FCSTD DOCUMENT  (FreeCAD 0.21R33771 (Git))
Label: Expeditioner Model
License: All rights reserved
LicenseURL: http://en.wikipedia.org/wiki/All_rights_reserved
objects: Part::Feature×562, Sketcher::SketchObject×231, App::Part×178, TechDraw::DrawViewDimension×156, PartDesign::Pocket×103, PartDesign::Fillet×78, Part::Extrusion×48, PartDesign::Body×41, App::MeasureDistance×31, PartDesign::Hole×30, TechDraw::DrawViewBalloon×28, PartDesign::Pad×27, PartDesign::FeatureBase×16, TechDraw::DrawViewAnnotation×14, TechDraw::DrawViewPart×11, Mesh::Feature×7, PartDesign::Chamfer×5, TechDraw::DrawSVGTemplate×5, TechDraw::DrawPage×5, App::FeaturePython×1, +5 more types
note: 1624 computed .brp shape members not serialized (recipe doc carries the construction recipe); baked Part::Feature solids carry a one-line shape summary decoded from their .brp

FEATURE [App::FeaturePython] Marz_Files  # WARN: FeaturePython — macro-defined, semantics opaque (R4)
FEATURE [Sketcher::SketchObject] Sketch  label="blank template"
  FullyConstrained = false
  MapMode = 5
  Support = -> [XY_Plane]
  sketch-geometry (4):
    g0: LineSegment StartX=0 StartY=615 StartZ=0 EndX=450 EndY=615 EndZ=0
    g1: LineSegment StartX=450 StartY=615 StartZ=0 EndX=450 EndY=15 EndZ=0
    g2: LineSegment StartX=450 StartY=15 StartZ=0 EndX=0 EndY=15 EndZ=0
    g3: LineSegment StartX=0 StartY=15 StartZ=0 EndX=0 EndY=615 EndZ=0
  constraints (10):
    c: Coincident(g0,g1)
    c: Coincident(g1,g2)
    c: Coincident(g2,g3)
    c: Coincident(g3,g0)
    c: Horizontal(g0)
    c: Horizontal(g2)
    c: Vertical(g1)
    c: Vertical(g3)
    c: DistanceX(g2,g2) = 450
    c: DistanceY(g1,g1) = 600
FEATURE [Image::ImagePlane] Screenshot_2024_10_02_125832  label="bettie schem"
  Placement = pos=(-143.3,315.1,0) rot=(0,0,1;1.5708rad)
  XSize = 165.652
  YSize = 124.636
FEATURE [Sketcher::SketchObject] Sketch011  label="bettie measurements"
  FullyConstrained = false
  MapMode = 5
  Support = -> [XY_Plane]
  sketch-geometry (52):
    g0: LineSegment StartX=45 StartY=-146.5 StartZ=0 EndX=35.3685 EndY=-167.589 EndZ=0
    g1: LineSegment StartX=35.3685 StartY=-167.589 StartZ=0 EndX=34.2637 EndY=-168.593 EndZ=0
    g2: LineSegment StartX=34.2637 StartY=-168.593 StartZ=0 EndX=33 EndY=-169.396 EndZ=0
    g3: LineSegment StartX=33 StartY=-169.396 StartZ=0 EndX=31.6649 EndY=-169.786 EndZ=0
    g4: LineSegment StartX=31.6649 StartY=-169.786 StartZ=0 EndX=29 EndY=-169.786 EndZ=0
    g5: LineSegment StartX=29 StartY=-169.786 StartZ=0 EndX=1.8 EndY=-159.5 EndZ=0
    g6: LineSegment StartX=1.8 StartY=-159.5 StartZ=0 EndX=-1.2 EndY=-159.5 EndZ=0
    g7: LineSegment StartX=-1.2 StartY=-159.5 StartZ=0 EndX=-69 EndY=-185.428 EndZ=0
    g8: LineSegment StartX=-69 StartY=-185.428 StartZ=0 EndX=-70.8 EndY=-185.428 EndZ=0
    g9: LineSegment StartX=-70.8 StartY=-185.428 StartZ=0 EndX=-71.8 EndY=-184.767 EndZ=0
    g10: LineSegment StartX=-71.8 StartY=-184.767 StartZ=0 EndX=-72.4211 EndY=-184 EndZ=0
    g11: LineSegment StartX=-72.4211 StartY=-184 StartZ=0 EndX=-72.8 EndY=-183.2 EndZ=0
    g12: LineSegment StartX=-72.8 StartY=-183.2 StartZ=0 EndX=-72.8555 EndY=-183 EndZ=0
    g13: LineSegment StartX=-72.8555 StartY=-183 StartZ=0 EndX=-72.8555 EndY=-181.7 EndZ=0
    g14: LineSegment StartX=-72.8555 StartY=-181.7 StartZ=0 EndX=-67.6345 EndY=-163 EndZ=0
    g15: LineSegment StartX=-67.6345 StartY=-163 StartZ=0 EndX=-64.5009 EndY=-153.288 EndZ=0
    g16: LineSegment StartX=-64.5009 StartY=-153.288 StartZ=0 EndX=-61.7538 EndY=-145.228 EndZ=0
    g17: LineSegment StartX=-61.7538 StartY=-145.228 StartZ=0 EndX=-59.2797 EndY=-138.257 EndZ=0
    g18: LineSegment StartX=-59.2797 StartY=-138.257 StartZ=0 EndX=-57.2993 EndY=-133 EndZ=0
    g19: LineSegment StartX=-57.2993 StartY=-133 StartZ=0 EndX=-54.706 EndY=-126.347 EndZ=0
    g20: LineSegment StartX=-54.706 StartY=-126.347 StartZ=0 EndX=-52.2652 EndY=-120.606 EndZ=0
    g21: LineSegment StartX=-52.2652 StartY=-120.606 StartZ=0 EndX=-48.3212 EndY=-111.536 EndZ=0
    g22: LineSegment StartX=-48.3212 StartY=-111.536 StartZ=0 EndX=-45 EndY=-104.429 EndZ=0
    g23: LineSegment StartX=-45 StartY=-104.429 StartZ=0 EndX=-42 EndY=-98 EndZ=0
    g24: LineSegment StartX=-42 StartY=-98 StartZ=0 EndX=-40.3107 EndY=-94.759 EndZ=0
    g25: LineSegment StartX=-40.3107 StartY=-94.759 StartZ=0 EndX=-39.498 EndY=-93.793 EndZ=0
    g26: LineSegment StartX=-39.498 StartY=-93.793 StartZ=0 EndX=-38.7466 EndY=-93.2563 EndZ=0
    g27: LineSegment StartX=-38.7466 StartY=-93.2563 StartZ=0 EndX=-38 EndY=-93 EndZ=0
    g28: LineSegment StartX=-38 StartY=-93 StartZ=0 EndX=-37 EndY=-93 EndZ=0
    g29: LineSegment StartX=-37 StartY=-93 StartZ=0 EndX=-36.528 EndY=-93 EndZ=0
    g30: LineSegment StartX=-36.528 StartY=-93 StartZ=0 EndX=3.99999 EndY=-118.6 EndZ=0
    g31: LineSegment StartX=3.99999 StartY=-118.6 StartZ=0 EndX=4.79999 EndY=-119 EndZ=0
    g32: LineSegment StartX=4.79999 StartY=-119 StartZ=0 EndX=7.79999 EndY=-119 EndZ=0
    g33: LineSegment StartX=7.79999 StartY=-119 StartZ=0 EndX=13.4 EndY=-117.1 EndZ=0
    g34: LineSegment StartX=13.4 StartY=-117.1 StartZ=0 EndX=18 EndY=-115.5 EndZ=0
    g35: LineSegment StartX=18 StartY=-115.5 StartZ=0 EndX=61 EndY=-100.8 EndZ=0
    g36: LineSegment StartX=61 StartY=-100.8 StartZ=0 EndX=62.5 EndY=-100.8 EndZ=0
    g37: LineSegment StartX=62.5 StartY=-100.8 StartZ=0 EndX=63 EndY=-101.2 EndZ=0
    g38: LineSegment StartX=63 StartY=-101.2 StartZ=0 EndX=63.5 EndY=-101.7 EndZ=0
    g39: LineSegment StartX=63.5 StartY=-101.7 StartZ=0 EndX=63.8 EndY=-102.1 EndZ=0
    g40: LineSegment StartX=63.8 StartY=-102.1 StartZ=0 EndX=63.9 EndY=-102.3 EndZ=0
    g41: LineSegment StartX=63.9 StartY=-102.3 StartZ=0 EndX=63.9 EndY=-104 EndZ=0
    g42: LineSegment StartX=63.9 StartY=-104 StartZ=0 EndX=52.7 EndY=-129 EndZ=0
    g43: LineSegment StartX=52.7 StartY=-129 StartZ=0 EndX=52.5574 EndY=-129.3 EndZ=0
    g44: LineSegment StartX=52.5574 StartY=-129.3 StartZ=0 EndX=52.5574 EndY=-130.5 EndZ=0
    g45: LineSegment StartX=52.5574 StartY=-130.5 StartZ=0 EndX=53.4 EndY=-131.7 EndZ=0
    g46: LineSegment StartX=53.4 StartY=-131.7 StartZ=0 EndX=54 EndY=-132 EndZ=0
    g47: LineSegment StartX=54 StartY=-132 StartZ=0 EndX=54 EndY=-146.5 EndZ=0
    g48: LineSegment StartX=54 StartY=-146.5 StartZ=0 EndX=45 EndY=-146.5 EndZ=0
    g49: LineSegment StartX=63.9 StartY=-104 StartZ=0 EndX=63.9 EndY=-129 EndZ=0
    g50: LineSegment StartX=-40.3107 StartY=-94.759 StartZ=0 EndX=-41 EndY=-94 EndZ=0
    g51: LineSegment StartX=-70.8 StartY=-185.428 StartZ=0 EndX=-70.8 EndY=-187 EndZ=0
  constraints (116):
    c: Coincident(g0,g1)
    c: Coincident(g1,g2)
    c: Coincident(g2,g3)
    c: Coincident(g3,g4)
    c: Horizontal(g4)
    c: Coincident(g4,g5)
    c: Coincident(g5,g6)
    c: Horizontal(g6)
    c: Coincident(g6,g7)
    c: Coincident(g7,g8)
    c: Horizontal(g8)
    c: Coincident(g8,g9)
    c: Coincident(g9,g10)
    c: Coincident(g10,g11)
    c: Coincident(g11,g12)
    c: Coincident(g12,g13)
    c: Vertical(g13)
    c: Coincident(g13,g14)
    c: Coincident(g14,g15)
    c: Coincident(g15,g16)
    c: Coincident(g16,g17)
    c: Coincident(g17,g18)
    c: Coincident(g18,g19)
    c: Coincident(g19,g20)
    c: Coincident(g20,g21)
    c: Coincident(g21,g22)
    c: Coincident(g22,g23)
    c: Coincident(g23,g24)
    c: Coincident(g24,g25)
    c: Coincident(g25,g26)
    c: Coincident(g26,g27)
    c: Coincident(g27,g28)
    c: Horizontal(g28)
    c: Coincident(g28,g29)
    c: Horizontal(g29)
    c: Coincident(g29,g30)
    c: Coincident(g30,g31)
    c: Coincident(g31,g32)
    c: Horizontal(g32)
    c: Coincident(g32,g33)
    c: Coincident(g33,g34)
    c: Coincident(g34,g35)
    c: Coincident(g35,g36)
    c: Horizontal(g36)
    c: Coincident(g36,g37)
    c: Coincident(g37,g38)
    c: Coincident(g38,g39)
    c: Coincident(g39,g40)
    c: Coincident(g40,g41)
    c: Vertical(g41)
    c: Coincident(g41,g42)
    c: Coincident(g42,g43)
    c: Coincident(g43,g44)
    c: Vertical(g44)
    c: Coincident(g44,g45)
    c: Coincident(g45,g46)
    c: Coincident(g46,g47)
    c: Vertical(g47)
    c: Coincident(g47,g48)
    c: Coincident(g48,g0)
    c: Horizontal(g48)
    c: Distance(g0) = 23.184
    c: Distance(g42) = 27.3942
    c: Distance(g43) = 0.33218
    c: Distance(g44) = 1.2
    c: Distance(g45) = 1.4663
    c: Distance(g46) = 0.67082
    c: Distance(g47) = 14.5
    c: Distance(g48) = 9
    c: Distance(g1) = 1.49309
    c: Distance(g2) = 1.49749
    c: Distance(g3) = 1.39068
    c: Distance(g4) = 2.6649
    c: Distance(g5) = 29.0798
    c: Distance(g6) = 3
    c: Distance(g7) = 72.5885
    c: Distance(g8) = 1.8
    c: Distance(g9) = 1.19864
    c: Distance(g10) = 0.98682
    c: Distance(g11) = 0.88518
    c: Distance(g12) = 0.20755
    c: Distance(g13) = 1.3
    c: Distance(g14) = 19.4152
    c: Distance(g15) = 10.2052
    c: Distance(g16) = 8.51506
    c: Distance(g17) = 7.39698
    c: Distance(g18) = 5.61771
    c: Distance(g19) = 7.14023
    c: Distance(g20) = 6.23864
    c: Distance(g21) = 9.89066
    c: Distance(g22) = 7.84408
    c: Distance(g23) = 7.09491
    c: Distance(g24) = 3.65484
    c: Distance(g25) = 1.26244
    c: Distance(g26) = 0.92337
    c: Distance(g27) = 0.78933
    c: Distance(g28) = 1
    c: Distance(g29) = 0.47203
    c: Distance(g30) = 47.9362
    c: Distance(g31) = 0.89443
    c: Distance(g32) = 3
    c: Distance(g33) = 5.91354
    c: Distance(g34) = 4.87032
    c: Distance(g35) = 45.4433
    c: Distance(g36) = 1.50001
    c: Distance(g37) = 0.64031
    c: Distance(g38) = 0.70711
    c: Distance(g39) = 0.5
    c: Distance(g40) = 0.22361
    c: Distance(g41) = 1.7
    c: Coincident(g49,g41)
    c: Vertical(g49)
    c: Coincident(g50,g24)
    c: Coincident(g51,g8)
    c: Vertical(g51)
    c: Angle(g8,g9) = 2.55763
FEATURE [PartDesign::Pad] Pad
  Direction = (0,0,1)
  Length = 45
  Length2 = 10
  Profile = -> Sketch
  ReferenceAxis = -> Sketch [N_Axis]
  Type = 0
FEATURE [Sketcher::SketchObject] Sketch002  label="pickup holes"
  FullyConstrained = false
  MapMode = 5
  Placement = pos=(0,0,45) rot=(0,0,1;0rad)
  Support = -> [Pad]
  sketch-geometry (28):
    g0: LineSegment StartX=225 StartY=601 StartZ=0 EndX=225 EndY=-1 EndZ=0
    g1: LineSegment StartX=182.5 StartY=460 StartZ=0 EndX=267.5 EndY=460 EndZ=0
    g2: LineSegment StartX=267.5 StartY=460 StartZ=0 EndX=267.5 EndY=441 EndZ=0
    g3: LineSegment StartX=267.5 StartY=441 StartZ=0 EndX=182.5 EndY=441 EndZ=0
    g4: LineSegment StartX=182.5 StartY=441 StartZ=0 EndX=182.5 EndY=460 EndZ=0
    g5: LineSegment StartX=182.5 StartY=400 StartZ=0 EndX=267.5 EndY=400 EndZ=0
    g6: LineSegment StartX=267.5 StartY=400 StartZ=0 EndX=267.5 EndY=381 EndZ=0
    g7: LineSegment StartX=267.5 StartY=381 StartZ=0 EndX=182.5 EndY=381 EndZ=0
    g8: LineSegment StartX=182.5 StartY=381 StartZ=0 EndX=182.5 EndY=400 EndZ=0
    g9: LineSegment StartX=188.75 StartY=357.8 StartZ=0 EndX=261.25 EndY=357.8 EndZ=0
    g10: LineSegment StartX=261.25 StartY=357.8 StartZ=0 EndX=261.25 EndY=347.8 EndZ=0
    g11: LineSegment StartX=261.25 StartY=347.8 StartZ=0 EndX=269.25 EndY=347.8 EndZ=0
    g12: LineSegment StartX=269.25 StartY=347.8 StartZ=0 EndX=269.25 EndY=327.8 EndZ=0
    g13: LineSegment StartX=269.25 StartY=327.8 StartZ=0 EndX=261.25 EndY=327.8 EndZ=0
    g14: LineSegment StartX=261.25 StartY=327.8 StartZ=0 EndX=261.25 EndY=317.8 EndZ=0
    g15: LineSegment StartX=261.25 StartY=317.8 StartZ=0 EndX=188.75 EndY=317.8 EndZ=0
    g16: LineSegment StartX=188.75 StartY=317.8 StartZ=0 EndX=188.75 EndY=327.8 EndZ=0
    g17: LineSegment StartX=188.75 StartY=327.8 StartZ=0 EndX=180.75 EndY=327.8 EndZ=0
    g18: LineSegment StartX=180.75 StartY=327.8 StartZ=0 EndX=180.75 EndY=347.8 EndZ=0
    g19: LineSegment StartX=180.75 StartY=347.8 StartZ=0 EndX=188.75 EndY=347.8 EndZ=0
    g20: LineSegment StartX=188.75 StartY=347.8 StartZ=0 EndX=188.75 EndY=357.8 EndZ=0
    g21: LineSegment StartX=182.5 StartY=460 StartZ=0 EndX=182.5 EndY=469.3 EndZ=0
    g22: LineSegment StartX=182.5 StartY=469.3 StartZ=0 EndX=210 EndY=469.3 EndZ=0
    g23: LineSegment StartX=182.5 StartY=441 StartZ=0 EndX=182.5 EndY=400 EndZ=0
    g24: LineSegment StartX=177 StartY=469.3 StartZ=0 EndX=177 EndY=357.8 EndZ=0
    g25: LineSegment StartX=177 StartY=357.8 StartZ=0 EndX=180.75 EndY=357.8 EndZ=0
    g26: LineSegment StartX=180.75 StartY=357.8 StartZ=0 EndX=188.75 EndY=357.8 EndZ=0
    g27: LineSegment StartX=261.25 StartY=357.8 StartZ=0 EndX=261.25 EndY=381 EndZ=0
  constraints (76):
    c: Vertical(g0)
    c: Coincident(g1,g2)
    c: Coincident(g2,g3)
    c: Coincident(g3,g4)
    c: Coincident(g4,g1)
    c: Horizontal(g1)
    c: Horizontal(g3)
    c: Vertical(g2)
    c: Vertical(g4)
    c: DistanceX(g1,g1) = 85
    c: DistanceY(g2,g2) = 19
    c: Coincident(g5,g6)
    c: Coincident(g6,g7)
    c: Coincident(g7,g8)
    c: Coincident(g8,g5)
    c: Horizontal(g5)
    c: Horizontal(g7)
    c: Vertical(g6)
    c: Vertical(g8)
    c: DistanceX(g5,g5) = 85
    c: DistanceY(g8,g8) = 19
    c: Horizontal(g9)
    c: Coincident(g9,g10)
    c: Vertical(g10)
    c: Coincident(g10,g11)
    c: Horizontal(g11)
    c: Coincident(g11,g12)
    c: Vertical(g12)
    c: Coincident(g12,g13)
    c: Horizontal(g13)
    c: Coincident(g13,g14)
    c: Vertical(g14)
    c: Coincident(g14,g15)
    c: Horizontal(g15)
    c: Coincident(g15,g16)
    c: Vertical(g16)
    c: Coincident(g16,g17)
    c: Horizontal(g17)
    c: Coincident(g17,g18)
    c: Vertical(g18)
    c: Coincident(g18,g19)
    c: Horizontal(g19)
    c: Coincident(g19,g20)
    c: Coincident(g20,g9)
    c: Vertical(g20)
    c: DistanceX(g9,g9) = 72.5
    c: DistanceY(g12,g12) = 20
    c: DistanceY(g10,g10) = 10
    c: DistanceY(g14,g14) = 10
    c: DistanceX(g19,g19) = 8
    c: DistanceX(g17,g17) = 8
    c: DistanceX(g13,g13) = 8
    c: DistanceY(g20,g20) = 10
    c: DistanceY(g16,g16) = 10
    c: DistanceX(g15,g15) = 72.5
    c: Coincident(g21,g1)
    c: Vertical(g21)
    c: DistanceY(g21,g21) = 9.3
    c: Coincident(g22,g21)
    c: Horizontal(g22)
    c: Coincident(g23,g3)
    c: Vertical(g23)
    c: DistanceY(g23,g23) = 41
    c: Vertical(g24)
    c: Coincident(g25,g24)
    c: Horizontal(g25)
    c: DistanceY(g24,g24) = 111.5
    c: Coincident(g26,g25)
    c: Coincident(g26,g9)
    c: Horizontal(g26)
    c: DistanceX(g26,g26) = 8
    c: DistanceX(g25,g25) = 3.74999
    c: Coincident(g27,g9)
    c: PointOnObject(g27,g7)
    c: Vertical(g27)
    c: DistanceY(g27,g27) = 23.2
FEATURE [Sketcher::SketchObject] Sketch003  label="tremelo pocket"
  FullyConstrained = false
  MapMode = 5
  Placement = pos=(0,0,45) rot=(0,0,1;0rad)
  Support = -> [Pad]
  sketch-geometry (11):
    g0: LineSegment StartX=225 StartY=610 StartZ=0 EndX=225 EndY=-10 EndZ=0
    g1: LineSegment StartX=182.5 StartY=460 StartZ=0 EndX=182.5 EndY=469.3 EndZ=0
    g2: LineSegment StartX=182.5 StartY=469.3 StartZ=0 EndX=182.5 EndY=481.3 EndZ=0
    g3: LineSegment StartX=178 StartY=481.3 StartZ=0 EndX=178 EndY=295.3 EndZ=0
    g4: LineSegment StartX=178 StartY=295.3 StartZ=0 EndX=178 EndY=282.3 EndZ=0
    g5: LineSegment StartX=224.9 StartY=282.4 StartZ=0 EndX=224.99 EndY=282.4 EndZ=0
    g6: LineSegment StartX=224.9 StartY=282.4 StartZ=0 EndX=189.9 EndY=282.4 EndZ=0
    g7: LineSegment StartX=189.9 StartY=282.3 StartZ=0 EndX=267.9 EndY=282.3 EndZ=0
    g8: LineSegment StartX=267.9 StartY=282.3 StartZ=0 EndX=267.9 EndY=263.3 EndZ=0
    g9: LineSegment StartX=267.9 StartY=263.3 StartZ=0 EndX=189.9 EndY=263.3 EndZ=0
    g10: LineSegment StartX=189.9 StartY=263.3 StartZ=0 EndX=189.9 EndY=282.3 EndZ=0
  constraints (26):
    c: Vertical(g0)
    c: Vertical(g1)
    c: Coincident(g2,g1)
    c: Vertical(g2)
    c: Vertical(g3)
    c: Coincident(g4,g3)
    c: Vertical(g4)
    c: DistanceY(g4,g4) = 13
    c: DistanceY(g3,g3) = 186
    c: DistanceY(g1,g1) = 9.3
    c: DistanceY(g2,g2) = 12
    c: Horizontal(g5)
    c: Coincident(g6,g5)
    c: Horizontal(g6)
    c: DistanceX(g6,g6) = 35
    c: DistanceX(g5,g5) = 0.08999
    c: Coincident(g7,g8)
    c: Coincident(g8,g9)
    c: Coincident(g9,g10)
    c: Coincident(g10,g7)
    c: Horizontal(g7)
    c: Horizontal(g9)
    c: Vertical(g8)
    c: Vertical(g10)
    c: DistanceX(g7,g7) = 78
    c: DistanceY(g10,g10) = 19
FEATURE [Sketcher::SketchObject] Sketch004  label="control pocket"
  FullyConstrained = false
  MapMode = 5
  Placement = pos=(0,0,45) rot=(0,0,1;0rad)
  Support = -> [Pad]
  sketch-geometry (11):
    g0: LineSegment StartX=330 StartY=250 StartZ=0 EndX=353.532 EndY=180 EndZ=0
    g1: LineSegment StartX=353.532 StartY=180 StartZ=0 EndX=290 EndY=180 EndZ=0
    g2: LineSegment StartX=290 StartY=180 StartZ=0 EndX=290 EndY=250 EndZ=0
    g3: LineSegment StartX=330 StartY=250 StartZ=0 EndX=290 EndY=250 EndZ=0
    g4: Circle CenterX=302 CenterY=230 CenterZ=0 NormalX=0 NormalY=0 NormalZ=1 AngleXU=0 Radius=8.5
    g5: Circle CenterX=302 CenterY=200 CenterZ=0 NormalX=0 NormalY=0 NormalZ=1 AngleXU=0 Radius=8.5
    g6: LineSegment StartX=316.216 StartY=240.298 StartZ=0 EndX=326.216 EndY=240.298 EndZ=0
    g7: LineSegment StartX=326.216 StartY=240.298 StartZ=0 EndX=341.048 EndY=194.647 EndZ=0
    g8: LineSegment StartX=341.048 StartY=194.647 StartZ=0 EndX=330.587 EndY=191.248 EndZ=0
    g9: LineSegment StartX=326.216 StartY=240.298 StartZ=0 EndX=315.754 EndY=236.898 EndZ=0
    g10: LineSegment StartX=315.754 StartY=236.898 StartZ=0 EndX=330.587 EndY=191.248 EndZ=0
  constraints (25):
    c: Coincident(g1,g0)
    c: Horizontal(g1)
    c: Coincident(g2,g1)
    c: Vertical(g2)
    c: Coincident(g3,g0)
    c: Coincident(g3,g2)
    c: Horizontal(g3)
    c: Distance(g0) = 73.8495
    c: DistanceX(g3,g3) = 40
    c: DistanceX(g1,g1) = 63.5319
    c: Diameter(g4) = 17
    c: Diameter(g5) = 17
    c: Horizontal(g6)
    c: Coincident(g7,g6)
    c: DistanceX(g6,g6) = 10
    c: Angle(g6,g7) = 1.88496
    c: Distance(g7) = 48
    c: Coincident(g8,g7)
    c: Angle(g7,g8) = 1.5708
    c: Distance(g8) = 11
    c: Coincident(g9,g7)
    c: Angle(g9,g7) = 1.5708
    c: Coincident(g10,g9)
    c: Coincident(g10,g8)
    c: Distance(g9) = 11
FEATURE [Sketcher::SketchObject] Sketch005  label="AFPI pocket"
  FullyConstrained = false
  MapMode = 5
  Placement = pos=(0,0,45) rot=(0,0,1;0rad)
  Support = -> [Pad]
  sketch-geometry (24):
    g0: LineSegment StartX=68 StartY=506.5 StartZ=0 EndX=160 EndY=506.5 EndZ=0
    g1: LineSegment StartX=160 StartY=506.5 StartZ=0 EndX=160 EndY=402.5 EndZ=0
    g2: LineSegment StartX=160 StartY=402.5 StartZ=0 EndX=68 EndY=402.5 EndZ=0
    g3: LineSegment StartX=68 StartY=402.5 StartZ=0 EndX=68 EndY=506.5 EndZ=0
    g4: LineSegment StartX=-192.181 StartY=581.522 StartZ=0 EndX=-181.31 EndY=478.092 EndZ=0
    g5: LineSegment StartX=-181.31 StartY=478.092 StartZ=0 EndX=-89.8139 EndY=487.709 EndZ=0
    g6: LineSegment StartX=-192.181 StartY=581.522 StartZ=0 EndX=-100.685 EndY=591.139 EndZ=0
    g7: LineSegment StartX=-100.685 StartY=591.139 StartZ=0 EndX=-89.8139 EndY=487.709 EndZ=0
    g8: LineSegment StartX=-192.181 StartY=581.522 StartZ=0 EndX=-192.181 EndY=481.522 EndZ=0
    g9: LineSegment StartX=175 StartY=400 StartZ=0 EndX=275 EndY=400 EndZ=0
    g10: LineSegment StartX=175 StartY=400 StartZ=0 EndX=175 EndY=490 EndZ=0
    g11: LineSegment StartX=175 StartY=400 StartZ=0 EndX=175 EndY=380 EndZ=0
    g12: LineSegment StartX=-89.8139 StartY=487.709 StartZ=0 EndX=-88.927 EndY=479.201 EndZ=0
    g13: LineSegment StartX=-181.31 StartY=478.092 StartZ=0 EndX=-180.433 EndY=469.628 EndZ=0
    g14: LineSegment StartX=-180.433 StartY=469.628 StartZ=0 EndX=-88.927 EndY=479.201 EndZ=0
    g15: LineSegment StartX=-192.181 StartY=581.522 StartZ=0 EndX=-193.082 EndY=590 EndZ=0
    g16: LineSegment StartX=-100.685 StartY=591.139 StartZ=0 EndX=-101.58 EndY=599.597 EndZ=0
    g17: LineSegment StartX=-101.58 StartY=599.597 StartZ=0 EndX=-193.082 EndY=590 EndZ=0
    g18: LineSegment StartX=68 StartY=506.5 StartZ=0 EndX=68 EndY=515 EndZ=0
    g19: LineSegment StartX=68 StartY=515 StartZ=0 EndX=160 EndY=515 EndZ=0
    g20: LineSegment StartX=160 StartY=515 StartZ=0 EndX=160 EndY=506.5 EndZ=0
    g21: LineSegment StartX=160 StartY=402.5 StartZ=0 EndX=160 EndY=393.9 EndZ=0
    g22: LineSegment StartX=160 StartY=393.9 StartZ=0 EndX=68 EndY=393.9 EndZ=0
    g23: LineSegment StartX=68 StartY=393.9 StartZ=0 EndX=68 EndY=402.5 EndZ=0
  constraints (60):
    c: Coincident(g0,g1)
    c: Coincident(g1,g2)
    c: Coincident(g2,g3)
    c: Coincident(g3,g0)
    c: Horizontal(g0)
    c: Horizontal(g2)
    c: Vertical(g1)
    c: Vertical(g3)
    c: DistanceY(g1,g1) = 104
    c: DistanceX(g0,g0) = 92
    c: Coincident(g4,g5)
    c: Coincident(g4,g6)
    c: Coincident(g6,g7)
    c: Coincident(g7,g5)
    c: Angle(g7,g5) = 1.5708
    c: Angle(g6,g7) = 1.5708
    c: Angle(g4,g6) = 1.5708
    c: Distance(g4) = 104
    c: Distance(g5) = 92
    c: Coincident(g8,g4)
    c: Vertical(g8)
    c: Angle(g8,g4) = 0.10472
    c: DistanceY(g8,g8) = 100
    c: Horizontal(g9)
    c: Coincident(g10,g9)
    c: Vertical(g10)
    c: Coincident(g11,g9)
    c: Vertical(g11)
    c: Coincident(g5,g12)
    c: Coincident(g4,g13)
    c: Coincident(g13,g14)
    c: Coincident(g14,g12)
    c: Distance(g12) = 8.5541
    c: Distance(g14) = 92.0049
    c: Distance(g13) = 8.50942
    c: Coincident(g4,g15)
    c: Coincident(g16,g6)
    c: Coincident(g17,g16)
    c: Coincident(g17,g15)
    c: Distance(g15) = 8.52543
    c: Distance(g17) = 92.0046
    c: Distance(g16) = 8.50507
    c: Angle(g17,g16) = 1.57171
    c: Angle(g12,g14) = 1.57116
    c: Coincident(g0,g18)
    c: Vertical(g18)
    c: Coincident(g18,g19)
    c: Horizontal(g19)
    c: Coincident(g19,g20)
    c: Coincident(g20,g0)
    c: Vertical(g20)
    c: Coincident(g1,g21)
    c: Vertical(g21)
    c: Coincident(g21,g22)
    c: Horizontal(g22)
    c: Coincident(g22,g23)
    c: Coincident(g23,g2)
    c: Vertical(g23)
    c: DistanceY(g23,g23) = 8.59999
    c: DistanceY(g18,g18) = 8.50001
FEATURE [Sketcher::SketchObject] Sketch007  label="RGB Board Pockets"
  FullyConstrained = false
  MapMode = 5
  Placement = pos=(0,0,45) rot=(0,0,1;0rad)
  Support = -> [Pad]
  sketch-geometry (12):
    g0: LineSegment StartX=220 StartY=282.3 StartZ=0 EndX=220 EndY=284.3 EndZ=0
    g1: LineSegment StartX=220 StartY=284.3 StartZ=0 EndX=220 EndY=382.3 EndZ=0
    g2: LineSegment StartX=183 StartY=427.9 StartZ=0 EndX=267 EndY=427.9 EndZ=0
    g3: LineSegment StartX=267 StartY=427.9 StartZ=0 EndX=267 EndY=412.9 EndZ=0
    g4: LineSegment StartX=267 StartY=412.9 StartZ=0 EndX=183 EndY=412.9 EndZ=0
    g5: LineSegment StartX=183 StartY=412.9 StartZ=0 EndX=183 EndY=427.9 EndZ=0
    g6: LineSegment StartX=182.5 StartY=460 StartZ=0 EndX=225 EndY=460 EndZ=0
    g7: LineSegment StartX=225 StartY=460 StartZ=0 EndX=225 EndY=244 EndZ=0
    g8: LineSegment StartX=267.5 StartY=441 StartZ=0 EndX=267.5 EndY=400 EndZ=0
    g9: LineSegment StartX=267 StartY=441 StartZ=0 EndX=267 EndY=420.4 EndZ=0
    g10: LineSegment StartX=263.999 StartY=441 StartZ=0 EndX=263.999 EndY=427.9 EndZ=0
    g11: LineSegment StartX=210 StartY=282.3 StartZ=0 EndX=210 EndY=302.3 EndZ=0
  constraints (21):
    c: Vertical(g0)
    c: Coincident(g1,g0)
    c: Vertical(g1)
    c: Coincident(g2,g3)
    c: Coincident(g3,g4)
    c: Coincident(g4,g5)
    c: Coincident(g5,g2)
    c: Horizontal(g2)
    c: Horizontal(g4)
    c: Vertical(g3)
    c: Vertical(g5)
    c: DistanceX(g2,g2) = 84
    c: DistanceY(g5,g5) = 15
    c: Horizontal(g6)
    c: Coincident(g7,g6)
    c: Vertical(g7)
    c: Vertical(g8)
    c: Vertical(g9)
    c: PointOnObject(g10,g2)
    c: Vertical(g10)
    c: Vertical(g11)
FEATURE [Sketcher::SketchObject] Sketch008  label="Speaker hole"
  FullyConstrained = false
  MapMode = 5
  Placement = pos=(0,0,45) rot=(0,0,1;0rad)
  Support = -> [Pad]
  sketch-geometry (3):
    g0: Circle CenterX=330 CenterY=121 CenterZ=0 NormalX=0 NormalY=0 NormalZ=1 AngleXU=0 Radius=37
    g1: LineSegment StartX=377 StartY=123.392 StartZ=0 EndX=283 EndY=123.392 EndZ=0
    g2: LineSegment StartX=377 StartY=123.4 StartZ=0 EndX=330 EndY=123.4 EndZ=0
  constraints (4):
    c: Diameter(g0) = 74
    c: Horizontal(g1)
    c: DistanceX(g1,g1) = 94
    c: Horizontal(g2)
FEATURE [Sketcher::SketchObject] Sketch009  label="control plate mount pocket"
  FullyConstrained = false
  MapMode = 5
  Placement = pos=(0,0,45) rot=(0,0,1;0rad)
  Support = -> [Pad]
  sketch-geometry (6):
    g0: LineSegment StartX=267.9 StartY=263.3 StartZ=0 EndX=267.9 EndY=243.3 EndZ=0
    g1: LineSegment StartX=267.9 StartY=243.3 StartZ=0 EndX=272.9 EndY=243.3 EndZ=0
    g2: LineSegment StartX=282 StartY=258 StartZ=0 EndX=337 EndY=258 EndZ=0
    g3: LineSegment StartX=282 StartY=258 StartZ=0 EndX=282 EndY=172 EndZ=0
    g4: LineSegment StartX=282 StartY=172 StartZ=0 EndX=365.925 EndY=172 EndZ=0
    g5: LineSegment StartX=365.925 StartY=172 StartZ=0 EndX=337 EndY=258 EndZ=0
  constraints (12):
    c: Vertical(g0)
    c: Coincident(g1,g0)
    c: Horizontal(g1)
    c: Horizontal(g2)
    c: Coincident(g3,g2)
    c: Vertical(g3)
    c: DistanceY(g3,g3) = 86
    c: Coincident(g4,g3)
    c: Horizontal(g4)
    c: Coincident(g5,g4)
    c: Coincident(g5,g2)
    c: Distance(g5) = 90.7339
FEATURE [Sketcher::SketchObject] Sketch001  label="Body Outline"
  FullyConstrained = false
  MapMode = 5
  Placement = pos=(0,0,45) rot=(0,0,1;0rad)
  Support = -> [Pad]
  sketch-geometry (66):
    g0: LineSegment StartX=0 StartY=610.061 StartZ=0 EndX=225 EndY=610.061 EndZ=0
    g1: LineSegment StartX=225 StartY=610.061 StartZ=0 EndX=225 EndY=-10 EndZ=0
    g2: LineSegment StartX=196 StartY=469.3 StartZ=0 EndX=196 EndY=495.3 EndZ=0
    g3: LineSegment StartX=197.29 StartY=495.3 StartZ=0 EndX=73.9 EndY=550.1 EndZ=0
    g4: LineSegment StartX=252.163 StartY=545.479 StartZ=0 EndX=252.549 EndY=509.479 EndZ=0
    g5: LineSegment StartX=252.549 StartY=509.479 StartZ=0 EndX=336.625 EndY=471.135 EndZ=0
    g6: LineSegment StartX=336.625 StartY=471.135 StartZ=0 EndX=340.409 EndY=466.998 EndZ=0
    g7: LineSegment StartX=340.409 StartY=466.998 StartZ=0 EndX=343.206 EndY=462.496 EndZ=0
    g8: LineSegment StartX=343.206 StartY=462.496 StartZ=0 EndX=343.206 EndY=452.096 EndZ=0
    g9: LineSegment StartX=343.206 StartY=452.096 StartZ=0 EndX=301.899 EndY=343.599 EndZ=0
    g10: LineSegment StartX=301.899 StartY=343.599 StartZ=0 EndX=301.899 EndY=331.599 EndZ=0
    g11: LineSegment StartX=405.404 StartY=60.6684 StartZ=0 EndX=405.404 EndY=53.4684 EndZ=0
    g12: LineSegment StartX=195.595 StartY=533.229 StartZ=0 EndX=190.6 EndY=530.763 EndZ=0
    g13: LineSegment StartX=190.6 StartY=530.763 StartZ=0 EndX=185.73 EndY=530.763 EndZ=0
    g14: LineSegment StartX=185.73 StartY=530.763 StartZ=0 EndX=184.498 EndY=530.891 EndZ=0
    g15: LineSegment StartX=184.498 StartY=530.891 StartZ=0 EndX=97.9951 EndY=587.067 EndZ=0
    g16: LineSegment StartX=198.214 StartY=509.5 StartZ=0 EndX=198.014 EndY=509.5 EndZ=0
    g17: LineSegment StartX=97.9951 StartY=587.067 StartZ=0 EndX=91.1434 EndY=587.067 EndZ=0
    g18: LineSegment StartX=91.1434 StartY=587.067 StartZ=0 EndX=89.4834 EndY=585.824 EndZ=0
    g19: LineSegment StartX=89.4834 StartY=585.824 StartZ=0 EndX=87.4934 EndY=583.854 EndZ=0
    g20: LineSegment StartX=87.4934 StartY=583.854 StartZ=0 EndX=85.9834 EndY=581.974 EndZ=0
    g21: LineSegment StartX=107.659 StartY=357.048 StartZ=0 EndX=122.894 EndY=344.497 EndZ=0
    g22: LineSegment StartX=122.894 StartY=344.497 StartZ=0 EndX=130.394 EndY=322.397 EndZ=0
    g23: LineSegment StartX=130.394 StartY=322.397 StartZ=0 EndX=130.394 EndY=310.397 EndZ=0
    g24: LineSegment StartX=130.394 StartY=310.397 StartZ=0 EndX=128.394 EndY=307.697 EndZ=0
    g25: LineSegment StartX=128.394 StartY=307.697 StartZ=0 EndX=44.2001 EndY=150.2 EndZ=0
    g26: LineSegment StartX=44.2001 StartY=150.2 StartZ=0 EndX=44.2001 EndY=148.6 EndZ=0
    g27: LineSegment StartX=44.2001 StartY=148.6 StartZ=0 EndX=44.2001 EndY=144.6 EndZ=0
    g28: LineSegment StartX=44.2001 StartY=144.6 StartZ=0 EndX=45.1101 EndY=141.95 EndZ=0
    g29: LineSegment StartX=45.1101 StartY=141.95 StartZ=0 EndX=47.2241 EndY=138.987 EndZ=0
    g30: LineSegment StartX=47.2241 StartY=138.987 StartZ=0 EndX=50.9701 EndY=135.84 EndZ=0
    g31: LineSegment StartX=405.404 StartY=53.4684 StartZ=0 EndX=402.904 EndY=49.7684 EndZ=0
    g32: LineSegment StartX=402.904 StartY=49.7684 StartZ=0 EndX=400.778 EndY=46.5378 EndZ=0
    g33: LineSegment StartX=400.778 StartY=46.5378 StartZ=0 EndX=395.404 EndY=46.5378 EndZ=0
    g34: LineSegment StartX=301.899 StartY=331.599 StartZ=0 EndX=405.5 EndY=60.6996 EndZ=0
    g35: LineSegment StartX=395.404 StartY=46.5378 StartZ=0 EndX=320.445 EndY=66.6105 EndZ=0
    g36: LineSegment StartX=320.445 StartY=66.6105 StartZ=0 EndX=282.02 EndY=79.0879 EndZ=0
    g37: LineSegment StartX=88.8 StartY=549.8 StartZ=0 EndX=397 EndY=549.8 EndZ=0
    g38: LineSegment StartX=320.445 StartY=66.6105 StartZ=0 EndX=290 EndY=70 EndZ=0
    g39: LineSegment StartX=290 StartY=70 StartZ=0 EndX=160 EndY=70 EndZ=0
    g40: LineSegment StartX=160 StartY=70 StartZ=0 EndX=50.9701 EndY=135.84 EndZ=0
    g41: LineSegment StartX=252.163 StartY=545.479 StartZ=0 EndX=197.847 EndY=545.479 EndZ=0
    g42: LineSegment StartX=197.847 StartY=545.479 StartZ=0 EndX=197.725 EndY=534.5 EndZ=0
    g43: LineSegment StartX=197.725 StartY=534.5 StartZ=0 EndX=195.595 EndY=533.229 EndZ=0
    g44: LineSegment StartX=88.8 StartY=549.8 StartZ=0 EndX=0 EndY=549.8 EndZ=0
    g45: LineSegment StartX=400.79 StartY=46.5378 StartZ=0 EndX=400.79 EndY=580 EndZ=0
    g46: LineSegment StartX=400.79 StartY=580 StartZ=0 EndX=-10 EndY=580 EndZ=0
    g47: LineSegment StartX=400.76 StartY=46.5378 StartZ=0 EndX=400.7 EndY=594.6 EndZ=0
    g48: LineSegment StartX=107.659 StartY=357.048 StartZ=0 EndX=96.1282 EndY=362.119 EndZ=0
    g49: LineSegment StartX=68 StartY=394 StartZ=0 EndX=68 EndY=379 EndZ=0
    g50: LineSegment StartX=68 StartY=379 StartZ=0 EndX=160 EndY=379 EndZ=0
    g51: LineSegment StartX=68 StartY=379 StartZ=0 EndX=53 EndY=379 EndZ=0
    g52: LineSegment StartX=53 StartY=379 StartZ=0 EndX=53 EndY=530 EndZ=0
    g53: LineSegment StartX=53 StartY=530 StartZ=0 EndX=159.753 EndY=530 EndZ=0
    g54: LineSegment StartX=159.753 StartY=530 StartZ=0 EndX=159.753 EndY=515 EndZ=0
    g55: LineSegment StartX=96.1282 StartY=362.119 StartZ=0 EndX=64 EndY=377 EndZ=0
    g56: LineSegment StartX=64 StartY=377 StartZ=0 EndX=61 EndY=378.8 EndZ=0
    g57: LineSegment StartX=61 StartY=378.8 StartZ=0 EndX=56.5 EndY=383.7 EndZ=0
    g58: LineSegment StartX=56.5 StartY=383.7 StartZ=0 EndX=54 EndY=388 EndZ=0
    g59: LineSegment StartX=54 StartY=388 StartZ=0 EndX=52.6 EndY=392 EndZ=0
    g60: LineSegment StartX=52.6 StartY=392 StartZ=0 EndX=52.6 EndY=529.8 EndZ=0
    g61: LineSegment StartX=52.6 StartY=529.8 StartZ=0 EndX=54 EndY=534 EndZ=0
    g62: LineSegment StartX=54 StartY=534 StartZ=0 EndX=57 EndY=538 EndZ=0
    g63: LineSegment StartX=57 StartY=538 StartZ=0 EndX=85.9834 EndY=581.974 EndZ=0
    g64: LineSegment StartX=44.2 StartY=150.3 StartZ=0 EndX=44 EndY=600 EndZ=0
    g65: LineSegment StartX=252.549 StartY=509.479 StartZ=0 EndX=197.725 EndY=534.501 EndZ=0
  constraints (165):
    c: PointOnObject(g0,g-2)
    c: Horizontal(g0)
    c: Coincident(g1,g0)
    c: Vertical(g1)
    c: DistanceX(g0,g0) = 225
    c: Vertical(g2)
    c: Coincident(g4,g5)
    c: Coincident(g5,g6)
    c: Coincident(g6,g7)
    c: Coincident(g7,g8)
    c: Vertical(g8)
    c: Coincident(g9,g8)
    c: Coincident(g10,g9)
    c: Vertical(g10)
    c: Vertical(g11)
    c: Coincident(g12,g13)
    c: Horizontal(g13)
    c: Coincident(g13,g14)
    c: Coincident(g14,g15)
    c: Distance(g14) = 1.23908
    c: Distance(g12) = 5.57001
    c: Horizontal(g16)
    c: DistanceX(g13,g13) = 4.86999
    c: Coincident(g17,g15)
    c: Horizontal(g17)
    c: Coincident(g18,g17)
    c: Coincident(g18,g19)
    c: Coincident(g19,g20)
    c: Coincident(g21,g22)
    c: Coincident(g22,g23)
    c: Vertical(g23)
    c: Coincident(g24,g23)
    c: Coincident(g25,g24)
    c: Coincident(g26,g25)
    c: Vertical(g26)
    c: Coincident(g26,g27)
    c: Vertical(g27)
    c: Coincident(g27,g28)
    c: Coincident(g28,g29)
    c: Coincident(g29,g30)
    c: Coincident(g31,g11)
    c: Coincident(g32,g31)
    c: Coincident(g33,g32)
    c: Horizontal(g33)
    c: DistanceX(g33,g33) = 5.37372
    c: DistanceY(g11,g11) = 7.20001
    c: Distance(g31) = 4.46542
    c: Distance(g32) = 3.86749
    c: Coincident(g34,g10)
    c: Angle(g11,g31) = 2.54738
    c: Angle(g11,g32) = 2.55948
    c: Coincident(g35,g33)
    c: Distance(g34) = 290.034
    c: Distance(g9) = 116.095
    c: DistanceY(g10,g10) = 12
    c: DistanceY(g8,g8) = 10.4
    c: Distance(g7) = 5.3
    c: Distance(g6) = 5.60673
    c: Distance(g5) = 92.4066
    c: Distance(g4) = 36.0023
    c: Distance(g20) = 2.41133
    c: Distance(g19) = 2.80018
    c: Distance(g18) = 2.07357
    c: DistanceX(g17,g17) = 6.85172
    c: Distance(g21) = 19.7388
    c: Distance(g22) = 23.3379
    c: DistanceY(g23,g23) = 12
    c: Distance(g24) = 3.36006
    c: DistanceY(g26,g26) = 1.6
    c: DistanceY(g27,g27) = 4
    c: Distance(g28) = 2.8019
    c: Distance(g29) = 3.63982
    c: Distance(g30) = 4.89246
    c: Angle(g28,g27) = 2.81082
    c: Angle(g29,g27) = 2.52188
    c: Angle(g30,g27) = 2.26951
    c: Angle(g23,g24) = 2.50404
    c: Angle(g22,g23) = 2.81442
    c: Distance(g35) = 77.6
    c: Angle(g33,g35) = 2.87995
    c: Coincident(g36,g35)
    c: Distance(g36) = 40.4
    c: Angle(g33,g36) = 2.82761
    c: Horizontal(g37)
    c: Coincident(g38,g35)
    c: Coincident(g39,g38)
    c: Horizontal(g39)
    c: Coincident(g40,g39)
    c: Coincident(g40,g30)
    c: Distance(g38) = 30.6334
    c: Angle(g38,g33) = 0.110874
    c: DistanceX(g39,g39) = 130
    c: Distance(g40) = 127.367
    c: Coincident(g4,g41)
    c: Horizontal(g41)
    c: Coincident(g41,g42)
    c: Coincident(g43,g42)
    c: Coincident(g43,g12)
    c: Distance(g43) = 2.4804
    c: Angle(g18,g17) = 2.49901
    c: Angle(g19,g17) = 2.36124
    c: Angle(g20,g17) = 2.24748
    c: Coincident(g44,g37)
    c: Horizontal(g44)
    c: Angle(g42,g43) = 2.11973
    c: Angle(g42,g12) = 2.04062
    c: Angle(g42,g13) = 1.58195
    c: Angle(g13,g14) = 3.03808
    c: Vertical(g45)
    c: Coincident(g46,g45)
    c: Horizontal(g46)
    c: DistanceY(g45,g45) = 533.462
    c: PointOnObject(g47,g33)
    c: DistanceY(g47,g47) = 548.062
    c: Angle(g39,g40) = 2.59833
    c: Coincident(g21,g48)
    c: Vertical(g49)
    c: Coincident(g49,g50)
    c: Horizontal(g50)
    c: Coincident(g49,g51)
    c: Horizontal(g51)
    c: Coincident(g51,g52)
    c: Vertical(g52)
    c: Coincident(g52,g53)
    c: Horizontal(g53)
    c: Coincident(g53,g54)
    c: Vertical(g54)
    c: Coincident(g48,g55)
    c: Coincident(g55,g56)
    c: Coincident(g56,g57)
    c: Coincident(g57,g58)
    c: Coincident(g58,g59)
    c: Coincident(g59,g60)
    c: Vertical(g60)
    c: Coincident(g60,g61)
    c: Coincident(g61,g62)
    c: Coincident(g63,g20)
    c: Distance(g25) = 178.589
    c: Angle(g25,g24) = 2.99497
    c: Distance(g48) = 12.5968
    c: Distance(g55) = 35.4072
    c: Distance(g56) = 3.49857
    c: Distance(g57) = 6.65282
    c: Distance(g58) = 4.97393
    c: Distance(g59) = 4.23793
    c: DistanceY(g60,g60) = 137.8
    c: Angle(g21,g22) = 2.58706
    c: Angle(g48,g21) = 2.86681
    c: Angle(g48,g55) = 3.12214
    c: Angle(g55,g56) = 3.03493
    c: Angle(g56,g57) = 2.85409
    c: Angle(g57,g58) = 2.92535
    c: Angle(g58,g59) = 2.95164
    c: Angle(g60,g61) = 2.81984
    c: Angle(g60,g62) = 2.49809
    c: Angle(g5,g4) = 2.00942
    c: Angle(g41,g4) = 1.58154
    c: DistanceX(g41,g41) = 54.3154
    c: Coincident(g65,g4)
    c: PointOnObject(g65,g42)
    c: Distance(g42) = 10.9802
    c: Distance(g63) = 52.6666
    c: Distance(g62) = 5
    c: Distance(g61) = 4.42719
    c: Distance(g15) = 103.143
FEATURE [Sketcher::SketchObject] Sketch013  label="Body Outline002"
  FullyConstrained = false
  MapMode = 5
  Placement = pos=(0,0,45) rot=(0,0,1;0rad)
  Support = -> [Pad]
  sketch-geometry (53):
    g0: LineSegment StartX=197.29 StartY=495.3 StartZ=0 EndX=73.9 EndY=550.1 EndZ=0
    g1: LineSegment StartX=252.163 StartY=545.48 StartZ=0 EndX=252.549 EndY=509.479 EndZ=0
    g2: LineSegment StartX=252.549 StartY=509.479 StartZ=0 EndX=349.415 EndY=461.037 EndZ=0
    g3: LineSegment StartX=349.415 StartY=461.037 StartZ=0 EndX=353.199 EndY=456.9 EndZ=0
    g4: LineSegment StartX=353.199 StartY=456.9 StartZ=0 EndX=356 EndY=452.4 EndZ=0
    g5: LineSegment StartX=356 StartY=452.4 StartZ=0 EndX=356 EndY=442 EndZ=0
    g6: LineSegment StartX=356 StartY=442 StartZ=0 EndX=320 EndY=343.5 EndZ=0
    g7: LineSegment StartX=320 StartY=343.5 StartZ=0 EndX=320 EndY=331.5 EndZ=0
    g8: LineSegment StartX=195.595 StartY=533.23 StartZ=0 EndX=190.6 EndY=530.763 EndZ=0
    g9: LineSegment StartX=190.6 StartY=530.763 StartZ=0 EndX=185.73 EndY=530.763 EndZ=0
    g10: LineSegment StartX=185.73 StartY=530.763 StartZ=0 EndX=184.498 EndY=530.892 EndZ=0
    g11: LineSegment StartX=184.498 StartY=530.892 StartZ=0 EndX=97.995 EndY=587.067 EndZ=0
    g12: LineSegment StartX=97.995 StartY=587.067 StartZ=0 EndX=91.1433 EndY=587.067 EndZ=0
    g13: LineSegment StartX=91.1433 StartY=587.067 StartZ=0 EndX=89.4833 EndY=585.824 EndZ=0
    g14: LineSegment StartX=89.4833 StartY=585.824 StartZ=0 EndX=87.4933 EndY=583.854 EndZ=0
    g15: LineSegment StartX=87.4933 StartY=583.854 StartZ=0 EndX=85.9833 EndY=581.974 EndZ=0
    g16: LineSegment StartX=107.659 StartY=357.048 StartZ=0 EndX=122.894 EndY=344.497 EndZ=0
    g17: LineSegment StartX=122.894 StartY=344.497 StartZ=0 EndX=130.394 EndY=322.397 EndZ=0
    g18: LineSegment StartX=130.394 StartY=322.397 StartZ=0 EndX=130.394 EndY=310.397 EndZ=0
    g19: LineSegment StartX=130.394 StartY=310.397 StartZ=0 EndX=128.394 EndY=307.697 EndZ=0
    g20: LineSegment StartX=128.394 StartY=307.697 StartZ=0 EndX=44.2001 EndY=150.2 EndZ=0
    g21: LineSegment StartX=44.2001 StartY=150.2 StartZ=0 EndX=44.2001 EndY=148.6 EndZ=0
    g22: LineSegment StartX=44.2001 StartY=148.6 StartZ=0 EndX=44.2001 EndY=144.6 EndZ=0
    g23: LineSegment StartX=44.2001 StartY=144.6 StartZ=0 EndX=45.1101 EndY=141.95 EndZ=0
    g24: LineSegment StartX=45.1101 StartY=141.95 StartZ=0 EndX=47.2241 EndY=138.987 EndZ=0
    g25: LineSegment StartX=47.2241 StartY=138.987 StartZ=0 EndX=50.9701 EndY=135.84 EndZ=0
    g26: LineSegment StartX=413.447 StartY=50.3961 StartZ=0 EndX=410.947 EndY=46.6961 EndZ=0
    g27: LineSegment StartX=410.947 StartY=46.6961 StartZ=0 EndX=408.821 EndY=43.4656 EndZ=0
    g28: LineSegment StartX=408.821 StartY=43.4656 StartZ=0 EndX=403.447 EndY=43.4656 EndZ=0
    g29: LineSegment StartX=403.447 StartY=43.4656 StartZ=0 EndX=320.445 EndY=66.6105 EndZ=0
    g30: LineSegment StartX=320.445 StartY=66.6105 StartZ=0 EndX=290 EndY=70 EndZ=0
    g31: LineSegment StartX=290 StartY=70 StartZ=0 EndX=160 EndY=70 EndZ=0
    g32: LineSegment StartX=160 StartY=70 StartZ=0 EndX=50.9701 EndY=135.84 EndZ=0
    g33: LineSegment StartX=252.163 StartY=545.48 StartZ=0 EndX=197.847 EndY=545.48 EndZ=0
    g34: LineSegment StartX=197.847 StartY=545.48 StartZ=0 EndX=197.725 EndY=534.5 EndZ=0
    g35: LineSegment StartX=197.725 StartY=534.5 StartZ=0 EndX=195.595 EndY=533.23 EndZ=0
    g36: LineSegment StartX=107.659 StartY=357.048 StartZ=0 EndX=96.1282 EndY=362.119 EndZ=0
    g37: LineSegment StartX=96.1282 StartY=362.119 StartZ=0 EndX=64 EndY=377 EndZ=0
    g38: LineSegment StartX=64 StartY=377 StartZ=0 EndX=61 EndY=378.8 EndZ=0
    g39: LineSegment StartX=61 StartY=378.8 StartZ=0 EndX=56.5 EndY=383.7 EndZ=0
    g40: LineSegment StartX=56.5 StartY=383.7 StartZ=0 EndX=54 EndY=388 EndZ=0
    g41: LineSegment StartX=54 StartY=388 StartZ=0 EndX=52.6 EndY=392 EndZ=0
    g42: LineSegment StartX=52.6 StartY=392 StartZ=0 EndX=52.6 EndY=529.8 EndZ=0
    g43: LineSegment StartX=52.6 StartY=529.8 StartZ=0 EndX=54 EndY=534 EndZ=0
    g44: LineSegment StartX=54 StartY=534 StartZ=0 EndX=57 EndY=538 EndZ=0
    g45: LineSegment StartX=57 StartY=538 StartZ=0 EndX=85.9833 EndY=581.974 EndZ=0
    g46: LineSegment StartX=413.447 StartY=50.3961 StartZ=0 EndX=413.447 EndY=57.5961 EndZ=0
    g47: LineSegment StartX=-1 StartY=616 StartZ=0 EndX=451 EndY=616 EndZ=0
    g48: LineSegment StartX=451 StartY=616 StartZ=0 EndX=451 EndY=14 EndZ=0
    g49: LineSegment StartX=451 StartY=14 StartZ=0 EndX=-1 EndY=14 EndZ=0
    g50: LineSegment StartX=-1 StartY=14 StartZ=0 EndX=-1 EndY=616 EndZ=0
    g51: LineSegment StartX=257 StartY=545.5 StartZ=0 EndX=257 EndY=245.424 EndZ=0
    g52: LineSegment StartX=320 StartY=331.5 StartZ=0 EndX=413.447 EndY=57.5961 EndZ=0
  constraints (145):
    c: Coincident(g1,g2)
    c: Coincident(g2,g3)
    c: Coincident(g3,g4)
    c: Coincident(g4,g5)
    c: Vertical(g5)
    c: Coincident(g6,g5)
    c: Coincident(g7,g6)
    c: Vertical(g7)
    c: Coincident(g8,g9)
    c: Horizontal(g9)
    c: Coincident(g9,g10)
    c: Coincident(g10,g11)
    c: Distance(g10) = 1.23908
    c: Distance(g8) = 5.57001
    c: DistanceX(g9,g9) = 4.86999
    c: Coincident(g12,g11)
    c: Horizontal(g12)
    c: Coincident(g13,g12)
    c: Coincident(g13,g14)
    c: Coincident(g14,g15)
    c: Coincident(g16,g17)
    c: Coincident(g17,g18)
    c: Vertical(g18)
    c: Coincident(g19,g18)
    c: Coincident(g20,g19)
    c: Coincident(g21,g20)
    c: Vertical(g21)
    c: Coincident(g21,g22)
    c: Vertical(g22)
    c: Coincident(g22,g23)
    c: Coincident(g23,g24)
    c: Coincident(g24,g25)
    c: Coincident(g27,g26)
    c: Coincident(g28,g27)
    c: Horizontal(g28)
    c: DistanceX(g28,g28) = 5.37372
    c: Distance(g26) = 4.46542
    c: Distance(g27) = 3.86749
    c: Coincident(g29,g28)
    c: DistanceY(g7,g7) = 12
    c: DistanceY(g5,g5) = 10.4
    c: Distance(g4) = 5.3
    c: Distance(g3) = 5.60673
    c: Distance(g1) = 36.0023
    c: Distance(g15) = 2.41133
    c: Distance(g14) = 2.80018
    c: Distance(g13) = 2.07357
    c: DistanceX(g12,g12) = 6.85172
    c: Distance(g16) = 19.7388
    c: Distance(g17) = 23.3379
    c: DistanceY(g18,g18) = 12
    c: Distance(g19) = 3.36006
    c: DistanceY(g21,g21) = 1.6
    c: DistanceY(g22,g22) = 4
    c: Distance(g23) = 2.8019
    c: Distance(g24) = 3.63982
    c: Distance(g25) = 4.89246
    c: Angle(g23,g22) = 2.81082
    c: Angle(g24,g22) = 2.52188
    c: Angle(g25,g22) = 2.26951
    c: Angle(g18,g19) = 2.50404
    c: Angle(g17,g18) = 2.81442
    c: Coincident(g30,g29)
    c: Coincident(g31,g30)
    c: Horizontal(g31)
    c: Coincident(g32,g31)
    c: Coincident(g32,g25)
    c: Distance(g30) = 30.6334
    c: Angle(g30,g28) = 0.110874
    c: DistanceX(g31,g31) = 130
    c: Distance(g32) = 127.367
    c: Coincident(g1,g33)
    c: Horizontal(g33)
    c: Coincident(g33,g34)
    c: Coincident(g35,g34)
    c: Coincident(g35,g8)
    c: Distance(g35) = 2.4804
    c: Angle(g13,g12) = 2.49901
    c: Angle(g14,g12) = 2.36124
    c: Angle(g15,g12) = 2.24748
    c: Angle(g34,g35) = 2.11973
    c: Angle(g34,g8) = 2.04062
    c: Angle(g34,g9) = 1.58195
    c: Angle(g9,g10) = 3.03808
    c: Angle(g31,g32) = 2.59833
    c: Coincident(g16,g36)
    c: Coincident(g36,g37)
    c: Coincident(g37,g38)
    c: Coincident(g38,g39)
    c: Coincident(g39,g40)
    c: Coincident(g40,g41)
    c: Coincident(g41,g42)
    c: Vertical(g42)
    c: Coincident(g42,g43)
    c: Coincident(g43,g44)
    c: Coincident(g45,g15)
    c: Distance(g20) = 178.589
    c: Angle(g20,g19) = 2.99497
    c: Distance(g36) = 12.5968
    c: Distance(g37) = 35.4072
    c: Distance(g38) = 3.49857
    c: Distance(g39) = 6.65282
    c: Distance(g40) = 4.97393
    c: Distance(g41) = 4.23793
    c: DistanceY(g42,g42) = 137.8
    c: Angle(g16,g17) = 2.58706
    c: Angle(g36,g16) = 2.86681
    c: Angle(g36,g37) = 3.12214
    c: Angle(g37,g38) = 3.03493
    c: Angle(g38,g39) = 2.85409
    c: Angle(g39,g40) = 2.92535
    c: Angle(g40,g41) = 2.95164
    c: Angle(g42,g43) = 2.81984
    c: Angle(g42,g44) = 2.49809
    c: Angle(g33,g1) = 1.58154
    c: DistanceX(g33,g33) = 54.3154
    c: Distance(g34) = 10.9802
    c: Distance(g45) = 52.6666
    c: Distance(g44) = 5
    c: Distance(g43) = 4.42719
    c: Distance(g11) = 103.143
    c: Coincident(g44,g45)
    c: Coincident(g46,g26)
    c: Vertical(g46)
    c: Distance(g46) = 7.20003
    c: Angle(g46,g26) = 2.54737
    c: Coincident(g47,g48)
    c: Coincident(g48,g49)
    c: Coincident(g49,g50)
    c: Coincident(g50,g47)
    c: Horizontal(g47)
    c: Horizontal(g49)
    c: Vertical(g48)
    c: Vertical(g50)
    c: DistanceY(g48,g48) = 602
    c: DistanceX(g49,g49) = 452
    c: Vertical(g51)
    c: Coincident(g52,g7)
    c: Coincident(g52,g46)
    c: Angle(g27,g28) = 2.1529
    c: Angle(g4,g5) = 2.58482
    c: Angle(g3,g5) = 2.40074
    c: Distance(g2) = 108.304
    c: Angle(g2,g5) = 2.03453
    c: Angle(g28,g29) = 2.86965
FEATURE [Sketcher::SketchObject] Sketch014  label="speaker grill recess"
  FullyConstrained = false
  MapMode = 5
  Placement = pos=(0,0,45) rot=(0,0,1;0rad)
  Support = -> [Pad]
  sketch-geometry (1):
    g0: Circle CenterX=330 CenterY=121 CenterZ=0 NormalX=0 NormalY=0 NormalZ=1 AngleXU=0 Radius=47
  constraints (1):
    c: Diameter(g0) = 94
FEATURE [Sketcher::SketchObject] Sketch015  label="Red Stripe outline"
  FullyConstrained = false
  MapMode = 5
  Placement = pos=(0,0,45) rot=(0,0,1;0rad)
  Support = -> [Pad]
  sketch-geometry (4):
    g0: LineSegment StartX=170 StartY=70 StartZ=0 EndX=280 EndY=70 EndZ=0
    g1: LineSegment StartX=280 StartY=70 StartZ=0 EndX=280 EndY=540 EndZ=0
    g2: LineSegment StartX=280 StartY=540 StartZ=0 EndX=170 EndY=540 EndZ=0
    g3: LineSegment StartX=170 StartY=540 StartZ=0 EndX=170 EndY=70 EndZ=0
  constraints (8):
    c: Coincident(g0,g1)
    c: Coincident(g1,g2)
    c: Coincident(g2,g3)
    c: Coincident(g3,g0)
    c: Horizontal(g0)
    c: Horizontal(g2)
    c: Vertical(g1)
    c: Vertical(g3)
FEATURE [Sketcher::SketchObject] Sketch016  label="AFPI Mount Pocket"
  FullyConstrained = false
  MapMode = 5
  Placement = pos=(0,0,45) rot=(0,0,1;0rad)
  Support = -> [Pad]
  sketch-geometry (4):
    g0: LineSegment StartX=68 StartY=514 StartZ=0 EndX=160 EndY=514 EndZ=0
    g1: LineSegment StartX=160 StartY=514 StartZ=0 EndX=160 EndY=395 EndZ=0
    g2: LineSegment StartX=160 StartY=395 StartZ=0 EndX=68 EndY=395 EndZ=0
    g3: LineSegment StartX=68 StartY=395 StartZ=0 EndX=68 EndY=514 EndZ=0
  constraints (10):
    c: Coincident(g0,g1)
    c: Coincident(g1,g2)
    c: Coincident(g2,g3)
    c: Coincident(g3,g0)
    c: Horizontal(g0)
    c: Horizontal(g2)
    c: Vertical(g1)
    c: Vertical(g3)
    c: DistanceY(g1,g1) = 119
    c: DistanceX(g0,g0) = 92
FEATURE [Sketcher::SketchObject] Sketch017  label="Pickup Controls layouts"
  FullyConstrained = false
  MapMode = 5
  Placement = pos=(0,0,45) rot=(0,0,1;0rad)
  Support = -> [Pad]
  sketch-geometry (11):
    g0: LineSegment StartX=330 StartY=250 StartZ=0 EndX=353.532 EndY=180 EndZ=0
    g1: LineSegment StartX=353.532 StartY=180 StartZ=0 EndX=290 EndY=180 EndZ=0
    g2: LineSegment StartX=290 StartY=180 StartZ=0 EndX=290 EndY=250 EndZ=0
    g3: LineSegment StartX=330 StartY=250 StartZ=0 EndX=290 EndY=250 EndZ=0
    g4: Circle CenterX=302 CenterY=230 CenterZ=0 NormalX=0 NormalY=0 NormalZ=1 AngleXU=0 Radius=8.5
    g5: Circle CenterX=302 CenterY=200 CenterZ=0 NormalX=0 NormalY=0 NormalZ=1 AngleXU=0 Radius=8.5
    g6: LineSegment StartX=316.216 StartY=240.209 StartZ=0 EndX=326.216 EndY=240.209 EndZ=0
    g7: LineSegment StartX=326.216 StartY=240.209 StartZ=0 EndX=341.048 EndY=194.558 EndZ=0
    g8: LineSegment StartX=341.048 StartY=194.558 StartZ=0 EndX=330.587 EndY=191.159 EndZ=0
    g9: LineSegment StartX=326.216 StartY=240.209 StartZ=0 EndX=315.754 EndY=236.809 EndZ=0
    g10: LineSegment StartX=315.754 StartY=236.809 StartZ=0 EndX=330.587 EndY=191.159 EndZ=0
  constraints (25):
    c: Coincident(g1,g0)
    c: Horizontal(g1)
    c: Coincident(g2,g1)
    c: Vertical(g2)
    c: Coincident(g3,g0)
    c: Coincident(g3,g2)
    c: Horizontal(g3)
    c: Distance(g0) = 73.8495
    c: DistanceX(g3,g3) = 40
    c: DistanceX(g1,g1) = 63.5319
    c: Diameter(g4) = 17
    c: Diameter(g5) = 17
    c: Horizontal(g6)
    c: Coincident(g7,g6)
    c: DistanceX(g6,g6) = 10
    c: Angle(g6,g7) = 1.88496
    c: Distance(g7) = 48
    c: Coincident(g8,g7)
    c: Angle(g7,g8) = 1.5708
    c: Distance(g8) = 11
    c: Coincident(g9,g7)
    c: Angle(g9,g7) = 1.5708
    c: Coincident(g10,g9)
    c: Coincident(g10,g8)
    c: Distance(g9) = 11
FEATURE [Sketcher::SketchObject] Sketch018  label="RGB clear plate pocket"
  FullyConstrained = false
  MapMode = 5
  Placement = pos=(0,0,45) rot=(0,0,1;0rad)
  Support = -> [Pad]
  sketch-geometry (4):
    g0: LineSegment StartX=178 StartY=430.5 StartZ=0 EndX=272 EndY=430.5 EndZ=0
    g1: LineSegment StartX=272 StartY=430.5 StartZ=0 EndX=272 EndY=410.5 EndZ=0
    g2: LineSegment StartX=272 StartY=410.5 StartZ=0 EndX=178 EndY=410.5 EndZ=0
    g3: LineSegment StartX=178 StartY=410.5 StartZ=0 EndX=178 EndY=430.5 EndZ=0
  constraints (10):
    c: Coincident(g0,g1)
    c: Coincident(g1,g2)
    c: Coincident(g2,g3)
    c: Coincident(g3,g0)
    c: Horizontal(g0)
    c: Horizontal(g2)
    c: Vertical(g1)
    c: Vertical(g3)
    c: DistanceY(g3,g3) = 20
    c: DistanceX(g0,g0) = 94
FEATURE [Sketcher::SketchObject] Sketch019  label="blank template001"
  FullyConstrained = false
  MapMode = 5
  Support = -> [XY_Plane001]
  sketch-geometry (4):
    g0: LineSegment StartX=0 StartY=615 StartZ=0 EndX=450 EndY=615 EndZ=0
    g1: LineSegment StartX=450 StartY=615 StartZ=0 EndX=450 EndY=15 EndZ=0
    g2: LineSegment StartX=450 StartY=15 StartZ=0 EndX=0 EndY=15 EndZ=0
    g3: LineSegment StartX=0 StartY=15 StartZ=0 EndX=0 EndY=615 EndZ=0
  constraints (10):
    c: Coincident(g0,g1)
    c: Coincident(g1,g2)
    c: Coincident(g2,g3)
    c: Coincident(g3,g0)
    c: Horizontal(g0)
    c: Horizontal(g2)
    c: Vertical(g1)
    c: Vertical(g3)
    c: DistanceX(g2,g2) = 450
    c: DistanceY(g1,g1) = 600
FEATURE [PartDesign::Pad] Pad001  label="Template 600x450"
  Direction = (0,0,1)
  Length = 45
  Length2 = 10
  Profile = -> Sketch019
  ReferenceAxis = -> Sketch019 [N_Axis]
  Type = 0
FEATURE [Sketcher::SketchObject] Sketch021  label="pickup holes001"
  FullyConstrained = false
  MapMode = 5
  Placement = pos=(0,0,45) rot=(0,0,1;0rad)
  Support = -> [Pad001]
  sketch-geometry (28):
    g0: LineSegment StartX=225 StartY=601 StartZ=0 EndX=225 EndY=-1 EndZ=0
    g1: LineSegment StartX=182.5 StartY=460 StartZ=0 EndX=267.5 EndY=460 EndZ=0
    g2: LineSegment StartX=267.5 StartY=460 StartZ=0 EndX=267.5 EndY=441 EndZ=0
    g3: LineSegment StartX=267.5 StartY=441 StartZ=0 EndX=182.5 EndY=441 EndZ=0
    g4: LineSegment StartX=182.5 StartY=441 StartZ=0 EndX=182.5 EndY=460 EndZ=0
    g5: LineSegment StartX=182.5 StartY=400 StartZ=0 EndX=267.5 EndY=400 EndZ=0
    g6: LineSegment StartX=267.5 StartY=400 StartZ=0 EndX=267.5 EndY=381 EndZ=0
    g7: LineSegment StartX=267.5 StartY=381 StartZ=0 EndX=182.5 EndY=381 EndZ=0
    g8: LineSegment StartX=182.5 StartY=381 StartZ=0 EndX=182.5 EndY=400 EndZ=0
    g9: LineSegment StartX=188.75 StartY=357.8 StartZ=0 EndX=261.25 EndY=357.8 EndZ=0
    g10: LineSegment StartX=261.25 StartY=357.8 StartZ=0 EndX=261.25 EndY=347.8 EndZ=0
    g11: LineSegment StartX=261.25 StartY=347.8 StartZ=0 EndX=269.25 EndY=347.8 EndZ=0
    g12: LineSegment StartX=269.25 StartY=347.8 StartZ=0 EndX=269.25 EndY=327.8 EndZ=0
    g13: LineSegment StartX=269.25 StartY=327.8 StartZ=0 EndX=261.25 EndY=327.8 EndZ=0
    g14: LineSegment StartX=261.25 StartY=327.8 StartZ=0 EndX=261.25 EndY=317.8 EndZ=0
    g15: LineSegment StartX=261.25 StartY=317.8 StartZ=0 EndX=188.75 EndY=317.8 EndZ=0
    g16: LineSegment StartX=188.75 StartY=317.8 StartZ=0 EndX=188.75 EndY=327.8 EndZ=0
    g17: LineSegment StartX=188.75 StartY=327.8 StartZ=0 EndX=180.75 EndY=327.8 EndZ=0
    g18: LineSegment StartX=180.75 StartY=327.8 StartZ=0 EndX=180.75 EndY=347.8 EndZ=0
    g19: LineSegment StartX=180.75 StartY=347.8 StartZ=0 EndX=188.75 EndY=347.8 EndZ=0
    g20: LineSegment StartX=188.75 StartY=347.8 StartZ=0 EndX=188.75 EndY=357.8 EndZ=0
    g21: LineSegment StartX=182.5 StartY=460 StartZ=0 EndX=182.5 EndY=469.3 EndZ=0
    g22: LineSegment StartX=182.5 StartY=469.3 StartZ=0 EndX=210 EndY=469.3 EndZ=0
    g23: LineSegment StartX=182.5 StartY=441 StartZ=0 EndX=182.5 EndY=400 EndZ=0
    g24: LineSegment StartX=177 StartY=469.3 StartZ=0 EndX=177 EndY=357.8 EndZ=0
    g25: LineSegment StartX=177 StartY=357.8 StartZ=0 EndX=180.75 EndY=357.8 EndZ=0
    g26: LineSegment StartX=180.75 StartY=357.8 StartZ=0 EndX=188.75 EndY=357.8 EndZ=0
    g27: LineSegment StartX=261.25 StartY=357.8 StartZ=0 EndX=261.25 EndY=381 EndZ=0
  constraints (76):
    c: Vertical(g0)
    c: Coincident(g1,g2)
    c: Coincident(g2,g3)
    c: Coincident(g3,g4)
    c: Coincident(g4,g1)
    c: Horizontal(g1)
    c: Horizontal(g3)
    c: Vertical(g2)
    c: Vertical(g4)
    c: DistanceX(g1,g1) = 85
    c: DistanceY(g2,g2) = 19
    c: Coincident(g5,g6)
    c: Coincident(g6,g7)
    c: Coincident(g7,g8)
    c: Coincident(g8,g5)
    c: Horizontal(g5)
    c: Horizontal(g7)
    c: Vertical(g6)
    c: Vertical(g8)
    c: DistanceX(g5,g5) = 85
    c: DistanceY(g8,g8) = 19
    c: Horizontal(g9)
    c: Coincident(g9,g10)
    c: Vertical(g10)
    c: Coincident(g10,g11)
    c: Horizontal(g11)
    c: Coincident(g11,g12)
    c: Vertical(g12)
    c: Coincident(g12,g13)
    c: Horizontal(g13)
    c: Coincident(g13,g14)
    c: Vertical(g14)
    c: Coincident(g14,g15)
    c: Horizontal(g15)
    c: Coincident(g15,g16)
    c: Vertical(g16)
    c: Coincident(g16,g17)
    c: Horizontal(g17)
    c: Coincident(g17,g18)
    c: Vertical(g18)
    c: Coincident(g18,g19)
    c: Horizontal(g19)
    c: Coincident(g19,g20)
    c: Coincident(g20,g9)
    c: Vertical(g20)
    c: DistanceX(g9,g9) = 72.5
    c: DistanceY(g12,g12) = 20
    c: DistanceY(g10,g10) = 10
    c: DistanceY(g14,g14) = 10
    c: DistanceX(g19,g19) = 8
    c: DistanceX(g17,g17) = 8
    c: DistanceX(g13,g13) = 8
    c: DistanceY(g20,g20) = 10
    c: DistanceY(g16,g16) = 10
    c: DistanceX(g15,g15) = 72.5
    c: Coincident(g21,g1)
    c: Vertical(g21)
    c: DistanceY(g21,g21) = 9.3
    c: Coincident(g22,g21)
    c: Horizontal(g22)
    c: Coincident(g23,g3)
    c: Vertical(g23)
    c: DistanceY(g23,g23) = 41
    c: Vertical(g24)
    c: Coincident(g25,g24)
    c: Horizontal(g25)
    c: DistanceY(g24,g24) = 111.5
    c: Coincident(g26,g25)
    c: Coincident(g26,g9)
    c: Horizontal(g26)
    c: DistanceX(g26,g26) = 8
    c: DistanceX(g25,g25) = 3.74999
    c: Coincident(g27,g9)
    c: PointOnObject(g27,g7)
    c: Vertical(g27)
    c: DistanceY(g27,g27) = 23.2
FEATURE [Sketcher::SketchObject] Sketch022  label="tremelo pocket001"
  FullyConstrained = false
  MapMode = 5
  Placement = pos=(0,0,45) rot=(0,0,1;0rad)
  Support = -> [Pad001]
  sketch-geometry (11):
    g0: LineSegment StartX=225 StartY=610 StartZ=0 EndX=225 EndY=-10 EndZ=0
    g1: LineSegment StartX=182.5 StartY=460 StartZ=0 EndX=182.5 EndY=469.3 EndZ=0
    g2: LineSegment StartX=182.5 StartY=469.3 StartZ=0 EndX=182.5 EndY=481.3 EndZ=0
    g3: LineSegment StartX=178 StartY=481.3 StartZ=0 EndX=178 EndY=295.3 EndZ=0
    g4: LineSegment StartX=178 StartY=295.3 StartZ=0 EndX=178 EndY=282.3 EndZ=0
    g5: LineSegment StartX=224.9 StartY=282.4 StartZ=0 EndX=224.99 EndY=282.4 EndZ=0
    g6: LineSegment StartX=224.9 StartY=282.4 StartZ=0 EndX=189.9 EndY=282.4 EndZ=0
    g7: LineSegment StartX=189.9 StartY=282.3 StartZ=0 EndX=267.9 EndY=282.3 EndZ=0
    g8: LineSegment StartX=267.9 StartY=282.3 StartZ=0 EndX=267.9 EndY=263.3 EndZ=0
    g9: LineSegment StartX=267.9 StartY=263.3 StartZ=0 EndX=189.9 EndY=263.3 EndZ=0
    g10: LineSegment StartX=189.9 StartY=263.3 StartZ=0 EndX=189.9 EndY=282.3 EndZ=0
  constraints (26):
    c: Vertical(g0)
    c: Vertical(g1)
    c: Coincident(g2,g1)
    c: Vertical(g2)
    c: Vertical(g3)
    c: Coincident(g4,g3)
    c: Vertical(g4)
    c: DistanceY(g4,g4) = 13
    c: DistanceY(g3,g3) = 186
    c: DistanceY(g1,g1) = 9.3
    c: DistanceY(g2,g2) = 12
    c: Horizontal(g5)
    c: Coincident(g6,g5)
    c: Horizontal(g6)
    c: DistanceX(g6,g6) = 35
    c: DistanceX(g5,g5) = 0.08999
    c: Coincident(g7,g8)
    c: Coincident(g8,g9)
    c: Coincident(g9,g10)
    c: Coincident(g10,g7)
    c: Horizontal(g7)
    c: Horizontal(g9)
    c: Vertical(g8)
    c: Vertical(g10)
    c: DistanceX(g7,g7) = 78
    c: DistanceY(g10,g10) = 19
FEATURE [Sketcher::SketchObject] Sketch023  label="control pocket001"
  FullyConstrained = false
  MapMode = 5
  Placement = pos=(0,0,45) rot=(0,0,1;0rad)
  Support = -> [Pad001]
  sketch-geometry (11):
    g0: LineSegment StartX=330 StartY=250 StartZ=0 EndX=353.532 EndY=180 EndZ=0
    g1: LineSegment StartX=353.532 StartY=180 StartZ=0 EndX=290 EndY=180 EndZ=0
    g2: LineSegment StartX=290 StartY=180 StartZ=0 EndX=290 EndY=250 EndZ=0
    g3: LineSegment StartX=330 StartY=250 StartZ=0 EndX=290 EndY=250 EndZ=0
    g4: Circle CenterX=302 CenterY=230 CenterZ=0 NormalX=0 NormalY=0 NormalZ=1 AngleXU=0 Radius=8.5
    g5: Circle CenterX=302 CenterY=200 CenterZ=0 NormalX=0 NormalY=0 NormalZ=1 AngleXU=0 Radius=8.5
    g6: LineSegment StartX=316.216 StartY=240.298 StartZ=0 EndX=326.216 EndY=240.298 EndZ=0
    g7: LineSegment StartX=326.216 StartY=240.298 StartZ=0 EndX=341.048 EndY=194.647 EndZ=0
    g8: LineSegment StartX=341.048 StartY=194.647 StartZ=0 EndX=330.587 EndY=191.248 EndZ=0
    g9: LineSegment StartX=326.216 StartY=240.298 StartZ=0 EndX=315.754 EndY=236.898 EndZ=0
    g10: LineSegment StartX=315.754 StartY=236.898 StartZ=0 EndX=330.587 EndY=191.248 EndZ=0
  constraints (25):
    c: Coincident(g1,g0)
    c: Horizontal(g1)
    c: Coincident(g2,g1)
    c: Vertical(g2)
    c: Coincident(g3,g0)
    c: Coincident(g3,g2)
    c: Horizontal(g3)
    c: Distance(g0) = 73.8495
    c: DistanceX(g3,g3) = 40
    c: DistanceX(g1,g1) = 63.5319
    c: Diameter(g4) = 17
    c: Diameter(g5) = 17
    c: Horizontal(g6)
    c: Coincident(g7,g6)
    c: DistanceX(g6,g6) = 10
    c: Angle(g6,g7) = 1.88496
    c: Distance(g7) = 48
    c: Coincident(g8,g7)
    c: Angle(g7,g8) = 1.5708
    c: Distance(g8) = 11
    c: Coincident(g9,g7)
    c: Angle(g9,g7) = 1.5708
    c: Coincident(g10,g9)
    c: Coincident(g10,g8)
    c: Distance(g9) = 11
FEATURE [Sketcher::SketchObject] Sketch024  label="AFPI pocket001"
  FullyConstrained = false
  MapMode = 5
  Placement = pos=(0,0,45) rot=(0,0,1;0rad)
  Support = -> [Pad001]
  sketch-geometry (24):
    g0: LineSegment StartX=68 StartY=506.5 StartZ=0 EndX=160 EndY=506.5 EndZ=0
    g1: LineSegment StartX=160 StartY=506.5 StartZ=0 EndX=160 EndY=402.5 EndZ=0
    g2: LineSegment StartX=160 StartY=402.5 StartZ=0 EndX=68 EndY=402.5 EndZ=0
    g3: LineSegment StartX=68 StartY=402.5 StartZ=0 EndX=68 EndY=506.5 EndZ=0
    g4: LineSegment StartX=-192.181 StartY=581.522 StartZ=0 EndX=-181.31 EndY=478.092 EndZ=0
    g5: LineSegment StartX=-181.31 StartY=478.092 StartZ=0 EndX=-89.8139 EndY=487.709 EndZ=0
    g6: LineSegment StartX=-192.181 StartY=581.522 StartZ=0 EndX=-100.685 EndY=591.139 EndZ=0
    g7: LineSegment StartX=-100.685 StartY=591.139 StartZ=0 EndX=-89.8139 EndY=487.709 EndZ=0
    g8: LineSegment StartX=-192.181 StartY=581.522 StartZ=0 EndX=-192.181 EndY=481.522 EndZ=0
    g9: LineSegment StartX=175 StartY=400 StartZ=0 EndX=275 EndY=400 EndZ=0
    g10: LineSegment StartX=175 StartY=400 StartZ=0 EndX=175 EndY=490 EndZ=0
    g11: LineSegment StartX=175 StartY=400 StartZ=0 EndX=175 EndY=380 EndZ=0
    g12: LineSegment StartX=-89.8139 StartY=487.709 StartZ=0 EndX=-88.927 EndY=479.201 EndZ=0
    g13: LineSegment StartX=-181.31 StartY=478.092 StartZ=0 EndX=-180.433 EndY=469.628 EndZ=0
    g14: LineSegment StartX=-180.433 StartY=469.628 StartZ=0 EndX=-88.927 EndY=479.201 EndZ=0
    g15: LineSegment StartX=-192.181 StartY=581.522 StartZ=0 EndX=-193.082 EndY=590 EndZ=0
    g16: LineSegment StartX=-100.685 StartY=591.139 StartZ=0 EndX=-101.58 EndY=599.597 EndZ=0
    g17: LineSegment StartX=-101.58 StartY=599.597 StartZ=0 EndX=-193.082 EndY=590 EndZ=0
    g18: LineSegment StartX=68 StartY=506.5 StartZ=0 EndX=68 EndY=515 EndZ=0
    g19: LineSegment StartX=68 StartY=515 StartZ=0 EndX=160 EndY=515 EndZ=0
    g20: LineSegment StartX=160 StartY=515 StartZ=0 EndX=160 EndY=506.5 EndZ=0
    g21: LineSegment StartX=160 StartY=402.5 StartZ=0 EndX=160 EndY=393.9 EndZ=0
    g22: LineSegment StartX=160 StartY=393.9 StartZ=0 EndX=68 EndY=393.9 EndZ=0
    g23: LineSegment StartX=68 StartY=393.9 StartZ=0 EndX=68 EndY=402.5 EndZ=0
  constraints (60):
    c: Coincident(g0,g1)
    c: Coincident(g1,g2)
    c: Coincident(g2,g3)
    c: Coincident(g3,g0)
    c: Horizontal(g0)
    c: Horizontal(g2)
    c: Vertical(g1)
    c: Vertical(g3)
    c: DistanceY(g1,g1) = 104
    c: DistanceX(g0,g0) = 92
    c: Coincident(g4,g5)
    c: Coincident(g4,g6)
    c: Coincident(g6,g7)
    c: Coincident(g7,g5)
    c: Angle(g7,g5) = 1.5708
    c: Angle(g6,g7) = 1.5708
    c: Angle(g4,g6) = 1.5708
    c: Distance(g4) = 104
    c: Distance(g5) = 92
    c: Coincident(g8,g4)
    c: Vertical(g8)
    c: Angle(g8,g4) = 0.10472
    c: DistanceY(g8,g8) = 100
    c: Horizontal(g9)
    c: Coincident(g10,g9)
    c: Vertical(g10)
    c: Coincident(g11,g9)
    c: Vertical(g11)
    c: Coincident(g5,g12)
    c: Coincident(g4,g13)
    c: Coincident(g13,g14)
    c: Coincident(g14,g12)
    c: Distance(g12) = 8.5541
    c: Distance(g14) = 92.0049
    c: Distance(g13) = 8.50942
    c: Coincident(g4,g15)
    c: Coincident(g16,g6)
    c: Coincident(g17,g16)
    c: Coincident(g17,g15)
    c: Distance(g15) = 8.52543
    c: Distance(g17) = 92.0046
    c: Distance(g16) = 8.50507
    c: Angle(g17,g16) = 1.57171
    c: Angle(g12,g14) = 1.57116
    c: Coincident(g0,g18)
    c: Vertical(g18)
    c: Coincident(g18,g19)
    c: Horizontal(g19)
    c: Coincident(g19,g20)
    c: Coincident(g20,g0)
    c: Vertical(g20)
    c: Coincident(g1,g21)
    c: Vertical(g21)
    c: Coincident(g21,g22)
    c: Horizontal(g22)
    c: Coincident(g22,g23)
    c: Coincident(g23,g2)
    c: Vertical(g23)
    c: DistanceY(g23,g23) = 8.59999
    c: DistanceY(g18,g18) = 8.50001
FEATURE [Sketcher::SketchObject] Sketch025  label="Batt Sleeve Pocket001"
  FullyConstrained = false
  MapMode = 5
  sketch-geometry (6):
    g0: LineSegment StartX=177.5 StartY=70 StartZ=0 EndX=272.5 EndY=70 EndZ=0
    g1: LineSegment StartX=272.5 StartY=70 StartZ=0 EndX=272.5 EndY=200 EndZ=0
    g2: LineSegment StartX=272.5 StartY=200 StartZ=0 EndX=177.5 EndY=200 EndZ=0
    g3: LineSegment StartX=177.5 StartY=200 StartZ=0 EndX=177.5 EndY=70 EndZ=0
    g4: LineSegment StartX=182.5 StartY=460 StartZ=0 EndX=267.5 EndY=460 EndZ=0
    g5: LineSegment StartX=225 StartY=459 StartZ=0 EndX=225 EndY=69 EndZ=0
  constraints (13):
    c: Coincident(g0,g1)
    c: Coincident(g1,g2)
    c: Coincident(g2,g3)
    c: Coincident(g3,g0)
    c: Horizontal(g0)
    c: Horizontal(g2)
    c: Vertical(g1)
    c: Vertical(g3)
    c: DistanceY(g1,g1) = 130
    c: DistanceX(g2,g2) = 95
    c: Horizontal(g4)
    c: DistanceX(g4,g4) = 85
    c: Vertical(g5)
FEATURE [Sketcher::SketchObject] Sketch026  label="RGB Board Pockets001"
  FullyConstrained = false
  MapMode = 5
  Placement = pos=(0,0,45) rot=(0,0,1;0rad)
  Support = -> [Pad001]
  sketch-geometry (12):
    g0: LineSegment StartX=220 StartY=282.3 StartZ=0 EndX=220 EndY=284.3 EndZ=0
    g1: LineSegment StartX=220 StartY=284.3 StartZ=0 EndX=220 EndY=382.3 EndZ=0
    g2: LineSegment StartX=183 StartY=427.9 StartZ=0 EndX=267 EndY=427.9 EndZ=0
    g3: LineSegment StartX=267 StartY=427.9 StartZ=0 EndX=267 EndY=412.9 EndZ=0
    g4: LineSegment StartX=267 StartY=412.9 StartZ=0 EndX=183 EndY=412.9 EndZ=0
    g5: LineSegment StartX=183 StartY=412.9 StartZ=0 EndX=183 EndY=427.9 EndZ=0
    g6: LineSegment StartX=182.5 StartY=460 StartZ=0 EndX=225 EndY=460 EndZ=0
    g7: LineSegment StartX=225 StartY=460 StartZ=0 EndX=225 EndY=244 EndZ=0
    g8: LineSegment StartX=267.5 StartY=441 StartZ=0 EndX=267.5 EndY=400 EndZ=0
    g9: LineSegment StartX=267 StartY=441 StartZ=0 EndX=267 EndY=420.4 EndZ=0
    g10: LineSegment StartX=263.999 StartY=441 StartZ=0 EndX=263.999 EndY=427.9 EndZ=0
    g11: LineSegment StartX=210 StartY=282.3 StartZ=0 EndX=210 EndY=302.3 EndZ=0
  constraints (21):
    c: Vertical(g0)
    c: Coincident(g1,g0)
    c: Vertical(g1)
    c: Coincident(g2,g3)
    c: Coincident(g3,g4)
    c: Coincident(g4,g5)
    c: Coincident(g5,g2)
    c: Horizontal(g2)
    c: Horizontal(g4)
    c: Vertical(g3)
    c: Vertical(g5)
    c: DistanceX(g2,g2) = 84
    c: DistanceY(g5,g5) = 15
    c: Horizontal(g6)
    c: Coincident(g7,g6)
    c: Vertical(g7)
    c: Vertical(g8)
    c: Vertical(g9)
    c: PointOnObject(g10,g2)
    c: Vertical(g10)
    c: Vertical(g11)
FEATURE [Sketcher::SketchObject] Sketch027  label="Speaker hole001"
  FullyConstrained = false
  MapMode = 5
  Placement = pos=(0,0,45) rot=(0,0,1;0rad)
  Support = -> [Pad001]
  sketch-geometry (3):
    g0: Circle CenterX=330 CenterY=121 CenterZ=0 NormalX=0 NormalY=0 NormalZ=1 AngleXU=0 Radius=37
    g1: LineSegment StartX=377 StartY=123.392 StartZ=0 EndX=283 EndY=123.392 EndZ=0
    g2: LineSegment StartX=377 StartY=123.4 StartZ=0 EndX=330 EndY=123.4 EndZ=0
  constraints (4):
    c: Diameter(g0) = 74
    c: Horizontal(g1)
    c: DistanceX(g1,g1) = 94
    c: Horizontal(g2)
FEATURE [Sketcher::SketchObject] Sketch028  label="control plate mount pocket001"
  FullyConstrained = false
  MapMode = 5
  Placement = pos=(0,0,45) rot=(0,0,1;0rad)
  Support = -> [Pad001]
  sketch-geometry (6):
    g0: LineSegment StartX=267.9 StartY=263.3 StartZ=0 EndX=267.9 EndY=243.3 EndZ=0
    g1: LineSegment StartX=267.9 StartY=243.3 StartZ=0 EndX=272.9 EndY=243.3 EndZ=0
    g2: LineSegment StartX=282 StartY=258 StartZ=0 EndX=337 EndY=258 EndZ=0
    g3: LineSegment StartX=282 StartY=258 StartZ=0 EndX=282 EndY=172 EndZ=0
    g4: LineSegment StartX=282 StartY=172 StartZ=0 EndX=365.925 EndY=172 EndZ=0
    g5: LineSegment StartX=365.925 StartY=172 StartZ=0 EndX=337 EndY=258 EndZ=0
  constraints (12):
    c: Vertical(g0)
    c: Coincident(g1,g0)
    c: Horizontal(g1)
    c: Horizontal(g2)
    c: Coincident(g3,g2)
    c: Vertical(g3)
    c: DistanceY(g3,g3) = 86
    c: Coincident(g4,g3)
    c: Horizontal(g4)
    c: Coincident(g5,g4)
    c: Coincident(g5,g2)
    c: Distance(g5) = 90.7339
FEATURE [Sketcher::SketchObject] Sketch029  label="neck pocket001"
  FullyConstrained = false
  MapMode = 5
  Placement = pos=(0,0,45) rot=(0,0,1;0rad)
  Support = -> [Pad001]
  sketch-geometry (8):
    g0: LineSegment StartX=225 StartY=610 StartZ=0 EndX=225 EndY=-10 EndZ=0
    g1: LineSegment StartX=182.5 StartY=460 StartZ=0 EndX=182.5 EndY=469.332 EndZ=0
    g2: LineSegment StartX=182.5 StartY=469.332 StartZ=0 EndX=225 EndY=469.332 EndZ=0
    g3: LineSegment StartX=196.001 StartY=469.332 StartZ=0 EndX=196.001 EndY=545.5 EndZ=0
    g4: ArcOfCircle CenterX=225 CenterY=596.31 CenterZ=0 NormalX=0 NormalY=0 NormalZ=1 AngleXU=0 Radius=127 StartAngle=4.4901 EndAngle=4.93459
    g5: LineSegment StartX=252.988 StartY=472.432 StartZ=0 EndX=252.15 EndY=545.7 EndZ=0
    g6: LineSegment StartX=197.001 StartY=472.435 StartZ=0 EndX=197.8 EndY=545.7 EndZ=0
    g7: LineSegment StartX=197.8 StartY=545.7 StartZ=0 EndX=252.15 EndY=545.7 EndZ=0
  constraints (15):
    c: Vertical(g0)
    c: Vertical(g1)
    c: Coincident(g2,g1)
    c: Horizontal(g2)
    c: PointOnObject(g3,g2)
    c: Vertical(g3)
    c: Radius(g4) = 127
    c: Coincident(g5,g4)
    c: Distance(g5) = 73.2725
    c: Coincident(g6,g4)
    c: Coincident(g7,g6)
    c: Coincident(g7,g5)
    c: Horizontal(g7)
    c: DistanceX(g7,g7) = 54.35
    c: Distance(g6) = 73.2695
FEATURE [Sketcher::SketchObject] Sketch031  label="Body Outline004"
  FullyConstrained = false
  MapMode = 5
  Placement = pos=(0,0,45) rot=(0,0,1;0rad)
  Support = -> [Pad001]
  sketch-geometry (54):
    g0: LineSegment StartX=197.29 StartY=495.3 StartZ=0 EndX=73.9 EndY=550.1 EndZ=0
    g1: LineSegment StartX=252.15 StartY=545.5 StartZ=0 EndX=252.536 EndY=509.5 EndZ=0
    g2: LineSegment StartX=252.536 StartY=509.5 StartZ=0 EndX=349.402 EndY=461.057 EndZ=0
    g3: LineSegment StartX=349.402 StartY=461.057 StartZ=0 EndX=353.186 EndY=456.92 EndZ=0
    g4: LineSegment StartX=353.186 StartY=456.92 StartZ=0 EndX=355.987 EndY=452.42 EndZ=0
    g5: LineSegment StartX=355.987 StartY=452.42 StartZ=0 EndX=355.987 EndY=442.02 EndZ=0
    g6: LineSegment StartX=355.987 StartY=442.02 StartZ=0 EndX=320 EndY=343.5 EndZ=0
    g7: LineSegment StartX=320 StartY=343.5 StartZ=0 EndX=320 EndY=331.5 EndZ=0
    g8: LineSegment StartX=195.596 StartY=533.25 StartZ=0 EndX=190.601 EndY=530.784 EndZ=0
    g9: LineSegment StartX=190.601 StartY=530.784 StartZ=0 EndX=185.731 EndY=530.784 EndZ=0
    g10: LineSegment StartX=185.731 StartY=530.784 StartZ=0 EndX=184.499 EndY=530.912 EndZ=0
    g11: LineSegment StartX=184.499 StartY=530.912 StartZ=0 EndX=97.9865 EndY=587.073 EndZ=0
    g12: LineSegment StartX=97.9865 StartY=587.073 StartZ=0 EndX=91.1348 EndY=587.073 EndZ=0
    g13: LineSegment StartX=91.1348 StartY=587.073 StartZ=0 EndX=89.4748 EndY=585.83 EndZ=0
    g14: LineSegment StartX=89.4748 StartY=585.83 StartZ=0 EndX=87.4848 EndY=583.86 EndZ=0
    g15: LineSegment StartX=87.4848 StartY=583.86 StartZ=0 EndX=85.9748 EndY=581.98 EndZ=0
    g16: LineSegment StartX=107.659 StartY=357.048 StartZ=0 EndX=122.894 EndY=344.497 EndZ=0
    g17: LineSegment StartX=122.894 StartY=344.497 StartZ=0 EndX=130.394 EndY=322.397 EndZ=0
    g18: LineSegment StartX=130.394 StartY=322.397 StartZ=0 EndX=130.394 EndY=310.397 EndZ=0
    g19: LineSegment StartX=130.394 StartY=310.397 StartZ=0 EndX=128.394 EndY=307.697 EndZ=0
    g20: LineSegment StartX=128.394 StartY=307.697 StartZ=0 EndX=44.2002 EndY=150.2 EndZ=0
    g21: LineSegment StartX=44.2002 StartY=150.2 StartZ=0 EndX=44.2002 EndY=148.6 EndZ=0
    g22: LineSegment StartX=44.2002 StartY=148.6 StartZ=0 EndX=44.2002 EndY=144.6 EndZ=0
    g23: LineSegment StartX=44.2002 StartY=144.6 StartZ=0 EndX=45.1102 EndY=141.95 EndZ=0
    g24: LineSegment StartX=45.1102 StartY=141.95 StartZ=0 EndX=47.2242 EndY=138.987 EndZ=0
    g25: LineSegment StartX=47.2242 StartY=138.987 StartZ=0 EndX=50.9702 EndY=135.84 EndZ=0
    g26: LineSegment StartX=413.447 StartY=50.3962 StartZ=0 EndX=410.947 EndY=46.6962 EndZ=0
    g27: LineSegment StartX=410.947 StartY=46.6962 StartZ=0 EndX=408.821 EndY=43.4657 EndZ=0
    g28: LineSegment StartX=408.821 StartY=43.4657 StartZ=0 EndX=403.447 EndY=43.4657 EndZ=0
    g29: LineSegment StartX=403.447 StartY=43.4657 StartZ=0 EndX=320.445 EndY=66.6106 EndZ=0
    g30: LineSegment StartX=320.445 StartY=66.6106 StartZ=0 EndX=290 EndY=70.0001 EndZ=0
    g31: LineSegment StartX=290 StartY=70.0001 StartZ=0 EndX=160 EndY=70.0001 EndZ=0
    g32: LineSegment StartX=160 StartY=70.0001 StartZ=0 EndX=50.9702 EndY=135.84 EndZ=0
    g33: LineSegment StartX=252.15 StartY=545.5 StartZ=0 EndX=197.848 EndY=545.5 EndZ=0
    g34: LineSegment StartX=197.848 StartY=545.5 StartZ=0 EndX=197.726 EndY=534.521 EndZ=0
    g35: LineSegment StartX=197.726 StartY=534.521 StartZ=0 EndX=195.596 EndY=533.25 EndZ=0
    g36: LineSegment StartX=107.659 StartY=357.048 StartZ=0 EndX=96.1282 EndY=362.119 EndZ=0
    g37: LineSegment StartX=96.1282 StartY=362.119 StartZ=0 EndX=64 EndY=377 EndZ=0
    g38: LineSegment StartX=64 StartY=377 StartZ=0 EndX=61 EndY=378.8 EndZ=0
    g39: LineSegment StartX=61 StartY=378.8 StartZ=0 EndX=56.5 EndY=383.7 EndZ=0
    g40: LineSegment StartX=56.5 StartY=383.7 StartZ=0 EndX=54 EndY=388 EndZ=0
    g41: LineSegment StartX=54 StartY=388 StartZ=0 EndX=52.6 EndY=392 EndZ=0
    g42: LineSegment StartX=52.6 StartY=392 StartZ=0 EndX=52.6 EndY=529.8 EndZ=0
    g43: LineSegment StartX=52.6 StartY=529.8 StartZ=0 EndX=54 EndY=534 EndZ=0
    g44: LineSegment StartX=54 StartY=534 StartZ=0 EndX=57 EndY=538 EndZ=0
    g45: LineSegment StartX=57 StartY=538 StartZ=0 EndX=85.9748 EndY=581.98 EndZ=0
    g46: LineSegment StartX=413.447 StartY=50.3962 StartZ=0 EndX=413.447 EndY=57.5962 EndZ=0
    g47: LineSegment StartX=-1 StartY=616 StartZ=0 EndX=451 EndY=616 EndZ=0
    g48: LineSegment StartX=451 StartY=616 StartZ=0 EndX=451 EndY=14 EndZ=0
    g49: LineSegment StartX=451 StartY=14 StartZ=0 EndX=-1 EndY=14 EndZ=0
    g50: LineSegment StartX=-1 StartY=14 StartZ=0 EndX=-1 EndY=616 EndZ=0
    g51: LineSegment StartX=257 StartY=545.5 StartZ=0 EndX=257 EndY=245.424 EndZ=0
    g52: LineSegment StartX=320 StartY=331.5 StartZ=0 EndX=413.447 EndY=57.5962 EndZ=0
    g53: LineSegment StartX=320 StartY=331.5 StartZ=0 EndX=127.305 EndY=331.5 EndZ=0
  constraints (149):
    c: Coincident(g1,g2)
    c: Coincident(g2,g3)
    c: Coincident(g3,g4)
    c: Coincident(g4,g5)
    c: Vertical(g5)
    c: Coincident(g6,g5)
    c: Coincident(g7,g6)
    c: Vertical(g7)
    c: Coincident(g8,g9)
    c: Horizontal(g9)
    c: Coincident(g9,g10)
    c: Coincident(g10,g11)
    c: Distance(g10) = 1.23908
    c: Distance(g8) = 5.57001
    c: DistanceX(g9,g9) = 4.86999
    c: Coincident(g12,g11)
    c: Horizontal(g12)
    c: Coincident(g13,g12)
    c: Coincident(g13,g14)
    c: Coincident(g14,g15)
    c: Coincident(g16,g17)
    c: Coincident(g17,g18)
    c: Vertical(g18)
    c: Coincident(g19,g18)
    c: Coincident(g20,g19)
    c: Coincident(g21,g20)
    c: Vertical(g21)
    c: Coincident(g21,g22)
    c: Vertical(g22)
    c: Coincident(g22,g23)
    c: Coincident(g23,g24)
    c: Coincident(g24,g25)
    c: Coincident(g27,g26)
    c: Coincident(g28,g27)
    c: Horizontal(g28)
    c: DistanceX(g28,g28) = 5.37372
    c: Distance(g26) = 4.46542
    c: Distance(g27) = 3.86749
    c: Coincident(g29,g28)
    c: DistanceY(g7,g7) = 12
    c: DistanceY(g5,g5) = 10.4
    c: Distance(g4) = 5.3
    c: Distance(g3) = 5.60673
    c: Distance(g1) = 36.0023
    c: Distance(g15) = 2.41133
    c: Distance(g14) = 2.80018
    c: Distance(g13) = 2.07357
    c: DistanceX(g12,g12) = 6.85172
    c: Distance(g16) = 19.7388
    c: Distance(g17) = 23.3379
    c: DistanceY(g18,g18) = 12
    c: DistanceY(g21,g21) = 1.6
    c: DistanceY(g22,g22) = 4
    c: Distance(g23) = 2.8019
    c: Distance(g24) = 3.63982
    c: Distance(g25) = 4.89246
    c: Angle(g23,g22) = 2.81082
    c: Angle(g24,g22) = 2.52188
    c: Angle(g25,g22) = 2.26951
    c: Angle(g18,g19) = 2.50404
    c: Angle(g17,g18) = 2.81442
    c: Coincident(g30,g29)
    c: Coincident(g31,g30)
    c: Horizontal(g31)
    c: Coincident(g32,g31)
    c: Coincident(g32,g25)
    c: Distance(g30) = 30.6334
    c: Angle(g30,g28) = 0.110874
    c: DistanceX(g31,g31) = 130
    c: Distance(g32) = 127.367
    c: Coincident(g1,g33)
    c: Horizontal(g33)
    c: Coincident(g33,g34)
    c: Coincident(g35,g34)
    c: Coincident(g35,g8)
    c: Distance(g35) = 2.4804
    c: Angle(g13,g12) = 2.49901
    c: Angle(g14,g12) = 2.36124
    c: Angle(g15,g12) = 2.24748
    c: Angle(g34,g35) = 2.11973
    c: Angle(g34,g8) = 2.04062
    c: Angle(g34,g9) = 1.58195
    c: Angle(g9,g10) = 3.03808
    c: Angle(g31,g32) = 2.59833
    c: Coincident(g16,g36)
    c: Coincident(g36,g37)
    c: Coincident(g37,g38)
    c: Coincident(g38,g39)
    c: Coincident(g39,g40)
    c: Coincident(g40,g41)
    c: Coincident(g41,g42)
    c: Vertical(g42)
    c: Coincident(g42,g43)
    c: Coincident(g43,g44)
    c: Coincident(g45,g15)
    c: Distance(g36) = 12.5968
    c: Distance(g37) = 35.4072
    c: Distance(g38) = 3.49857
    c: Distance(g39) = 6.65282
    c: Distance(g40) = 4.97393
    c: Distance(g41) = 4.23793
    c: DistanceY(g42,g42) = 137.8
    c: Angle(g16,g17) = 2.58706
    c: Angle(g36,g16) = 2.86681
    c: Angle(g36,g37) = 3.12214
    c: Angle(g37,g38) = 3.03493
    c: Angle(g38,g39) = 2.85409
    c: Angle(g39,g40) = 2.92535
    c: Angle(g40,g41) = 2.95164
    c: Angle(g42,g43) = 2.81984
    c: Angle(g42,g44) = 2.49809
    c: Angle(g33,g1) = 1.58154
    c: Distance(g34) = 10.9802
    c: Distance(g45) = 52.6666
    c: Distance(g44) = 5
    c: Distance(g43) = 4.42719
    c: Distance(g11) = 103.143
    c: Coincident(g44,g45)
    c: Coincident(g46,g26)
    c: Vertical(g46)
    c: Distance(g46) = 7.20003
    c: Angle(g46,g26) = 2.54737
    c: Coincident(g47,g48)
    c: Coincident(g48,g49)
    c: Coincident(g49,g50)
    c: Coincident(g50,g47)
    c: Horizontal(g47)
    c: Horizontal(g49)
    c: Vertical(g48)
    c: Vertical(g50)
    c: DistanceY(g48,g48) = 602
    c: DistanceX(g49,g49) = 452
    c: Vertical(g51)
    c: Coincident(g52,g7)
    c: Coincident(g52,g46)
    c: Angle(g27,g28) = 2.1529
    c: Angle(g4,g5) = 2.58482
    c: Angle(g3,g5) = 2.40074
    c: Distance(g2) = 108.304
    c: Angle(g2,g5) = 2.03453
    c: Angle(g28,g29) = 2.86965
    c: DistanceX(g33,g33) = 54.3011
    c: Angle(g21,g20) = 2.65067
    c: Distance(g20) = 178.589
    c: Distance(g19) = 3.36006
    c: Coincident(g53,g7)
    c: PointOnObject(g53,g17)
    c: Horizontal(g53)
    c: DistanceX(g53,g53) = 192.695
FEATURE [Sketcher::SketchObject] Sketch032  label="speaker grill recess001"
  FullyConstrained = false
  MapMode = 5
  Placement = pos=(0,0,45) rot=(0,0,1;0rad)
  Support = -> [Pad001]
  sketch-geometry (1):
    g0: Circle CenterX=330 CenterY=121 CenterZ=0 NormalX=0 NormalY=0 NormalZ=1 AngleXU=0 Radius=47
  constraints (1):
    c: Diameter(g0) = 94
FEATURE [Sketcher::SketchObject] Sketch033  label="Red Stripe outline001"
  FullyConstrained = false
  MapMode = 5
  Placement = pos=(0,0,45) rot=(0,0,1;0rad)
  Support = -> [Pad001]
  sketch-geometry (41):
    g0: LineSegment StartX=170 StartY=70 StartZ=0 EndX=280 EndY=70 EndZ=0
    g1: LineSegment StartX=170 StartY=540 StartZ=0 EndX=170 EndY=70 EndZ=0
    g2: LineSegment StartX=189.9 StartY=282.3 StartZ=0 EndX=267.9 EndY=282.3 EndZ=0
    g3: LineSegment StartX=267.9 StartY=282.3 StartZ=0 EndX=267.9 EndY=263.3 EndZ=0
    g4: LineSegment StartX=267.9 StartY=263.3 StartZ=0 EndX=189.9 EndY=263.3 EndZ=0
    g5: LineSegment StartX=189.9 StartY=263.3 StartZ=0 EndX=189.9 EndY=282.3 EndZ=0
    g6: LineSegment StartX=188.75 StartY=357.8 StartZ=0 EndX=261.25 EndY=357.8 EndZ=0
    g7: LineSegment StartX=261.25 StartY=357.8 StartZ=0 EndX=261.25 EndY=347.8 EndZ=0
    g8: LineSegment StartX=261.25 StartY=347.8 StartZ=0 EndX=269.25 EndY=347.8 EndZ=0
    g9: LineSegment StartX=269.25 StartY=347.8 StartZ=0 EndX=269.25 EndY=327.8 EndZ=0
    g10: LineSegment StartX=269.25 StartY=327.8 StartZ=0 EndX=261.25 EndY=327.8 EndZ=0
    g11: LineSegment StartX=261.25 StartY=327.8 StartZ=0 EndX=261.25 EndY=317.8 EndZ=0
    g12: LineSegment StartX=261.25 StartY=317.8 StartZ=0 EndX=188.75 EndY=317.8 EndZ=0
    g13: LineSegment StartX=188.75 StartY=317.8 StartZ=0 EndX=188.75 EndY=327.8 EndZ=0
    g14: LineSegment StartX=188.75 StartY=327.8 StartZ=0 EndX=180.75 EndY=327.8 EndZ=0
    g15: LineSegment StartX=180.75 StartY=327.8 StartZ=0 EndX=180.75 EndY=347.8 EndZ=0
    g16: LineSegment StartX=180.75 StartY=347.8 StartZ=0 EndX=188.75 EndY=347.8 EndZ=0
    g17: LineSegment StartX=188.75 StartY=347.8 StartZ=0 EndX=188.75 EndY=357.8 EndZ=0
    g18: LineSegment StartX=182.5 StartY=381 StartZ=0 EndX=182.5 EndY=400 EndZ=0
    g19: LineSegment StartX=182.5 StartY=400 StartZ=0 EndX=267.5 EndY=400 EndZ=0
    g20: LineSegment StartX=267.5 StartY=400 StartZ=0 EndX=267.5 EndY=381 EndZ=0
    g21: LineSegment StartX=267.5 StartY=381 StartZ=0 EndX=182.5 EndY=381 EndZ=0
    g22: LineSegment StartX=178 StartY=430.5 StartZ=0 EndX=178 EndY=410.5 EndZ=0
    g23: LineSegment StartX=178 StartY=410.5 StartZ=0 EndX=272 EndY=410.5 EndZ=0
    g24: LineSegment StartX=272 StartY=410.5 StartZ=0 EndX=272 EndY=430.5 EndZ=0
    g25: LineSegment StartX=272 StartY=430.5 StartZ=0 EndX=178 EndY=430.5 EndZ=0
    g26: LineSegment StartX=182.5 StartY=460 StartZ=0 EndX=267.5 EndY=460 EndZ=0
    g27: LineSegment StartX=267.5 StartY=460 StartZ=0 EndX=267.5 EndY=441 EndZ=0
    g28: LineSegment StartX=267.5 StartY=441 StartZ=0 EndX=182.5 EndY=441 EndZ=0
    g29: LineSegment StartX=182.5 StartY=441 StartZ=0 EndX=182.5 EndY=460 EndZ=0
    g30: LineSegment StartX=280 StartY=70 StartZ=0 EndX=280 EndY=495.759 EndZ=0
    g31: LineSegment StartX=280 StartY=495.759 StartZ=0 EndX=252.536 EndY=509.5 EndZ=0
    g32: LineSegment StartX=197.726 StartY=534.521 StartZ=0 EndX=195.6 EndY=533.253 EndZ=0
    g33: LineSegment StartX=195.6 StartY=533.253 StartZ=0 EndX=190.601 EndY=530.784 EndZ=0
    g34: LineSegment StartX=190.601 StartY=530.784 StartZ=0 EndX=185.73 EndY=530.784 EndZ=0
    g35: LineSegment StartX=185.73 StartY=530.784 StartZ=0 EndX=184.499 EndY=530.912 EndZ=0
    g36: LineSegment StartX=184.499 StartY=530.912 StartZ=0 EndX=170 EndY=540.325 EndZ=0
    g37: LineSegment StartX=170 StartY=540.325 StartZ=0 EndX=170 EndY=540 EndZ=0
    g38: LineSegment StartX=197.726 StartY=534.521 StartZ=0 EndX=196.975 EndY=469.3 EndZ=0
    g39: LineSegment StartX=196.975 StartY=469.3 StartZ=0 EndX=252.975 EndY=469.3 EndZ=0
    g40: LineSegment StartX=252.975 StartY=469.3 StartZ=0 EndX=252.536 EndY=509.5 EndZ=0
  constraints (74):
    c: Coincident(g1,g0)
    c: Horizontal(g0)
    c: Vertical(g1)
    c: Coincident(g2,g3)
    c: Coincident(g3,g4)
    c: Coincident(g4,g5)
    c: Coincident(g5,g2)
    c: Horizontal(g2)
    c: Horizontal(g4)
    c: Vertical(g3)
    c: Vertical(g5)
    c: Horizontal(g6)
    c: Coincident(g6,g7)
    c: Vertical(g7)
    c: Coincident(g7,g8)
    c: Horizontal(g8)
    c: Coincident(g8,g9)
    c: Vertical(g9)
    c: Coincident(g9,g10)
    c: Horizontal(g10)
    c: Coincident(g10,g11)
    c: Vertical(g11)
    c: Coincident(g11,g12)
    c: Horizontal(g12)
    c: Coincident(g12,g13)
    c: Vertical(g13)
    c: Coincident(g13,g14)
    c: Horizontal(g14)
    c: Coincident(g14,g15)
    c: Vertical(g15)
    c: Coincident(g15,g16)
    c: Horizontal(g16)
    c: Coincident(g16,g17)
    c: Coincident(g17,g6)
    c: Vertical(g17)
    c: Vertical(g18)
    c: Coincident(g18,g19)
    c: Horizontal(g19)
    c: Coincident(g19,g20)
    c: Vertical(g20)
    c: Coincident(g20,g21)
    c: Coincident(g21,g18)
    c: Horizontal(g21)
    c: Vertical(g22)
    c: Coincident(g22,g23)
    c: Horizontal(g23)
    c: Coincident(g23,g24)
    c: Vertical(g24)
    c: Coincident(g24,g25)
    c: Coincident(g25,g22)
    c: Horizontal(g25)
    c: Horizontal(g26)
    c: Coincident(g26,g27)
    c: Vertical(g27)
    c: Coincident(g27,g28)
    c: Horizontal(g28)
    c: Coincident(g28,g29)
    c: Coincident(g29,g26)
    c: Vertical(g29)
    c: Coincident(g0,g30)
    c: Vertical(g30)
    c: Coincident(g30,g31)
    c: Coincident(g32,g33)
    c: Coincident(g33,g34)
    c: Horizontal(g34)
    c: Coincident(g34,g35)
    c: Coincident(g35,g36)
    c: Coincident(g36,g37)
    c: Coincident(g37,g1)
    c: Vertical(g37)
    c: Coincident(g32,g38)
    c: Coincident(g38,g39)
    c: Horizontal(g39)
    c: Coincident(g39,g40)
FEATURE [Sketcher::SketchObject] Sketch034  label="AFPI Mount Pocket001"
  FullyConstrained = false
  MapMode = 5
  Placement = pos=(0,0,45) rot=(0,0,1;0rad)
  Support = -> [Pad001]
  sketch-geometry (4):
    g0: LineSegment StartX=68 StartY=514 StartZ=0 EndX=160 EndY=514 EndZ=0
    g1: LineSegment StartX=160 StartY=514 StartZ=0 EndX=160 EndY=395 EndZ=0
    g2: LineSegment StartX=160 StartY=395 StartZ=0 EndX=68 EndY=395 EndZ=0
    g3: LineSegment StartX=68 StartY=395 StartZ=0 EndX=68 EndY=514 EndZ=0
  constraints (10):
    c: Coincident(g0,g1)
    c: Coincident(g1,g2)
    c: Coincident(g2,g3)
    c: Coincident(g3,g0)
    c: Horizontal(g0)
    c: Horizontal(g2)
    c: Vertical(g1)
    c: Vertical(g3)
    c: DistanceY(g1,g1) = 119
    c: DistanceX(g0,g0) = 92
FEATURE [Sketcher::SketchObject] Sketch035  label="Pickup Controls layouts001"
  FullyConstrained = false
  MapMode = 5
  Placement = pos=(0,0,45) rot=(0,0,1;0rad)
  Support = -> [Pad001]
  sketch-geometry (7):
    g0: Circle CenterX=302 CenterY=230 CenterZ=0 NormalX=0 NormalY=0 NormalZ=1 AngleXU=0 Radius=8.5
    g1: Circle CenterX=302 CenterY=200 CenterZ=0 NormalX=0 NormalY=0 NormalZ=1 AngleXU=0 Radius=8.5
    g2: LineSegment StartX=316.216 StartY=240.209 StartZ=0 EndX=326.216 EndY=240.209 EndZ=0
    g3: LineSegment StartX=326.216 StartY=240.209 StartZ=0 EndX=341.048 EndY=194.558 EndZ=0
    g4: LineSegment StartX=341.048 StartY=194.558 StartZ=0 EndX=330.587 EndY=191.159 EndZ=0
    g5: LineSegment StartX=326.216 StartY=240.209 StartZ=0 EndX=315.754 EndY=236.809 EndZ=0
    g6: LineSegment StartX=315.754 StartY=236.809 StartZ=0 EndX=330.587 EndY=191.159 EndZ=0
  constraints (15):
    c: Diameter(g0) = 17
    c: Diameter(g1) = 17
    c: Horizontal(g2)
    c: Coincident(g3,g2)
    c: DistanceX(g2,g2) = 10
    c: Angle(g2,g3) = 1.88496
    c: Distance(g3) = 48
    c: Coincident(g4,g3)
    c: Angle(g3,g4) = 1.5708
    c: Distance(g4) = 11
    c: Coincident(g5,g3)
    c: Angle(g5,g3) = 1.5708
    c: Coincident(g6,g5)
    c: Coincident(g6,g4)
    c: Distance(g5) = 11
FEATURE [Sketcher::SketchObject] Sketch036  label="RGB clear plate pocket001"
  FullyConstrained = false
  MapMode = 5
  Placement = pos=(0,0,45) rot=(0,0,1;0rad)
  Support = -> [Pad001]
  sketch-geometry (4):
    g0: LineSegment StartX=178 StartY=430.5 StartZ=0 EndX=272 EndY=430.5 EndZ=0
    g1: LineSegment StartX=272 StartY=430.5 StartZ=0 EndX=272 EndY=410.5 EndZ=0
    g2: LineSegment StartX=272 StartY=410.5 StartZ=0 EndX=178 EndY=410.5 EndZ=0
    g3: LineSegment StartX=178 StartY=410.5 StartZ=0 EndX=178 EndY=430.5 EndZ=0
  constraints (10):
    c: Coincident(g0,g1)
    c: Coincident(g1,g2)
    c: Coincident(g2,g3)
    c: Coincident(g3,g0)
    c: Horizontal(g0)
    c: Horizontal(g2)
    c: Vertical(g1)
    c: Vertical(g3)
    c: DistanceY(g3,g3) = 20
    c: DistanceX(g0,g0) = 94
FEATURE [PartDesign::Pocket] Pocket  label="Body Cutout"
  BaseFeature = -> Pad001
  Direction = (0,0,-1)
  Length = 45
  Length2 = 5
  Profile = -> Sketch031
  ReferenceAxis = -> Sketch031 [N_Axis]
  Type = 0
FEATURE [Sketcher::SketchObject] Sketch010  label="neck pocket"
  FullyConstrained = false
  MapMode = 5
  Placement = pos=(0,0,45) rot=(0,0,1;0rad)
  Support = -> [Pocket]
  sketch-geometry (8):
    g0: LineSegment StartX=225 StartY=610 StartZ=0 EndX=225 EndY=-10 EndZ=0
    g1: LineSegment StartX=182.5 StartY=460 StartZ=0 EndX=182.5 EndY=469.3 EndZ=0
    g2: LineSegment StartX=182.5 StartY=469.3 StartZ=0 EndX=223 EndY=469.3 EndZ=0
    g3: LineSegment StartX=253 StartY=469.3 StartZ=0 EndX=197 EndY=469.3 EndZ=0
    g4: LineSegment StartX=196.001 StartY=469.3 StartZ=0 EndX=196.001 EndY=545.5 EndZ=0
    g5: LineSegment StartX=252.15 StartY=545.5 StartZ=0 EndX=197.85 EndY=545.5 EndZ=0
    g6: LineSegment StartX=197 StartY=469.3 StartZ=0 EndX=197.85 EndY=545.5 EndZ=0
    g7: LineSegment StartX=253 StartY=469.3 StartZ=0 EndX=252.15 EndY=545.5 EndZ=0
  constraints (14):
    c: Vertical(g0)
    c: Vertical(g1)
    c: Coincident(g2,g1)
    c: Horizontal(g2)
    c: Horizontal(g3)
    c: DistanceX(g3,g3) = 56
    c: PointOnObject(g4,g2)
    c: Vertical(g4)
    c: Horizontal(g5)
    c: DistanceX(g5,g5) = 54.3
    c: Coincident(g6,g3)
    c: Distance(g6) = 76.2047
    c: Coincident(g7,g3)
    c: Distance(g7) = 76.2047
FEATURE [PartDesign::Pocket] Pocket001  label="Neck Pocket"
  BaseFeature = -> Pocket
  Direction = (0,0,-1)
  Length = 20
  Length2 = 5
  Profile = -> Sketch029
  ReferenceAxis = -> Sketch029 [N_Axis]
  Type = 0
FEATURE [PartDesign::Pocket] Pocket002  label="Speaker magnet hole"
  BaseFeature = -> Pocket001
  Direction = (0,0,-1)
  Length = 45
  Length2 = 5
  Profile = -> Sketch027
  ReferenceAxis = -> Sketch027 [N_Axis]
  Type = 0
FEATURE [PartDesign::Pocket] Pocket003  label="Tremelo Pocket"
  BaseFeature = -> Pocket002
  Direction = (0,0,-1)
  Length = 6
  Length2 = 5
  Profile = -> Sketch022
  ReferenceAxis = -> Sketch022 [N_Axis]
  Type = 0
FEATURE [PartDesign::Pocket] Pocket004  label="AFPI Main body Pocket"
  BaseFeature = -> Pocket003
  Direction = (0,0,-1)
  Length = 45
  Length2 = 5
  Profile = -> Sketch024
  ReferenceAxis = -> Sketch024 [N_Axis]
  Type = 0
FEATURE [PartDesign::Pocket] Pocket005  label="AFPI body mount"
  BaseFeature = -> Pocket004
  Direction = (0,0,-1)
  Length = 5.5
  Length2 = 5
  Profile = -> Sketch034
  ReferenceAxis = -> Sketch034 [N_Axis]
  Type = 0
FEATURE [PartDesign::Pocket] Pocket006  label="Control Pocket"
  BaseFeature = -> Pocket005
  Direction = (0,0,-1)
  Length = 36
  Length2 = 5
  Profile = -> Sketch023
  ReferenceAxis = -> Sketch023 [N_Axis]
  Type = 0
FEATURE [PartDesign::Pocket] Pocket007  label="Control plate pocket"
  BaseFeature = -> Pocket006
  Direction = (0,0,-1)
  Length = 3
  Length2 = 5
  Profile = -> Sketch028
  ReferenceAxis = -> Sketch028 [N_Axis]
  Type = 0
FEATURE [Sketcher::SketchObject] Sketch006  label="Batt Sleeve Pocket"
  FullyConstrained = false
  MapMode = 5
  Placement = pos=(0,0,0) rot=(1,0,0;3.14159rad)
  Support = -> [Pocket007]
  sketch-geometry (6):
    g0: LineSegment StartX=177.5 StartY=70 StartZ=0 EndX=272.5 EndY=70 EndZ=0
    g1: LineSegment StartX=272.5 StartY=70 StartZ=0 EndX=272.5 EndY=200 EndZ=0
    g2: LineSegment StartX=272.5 StartY=200 StartZ=0 EndX=177.5 EndY=200 EndZ=0
    g3: LineSegment StartX=177.5 StartY=200 StartZ=0 EndX=177.5 EndY=70 EndZ=0
    g4: LineSegment StartX=182.5 StartY=460 StartZ=0 EndX=267.5 EndY=460 EndZ=0
    g5: LineSegment StartX=225 StartY=459 StartZ=0 EndX=225 EndY=69 EndZ=0
  constraints (13):
    c: Coincident(g0,g1)
    c: Coincident(g1,g2)
    c: Coincident(g2,g3)
    c: Coincident(g3,g0)
    c: Horizontal(g0)
    c: Horizontal(g2)
    c: Vertical(g1)
    c: Vertical(g3)
    c: DistanceY(g1,g1) = 130
    c: DistanceX(g2,g2) = 95
    c: Horizontal(g4)
    c: DistanceX(g4,g4) = 85
    c: Vertical(g5)
FEATURE [PartDesign::Body] Body  label="Body Template and outlines"
  Group = -> [Sketch,Sketch001,Sketch002,Sketch003,Sketch004,Sketch005,Sketch006,Sketch007,Sketch008,Sketch009,Sketch010,Sketch011,Pad,Sketch013,Sketch014,Sketch015,Sketch016,Sketch017,Sketch018]
  Origin = -> Origin
  Tip = -> Pad
FEATURE [PartDesign::Pocket] Pocket008  label="Battery Sleeve Pocket"
  BaseFeature = -> Pocket007
  Direction = (0,0,-1)
  Length = 28.5
  Length2 = 5
  Profile = -> Sketch025
  ReferenceAxis = -> Sketch025 [N_Axis]
  Reversed = true
  Type = 0
FEATURE [Part::Extrusion] Extrude001  label="painted Red Stripe"
  Base = -> Sketch033
  Dir = (0,0,1)
  DirMode = 2
  FaceMakerClass = Part::FaceMakerBullseye
  LengthFwd = 0
  LengthRev = 0
  Solid = true
  Symmetric = false
FEATURE [PartDesign::Pocket] Pocket009  label="pickup pockets"
  BaseFeature = -> Pocket008
  Direction = (0,0,-1)
  Length = 24
  Length2 = 5
  Profile = -> Sketch021
  ReferenceAxis = -> Sketch021 [N_Axis]
  Type = 0
FEATURE [PartDesign::Pocket] Pocket010  label="RGB Board Pocket"
  BaseFeature = -> Pocket009
  Direction = (0,0,-1)
  Length = 22
  Length2 = 5
  Profile = -> Sketch026
  ReferenceAxis = -> Sketch026 [N_Axis]
  Type = 0
FEATURE [PartDesign::Pocket] Pocket011  label="Speaker Grill Pocket"
  BaseFeature = -> Pocket010
  Direction = (0,0,-1)
  Length = 2
  Length2 = 5
  Profile = -> Sketch032
  ReferenceAxis = -> Sketch032 [N_Axis]
  Type = 0
FEATURE [PartDesign::Pocket] Pocket012  label="RGB Clear Plate Pocket"
  BaseFeature = -> Pocket011
  Direction = (0,0,-1)
  Length = 1.8
  Length2 = 5
  Profile = -> Sketch036
  ReferenceAxis = -> Sketch036 [N_Axis]
  Type = 0
FEATURE [App::Part] Part  label="Guitar Body Template"
  Group = -> [Body]
  Origin = -> Origin002
FEATURE [PartDesign::FeatureBase] BaseFeature002  label="centre walling"
FEATURE [PartDesign::FeatureBase] BaseFeature003
FEATURE [PartDesign::Body] Body002  label="OLED SCREEN"
  Origin = -> Origin007
FEATURE [App::MeasureDistance] Distance  label="Distance: 73.45 mm"
  Distance = 73.4508
  P1 = (-13.0946,110.772,1.2)
  P2 = (-12.7297,37.41,-2.4)
FEATURE [App::MeasureDistance] Distance001  label="Distance: 90.28 mm"
  Distance = 90.2836
  P1 = (-30.0421,47.8754,4.2)
  P2 = (60,47.8975,-2.4)
FEATURE [App::MeasureDistance] Distance002  label="Distance: 29.15 mm"
  Distance = 29.1515
  P1 = (-9.36148,64.9754,1.2)
  P2 = (-9.65197,64.9277,-27.95)
FEATURE [App::MeasureDistance] Distance003  label="Distance: 1.60 mm"
  Distance = 1.60068
  P1 = (59.543,51.023,-30.6)
  P2 = (59.4962,51.023,-32.2)
FEATURE [App::MeasureDistance] Distance004  label="Distance: 10.32 mm"
  Distance = 10.324
  P1 = (48.0802,57.404,-30.4)
  P2 = (47.9984,57.9005,-20.0883)
FEATURE [App::MeasureDistance] Distance005  label="Distance: 6.87 mm"
  Distance = 6.87486
  P1 = (29.3003,61.567,-32.3751)
  P2 = (29.287,61.567,-39.25)
FEATURE [App::MeasureDistance] Distance006  label="Distance: 44.99 mm"
  Distance = 44.9895
  P1 = (-36.4,26.58,-44.9895)
  P2 = (-36.4,26.58,0)
FEATURE [App::MeasureDistance] Distance007  label="Distance: 84.96 mm"
  Distance = 84.959
  P1 = (-33.3675,114.27,-45)
  P2 = (-33.45,29.3107,-45)
FEATURE [App::MeasureDistance] Distance008  label="Distance: 96.93 mm"
  Distance = 96.9292
  P1 = (-33.3792,29.203,-45)
  P2 = (63.55,29.203,-45)
FEATURE [App::MeasureDistance] Distance009  label="Distance: 101.69 mm"
  Distance = 101.69
  P1 = (-35.6401,26.9804,-45)
  P2 = (66.05,26.7738,-45)
FEATURE [App::MeasureDistance] Distance010  label="Distance: 89.52 mm"
  Distance = 89.5204
  P1 = (-35.95,116.705,-45)
  P2 = (-35.4239,27.1861,-45)
FEATURE [App::MeasureDistance] Distance011  label="Distance: 124.21 mm"
  Distance = 124.207
  P1 = (77.3519,24.8322,2.2)
  P2 = (-46.8546,24.4842,2.2)
FEATURE [App::MeasureDistance] Distance012  label="Distance: 97.00 mm"
  Distance = 97
  P1 = (63.55,114.203,0)
  P2 = (-33.45,114.203,0)
FEATURE [App::MeasureDistance] Distance013  label="Distance: 3.95 mm"
  Distance = 3.95392
  P1 = (-21.5031,94.2803,-30.6)
  P2 = (-25.457,94.2578,-30.6)
FEATURE [App::MeasureDistance] Distance014  label="Distance: 2.64 mm"
  Distance = 2.6442
  P1 = (-17.6786,58.6345,-26.3)
  P2 = (-19.125,58.5074,-28.5098)
FEATURE [App::MeasureDistance] Distance015  label="Distance: 21.17 mm"
  Distance = 21.1653
  P1 = (63.4222,50.3697,-26.8)
  P2 = (63.55,29.2224,-27.6637)
FEATURE [App::MeasureDistance] Distance016  label="Distance: 17.28 mm"
  Distance = 17.2787
  P1 = (63.5047,96.965,-26.8)
  P2 = (62.3428,114.203,-26.5675)
FEATURE [App::MeasureDistance] Distance017  label="Distance: 29.49 mm"
  Distance = 29.4907
  P1 = (63.4734,88.365,-26.8)
  P2 = (63.53,58.8744,-26.8)
FEATURE [App::MeasureDistance] Distance018  label="Distance: 2.93 mm"
  Distance = 2.93101
  P1 = (-35.9205,26.6266,2.2)
  P2 = (-35.7592,23.7,2.2)
FEATURE [App::Part] Part007  label="AFPI Board"
  Group = -> [Distance005,Distance004,Distance003]
  Origin = -> Origin067
FEATURE [App::Part] Part009  label="Comp Placements"
  Group = -> [Distance001,Distance,Distance002]
  Origin = -> Origin069
FEATURE [App::Part] Part014  label="Enclosure001"
  Group = -> [Distance006,Distance007,Distance008,Distance009,Distance010,Distance011]
  Origin = -> Origin076
FEATURE [App::Part] Part008  label="Measurements"
  Group = -> [Part007,Part009,Part014,Distance012,Distance018,Distance017,Distance016,Distance015,Distance014,Distance013]
  Origin = -> Origin068
FEATURE [Part::Feature] Part__Feature  label="SOLID"
  shape: bbox 4.9 x 4.9 x 5.1 mm, 7 faces (baked)
FEATURE [Part::Feature] Part__Feature001  label="COMPOUND"
  shape: bbox 14 x 14.9 x 25.2 mm, 393 faces, 0 solids (baked)
FEATURE [Part::Feature] Part__Feature002  label="COMPOUND001"
  shape: bbox 11.4 x 9.2 x 0.4 mm, 11 faces, 0 solids (baked)
FEATURE [App::Part] COMPOUND  label="COMPOUND002"
  Group = -> [Part__Feature001,Part__Feature002]
  Origin = -> Origin009
FEATURE [Part::Feature] Part__Feature003  label="SOLID001"
  shape: bbox 4.9 x 4.9 x 5.1 mm, 7 faces (baked)
FEATURE [Part::Feature] Part__Feature004  label="COMPOUND003"
  shape: bbox 14 x 14.9 x 25.2 mm, 393 faces, 0 solids (baked)
FEATURE [Part::Feature] Part__Feature005  label="COMPOUND004"
  shape: bbox 11.4 x 9.2 x 0.4 mm, 11 faces, 0 solids (baked)
FEATURE [App::Part] COMPOUND001  label="COMPOUND005"
  Group = -> [Part__Feature004,Part__Feature005]
  Origin = -> Origin011
FEATURE [Part::Feature] Part__Feature006  label="SOLID002"
  shape: bbox 4.9 x 4.9 x 5.1 mm, 7 faces (baked)
FEATURE [Part::Feature] Part__Feature007  label="COMPOUND006"
  shape: bbox 14 x 14.9 x 25.2 mm, 393 faces, 0 solids (baked)
FEATURE [Part::Feature] Part__Feature008  label="COMPOUND007"
  shape: bbox 11.4 x 9.2 x 0.4 mm, 11 faces, 0 solids (baked)
FEATURE [App::Part] COMPOUND002  label="COMPOUND008"
  Group = -> [Part__Feature007,Part__Feature008]
  Origin = -> Origin013
FEATURE [Part::Feature] Part__Feature009  label="SOLID003"
  shape: bbox 4.9 x 4.9 x 5.1 mm, 7 faces (baked)
FEATURE [Part::Feature] Part__Feature010  label="COMPOUND009"
  shape: bbox 14 x 14.9 x 25.2 mm, 393 faces, 0 solids (baked)
FEATURE [Part::Feature] Part__Feature011  label="COMPOUND010"
  shape: bbox 11.4 x 9.2 x 0.4 mm, 11 faces, 0 solids (baked)
FEATURE [App::Part] COMPOUND003  label="COMPOUND011"
  Group = -> [Part__Feature010,Part__Feature011]
  Origin = -> Origin015
FEATURE [Part::Feature] Part__Feature012  label="Extrude005"
  Placement = pos=(0,0,0.05) rot=(0,0,1;0rad)
  shape: bbox 4 x 4 x 0.85 mm, 6 faces (baked)
FEATURE [Part::Feature] Part__Feature013  label="Fusion001"
  shape: bbox 0.25 x 0.4 x 0.203 mm, 6 faces (baked)
FEATURE [Part::Feature] Part__Feature014  label="Fusion002"
  shape: bbox 0.25 x 0.4 x 0.203 mm, 6 faces (baked)
FEATURE [Part::Feature] Part__Feature015  label="Fusion003"
  shape: bbox 0.25 x 0.4 x 0.203 mm, 6 faces (baked)
FEATURE [Part::Feature] Part__Feature016  label="Fusion004"
  shape: bbox 0.25 x 0.4 x 0.203 mm, 6 faces (baked)
FEATURE [Part::Feature] Part__Feature017  label="Fusion005"
  shape: bbox 0.25 x 0.4 x 0.203 mm, 6 faces (baked)
FEATURE [Part::Feature] Part__Feature018  label="Fusion006"
  shape: bbox 0.25 x 0.4 x 0.203 mm, 6 faces (baked)
FEATURE [Part::Feature] Part__Feature019  label="Fusion007"
  shape: bbox 0.4 x 0.25 x 0.203 mm, 6 faces (baked)
FEATURE [Part::Feature] Part__Feature020  label="Fusion008"
  shape: bbox 0.4 x 0.25 x 0.203 mm, 6 faces (baked)
FEATURE [Part::Feature] Part__Feature021  label="Fusion009"
  shape: bbox 0.4 x 0.25 x 0.203 mm, 6 faces (baked)
FEATURE [Part::Feature] Part__Feature022  label="Fusion010"
  shape: bbox 0.4 x 0.25 x 0.203 mm, 6 faces (baked)
FEATURE [Part::Feature] Part__Feature023  label="Fusion011"
  shape: bbox 0.4 x 0.25 x 0.203 mm, 6 faces (baked)
FEATURE [Part::Feature] Part__Feature024  label="Fusion012"
  shape: bbox 0.4 x 0.25 x 0.203 mm, 6 faces (baked)
FEATURE [Part::Feature] Part__Feature025  label="Fusion013"
  shape: bbox 0.25 x 0.4 x 0.203 mm, 6 faces (baked)
FEATURE [Part::Feature] Part__Feature026  label="Fusion014"
  shape: bbox 0.25 x 0.4 x 0.203 mm, 6 faces (baked)
FEATURE [Part::Feature] Part__Feature027  label="Fusion015"
  shape: bbox 0.25 x 0.4 x 0.203 mm, 6 faces (baked)
FEATURE [Part::Feature] Part__Feature028  label="Fusion016"
  shape: bbox 0.25 x 0.4 x 0.203 mm, 6 faces (baked)
FEATURE [Part::Feature] Part__Feature029  label="Fusion017"
  shape: bbox 0.25 x 0.4 x 0.203 mm, 6 faces (baked)
FEATURE [Part::Feature] Part__Feature030  label="Fusion018"
  shape: bbox 0.25 x 0.4 x 0.203 mm, 6 faces (baked)
FEATURE [Part::Feature] Part__Feature031  label="Fusion019"
  shape: bbox 0.4 x 0.25 x 0.203 mm, 6 faces (baked)
FEATURE [Part::Feature] Part__Feature032  label="Fusion020"
  shape: bbox 0.4 x 0.25 x 0.203 mm, 6 faces (baked)
FEATURE [Part::Feature] Part__Feature033  label="Fusion021"
  shape: bbox 0.4 x 0.25 x 0.203 mm, 6 faces (baked)
FEATURE [Part::Feature] Part__Feature034  label="Fusion022"
  shape: bbox 0.4 x 0.25 x 0.203 mm, 6 faces (baked)
FEATURE [Part::Feature] Part__Feature035  label="Fusion023"
  shape: bbox 0.4 x 0.25 x 0.203 mm, 6 faces (baked)
FEATURE [Part::Feature] Part__Feature036  label="Fusion024"
  shape: bbox 0.4 x 0.25 x 0.203 mm, 6 faces (baked)
FEATURE [Part::Feature] Part__Feature037  label="Fusion025"
  shape: bbox 2.6 x 2.6 x 0.203 mm, 12 faces (baked)
FEATURE [Part::Feature] Part__Feature038  label="Fusion026"
  shape: bbox 2e+100 x 2e+100 x 2e+100 mm, 1 faces, 0 solids (baked)
FEATURE [Part::Feature] Part__Feature039  label="Fusion027"
  shape: bbox 2e+100 x 2e+100 x 2e+100 mm, 1 faces, 0 solids (baked)
FEATURE [Part::Feature] Part__Feature040  label="Fusion028"
  shape: bbox 2e+100 x 2e+100 x 2e+100 mm, 1 faces, 0 solids (baked)
FEATURE [Part::Feature] Part__Feature041  label="Fusion029"
  shape: bbox 2e+100 x 2e+100 x 2e+100 mm, 1 faces, 0 solids (baked)
FEATURE [App::Part] Fusion001  label="Fusion030"
  Group = -> [Part__Feature013,Part__Feature014,Part__Feature015,Part__Feature016,Part__Feature017,Part__Feature018,Part__Feature019,Part__Feature020,Part__Feature021,Part__Feature022,Part__Feature023,Part__Feature024,Part__Feature025,Part__Feature026,Part__Feature027,Part__Feature028,Part__Feature029,Part__Feature030,Part__Feature031,Part__Feature032,Part__Feature033,Part__Feature034,Part__Feature035,+6 more]
  Origin = -> Origin017
FEATURE [App::Part] ATTINY817
  Group = -> [Part__Feature012,Fusion001]
  Origin = -> Origin018
  Placement = pos=(33.27,10.79,1.6) rot=(0,0,-1;0.785398rad)
FEATURE [Part::Feature] Part__Feature042  label="Pino"
  shape: bbox 0.64 x 0.64 x 11.54 mm, 14 faces (baked)
FEATURE [Part::Feature] Part__Feature043  label="Base"
  Placement = pos=(0,0,3) rot=(0,0,1;0rad)
  shape: bbox 2.54 x 2.54 x 2.54 mm, 18 faces (baked)
FEATURE [Part::Feature] Part__Feature044  label="Pino001"
  shape: bbox 0.64 x 0.64 x 11.54 mm, 14 faces (baked)
FEATURE [Part::Feature] Part__Feature045  label="Base001"
  Placement = pos=(0,0,3) rot=(0,0,1;0rad)
  shape: bbox 2.54 x 2.54 x 2.54 mm, 18 faces (baked)
FEATURE [Part::Feature] Part__Feature046  label="Pino002"
  shape: bbox 0.64 x 0.64 x 11.54 mm, 14 faces (baked)
FEATURE [Part::Feature] Part__Feature047  label="Base002"
  Placement = pos=(0,0,3) rot=(0,0,1;0rad)
  shape: bbox 2.54 x 2.54 x 2.54 mm, 18 faces (baked)
FEATURE [Part::Feature] Part__Feature048  label="Pino003"
  shape: bbox 0.64 x 0.64 x 11.54 mm, 14 faces (baked)
FEATURE [Part::Feature] Part__Feature049  label="Base003"
  Placement = pos=(0,0,3) rot=(0,0,1;0rad)
  shape: bbox 2.54 x 2.54 x 2.54 mm, 18 faces (baked)
FEATURE [Part::Feature] Part__Feature050  label="Pino004"
  shape: bbox 0.64 x 0.64 x 11.54 mm, 14 faces (baked)
FEATURE [Part::Feature] Part__Feature051  label="Base004"
  Placement = pos=(0,0,3) rot=(0,0,1;0rad)
  shape: bbox 2.54 x 2.54 x 2.54 mm, 18 faces (baked)
FEATURE [Part::Feature] Part__Feature052  label="Pino005"
  shape: bbox 0.64 x 0.64 x 11.54 mm, 14 faces (baked)
FEATURE [Part::Feature] Part__Feature053  label="Base005"
  Placement = pos=(0,0,3) rot=(0,0,1;0rad)
  shape: bbox 2.54 x 2.54 x 2.54 mm, 18 faces (baked)
FEATURE [Part::Feature] Part__Feature054  label="BMxB-SRSS-TB"
  Placement = pos=(6.64,12.17,1.6) rot=(0,0,-1;1.5708rad)
  shape: bbox 3.1 x 0.2 x 3.05 mm, 27 faces (baked)
FEATURE [Part::Feature] Part__Feature055  label="BMxB-SRSS-TB001"
  Placement = pos=(6.64,12.17,1.6) rot=(0,0,-1;1.5708rad)
  shape: bbox 3.1 x 0.2 x 3.05 mm, 27 faces (baked)
FEATURE [Part::Feature] Part__Feature056  label="BMxB-SRSS-TB002"
  Placement = pos=(6.64,12.17,1.6) rot=(0,0,-1;1.5708rad)
  shape: bbox 3.1 x 0.2 x 3.05 mm, 27 faces (baked)
FEATURE [Part::Feature] Part__Feature057  label="BMxB-SRSS-TB003"
  Placement = pos=(6.64,12.17,1.6) rot=(0,0,-1;1.5708rad)
  shape: bbox 3.1 x 0.2 x 3.05 mm, 27 faces (baked)
FEATURE [Part::Feature] Part__Feature058  label="BMxB-SRSS-TB004"
  Placement = pos=(6.64,12.17,1.6) rot=(0,0,-1;1.5708rad)
  shape: bbox 1.5 x 0.2 x 1.25 mm, 11 faces (baked)
FEATURE [Part::Feature] Part__Feature059  label="BMxB-SRSS-TB005"
  Placement = pos=(6.64,12.17,1.6) rot=(0,0,-1;1.5708rad)
  shape: bbox 1.5 x 0.2 x 1.25 mm, 11 faces (baked)
FEATURE [Part::Feature] Part__Feature060  label="BMxB-SRSS-TB006"
  Placement = pos=(6.64,12.17,1.6) rot=(0,0,-1;1.5708rad)
  shape: bbox 2.9 x 6 x 4.25 mm, 121 faces (baked)
FEATURE [App::Part] BMxB_SRSS_TB  label="BMxB-SRSS-TB007"
  Group = -> [Part__Feature054,Part__Feature055,Part__Feature056,Part__Feature057,Part__Feature058,Part__Feature059,Part__Feature060]
  Origin = -> Origin026
FEATURE [Part::Feature] Part__Feature061  label="BMxB-SRSS-TB008"
  Placement = pos=(69.43,9.17,1.6) rot=(0,0,1;1.5708rad)
  shape: bbox 3.1 x 0.2 x 3.05 mm, 27 faces (baked)
FEATURE [Part::Feature] Part__Feature062  label="BMxB-SRSS-TB009"
  Placement = pos=(69.43,9.17,1.6) rot=(0,0,1;1.5708rad)
  shape: bbox 3.1 x 0.2 x 3.05 mm, 27 faces (baked)
FEATURE [Part::Feature] Part__Feature063  label="BMxB-SRSS-TB010"
  Placement = pos=(69.43,9.17,1.6) rot=(0,0,1;1.5708rad)
  shape: bbox 3.1 x 0.2 x 3.05 mm, 27 faces (baked)
FEATURE [Part::Feature] Part__Feature064  label="BMxB-SRSS-TB011"
  Placement = pos=(69.43,9.17,1.6) rot=(0,0,1;1.5708rad)
  shape: bbox 3.1 x 0.2 x 3.05 mm, 27 faces (baked)
FEATURE [Part::Feature] Part__Feature065  label="BMxB-SRSS-TB012"
  Placement = pos=(69.43,9.17,1.6) rot=(0,0,1;1.5708rad)
  shape: bbox 1.5 x 0.2 x 1.25 mm, 11 faces (baked)
FEATURE [Part::Feature] Part__Feature066  label="BMxB-SRSS-TB013"
  Placement = pos=(69.43,9.17,1.6) rot=(0,0,1;1.5708rad)
  shape: bbox 1.5 x 0.2 x 1.25 mm, 11 faces (baked)
FEATURE [Part::Feature] Part__Feature067  label="BMxB-SRSS-TB014"
  Placement = pos=(69.43,9.17,1.6) rot=(0,0,1;1.5708rad)
  shape: bbox 2.9 x 6 x 4.25 mm, 121 faces (baked)
FEATURE [App::Part] BMxB_SRSS_TB001  label="BMxB-SRSS-TB015"
  Group = -> [Part__Feature061,Part__Feature062,Part__Feature063,Part__Feature064,Part__Feature065,Part__Feature066,Part__Feature067]
  Origin = -> Origin027
FEATURE [Part::Feature] Part__Feature068  label="Pino006"
  shape: bbox 0.64 x 0.64 x 11.54 mm, 14 faces (baked)
FEATURE [Part::Feature] Part__Feature069  label="Base006"
  Placement = pos=(0,0,3) rot=(0,0,1;0rad)
  shape: bbox 2.54 x 2.54 x 2.54 mm, 18 faces (baked)
FEATURE [Part::Feature] Part__Feature070  label="Pino007"
  shape: bbox 0.64 x 0.64 x 11.54 mm, 14 faces (baked)
FEATURE [Part::Feature] Part__Feature071  label="Base007"
  Placement = pos=(0,0,3) rot=(0,0,1;0rad)
  shape: bbox 2.54 x 2.54 x 2.54 mm, 18 faces (baked)
FEATURE [Part::Feature] Part__Feature072  label="Pino008"
  shape: bbox 0.64 x 0.64 x 11.54 mm, 14 faces (baked)
FEATURE [Part::Feature] Part__Feature073  label="Base008"
  Placement = pos=(0,0,3) rot=(0,0,1;0rad)
  shape: bbox 2.54 x 2.54 x 2.54 mm, 18 faces (baked)
FEATURE [Part::Feature] Part__Feature074  label="Pino009"
  shape: bbox 0.64 x 0.64 x 11.54 mm, 14 faces (baked)
FEATURE [Part::Feature] Part__Feature075  label="Base009"
  Placement = pos=(0,0,3) rot=(0,0,1;0rad)
  shape: bbox 2.54 x 2.54 x 2.54 mm, 18 faces (baked)
FEATURE [Part::Feature] Part__Feature076  label="Pino010"
  shape: bbox 0.64 x 0.64 x 11.54 mm, 14 faces (baked)
FEATURE [Part::Feature] Part__Feature077  label="Base010"
  Placement = pos=(0,0,3) rot=(0,0,1;0rad)
  shape: bbox 2.54 x 2.54 x 2.54 mm, 18 faces (baked)
FEATURE [Part::Feature] Part__Feature078  label="Pino011"
  shape: bbox 0.64 x 0.64 x 11.54 mm, 14 faces (baked)
FEATURE [Part::Feature] Part__Feature079  label="Base011"
  Placement = pos=(0,0,3) rot=(0,0,1;0rad)
  shape: bbox 2.54 x 2.54 x 2.54 mm, 18 faces (baked)
FEATURE [Part::Feature] Part__Feature080  label="Cut005"
  shape: bbox 76.2 x 21.59 x 1.6 mm, 94 faces (baked)
FEATURE [Part::Feature] Part__Feature081  label="Extrude008"
  shape: bbox 5.4 x 2.8 x 1.6 mm, 10 faces (baked)
FEATURE [Part::Feature] Part__Feature082  label="Extrude009"
  shape: bbox 5.4 x 2.8 x 1.6 mm, 10 faces (baked)
FEATURE [Part::Feature] Part__Feature083  label="Extrude010"
  shape: bbox 5.4 x 2.8 x 1.6 mm, 10 faces (baked)
FEATURE [Part::Feature] Part__Feature084  label="Extrude011"
  shape: bbox 5.4 x 2.8 x 1.6 mm, 10 faces (baked)
FEATURE [Part::Feature] Part__Feature085  label="Extrude012"
  shape: bbox 5.4 x 2.8 x 1.6 mm, 10 faces (baked)
FEATURE [Part::Feature] Part__Feature086  label="Extrude013"
  shape: bbox 5.4 x 2.8 x 1.6 mm, 10 faces (baked)
FEATURE [Part::Feature] Part__Feature087  label="Extrude014"
  shape: bbox 5.4 x 2.8 x 1.6 mm, 10 faces (baked)
FEATURE [Part::Feature] Part__Feature088  label="Extrude015"
  shape: bbox 5.4 x 2.8 x 1.6 mm, 10 faces (baked)
FEATURE [Part::Feature] Part__Feature089  label="Extrude016"
  shape: bbox 3.2 x 3.2 x 1.6 mm, 4 faces (baked)
FEATURE [Part::Feature] Part__Feature090  label="Extrude017"
  shape: bbox 3.2 x 3.2 x 1.6 mm, 4 faces (baked)
FEATURE [Part::Feature] Part__Feature091  label="Extrude018"
  shape: bbox 3.2 x 3.2 x 1.6 mm, 4 faces (baked)
FEATURE [Part::Feature] Part__Feature092  label="Extrude019"
  shape: bbox 3.2 x 3.2 x 1.6 mm, 4 faces (baked)
FEATURE [Part::Feature] Part__Feature093  label="Extrude020"
  shape: bbox 1.8 x 1.8 x 1.6 mm, 4 faces (baked)
FEATURE [Part::Feature] Part__Feature094  label="Extrude021"
  shape: bbox 1.8 x 1.8 x 1.6 mm, 4 faces (baked)
FEATURE [Part::Feature] Part__Feature095  label="Extrude022"
  shape: bbox 1.8 x 1.8 x 1.6 mm, 4 faces (baked)
FEATURE [Part::Feature] Part__Feature096  label="Extrude023"
  shape: bbox 1.8 x 1.8 x 1.6 mm, 4 faces (baked)
FEATURE [Part::Feature] Part__Feature097  label="Extrude024"
  shape: bbox 1.8 x 1.8 x 1.6 mm, 4 faces (baked)
FEATURE [Part::Feature] Part__Feature098  label="Extrude025"
  shape: bbox 1.8 x 1.8 x 1.6 mm, 4 faces (baked)
FEATURE [Part::Feature] Part__Feature099  label="Extrude026"
  shape: bbox 1.8 x 1.8 x 1.6 mm, 4 faces (baked)
FEATURE [Part::Feature] Part__Feature100  label="Extrude027"
  shape: bbox 1.8 x 1.8 x 1.6 mm, 4 faces (baked)
FEATURE [Part::Feature] Part__Feature101  label="Extrude028"
  shape: bbox 1.8 x 1.8 x 1.6 mm, 4 faces (baked)
FEATURE [Part::Feature] Part__Feature102  label="Extrude029"
  shape: bbox 1.8 x 1.8 x 1.6 mm, 4 faces (baked)
FEATURE [Part::Feature] Part__Feature103  label="Extrude030"
  shape: bbox 1.8 x 1.8 x 1.6 mm, 4 faces (baked)
FEATURE [Part::Feature] Part__Feature104  label="Extrude031"
  shape: bbox 1.8 x 1.8 x 1.6 mm, 4 faces (baked)
FEATURE [Part::Feature] Part__Feature105  label="Extrude032"
  shape: bbox 1.8 x 1.8 x 1.6 mm, 4 faces (baked)
FEATURE [Part::Feature] Part__Feature106  label="Extrude033"
  shape: bbox 1.8 x 1.8 x 1.6 mm, 4 faces (baked)
FEATURE [Part::Feature] Part__Feature107  label="Extrude034"
  shape: bbox 1.8 x 1.8 x 1.6 mm, 4 faces (baked)
FEATURE [Part::Feature] Part__Feature108  label="Extrude035"
  shape: bbox 1.8 x 1.8 x 1.6 mm, 4 faces (baked)
FEATURE [Part::Feature] Part__Feature109  label="Extrude036"
  shape: bbox 1.8 x 1.8 x 1.6 mm, 4 faces (baked)
FEATURE [Part::Feature] Part__Feature110  label="Extrude037"
  shape: bbox 1.8 x 1.8 x 1.6 mm, 4 faces (baked)
FEATURE [Part::Feature] Part__Feature111  label="Extrude038"
  shape: bbox 1.8 x 1.8 x 1.6 mm, 4 faces (baked)
FEATURE [Part::Feature] Part__Feature112  label="Extrude039"
  shape: bbox 1.8 x 1.8 x 1.6 mm, 4 faces (baked)
FEATURE [Part::Feature] Part__Feature113  label="Extrude040"
  shape: bbox 1.778 x 1.778 x 1.6 mm, 4 faces (baked)
FEATURE [Part::Feature] Part__Feature114  label="Extrude041"
  shape: bbox 1.778 x 1.778 x 1.6 mm, 4 faces (baked)
FEATURE [Part::Feature] Part__Feature115  label="Extrude042"
  shape: bbox 1.778 x 1.778 x 1.6 mm, 4 faces (baked)
FEATURE [Part::Feature] Part__Feature116  label="Extrude043"
  shape: bbox 1.778 x 1.778 x 1.6 mm, 4 faces (baked)
FEATURE [Part::Feature] Part__Feature117  label="Extrude044"
  shape: bbox 1.778 x 1.778 x 1.6 mm, 4 faces (baked)
FEATURE [Part::Feature] Part__Feature118  label="Extrude045"
  shape: bbox 1.778 x 1.778 x 1.6 mm, 4 faces (baked)
FEATURE [Part::Feature] Part__Feature119  label="Extrude046"
  shape: bbox 1.778 x 1.778 x 1.6 mm, 4 faces (baked)
FEATURE [Part::Feature] Part__Feature120  label="Extrude047"
  shape: bbox 1.778 x 1.778 x 1.6 mm, 4 faces (baked)
FEATURE [Part::Feature] Part__Feature121  label="Extrude048"
  shape: bbox 1.778 x 1.778 x 1.6 mm, 4 faces (baked)
FEATURE [Part::Feature] Part__Feature122  label="Extrude049"
  shape: bbox 1.778 x 1.778 x 1.6 mm, 4 faces (baked)
FEATURE [Part::Feature] Part__Feature123  label="Extrude050"
  shape: bbox 1.778 x 1.778 x 1.6 mm, 4 faces (baked)
FEATURE [Part::Feature] Part__Feature124  label="Extrude051"
  shape: bbox 1.778 x 1.778 x 1.6 mm, 4 faces (baked)
FEATURE [App::Part] Extrude008  label="Extrude052"
  Group = -> [Part__Feature081,Part__Feature082,Part__Feature083,Part__Feature084,Part__Feature085,Part__Feature086,Part__Feature087,Part__Feature088,Part__Feature089,Part__Feature090,Part__Feature091,Part__Feature092,Part__Feature093,Part__Feature094,Part__Feature095,Part__Feature096,Part__Feature097,Part__Feature098,Part__Feature099,Part__Feature100,Part__Feature101,Part__Feature102,Part__Feature103,+21 more]
  Origin = -> Origin035
FEATURE [App::Part] PCB001
  Group = -> [Part__Feature080,Extrude008]
  Origin = -> Origin036
FEATURE [Part::Feature] Part__Feature125  label="Solid"
  shape: bbox 1.34 x 0.68 x 0.254 mm, 7 faces (baked)
FEATURE [Part::Feature] Part__Feature126  label="Solid001"
  shape: bbox 1.34 x 0.68 x 0.254 mm, 6 faces (baked)
FEATURE [Part::Feature] Part__Feature127  label="Solid002"
  shape: bbox 1.34 x 0.68 x 0.254 mm, 6 faces (baked)
FEATURE [Part::Feature] Part__Feature128  label="Solid003"
  shape: bbox 1.34 x 0.68 x 0.254 mm, 6 faces (baked)
FEATURE [Part::Feature] Part__Feature129  label="Face"
  shape: bbox 0.1489 x 2.8 x 0.94 mm, 1 faces, 0 solids (baked)
FEATURE [Part::Feature] Part__Feature130  label="Face001"
  shape: bbox 3.2 x 0.1489 x 0.94 mm, 1 faces, 0 solids (baked)
FEATURE [Part::Feature] Part__Feature131  label="Face002"
  shape: bbox 0.1489 x 2.8 x 0.94 mm, 1 faces, 0 solids (baked)
FEATURE [Part::Feature] Part__Feature132  label="Face003"
  shape: bbox 3.2 x 0.1489 x 0.94 mm, 1 faces, 0 solids (baked)
FEATURE [Part::Feature] Part__Feature133  label="Face004"
  shape: bbox 2.902 x 2.502 x 2e-07 mm, 1 faces, 0 solids (baked)
FEATURE [Part::Feature] Part__Feature134  label="Face005"
  shape: bbox 0.8 x 0.8 x 0.2 mm, 1 faces, 0 solids (baked)
FEATURE [Part::Feature] Part__Feature135  label="Face006"
  shape: bbox 0.8 x 0.8 x 2e-07 mm, 1 faces, 0 solids (baked)
FEATURE [Part::Feature] Part__Feature136  label="Face007"
  shape: bbox 1 x 1 x 2e-07 mm, 1 faces, 0 solids (baked)
FEATURE [Part::Feature] Part__Feature137  label="Face008"
  shape: bbox 1 x 1 x 0.84 mm, 1 faces, 0 solids (baked)
FEATURE [Part::Feature] Part__Feature138  label="Face009"
  shape: bbox 2.2 x 2e-07 x 0.84 mm, 1 faces, 0 solids (baked)
FEATURE [Part::Feature] Part__Feature139  label="Face010"
  shape: bbox 2e-07 x 2.8 x 0.84 mm, 1 faces, 0 solids (baked)
FEATURE [Part::Feature] Part__Feature140  label="Face011"
  shape: bbox 3.2 x 2e-07 x 0.84 mm, 1 faces, 0 solids (baked)
FEATURE [Part::Feature] Part__Feature141  label="Face012"
  shape: bbox 2e-07 x 1.8 x 0.84 mm, 1 faces, 0 solids (baked)
FEATURE [Part::Feature] Part__Feature142  label="Face013"
  shape: bbox 3.2 x 2.8 x 2e-07 mm, 1 faces, 0 solids (baked)
FEATURE [Part::Feature] Part__Feature143  label="Face014"
  shape: bbox 2.4 x 2.4 x 0.2 mm, 1 faces, 0 solids (baked)
FEATURE [Part::Feature] Part__Feature144  label="Face015"
  shape: bbox 2.4 x 2.4 x 2e-07 mm, 1 faces, 0 solids (baked)
FEATURE [App::Part] NEO3535_REVERSE
  Group = -> [Part__Feature125,Part__Feature126,Part__Feature127,Part__Feature128,Part__Feature129,Part__Feature130,Part__Feature131,Part__Feature132,Part__Feature133,Part__Feature134,Part__Feature135,Part__Feature136,Part__Feature137,Part__Feature138,Part__Feature139,Part__Feature140,Part__Feature141,Part__Feature142,Part__Feature143,Part__Feature144]
  Origin = -> Origin037
  Placement = pos=(9.53,10.79,1.6) rot=(-0.707107,0.707107,0;3.14159rad)
FEATURE [Part::Feature] Part__Feature145  label="Solid004"
  shape: bbox 1.34 x 0.68 x 0.254 mm, 7 faces (baked)
FEATURE [Part::Feature] Part__Feature146  label="Solid005"
  shape: bbox 1.34 x 0.68 x 0.254 mm, 6 faces (baked)
FEATURE [Part::Feature] Part__Feature147  label="Solid006"
  shape: bbox 1.34 x 0.68 x 0.254 mm, 6 faces (baked)
FEATURE [Part::Feature] Part__Feature148  label="Solid007"
  shape: bbox 1.34 x 0.68 x 0.254 mm, 6 faces (baked)
FEATURE [Part::Feature] Part__Feature149  label="Face016"
  shape: bbox 0.1489 x 2.8 x 0.94 mm, 1 faces, 0 solids (baked)
FEATURE [Part::Feature] Part__Feature150  label="Face017"
  shape: bbox 3.2 x 0.1489 x 0.94 mm, 1 faces, 0 solids (baked)
FEATURE [Part::Feature] Part__Feature151  label="Face018"
  shape: bbox 0.1489 x 2.8 x 0.94 mm, 1 faces, 0 solids (baked)
FEATURE [Part::Feature] Part__Feature152  label="Face019"
  shape: bbox 3.2 x 0.1489 x 0.94 mm, 1 faces, 0 solids (baked)
FEATURE [Part::Feature] Part__Feature153  label="Face020"
  shape: bbox 2.902 x 2.502 x 2e-07 mm, 1 faces, 0 solids (baked)
FEATURE [Part::Feature] Part__Feature154  label="Face021"
  shape: bbox 0.8 x 0.8 x 0.2 mm, 1 faces, 0 solids (baked)
FEATURE [Part::Feature] Part__Feature155  label="Face022"
  shape: bbox 0.8 x 0.8 x 2e-07 mm, 1 faces, 0 solids (baked)
FEATURE [Part::Feature] Part__Feature156  label="Face023"
  shape: bbox 1 x 1 x 2e-07 mm, 1 faces, 0 solids (baked)
FEATURE [Part::Feature] Part__Feature157  label="Face024"
  shape: bbox 1 x 1 x 0.84 mm, 1 faces, 0 solids (baked)
FEATURE [Part::Feature] Part__Feature158  label="Face025"
  shape: bbox 2.2 x 2e-07 x 0.84 mm, 1 faces, 0 solids (baked)
FEATURE [Part::Feature] Part__Feature159  label="Face026"
  shape: bbox 2e-07 x 2.8 x 0.84 mm, 1 faces, 0 solids (baked)
FEATURE [Part::Feature] Part__Feature160  label="Face027"
  shape: bbox 3.2 x 2e-07 x 0.84 mm, 1 faces, 0 solids (baked)
FEATURE [Part::Feature] Part__Feature161  label="Face028"
  shape: bbox 2e-07 x 1.8 x 0.84 mm, 1 faces, 0 solids (baked)
FEATURE [Part::Feature] Part__Feature162  label="Face029"
  shape: bbox 3.2 x 2.8 x 2e-07 mm, 1 faces, 0 solids (baked)
FEATURE [Part::Feature] Part__Feature163  label="Face030"
  shape: bbox 2.4 x 2.4 x 0.2 mm, 1 faces, 0 solids (baked)
FEATURE [Part::Feature] Part__Feature164  label="Face031"
  shape: bbox 2.4 x 2.4 x 2e-07 mm, 1 faces, 0 solids (baked)
FEATURE [App::Part] NEO3535_REVERSE001
  Group = -> [Part__Feature145,Part__Feature146,Part__Feature147,Part__Feature148,Part__Feature149,Part__Feature150,Part__Feature151,Part__Feature152,Part__Feature153,Part__Feature154,Part__Feature155,Part__Feature156,Part__Feature157,Part__Feature158,Part__Feature159,Part__Feature160,Part__Feature161,Part__Feature162,Part__Feature163,Part__Feature164]
  Origin = -> Origin038
  Placement = pos=(28.19,10.79,1.6) rot=(-0.707107,0.707107,0;3.14159rad)
FEATURE [Part::Feature] Part__Feature165  label="Solid008"
  shape: bbox 1.34 x 0.68 x 0.254 mm, 7 faces (baked)
FEATURE [Part::Feature] Part__Feature166  label="Solid009"
  shape: bbox 1.34 x 0.68 x 0.254 mm, 6 faces (baked)
FEATURE [Part::Feature] Part__Feature167  label="Solid010"
  shape: bbox 1.34 x 0.68 x 0.254 mm, 6 faces (baked)
FEATURE [Part::Feature] Part__Feature168  label="Solid011"
  shape: bbox 1.34 x 0.68 x 0.254 mm, 6 faces (baked)
FEATURE [Part::Feature] Part__Feature169  label="Face032"
  shape: bbox 0.1489 x 2.8 x 0.94 mm, 1 faces, 0 solids (baked)
FEATURE [Part::Feature] Part__Feature170  label="Face033"
  shape: bbox 3.2 x 0.1489 x 0.94 mm, 1 faces, 0 solids (baked)
FEATURE [Part::Feature] Part__Feature171  label="Face034"
  shape: bbox 0.1489 x 2.8 x 0.94 mm, 1 faces, 0 solids (baked)
FEATURE [Part::Feature] Part__Feature172  label="Face035"
  shape: bbox 3.2 x 0.1489 x 0.94 mm, 1 faces, 0 solids (baked)
FEATURE [Part::Feature] Part__Feature173  label="Face036"
  shape: bbox 2.902 x 2.502 x 2e-07 mm, 1 faces, 0 solids (baked)
FEATURE [Part::Feature] Part__Feature174  label="Face037"
  shape: bbox 0.8 x 0.8 x 0.2 mm, 1 faces, 0 solids (baked)
FEATURE [Part::Feature] Part__Feature175  label="Face038"
  shape: bbox 0.8 x 0.8 x 2e-07 mm, 1 faces, 0 solids (baked)
FEATURE [Part::Feature] Part__Feature176  label="Face039"
  shape: bbox 1 x 1 x 2e-07 mm, 1 faces, 0 solids (baked)
FEATURE [Part::Feature] Part__Feature177  label="Face040"
  shape: bbox 1 x 1 x 0.84 mm, 1 faces, 0 solids (baked)
FEATURE [Part::Feature] Part__Feature178  label="Face041"
  shape: bbox 2.2 x 2e-07 x 0.84 mm, 1 faces, 0 solids (baked)
FEATURE [Part::Feature] Part__Feature179  label="Face042"
  shape: bbox 2e-07 x 2.8 x 0.84 mm, 1 faces, 0 solids (baked)
FEATURE [Part::Feature] Part__Feature180  label="Face043"
  shape: bbox 3.2 x 2e-07 x 0.84 mm, 1 faces, 0 solids (baked)
FEATURE [Part::Feature] Part__Feature181  label="Face044"
  shape: bbox 2e-07 x 1.8 x 0.84 mm, 1 faces, 0 solids (baked)
FEATURE [Part::Feature] Part__Feature182  label="Face045"
  shape: bbox 3.2 x 2.8 x 2e-07 mm, 1 faces, 0 solids (baked)
FEATURE [Part::Feature] Part__Feature183  label="Face046"
  shape: bbox 2.4 x 2.4 x 0.2 mm, 1 faces, 0 solids (baked)
FEATURE [Part::Feature] Part__Feature184  label="Face047"
  shape: bbox 2.4 x 2.4 x 2e-07 mm, 1 faces, 0 solids (baked)
FEATURE [App::Part] NEO3535_REVERSE002
  Group = -> [Part__Feature165,Part__Feature166,Part__Feature167,Part__Feature168,Part__Feature169,Part__Feature170,Part__Feature171,Part__Feature172,Part__Feature173,Part__Feature174,Part__Feature175,Part__Feature176,Part__Feature177,Part__Feature178,Part__Feature179,Part__Feature180,Part__Feature181,Part__Feature182,Part__Feature183,Part__Feature184]
  Origin = -> Origin039
  Placement = pos=(47.63,10.79,1.6) rot=(-0.707107,0.707107,0;3.14159rad)
FEATURE [Part::Feature] Part__Feature185  label="Solid012"
  shape: bbox 1.34 x 0.68 x 0.254 mm, 7 faces (baked)
FEATURE [Part::Feature] Part__Feature186  label="Solid013"
  shape: bbox 1.34 x 0.68 x 0.254 mm, 6 faces (baked)
FEATURE [Part::Feature] Part__Feature187  label="Solid014"
  shape: bbox 1.34 x 0.68 x 0.254 mm, 6 faces (baked)
FEATURE [Part::Feature] Part__Feature188  label="Solid015"
  shape: bbox 1.34 x 0.68 x 0.254 mm, 6 faces (baked)
FEATURE [Part::Feature] Part__Feature189  label="Face048"
  shape: bbox 0.1489 x 2.8 x 0.94 mm, 1 faces, 0 solids (baked)
FEATURE [Part::Feature] Part__Feature190  label="Face049"
  shape: bbox 3.2 x 0.1489 x 0.94 mm, 1 faces, 0 solids (baked)
FEATURE [Part::Feature] Part__Feature191  label="Face050"
  shape: bbox 0.1489 x 2.8 x 0.94 mm, 1 faces, 0 solids (baked)
FEATURE [Part::Feature] Part__Feature192  label="Face051"
  shape: bbox 3.2 x 0.1489 x 0.94 mm, 1 faces, 0 solids (baked)
FEATURE [Part::Feature] Part__Feature193  label="Face052"
  shape: bbox 2.902 x 2.502 x 2e-07 mm, 1 faces, 0 solids (baked)
FEATURE [Part::Feature] Part__Feature194  label="Face053"
  shape: bbox 0.8 x 0.8 x 0.2 mm, 1 faces, 0 solids (baked)
FEATURE [Part::Feature] Part__Feature195  label="Face054"
  shape: bbox 0.8 x 0.8 x 2e-07 mm, 1 faces, 0 solids (baked)
FEATURE [Part::Feature] Part__Feature196  label="Face055"
  shape: bbox 1 x 1 x 2e-07 mm, 1 faces, 0 solids (baked)
FEATURE [Part::Feature] Part__Feature197  label="Face056"
  shape: bbox 1 x 1 x 0.84 mm, 1 faces, 0 solids (baked)
FEATURE [Part::Feature] Part__Feature198  label="Face057"
  shape: bbox 2.2 x 2e-07 x 0.84 mm, 1 faces, 0 solids (baked)
FEATURE [Part::Feature] Part__Feature199  label="Face058"
  shape: bbox 2e-07 x 2.8 x 0.84 mm, 1 faces, 0 solids (baked)
FEATURE [Part::Feature] Part__Feature200  label="Face059"
  shape: bbox 3.2 x 2e-07 x 0.84 mm, 1 faces, 0 solids (baked)
FEATURE [Part::Feature] Part__Feature201  label="Face060"
  shape: bbox 2e-07 x 1.8 x 0.84 mm, 1 faces, 0 solids (baked)
FEATURE [Part::Feature] Part__Feature202  label="Face061"
  shape: bbox 3.2 x 2.8 x 2e-07 mm, 1 faces, 0 solids (baked)
FEATURE [Part::Feature] Part__Feature203  label="Face062"
  shape: bbox 2.4 x 2.4 x 0.2 mm, 1 faces, 0 solids (baked)
FEATURE [Part::Feature] Part__Feature204  label="Face063"
  shape: bbox 2.4 x 2.4 x 2e-07 mm, 1 faces, 0 solids (baked)
FEATURE [App::Part] NEO3535_REVERSE003
  Group = -> [Part__Feature185,Part__Feature186,Part__Feature187,Part__Feature188,Part__Feature189,Part__Feature190,Part__Feature191,Part__Feature192,Part__Feature193,Part__Feature194,Part__Feature195,Part__Feature196,Part__Feature197,Part__Feature198,Part__Feature199,Part__Feature200,Part__Feature201,Part__Feature202,Part__Feature203,Part__Feature204]
  Origin = -> Origin040
  Placement = pos=(66.67,10.79,1.6) rot=(-0.707107,0.707107,0;3.14159rad)
FEATURE [Part::Feature] Part__Feature205  label="Washer"
  Placement = pos=(0,0,7.5) rot=(0,0,1;0rad)
  shape: bbox 11 x 11 x 1 mm, 6 faces (baked)
FEATURE [Part::Feature] Part__Feature206  label="Cap"
  shape: bbox 6.494 x 6.494 x 3.75 mm, 6 faces (baked)
FEATURE [Part::Feature] Part__Feature207  label="Metal Body"
  shape: bbox 10.29 x 10.29 x 9.954 mm, 63 faces (baked)
FEATURE [Part::Feature] Part__Feature208  label="Plastic Body"
  shape: bbox 7.3 x 7.3 x 7 mm, 4 faces (baked)
FEATURE [Part::Feature] Part__Feature209  label="Contact 1"
  shape: bbox 0.5 x 4 x 5.75 mm, 14 faces (baked)
FEATURE [Part::Feature] Part__Feature210  label="Contact 2"
  shape: bbox 0.5 x 4 x 5.75 mm, 14 faces (baked)
FEATURE [Part::Feature] Part__Feature211  label="Nut"
  Placement = pos=(0,0,0.5) rot=(0,0,1;0rad)
  shape: bbox 11.05 x 10.02 x 2 mm, 53 faces (baked)
FEATURE [Part::Feature] Part__Feature212  label="Body"
  Placement = pos=(0,0,-0.3) rot=(0,0,1;0rad)
  shape: bbox 12.9 x 6.5 x 10.2 mm, 48 faces (baked)
FEATURE [Part::Feature] Part__Feature213  label="Body001"
  shape: bbox 12.9 x 6.5 x 17.85 mm, 60 faces (baked)
FEATURE [Part::Feature] Part__Feature214  label="Body002"
  Placement = pos=(0,0,6) rot=(0,1,0;0.174533rad)
  shape: bbox 5.726 x 4 x 14.94 mm, 4 faces (baked)
FEATURE [Part::Feature] Part__Feature215  label="Body003"
  Placement = pos=(0,0,0.875) rot=(0,0,1;0rad)
  shape: bbox 9.007 x 9.007 x 1.75 mm, 23 faces (baked)
FEATURE [Part::Feature] Part__Feature216  label="Body004"
  Placement = pos=(0,0,5.35) rot=(0,0,1;0rad)
  shape: bbox 9.007 x 9.007 x 1.75 mm, 23 faces (baked)
FEATURE [Part::Feature] Part__Feature217  label="Body005"
  Placement = pos=(0,0,1.75) rot=(0,0,1;0rad)
  shape: bbox 12.98 x 11.95 x 1.8 mm, 14 faces (baked)
FEATURE [Part::Feature] Part__Feature218  label="Body006"
  Placement = pos=(-4.6,0,-9.55) rot=(0,0,1;0rad)
  shape: bbox 0.65 x 2 x 4 mm, 12 faces (baked)
FEATURE [Part::Feature] Part__Feature219  label="Body007"
  Placement = pos=(0,0,-9.55) rot=(0,0,1;0rad)
  shape: bbox 0.65 x 2 x 4 mm, 12 faces (baked)
FEATURE [Part::Feature] Part__Feature220  label="Body008"
  Placement = pos=(4.6,0,-9.55) rot=(0,0,1;0rad)
  shape: bbox 0.65 x 2 x 4 mm, 12 faces (baked)
FEATURE [App::Part] Array
  Group = -> [Part__Feature218,Part__Feature219,Part__Feature220]
  Origin = -> Origin044
FEATURE [Part::Feature] Part__Feature221  label="SOLID004"
  shape: bbox 3.2 x 1.6 x 1.6 mm, 28 faces (baked)
FEATURE [App::Part] C_1206_3216Metric
  Group = -> [Part__Feature221]
  Origin = -> Origin046
  Placement = pos=(3.981,-17.999,1.65) rot=(0,0,1;0rad)
FEATURE [Part::Feature] Part__Feature222  label="SOLID005"
  shape: bbox 3.2 x 1.6 x 1.6 mm, 28 faces (baked)
FEATURE [App::Part] C_1206_3216Metric001
  Group = -> [Part__Feature222]
  Origin = -> Origin047
  Placement = pos=(69.458,-8.113,1.65) rot=(0,0,1;1.5708rad)
FEATURE [Part::Feature] Part__Feature223  label="SOLID006"
  shape: bbox 3.2 x 1.6 x 1.6 mm, 28 faces (baked)
FEATURE [App::Part] C_1206_3216Metric002
  Group = -> [Part__Feature223]
  Origin = -> Origin048
  Placement = pos=(9.315,-17.999,1.65) rot=(0,0,1;3.14159rad)
FEATURE [Part::Feature] Part__Feature224  label="SOLID007"
  shape: bbox 7.4 x 5.75 x 10.4 mm, 89 faces (baked)
FEATURE [App::Part] JST_XH_B2B_XH_A_1x02_P2_50mm_Vertical  label="JST_XH_B2B-XH-A_1x02_P2.50mm_Vertical"
  Group = -> [Part__Feature224]
  Origin = -> Origin049
  Placement = pos=(8.68,-29.556,1.65) rot=(0,0,-1;1.5708rad)
FEATURE [Part::Feature] Part__Feature225  label="SOLID008"
  shape: bbox 3.2 x 1.6 x 0.55 mm, 26 faces (baked)
FEATURE [Part::Feature] Part__Feature226  label="SOLID009"
  shape: bbox 8.606 x 8.603 x 7.7 mm, 41 faces (baked)
FEATURE [App::Part] CP_Elec_6_3x7_7  label="CP_Elec_6.3x7.7"
  Group = -> [Part__Feature226]
  Origin = -> Origin051
  Placement = pos=(61.883,-33.122,1.65) rot=(0,0,1;3.14159rad)
FEATURE [Part::Feature] Part__Feature227  label="SOLID010"
  shape: bbox 6.985 x 6.828 x 5.4 mm, 41 faces (baked)
FEATURE [App::Part] CP_Elec_5x5_4  label="CP_Elec_5x5.4"
  Group = -> [Part__Feature227]
  Origin = -> Origin052
  Placement = pos=(52.536,-38.573,1.65) rot=(0,0,1;3.14159rad)
FEATURE [Part::Feature] Part__Feature228  label="SOLID011"
  shape: bbox 7 x 6.5 x 1.7 mm, 78 faces (baked)
FEATURE [Part::Feature] Part__Feature229  label="SOLID012"
  shape: bbox 10.73 x 10.92 x 10.5 mm, 41 faces (baked)
FEATURE [App::Part] CP_Elec_8x10_5  label="CP_Elec_8x10.5"
  Group = -> [Part__Feature229]
  Origin = -> Origin054
  Placement = pos=(73.716,-34.646,1.65) rot=(0,0,1;0rad)
FEATURE [Part::Feature] Part__Feature230  label="SOLID013"
  shape: bbox 3.2 x 1.6 x 0.55 mm, 26 faces (baked)
FEATURE [Part::Feature] Part__Feature231  label="SOLID014"
  shape: bbox 3.2 x 1.6 x 0.55 mm, 26 faces (baked)
FEATURE [Part::Feature] Part__Feature232  label="COMPOUND012"
  shape: bbox 17 x 9 x 5.8 mm, 69 faces (baked)
FEATURE [Part::Feature] Part__Feature233  label="COMPOUND013"
  shape: bbox 9.65 x 11.95 x 1.35 mm, 32 faces (baked)
FEATURE [Part::Feature] Part__Feature234  label="COMPOUND014"
  shape: bbox 1.8 x 0.5 x 0.45 mm, 8 faces (baked)
FEATURE [Part::Feature] Part__Feature235  label="COMPOUND015"
  shape: bbox 1.8 x 0.5 x 0.45 mm, 8 faces (baked)
FEATURE [Part::Feature] Part__Feature236  label="COMPOUND016"
  shape: bbox 1.8 x 0.5 x 0.45 mm, 8 faces (baked)
FEATURE [Part::Feature] Part__Feature237  label="COMPOUND017"
  shape: bbox 1.8 x 0.5 x 0.45 mm, 8 faces (baked)
FEATURE [Part::Feature] Part__Feature238  label="COMPOUND018"
  shape: bbox 1.8 x 0.5 x 0.45 mm, 8 faces (baked)
FEATURE [Part::Feature] Part__Feature239  label="COMPOUND019"
  shape: bbox 1.8 x 0.5 x 0.45 mm, 8 faces (baked)
FEATURE [Part::Feature] Part__Feature240  label="COMPOUND020"
  shape: bbox 1.8 x 0.5 x 0.45 mm, 8 faces (baked)
FEATURE [Part::Feature] Part__Feature241  label="COMPOUND021"
  shape: bbox 1.8 x 0.5 x 0.45 mm, 8 faces (baked)
FEATURE [Part::Feature] Part__Feature242  label="COMPOUND022"
  shape: bbox 11.45 x 11.95 x 1.55 mm, 59 faces (baked)
FEATURE [Part::Feature] Part__Feature243  label="COMPOUND023"
  shape: bbox 35.5 x 36.8 x 1.6 mm, 37 faces (baked)
FEATURE [Part::Feature] Part__Feature244  label="COMPOUND024"
  shape: bbox 1.3 x 1.3 x 0.1 mm, 4 faces (baked)
FEATURE [Part::Feature] Part__Feature245  label="COMPOUND025"
  shape: bbox 1.3 x 1.3 x 0.1 mm, 4 faces (baked)
FEATURE [Part::Feature] Part__Feature246  label="COMPOUND026"
  shape: bbox 1.3 x 1.3 x 0.1 mm, 4 faces (baked)
FEATURE [Part::Feature] Part__Feature247  label="COMPOUND027"
  shape: bbox 1.3 x 1.3 x 0.1 mm, 4 faces (baked)
FEATURE [Part::Feature] Part__Feature248  label="COMPOUND028"
  shape: bbox 1.3 x 1.3 x 0.1 mm, 4 faces (baked)
FEATURE [Part::Feature] Part__Feature249  label="COMPOUND029"
  shape: bbox 1.3 x 1.3 x 0.1 mm, 4 faces (baked)
FEATURE [Part::Feature] Part__Feature250  label="COMPOUND030"
  shape: bbox 1.3 x 1.3 x 0.1 mm, 4 faces (baked)
FEATURE [Part::Feature] Part__Feature251  label="COMPOUND031"
  shape: bbox 1.3 x 1.3 x 0.1 mm, 4 faces (baked)
FEATURE [Part::Feature] Part__Feature252  label="COMPOUND032"
  shape: bbox 1.3 x 1.3 x 0.1 mm, 4 faces (baked)
FEATURE [Part::Feature] Part__Feature253  label="COMPOUND033"
  shape: bbox 1.3 x 1.3 x 0.1 mm, 4 faces (baked)
FEATURE [Part::Feature] Part__Feature254  label="COMPOUND034"
  shape: bbox 1.3 x 1.3 x 0.1 mm, 4 faces (baked)
FEATURE [Part::Feature] Part__Feature255  label="COMPOUND035"
  shape: bbox 1.3 x 1.3 x 0.1 mm, 4 faces (baked)
FEATURE [Part::Feature] Part__Feature256  label="COMPOUND036"
  shape: bbox 1.3 x 1.3 x 0.1 mm, 4 faces (baked)
FEATURE [Part::Feature] Part__Feature257  label="COMPOUND037"
  shape: bbox 1.3 x 1.3 x 0.1 mm, 4 faces (baked)
FEATURE [Part::Feature] Part__Feature258  label="COMPOUND038"
  shape: bbox 1.3 x 1.3 x 0.1 mm, 4 faces (baked)
FEATURE [Part::Feature] Part__Feature259  label="COMPOUND039"
  shape: bbox 1.3 x 1.3 x 0.1 mm, 4 faces (baked)
FEATURE [Part::Feature] Part__Feature260  label="COMPOUND040"
  shape: bbox 1.3 x 1.3 x 0.1 mm, 4 faces (baked)
FEATURE [Part::Feature] Part__Feature261  label="COMPOUND041"
  shape: bbox 1.3 x 1.3 x 0.1 mm, 4 faces (baked)
FEATURE [Part::Feature] Part__Feature262  label="COMPOUND042"
  shape: bbox 1.3 x 1.3 x 0.1 mm, 4 faces (baked)
FEATURE [Part::Feature] Part__Feature263  label="COMPOUND043"
  shape: bbox 1.3 x 1.3 x 0.1 mm, 4 faces (baked)
FEATURE [Part::Feature] Part__Feature264  label="COMPOUND044"
  shape: bbox 1.3 x 1.3 x 0.1 mm, 4 faces (baked)
FEATURE [Part::Feature] Part__Feature265  label="COMPOUND045"
  shape: bbox 1.3 x 1.3 x 0.1 mm, 4 faces (baked)
FEATURE [Part::Feature] Part__Feature266  label="COMPOUND046"
  shape: bbox 1.3 x 1.3 x 0.1 mm, 4 faces (baked)
FEATURE [Part::Feature] Part__Feature267  label="COMPOUND047"
  shape: bbox 1.3 x 1.3 x 0.1 mm, 4 faces (baked)
FEATURE [Part::Feature] Part__Feature268  label="COMPOUND048"
  shape: bbox 1.3 x 1.3 x 0.1 mm, 4 faces (baked)
FEATURE [Part::Feature] Part__Feature269  label="COMPOUND049"
  shape: bbox 1.3 x 1.3 x 0.1 mm, 4 faces (baked)
FEATURE [Part::Feature] Part__Feature270  label="COMPOUND050"
  shape: bbox 1.3 x 1.3 x 0.1 mm, 4 faces (baked)
FEATURE [Part::Feature] Part__Feature271  label="COMPOUND051"
  shape: bbox 1.3 x 1.3 x 0.1 mm, 4 faces (baked)
FEATURE [Part::Feature] Part__Feature272  label="COMPOUND052"
  shape: bbox 4.7 x 4.7 x 3 mm, 6 faces (baked)
FEATURE [Part::Feature] Part__Feature273  label="COMPOUND053"
  shape: bbox 1.3 x 1.3 x 0.1 mm, 4 faces (baked)
FEATURE [Part::Feature] Part__Feature274  label="COMPOUND054"
  shape: bbox 1.3 x 1.3 x 0.1 mm, 4 faces (baked)
FEATURE [Part::Feature] Part__Feature275  label="COMPOUND055"
  shape: bbox 1.3 x 1.3 x 0.1 mm, 4 faces (baked)
FEATURE [Part::Feature] Part__Feature276  label="COMPOUND056"
  shape: bbox 1.3 x 1.3 x 0.1 mm, 4 faces (baked)
FEATURE [Part::Feature] Part__Feature277  label="COMPOUND057"
  shape: bbox 1.3 x 1.3 x 0.1 mm, 4 faces (baked)
FEATURE [Part::Feature] Part__Feature278  label="COMPOUND058"
  shape: bbox 1.3 x 1.3 x 0.1 mm, 4 faces (baked)
FEATURE [Part::Feature] Part__Feature279  label="COMPOUND059"
  shape: bbox 1.3 x 1.3 x 0.1 mm, 4 faces (baked)
FEATURE [Part::Feature] Part__Feature280  label="COMPOUND060"
  shape: bbox 1.3 x 1.3 x 0.1 mm, 4 faces (baked)
FEATURE [Part::Feature] Part__Feature281  label="COMPOUND061"
  shape: bbox 1.3 x 1.3 x 0.1 mm, 4 faces (baked)
FEATURE [Part::Feature] Part__Feature282  label="COMPOUND062"
  shape: bbox 1.3 x 1.3 x 0.1 mm, 4 faces (baked)
FEATURE [Part::Feature] Part__Feature283  label="COMPOUND063"
  shape: bbox 1.3 x 1.3 x 0.1 mm, 4 faces (baked)
FEATURE [Part::Feature] Part__Feature284  label="COMPOUND064"
  shape: bbox 1.3 x 1.3 x 0.1 mm, 4 faces (baked)
FEATURE [Part::Feature] Part__Feature285  label="COMPOUND065"
  shape: bbox 1.3 x 1.3 x 0.1 mm, 4 faces (baked)
FEATURE [Part::Feature] Part__Feature286  label="COMPOUND066"
  shape: bbox 1.3 x 1.3 x 0.1 mm, 4 faces (baked)
FEATURE [App::Part] COMPOUND004  label="COMPOUND067"
  Group = -> [Part__Feature232,Part__Feature233,Part__Feature234,Part__Feature235,Part__Feature236,Part__Feature237,Part__Feature238,Part__Feature239,Part__Feature240,Part__Feature241,Part__Feature242,Part__Feature243,Part__Feature244,Part__Feature245,Part__Feature246,Part__Feature247,Part__Feature248,Part__Feature249,Part__Feature250,Part__Feature251,Part__Feature252,Part__Feature253,Part__Feature254,+32 more]
  Origin = -> Origin057
FEATURE [Part::Feature] Part__Feature287  label="COMPOUND068"
  shape: bbox 35.5 x 1.4 x 17.7 mm, 74 faces (baked)
FEATURE [Part::Feature] Part__Feature288  label="COMPOUND069"
  shape: bbox 4.2 x 1.55 x 0.3 mm, 15 faces (baked)
FEATURE [Part::Feature] Part__Feature289  label="COMPOUND070"
  shape: bbox 4.2 x 1.55 x 0.3 mm, 15 faces (baked)
FEATURE [Part::Feature] Part__Feature290  label="COMPOUND071"
  shape: bbox 4.2 x 1.55 x 0.3 mm, 15 faces (baked)
FEATURE [Part::Feature] Part__Feature291  label="COMPOUND072"
  shape: bbox 4.2 x 1.55 x 0.3 mm, 15 faces (baked)
FEATURE [Part::Feature] Part__Feature292  label="COMPOUND073"
  shape: bbox 4.2 x 1.55 x 0.3 mm, 15 faces (baked)
FEATURE [Part::Feature] Part__Feature293  label="COMPOUND074"
  shape: bbox 4.15 x 2.4 x 6.9 mm, 176 faces (baked)
FEATURE [Part::Feature] Part__Feature294  label="COMPOUND075"
  shape: bbox 5.619 x 3.786 x 8.172 mm, 257 faces (baked)
FEATURE [Part::Feature] Part__Feature295  label="COMPOUND076"
  shape: bbox 10 x 1.52 x 10 mm, 6 faces (baked)
FEATURE [Part::Feature] Part__Feature296  label="COMPOUND077"
  shape: bbox 4.893 x 2.55 x 3.225 mm, 149 faces (baked)
FEATURE [App::Part] COMPOUND005  label="COMPOUND078"
  Group = -> [Part__Feature287,Part__Feature288,Part__Feature289,Part__Feature290,Part__Feature291,Part__Feature292,Part__Feature293,Part__Feature294,Part__Feature295,Part__Feature296]
  Origin = -> Origin059
FEATURE [Part::Feature] Part__Feature297  label="SOLID015"
  shape: bbox 7.874 x 9.27 x 6.98 mm, 148 faces (baked)
FEATURE [App::Part] DIP_8_W7_62mm  label="DIP-8_W7.62mm"
  Group = -> [Part__Feature297]
  Origin = -> Origin061
  Placement = pos=(70.519,-20.422,1.65) rot=(0,0,-1;1.5708rad)
FEATURE [Part::Feature] Part__Feature298  label="SOLID016"
  shape: bbox 3.2 x 1.6 x 1.6 mm, 28 faces (baked)
FEATURE [App::Part] C_1206_3216Metric003
  Group = -> [Part__Feature298]
  Origin = -> Origin062
  Placement = pos=(59.425,-25.475,1.65) rot=(0,0,1;1.5708rad)
FEATURE [Part::Feature] Part__Feature299  label="SOLID017"
  shape: bbox 3.2 x 1.6 x 1.6 mm, 28 faces (baked)
FEATURE [App::Part] C_1206_3216Metric004
  Group = -> [Part__Feature299]
  Origin = -> Origin063
  Placement = pos=(59.552,-38.583,1.65) rot=(0,0,1;0rad)
FEATURE [Part::Feature] Part__Feature300  label="SOLID018"
  shape: bbox 4.83 x 3.745 x 9.8 mm, 23 faces (baked)
FEATURE [Part::Feature] Part__Feature301  label="SOLID019"
  shape: bbox 9.9 x 5.75 x 10.4 mm, 117 faces (baked)
FEATURE [App::Part] JST_XH_B3B_XH_A_1x03_P2_50mm_Vertical  label="JST_XH_B3B-XH-A_1x03_P2.50mm_Vertical"
  Group = -> [Part__Feature301]
  Origin = -> Origin065
  Placement = pos=(52.766,-32.183,-0.05) rot=(0.707107,0.707107,0;3.14159rad)
FEATURE [Part::Feature] Part__Feature302  label="_autosave-AFPI Device V1.1 PCB"
  shape: bbox 85 x 45 x 1.6 mm, 102 faces (baked)
FEATURE [Part::Feature] Path
  shape: bbox 180.6 x 86.08 x 2e-07 mm, 1 faces, 0 solids (baked)
FEATURE [Part::Feature] Path001
  shape: bbox 17.99 x 36.34 x 2e-07 mm, 1 faces, 0 solids (baked)
FEATURE [Part::Feature] Path002
  shape: bbox 129.5 x 129.9 x 2e-07 mm, 1 faces, 0 solids (baked)
FEATURE [Part::FeaturePython] Clone  label="Path003"  # Draft clone (typed FeaturePython)
  AttacherType = Attacher::AttachEngine3D
  Fuse = false
  Objects = -> [Path002,Path,Path001]
  Placement = pos=(-28.9278,29.2503,27.7988) rot=(0,0,1;0rad)
  Scale = (0.04,0.04,0.04)
FEATURE [App::Part] Pushbutton_v16  label="Home SW"
  Group = -> [Part__Feature205,Part__Feature206,Part__Feature207,Part__Feature208,Part__Feature209,Part__Feature210,Part__Feature211]
  Origin = -> Origin042
  Placement = pos=(-24.3,43.2,15.9) rot=(0,1,0;3.14159rad)
FEATURE [App::Part] R_1206_3216Metric
  Group = -> [Part__Feature225]
  Origin = -> Origin050
  Placement = pos=(75.257,-6.833,1.65) rot=(0,0,1;3.14159rad)
FEATURE [App::Part] R_1206_3216Metric001
  Group = -> [Part__Feature230]
  Origin = -> Origin055
  Placement = pos=(65.267,-8.24,1.65) rot=(0,0,1;1.5708rad)
FEATURE [App::Part] R_1206_3216Metric002
  Group = -> [Part__Feature231]
  Origin = -> Origin056
  Placement = pos=(64.589,-38.583,1.65) rot=(0,0,1;3.14159rad)
FEATURE [App::Part] SOT_223  label="SOT-223"
  Group = -> [Part__Feature228]
  Origin = -> Origin053
  Placement = pos=(7.664,-12.03,1.65) rot=(0,0,1;1.5708rad)
FEATURE [App::Part] SW_PEC11R_4215F_S0024  label="SW-PEC11R-4215F-S0024"
  Group = -> [Part__Feature,COMPOUND]
  Origin = -> Origin010
  Placement = pos=(9.53,10.79,0) rot=(0.707107,0.707107,0;3.14159rad)
FEATURE [App::Part] SW_PEC11R_4215F_S0025  label="SW-PEC11R-4215F-S0025"
  Group = -> [Part__Feature003,COMPOUND001]
  Origin = -> Origin012
  Placement = pos=(28.57,10.79,0.05) rot=(0.707107,0.707107,0;3.14159rad)
FEATURE [App::Part] SW_PEC11R_4215F_S0026  label="SW-PEC11R-4215F-S0026"
  Group = -> [Part__Feature006,COMPOUND002]
  Origin = -> Origin014
  Placement = pos=(47.63,10.79,0.05) rot=(0.707107,0.707107,0;3.14159rad)
FEATURE [App::Part] SW_PEC11R_4215F_S0027  label="SW-PEC11R-4215F-S0027"
  Group = -> [Part__Feature009,COMPOUND003]
  Origin = -> Origin016
  Placement = pos=(66.67,10.79,0.05) rot=(0.707107,0.707107,0;3.14159rad)
FEATURE [Part::Part2DObjectPython] ShapeString  # Draft 2D object (typed FeaturePython)
  FontFile = <path>
  MakeFace = true
  Placement = pos=(46.09,3.49,-4.88) rot=(0,1,0;3.14159rad)
  Size = 2
  String = 2.42 OLED I2C Display
  Tracking = 0
FEATURE [Part::Extrusion] Extrude004
  Base = -> ShapeString
  Dir = (0,0,-1)
  DirMode = 2
  FaceMakerClass = Part::FaceMakerBullseye
  LengthFwd = 0.3
  LengthRev = 0
  Placement = pos=(0,0,4.7) rot=(0,0,1;0rad)
  Solid = false
  Symmetric = false
FEATURE [Sketcher::SketchObject] Sketch038  label="Disp PCB Outer"
  FullyConstrained = false
  MapMode = 5
  Support = -> [XY_Plane007]
  sketch-geometry (4):
    g0: LineSegment StartX=-10 StartY=-12.8284 StartZ=0 EndX=60 EndY=-12.8284 EndZ=0
    g1: LineSegment StartX=60 StartY=-12.8284 StartZ=0 EndX=60 EndY=35.1716 EndZ=0
    g2: LineSegment StartX=60 StartY=35.1716 StartZ=0 EndX=-10 EndY=35.1716 EndZ=0
    g3: LineSegment StartX=-10 StartY=35.1716 StartZ=0 EndX=-10 EndY=-12.8284 EndZ=0
  constraints (10):
    c: Coincident(g0,g1)
    c: Coincident(g1,g2)
    c: Coincident(g2,g3)
    c: Coincident(g3,g0)
    c: Horizontal(g0)
    c: Horizontal(g2)
    c: Vertical(g1)
    c: Vertical(g3)
    c: DistanceX(g2,g2) = 70
    c: DistanceY(g3,g3) = 48
FEATURE [Part::Extrusion] Extrude
  Base = -> Sketch038
  Dir = (0,0,1)
  DirMode = 2
  FaceMakerClass = Part::FaceMakerBullseye
  LengthFwd = 1.2
  LengthRev = 0
  Solid = true
  Symmetric = false
FEATURE [Sketcher::SketchObject] Sketch039  label="Disp screen Outer"
  FullyConstrained = false
  MapMode = 5
  Placement = pos=(0,0,1.2) rot=(0,0,1;0rad)
  Support = -> [Extrude]
  sketch-geometry (8):
    g0: LineSegment StartX=-10 StartY=35.18 StartZ=0 EndX=-6 EndY=35.18 EndZ=0
    g1: LineSegment StartX=-6 StartY=35.18 StartZ=0 EndX=-6 EndY=31.18 EndZ=0
    g2: LineSegment StartX=60 StartY=-12.8284 StartZ=0 EndX=56 EndY=-12.8284 EndZ=0
    g3: LineSegment StartX=56 StartY=-12.8284 StartZ=0 EndX=56 EndY=-8.83 EndZ=0
    g4: LineSegment StartX=56 StartY=-8.83 StartZ=0 EndX=-6 EndY=-8.83 EndZ=0
    g5: LineSegment StartX=-6 StartY=-8.83 StartZ=0 EndX=-6 EndY=31.18 EndZ=0
    g6: LineSegment StartX=-6 StartY=31.18 StartZ=0 EndX=56 EndY=31.18 EndZ=0
    g7: LineSegment StartX=56 StartY=31.18 StartZ=0 EndX=56 EndY=-8.83 EndZ=0
  constraints (20):
    c: Horizontal(g0)
    c: DistanceX(g0,g0) = 4
    c: Coincident(g1,g0)
    c: Vertical(g1)
    c: DistanceY(g1,g1) = 4
    c: Horizontal(g2)
    c: DistanceX(g2,g2) = 4
    c: Vertical(g3)
    c: Coincident(g4,g5)
    c: Coincident(g5,g6)
    c: Coincident(g6,g7)
    c: Coincident(g7,g4)
    c: Horizontal(g4)
    c: Horizontal(g6)
    c: Vertical(g5)
    c: Vertical(g7)
    c: Coincident(g4,g3)
    c: Coincident(g5,g1)
    c: DistanceX(g6,g6) = 62
    c: DistanceY(g5,g5) = 40.01
FEATURE [Part::Extrusion] Extrude002
  Base = -> Sketch039
  Dir = (0,0,1)
  DirMode = 2
  FaceMakerClass = Part::FaceMakerBullseye
  LengthFwd = 3
  LengthRev = 0
  Solid = true
  Symmetric = false
FEATURE [Sketcher::SketchObject] Sketch040  label="Disp Glass"
  FullyConstrained = false
  MapMode = 5
  Placement = pos=(0,0,4.2) rot=(0,0,1;0rad)
  Support = -> [Extrude002]
  sketch-geometry (8):
    g0: LineSegment StartX=-6 StartY=31.18 StartZ=0 EndX=-3.4 EndY=31.18 EndZ=0
    g1: LineSegment StartX=-3.4 StartY=31.18 StartZ=0 EndX=-3.4 EndY=29.28 EndZ=0
    g2: LineSegment StartX=56 StartY=-8.83 StartZ=0 EndX=53.7 EndY=-8.83 EndZ=0
    g3: LineSegment StartX=53.7 StartY=-8.83 StartZ=0 EndX=53.7 EndY=-1.38 EndZ=0
    g4: LineSegment StartX=-3.4 StartY=29.28 StartZ=0 EndX=53.7 EndY=29.28 EndZ=0
    g5: LineSegment StartX=53.7 StartY=29.28 StartZ=0 EndX=53.7 EndY=-1.38 EndZ=0
    g6: LineSegment StartX=53.7 StartY=-1.38 StartZ=0 EndX=-3.4 EndY=-1.38 EndZ=0
    g7: LineSegment StartX=-3.4 StartY=-1.38 StartZ=0 EndX=-3.4 EndY=29.28 EndZ=0
  constraints (22):
    c: Horizontal(g0)
    c: DistanceX(g0,g0) = 2.6
    c: Coincident(g1,g0)
    c: Vertical(g1)
    c: DistanceY(g1,g1) = 1.9
    c: Horizontal(g2)
    c: DistanceX(g2,g2) = 2.3
    c: Coincident(g3,g2)
    c: Vertical(g3)
    c: DistanceY(g3,g3) = 7.45
    c: Coincident(g4,g5)
    c: Coincident(g5,g6)
    c: Coincident(g6,g7)
    c: Coincident(g7,g4)
    c: Horizontal(g4)
    c: Horizontal(g6)
    c: Vertical(g5)
    c: Vertical(g7)
    c: Coincident(g4,g1)
    c: Coincident(g5,g3)
    c: DistanceY(g5,g5) = 30.66
    c: DistanceX(g6,g6) = 57.1
FEATURE [Part::Extrusion] Extrude003
  Base = -> Sketch040
  Dir = (0,0,1)
  DirMode = 2
  FaceMakerClass = Part::FaceMakerBullseye
  LengthFwd = 0.1
  LengthRev = 0
  Solid = true
  Symmetric = false
FEATURE [Sketcher::SketchObject] Sketch041  label="Disp Mounting Holes"
  FullyConstrained = false
  MapMode = 5
  Placement = pos=(0,0,1.2) rot=(0,0,1;0rad)
  Support = -> [Extrude]
  sketch-geometry (12):
    g0: Circle CenterX=-7.75 CenterY=32.92 CenterZ=0 NormalX=0 NormalY=0 NormalZ=1 AngleXU=0 Radius=1.25
    g1: LineSegment StartX=-10 StartY=35.1716 StartZ=0 EndX=-10 EndY=32.9216 EndZ=0
    g2: LineSegment StartX=-10 StartY=32.922 StartZ=0 EndX=-9 EndY=32.922 EndZ=0
    g3: Circle CenterX=57.7504 CenterY=32.922 CenterZ=0 NormalX=0 NormalY=0 NormalZ=1 AngleXU=0 Radius=1.25
    g4: LineSegment StartX=60 StartY=35.1715 StartZ=0 EndX=60 EndY=32.9215 EndZ=0
    g5: LineSegment StartX=60 StartY=32.9215 StartZ=0 EndX=59 EndY=32.9215 EndZ=0
    g6: LineSegment StartX=-10 StartY=-12.8284 StartZ=0 EndX=-10 EndY=-10.5284 EndZ=0
    g7: LineSegment StartX=-10 StartY=-10.5284 StartZ=0 EndX=-9 EndY=-10.5284 EndZ=0
    g8: LineSegment StartX=60 StartY=-12.8278 StartZ=0 EndX=60 EndY=-10.5278 EndZ=0
    g9: LineSegment StartX=60 StartY=-10.5278 StartZ=0 EndX=59 EndY=-10.5278 EndZ=0
    g10: Circle CenterX=57.75 CenterY=-10.5274 CenterZ=0 NormalX=0 NormalY=0 NormalZ=1 AngleXU=0 Radius=1.25
    g11: Circle CenterX=-7.75 CenterY=-10.53 CenterZ=0 NormalX=0 NormalY=0 NormalZ=1 AngleXU=0 Radius=1.25
  constraints (23):
    c: Diameter(g0) = 2.5
    c: Vertical(g1)
    c: DistanceY(g1,g1) = 2.25
    c: Horizontal(g2)
    c: DistanceX(g2,g2) = 1
    c: Diameter(g3) = 2.5
    c: Vertical(g4)
    c: DistanceY(g4,g4) = 2.25
    c: Coincident(g5,g4)
    c: Horizontal(g5)
    c: DistanceX(g5,g5) = 1
    c: Vertical(g6)
    c: DistanceY(g6,g6) = 2.3
    c: Coincident(g7,g6)
    c: Horizontal(g7)
    c: DistanceX(g7,g7) = 1
    c: Vertical(g8)
    c: DistanceY(g8,g8) = 2.3
    c: Coincident(g9,g8)
    c: Horizontal(g9)
    c: DistanceX(g9,g9) = 1
    c: Diameter(g10) = 2.5
    c: Diameter(g11) = 2.5
FEATURE [PartDesign::Hole] Hole
  CustomThreadClearance = 0
  Depth = 3
  DepthType = 0
  Diameter = 2.5
  DrillForDepth = false
  DrillPoint = 0
  DrillPointAngle = 118
  HoleCutCountersinkAngle = 90
  HoleCutCustomValues = false
  HoleCutDepth = 0
  HoleCutDiameter = 6.1
  HoleCutType = 0
  ModelThread = false
  Profile = -> Sketch041
  Tapered = false
  TaperedAngle = 90
  ThreadClass = 0
  ThreadDepth = 3
  ThreadDepthType = 0
  ThreadDirection = 0
  ThreadFit = 0
  ThreadSize = 0
  ThreadType = 0
  Threaded = false
  UseCustomThreadClearance = false
FEATURE [App::Part] Part005  label="2.42 OLED Display"
  Group = -> [Body002,Hole,Extrude002,Extrude003,Sketch039,Sketch038,Sketch041,Sketch040,Extrude,ShapeString,Extrude004]
  Origin = -> Origin008
  Placement = pos=(-2,75.6,0) rot=(0,0,1;0rad)
FEATURE [Sketcher::SketchObject] Sketch047  label="Enclosure Walling"
  FullyConstrained = false
  MapMode = 5
  Support = -> [XY_Plane075]
  sketch-geometry (22):
    g0: LineSegment StartX=-10 StartY=32.398 StartZ=0 EndX=-10 EndY=110.768 EndZ=0
    g1: LineSegment StartX=-10 StartY=32.398 StartZ=0 EndX=-10 EndY=29.078 EndZ=0
    g2: LineSegment StartX=-10 StartY=110.768 StartZ=0 EndX=-10 EndY=114.078 EndZ=0
    g3: LineSegment StartX=-30.9 StartY=43.2 StartZ=0 EndX=60 EndY=43.2 EndZ=0
    g4: LineSegment StartX=60 StartY=43.2 StartZ=0 EndX=63.1 EndY=43.2 EndZ=0
    g5: LineSegment StartX=-30.9 StartY=43.2 StartZ=0 EndX=-33.9 EndY=43.2 EndZ=0
    g6: LineSegment StartX=-33.9 StartY=43.2 StartZ=0 EndX=-33.9 EndY=140 EndZ=0
    g7: LineSegment StartX=-10 StartY=114.078 StartZ=0 EndX=-33.9 EndY=114.078 EndZ=0
    g8: LineSegment StartX=-10 StartY=29.078 StartZ=0 EndX=70 EndY=29.078 EndZ=0
    g9: LineSegment StartX=63.1 StartY=43.2 StartZ=0 EndX=63.1 EndY=29.078 EndZ=0
    g10: LineSegment StartX=-33.9 StartY=114.078 StartZ=0 EndX=63.1 EndY=114.078 EndZ=0
    g11: LineSegment StartX=63.1 StartY=114.078 StartZ=0 EndX=63.1 EndY=29.078 EndZ=0
    g12: LineSegment StartX=63.1 StartY=29.078 StartZ=0 EndX=-33.9 EndY=29.078 EndZ=0
    g13: LineSegment StartX=-33.9 StartY=29.078 StartZ=0 EndX=-33.9 EndY=114.078 EndZ=0
    g14: LineSegment StartX=-33.9 StartY=29.078 StartZ=0 EndX=-33.9 EndY=26.58 EndZ=0
    g15: LineSegment StartX=-33.9 StartY=26.58 StartZ=0 EndX=-36.4 EndY=26.58 EndZ=0
    g16: LineSegment StartX=63.1 StartY=114.078 StartZ=0 EndX=65.6 EndY=114.078 EndZ=0
    g17: LineSegment StartX=65.6 StartY=114.078 StartZ=0 EndX=65.6 EndY=116.58 EndZ=0
    g18: LineSegment StartX=-36.4 StartY=26.58 StartZ=0 EndX=65.6 EndY=26.58 EndZ=0
    g19: LineSegment StartX=65.6 StartY=26.58 StartZ=0 EndX=65.6 EndY=116.58 EndZ=0
    g20: LineSegment StartX=65.6 StartY=116.58 StartZ=0 EndX=-36.4 EndY=116.58 EndZ=0
    g21: LineSegment StartX=-36.4 StartY=116.58 StartZ=0 EndX=-36.4 EndY=26.58 EndZ=0
  constraints (52):
    c: Vertical(g0)
    c: Coincident(g1,g0)
    c: Vertical(g1)
    c: Coincident(g2,g0)
    c: Vertical(g2)
    c: Horizontal(g3)
    c: Coincident(g4,g3)
    c: Horizontal(g4)
    c: Coincident(g5,g3)
    c: Horizontal(g5)
    c: Coincident(g6,g5)
    c: Vertical(g6)
    c: Coincident(g7,g2)
    c: PointOnObject(g7,g6)
    c: Horizontal(g7)
    c: Coincident(g8,g1)
    c: Horizontal(g8)
    c: Coincident(g9,g4)
    c: PointOnObject(g9,g8)
    c: Vertical(g9)
    c: Coincident(g10,g11)
    c: Coincident(g11,g12)
    c: Coincident(g12,g13)
    c: Coincident(g13,g10)
    c: Horizontal(g10)
    c: Horizontal(g12)
    c: Vertical(g11)
    c: Vertical(g13)
    c: Coincident(g10,g7)
    c: Coincident(g11,g9)
    c: DistanceX(g10,g10) = 97
    c: DistanceY(g13,g13) = 85
    c: Coincident(g14,g12)
    c: Vertical(g14)
    c: Coincident(g15,g14)
    c: Horizontal(g15)
    c: Coincident(g16,g10)
    c: Horizontal(g16)
    c: Coincident(g17,g16)
    c: Vertical(g17)
    c: Coincident(g18,g19)
    c: Coincident(g19,g20)
    c: Coincident(g20,g21)
    c: Coincident(g21,g18)
    c: Horizontal(g18)
    c: Horizontal(g20)
    c: Vertical(g19)
    c: Vertical(g21)
    c: Coincident(g18,g15)
    c: Coincident(g19,g17)
    c: DistanceX(g20,g20) = 102
    c: DistanceY(g19,g19) = 90
FEATURE [Part::Extrusion] Extrude009  label="Walls"
  Base = -> Sketch047
  Dir = (0,0,1)
  DirMode = 2
  FaceMakerClass = Part::FaceMakerBullseye
  LengthFwd = 45
  LengthRev = 0
  Reversed = true
  Solid = true
  Symmetric = false
FEATURE [Sketcher::SketchObject] Sketch048  label="Main Top Plate"
  FullyConstrained = false
  MapMode = 5
  Support = -> [XY_Plane072]
  sketch-geometry (8):
    g0: LineSegment StartX=-44.45 StartY=26.7053 StartZ=0 EndX=-47.45 EndY=26.7053 EndZ=0
    g1: LineSegment StartX=-44.45 StartY=26.7053 StartZ=0 EndX=-44.45 EndY=23.701 EndZ=0
    g2: LineSegment StartX=74.55 StartY=116.705 StartZ=0 EndX=77.55 EndY=116.705 EndZ=0
    g3: LineSegment StartX=77.55 StartY=116.705 StartZ=0 EndX=77.55 EndY=119.704 EndZ=0
    g4: LineSegment StartX=77.55 StartY=119.704 StartZ=0 EndX=-47.4504 EndY=119.704 EndZ=0
    g5: LineSegment StartX=-47.4504 StartY=119.704 StartZ=0 EndX=-47.4504 EndY=23.7 EndZ=0
    g6: LineSegment StartX=-47.4504 StartY=23.7 StartZ=0 EndX=77.55 EndY=23.7 EndZ=0
    g7: LineSegment StartX=77.55 StartY=23.7 StartZ=0 EndX=77.55 EndY=119.704 EndZ=0
  constraints (15):
    c: Horizontal(g0)
    c: Coincident(g1,g0)
    c: Vertical(g1)
    c: Horizontal(g2)
    c: Coincident(g3,g2)
    c: Vertical(g3)
    c: Coincident(g4,g5)
    c: Coincident(g5,g6)
    c: Coincident(g6,g7)
    c: Coincident(g7,g4)
    c: Horizontal(g4)
    c: Horizontal(g6)
    c: Vertical(g5)
    c: Vertical(g7)
    c: Coincident(g4,g3)
FEATURE [Part::Extrusion] Extrude013  label="bare plate"
  Base = -> Sketch048
  Dir = (0,0,1)
  DirMode = 2
  FaceMakerClass = Part::FaceMakerBullseye
  LengthFwd = 3
  LengthRev = 0
  Solid = true
  Symmetric = false
FEATURE [PartDesign::FeatureBase] BaseFeature
  BaseFeature = -> Extrude013
FEATURE [Sketcher::SketchObject] Sketch042  label="Home Button Hole"
  FullyConstrained = false
  MapMode = 5
  Placement = pos=(0,0,3) rot=(0,0,1;0rad)
  Support = -> [Extrude013]
  sketch-geometry (2):
    g0: LineSegment StartX=-25.4 StartY=48.2 StartZ=0 EndX=-25.4 EndY=43.2 EndZ=0
    g1: Circle CenterX=-25.4 CenterY=43.2 CenterZ=0 NormalX=0 NormalY=0 NormalZ=1 AngleXU=0 Radius=3.75
  constraints (3):
    c: Vertical(g0)
    c: Coincident(g1,g0)
    c: Diameter(g1) = 7.5
FEATURE [PartDesign::Hole] Hole001
  BaseFeature = -> BaseFeature
  CustomThreadClearance = 0
  Depth = 3
  DepthType = 0
  Diameter = 7.5
  DrillForDepth = false
  DrillPoint = 0
  DrillPointAngle = 118
  HoleCutCountersinkAngle = 90
  HoleCutCustomValues = false
  HoleCutDepth = 0
  HoleCutDiameter = 6.1
  HoleCutType = 0
  ModelThread = false
  Profile = -> Sketch042
  Tapered = false
  TaperedAngle = 90
  ThreadClass = 0
  ThreadDepth = 3
  ThreadDepthType = 0
  ThreadDirection = 0
  ThreadFit = 0
  ThreadSize = 0
  ThreadType = 0
  Threaded = false
  UseCustomThreadClearance = false
FEATURE [Sketcher::SketchObject] Sketch043  label="Power Switch Hole"
  FullyConstrained = false
  MapMode = 5
  Placement = pos=(0,0,3) rot=(0,0,1;0rad)
  Support = -> [Hole001]
  sketch-geometry (1):
    g0: Circle CenterX=-25.3 CenterY=87.77 CenterZ=0 NormalX=0 NormalY=0 NormalZ=1 AngleXU=0 Radius=3.25
  constraints (1):
    c: Diameter(g0) = 6.5
FEATURE [PartDesign::Hole] Hole002
  BaseFeature = -> Hole001
  CustomThreadClearance = 0
  Depth = 3
  DepthType = 0
  Diameter = 6.5
  DrillForDepth = false
  DrillPoint = 0
  DrillPointAngle = 118
  HoleCutCountersinkAngle = 90
  HoleCutCustomValues = false
  HoleCutDepth = 0
  HoleCutDiameter = 6.1
  HoleCutType = 0
  ModelThread = false
  Profile = -> Sketch043
  Tapered = false
  TaperedAngle = 90
  ThreadClass = 0
  ThreadDepth = 3
  ThreadDepthType = 0
  ThreadDirection = 0
  ThreadFit = 0
  ThreadSize = 0
  ThreadType = 0
  Threaded = false
  UseCustomThreadClearance = false
FEATURE [Sketcher::SketchObject] Sketch045  label="Rot Enc Holes"
  FullyConstrained = false
  MapMode = 5
  Placement = pos=(0,0,3) rot=(0,0,1;0rad)
  Support = -> [Hole002]
  sketch-geometry (10):
    g0: LineSegment StartX=31.43 StartY=51.71 StartZ=0 EndX=31.43 EndY=44.71 EndZ=0
    g1: LineSegment StartX=50.47 StartY=44.71 StartZ=0 EndX=50.47 EndY=51.71 EndZ=0
    g2: LineSegment StartX=-6.67 StartY=48.2 StartZ=0 EndX=-6.67 EndY=43.2 EndZ=0
    g3: Circle CenterX=-6.67 CenterY=43.2 CenterZ=0 NormalX=0 NormalY=0 NormalZ=1 AngleXU=0 Radius=3.75
    g4: LineSegment StartX=12.3686 StartY=48.2 StartZ=0 EndX=12.3686 EndY=43.2 EndZ=0
    g5: Circle CenterX=12.3686 CenterY=43.2 CenterZ=0 NormalX=0 NormalY=0 NormalZ=1 AngleXU=0 Radius=3.75
    g6: LineSegment StartX=31.43 StartY=48.2 StartZ=0 EndX=31.43 EndY=43.2 EndZ=0
    g7: Circle CenterX=31.43 CenterY=43.2 CenterZ=0 NormalX=0 NormalY=0 NormalZ=1 AngleXU=0 Radius=3.75
    g8: LineSegment StartX=50.47 StartY=48.2 StartZ=0 EndX=50.47 EndY=43.2 EndZ=0
    g9: Circle CenterX=50.47 CenterY=43.2 CenterZ=0 NormalX=0 NormalY=0 NormalZ=1 AngleXU=0 Radius=3.75
  constraints (15):
    c: Vertical(g0)
    c: Vertical(g1)
    c: Vertical(g2)
    c: Diameter(g3) = 7.5
    c: DistanceY(g2,g2) = 5
    c: Vertical(g4)
    c: DistanceY(g4,g4) = 5
    c: Coincident(g5,g4)
    c: Diameter(g5) = 7.5
    c: Vertical(g6)
    c: Coincident(g7,g6)
    c: Diameter(g7) = 7.5
    c: Vertical(g8)
    c: Coincident(g9,g8)
    c: Diameter(g9) = 7.5
FEATURE [PartDesign::Hole] Hole003
  BaseFeature = -> Hole002
  CustomThreadClearance = 0
  Depth = 3
  DepthType = 0
  Diameter = 7.5
  DrillForDepth = false
  DrillPoint = 0
  DrillPointAngle = 118
  HoleCutCountersinkAngle = 90
  HoleCutCustomValues = false
  HoleCutDepth = 0
  HoleCutDiameter = 6.1
  HoleCutType = 0
  ModelThread = false
  Profile = -> Sketch045
  Tapered = false
  TaperedAngle = 90
  ThreadClass = 0
  ThreadDepth = 3
  ThreadDepthType = 0
  ThreadDirection = 0
  ThreadFit = 0
  ThreadSize = 0
  ThreadType = 0
  Threaded = false
  UseCustomThreadClearance = false
FEATURE [Sketcher::SketchObject] Sketch044  label="Display Mounting Hole"
  FullyConstrained = false
  MapMode = 5
  Placement = pos=(0,0,3) rot=(0,0,1;0rad)
  Support = -> [Hole003]
  sketch-geometry (4):
    g0: Circle CenterX=-10.85 CenterY=65.07 CenterZ=0 NormalX=0 NormalY=0 NormalZ=1 AngleXU=0 Radius=1.25
    g1: Circle CenterX=54.65 CenterY=65.07 CenterZ=0 NormalX=0 NormalY=0 NormalZ=1 AngleXU=0 Radius=1.25
    g2: Circle CenterX=54.65 CenterY=108.53 CenterZ=0 NormalX=0 NormalY=0 NormalZ=1 AngleXU=0 Radius=1.25
    g3: Circle CenterX=-10.85 CenterY=108.52 CenterZ=0 NormalX=0 NormalY=0 NormalZ=1 AngleXU=0 Radius=1.25
  constraints (4):
    c: Diameter(g0) = 2.5
    c: Diameter(g1) = 2.5
    c: Diameter(g2) = 2.5
    c: Diameter(g3) = 2.5
FEATURE [PartDesign::Hole] Hole004
  BaseFeature = -> Hole003
  CustomThreadClearance = 0
  Depth = 3
  DepthType = 0
  Diameter = 2.7
  DrillForDepth = false
  DrillPoint = 0
  DrillPointAngle = 118
  HoleCutCountersinkAngle = 90
  HoleCutCustomValues = false
  HoleCutDepth = 0
  HoleCutDiameter = 6.1
  HoleCutType = 0
  ModelThread = false
  Profile = -> Sketch044
  Tapered = false
  TaperedAngle = 90
  ThreadClass = 0
  ThreadDepth = 3
  ThreadDepthType = 0
  ThreadDirection = 0
  ThreadFit = 0
  ThreadSize = 0
  ThreadType = 0
  Threaded = false
  UseCustomThreadClearance = false
FEATURE [Sketcher::SketchObject] Sketch046  label="Display View Hole"
  FullyConstrained = false
  MapMode = 5
  Placement = pos=(0,0,3) rot=(0,0,1;0rad)
  Support = -> [Hole004]
  sketch-geometry (4):
    g0: LineSegment StartX=-6.5 StartY=104.88 StartZ=0 EndX=50.6 EndY=104.88 EndZ=0
    g1: LineSegment StartX=50.6 StartY=104.88 StartZ=0 EndX=50.6 EndY=74.22 EndZ=0
    g2: LineSegment StartX=50.6 StartY=74.22 StartZ=0 EndX=-6.5 EndY=74.22 EndZ=0
    g3: LineSegment StartX=-6.5 StartY=74.22 StartZ=0 EndX=-6.5 EndY=104.88 EndZ=0
  constraints (10):
    c: Coincident(g0,g1)
    c: Coincident(g1,g2)
    c: Coincident(g2,g3)
    c: Coincident(g3,g0)
    c: Horizontal(g0)
    c: Horizontal(g2)
    c: Vertical(g1)
    c: Vertical(g3)
    c: DistanceY(g1,g1) = 30.66
    c: DistanceX(g2,g2) = 57.1
FEATURE [PartDesign::Pocket] Pocket013
  BaseFeature = -> Hole004
  Direction = (0,0,-1)
  Length = 3
  Length2 = 5
  Profile = -> Sketch046
  ReferenceAxis = -> Sketch046 [N_Axis]
  Type = 0
FEATURE [Sketcher::SketchObject] Sketch050  label="Left Lip sk"
  FullyConstrained = false
  MapMode = 5
  Support = -> [BaseFeature002]
  sketch-geometry (4):
    g0: LineSegment StartX=-36.4 StartY=26.5706 StartZ=0 EndX=-44.9 EndY=26.5706 EndZ=0
    g1: LineSegment StartX=-44.9 StartY=26.5706 StartZ=0 EndX=-44.9 EndY=116.571 EndZ=0
    g2: LineSegment StartX=-44.9 StartY=116.571 StartZ=0 EndX=-36.4 EndY=116.571 EndZ=0
    g3: LineSegment StartX=-36.4 StartY=116.571 StartZ=0 EndX=-36.4 EndY=26.5706 EndZ=0
  constraints (10):
    c: Coincident(g0,g1)
    c: Coincident(g1,g2)
    c: Coincident(g2,g3)
    c: Coincident(g3,g0)
    c: Horizontal(g0)
    c: Horizontal(g2)
    c: Vertical(g1)
    c: Vertical(g3)
    c: DistanceY(g1,g1) = 90
    c: DistanceX(g2,g2) = 8.5
FEATURE [Part::Extrusion] Extrude014  label="left lip bare"
  Base = -> Sketch050
  Dir = (0,0,1)
  DirMode = 2
  FaceMakerClass = Part::FaceMakerBullseye
  LengthFwd = 5
  LengthRev = 0
  Reversed = true
  Solid = true
  Symmetric = false
FEATURE [Sketcher::SketchObject] Sketch051  label="left ext mounting holes"
  FullyConstrained = false
  MapMode = 5
  Support = -> [Extrude014]
  sketch-geometry (11):
    g0: LineSegment StartX=-44.925 StartY=26.5956 StartZ=0 EndX=-44.925 EndY=30.85 EndZ=0
    g1: LineSegment StartX=-44.925 StartY=30.85 StartZ=0 EndX=65.575 EndY=30.85 EndZ=0
    g2: LineSegment StartX=-44.925 StartY=30.85 StartZ=0 EndX=-44.925 EndY=70.008 EndZ=0
    g3: LineSegment StartX=-44.925 StartY=70.008 StartZ=0 EndX=65.5785 EndY=70.008 EndZ=0
    g4: LineSegment StartX=-44.925 StartY=116.596 StartZ=0 EndX=-44.925 EndY=112.35 EndZ=0
    g5: LineSegment StartX=-44.925 StartY=112.35 StartZ=0 EndX=-33.925 EndY=112.35 EndZ=0
    g6: LineSegment StartX=-44.925 StartY=116.596 StartZ=0 EndX=-40.675 EndY=116.596 EndZ=0
    g7: LineSegment StartX=-40.675 StartY=116.596 StartZ=0 EndX=-40.675 EndY=26.5956 EndZ=0
    g8: Circle CenterX=-40.675 CenterY=30.85 CenterZ=0 NormalX=0 NormalY=0 NormalZ=1 AngleXU=0 Radius=1.6
    g9: Circle CenterX=-40.675 CenterY=70.008 CenterZ=0 NormalX=0 NormalY=0 NormalZ=1 AngleXU=0 Radius=1.6
    g10: Circle CenterX=-40.675 CenterY=112.35 CenterZ=0 NormalX=0 NormalY=0 NormalZ=1 AngleXU=0 Radius=1.6
  constraints (20):
    c: Vertical(g0)
    c: Coincident(g1,g0)
    c: Horizontal(g1)
    c: Coincident(g2,g0)
    c: Vertical(g2)
    c: Coincident(g3,g2)
    c: Horizontal(g3)
    c: Vertical(g4)
    c: Coincident(g5,g4)
    c: Horizontal(g5)
    c: Coincident(g6,g4)
    c: Horizontal(g6)
    c: Coincident(g7,g6)
    c: Vertical(g7)
    c: PointOnObject(g8,g7)
    c: Diameter(g8) = 3.2
    c: PointOnObject(g9,g3)
    c: Diameter(g9) = 3.2
    c: PointOnObject(g10,g5)
    c: Diameter(g10) = 3.2
FEATURE [PartDesign::Hole] Hole005  label="left Lip mount"
  CustomThreadClearance = 0
  Depth = 5
  DepthType = 0
  Diameter = 3.2
  DrillForDepth = false
  DrillPoint = 1
  DrillPointAngle = 118
  HoleCutCountersinkAngle = 90
  HoleCutCustomValues = false
  HoleCutDepth = 0
  HoleCutDiameter = 6.1
  HoleCutType = 0
  ModelThread = false
  Placement = pos=(0.1,0,0) rot=(0,0,1;0rad)
  Profile = -> Sketch051
  Tapered = false
  TaperedAngle = 90
  ThreadClass = 0
  ThreadDepth = 5
  ThreadDepthType = 0
  ThreadDirection = 0
  ThreadFit = 0
  ThreadSize = 0
  ThreadType = 0
  Threaded = false
  UseCustomThreadClearance = false
FEATURE [Sketcher::SketchObject] Sketch052  label="right Lip sk"
  FullyConstrained = false
  MapMode = 5
  Support = -> [BaseFeature002]
  sketch-geometry (4):
    g0: LineSegment StartX=65.5709 StartY=26.605 StartZ=0 EndX=74.0709 EndY=26.605 EndZ=0
    g1: LineSegment StartX=74.0709 StartY=26.605 StartZ=0 EndX=74.0709 EndY=116.605 EndZ=0
    g2: LineSegment StartX=74.0709 StartY=116.605 StartZ=0 EndX=65.5709 EndY=116.605 EndZ=0
    g3: LineSegment StartX=65.5709 StartY=116.605 StartZ=0 EndX=65.5709 EndY=26.605 EndZ=0
  constraints (10):
    c: Coincident(g0,g1)
    c: Coincident(g1,g2)
    c: Coincident(g2,g3)
    c: Coincident(g3,g0)
    c: Horizontal(g0)
    c: Horizontal(g2)
    c: Vertical(g1)
    c: Vertical(g3)
    c: DistanceY(g1,g1) = 90
    c: DistanceX(g2,g2) = 8.5
FEATURE [Part::Extrusion] Extrude015  label="right lip bare"
  Base = -> Sketch052
  Dir = (0,0,1)
  DirMode = 2
  FaceMakerClass = Part::FaceMakerBullseye
  LengthFwd = 5
  LengthRev = 0
  Reversed = true
  Solid = true
  Symmetric = false
FEATURE [Sketcher::SketchObject] Sketch053  label="right ext mounting holes"
  FullyConstrained = false
  MapMode = 5
  Support = -> [Extrude015]
  sketch-geometry (7):
    g0: LineSegment StartX=74.046 StartY=26.63 StartZ=0 EndX=69.8 EndY=26.63 EndZ=0
    g1: LineSegment StartX=69.8 StartY=26.63 StartZ=0 EndX=69.8 EndY=116.63 EndZ=0
    g2: LineSegment StartX=69.81 StartY=116.63 StartZ=0 EndX=69.81 EndY=112.38 EndZ=0
    g3: Circle CenterX=69.8 CenterY=112.38 CenterZ=0 NormalX=0 NormalY=0 NormalZ=1 AngleXU=0 Radius=1.6
    g4: Circle CenterX=69.8 CenterY=73.22 CenterZ=0 NormalX=0 NormalY=0 NormalZ=1 AngleXU=0 Radius=1.6
    g5: LineSegment StartX=69.81 StartY=26.63 StartZ=0 EndX=69.81 EndY=30.88 EndZ=0
    g6: Circle CenterX=69.8 CenterY=30.88 CenterZ=0 NormalX=0 NormalY=0 NormalZ=1 AngleXU=0 Radius=1.6
  constraints (9):
    c: Horizontal(g0)
    c: Coincident(g1,g0)
    c: Vertical(g1)
    c: Vertical(g2)
    c: Diameter(g3) = 3.2
    c: Diameter(g4) = 3.2
    c: PointOnObject(g5,g0)
    c: Vertical(g5)
    c: Diameter(g6) = 3.2
FEATURE [PartDesign::Hole] Hole006  label="right Lip mount"
  CustomThreadClearance = 0
  Depth = 5
  DepthType = 0
  Diameter = 3.2
  DrillForDepth = false
  DrillPoint = 1
  DrillPointAngle = 118
  HoleCutCountersinkAngle = 90
  HoleCutCustomValues = false
  HoleCutDepth = 0
  HoleCutDiameter = 6.1
  HoleCutType = 0
  ModelThread = false
  Profile = -> Sketch053
  Tapered = false
  TaperedAngle = 90
  ThreadClass = 0
  ThreadDepth = 5
  ThreadDepthType = 0
  ThreadDirection = 0
  ThreadFit = 0
  ThreadSize = 0
  ThreadType = 0
  Threaded = false
  UseCustomThreadClearance = false
FEATURE [Sketcher::SketchObject] Sketch054  label="plate to enc mounting holes"
  FullyConstrained = false
  MapMode = 5
  Placement = pos=(0,0,3) rot=(0,0,1;0rad)
  Support = -> [Pocket013]
  sketch-geometry (6):
    g0: Circle CenterX=-40.2273 CenterY=30.9765 CenterZ=0 NormalX=0 NormalY=0 NormalZ=1 AngleXU=0 Radius=1.6
    g1: Circle CenterX=-40.2319 CenterY=70.1333 CenterZ=0 NormalX=0 NormalY=0 NormalZ=1 AngleXU=0 Radius=1.6
    g2: Circle CenterX=-40.231 CenterY=112.471 CenterZ=0 NormalX=0 NormalY=0 NormalZ=1 AngleXU=0 Radius=1.6
    g3: Circle CenterX=70.2732 CenterY=112.478 CenterZ=0 NormalX=0 NormalY=0 NormalZ=1 AngleXU=0 Radius=1.6
    g4: Circle CenterX=70.2763 CenterY=73.3222 CenterZ=0 NormalX=0 NormalY=0 NormalZ=1 AngleXU=0 Radius=1.6
    g5: Circle CenterX=70.2722 CenterY=30.9778 CenterZ=0 NormalX=0 NormalY=0 NormalZ=1 AngleXU=0 Radius=1.6
  constraints (6):
    c: Diameter(g0) = 3.2
    c: Diameter(g1) = 3.2
    c: Diameter(g2) = 3.2
    c: Diameter(g3) = 3.2
    c: Diameter(g4) = 3.2
    c: Diameter(g5) = 3.2
FEATURE [PartDesign::Hole] Hole007
  BaseFeature = -> Pocket013
  CustomThreadClearance = 0
  Depth = 3
  DepthType = 0
  Diameter = 3.2
  DrillForDepth = false
  DrillPoint = 1
  DrillPointAngle = 118
  HoleCutCountersinkAngle = 90
  HoleCutCustomValues = false
  HoleCutDepth = 0
  HoleCutDiameter = 6.1
  HoleCutType = 0
  ModelThread = false
  Profile = -> Sketch054
  Tapered = false
  TaperedAngle = 90
  ThreadClass = 0
  ThreadDepth = 3
  ThreadDepthType = 0
  ThreadDirection = 0
  ThreadFit = 0
  ThreadSize = 0
  ThreadType = 0
  Threaded = false
  UseCustomThreadClearance = false
FEATURE [PartDesign::Fillet] Fillet
  Base = -> Hole007 [Edge32,Edge8,Edge10,Edge2,Edge4,Edge1,Edge7,Edge5]
  BaseFeature = -> Hole007
  Radius = 2
  SupportTransform = false
  UseAllEdges = false
FEATURE [PartDesign::Fillet] Fillet001
  Base = -> Fillet [Edge76,Edge80,Edge81,Edge78]
  BaseFeature = -> Fillet
  Radius = 2
  SupportTransform = false
  UseAllEdges = false
FEATURE [PartDesign::Chamfer] Chamfer
  Angle = 45
  Base = -> Fillet001 [Edge64,Edge40,Edge8,Edge10]
  BaseFeature = -> Fillet001
  ChamferType = 0
  FlipDirection = false
  Size = 1
  Size2 = 1
  SupportTransform = false
  UseAllEdges = false
FEATURE [Sketcher::SketchObject] Sketch055  label="House icon Sketch"
  FullyConstrained = false
  MapMode = 5
  Placement = pos=(0,0,3) rot=(0,0,1;0rad)
  Support = -> [Fillet001]
  sketch-geometry (60):
    g0: BSplineCurve PolesCount=4 KnotsCount=2 Degree=3 IsPeriodic=0
    g1: BSplineCurve PolesCount=4 KnotsCount=2 Degree=3 IsPeriodic=0
    g2: BSplineCurve PolesCount=4 KnotsCount=2 Degree=3 IsPeriodic=0
    g3: BSplineCurve PolesCount=2 KnotsCount=2 Degree=1 IsPeriodic=0
    g4: BSplineCurve PolesCount=2 KnotsCount=2 Degree=1 IsPeriodic=0
    g5: BSplineCurve PolesCount=4 KnotsCount=2 Degree=3 IsPeriodic=0
    g6: BSplineCurve PolesCount=4 KnotsCount=2 Degree=3 IsPeriodic=0
    g7: BSplineCurve PolesCount=2 KnotsCount=2 Degree=1 IsPeriodic=0
    g8: BSplineCurve PolesCount=2 KnotsCount=2 Degree=1 IsPeriodic=0
    g9: BSplineCurve PolesCount=4 KnotsCount=2 Degree=3 IsPeriodic=0
    g10: BSplineCurve PolesCount=4 KnotsCount=2 Degree=3 IsPeriodic=0
    g11: BSplineCurve PolesCount=4 KnotsCount=2 Degree=3 IsPeriodic=0
    g12: BSplineCurve PolesCount=4 KnotsCount=2 Degree=3 IsPeriodic=0
    g13: BSplineCurve PolesCount=4 KnotsCount=2 Degree=3 IsPeriodic=0
    g14: BSplineCurve PolesCount=4 KnotsCount=2 Degree=3 IsPeriodic=0
    g15: BSplineCurve PolesCount=2 KnotsCount=2 Degree=1 IsPeriodic=0
    g16: BSplineCurve PolesCount=2 KnotsCount=2 Degree=1 IsPeriodic=0
    g17: BSplineCurve PolesCount=4 KnotsCount=2 Degree=3 IsPeriodic=0
    g18: BSplineCurve PolesCount=4 KnotsCount=2 Degree=3 IsPeriodic=0
    g19: BSplineCurve PolesCount=2 KnotsCount=2 Degree=1 IsPeriodic=0
    g20: BSplineCurve PolesCount=2 KnotsCount=2 Degree=1 IsPeriodic=0
    g21: BSplineCurve PolesCount=4 KnotsCount=2 Degree=3 IsPeriodic=0
    g22: BSplineCurve PolesCount=4 KnotsCount=2 Degree=3 IsPeriodic=0
    g23: BSplineCurve PolesCount=4 KnotsCount=2 Degree=3 IsPeriodic=0
    g24: BSplineCurve PolesCount=4 KnotsCount=2 Degree=3 IsPeriodic=0
    g25: BSplineCurve PolesCount=4 KnotsCount=2 Degree=3 IsPeriodic=0
    g26: BSplineCurve PolesCount=4 KnotsCount=2 Degree=3 IsPeriodic=0
    g27: BSplineCurve PolesCount=4 KnotsCount=2 Degree=3 IsPeriodic=0
    g28: BSplineCurve PolesCount=4 KnotsCount=2 Degree=3 IsPeriodic=0
    g29: BSplineCurve PolesCount=4 KnotsCount=2 Degree=3 IsPeriodic=0
    g30: BSplineCurve PolesCount=4 KnotsCount=2 Degree=3 IsPeriodic=0
    g31: BSplineCurve PolesCount=4 KnotsCount=2 Degree=3 IsPeriodic=0
    g32: BSplineCurve PolesCount=4 KnotsCount=2 Degree=3 IsPeriodic=0
    g33: BSplineCurve PolesCount=4 KnotsCount=2 Degree=3 IsPeriodic=0
    g34: BSplineCurve PolesCount=4 KnotsCount=2 Degree=3 IsPeriodic=0
    g35: BSplineCurve PolesCount=4 KnotsCount=2 Degree=3 IsPeriodic=0
    g36: BSplineCurve PolesCount=4 KnotsCount=2 Degree=3 IsPeriodic=0
    g37: BSplineCurve PolesCount=4 KnotsCount=2 Degree=3 IsPeriodic=0
    g38: BSplineCurve PolesCount=4 KnotsCount=2 Degree=3 IsPeriodic=0
    g39: BSplineCurve PolesCount=4 KnotsCount=2 Degree=3 IsPeriodic=0
    g40: BSplineCurve PolesCount=4 KnotsCount=2 Degree=3 IsPeriodic=0
    g41: BSplineCurve PolesCount=4 KnotsCount=2 Degree=3 IsPeriodic=0
    g42: BSplineCurve PolesCount=4 KnotsCount=2 Degree=3 IsPeriodic=0
    g43: BSplineCurve PolesCount=4 KnotsCount=2 Degree=3 IsPeriodic=0
    g44: BSplineCurve PolesCount=2 KnotsCount=2 Degree=1 IsPeriodic=0
    g45: BSplineCurve PolesCount=2 KnotsCount=2 Degree=1 IsPeriodic=0
    g46: BSplineCurve PolesCount=4 KnotsCount=2 Degree=3 IsPeriodic=0
    g47: BSplineCurve PolesCount=4 KnotsCount=2 Degree=3 IsPeriodic=0
    g48: BSplineCurve PolesCount=4 KnotsCount=2 Degree=3 IsPeriodic=0
    g49: BSplineCurve PolesCount=4 KnotsCount=2 Degree=3 IsPeriodic=0
    g50: BSplineCurve PolesCount=4 KnotsCount=2 Degree=3 IsPeriodic=0
    g51: BSplineCurve PolesCount=4 KnotsCount=2 Degree=3 IsPeriodic=0
    g52: BSplineCurve PolesCount=2 KnotsCount=2 Degree=1 IsPeriodic=0
    g53: BSplineCurve PolesCount=2 KnotsCount=2 Degree=1 IsPeriodic=0
    g54: BSplineCurve PolesCount=4 KnotsCount=2 Degree=3 IsPeriodic=0
    g55: BSplineCurve PolesCount=4 KnotsCount=2 Degree=3 IsPeriodic=0
    g56: BSplineCurve PolesCount=2 KnotsCount=2 Degree=1 IsPeriodic=0
    g57: BSplineCurve PolesCount=2 KnotsCount=2 Degree=1 IsPeriodic=0
    g58: BSplineCurve PolesCount=2 KnotsCount=2 Degree=1 IsPeriodic=0
    g59: BSplineCurve PolesCount=2 KnotsCount=2 Degree=1 IsPeriodic=0
  constraints (60):
    c: Coincident(g0,g1)
    c: Coincident(g1,g2)
    c: Coincident(g2,g3)
    c: Coincident(g3,g4)
    c: Coincident(g4,g5)
    c: Coincident(g5,g6)
    c: Coincident(g6,g7)
    c: Coincident(g7,g8)
    c: Coincident(g8,g9)
    c: Coincident(g9,g10)
    c: Coincident(g10,g11)
    c: Coincident(g11,g12)
    c: Coincident(g12,g13)
    c: Coincident(g13,g14)
    c: Coincident(g14,g15)
    c: Coincident(g15,g16)
    c: Coincident(g16,g17)
    c: Coincident(g17,g18)
    c: Coincident(g18,g19)
    c: Coincident(g19,g20)
    c: Coincident(g20,g21)
    c: Coincident(g21,g22)
    c: Coincident(g22,g23)
    c: Coincident(g23,g0)
    c: Coincident(g24,g25)
    c: Coincident(g25,g26)
    c: Coincident(g26,g27)
    c: Coincident(g27,g28)
    c: Coincident(g28,g29)
    c: Coincident(g29,g30)
    c: Coincident(g30,g31)
    c: Coincident(g31,g32)
    c: Coincident(g32,g33)
    c: Coincident(g33,g34)
    c: Coincident(g34,g35)
    c: Coincident(g35,g36)
    c: Coincident(g36,g37)
    c: Coincident(g37,g38)
    c: Coincident(g38,g39)
    c: Coincident(g39,g40)
    c: Coincident(g40,g41)
    c: Coincident(g41,g42)
    c: Coincident(g42,g43)
    c: Coincident(g43,g44)
    c: Coincident(g44,g45)
    c: Coincident(g45,g46)
    c: Coincident(g46,g47)
    c: Coincident(g47,g48)
    c: Coincident(g48,g49)
    c: Coincident(g49,g50)
    c: Coincident(g50,g51)
    c: Coincident(g51,g24)
    c: Coincident(g52,g53)
    c: Coincident(g53,g54)
    c: Coincident(g54,g55)
    c: Coincident(g55,g56)
    c: Coincident(g56,g57)
    c: Coincident(g57,g58)
    c: Coincident(g58,g59)
    c: Coincident(g59,g52)
FEATURE [Sketcher::SketchObject] Sketch056
  FullyConstrained = false
  MapMode = 5
  Placement = pos=(0,0,3) rot=(0,0,1;0rad)
  Support = -> [Fillet001]
  sketch-geometry (10):
    g0: LineSegment StartX=75.55 StartY=117.704 StartZ=0 EndX=75.55 EndY=116.7 EndZ=0
    g1: LineSegment StartX=-45.45 StartY=25.7 StartZ=0 EndX=-44.45 EndY=25.7 EndZ=0
    g2: LineSegment StartX=-33.5221 StartY=26.7 StartZ=0 EndX=63.6179 EndY=26.7 EndZ=0
    g3: LineSegment StartX=74.55 StartY=37.6321 StartZ=0 EndX=74.55 EndY=103.972 EndZ=0
    g4: LineSegment StartX=61.8221 StartY=116.7 StartZ=0 EndX=-31.7179 EndY=116.7 EndZ=0
    g5: LineSegment StartX=-44.45 StartY=103.968 StartZ=0 EndX=-44.45 EndY=37.6279 EndZ=0
    g6: ArcOfCircle CenterX=-31.7179 CenterY=103.968 CenterZ=0 NormalX=0 NormalY=0 NormalZ=1 AngleXU=0 Radius=12.7321 StartAngle=1.5708 EndAngle=3.14159
    g7: ArcOfCircle CenterX=61.8221 CenterY=103.972 CenterZ=0 NormalX=0 NormalY=0 NormalZ=1 AngleXU=0 Radius=12.7279 StartAngle=0 EndAngle=1.5708
    g8: ArcOfCircle CenterX=-33.5221 CenterY=37.6279 CenterZ=0 NormalX=0 NormalY=0 NormalZ=1 AngleXU=0 Radius=10.9279 StartAngle=3.14159 EndAngle=4.71239
    g9: ArcOfCircle CenterX=63.6179 CenterY=37.6321 CenterZ=0 NormalX=0 NormalY=0 NormalZ=1 AngleXU=0 Radius=10.9321 StartAngle=4.71239 EndAngle=6.28319
  constraints (18):
    c: Vertical(g0)
    c: Horizontal(g1)
    c: Horizontal(g2)
    c: Horizontal(g4)
    c: Vertical(g3)
    c: Vertical(g5)
    c: Tangent(g4,g6) = -1.5708
    c: Tangent(g5,g6) = -1.5708
    c: Tangent(g3,g7) = -1.5708
    c: Tangent(g4,g7) = -1.5708
    c: Tangent(g2,g8) = -1.5708
    c: Tangent(g5,g8) = -1.5708
    c: Tangent(g2,g9) = -1.5708
    c: Tangent(g3,g9) = -1.5708
    c: DistanceX(g2,g2) = 97.14
    c: DistanceX(g4,g4) = 93.54
    c: DistanceY(g3,g3) = 66.34
    c: DistanceY(g5,g5) = 66.34
FEATURE [PartDesign::Body] Body003  label="Top Plate"
  BaseFeature = -> Extrude013
  Group = -> [BaseFeature,Sketch042,Sketch043,Sketch044,Sketch045,Sketch046,Hole001,Hole002,Hole003,Hole004,Pocket013,Sketch054,Hole007,Fillet,Fillet001,Sketch056,Sketch055,Chamfer]
  Origin = -> Origin072
  Placement = pos=(0,0,24.7) rot=(0,0,1;0rad)
  Tip = -> Chamfer
FEATURE [App::Part] Part011  label="Top Enclosure Plate"
  Group = -> [Body003,Path002,Path,Path001,Clone]
  Origin = -> Origin071
  Placement = pos=(0,0,-22.5) rot=(0,0,1;0rad)
FEATURE [Sketcher::SketchObject] Sketch057  label="Internal Mounts"
  FullyConstrained = false
  MapMode = 5
  Placement = pos=(0,0,-45) rot=(1,0,0;3.14159rad)
  Support = -> [BaseFeature002]
  sketch-geometry (10):
    g0: LineSegment StartX=-23.93 StartY=-53.0177 StartZ=0 EndX=-23.93 EndY=-56.1943 EndZ=0
    g1: LineSegment StartX=-23.93 StartY=-53.0177 StartZ=0 EndX=-23.93 EndY=-50.27 EndZ=0
    g2: LineSegment StartX=-22.332 StartY=-54.606 StartZ=0 EndX=-19.58 EndY=-54.606 EndZ=0
    g3: LineSegment StartX=-23.93 StartY=-56.1943 StartZ=0 EndX=-23.93 EndY=-58.87 EndZ=0
    g4: LineSegment StartX=-23.93 StartY=-58.87 StartZ=0 EndX=-16.93 EndY=-58.87 EndZ=0
    g5: LineSegment StartX=-23.93 StartY=-50.27 StartZ=0 EndX=-33.9264 EndY=-50.27 EndZ=0
    g6: LineSegment StartX=-33.9 StartY=-50.27 StartZ=0 EndX=-19.57 EndY=-50.27 EndZ=0
    g7: LineSegment StartX=-19.57 StartY=-50.27 StartZ=0 EndX=-19.57 EndY=-58.87 EndZ=0
    g8: LineSegment StartX=-19.57 StartY=-58.87 StartZ=0 EndX=-33.9 EndY=-58.87 EndZ=0
    g9: LineSegment StartX=-33.9 StartY=-58.87 StartZ=0 EndX=-33.9 EndY=-50.27 EndZ=0
  constraints (22):
    c: Vertical(g0)
    c: Coincident(g1,g0)
    c: Vertical(g1)
    c: Horizontal(g2)
    c: Coincident(g3,g0)
    c: Vertical(g3)
    c: Coincident(g4,g3)
    c: Horizontal(g4)
    c: Coincident(g5,g1)
    c: Horizontal(g5)
    c: Coincident(g6,g7)
    c: Coincident(g7,g8)
    c: Coincident(g8,g9)
    c: Coincident(g9,g6)
    c: Horizontal(g6)
    c: Horizontal(g8)
    c: Vertical(g7)
    c: Vertical(g9)
    c: PointOnObject(g6,g5)
    c: PointOnObject(g7,g4)
    c: DistanceX(g6,g6) = 14.33
    c: DistanceY(g7,g7) = 8.6
FEATURE [Part::Extrusion] Extrude016  label="Extrude053"
  Base = -> Sketch057
  Dir = (0,0,-1)
  DirMode = 2
  FaceMakerClass = Part::FaceMakerBullseye
  LengthFwd = 16
  LengthRev = 0
  Reversed = true
  Solid = true
  Symmetric = false
FEATURE [Sketcher::SketchObject] Sketch058  label="bottom left mount"
  FullyConstrained = false
  MapMode = 5
  Placement = pos=(0,0,-29) rot=(0,0,1;0rad)
  Support = -> [Extrude016]
  sketch-geometry (2):
    g0: LineSegment StartX=-25.532 StartY=54.606 StartZ=0 EndX=-23.93 EndY=54.606 EndZ=0
    g1: Circle CenterX=-23.93 CenterY=54.606 CenterZ=0 NormalX=0 NormalY=0 NormalZ=1 AngleXU=0 Radius=1.5
  constraints (3):
    c: Horizontal(g0)
    c: Coincident(g1,g0)
    c: Diameter(g1) = 3
FEATURE [PartDesign::Hole] Hole008  label="bottom left pcb mount"
  CustomThreadClearance = 0
  Depth = 4
  DepthType = 0
  Diameter = 3
  DrillForDepth = false
  DrillPoint = 0
  DrillPointAngle = 118
  HoleCutCountersinkAngle = 90
  HoleCutCustomValues = false
  HoleCutDepth = 0
  HoleCutDiameter = 6.1
  HoleCutType = 0
  ModelThread = false
  Profile = -> Sketch058
  Tapered = false
  TaperedAngle = 90
  ThreadClass = 0
  ThreadDepth = 4
  ThreadDepthType = 0
  ThreadDirection = 0
  ThreadFit = 0
  ThreadSize = 0
  ThreadType = 0
  Threaded = false
  UseCustomThreadClearance = false
FEATURE [Sketcher::SketchObject] Sketch059  label="top left mount"
  FullyConstrained = false
  MapMode = 5
  Placement = pos=(0,0,-45) rot=(1,0,0;3.14159rad)
  Support = -> [BaseFeature002]
  sketch-geometry (10):
    g0: LineSegment StartX=-23.93 StartY=-90.99 StartZ=0 EndX=-23.93 EndY=-88.24 EndZ=0
    g1: LineSegment StartX=-23.93 StartY=-88.24 StartZ=0 EndX=-33.9252 EndY=-88.24 EndZ=0
    g2: LineSegment StartX=-23.93 StartY=-94.1675 StartZ=0 EndX=-23.93 EndY=-96.92 EndZ=0
    g3: LineSegment StartX=-23.93 StartY=-96.92 StartZ=0 EndX=-17 EndY=-96.92 EndZ=0
    g4: LineSegment StartX=-22.332 StartY=-92.579 StartZ=0 EndX=-19.5752 EndY=-92.579 EndZ=0
    g5: LineSegment StartX=-19.5752 StartY=-92.579 StartZ=0 EndX=-19.5752 EndY=-96.92 EndZ=0
    g6: LineSegment StartX=-19.5752 StartY=-96.92 StartZ=0 EndX=-33.9252 EndY=-96.92 EndZ=0
    g7: LineSegment StartX=-33.9252 StartY=-96.92 StartZ=0 EndX=-33.9252 EndY=-88.24 EndZ=0
    g8: LineSegment StartX=-33.9252 StartY=-88.24 StartZ=0 EndX=-19.5752 EndY=-88.24 EndZ=0
    g9: LineSegment StartX=-19.5752 StartY=-88.24 StartZ=0 EndX=-19.5752 EndY=-96.92 EndZ=0
  constraints (22):
    c: Vertical(g0)
    c: Coincident(g1,g0)
    c: Horizontal(g1)
    c: Vertical(g2)
    c: Coincident(g3,g2)
    c: Horizontal(g3)
    c: Horizontal(g4)
    c: Coincident(g5,g4)
    c: PointOnObject(g5,g3)
    c: Vertical(g5)
    c: Coincident(g6,g7)
    c: Coincident(g7,g8)
    c: Coincident(g8,g9)
    c: Coincident(g9,g6)
    c: Horizontal(g6)
    c: Horizontal(g8)
    c: Vertical(g7)
    c: Vertical(g9)
    c: Coincident(g6,g5)
    c: Coincident(g7,g1)
    c: DistanceX(g8,g8) = 14.35
    c: DistanceY(g7,g7) = 8.68
FEATURE [Part::Extrusion] Extrude017  label="top left pcb"
  Base = -> Sketch059
  Dir = (0,0,-1)
  DirMode = 2
  FaceMakerClass = Part::FaceMakerBullseye
  LengthFwd = 16
  LengthRev = 0
  Reversed = true
  Solid = true
  Symmetric = false
FEATURE [Sketcher::SketchObject] Sketch060  label="top left mount001"
  FullyConstrained = false
  MapMode = 5
  Placement = pos=(0,0,-29) rot=(0,0,1;0rad)
  Support = -> [Extrude017]
  sketch-geometry (2):
    g0: LineSegment StartX=-25.532 StartY=92.579 StartZ=0 EndX=-23.93 EndY=92.579 EndZ=0
    g1: Circle CenterX=-23.93 CenterY=92.579 CenterZ=0 NormalX=0 NormalY=0 NormalZ=1 AngleXU=0 Radius=1.5
  constraints (3):
    c: Horizontal(g0)
    c: Coincident(g1,g0)
    c: Diameter(g1) = 3
FEATURE [PartDesign::Hole] Hole009  label="top left pcb mount"
  CustomThreadClearance = 0
  Depth = 4
  DepthType = 0
  Diameter = 3
  DrillForDepth = false
  DrillPoint = 0
  DrillPointAngle = 118
  HoleCutCountersinkAngle = 90
  HoleCutCustomValues = false
  HoleCutDepth = 0
  HoleCutDiameter = 6.1
  HoleCutType = 0
  ModelThread = false
  Profile = -> Sketch060
  Tapered = false
  TaperedAngle = 90
  ThreadClass = 0
  ThreadDepth = 4
  ThreadDepthType = 0
  ThreadDirection = 0
  ThreadFit = 0
  ThreadSize = 0
  ThreadType = 0
  Threaded = false
  UseCustomThreadClearance = false
FEATURE [Sketcher::SketchObject] Sketch061  label="top right mount"
  FullyConstrained = false
  MapMode = 5
  Placement = pos=(0,0,-45) rot=(1,0,0;3.14159rad)
  Support = -> [BaseFeature002]
  sketch-geometry (11):
    g0: LineSegment StartX=53.07 StartY=-52.99 StartZ=0 EndX=53.07 EndY=-50.24 EndZ=0
    g1: LineSegment StartX=53.07 StartY=-50.24 StartZ=0 EndX=63.0742 EndY=-50.24 EndZ=0
    g2: LineSegment StartX=51.4672 StartY=-54.58 StartZ=0 EndX=48.72 EndY=-54.58 EndZ=0
    g3: LineSegment StartX=53.07 StartY=-52.99 StartZ=0 EndX=53.07 EndY=-56.1672 EndZ=0
    g4: LineSegment StartX=53.07 StartY=-56.1672 StartZ=0 EndX=53.07 EndY=-58.8447 EndZ=0
    g5: LineSegment StartX=53.07 StartY=-58.8447 StartZ=0 EndX=48 EndY=-58.8447 EndZ=0
    g6: LineSegment StartX=48.72 StartY=-54.58 StartZ=0 EndX=48.72 EndY=-58.8447 EndZ=0
    g7: LineSegment StartX=48.72 StartY=-58.8447 StartZ=0 EndX=63.08 EndY=-58.8447 EndZ=0
    g8: LineSegment StartX=63.08 StartY=-58.8447 StartZ=0 EndX=63.08 EndY=-50.2447 EndZ=0
    g9: LineSegment StartX=63.08 StartY=-50.2447 StartZ=0 EndX=48.72 EndY=-50.2447 EndZ=0
    g10: LineSegment StartX=48.72 StartY=-50.2447 StartZ=0 EndX=48.72 EndY=-58.8447 EndZ=0
  constraints (24):
    c: Vertical(g0)
    c: Coincident(g1,g0)
    c: Horizontal(g1)
    c: Horizontal(g2)
    c: Coincident(g3,g0)
    c: Vertical(g3)
    c: Coincident(g4,g3)
    c: Vertical(g4)
    c: Coincident(g5,g4)
    c: Horizontal(g5)
    c: Coincident(g6,g2)
    c: PointOnObject(g6,g5)
    c: Vertical(g6)
    c: Coincident(g7,g8)
    c: Coincident(g8,g9)
    c: Coincident(g9,g10)
    c: Coincident(g10,g7)
    c: Horizontal(g7)
    c: Horizontal(g9)
    c: Vertical(g8)
    c: Vertical(g10)
    c: Coincident(g7,g6)
    c: DistanceX(g9,g9) = 14.36
    c: DistanceY(g8,g8) = 8.6
FEATURE [Part::Extrusion] Extrude018  label="Extrude054"
  Base = -> Sketch061
  Dir = (0,0,-1)
  DirMode = 2
  FaceMakerClass = Part::FaceMakerBullseye
  LengthFwd = 16
  LengthRev = 0
  Reversed = true
  Solid = true
  Symmetric = false
FEATURE [Sketcher::SketchObject] Sketch062
  FullyConstrained = false
  MapMode = 5
  Placement = pos=(0,0,-29) rot=(0,0,1;0rad)
  Support = -> [Extrude018]
  sketch-geometry (2):
    g0: LineSegment StartX=51.468 StartY=54.579 StartZ=0 EndX=53.07 EndY=54.579 EndZ=0
    g1: Circle CenterX=53.07 CenterY=54.579 CenterZ=0 NormalX=0 NormalY=0 NormalZ=1 AngleXU=0 Radius=1.5
  constraints (3):
    c: Horizontal(g0)
    c: Coincident(g1,g0)
    c: Diameter(g1) = 3
FEATURE [PartDesign::Hole] Hole010  label="bottom right pcb mount"
  CustomThreadClearance = 0
  Depth = 4
  DepthType = 0
  Diameter = 3
  DrillForDepth = false
  DrillPoint = 0
  DrillPointAngle = 118
  HoleCutCountersinkAngle = 90
  HoleCutCustomValues = false
  HoleCutDepth = 0
  HoleCutDiameter = 6.1
  HoleCutType = 0
  ModelThread = false
  Placement = pos=(0.21,0,0) rot=(0,0,1;0rad)
  Profile = -> Sketch062
  Tapered = false
  TaperedAngle = 90
  ThreadClass = 0
  ThreadDepth = 4
  ThreadDepthType = 0
  ThreadDirection = 0
  ThreadFit = 0
  ThreadSize = 0
  ThreadType = 0
  Threaded = false
  UseCustomThreadClearance = false
FEATURE [Sketcher::SketchObject] Sketch063  label="top right mount001"
  FullyConstrained = false
  MapMode = 5
  Placement = pos=(0,0,-45) rot=(1,0,0;3.14159rad)
  Support = -> [BaseFeature002]
  sketch-geometry (11):
    g0: LineSegment StartX=53.07 StartY=-90.99 StartZ=0 EndX=53.07 EndY=-88.24 EndZ=0
    g1: LineSegment StartX=53.07 StartY=-88.24 StartZ=0 EndX=63.0745 EndY=-88.24 EndZ=0
    g2: LineSegment StartX=51.468 StartY=-92.579 StartZ=0 EndX=48.715 EndY=-92.579 EndZ=0
    g3: LineSegment StartX=48.715 StartY=-92.579 StartZ=0 EndX=48.715 EndY=-100.1 EndZ=0
    g4: LineSegment StartX=53.07 StartY=-90.99 StartZ=0 EndX=53.07 EndY=-94.1675 EndZ=0
    g5: LineSegment StartX=53.07 StartY=-94.1675 StartZ=0 EndX=53.07 EndY=-96.84 EndZ=0
    g6: LineSegment StartX=53.07 StartY=-96.84 StartZ=0 EndX=48.715 EndY=-96.84 EndZ=0
    g7: LineSegment StartX=48.715 StartY=-96.84 StartZ=0 EndX=63.075 EndY=-96.84 EndZ=0
    g8: LineSegment StartX=63.075 StartY=-96.84 StartZ=0 EndX=63.075 EndY=-88.24 EndZ=0
    g9: LineSegment StartX=63.075 StartY=-88.24 StartZ=0 EndX=48.715 EndY=-88.24 EndZ=0
    g10: LineSegment StartX=48.715 StartY=-88.24 StartZ=0 EndX=48.715 EndY=-96.84 EndZ=0
  constraints (24):
    c: Vertical(g0)
    c: Coincident(g1,g0)
    c: Horizontal(g1)
    c: Horizontal(g2)
    c: Coincident(g3,g2)
    c: Vertical(g3)
    c: Coincident(g4,g0)
    c: Vertical(g4)
    c: Coincident(g5,g4)
    c: Vertical(g5)
    c: Coincident(g6,g5)
    c: PointOnObject(g6,g3)
    c: Horizontal(g6)
    c: Coincident(g7,g8)
    c: Coincident(g8,g9)
    c: Coincident(g9,g10)
    c: Coincident(g10,g7)
    c: Horizontal(g7)
    c: Horizontal(g9)
    c: Vertical(g8)
    c: Vertical(g10)
    c: Coincident(g7,g6)
    c: DistanceX(g9,g9) = 14.36
    c: DistanceY(g8,g8) = 8.6
FEATURE [Part::Extrusion] Extrude019  label="Extrude055"
  Base = -> Sketch063
  Dir = (0,0,-1)
  DirMode = 2
  FaceMakerClass = Part::FaceMakerBullseye
  LengthFwd = 16
  LengthRev = 0
  Reversed = true
  Solid = true
  Symmetric = false
FEATURE [Sketcher::SketchObject] Sketch064
  FullyConstrained = false
  MapMode = 5
  Placement = pos=(0,0,-29) rot=(0,0,1;0rad)
  Support = -> [Extrude019]
  sketch-geometry (2):
    g0: LineSegment StartX=51.468 StartY=92.579 StartZ=0 EndX=53.07 EndY=92.579 EndZ=0
    g1: Circle CenterX=53.07 CenterY=92.579 CenterZ=0 NormalX=0 NormalY=0 NormalZ=1 AngleXU=0 Radius=1.5
  constraints (3):
    c: Horizontal(g0)
    c: Coincident(g1,g0)
    c: Diameter(g1) = 3
FEATURE [PartDesign::Hole] Hole011
  CustomThreadClearance = 0
  Depth = 4
  DepthType = 0
  Diameter = 3
  DrillForDepth = false
  DrillPoint = 0
  DrillPointAngle = 118
  HoleCutCountersinkAngle = 90
  HoleCutCustomValues = false
  HoleCutDepth = 0
  HoleCutDiameter = 6.1
  HoleCutType = 0
  ModelThread = false
  Placement = pos=(0.16,0,0) rot=(0,0,1;0rad)
  Profile = -> Sketch064
  Tapered = false
  TaperedAngle = 90
  ThreadClass = 0
  ThreadDepth = 4
  ThreadDepthType = 0
  ThreadDirection = 0
  ThreadFit = 0
  ThreadSize = 0
  ThreadType = 0
  Threaded = false
  UseCustomThreadClearance = false
FEATURE [Sketcher::SketchObject] Sketch065  label="bottom left "
  FullyConstrained = false
  MapMode = 5
  Placement = pos=(0,0,-45) rot=(1,0,0;3.14159rad)
  Support = -> [BaseFeature002]
  sketch-geometry (6):
    g0: LineSegment StartX=-33.925 StartY=-114.1 StartZ=0 EndX=-33.925 EndY=-109.1 EndZ=0
    g1: LineSegment StartX=-33.925 StartY=-109.1 StartZ=0 EndX=-28.925 EndY=-109.1 EndZ=0
    g2: LineSegment StartX=-33.925 StartY=-114.1 StartZ=0 EndX=-28.925 EndY=-114.1 EndZ=0
    g3: LineSegment StartX=-28.925 StartY=-114.1 StartZ=0 EndX=-28.925 EndY=-109.1 EndZ=0
    g4: LineSegment StartX=-28.925 StartY=-109.1 StartZ=0 EndX=-33.925 EndY=-109.1 EndZ=0
    g5: LineSegment StartX=-33.925 StartY=-109.1 StartZ=0 EndX=-33.925 EndY=-114.1 EndZ=0
  constraints (15):
    c: Vertical(g0)
    c: Coincident(g1,g0)
    c: Horizontal(g1)
    c: Coincident(g2,g3)
    c: Coincident(g3,g4)
    c: Coincident(g4,g5)
    c: Coincident(g5,g2)
    c: Horizontal(g2)
    c: Horizontal(g4)
    c: Vertical(g3)
    c: Vertical(g5)
    c: Coincident(g2,g0)
    c: Coincident(g3,g1)
    c: DistanceX(g4,g4) = 5
    c: DistanceY(g3,g3) = 5
FEATURE [Part::Extrusion] Extrude020  label="Extrude056"
  Base = -> Sketch065
  Dir = (0,0,-1)
  DirMode = 2
  FaceMakerClass = Part::FaceMakerBullseye
  LengthFwd = 6
  LengthRev = 0
  Reversed = true
  Solid = true
  Symmetric = false
FEATURE [Sketcher::SketchObject] Sketch066
  FullyConstrained = false
  MapMode = 5
  Placement = pos=(0,0,-45) rot=(1,0,0;3.14159rad)
  Support = -> [Extrude020]
  sketch-geometry (3):
    g0: LineSegment StartX=-33.925 StartY=-114.103 StartZ=0 EndX=-33.925 EndY=-111.958 EndZ=0
    g1: LineSegment StartX=-33.925 StartY=-111.958 StartZ=0 EndX=-31.78 EndY=-111.958 EndZ=0
    g2: Circle CenterX=-31.78 CenterY=-111.958 CenterZ=0 NormalX=0 NormalY=0 NormalZ=1 AngleXU=0 Radius=1.5
  constraints (5):
    c: Vertical(g0)
    c: Coincident(g1,g0)
    c: Horizontal(g1)
    c: Coincident(g2,g1)
    c: Diameter(g2) = 3
FEATURE [PartDesign::Hole] Hole012
  CustomThreadClearance = 0
  Depth = 4
  DepthType = 0
  Diameter = 3
  DrillForDepth = false
  DrillPoint = 0
  DrillPointAngle = 118
  HoleCutCountersinkAngle = 90
  HoleCutCustomValues = false
  HoleCutDepth = 0
  HoleCutDiameter = 6.1
  HoleCutType = 0
  ModelThread = false
  Profile = -> Sketch066
  Tapered = false
  TaperedAngle = 90
  ThreadClass = 0
  ThreadDepth = 4
  ThreadDepthType = 0
  ThreadDirection = 0
  ThreadFit = 0
  ThreadSize = 0
  ThreadType = 0
  Threaded = false
  UseCustomThreadClearance = false
FEATURE [Sketcher::SketchObject] Sketch067
  FullyConstrained = false
  MapMode = 5
  Placement = pos=(0,0,-45) rot=(1,0,0;3.14159rad)
  Support = -> [BaseFeature002]
  sketch-geometry (4):
    g0: LineSegment StartX=-33.9 StartY=-29.0739 StartZ=0 EndX=-28.9 EndY=-29.0739 EndZ=0
    g1: LineSegment StartX=-28.9 StartY=-29.0739 StartZ=0 EndX=-28.9 EndY=-34.0739 EndZ=0
    g2: LineSegment StartX=-28.9 StartY=-34.0739 StartZ=0 EndX=-33.9 EndY=-34.0739 EndZ=0
    g3: LineSegment StartX=-33.9 StartY=-34.0739 StartZ=0 EndX=-33.9 EndY=-29.0739 EndZ=0
  constraints (10):
    c: Coincident(g0,g1)
    c: Coincident(g1,g2)
    c: Coincident(g2,g3)
    c: Coincident(g3,g0)
    c: Horizontal(g0)
    c: Horizontal(g2)
    c: Vertical(g1)
    c: Vertical(g3)
    c: DistanceX(g2,g2) = 5
    c: DistanceY(g1,g1) = 5
FEATURE [Part::Extrusion] Extrude021  label="Extrude057"
  Base = -> Sketch067
  Dir = (0,0,-1)
  DirMode = 2
  FaceMakerClass = Part::FaceMakerBullseye
  LengthFwd = 6
  LengthRev = 0
  Reversed = true
  Solid = true
  Symmetric = false
FEATURE [Sketcher::SketchObject] Sketch068
  FullyConstrained = false
  MapMode = 5
  Placement = pos=(0,0,-45) rot=(1,0,0;3.14159rad)
  Support = -> [Extrude021]
  sketch-geometry (3):
    g0: LineSegment StartX=-33.9251 StartY=-29.103 StartZ=0 EndX=-33.9251 EndY=-31.25 EndZ=0
    g1: LineSegment StartX=-33.9251 StartY=-31.25 StartZ=0 EndX=-31.78 EndY=-31.25 EndZ=0
    g2: Circle CenterX=-31.78 CenterY=-31.25 CenterZ=0 NormalX=0 NormalY=0 NormalZ=1 AngleXU=0 Radius=1.5
  constraints (5):
    c: Vertical(g0)
    c: Coincident(g1,g0)
    c: Horizontal(g1)
    c: Coincident(g2,g1)
    c: Diameter(g2) = 3
FEATURE [PartDesign::Hole] Hole013
  CustomThreadClearance = 0
  Depth = 4
  DepthType = 0
  Diameter = 3
  DrillForDepth = false
  DrillPoint = 0
  DrillPointAngle = 118
  HoleCutCountersinkAngle = 90
  HoleCutCustomValues = false
  HoleCutDepth = 0
  HoleCutDiameter = 6.1
  HoleCutType = 0
  ModelThread = false
  Placement = pos=(0,-0.04,0) rot=(0,0,1;0rad)
  Profile = -> Sketch068
  Tapered = false
  TaperedAngle = 90
  ThreadClass = 0
  ThreadDepth = 4
  ThreadDepthType = 0
  ThreadDirection = 0
  ThreadFit = 0
  ThreadSize = 0
  ThreadType = 0
  Threaded = false
  UseCustomThreadClearance = false
FEATURE [Sketcher::SketchObject] Sketch069
  FullyConstrained = false
  MapMode = 5
  Placement = pos=(0,0,-45) rot=(1,0,0;3.14159rad)
  Support = -> [BaseFeature002]
  sketch-geometry (4):
    g0: LineSegment StartX=63.08 StartY=-114.1 StartZ=0 EndX=58.08 EndY=-114.1 EndZ=0
    g1: LineSegment StartX=58.08 StartY=-114.1 StartZ=0 EndX=58.08 EndY=-109.1 EndZ=0
    g2: LineSegment StartX=58.08 StartY=-109.1 StartZ=0 EndX=63.08 EndY=-109.1 EndZ=0
    g3: LineSegment StartX=63.08 StartY=-109.1 StartZ=0 EndX=63.08 EndY=-114.1 EndZ=0
  constraints (10):
    c: Coincident(g0,g1)
    c: Coincident(g1,g2)
    c: Coincident(g2,g3)
    c: Coincident(g3,g0)
    c: Horizontal(g0)
    c: Horizontal(g2)
    c: Vertical(g1)
    c: Vertical(g3)
    c: DistanceX(g2,g2) = 5
    c: DistanceY(g1,g1) = 5
FEATURE [Part::Extrusion] Extrude022  label="Extrude058"
  Base = -> Sketch069
  Dir = (0,0,-1)
  DirMode = 2
  FaceMakerClass = Part::FaceMakerBullseye
  LengthFwd = 6
  LengthRev = 0
  Reversed = true
  Solid = true
  Symmetric = false
FEATURE [Sketcher::SketchObject] Sketch070
  FullyConstrained = false
  MapMode = 5
  Placement = pos=(0,0,-45) rot=(1,0,0;3.14159rad)
  Support = -> [Extrude022]
  sketch-geometry (3):
    g0: LineSegment StartX=63.0765 StartY=-114.103 StartZ=0 EndX=60.93 EndY=-114.103 EndZ=0
    g1: LineSegment StartX=60.93 StartY=-114.103 StartZ=0 EndX=60.93 EndY=-111.95 EndZ=0
    g2: Circle CenterX=60.93 CenterY=-111.95 CenterZ=0 NormalX=0 NormalY=0 NormalZ=1 AngleXU=0 Radius=1.5
  constraints (5):
    c: Horizontal(g0)
    c: Coincident(g1,g0)
    c: Vertical(g1)
    c: Coincident(g2,g1)
    c: Diameter(g2) = 3
FEATURE [PartDesign::Hole] Hole014
  CustomThreadClearance = 0
  Depth = 4
  DepthType = 0
  Diameter = 3
  DrillForDepth = false
  DrillPoint = 0
  DrillPointAngle = 118
  HoleCutCountersinkAngle = 90
  HoleCutCustomValues = false
  HoleCutDepth = 0
  HoleCutDiameter = 6.1
  HoleCutType = 0
  ModelThread = false
  Placement = pos=(0.07,0,0) rot=(0,0,1;0rad)
  Profile = -> Sketch070
  Tapered = false
  TaperedAngle = 90
  ThreadClass = 0
  ThreadDepth = 4
  ThreadDepthType = 0
  ThreadDirection = 0
  ThreadFit = 0
  ThreadSize = 0
  ThreadType = 0
  Threaded = false
  UseCustomThreadClearance = false
FEATURE [Sketcher::SketchObject] Sketch071
  FullyConstrained = false
  MapMode = 5
  Placement = pos=(0,0,-45) rot=(1,0,0;3.14159rad)
  Support = -> [BaseFeature002]
  sketch-geometry (4):
    g0: LineSegment StartX=58.075 StartY=-34.103 StartZ=0 EndX=63.075 EndY=-34.103 EndZ=0
    g1: LineSegment StartX=63.075 StartY=-34.103 StartZ=0 EndX=63.075 EndY=-29.103 EndZ=0
    g2: LineSegment StartX=63.075 StartY=-29.103 StartZ=0 EndX=58.075 EndY=-29.103 EndZ=0
    g3: LineSegment StartX=58.075 StartY=-29.103 StartZ=0 EndX=58.075 EndY=-34.103 EndZ=0
  constraints (10):
    c: Coincident(g0,g1)
    c: Coincident(g1,g2)
    c: Coincident(g2,g3)
    c: Coincident(g3,g0)
    c: Horizontal(g0)
    c: Horizontal(g2)
    c: Vertical(g1)
    c: Vertical(g3)
    c: DistanceX(g2,g2) = 5
    c: DistanceY(g1,g1) = 5
FEATURE [Part::Extrusion] Extrude023  label="Extrude059"
  Base = -> Sketch071
  Dir = (0,0,-1)
  DirMode = 2
  FaceMakerClass = Part::FaceMakerBullseye
  LengthFwd = 6
  LengthRev = 0
  Reversed = true
  Solid = true
  Symmetric = false
FEATURE [Sketcher::SketchObject] Sketch072
  FullyConstrained = false
  MapMode = 5
  Placement = pos=(0,0,-45) rot=(1,0,0;3.14159rad)
  Support = -> [Extrude023]
  sketch-geometry (3):
    g0: LineSegment StartX=63.075 StartY=-29.103 StartZ=0 EndX=63.075 EndY=-31.25 EndZ=0
    g1: LineSegment StartX=63.075 StartY=-31.25 StartZ=0 EndX=60.92 EndY=-31.25 EndZ=0
    g2: Circle CenterX=60.92 CenterY=-31.25 CenterZ=0 NormalX=0 NormalY=0 NormalZ=1 AngleXU=0 Radius=1.5
  constraints (5):
    c: Vertical(g0)
    c: Coincident(g1,g0)
    c: Horizontal(g1)
    c: Coincident(g2,g1)
    c: Diameter(g2) = 3
FEATURE [PartDesign::Hole] Hole015
  CustomThreadClearance = 0
  Depth = 4
  DepthType = 0
  Diameter = 3
  DrillForDepth = false
  DrillPoint = 0
  DrillPointAngle = 118
  HoleCutCountersinkAngle = 90
  HoleCutCustomValues = false
  HoleCutDepth = 0
  HoleCutDiameter = 6.1
  HoleCutType = 0
  ModelThread = false
  Placement = pos=(0.09,-0.09,0) rot=(0,0,1;0rad)
  Profile = -> Sketch072
  Tapered = false
  TaperedAngle = 90
  ThreadClass = 0
  ThreadDepth = 4
  ThreadDepthType = 0
  ThreadDirection = 0
  ThreadFit = 0
  ThreadSize = 0
  ThreadType = 0
  Threaded = false
  UseCustomThreadClearance = false
FEATURE [Sketcher::SketchObject] Sketch073
  FullyConstrained = false
  MapMode = 5
  Placement = pos=(63.1,0,0) rot=(0.57735,-0.57735,-0.57735;2.0944rad)
  Support = -> [BaseFeature003]
  sketch-geometry (5):
    g0: LineSegment StartX=-88 StartY=-45 StartZ=0 EndX=-88 EndY=-35 EndZ=0
    g1: LineSegment StartX=-88 StartY=-35 StartZ=0 EndX=-59 EndY=-35 EndZ=0
    g2: LineSegment StartX=-59 StartY=-35 StartZ=0 EndX=-59 EndY=-20 EndZ=0
    g3: LineSegment StartX=-59 StartY=-20 StartZ=0 EndX=-88 EndY=-20 EndZ=0
    g4: LineSegment StartX=-88 StartY=-20 StartZ=0 EndX=-88 EndY=-35 EndZ=0
  constraints (12):
    c: Vertical(g0)
    c: Coincident(g1,g2)
    c: Coincident(g2,g3)
    c: Coincident(g3,g4)
    c: Coincident(g4,g1)
    c: Horizontal(g1)
    c: Horizontal(g3)
    c: Vertical(g2)
    c: Vertical(g4)
    c: Coincident(g1,g0)
    c: DistanceX(g3,g3) = 29
    c: DistanceY(g4,g4) = 15
FEATURE [PartDesign::Pocket] Pocket014
  BaseFeature = -> BaseFeature003
  Direction = (1,0,0)
  Length = 3
  Length2 = 5
  Profile = -> Sketch073
  ReferenceAxis = -> Sketch073 [N_Axis]
  Type = 0
FEATURE [PartDesign::Body] Body004  label="Enclosure Centre and mounts"
  Group = -> [BaseFeature003,Sketch073,Pocket014]
  Origin = -> Origin075
  Placement = pos=(0.025,-0.025,-3e-15) rot=(0,0,1;0rad)
  Tip = -> Pocket014
FEATURE [App::Part] Part013  label="Centre Exterior "
  Group = -> [Body004,Sketch050,BaseFeature002,Extrude014,Sketch051,Sketch052,Hole005,Extrude015,Sketch057,Hole006,Sketch053,Hole009,Sketch058,Sketch059,Hole008,Extrude017,Sketch060,Sketch061,Extrude018,Sketch062,Sketch063,Hole010,Extrude019,Hole011,Sketch064,Sketch065,Extrude020,Hole012,Sketch066,Sketch067,Extrude021,Hole013,Sketch069,Sketch068,Extrude022,Sketch070,Hole014,Sketch071,Extrude023,Sketch072,+1 more]
  Origin = -> Origin074
  Placement = pos=(0.45,0.125,2.2) rot=(0,0,1;0rad)
FEATURE [Sketcher::SketchObject] Sketch074  label="B plate"
  FullyConstrained = false
  MapMode = 5
  Support = -> [XY_Plane078]
  sketch-geometry (4):
    g0: LineSegment StartX=-47.45 StartY=23.7 StartZ=0 EndX=77.55 EndY=23.7 EndZ=0
    g1: LineSegment StartX=77.55 StartY=23.7 StartZ=0 EndX=77.55 EndY=119.7 EndZ=0
    g2: LineSegment StartX=77.55 StartY=119.7 StartZ=0 EndX=-47.45 EndY=119.7 EndZ=0
    g3: LineSegment StartX=-47.45 StartY=119.7 StartZ=0 EndX=-47.45 EndY=23.7 EndZ=0
  constraints (10):
    c: Coincident(g0,g1)
    c: Coincident(g1,g2)
    c: Coincident(g2,g3)
    c: Coincident(g3,g0)
    c: Horizontal(g0)
    c: Horizontal(g2)
    c: Vertical(g1)
    c: Vertical(g3)
    c: DistanceX(g2,g2) = 125
    c: DistanceY(g1,g1) = 96
FEATURE [Part::Extrusion] Extrude024  label="Extrude060"
  Base = -> Sketch074
  Dir = (0,0,1)
  DirMode = 2
  FaceMakerClass = Part::FaceMakerBullseye
  LengthFwd = 3
  LengthRev = 0
  Reversed = true
  Solid = true
  Symmetric = false
FEATURE [PartDesign::FeatureBase] BaseFeature004
  BaseFeature = -> Extrude024
FEATURE [Sketcher::SketchObject] Sketch075
  FullyConstrained = false
  MapMode = 5
  Placement = pos=(0,0,-3) rot=(1,0,0;3.14159rad)
  Support = -> [BaseFeature004]
  sketch-geometry (4):
    g0: Circle CenterX=-31.331 CenterY=-31.335 CenterZ=0 NormalX=0 NormalY=0 NormalZ=1 AngleXU=0 Radius=1.6
    g1: Circle CenterX=-31.332 CenterY=-112.083 CenterZ=0 NormalX=0 NormalY=0 NormalZ=1 AngleXU=0 Radius=1.6
    g2: Circle CenterX=61.4495 CenterY=-112.078 CenterZ=0 NormalX=0 NormalY=0 NormalZ=1 AngleXU=0 Radius=1.6
    g3: Circle CenterX=61.46 CenterY=-31.285 CenterZ=0 NormalX=0 NormalY=0 NormalZ=1 AngleXU=0 Radius=1.6
  constraints (4):
    c: Diameter(g0) = 3.2
    c: Diameter(g1) = 3.2
    c: Diameter(g2) = 3.2
    c: Diameter(g3) = 3.2
FEATURE [PartDesign::Hole] Hole016
  BaseFeature = -> BaseFeature004
  CustomThreadClearance = 0
  Depth = 3
  DepthType = 0
  Diameter = 3.2
  DrillForDepth = false
  DrillPoint = 1
  DrillPointAngle = 118
  HoleCutCountersinkAngle = 90
  HoleCutCustomValues = false
  HoleCutDepth = 0
  HoleCutDiameter = 6.1
  HoleCutType = 0
  ModelThread = false
  Profile = -> Sketch075
  Tapered = false
  TaperedAngle = 90
  ThreadClass = 0
  ThreadDepth = 3
  ThreadDepthType = 0
  ThreadDirection = 0
  ThreadFit = 0
  ThreadSize = 0
  ThreadType = 0
  Threaded = false
  UseCustomThreadClearance = false
FEATURE [PartDesign::Fillet] Fillet002
  Base = -> Hole016 [Edge1,Edge7,Edge4,Edge2,Edge10,Edge8,Edge16,Edge5]
  BaseFeature = -> Hole016
  Radius = 2
  SupportTransform = false
  UseAllEdges = false
FEATURE [PartDesign::Body] Body005  label="Bottom Plate"
  BaseFeature = -> Extrude024
  Group = -> [BaseFeature004,Sketch075,Hole016,Fillet002]
  Origin = -> Origin078
  Placement = pos=(0,0,-41.83) rot=(0,0,1;0rad)
  Tip = -> Fillet002
FEATURE [App::Part] Part015  label="Bottom cover plate"
  Group = -> [Body005]
  Origin = -> Origin077
  Placement = pos=(0,0,-1.06) rot=(0,0,1;0rad)
FEATURE [App::Part] Part012  label="Enclosure"
  Group = -> [Part011,Part013,Part015]
  Origin = -> Origin073
FEATURE [App::Part] TO_92  label="TO-92"
  Group = -> [Part__Feature300]
  Origin = -> Origin064
  Placement = pos=(77.035,-11.532,1.65) rot=(0,0,1;3.14159rad)
FEATURE [App::Part] TeensyAudioBoard
  Group = -> [COMPOUND004]
  Origin = -> Origin058
  Placement = pos=(12.683,-42.31,2.65) rot=(0,0,1;0rad)
FEATURE [App::Part] Teensy_4_0_Assembly  label="Teensy_4.0_Assembly"
  Group = -> [COMPOUND005]
  Origin = -> Origin060
  Placement = pos=(63.133,-13.31,-16.35) rot=(1,0,0;1.5708rad)
FEATURE [App::Part] AFPI_Device_V1_1_1  label="AFPI Device V1.1 1"
  Group = -> [C_1206_3216Metric,C_1206_3216Metric001,C_1206_3216Metric002,JST_XH_B2B_XH_A_1x02_P2_50mm_Vertical,R_1206_3216Metric,CP_Elec_6_3x7_7,CP_Elec_5x5_4,SOT_223,CP_Elec_8x10_5,R_1206_3216Metric001,R_1206_3216Metric002,TeensyAudioBoard,Teensy_4_0_Assembly,DIP_8_W7_62mm,C_1206_3216Metric003,C_1206_3216Metric004,TO_92,JST_XH_B3B_XH_A_1x03_P2_50mm_Vertical,Part__Feature302]
  Origin = -> Origin066
  Placement = pos=(-27.8,96.2,-26.3) rot=(0,0,1;0rad)
FEATURE [App::Part] Unnamed  label="Power SW"
  Group = -> [Part__Feature212,Part__Feature213,Part__Feature214,Part__Feature215,Part__Feature216,Part__Feature217,Array]
  Origin = -> Origin045
  Placement = pos=(-24.2,87.7,1.4) rot=(0,0,1;4.71239rad)
FEATURE [App::Part] _  label="1"
  Group = -> [Part__Feature042,Part__Feature043]
  Origin = -> Origin019
FEATURE [App::Part] _001  label="2"
  Group = -> [Part__Feature044,Part__Feature045]
  Origin = -> Origin020
  Placement = pos=(2.54,0,0) rot=(0,0,1;0rad)
FEATURE [App::Part] _002  label="3"
  Group = -> [Part__Feature046,Part__Feature047]
  Origin = -> Origin021
  Placement = pos=(5.08,0,0) rot=(0,0,1;0rad)
FEATURE [App::Part] _003  label="4"
  Group = -> [Part__Feature048,Part__Feature049]
  Origin = -> Origin022
  Placement = pos=(7.62,0,0) rot=(0,0,1;0rad)
FEATURE [App::Part] _004  label="5"
  Group = -> [Part__Feature050,Part__Feature051]
  Origin = -> Origin023
  Placement = pos=(10.16,0,0) rot=(0,0,1;0rad)
FEATURE [App::Part] _005  label="6"
  Group = -> [Part__Feature052,Part__Feature053]
  Origin = -> Origin024
  Placement = pos=(12.7,0,0) rot=(0,0,1;0rad)
FEATURE [App::Part] _006  label="1001"
  Group = -> [Part__Feature068,Part__Feature069]
  Origin = -> Origin028
FEATURE [App::Part] _007  label="2001"
  Group = -> [Part__Feature070,Part__Feature071]
  Origin = -> Origin029
  Placement = pos=(2.54,0,0) rot=(0,0,1;0rad)
FEATURE [App::Part] _008  label="3001"
  Group = -> [Part__Feature072,Part__Feature073]
  Origin = -> Origin030
  Placement = pos=(5.08,0,0) rot=(0,0,1;0rad)
FEATURE [App::Part] _009  label="4001"
  Group = -> [Part__Feature074,Part__Feature075]
  Origin = -> Origin031
  Placement = pos=(7.62,0,0) rot=(0,0,1;0rad)
FEATURE [App::Part] _010  label="5001"
  Group = -> [Part__Feature076,Part__Feature077]
  Origin = -> Origin032
  Placement = pos=(10.16,0,0) rot=(0,0,1;0rad)
FEATURE [App::Part] _011  label="6001"
  Group = -> [Part__Feature078,Part__Feature079]
  Origin = -> Origin033
  Placement = pos=(12.7,0,0) rot=(0,0,1;0rad)
FEATURE [App::Part] _PIN_HEADER  label="6PIN_HEADER"
  Group = -> [_,_001,_002,_003,_004,_005]
  Origin = -> Origin025
  Placement = pos=(31.75,19.68,-1.6) rot=(0,0,1;0rad)
FEATURE [App::Part] _PIN_HEADER001  label="6PIN_HEADER001"
  Group = -> [_006,_007,_008,_009,_010,_011]
  Origin = -> Origin034
  Placement = pos=(31.75,1.91,-1.6) rot=(0,0,1;0rad)
FEATURE [App::Part] ADAFRUIT_ENCODER
  Group = -> [SW_PEC11R_4215F_S0024,SW_PEC11R_4215F_S0025,SW_PEC11R_4215F_S0026,SW_PEC11R_4215F_S0027,ATTINY817,_PIN_HEADER,BMxB_SRSS_TB,BMxB_SRSS_TB001,_PIN_HEADER001,PCB001,NEO3535_REVERSE,NEO3535_REVERSE001,NEO3535_REVERSE002,NEO3535_REVERSE003]
  Origin = -> Origin041
  Placement = pos=(-15.1,54,-2.4) rot=(1,0,0;3.14159rad)
FEATURE [App::Part] Part006  label="Peripherals"
  Group = -> [Part005,ADAFRUIT_ENCODER,Pushbutton_v16,Unnamed]
  Origin = -> Origin043
  Placement = pos=(-1.1,0,-2.3) rot=(0,0,1;0rad)
FEATURE [App::Part] Part010  label="Internal Components"
  Group = -> [Part006,AFPI_Device_V1_1_1]
  Origin = -> Origin070
FEATURE [App::Part] Part004  label="AFPI Device and Enclosure"
  Group = -> [Part010,Part012,Part008]
  Origin = -> Origin006
  Placement = pos=(42.3,469.8,42.9) rot=(0,0,1;4.71239rad)
FEATURE [Part::Feature] Part__Feature303  label="M2.5_MF_TORRETTA"
  Placement = pos=(-38.55,10.82,-10.01) rot=(0,0,1;0rad)
  shape: bbox 5.78 x 5.78 x 16.02 mm, 16 faces (baked)
FEATURE [Part::Feature] Part__Feature304  label="M2.5_MF_TORRETTA001"
  Placement = pos=(39.79,10.82,-10.01) rot=(0,0,1;0rad)
  shape: bbox 5.78 x 5.78 x 16.02 mm, 16 faces (baked)
FEATURE [Part::Feature] Part__Feature305  label="SOLID022"
  shape: bbox 3.2 x 1.6 x 0.55 mm, 26 faces (baked)
FEATURE [Part::Feature] Part__Feature306  label="SOLID023"
  shape: bbox 3.2 x 1.6 x 1.6 mm, 28 faces (baked)
FEATURE [App::Part] C_1206_3216Metric008
  Group = -> [Part__Feature306]
  Origin = -> Origin084
  Placement = pos=(-7.575,15.225,1.65) rot=(0,0,1;0rad)
FEATURE [Part::Feature] Part__Feature307  label="SOLID024"
  shape: bbox 6.985 x 6.828 x 5.4 mm, 41 faces (baked)
FEATURE [App::Part] CP_Elec_5x5_005  label="CP_Elec_5x5.005"
  Group = -> [Part__Feature307]
  Origin = -> Origin085
  Placement = pos=(-32.5875,14.125,1.65) rot=(0,0,1;0rad)
FEATURE [Part::Feature] Part__Feature308  label="SOLID025"
  shape: bbox 7 x 4.95 x 4.2 mm, 162 faces (baked)
FEATURE [App::Part] JST_GH_BM03B_GHS_TBT_1x03_1MP_P1_25mm_Vertical004  label="JST_GH_BM03B-GHS-TBT_1x03-1MP_P1.25mm_Vertical004"
  Group = -> [Part__Feature308]
  Origin = -> Origin086
  Placement = pos=(32.3125,7.9,1.65) rot=(0,0,1;3.14159rad)
FEATURE [Part::Feature] Part__Feature309  label="SOLID026"
  shape: bbox 5.4 x 5 x 1.6 mm, 68 faces (baked)
FEATURE [App::Part] LED_WS2812B_PLCC4_5_0x5_0mm_P3_2mm008  label="LED_WS2812B_PLCC4_5.0x5.0mm_P3.2mm008"
  Group = -> [Part__Feature309]
  Origin = -> Origin087
  Placement = pos=(-6.1875,10.825,1.65) rot=(0,0,1;3.14159rad)
FEATURE [Part::Feature] Part__Feature310  label="SOLID027"
  shape: bbox 3.2 x 1.6 x 1.6 mm, 28 faces (baked)
FEATURE [App::Part] C_1206_3216Metric009
  Group = -> [Part__Feature310]
  Origin = -> Origin088
  Placement = pos=(18.1125,15.225,1.65) rot=(0,0,1;0rad)
FEATURE [Part::Feature] Part__Feature311  label="SOLID028"
  shape: bbox 3.2 x 1.6 x 1.6 mm, 28 faces (baked)
FEATURE [App::Part] C_1206_3216Metric010
  Group = -> [Part__Feature311]
  Origin = -> Origin089
  Placement = pos=(5.25,15.2,1.65) rot=(0,0,1;0rad)
FEATURE [Part::Feature] Part__Feature312  label="SOLID029"
  shape: bbox 3.2 x 1.6 x 1.6 mm, 28 faces (baked)
FEATURE [App::Part] C_1206_3216Metric011
  Group = -> [Part__Feature312]
  Origin = -> Origin090
  Placement = pos=(-20.3625,15.225,1.65) rot=(0,0,1;0rad)
FEATURE [Part::Feature] Part__Feature313  label="SOLID030"
  shape: bbox 5.4 x 5 x 1.6 mm, 68 faces (baked)
FEATURE [App::Part] LED_WS2812B_PLCC4_5_0x5_0mm_P3_2mm009  label="LED_WS2812B_PLCC4_5.0x5.0mm_P3.2mm009"
  Group = -> [Part__Feature313]
  Origin = -> Origin091
  Placement = pos=(-19.0375,10.825,1.65) rot=(0,0,1;3.14159rad)
FEATURE [Part::Feature] Part__Feature314  label="SOLID031"
  shape: bbox 5.4 x 5 x 1.6 mm, 68 faces (baked)
FEATURE [App::Part] LED_WS2812B_PLCC4_5_0x5_0mm_P3_2mm010  label="LED_WS2812B_PLCC4_5.0x5.0mm_P3.2mm010"
  Group = -> [Part__Feature314]
  Origin = -> Origin092
  Placement = pos=(6.6375,10.825,1.65) rot=(0,0,1;3.14159rad)
FEATURE [Part::Feature] Part__Feature315  label="SOLID032"
  shape: bbox 5.4 x 5 x 1.6 mm, 68 faces (baked)
FEATURE [App::Part] LED_WS2812B_PLCC4_5_0x5_0mm_P3_2mm011  label="LED_WS2812B_PLCC4_5.0x5.0mm_P3.2mm011"
  Group = -> [Part__Feature315]
  Origin = -> Origin093
  Placement = pos=(19.5125,10.825,1.65) rot=(0,0,1;3.14159rad)
FEATURE [Part::Feature] Part__Feature316  label="SOLID033"
  shape: bbox 7 x 4.95 x 4.2 mm, 162 faces (baked)
FEATURE [App::Part] JST_GH_BM03B_GHS_TBT_1x03_1MP_P1_25mm_Vertical005  label="JST_GH_BM03B-GHS-TBT_1x03-1MP_P1.25mm_Vertical005"
  Group = -> [Part__Feature316]
  Origin = -> Origin094
  Placement = pos=(-32.3375,6.75,1.65) rot=(0,0,1;3.14159rad)
FEATURE [Part::Feature] Part__Feature317  label="_autosave-RGB LED Mounting Board PCB003"
  shape: bbox 84 x 15 x 1.6 mm, 8 faces (baked)
FEATURE [App::Part] R_1206_3216Metric003
  Group = -> [Part__Feature305]
  Origin = -> Origin083
  Placement = pos=(-25.2625,6.65,1.65) rot=(0,0,-1;1.5708rad)
FEATURE [App::Part] Part017  label="PCB 1"
  Group = -> [CP_Elec_5x5_005,C_1206_3216Metric008,C_1206_3216Metric009,C_1206_3216Metric010,C_1206_3216Metric011,JST_GH_BM03B_GHS_TBT_1x03_1MP_P1_25mm_Vertical004,JST_GH_BM03B_GHS_TBT_1x03_1MP_P1_25mm_Vertical005,LED_WS2812B_PLCC4_5_0x5_0mm_P3_2mm008,LED_WS2812B_PLCC4_5_0x5_0mm_P3_2mm009,LED_WS2812B_PLCC4_5_0x5_0mm_P3_2mm010,LED_WS2812B_PLCC4_5_0x5_0mm_P3_2mm011,R_1206_3216Metric003,Part__Feature317]
  Origin = -> Origin082
  Placement = pos=(0.6,0,-11.45) rot=(0,0,1;0rad)
FEATURE [Sketcher::SketchObject] Sketch076
  FullyConstrained = false
  sketch-geometry (5):
    g0: LineSegment StartX=-46.38 StartY=20.9 StartZ=0 EndX=47.62 EndY=20.9 EndZ=0
    g1: LineSegment StartX=47.62 StartY=20.9 StartZ=0 EndX=47.62 EndY=0.899999 EndZ=0
    g2: LineSegment StartX=47.62 StartY=0.899999 StartZ=0 EndX=-46.38 EndY=0.899999 EndZ=0
    g3: LineSegment StartX=-46.38 StartY=0.899999 StartZ=0 EndX=-46.38 EndY=20.9 EndZ=0
    g4: LineSegment StartX=-41.3775 StartY=18.375 StartZ=0 EndX=-41.3775 EndY=20.9 EndZ=0
  constraints (11):
    c: Coincident(g0,g1)
    c: Coincident(g1,g2)
    c: Coincident(g2,g3)
    c: Coincident(g3,g0)
    c: Horizontal(g0)
    c: Horizontal(g2)
    c: Vertical(g1)
    c: Vertical(g3)
    c: DistanceX(g0,g0) = 94
    c: DistanceY(g3,g3) = 20
    c: Vertical(g4)
FEATURE [Part::Extrusion] Extrude025  label="Extrude061"
  Base = -> Sketch076
  Dir = (0,0,1)
  DirMode = 2
  FaceMakerClass = Part::FaceMakerBullseye
  LengthFwd = 3
  LengthRev = 0
  Solid = true
  Symmetric = false
FEATURE [PartDesign::FeatureBase] BaseFeature005
  BaseFeature = -> Extrude025
FEATURE [Sketcher::SketchObject] Sketch077
  FullyConstrained = false
  MapMode = 5
  Placement = pos=(0,0,3) rot=(0,0,1;0rad)
  Support = -> [BaseFeature005]
  sketch-geometry (2):
    g0: Circle CenterX=-38.55 CenterY=10.83 CenterZ=0 NormalX=0 NormalY=0 NormalZ=1 AngleXU=0 Radius=1.25
    g1: Circle CenterX=39.8 CenterY=10.8236 CenterZ=0 NormalX=0 NormalY=0 NormalZ=1 AngleXU=0 Radius=1.25
  constraints (2):
    c: Diameter(g0) = 2.5
    c: Diameter(g1) = 2.5
FEATURE [PartDesign::Hole] Hole017
  BaseFeature = -> BaseFeature005
  CustomThreadClearance = 0
  Depth = 3
  DepthType = 0
  Diameter = 2.5
  DrillForDepth = false
  DrillPoint = 0
  DrillPointAngle = 118
  HoleCutCountersinkAngle = 90
  HoleCutCustomValues = false
  HoleCutDepth = 0
  HoleCutDiameter = 6.1
  HoleCutType = 0
  ModelThread = false
  Profile = -> Sketch077
  Tapered = false
  TaperedAngle = 90
  ThreadClass = 0
  ThreadDepth = 3
  ThreadDepthType = 0
  ThreadDirection = 0
  ThreadFit = 0
  ThreadSize = 0
  ThreadType = 0
  Threaded = false
  UseCustomThreadClearance = false
FEATURE [PartDesign::Fillet] Fillet003
  Base = -> Hole017 [Edge5,Edge1,Edge2,Edge8]
  BaseFeature = -> Hole017
  Radius = 6
  SupportTransform = false
  UseAllEdges = false
FEATURE [Sketcher::SketchObject] Sketch078
  FullyConstrained = false
  MapMode = 5
  Placement = pos=(0,0,3) rot=(0,0,1;0rad)
  Support = -> [Fillet003]
  sketch-geometry (4):
    g0: LineSegment StartX=-23.0016 StartY=0.200001 StartZ=0 EndX=-46.4016 EndY=0.200001 EndZ=0
    g1: LineSegment StartX=-46.4016 StartY=0.200001 StartZ=0 EndX=-46.4016 EndY=21.2 EndZ=0
    g2: LineSegment StartX=-46.4016 StartY=21.2 StartZ=0 EndX=-23.0016 EndY=21.2 EndZ=0
    g3: LineSegment StartX=-23.0016 StartY=21.2 StartZ=0 EndX=-23.0016 EndY=0.200001 EndZ=0
  constraints (10):
    c: Coincident(g0,g1)
    c: Coincident(g1,g2)
    c: Coincident(g2,g3)
    c: Coincident(g3,g0)
    c: Horizontal(g0)
    c: Horizontal(g2)
    c: Vertical(g1)
    c: Vertical(g3)
    c: DistanceX(g2,g2) = 23.4
    c: DistanceY(g1,g1) = 21
FEATURE [PartDesign::Pocket] Pocket015
  BaseFeature = -> Fillet003
  Direction = (0,0,-1)
  Length = 1.5
  Length2 = 5
  Profile = -> Sketch078
  ReferenceAxis = -> Sketch078 [N_Axis]
  Type = 0
FEATURE [Sketcher::SketchObject] Sketch079
  FullyConstrained = false
  MapMode = 5
  Placement = pos=(0,0,3) rot=(0,0,1;0rad)
  Support = -> [Pocket015]
  sketch-geometry (4):
    g0: LineSegment StartX=24.7 StartY=21.1996 StartZ=0 EndX=48.1 EndY=21.1996 EndZ=0
    g1: LineSegment StartX=48.1 StartY=21.1996 StartZ=0 EndX=48.1 EndY=0.199637 EndZ=0
    g2: LineSegment StartX=48.1 StartY=0.199637 StartZ=0 EndX=24.7 EndY=0.199637 EndZ=0
    g3: LineSegment StartX=24.7 StartY=0.199637 StartZ=0 EndX=24.7 EndY=21.1996 EndZ=0
  constraints (10):
    c: Coincident(g0,g1)
    c: Coincident(g1,g2)
    c: Coincident(g2,g3)
    c: Coincident(g3,g0)
    c: Horizontal(g0)
    c: Horizontal(g2)
    c: Vertical(g1)
    c: Vertical(g3)
    c: DistanceX(g0,g0) = 23.4
    c: DistanceY(g3,g3) = 21
FEATURE [PartDesign::Pocket] Pocket016
  BaseFeature = -> Pocket015
  Direction = (0,0,-1)
  Length = 1.5
  Length2 = 5
  Profile = -> Sketch079
  ReferenceAxis = -> Sketch079 [N_Axis]
  Type = 0
FEATURE [PartDesign::Body] Body006  label="Body009"
  BaseFeature = -> Extrude025
  Group = -> [BaseFeature005,Sketch077,Hole017,Fillet003,Sketch078,Pocket015,Sketch079,Pocket016]
  Origin = -> Origin081
  Tip = -> Pocket016
FEATURE [App::Part] Part018  label="B1 Top plate"
  Group = -> [Body006,Sketch076,Extrude025]
  Origin = -> Origin080
FEATURE [PartDesign::Body] BaseFeature010Body
  Origin = -> Origin117
FEATURE [PartDesign::Body] Body007  label="CELL MOUNT BODY"
  Origin = -> Origin098
FEATURE [PartDesign::Body] Body008  label="BACK BODY"
  Origin = -> Origin100
FEATURE [PartDesign::Body] Body011  label="HANDLE FASTEN PIN BODY"
  Origin = -> Origin106
FEATURE [App::MeasureDistance] Distance019  label="Distance: 3.33780 mm"
  Distance = 3.3378
  P1 = (43.5,-109.3,19.3861)
  P2 = (43.16,-112.62,19.44)
FEATURE [App::MeasureDistance] Distance020  label="Distance: 94.93000 mm"
  Distance = 94.93
  P1 = (84.2,-109.301,22.88)
  P2 = (84.2,-14.3705,22.88)
FEATURE [App::MeasureDistance] Distance021  label="Distance: 84.03434 mm"
  Distance = 84.0343
  P1 = (0.165655,-109.301,22.88)
  P2 = (84.2,-109.301,22.88)
FEATURE [App::MeasureDistance] Distance022  label="Distance: 22.78329 mm"
  Distance = 22.7833
  P1 = (0,-14.3705,22.7833)
  P2 = (0,-14.4,0)
FEATURE [App::MeasureDistance] Distance023  label="Distance: 10.06841 mm"
  Distance = 10.0684
  P1 = (82.0192,-16.37,21.3)
  P2 = (82.2,-26.4368,21.3)
FEATURE [App::MeasureDistance] Distance024  label="Distance: 7.48747 mm"
  Distance = 7.48747
  P1 = (82.0952,-107.281,21.3)
  P2 = (82.1396,-99.794,21.3)
FEATURE [App::MeasureDistance] Distance025  label="Distance: 1.03116 mm"
  Distance = 1.03116
  P1 = (82.2,-95.6714,11.6529)
  P2 = (82.1272,-96.7,11.65)
FEATURE [App::MeasureDistance] Distance026  label="Distance: 0.98878 mm"
  Distance = 0.988782
  P1 = (62.8884,-97.788,21.3)
  P2 = (61.9,-97.7591,21.3)
FEATURE [App::MeasureDistance] Distance027  label="Distance: 3.00017 mm"
  Distance = 3.00017
  P1 = (0,-109.3,3.96765)
  P2 = (-3,-109.3,3.93616)
FEATURE [App::MeasureDistance] Distance028  label="Distance: 90.20000 mm"
  Distance = 90.2
  P1 = (-3,-109.3,0)
  P2 = (87.2,-109.302,0)
FEATURE [App::MeasureDistance] Distance029  label="Distance: 94.80000 mm"
  Distance = 94.8
  P1 = (89.5,2.74181e-07,-2.3)
  P2 = (-5.3,2.74181e-07,-2.3)
FEATURE [App::MeasureDistance] Distance030  label="Distance: 94.92901 mm"
  Distance = 94.929
  P1 = (0,-109.3,22.6426)
  P2 = (0,-14.3705,22.6545)
FEATURE [App::Part] Part027  label="Batt Measurements"
  Group = -> [Distance019,Distance020,Distance021,Distance022,Distance023,Distance024,Distance025,Distance026,Distance027,Distance028,Distance029,Distance030]
  Origin = -> Origin110
FEATURE [Part::Feature] Part__Feature318  label="cell 001"
  Placement = pos=(11.67,-30.7,11.73) rot=(1,0,0;1.5708rad)
  shape: bbox 19.48 x 65 x 19.48 mm, 202 faces (baked)
FEATURE [Part::Feature] Part__Feature319  label="cell 002"
  Placement = pos=(32.21,-30.56,12.09) rot=(1,0,0;1.5708rad)
  shape: bbox 19.48 x 65 x 19.48 mm, 202 faces (baked)
FEATURE [Part::Feature] Part__Feature320  label="cell 003"
  Placement = pos=(52.45,-30.79,11.7) rot=(1,0,0;1.5708rad)
  shape: bbox 19.48 x 65 x 19.48 mm, 202 faces (baked)
FEATURE [Part::Feature] Part__Feature321  label="cell 004"
  Placement = pos=(72.58,-30.46,11.13) rot=(1,0,0;1.5708rad)
  shape: bbox 19.48 x 65 x 19.48 mm, 202 faces (baked)
FEATURE [App::Part] Part022  label="Batt Cells"
  Group = -> [Part__Feature318,Part__Feature319,Part__Feature320,Part__Feature321]
  Origin = -> Origin099
FEATURE [Sketcher::SketchObject] Sketch080
  FullyConstrained = false
  MapMode = 5
  Support = -> [XY_Plane098]
  sketch-geometry (4):
    g0: LineSegment StartX=0 StartY=-99.794 StartZ=0 EndX=84.2 EndY=-99.794 EndZ=0
    g1: LineSegment StartX=84.2 StartY=-99.794 StartZ=0 EndX=84.2 EndY=-26.494 EndZ=0
    g2: LineSegment StartX=84.2 StartY=-26.494 StartZ=0 EndX=0 EndY=-26.494 EndZ=0
    g3: LineSegment StartX=0 StartY=-26.494 StartZ=0 EndX=0 EndY=-99.794 EndZ=0
  constraints (10):
    c: Coincident(g0,g1)
    c: Coincident(g1,g2)
    c: Coincident(g2,g3)
    c: Coincident(g3,g0)
    c: Horizontal(g0)
    c: Horizontal(g2)
    c: Vertical(g1)
    c: Vertical(g3)
    c: DistanceX(g2,g2) = 84.2
    c: DistanceY(g3,g3) = 73.3
FEATURE [Part::Extrusion] Extrude026  label="CELL MOUNT FLOOR"
  Base = -> Sketch080
  Dir = (0,0,1)
  DirMode = 2
  FaceMakerClass = Part::FaceMakerBullseye
  LengthFwd = 2
  LengthRev = 0
  Solid = true
  Symmetric = false
FEATURE [Sketcher::SketchObject] Sketch081
  FullyConstrained = false
  MapMode = 5
  Placement = pos=(0,0,2) rot=(0,0,1;0rad)
  Support = -> [Extrude026]
  sketch-geometry (12):
    g0: LineSegment StartX=0 StartY=-26.494 StartZ=0 EndX=84.2 EndY=-26.494 EndZ=0
    g1: LineSegment StartX=84.2 StartY=-26.494 StartZ=0 EndX=84.2 EndY=-99.794 EndZ=0
    g2: LineSegment StartX=84.2 StartY=-99.794 StartZ=0 EndX=0 EndY=-99.794 EndZ=0
    g3: LineSegment StartX=0 StartY=-99.794 StartZ=0 EndX=0 EndY=-26.494 EndZ=0
    g4: LineSegment StartX=84.2 StartY=-99.794 StartZ=0 EndX=84.2 EndY=-97.79 EndZ=0
    g5: LineSegment StartX=84.2 StartY=-97.79 StartZ=0 EndX=82.2 EndY=-97.79 EndZ=0
    g6: LineSegment StartX=0 StartY=-26.494 StartZ=0 EndX=0 EndY=-28.49 EndZ=0
    g7: LineSegment StartX=0 StartY=-28.49 StartZ=0 EndX=2 EndY=-28.49 EndZ=0
    g8: LineSegment StartX=2 StartY=-28.49 StartZ=0 EndX=82.2 EndY=-28.49 EndZ=0
    g9: LineSegment StartX=82.2 StartY=-28.49 StartZ=0 EndX=82.2 EndY=-97.79 EndZ=0
    g10: LineSegment StartX=82.2 StartY=-97.79 StartZ=0 EndX=2 EndY=-97.79 EndZ=0
    g11: LineSegment StartX=2 StartY=-97.79 StartZ=0 EndX=2 EndY=-28.49 EndZ=0
  constraints (31):
    c: Coincident(g0,g1)
    c: Coincident(g1,g2)
    c: Coincident(g2,g3)
    c: Coincident(g3,g0)
    c: Horizontal(g0)
    c: Horizontal(g2)
    c: Vertical(g1)
    c: Vertical(g3)
    c: PointOnObject(g0,g-2)
    c: DistanceX(g2,g2) = 84.2
    c: DistanceY(g1,g1) = 73.3
    c: Coincident(g4,g1)
    c: PointOnObject(g4,g1)
    c: Coincident(g5,g4)
    c: Horizontal(g5)
    c: Coincident(g6,g0)
    c: PointOnObject(g6,g3)
    c: Coincident(g7,g6)
    c: Horizontal(g7)
    c: Coincident(g8,g9)
    c: Coincident(g9,g10)
    c: Coincident(g10,g11)
    c: Coincident(g11,g8)
    c: Horizontal(g8)
    c: Horizontal(g10)
    c: Vertical(g9)
    c: Vertical(g11)
    c: Coincident(g8,g7)
    c: Coincident(g9,g5)
    c: DistanceX(g8,g8) = 80.2
    c: DistanceY(g9,g9) = 69.3
FEATURE [Part::Extrusion] Extrude027  label="CELL MOUNT EXT WALLS"
  Base = -> Sketch081
  Dir = (0,0,1)
  DirMode = 2
  FaceMakerClass = Part::FaceMakerBullseye
  LengthFwd = 19.3
  LengthRev = 0
  Solid = true
  Symmetric = false
FEATURE [PartDesign::FeatureBase] BaseFeature012
  BaseFeature = -> Extrude027
FEATURE [Sketcher::SketchObject] Sketch082
  FullyConstrained = false
  MapMode = 5
  Placement = pos=(0,0,2) rot=(0,0,1;0rad)
  Support = -> [Extrude026]
  sketch-geometry (15):
    g0: LineSegment StartX=22.2999 StartY=-28.6 StartZ=0 EndX=41.5999 EndY=-28.6 EndZ=0
    g1: LineSegment StartX=21.2995 StartY=-28.49 StartZ=0 EndX=22.2995 EndY=-28.49 EndZ=0
    g2: LineSegment StartX=22.2995 StartY=-28.49 StartZ=0 EndX=22.2995 EndY=-97.8 EndZ=0
    g3: LineSegment StartX=22.2995 StartY=-97.8 StartZ=0 EndX=21.2995 EndY=-97.8 EndZ=0
    g4: LineSegment StartX=21.2995 StartY=-97.8 StartZ=0 EndX=21.2995 EndY=-28.49 EndZ=0
    g5: LineSegment StartX=41.6 StartY=-28.49 StartZ=0 EndX=42.6 EndY=-28.49 EndZ=0
    g6: LineSegment StartX=42.6 StartY=-28.49 StartZ=0 EndX=42.6 EndY=-97.79 EndZ=0
    g7: LineSegment StartX=42.6 StartY=-97.79 StartZ=0 EndX=41.6 EndY=-97.79 EndZ=0
    g8: LineSegment StartX=41.6 StartY=-97.79 StartZ=0 EndX=41.6 EndY=-28.49 EndZ=0
    g9: LineSegment StartX=42.6 StartY=-28.6021 StartZ=0 EndX=61.9 EndY=-28.6021 EndZ=0
    g10: LineSegment StartX=61.9 StartY=-28.49 StartZ=0 EndX=62.9 EndY=-28.49 EndZ=0
    g11: LineSegment StartX=62.9 StartY=-28.49 StartZ=0 EndX=62.9 EndY=-97.8 EndZ=0
    g12: LineSegment StartX=62.9 StartY=-97.8 StartZ=0 EndX=61.9 EndY=-97.8 EndZ=0
    g13: LineSegment StartX=61.9 StartY=-97.8 StartZ=0 EndX=61.9 EndY=-28.49 EndZ=0
    g14: LineSegment StartX=62.9 StartY=-28.601 StartZ=0 EndX=82.2 EndY=-28.601 EndZ=0
  constraints (38):
    c: Horizontal(g0)
    c: Coincident(g1,g2)
    c: Coincident(g2,g3)
    c: Coincident(g3,g4)
    c: Coincident(g4,g1)
    c: Horizontal(g1)
    c: Horizontal(g3)
    c: Vertical(g2)
    c: Vertical(g4)
    c: Coincident(g5,g6)
    c: Coincident(g6,g7)
    c: Coincident(g7,g8)
    c: Coincident(g8,g5)
    c: Horizontal(g5)
    c: Horizontal(g7)
    c: Vertical(g6)
    c: Vertical(g8)
    c: PointOnObject(g9,g6)
    c: Horizontal(g9)
    c: Coincident(g10,g11)
    c: Coincident(g11,g12)
    c: Coincident(g12,g13)
    c: Coincident(g13,g10)
    c: Horizontal(g10)
    c: Horizontal(g12)
    c: Vertical(g11)
    c: Vertical(g13)
    c: PointOnObject(g14,g11)
    c: Horizontal(g14)
    c: DistanceY(g4,g4) = 69.31
    c: DistanceY(g8,g8) = 69.3
    c: DistanceY(g13,g13) = 69.31
    c: DistanceX(g1,g1) = 1
    c: DistanceX(g0,g0) = 19.3
    c: DistanceX(g9,g9) = 19.3
    c: DistanceX(g5,g5) = 1
    c: DistanceX(g10,g10) = 1
    c: DistanceX(g14,g14) = 19.3
FEATURE [Part::Extrusion] Extrude028  label="CELL DIVIDER WALLS"
  Base = -> Sketch082
  Dir = (0,0,1)
  DirMode = 2
  FaceMakerClass = Part::FaceMakerBullseye
  LengthFwd = 19.3
  LengthRev = 0
  Solid = true
  Symmetric = false
FEATURE [Sketcher::SketchObject] Sketch083
  FullyConstrained = false
  MapMode = 5
  Placement = pos=(0,0,2) rot=(0,0,1;0rad)
  Support = -> [Extrude026]
  sketch-geometry (66):
    g0: LineSegment StartX=2.1 StartY=-28.49 StartZ=0 EndX=2.1 EndY=-29.49 EndZ=0
    g1: LineSegment StartX=2 StartY=-29.5 StartZ=0 EndX=6.5 EndY=-29.5 EndZ=0
    g2: LineSegment StartX=6.5 StartY=-29.5 StartZ=0 EndX=6.5 EndY=-30.5 EndZ=0
    g3: LineSegment StartX=6.5 StartY=-30.5 StartZ=0 EndX=2 EndY=-30.5 EndZ=0
    g4: LineSegment StartX=2 StartY=-30.5 StartZ=0 EndX=2 EndY=-29.5 EndZ=0
    g5: LineSegment StartX=21.3 StartY=-29.49 StartZ=0 EndX=16.8 EndY=-29.49 EndZ=0
    g6: LineSegment StartX=16.8 StartY=-29.49 StartZ=0 EndX=16.8 EndY=-30.49 EndZ=0
    g7: LineSegment StartX=16.8 StartY=-30.49 StartZ=0 EndX=21.3 EndY=-30.49 EndZ=0
    g8: LineSegment StartX=21.3 StartY=-30.49 StartZ=0 EndX=21.3 EndY=-29.49 EndZ=0
    g9: LineSegment StartX=22.3 StartY=-30.49 StartZ=0 EndX=26.8 EndY=-30.49 EndZ=0
    g10: LineSegment StartX=26.8 StartY=-30.49 StartZ=0 EndX=26.8 EndY=-29.49 EndZ=0
    g11: LineSegment StartX=26.8 StartY=-29.49 StartZ=0 EndX=22.3 EndY=-29.49 EndZ=0
    g12: LineSegment StartX=22.3 StartY=-29.49 StartZ=0 EndX=22.3 EndY=-30.49 EndZ=0
    g13: LineSegment StartX=41.6 StartY=-29.5 StartZ=0 EndX=37.1 EndY=-29.5 EndZ=0
    g14: LineSegment StartX=37.1 StartY=-29.5 StartZ=0 EndX=37.1 EndY=-30.5 EndZ=0
    g15: LineSegment StartX=37.1 StartY=-30.5 StartZ=0 EndX=41.6 EndY=-30.5 EndZ=0
    g16: LineSegment StartX=41.6 StartY=-30.5 StartZ=0 EndX=41.6 EndY=-29.5 EndZ=0
    g17: LineSegment StartX=42.6 StartY=-29.5 StartZ=0 EndX=47.1 EndY=-29.5 EndZ=0
    g18: LineSegment StartX=47.1 StartY=-29.5 StartZ=0 EndX=47.1 EndY=-30.5 EndZ=0
    g19: LineSegment StartX=47.1 StartY=-30.5 StartZ=0 EndX=42.6 EndY=-30.5 EndZ=0
    g20: LineSegment StartX=42.6 StartY=-30.5 StartZ=0 EndX=42.6 EndY=-29.5 EndZ=0
    g21: LineSegment StartX=61.9 StartY=-29.5 StartZ=0 EndX=57.4 EndY=-29.5 EndZ=0
    g22: LineSegment StartX=57.4 StartY=-29.5 StartZ=0 EndX=57.4 EndY=-30.5 EndZ=0
    g23: LineSegment StartX=57.4 StartY=-30.5 StartZ=0 EndX=61.9 EndY=-30.5 EndZ=0
    g24: LineSegment StartX=61.9 StartY=-30.5 StartZ=0 EndX=61.9 EndY=-29.5 EndZ=0
    g25: LineSegment StartX=62.9 StartY=-29.5 StartZ=0 EndX=67.4 EndY=-29.5 EndZ=0
    g26: LineSegment StartX=67.4 StartY=-29.5 StartZ=0 EndX=67.4 EndY=-30.5 EndZ=0
    g27: LineSegment StartX=67.4 StartY=-30.5 StartZ=0 EndX=62.9 EndY=-30.5 EndZ=0
    g28: LineSegment StartX=62.9 StartY=-30.5 StartZ=0 EndX=62.9 EndY=-29.5 EndZ=0
    g29: LineSegment StartX=82.2 StartY=-29.5 StartZ=0 EndX=77.7 EndY=-29.5 EndZ=0
    g30: LineSegment StartX=77.7 StartY=-29.5 StartZ=0 EndX=77.7 EndY=-30.5 EndZ=0
    g31: LineSegment StartX=77.7 StartY=-30.5 StartZ=0 EndX=82.2 EndY=-30.5 EndZ=0
    g32: LineSegment StartX=82.2 StartY=-30.5 StartZ=0 EndX=82.2 EndY=-29.5 EndZ=0
    g33: LineSegment StartX=2.1 StartY=-97.79 StartZ=0 EndX=2.1 EndY=-96.7 EndZ=0
    g34: LineSegment StartX=2 StartY=-96.7 StartZ=0 EndX=6.5 EndY=-96.7 EndZ=0
    g35: LineSegment StartX=6.5 StartY=-96.7 StartZ=0 EndX=6.5 EndY=-95.7 EndZ=0
    g36: LineSegment StartX=6.5 StartY=-95.7 StartZ=0 EndX=2 EndY=-95.7 EndZ=0
    g37: LineSegment StartX=2 StartY=-95.7 StartZ=0 EndX=2 EndY=-96.7 EndZ=0
    g38: LineSegment StartX=21.3 StartY=-95.7 StartZ=0 EndX=16.8 EndY=-95.7 EndZ=0
    g39: LineSegment StartX=16.8 StartY=-95.7 StartZ=0 EndX=16.8 EndY=-96.7 EndZ=0
    g40: LineSegment StartX=16.8 StartY=-96.7 StartZ=0 EndX=21.3 EndY=-96.7 EndZ=0
    g41: LineSegment StartX=21.3 StartY=-96.7 StartZ=0 EndX=21.3 EndY=-95.7 EndZ=0
    g42: LineSegment StartX=22.3 StartY=-96.7 StartZ=0 EndX=26.8 EndY=-96.7 EndZ=0
    g43: LineSegment StartX=26.8 StartY=-96.7 StartZ=0 EndX=26.8 EndY=-95.7 EndZ=0
    g44: LineSegment StartX=26.8 StartY=-95.7 StartZ=0 EndX=22.3 EndY=-95.7 EndZ=0
    g45: LineSegment StartX=22.3 StartY=-95.7 StartZ=0 EndX=22.3 EndY=-96.7 EndZ=0
    g46: LineSegment StartX=41.6 StartY=-95.7 StartZ=0 EndX=37.1 EndY=-95.7 EndZ=0
    g47: LineSegment StartX=37.1 StartY=-95.7 StartZ=0 EndX=37.1 EndY=-96.7 EndZ=0
    g48: LineSegment StartX=37.1 StartY=-96.7 StartZ=0 EndX=41.6 EndY=-96.7 EndZ=0
    g49: LineSegment StartX=41.6 StartY=-96.7 StartZ=0 EndX=41.6 EndY=-95.7 EndZ=0
    g50: LineSegment StartX=42.6 StartY=-96.7 StartZ=0 EndX=47.1 EndY=-96.7 EndZ=0
    g51: LineSegment StartX=47.1 StartY=-96.7 StartZ=0 EndX=47.1 EndY=-95.7 EndZ=0
    g52: LineSegment StartX=47.1 StartY=-95.7 StartZ=0 EndX=42.6 EndY=-95.7 EndZ=0
    g53: LineSegment StartX=42.6 StartY=-95.7 StartZ=0 EndX=42.6 EndY=-96.7 EndZ=0
    g54: LineSegment StartX=61.9 StartY=-95.7 StartZ=0 EndX=57.4 EndY=-95.7 EndZ=0
    g55: LineSegment StartX=57.4 StartY=-95.7 StartZ=0 EndX=57.4 EndY=-96.7 EndZ=0
    g56: LineSegment StartX=57.4 StartY=-96.7 StartZ=0 EndX=61.9 EndY=-96.7 EndZ=0
    g57: LineSegment StartX=61.9 StartY=-96.7 StartZ=0 EndX=61.9 EndY=-95.7 EndZ=0
    g58: LineSegment StartX=62.9 StartY=-95.7 StartZ=0 EndX=67.4 EndY=-95.7 EndZ=0
    g59: LineSegment StartX=67.4 StartY=-95.7 StartZ=0 EndX=67.4 EndY=-96.7 EndZ=0
    g60: LineSegment StartX=67.4 StartY=-96.7 StartZ=0 EndX=62.9 EndY=-96.7 EndZ=0
    g61: LineSegment StartX=62.9 StartY=-96.7 StartZ=0 EndX=62.9 EndY=-95.7 EndZ=0
    g62: LineSegment StartX=82.2 StartY=-95.7 StartZ=0 EndX=77.7 EndY=-95.7 EndZ=0
    g63: LineSegment StartX=77.7 StartY=-95.7 StartZ=0 EndX=77.7 EndY=-96.7 EndZ=0
    g64: LineSegment StartX=77.7 StartY=-96.7 StartZ=0 EndX=82.2 EndY=-96.7 EndZ=0
    g65: LineSegment StartX=82.2 StartY=-96.7 StartZ=0 EndX=82.2 EndY=-95.7 EndZ=0
  constraints (162):
    c: Vertical(g0)
    c: Coincident(g1,g2)
    c: Coincident(g2,g3)
    c: Coincident(g3,g4)
    c: Coincident(g4,g1)
    c: Horizontal(g1)
    c: Horizontal(g3)
    c: Vertical(g2)
    c: Vertical(g4)
    c: Coincident(g5,g6)
    c: Coincident(g6,g7)
    c: Coincident(g7,g8)
    c: Coincident(g8,g5)
    c: Horizontal(g5)
    c: Horizontal(g7)
    c: Vertical(g6)
    c: Vertical(g8)
    c: DistanceX(g1,g1) = 4.5
    c: DistanceX(g5,g5) = 4.5
    c: DistanceY(g2,g2) = 1
    c: DistanceY(g6,g6) = 1
    c: Coincident(g9,g10)
    c: Coincident(g10,g11)
    c: Coincident(g11,g12)
    c: Coincident(g12,g9)
    c: Horizontal(g9)
    c: Horizontal(g11)
    c: Vertical(g10)
    c: Vertical(g12)
    c: Coincident(g13,g14)
    c: Coincident(g14,g15)
    c: Coincident(g15,g16)
    c: Coincident(g16,g13)
    c: Horizontal(g13)
    c: Horizontal(g15)
    c: Vertical(g14)
    c: Vertical(g16)
    c: DistanceX(g13,g13) = 4.5
    c: DistanceX(g11,g11) = 4.5
    c: DistanceY(g10,g10) = 1
    c: DistanceY(g14,g14) = 1
    c: Coincident(g17,g18)
    c: Coincident(g18,g19)
    c: Coincident(g19,g20)
    c: Coincident(g20,g17)
    c: Horizontal(g17)
    c: Horizontal(g19)
    c: Vertical(g18)
    c: Vertical(g20)
    c: Coincident(g21,g22)
    c: Coincident(g22,g23)
    c: Coincident(g23,g24)
    c: Coincident(g24,g21)
    c: Horizontal(g21)
    c: Horizontal(g23)
    c: Vertical(g22)
    c: Vertical(g24)
    c: DistanceX(g17,g17) = 4.5
    c: DistanceY(g18,g18) = 1
    c: DistanceX(g21,g21) = 4.5
    c: DistanceY(g22,g22) = 1
    c: Coincident(g25,g26)
    c: Coincident(g26,g27)
    c: Coincident(g27,g28)
    c: Coincident(g28,g25)
    c: Horizontal(g25)
    c: Horizontal(g27)
    c: Vertical(g26)
    c: Vertical(g28)
    c: Coincident(g29,g30)
    c: Coincident(g30,g31)
    c: Coincident(g31,g32)
    c: Coincident(g32,g29)
    c: Horizontal(g29)
    c: Horizontal(g31)
    c: Vertical(g30)
    c: Vertical(g32)
    c: DistanceX(g29,g29) = 4.5
    c: DistanceX(g25,g25) = 4.5
    c: DistanceY(g26,g26) = 1
    c: DistanceY(g30,g30) = 1
    c: Vertical(g33)
    c: Coincident(g34,g35)
    c: Coincident(g35,g36)
    c: Coincident(g36,g37)
    c: Coincident(g37,g34)
    c: Horizontal(g34)
    c: Horizontal(g36)
    c: Vertical(g35)
    c: Vertical(g37)
    c: Coincident(g38,g39)
    c: Coincident(g39,g40)
    c: Coincident(g40,g41)
    c: Coincident(g41,g38)
    c: Horizontal(g38)
    c: Horizontal(g40)
    c: Vertical(g39)
    c: Vertical(g41)
    c: DistanceY(g39,g39) = 1
    c: DistanceY(g35,g35) = 1
    c: DistanceX(g36,g36) = 4.5
    c: DistanceX(g38,g38) = 4.5
    c: Coincident(g42,g43)
    c: Coincident(g43,g44)
    c: Coincident(g44,g45)
    c: Coincident(g45,g42)
    c: Horizontal(g42)
    c: Horizontal(g44)
    c: Vertical(g43)
    c: Vertical(g45)
    c: Coincident(g46,g47)
    c: Coincident(g47,g48)
    c: Coincident(g48,g49)
    c: Coincident(g49,g46)
    c: Horizontal(g46)
    c: Horizontal(g48)
    c: Vertical(g47)
    c: Vertical(g49)
    c: DistanceX(g46,g46) = 4.5
    c: DistanceX(g44,g44) = 4.5
    c: DistanceY(g43,g43) = 1
    c: DistanceY(g47,g47) = 1
    c: Coincident(g50,g51)
    c: Coincident(g51,g52)
    c: Coincident(g52,g53)
    c: Coincident(g53,g50)
    c: Horizontal(g50)
    c: Horizontal(g52)
    c: Vertical(g51)
    c: Vertical(g53)
    c: DistanceY(g51,g51) = 1
    c: DistanceX(g52,g52) = 4.5
    c: Coincident(g54,g55)
    c: Coincident(g55,g56)
    c: Coincident(g56,g57)
    c: Coincident(g57,g54)
    c: Horizontal(g54)
    c: Horizontal(g56)
    c: Vertical(g55)
    c: Vertical(g57)
    c: DistanceX(g54,g54) = 4.5
    c: DistanceY(g55,g55) = 1
    c: Coincident(g58,g59)
    c: Coincident(g59,g60)
    c: Coincident(g60,g61)
    c: Coincident(g61,g58)
    c: Horizontal(g58)
    c: Horizontal(g60)
    c: Vertical(g59)
    c: Vertical(g61)
    c: DistanceY(g59,g59) = 1
    c: DistanceX(g60,g60) = 4.5
    c: Coincident(g62,g63)
    c: Coincident(g63,g64)
    c: Coincident(g64,g65)
    c: Coincident(g65,g62)
    c: Horizontal(g62)
    c: Horizontal(g64)
    c: Vertical(g63)
    c: Vertical(g65)
    c: DistanceY(g63,g63) = 1
    c: DistanceX(g62,g62) = 4.5
FEATURE [Part::Extrusion] Extrude029  label="CELL ENDS SPRING HOLDERS"
  Base = -> Sketch083
  Dir = (0,0,1)
  DirMode = 2
  FaceMakerClass = Part::FaceMakerBullseye
  LengthFwd = 9.65
  LengthRev = 0
  Solid = true
  Symmetric = false
FEATURE [Sketcher::SketchObject] Sketch084
  FullyConstrained = false
  MapMode = 5
  Support = -> [XY_Plane098]
  sketch-geometry (4):
    g0: LineSegment StartX=0 StartY=-26.49 StartZ=0 EndX=84.2 EndY=-26.49 EndZ=0
    g1: LineSegment StartX=84.2 StartY=-26.49 StartZ=0 EndX=84.2 EndY=-14.4 EndZ=0
    g2: LineSegment StartX=84.2 StartY=-14.4 StartZ=0 EndX=0 EndY=-14.4 EndZ=0
    g3: LineSegment StartX=0 StartY=-14.4 StartZ=0 EndX=0 EndY=-26.49 EndZ=0
  constraints (11):
    c: Coincident(g0,g1)
    c: Coincident(g1,g2)
    c: Coincident(g2,g3)
    c: Coincident(g3,g0)
    c: Horizontal(g0)
    c: Horizontal(g2)
    c: Vertical(g1)
    c: Vertical(g3)
    c: PointOnObject(g0,g-2)
    c: DistanceX(g2,g2) = 84.2
    c: DistanceY(g1,g1) = 12.09
FEATURE [Part::Extrusion] Extrude030  label="BACK FLOOR"
  Base = -> Sketch084
  Dir = (0,0,1)
  DirMode = 2
  FaceMakerClass = Part::FaceMakerBullseye
  LengthFwd = 2
  LengthRev = 0
  Solid = true
  Symmetric = false
FEATURE [Sketcher::SketchObject] Sketch085
  FullyConstrained = false
  MapMode = 5
  Placement = pos=(0,0,2) rot=(0,0,1;0rad)
  Support = -> [Extrude030]
  sketch-geometry (8):
    g0: LineSegment StartX=0 StartY=-26.4942 StartZ=0 EndX=84.2 EndY=-26.4942 EndZ=0
    g1: LineSegment StartX=84.2 StartY=-26.4942 StartZ=0 EndX=84.2 EndY=-14.4 EndZ=0
    g2: LineSegment StartX=84.2 StartY=-14.4 StartZ=0 EndX=0 EndY=-14.4 EndZ=0
    g3: LineSegment StartX=0 StartY=-14.4 StartZ=0 EndX=0 EndY=-26.4942 EndZ=0
    g4: LineSegment StartX=82.2 StartY=-26.4942 StartZ=0 EndX=2 EndY=-26.4942 EndZ=0
    g5: LineSegment StartX=2 StartY=-26.4942 StartZ=0 EndX=2 EndY=-16.37 EndZ=0
    g6: LineSegment StartX=2 StartY=-16.37 StartZ=0 EndX=82.2 EndY=-16.37 EndZ=0
    g7: LineSegment StartX=82.2 StartY=-16.37 StartZ=0 EndX=82.2 EndY=-26.4942 EndZ=0
  constraints (22):
    c: Coincident(g0,g1)
    c: Coincident(g1,g2)
    c: Coincident(g2,g3)
    c: Coincident(g3,g0)
    c: Horizontal(g0)
    c: Horizontal(g2)
    c: Vertical(g1)
    c: Vertical(g3)
    c: PointOnObject(g0,g-2)
    c: Coincident(g4,g5)
    c: Coincident(g5,g6)
    c: Coincident(g6,g7)
    c: Coincident(g7,g4)
    c: Horizontal(g4)
    c: Horizontal(g6)
    c: Vertical(g5)
    c: Vertical(g7)
    c: PointOnObject(g4,g0)
    c: DistanceX(g6,g6) = 80.2
    c: DistanceX(g2,g2) = 84.2
    c: DistanceY(g5,g5) = 10.1242
    c: DistanceY(g3,g3) = 12.0942
FEATURE [Part::Extrusion] Extrude005  label="Extrude062"
  Base = -> Sketch085
  Dir = (0,0,1)
  DirMode = 2
  FaceMakerClass = Part::FaceMakerBullseye
  LengthFwd = 19.3
  LengthRev = 0
  Solid = true
  Symmetric = false
FEATURE [PartDesign::FeatureBase] BaseFeature006
  BaseFeature = -> Extrude005
FEATURE [Sketcher::SketchObject] Sketch086
  FullyConstrained = false
  MapMode = 5
  Placement = pos=(0,-14.4,0) rot=(0,0.707107,0.707107;3.14159rad)
  Support = -> [BaseFeature006]
  sketch-geometry (4):
    g0: LineSegment StartX=-7 StartY=10 StartZ=0 EndX=-24.64 EndY=10 EndZ=0
    g1: LineSegment StartX=-24.64 StartY=10 StartZ=0 EndX=-24.64 EndY=14 EndZ=0
    g2: LineSegment StartX=-24.64 StartY=14 StartZ=0 EndX=-7 EndY=14 EndZ=0
    g3: LineSegment StartX=-7 StartY=14 StartZ=0 EndX=-7 EndY=10 EndZ=0
  constraints (10):
    c: Coincident(g0,g1)
    c: Coincident(g1,g2)
    c: Coincident(g2,g3)
    c: Coincident(g3,g0)
    c: Horizontal(g0)
    c: Horizontal(g2)
    c: Vertical(g1)
    c: Vertical(g3)
    c: DistanceX(g2,g2) = 17.64
    c: DistanceY(g1,g1) = 4
FEATURE [PartDesign::Pocket] Pocket017  label="BACK WALL"
  Direction = (0,-1,2e-16)
  Length = 2
  Length2 = 5
  Profile = -> Sketch086
  ReferenceAxis = -> Sketch086 [N_Axis]
  Type = 0
FEATURE [Sketcher::SketchObject] Sketch087
  FullyConstrained = false
  MapMode = 5
  Support = -> [XY_Plane102]
  sketch-geometry (4):
    g0: LineSegment StartX=-140 StartY=-110 StartZ=0 EndX=-128 EndY=-110 EndZ=0
    g1: LineSegment StartX=-128 StartY=-110 StartZ=0 EndX=-128 EndY=-117 EndZ=0
    g2: LineSegment StartX=-128 StartY=-117 StartZ=0 EndX=-140 EndY=-117 EndZ=0
    g3: LineSegment StartX=-140 StartY=-117 StartZ=0 EndX=-140 EndY=-110 EndZ=0
  constraints (10):
    c: Coincident(g0,g1)
    c: Coincident(g1,g2)
    c: Coincident(g2,g3)
    c: Coincident(g3,g0)
    c: Horizontal(g0)
    c: Horizontal(g2)
    c: Vertical(g1)
    c: Vertical(g3)
    c: DistanceX(g0,g0) = 12
    c: DistanceY(g3,g3) = 7
FEATURE [Part::Extrusion] Extrude007
  Base = -> Sketch087
  Dir = (0,0,1)
  DirMode = 2
  FaceMakerClass = Part::FaceMakerBullseye
  LengthFwd = 7
  LengthRev = 0
  Solid = true
  Symmetric = false
FEATURE [PartDesign::FeatureBase] BaseFeature007
  BaseFeature = -> Extrude007
FEATURE [Sketcher::SketchObject] Sketch012
  FullyConstrained = false
  MapMode = 5
  Placement = pos=(0,0,7) rot=(0,0,1;0rad)
  Support = -> [Extrude007]
  sketch-geometry (4):
    g0: LineSegment StartX=-139 StartY=-111 StartZ=0 EndX=-129 EndY=-111 EndZ=0
    g1: LineSegment StartX=-129 StartY=-111 StartZ=0 EndX=-129 EndY=-116 EndZ=0
    g2: LineSegment StartX=-129 StartY=-116 StartZ=0 EndX=-139 EndY=-116 EndZ=0
    g3: LineSegment StartX=-139 StartY=-116 StartZ=0 EndX=-139 EndY=-111 EndZ=0
  constraints (10):
    c: Coincident(g0,g1)
    c: Coincident(g1,g2)
    c: Coincident(g2,g3)
    c: Coincident(g3,g0)
    c: Horizontal(g0)
    c: Horizontal(g2)
    c: Vertical(g1)
    c: Vertical(g3)
    c: DistanceY(g3,g3) = 5
    c: DistanceX(g0,g0) = 10
FEATURE [Sketcher::SketchObject] Sketch088
  FullyConstrained = false
  MapMode = 5
  Placement = pos=(0,-117,0) rot=(1,0,0;1.5708rad)
  Support = -> [Extrude007]
  sketch-geometry (4):
    g0: LineSegment StartX=-135 StartY=2 StartZ=0 EndX=-133 EndY=2 EndZ=0
    g1: LineSegment StartX=-133 StartY=2 StartZ=0 EndX=-133 EndY=5 EndZ=0
    g2: LineSegment StartX=-133 StartY=5 StartZ=0 EndX=-135 EndY=5 EndZ=0
    g3: LineSegment StartX=-135 StartY=5 StartZ=0 EndX=-135 EndY=2 EndZ=0
  constraints (10):
    c: Coincident(g0,g1)
    c: Coincident(g1,g2)
    c: Coincident(g2,g3)
    c: Coincident(g3,g0)
    c: Horizontal(g0)
    c: Horizontal(g2)
    c: Vertical(g1)
    c: Vertical(g3)
    c: DistanceX(g2,g2) = 2
    c: DistanceY(g3,g3) = 3
FEATURE [PartDesign::Pocket] Pocket018
  Direction = (0,1,-2e-16)
  Length = 3.5
  Length2 = 5
  Profile = -> Sketch088
  ReferenceAxis = -> Sketch088 [N_Axis]
  Type = 0
FEATURE [PartDesign::FeatureBase] BaseFeature008
  BaseFeature = -> Pocket018
FEATURE [Sketcher::SketchObject] Sketch089
  FullyConstrained = false
  MapMode = 5
  Placement = pos=(-128,0,0) rot=(0.57735,0.57735,0.57735;2.0944rad)
  Support = -> [Pocket018]
  sketch-geometry (1):
    g0: Circle CenterX=-115.25 CenterY=3.5 CenterZ=0 NormalX=0 NormalY=0 NormalZ=1 AngleXU=0 Radius=0.75
  constraints (1):
    c: Diameter(g0) = 1.5
FEATURE [PartDesign::Hole] Hole018  label="MAIN LOCKING HANDLE MNT"
  CustomThreadClearance = 0
  Depth = 12
  DepthType = 0
  Diameter = 1.5
  DrillForDepth = false
  DrillPoint = 1
  DrillPointAngle = 118
  HoleCutCountersinkAngle = 90
  HoleCutCustomValues = false
  HoleCutDepth = 0
  HoleCutDiameter = 6.1
  HoleCutType = 0
  ModelThread = false
  Profile = -> Sketch089
  Tapered = false
  TaperedAngle = 90
  ThreadClass = 0
  ThreadDepth = 12
  ThreadDepthType = 0
  ThreadDirection = 0
  ThreadFit = 0
  ThreadSize = 0
  ThreadType = 0
  Threaded = false
  UseCustomThreadClearance = false
FEATURE [Sketcher::SketchObject] Sketch090
  FullyConstrained = false
  MapMode = 5
  Placement = pos=(0,0,0) rot=(0.57735,0.57735,0.57735;2.0944rad)
  Support = -> [YZ_Plane104]
  sketch-geometry (17):
    g0: LineSegment StartX=-128 StartY=5 StartZ=0 EndX=-130 EndY=5 EndZ=0
    g1: LineSegment StartX=-130 StartY=5 StartZ=0 EndX=-130.3 EndY=5 EndZ=0
    g2: LineSegment StartX=-130.3 StartY=5 StartZ=0 EndX=-133.3 EndY=5 EndZ=0
    g3: LineSegment StartX=-133.3 StartY=5 StartZ=0 EndX=-133.3 EndY=3 EndZ=0
    g4: LineSegment StartX=-133.3 StartY=3 StartZ=0 EndX=-131.8 EndY=3 EndZ=0
    g5: LineSegment StartX=-131.8 StartY=3 StartZ=0 EndX=-131.8 EndY=-7 EndZ=0
    g6: LineSegment StartX=-131.8 StartY=-7 StartZ=0 EndX=-133.3 EndY=-7 EndZ=0
    g7: LineSegment StartX=-133.3 StartY=-7 StartZ=0 EndX=-133.3 EndY=-9 EndZ=0
    g8: LineSegment StartX=-133.3 StartY=-9 StartZ=0 EndX=-130.3 EndY=-9 EndZ=0
    g9: LineSegment StartX=-128 StartY=5 StartZ=0 EndX=-127.7 EndY=5 EndZ=0
    g10: LineSegment StartX=-127.7 StartY=5 StartZ=0 EndX=-124.2 EndY=5 EndZ=0
    g11: LineSegment StartX=-124.2 StartY=5 StartZ=0 EndX=-124.2 EndY=2 EndZ=0
    g12: LineSegment StartX=-124.2 StartY=2 StartZ=0 EndX=-127.7 EndY=2 EndZ=0
    g13: LineSegment StartX=-127.7 StartY=2 StartZ=0 EndX=-128 EndY=2 EndZ=0
    g14: LineSegment StartX=-128 StartY=2 StartZ=0 EndX=-130 EndY=2 EndZ=0
    g15: LineSegment StartX=-130 StartY=2 StartZ=0 EndX=-130.3 EndY=2 EndZ=0
    g16: LineSegment StartX=-130.3 StartY=2 StartZ=0 EndX=-130.3 EndY=-9 EndZ=0
  constraints (49):
    c: Horizontal(g0)
    c: Coincident(g0,g1)
    c: Horizontal(g1)
    c: Coincident(g1,g2)
    c: Horizontal(g2)
    c: Coincident(g2,g3)
    c: Vertical(g3)
    c: Coincident(g3,g4)
    c: Horizontal(g4)
    c: Coincident(g4,g5)
    c: Vertical(g5)
    c: Coincident(g5,g6)
    c: Horizontal(g6)
    c: Coincident(g6,g7)
    c: Vertical(g7)
    c: Coincident(g7,g8)
    c: Horizontal(g8)
    c: DistanceY(g5,g5) = 10
    c: DistanceY(g3,g3) = 2
    c: DistanceX(g4,g4) = 1.5
    c: DistanceX(g2,g2) = 3
    c: DistanceX(g1,g1) = 0.3
    c: DistanceX(g0,g0) = 2
    c: DistanceX(g6,g6) = 1.5
    c: Coincident(g9,g0)
    c: Horizontal(g9)
    c: Coincident(g9,g10)
    c: Horizontal(g10)
    c: Coincident(g10,g11)
    c: Vertical(g11)
    c: Coincident(g11,g12)
    c: Horizontal(g12)
    c: Coincident(g12,g13)
    c: Horizontal(g13)
    c: Coincident(g13,g14)
    c: Horizontal(g14)
    c: Coincident(g15,g14)
    c: Horizontal(g15)
    c: Coincident(g15,g16)
    c: Coincident(g16,g8)
    c: Vertical(g16)
    c: DistanceY(g7,g7) = 2
    c: DistanceY(g16,g16) = 11
    c: DistanceX(g8,g8) = 3
    c: DistanceX(g15,g15) = 0.3
    c: DistanceX(g14,g14) = 2
    c: DistanceX(g13,g13) = 0.3
    c: DistanceX(g12,g12) = 3.5
    c: DistanceX(g10,g10) = 3.5
FEATURE [Part::Extrusion] Extrude041  label="Extrude071"
  Base = -> Sketch090
  Dir = (1,-1e-16,1e-16)
  DirMode = 2
  FaceMakerClass = Part::FaceMakerBullseye
  LengthFwd = 2
  LengthRev = 0
  Solid = true
  Symmetric = false
FEATURE [Sketcher::SketchObject] Sketch091
  FullyConstrained = false
  MapMode = 5
  Placement = pos=(0,0,0) rot=(0.57735,0.57735,0.57735;2.0944rad)
  Support = -> [YZ_Plane106]
  sketch-geometry (1):
    g0: Circle CenterX=-160 CenterY=10 CenterZ=0 NormalX=0 NormalY=0 NormalZ=1 AngleXU=0 Radius=1.5
  constraints (1):
    c: Diameter(g0) = 3
FEATURE [Part::Extrusion] Extrude011  label="PIN BASE"
  Base = -> Sketch091
  Dir = (1,-1e-16,1e-16)
  DirMode = 2
  FaceMakerClass = Part::FaceMakerBullseye
  LengthFwd = 1.5
  LengthRev = 0
  Solid = true
  Symmetric = false
FEATURE [Sketcher::SketchObject] Sketch092
  FullyConstrained = false
  MapMode = 5
  Placement = pos=(1.5,-3e-16,3e-16) rot=(0.57735,0.57735,0.57735;2.0944rad)
  Support = -> [Extrude011]
  sketch-geometry (1):
    g0: Circle CenterX=-160 CenterY=10 CenterZ=0 NormalX=0 NormalY=0 NormalZ=1 AngleXU=0 Radius=0.74
  constraints (1):
    c: Diameter(g0) = 1.48
FEATURE [Part::Extrusion] Extrude012  label="PIN LENGTH"
  Base = -> Sketch092
  Dir = (1,-2e-16,2e-16)
  DirMode = 2
  FaceMakerClass = Part::FaceMakerBullseye
  LengthFwd = 13.5
  LengthRev = 0
  Solid = true
  Symmetric = false
FEATURE [App::Part] Part025  label="handle to mechanism pin"
  Group = -> [Body011,Sketch091,Extrude011,Sketch092,Extrude012]
  Origin = -> Origin105
  Placement = pos=(34.67,54.77,7.74) rot=(0,0,1;0rad)
FEATURE [Sketcher::SketchObject] Sketch093
  FullyConstrained = false
  MapMode = 5
  Support = -> [XY_Plane107]
  sketch-geometry (4):
    g0: LineSegment StartX=0 StartY=-99.794 StartZ=0 EndX=84.2 EndY=-99.794 EndZ=0
    g1: LineSegment StartX=84.2 StartY=-99.794 StartZ=0 EndX=84.2 EndY=-109.304 EndZ=0
    g2: LineSegment StartX=84.2 StartY=-109.304 StartZ=0 EndX=0 EndY=-109.304 EndZ=0
    g3: LineSegment StartX=0 StartY=-109.304 StartZ=0 EndX=0 EndY=-99.794 EndZ=0
  constraints (11):
    c: Coincident(g0,g1)
    c: Coincident(g1,g2)
    c: Coincident(g2,g3)
    c: Coincident(g3,g0)
    c: Horizontal(g0)
    c: Horizontal(g2)
    c: Vertical(g1)
    c: Vertical(g3)
    c: PointOnObject(g0,g-2)
    c: DistanceX(g2,g2) = 84.2
    c: DistanceY(g1,g1) = 9.51
FEATURE [Part::Extrusion] Extrude031  label="Extrude063"
  Base = -> Sketch093
  Dir = (0,0,1)
  DirMode = 2
  FaceMakerClass = Part::FaceMakerBullseye
  LengthFwd = 2
  LengthRev = 0
  Solid = true
  Symmetric = false
FEATURE [PartDesign::FeatureBase] BaseFeature009  label="FRONT FLOOR"
  BaseFeature = -> Extrude031
FEATURE [Sketcher::SketchObject] Sketch094
  FullyConstrained = false
  MapMode = 5
  Placement = pos=(0,0,2) rot=(0,0,1;0rad)
  Support = -> [Extrude031]
  sketch-geometry (8):
    g0: LineSegment StartX=0 StartY=-99.8 StartZ=0 EndX=0 EndY=-109.3 EndZ=0
    g1: LineSegment StartX=0 StartY=-109.3 StartZ=0 EndX=84.2 EndY=-109.3 EndZ=0
    g2: LineSegment StartX=84.2 StartY=-109.3 StartZ=0 EndX=84.2 EndY=-99.79 EndZ=0
    g3: LineSegment StartX=84.2 StartY=-99.79 StartZ=0 EndX=82.2 EndY=-99.79 EndZ=0
    g4: LineSegment StartX=82.2 StartY=-99.79 StartZ=0 EndX=82.2 EndY=-107.3 EndZ=0
    g5: LineSegment StartX=82.2 StartY=-107.3 StartZ=0 EndX=2 EndY=-107.3 EndZ=0
    g6: LineSegment StartX=2 StartY=-107.3 StartZ=0 EndX=2 EndY=-99.8 EndZ=0
    g7: LineSegment StartX=2 StartY=-99.8 StartZ=0 EndX=0 EndY=-99.8 EndZ=0
  constraints (23):
    c: PointOnObject(g0,g-2)
    c: PointOnObject(g0,g-2)
    c: Coincident(g0,g1)
    c: Horizontal(g1)
    c: Coincident(g1,g2)
    c: Vertical(g2)
    c: Coincident(g2,g3)
    c: Horizontal(g3)
    c: Coincident(g3,g4)
    c: Vertical(g4)
    c: Coincident(g4,g5)
    c: Horizontal(g5)
    c: Coincident(g5,g6)
    c: Vertical(g6)
    c: Coincident(g6,g7)
    c: Coincident(g7,g0)
    c: Horizontal(g7)
    c: DistanceX(g7,g7) = 2
    c: DistanceX(g1,g1) = 84.2
    c: DistanceX(g5,g5) = 80.2
    c: DistanceY(g2,g2) = 9.51
    c: DistanceY(g4,g4) = 7.51
    c: DistanceY(g6,g6) = 7.5
FEATURE [Part::Extrusion] Extrude032  label="FRONT WALL"
  Base = -> Sketch094
  Dir = (0,0,1)
  DirMode = 2
  FaceMakerClass = Part::FaceMakerBullseye
  LengthFwd = 19.3
  LengthRev = 0
  Solid = true
  Symmetric = false
FEATURE [PartDesign::FeatureBase] BaseFeature011
  BaseFeature = -> Extrude032
FEATURE [Sketcher::SketchObject] Sketch095
  FullyConstrained = false
  MapMode = 5
  Placement = pos=(0,0,2) rot=(0,0,1;0rad)
  Support = -> [BaseFeature009]
  sketch-geometry (4):
    g0: LineSegment StartX=2 StartY=-107.3 StartZ=0 EndX=8 EndY=-107.3 EndZ=0
    g1: LineSegment StartX=8 StartY=-107.3 StartZ=0 EndX=8 EndY=-101.3 EndZ=0
    g2: LineSegment StartX=8 StartY=-101.3 StartZ=0 EndX=2 EndY=-101.3 EndZ=0
    g3: LineSegment StartX=2 StartY=-101.3 StartZ=0 EndX=2 EndY=-107.3 EndZ=0
  constraints (10):
    c: Coincident(g0,g1)
    c: Coincident(g1,g2)
    c: Coincident(g2,g3)
    c: Coincident(g3,g0)
    c: Horizontal(g0)
    c: Horizontal(g2)
    c: Vertical(g1)
    c: Vertical(g3)
    c: DistanceX(g2,g2) = 6
    c: DistanceY(g1,g1) = 6
FEATURE [Part::Extrusion] Extrude033  label="Extrude064"
  Base = -> Sketch095
  Dir = (0,0,1)
  DirMode = 2
  FaceMakerClass = Part::FaceMakerBullseye
  LengthFwd = 19.3
  LengthRev = 0
  Solid = true
  Symmetric = false
FEATURE [Sketcher::SketchObject] Sketch096
  FullyConstrained = false
  MapMode = 5
  Placement = pos=(0,0,21.3) rot=(0,0,1;0rad)
  Support = -> [Extrude033]
  sketch-geometry (1):
    g0: Circle CenterX=5 CenterY=-104.3 CenterZ=0 NormalX=0 NormalY=0 NormalZ=1 AngleXU=0 Radius=1.55
  constraints (1):
    c: Diameter(g0) = 3.1
FEATURE [PartDesign::Hole] Hole019  label="FRONT LEFT INSERT MNT"
  CustomThreadClearance = 0
  Depth = 2.5
  DepthType = 0
  Diameter = 3.2
  DrillForDepth = false
  DrillPoint = 1
  DrillPointAngle = 118
  HoleCutCountersinkAngle = 90
  HoleCutCustomValues = false
  HoleCutDepth = 0
  HoleCutDiameter = 6.1
  HoleCutType = 0
  ModelThread = false
  Profile = -> Sketch096
  Tapered = false
  TaperedAngle = 90
  ThreadClass = 0
  ThreadDepth = 2.5
  ThreadDepthType = 0
  ThreadDirection = 0
  ThreadFit = 0
  ThreadSize = 0
  ThreadType = 0
  Threaded = false
  UseCustomThreadClearance = false
FEATURE [Sketcher::SketchObject] Sketch097
  FullyConstrained = false
  MapMode = 5
  Placement = pos=(0,0,2) rot=(0,0,1;0rad)
  Support = -> [BaseFeature009]
  sketch-geometry (4):
    g0: LineSegment StartX=82.2 StartY=-107.3 StartZ=0 EndX=76.2 EndY=-107.3 EndZ=0
    g1: LineSegment StartX=76.2 StartY=-107.3 StartZ=0 EndX=76.2 EndY=-101.3 EndZ=0
    g2: LineSegment StartX=76.2 StartY=-101.3 StartZ=0 EndX=82.2 EndY=-101.3 EndZ=0
    g3: LineSegment StartX=82.2 StartY=-101.3 StartZ=0 EndX=82.2 EndY=-107.3 EndZ=0
  constraints (9):
    c: Coincident(g0,g1)
    c: Coincident(g1,g2)
    c: Coincident(g2,g3)
    c: Coincident(g3,g0)
    c: Horizontal(g0)
    c: Horizontal(g2)
    c: Vertical(g1)
    c: Vertical(g3)
    c: DistanceY(g1,g1) = 6
FEATURE [Part::Extrusion] Extrude034  label="Extrude065"
  Base = -> Sketch097
  Dir = (0,0,1)
  DirMode = 2
  FaceMakerClass = Part::FaceMakerBullseye
  LengthFwd = 19.3
  LengthRev = 0
  Solid = true
  Symmetric = false
FEATURE [Sketcher::SketchObject] Sketch098
  FullyConstrained = false
  MapMode = 5
  Placement = pos=(0,0,21.3) rot=(0,0,1;0rad)
  Support = -> [Extrude034]
  sketch-geometry (1):
    g0: Circle CenterX=79.2 CenterY=-104.3 CenterZ=0 NormalX=0 NormalY=0 NormalZ=1 AngleXU=0 Radius=1.6
  constraints (1):
    c: Diameter(g0) = 3.2
FEATURE [PartDesign::Hole] Hole020  label="FRONT RIGHT INSERT MNT"
  CustomThreadClearance = 0
  Depth = 2.3
  DepthType = 0
  Diameter = 3.2
  DrillForDepth = false
  DrillPoint = 1
  DrillPointAngle = 118
  HoleCutCountersinkAngle = 90
  HoleCutCustomValues = false
  HoleCutDepth = 0
  HoleCutDiameter = 6.1
  HoleCutType = 0
  ModelThread = false
  Profile = -> Sketch098
  Tapered = false
  TaperedAngle = 90
  ThreadClass = 0
  ThreadDepth = 2.3
  ThreadDepthType = 0
  ThreadDirection = 0
  ThreadFit = 0
  ThreadSize = 0
  ThreadType = 0
  Threaded = false
  UseCustomThreadClearance = false
FEATURE [Sketcher::SketchObject] Sketch099
  FullyConstrained = false
  MapMode = 5
  Placement = pos=(0,-16.37,0) rot=(1,0,0;1.5708rad)
  Support = -> [Pocket017]
  sketch-geometry (4):
    g0: LineSegment StartX=2 StartY=21.3 StartZ=0 EndX=7 EndY=21.3 EndZ=0
    g1: LineSegment StartX=7 StartY=21.3 StartZ=0 EndX=7 EndY=16.3 EndZ=0
    g2: LineSegment StartX=7 StartY=16.3 StartZ=0 EndX=2 EndY=16.3 EndZ=0
    g3: LineSegment StartX=2 StartY=16.3 StartZ=0 EndX=2 EndY=21.3 EndZ=0
  constraints (10):
    c: Coincident(g0,g1)
    c: Coincident(g1,g2)
    c: Coincident(g2,g3)
    c: Coincident(g3,g0)
    c: Horizontal(g0)
    c: Horizontal(g2)
    c: Vertical(g1)
    c: Vertical(g3)
    c: DistanceY(g1,g1) = 5
    c: DistanceX(g0,g0) = 5
FEATURE [Part::Extrusion] Extrude035  label="Extrude066"
  Base = -> Sketch099
  Dir = (0,-1,2e-16)
  DirMode = 2
  FaceMakerClass = Part::FaceMakerBullseye
  LengthFwd = 5
  LengthRev = 0
  Solid = true
  Symmetric = false
FEATURE [Sketcher::SketchObject] Sketch100
  FullyConstrained = false
  MapMode = 5
  Placement = pos=(0,4.7e-15,21.3) rot=(0,0,1;0rad)
  Support = -> [Extrude035]
  sketch-geometry (1):
    g0: Circle CenterX=4 CenterY=-18.4 CenterZ=0 NormalX=0 NormalY=0 NormalZ=1 AngleXU=0 Radius=1.6
  constraints (1):
    c: Diameter(g0) = 3.2
FEATURE [PartDesign::Hole] Hole021  label="BACK LEFT INSERT MNT"
  CustomThreadClearance = 0
  Depth = 2.2
  DepthType = 0
  Diameter = 3.2
  DrillForDepth = false
  DrillPoint = 1
  DrillPointAngle = 118
  HoleCutCountersinkAngle = 90
  HoleCutCustomValues = false
  HoleCutDepth = 0
  HoleCutDiameter = 6.1
  HoleCutType = 0
  ModelThread = false
  Profile = -> Sketch100
  Tapered = false
  TaperedAngle = 90
  ThreadClass = 0
  ThreadDepth = 2.2
  ThreadDepthType = 0
  ThreadDirection = 0
  ThreadFit = 0
  ThreadSize = 0
  ThreadType = 0
  Threaded = false
  UseCustomThreadClearance = false
FEATURE [Sketcher::SketchObject] Sketch101
  FullyConstrained = false
  MapMode = 5
  Placement = pos=(0,-16.37,0) rot=(1,0,0;1.5708rad)
  Support = -> [Pocket017]
  sketch-geometry (4):
    g0: LineSegment StartX=82.2 StartY=21.3 StartZ=0 EndX=77.2 EndY=21.3 EndZ=0
    g1: LineSegment StartX=77.2 StartY=21.3 StartZ=0 EndX=77.2 EndY=16.3 EndZ=0
    g2: LineSegment StartX=77.2 StartY=16.3 StartZ=0 EndX=82.2 EndY=16.3 EndZ=0
    g3: LineSegment StartX=82.2 StartY=16.3 StartZ=0 EndX=82.2 EndY=21.3 EndZ=0
  constraints (10):
    c: Coincident(g0,g1)
    c: Coincident(g1,g2)
    c: Coincident(g2,g3)
    c: Coincident(g3,g0)
    c: Horizontal(g0)
    c: Horizontal(g2)
    c: Vertical(g1)
    c: Vertical(g3)
    c: DistanceX(g0,g0) = 5
    c: DistanceY(g3,g3) = 5
FEATURE [Part::Extrusion] Extrude036  label="Extrude067"
  Base = -> Sketch101
  Dir = (0,-1,2e-16)
  DirMode = 2
  FaceMakerClass = Part::FaceMakerBullseye
  LengthFwd = 5
  LengthRev = 0
  Solid = true
  Symmetric = false
FEATURE [Sketcher::SketchObject] Sketch102
  FullyConstrained = false
  MapMode = 5
  Placement = pos=(0,4.7e-15,21.3) rot=(0,0,1;0rad)
  Support = -> [Extrude036]
  sketch-geometry (1):
    g0: Circle CenterX=80 CenterY=-18.4 CenterZ=0 NormalX=0 NormalY=0 NormalZ=1 AngleXU=0 Radius=1.6
  constraints (1):
    c: Diameter(g0) = 3.2
FEATURE [PartDesign::Hole] Hole022  label="BACK RIGHT INSERT MNT"
  CustomThreadClearance = 0
  Depth = 2.3
  DepthType = 0
  Diameter = 3.2
  DrillForDepth = false
  DrillPoint = 1
  DrillPointAngle = 118
  HoleCutCountersinkAngle = 90
  HoleCutCustomValues = false
  HoleCutDepth = 0
  HoleCutDiameter = 6.1
  HoleCutType = 0
  ModelThread = false
  Profile = -> Sketch102
  Tapered = false
  TaperedAngle = 90
  ThreadClass = 0
  ThreadDepth = 2.3
  ThreadDepthType = 0
  ThreadDirection = 0
  ThreadFit = 0
  ThreadSize = 0
  ThreadType = 0
  Threaded = false
  UseCustomThreadClearance = false
FEATURE [Sketcher::SketchObject] Sketch103
  FullyConstrained = false
  MapMode = 5
  Support = -> [XY_Plane109]
  sketch-geometry (4):
    g0: LineSegment StartX=0 StartY=-14.3705 StartZ=0 EndX=84.2 EndY=-14.3705 EndZ=0
    g1: LineSegment StartX=84.2 StartY=-14.3705 StartZ=0 EndX=84.2 EndY=-109.301 EndZ=0
    g2: LineSegment StartX=84.2 StartY=-109.301 StartZ=0 EndX=0 EndY=-109.301 EndZ=0
    g3: LineSegment StartX=0 StartY=-109.301 StartZ=0 EndX=0 EndY=-14.3705 EndZ=0
  constraints (11):
    c: Coincident(g0,g1)
    c: Coincident(g1,g2)
    c: Coincident(g2,g3)
    c: Coincident(g3,g0)
    c: Horizontal(g0)
    c: Horizontal(g2)
    c: Vertical(g1)
    c: Vertical(g3)
    c: PointOnObject(g0,g-2)
    c: DistanceX(g2,g2) = 84.2
    c: DistanceY(g1,g1) = 94.93
FEATURE [Part::Extrusion] Extrude037  label="Extrude068"
  Base = -> Sketch103
  Dir = (0,0,1)
  DirMode = 2
  FaceMakerClass = Part::FaceMakerBullseye
  LengthFwd = 1.5
  LengthRev = 0
  Solid = true
  Symmetric = false
FEATURE [Sketcher::SketchObject] Sketch104
  FullyConstrained = false
  MapMode = 5
  Placement = pos=(0,0,1.5) rot=(0,0,1;0rad)
  Support = -> [Extrude037]
  sketch-geometry (4):
    g0: Circle CenterX=4 CenterY=-18.3995 CenterZ=0 NormalX=0 NormalY=0 NormalZ=1 AngleXU=0 Radius=1.6
    g1: Circle CenterX=80 CenterY=-18.4 CenterZ=0 NormalX=0 NormalY=0 NormalZ=1 AngleXU=0 Radius=1.6
    g2: Circle CenterX=79.2 CenterY=-104.3 CenterZ=0 NormalX=0 NormalY=0 NormalZ=1 AngleXU=0 Radius=1.6
    g3: Circle CenterX=5 CenterY=-104.3 CenterZ=0 NormalX=0 NormalY=0 NormalZ=1 AngleXU=0 Radius=1.6
  constraints (4):
    c: Diameter(g0) = 3.2
    c: Diameter(g1) = 3.2
    c: Diameter(g2) = 3.2
    c: Diameter(g3) = 3.2
FEATURE [PartDesign::Hole] Hole023  label="TOP PLATE WITH COUNTERSUNK HOLES"
  CustomThreadClearance = 0
  Depth = 2
  DepthType = 0
  Diameter = 2
  DrillForDepth = false
  DrillPoint = 0
  DrillPointAngle = 118
  HoleCutCountersinkAngle = 90
  HoleCutCustomValues = false
  HoleCutDepth = 2
  HoleCutDiameter = 3.8
  HoleCutType = 2
  ModelThread = false
  Profile = -> Sketch104
  Tapered = false
  TaperedAngle = 90
  ThreadClass = 0
  ThreadDepth = 2
  ThreadDepthType = 0
  ThreadDirection = 0
  ThreadFit = 0
  ThreadSize = 0
  ThreadType = 0
  Threaded = false
  UseCustomThreadClearance = false
FEATURE [Sketcher::SketchObject] Sketch105
  FullyConstrained = false
  MapMode = 5
  Placement = pos=(0,0,2) rot=(0,0,1;0rad)
  Support = -> [BaseFeature009]
  sketch-geometry (7):
    g0: LineSegment StartX=2 StartY=-99.8 StartZ=0 EndX=82.2 EndY=-99.8 EndZ=0
    g1: LineSegment StartX=2 StartY=-99.9 StartZ=0 EndX=42.1 EndY=-99.9 EndZ=0
    g2: LineSegment StartX=42.1 StartY=-100 StartZ=0 EndX=37.85 EndY=-100 EndZ=0
    g3: LineSegment StartX=37.85 StartY=-99.7927 StartZ=0 EndX=46.4 EndY=-99.7927 EndZ=0
    g4: LineSegment StartX=46.4 StartY=-99.7927 StartZ=0 EndX=46.4 EndY=-107.303 EndZ=0
    g5: LineSegment StartX=46.4 StartY=-107.303 StartZ=0 EndX=37.85 EndY=-107.303 EndZ=0
    g6: LineSegment StartX=37.85 StartY=-107.303 StartZ=0 EndX=37.85 EndY=-99.7927 EndZ=0
  constraints (15):
    c: Horizontal(g0)
    c: DistanceX(g0,g0) = 80.2
    c: Horizontal(g1)
    c: DistanceX(g1,g1) = 40.1
    c: Horizontal(g2)
    c: Coincident(g3,g4)
    c: Coincident(g4,g5)
    c: Coincident(g5,g6)
    c: Coincident(g6,g3)
    c: Horizontal(g3)
    c: Horizontal(g5)
    c: Vertical(g4)
    c: Vertical(g6)
    c: DistanceY(g4,g4) = 7.51
    c: DistanceX(g3,g3) = 8.55
FEATURE [Part::Extrusion] Extrude038  label="Extrude069"
  Base = -> Sketch105
  Dir = (0,0,1)
  DirMode = 2
  FaceMakerClass = Part::FaceMakerBullseye
  LengthFwd = 5.5
  LengthRev = 0
  Solid = true
  Symmetric = false
FEATURE [Sketcher::SketchObject] Sketch106
  FullyConstrained = false
  MapMode = 5
  Placement = pos=(0,0,7.5) rot=(0,0,1;0rad)
  Support = -> [Extrude038]
  sketch-geometry (1):
    g0: Circle CenterX=42.15 CenterY=-103.5 CenterZ=0 NormalX=0 NormalY=0 NormalZ=1 AngleXU=0 Radius=2.25
  constraints (1):
    c: Diameter(g0) = 4.5
FEATURE [PartDesign::Hole] Hole024  label="FRONT LOCK SLOT"
  CustomThreadClearance = 0
  Depth = 5.5
  DepthType = 0
  Diameter = 4.5
  DrillForDepth = false
  DrillPoint = 0
  DrillPointAngle = 118
  HoleCutCountersinkAngle = 90
  HoleCutCustomValues = false
  HoleCutDepth = 0
  HoleCutDiameter = 6.1
  HoleCutType = 0
  ModelThread = false
  Profile = -> Sketch106
  Tapered = false
  TaperedAngle = 90
  ThreadClass = 0
  ThreadDepth = 5.5
  ThreadDepthType = 0
  ThreadDirection = 0
  ThreadFit = 0
  ThreadSize = 0
  ThreadType = 0
  Threaded = false
  UseCustomThreadClearance = false
FEATURE [Sketcher::SketchObject] Sketch107
  FullyConstrained = false
  MapMode = 5
  Placement = pos=(0,0,0) rot=(1,0,0;3.14159rad)
  Support = -> [Hole018]
  sketch-geometry (1):
    g0: Circle CenterX=-134 CenterY=113.5 CenterZ=0 NormalX=0 NormalY=0 NormalZ=1 AngleXU=0 Radius=2.125
  constraints (1):
    c: Diameter(g0) = 4.25
FEATURE [Part::Extrusion] Extrude039  label="SPRING CYLINDER"
  Base = -> Sketch107
  Dir = (0,0,-1)
  DirMode = 2
  FaceMakerClass = Part::FaceMakerBullseye
  LengthFwd = 9
  LengthRev = 0
  Solid = true
  Symmetric = false
FEATURE [Sketcher::SketchObject] Sketch108
  FullyConstrained = false
  MapMode = 5
  Placement = pos=(0,0,1.5) rot=(0,0,1;0rad)
  Support = -> [Hole023]
  sketch-geometry (4):
    g0: LineSegment StartX=36.86 StartY=-100.71 StartZ=0 EndX=47.46 EndY=-100.71 EndZ=0
    g1: LineSegment StartX=47.46 StartY=-100.71 StartZ=0 EndX=47.46 EndY=-106.31 EndZ=0
    g2: LineSegment StartX=47.46 StartY=-106.31 StartZ=0 EndX=36.86 EndY=-106.31 EndZ=0
    g3: LineSegment StartX=36.86 StartY=-106.31 StartZ=0 EndX=36.86 EndY=-100.71 EndZ=0
  constraints (10):
    c: Coincident(g0,g1)
    c: Coincident(g1,g2)
    c: Coincident(g2,g3)
    c: Coincident(g3,g0)
    c: Horizontal(g0)
    c: Horizontal(g2)
    c: Vertical(g1)
    c: Vertical(g3)
    c: DistanceX(g0,g0) = 10.6
    c: DistanceY(g3,g3) = 5.6
FEATURE [PartDesign::Pocket] Pocket020  label="TOP PLATE WITH LOCK POCKET"
  BaseFeature = -> Hole023
  Direction = (0,0,-1)
  Length = 1.5
  Length2 = 5
  Profile = -> Sketch108
  ReferenceAxis = -> Sketch108 [N_Axis]
  Type = 0
FEATURE [PartDesign::Body] Body013  label="TOP PLATE BODY"
  Group = -> [Sketch104,Hole023,Sketch108,Pocket020]
  Origin = -> Origin109
  Tip = -> Pocket020
FEATURE [App::Part] Part026  label="top plate"
  Group = -> [Body013,Sketch103,Extrude037]
  Origin = -> Origin108
  Placement = pos=(0,0,21.28) rot=(0,0,1;0rad)
FEATURE [Sketcher::SketchObject] Sketch109
  FullyConstrained = false
  MapMode = 5
  Placement = pos=(0,0,7) rot=(0,0,1;0rad)
  Support = -> [Hole018]
  sketch-geometry (4):
    g0: LineSegment StartX=-139 StartY=-111 StartZ=0 EndX=-129 EndY=-111 EndZ=0
    g1: LineSegment StartX=-129 StartY=-111 StartZ=0 EndX=-129 EndY=-116 EndZ=0
    g2: LineSegment StartX=-129 StartY=-116 StartZ=0 EndX=-139 EndY=-116 EndZ=0
    g3: LineSegment StartX=-139 StartY=-116 StartZ=0 EndX=-139 EndY=-111 EndZ=0
  constraints (10):
    c: Coincident(g0,g1)
    c: Coincident(g1,g2)
    c: Coincident(g2,g3)
    c: Coincident(g3,g0)
    c: Horizontal(g0)
    c: Horizontal(g2)
    c: Vertical(g1)
    c: Vertical(g3)
    c: DistanceY(g1,g1) = 5
    c: DistanceX(g0,g0) = 10
FEATURE [Part::Extrusion] Extrude040  label="Extrude070"
  Base = -> Sketch109
  Dir = (0,0,1)
  DirMode = 2
  FaceMakerClass = Part::FaceMakerBullseye
  LengthFwd = 4.5
  LengthRev = 0
  Solid = true
  Symmetric = false
FEATURE [PartDesign::FeatureBase] BaseFeature010
  BaseFeature = -> Extrude040
FEATURE [Sketcher::SketchObject] Sketch110
  FullyConstrained = false
  MapMode = 5
  Placement = pos=(-129,0,0) rot=(0.57735,0.57735,0.57735;2.0944rad)
  Support = -> [Extrude040]
  sketch-geometry (3):
    g0: LineSegment StartX=-110.99 StartY=8.49 StartZ=0 EndX=-116 EndY=11.5 EndZ=0
    g1: LineSegment StartX=-116 StartY=11.5 StartZ=0 EndX=-110.99 EndY=11.5 EndZ=0
    g2: LineSegment StartX=-110.99 StartY=11.5 StartZ=0 EndX=-110.99 EndY=8.49 EndZ=0
  constraints (7):
    c: Coincident(g0,g1)
    c: Horizontal(g1)
    c: Coincident(g1,g2)
    c: Coincident(g2,g0)
    c: Vertical(g2)
    c: DistanceY(g2,g2) = 3.01
    c: DistanceX(g1,g1) = 5.01
FEATURE [PartDesign::Pocket] Pocket019  label="LOCK SLIDE HOOK"
  Direction = (-1,0,0)
  Length = 10
  Length2 = 5
  Profile = -> Sketch110
  ReferenceAxis = -> Sketch110 [N_Axis]
  Type = 0
FEATURE [Sketcher::SketchObject] Sketch111
  FullyConstrained = false
  MapMode = 5
  Support = -> [XY_Plane102]
  sketch-geometry (6):
    g0: LineSegment StartX=-145 StartY=-119.61 StartZ=0 EndX=-145 EndY=-110 EndZ=0
    g1: LineSegment StartX=-123 StartY=-119.61 StartZ=0 EndX=-123 EndY=-110 EndZ=0
    g2: LineSegment StartX=-147 StartY=-110 StartZ=0 EndX=-121 EndY=-110 EndZ=0
    g3: LineSegment StartX=-121 StartY=-110 StartZ=0 EndX=-121 EndY=-117 EndZ=0
    g4: LineSegment StartX=-121 StartY=-117 StartZ=0 EndX=-147 EndY=-117 EndZ=0
    g5: LineSegment StartX=-147 StartY=-117 StartZ=0 EndX=-147 EndY=-110 EndZ=0
  constraints (12):
    c: Vertical(g0)
    c: Vertical(g1)
    c: Coincident(g2,g3)
    c: Coincident(g3,g4)
    c: Coincident(g4,g5)
    c: Coincident(g5,g2)
    c: Horizontal(g2)
    c: Horizontal(g4)
    c: Vertical(g3)
    c: Vertical(g5)
    c: DistanceY(g5,g5) = 7
    c: DistanceX(g2,g2) = 26
FEATURE [Part::Extrusion] Extrude047  label="Extrude076"
  Base = -> Sketch111
  Dir = (0,0,1)
  DirMode = 2
  FaceMakerClass = Part::FaceMakerBullseye
  LengthFwd = 7
  LengthRev = 0
  Solid = true
  Symmetric = false
FEATURE [PartDesign::FeatureBase] BaseFeature016
  BaseFeature = -> Extrude047
FEATURE [Sketcher::SketchObject] Sketch112
  FullyConstrained = false
  MapMode = 5
  Placement = pos=(0,-109.3,0) rot=(1,0,0;1.5708rad)
  Support = -> [Extrude032]
  sketch-geometry (4):
    g0: LineSegment StartX=40.86 StartY=19.75 StartZ=0 EndX=43.5 EndY=19.75 EndZ=0
    g1: LineSegment StartX=43.5 StartY=19.75 StartZ=0 EndX=43.5 EndY=12.6 EndZ=0
    g2: LineSegment StartX=43.5 StartY=12.6 StartZ=0 EndX=40.86 EndY=12.6 EndZ=0
    g3: LineSegment StartX=40.86 StartY=12.6 StartZ=0 EndX=40.86 EndY=19.75 EndZ=0
  constraints (10):
    c: Coincident(g0,g1)
    c: Coincident(g1,g2)
    c: Coincident(g2,g3)
    c: Coincident(g3,g0)
    c: Horizontal(g0)
    c: Horizontal(g2)
    c: Vertical(g1)
    c: Vertical(g3)
    c: DistanceX(g0,g0) = 2.64
    c: DistanceY(g3,g3) = 7.15
FEATURE [PartDesign::Pocket] Pocket021  label="FRONT WALL WITH HANDLE SLOT"
  BaseFeature = -> BaseFeature011
  Direction = (0,1,-2e-16)
  Length = 2
  Length2 = 5
  Profile = -> Sketch112
  ReferenceAxis = -> Sketch112 [N_Axis]
  Type = 0
FEATURE [Sketcher::SketchObject] Sketch113
  FullyConstrained = false
  MapMode = 5
  Placement = pos=(2,-4e-16,4e-16) rot=(0.57735,0.57735,0.57735;2.0944rad)
  Support = -> [Extrude041]
  sketch-geometry (1):
    g0: Circle CenterX=-125.95 CenterY=3.5 CenterZ=0 NormalX=0 NormalY=0 NormalZ=1 AngleXU=0 Radius=0.75
  constraints (1):
    c: Diameter(g0) = 1.5
FEATURE [PartDesign::Hole] Hole025  label="BASE HANDLE INSERT"
  CustomThreadClearance = 0
  Depth = 2
  DepthType = 0
  Diameter = 1.5
  DrillForDepth = false
  DrillPoint = 1
  DrillPointAngle = 118
  HoleCutCountersinkAngle = 90
  HoleCutCustomValues = false
  HoleCutDepth = 0
  HoleCutDiameter = 6.1
  HoleCutType = 0
  ModelThread = false
  Profile = -> Sketch113
  Tapered = false
  TaperedAngle = 90
  ThreadClass = 0
  ThreadDepth = 2
  ThreadDepthType = 0
  ThreadDirection = 0
  ThreadFit = 0
  ThreadSize = 0
  ThreadType = 0
  Threaded = false
  UseCustomThreadClearance = false
FEATURE [Sketcher::SketchObject] Sketch114
  FullyConstrained = false
  MapMode = 5
  Placement = pos=(0,-28.49,0) rot=(1,0,0;1.5708rad)
  Support = -> [Extrude027]
  sketch-geometry (8):
    g0: ArcOfCircle CenterX=11.5 CenterY=21.374 CenterZ=0 NormalX=0 NormalY=0 NormalZ=1 AngleXU=0 Radius=7.50005 StartAngle=3.13813 EndAngle=6.28665
    g1: LineSegment StartX=4 StartY=21.4 StartZ=0 EndX=19 EndY=21.4 EndZ=0
    g2: ArcOfCircle CenterX=32 CenterY=21.3845 CenterZ=0 NormalX=0 NormalY=0 NormalZ=1 AngleXU=0 Radius=8.00001 StartAngle=3.13966 EndAngle=6.28512
    g3: LineSegment StartX=24 StartY=21.4 StartZ=0 EndX=40 EndY=21.4 EndZ=0
    g4: ArcOfCircle CenterX=52.2 CenterY=21.3636 CenterZ=0 NormalX=0 NormalY=0 NormalZ=1 AngleXU=0 Radius=7.80009 StartAngle=3.13692 EndAngle=6.28785
    g5: LineSegment StartX=60 StartY=21.4 StartZ=0 EndX=44.4 EndY=21.4 EndZ=0
    g6: ArcOfCircle CenterX=72.5 CenterY=21.2875 CenterZ=0 NormalX=0 NormalY=0 NormalZ=1 AngleXU=0 Radius=7.50084 StartAngle=3.12659 EndAngle=6.29819
    g7: LineSegment StartX=80 StartY=21.4 StartZ=0 EndX=65 EndY=21.4 EndZ=0
  constraints (19):
    c: Coincident(g1,g0)
    c: Coincident(g1,g0)
    c: Horizontal(g1)
    c: DistanceX(g1,g1) = 15
    c: Diameter(g0) = 15.0001
    c: Coincident(g3,g2)
    c: Coincident(g3,g2)
    c: Horizontal(g3)
    c: DistanceX(g3,g3) = 16
    c: Diameter(g2) = 16
    c: Coincident(g5,g4)
    c: Coincident(g5,g4)
    c: Horizontal(g5)
    c: DistanceX(g5,g5) = 15.6
    c: Diameter(g4) = 15.6002
    c: Coincident(g7,g6)
    c: Coincident(g7,g6)
    c: Horizontal(g7)
    c: DistanceX(g7,g7) = 15
FEATURE [PartDesign::Pocket] Pocket022  label="cell walls"
  BaseFeature = -> BaseFeature012
  Direction = (0,1,-2e-16)
  Length = 5
  Length2 = 5
  Profile = -> Sketch114
  ReferenceAxis = -> Sketch114 [N_Axis]
  Type = 0
FEATURE [PartDesign::FeatureBase] BaseFeature013
  BaseFeature = -> Pocket022
FEATURE [Sketcher::SketchObject] Sketch115
  FullyConstrained = false
  MapMode = 5
  Placement = pos=(2,-4e-16,4e-16) rot=(0.57735,0.57735,0.57735;2.0944rad)
  Support = -> [Hole025]
  sketch-geometry (9):
    g0: LineSegment StartX=-133.3 StartY=5 StartZ=0 EndX=-133.3 EndY=3 EndZ=0
    g1: LineSegment StartX=-133.3 StartY=3 StartZ=0 EndX=-131.8 EndY=3 EndZ=0
    g2: LineSegment StartX=-131.8 StartY=3 StartZ=0 EndX=-131.8 EndY=-7 EndZ=0
    g3: LineSegment StartX=-131.8 StartY=-7 StartZ=0 EndX=-133.3 EndY=-7 EndZ=0
    g4: LineSegment StartX=-133.3 StartY=-7 StartZ=0 EndX=-133.3 EndY=-9 EndZ=0
    g5: LineSegment StartX=-133.3 StartY=-9 StartZ=0 EndX=-130.3 EndY=-9 EndZ=0
    g6: LineSegment StartX=-130.3 StartY=-9 StartZ=0 EndX=-130.3 EndY=2 EndZ=0
    g7: LineSegment StartX=-130.3 StartY=2 StartZ=0 EndX=-130.3 EndY=5 EndZ=0
    g8: LineSegment StartX=-130.3 StartY=5 StartZ=0 EndX=-133.3 EndY=5 EndZ=0
  constraints (25):
    c: Vertical(g0)
    c: Coincident(g0,g1)
    c: Horizontal(g1)
    c: Coincident(g1,g2)
    c: Vertical(g2)
    c: Coincident(g2,g3)
    c: Horizontal(g3)
    c: Coincident(g3,g4)
    c: Vertical(g4)
    c: Coincident(g4,g5)
    c: Horizontal(g5)
    c: Coincident(g5,g6)
    c: Vertical(g6)
    c: Coincident(g6,g7)
    c: Vertical(g7)
    c: Coincident(g7,g8)
    c: Coincident(g8,g0)
    c: Horizontal(g8)
    c: DistanceX(g8,g8) = 3
    c: DistanceX(g1,g1) = 1.5
    c: DistanceX(g3,g3) = 1.50001
    c: DistanceY(g6,g6) = 11
    c: DistanceY(g2,g2) = 10
    c: DistanceY(g4,g4) = 2
    c: DistanceY(g0,g0) = 2
FEATURE [Part::Extrusion] Extrude042  label="Extrude072"
  Base = -> Sketch115
  Dir = (1,-2e-16,2e-16)
  DirMode = 2
  FaceMakerClass = Part::FaceMakerBullseye
  LengthFwd = 10
  LengthRev = 0
  Solid = true
  Symmetric = false
FEATURE [Sketcher::SketchObject] Sketch116
  FullyConstrained = false
  MapMode = 5
  Placement = pos=(-3e-16,0,0) rot=(-0.57735,0.57735,0.57735;4.18879rad)
  Support = -> [Hole025]
  sketch-geometry (9):
    g0: LineSegment StartX=133.3 StartY=5 StartZ=0 EndX=133.3 EndY=3 EndZ=0
    g1: LineSegment StartX=133.3 StartY=3 StartZ=0 EndX=131.8 EndY=3 EndZ=0
    g2: LineSegment StartX=131.8 StartY=3 StartZ=0 EndX=131.8 EndY=-7 EndZ=0
    g3: LineSegment StartX=131.8 StartY=-7 StartZ=0 EndX=133.3 EndY=-7 EndZ=0
    g4: LineSegment StartX=133.3 StartY=-7 StartZ=0 EndX=133.3 EndY=-9 EndZ=0
    g5: LineSegment StartX=133.3 StartY=-9 StartZ=0 EndX=130.3 EndY=-9 EndZ=0
    g6: LineSegment StartX=130.3 StartY=-9 StartZ=0 EndX=130.3 EndY=2 EndZ=0
    g7: LineSegment StartX=130.3 StartY=2 StartZ=0 EndX=130.3 EndY=5 EndZ=0
    g8: LineSegment StartX=130.3 StartY=5 StartZ=0 EndX=133.3 EndY=5 EndZ=0
  constraints (25):
    c: Vertical(g0)
    c: Coincident(g0,g1)
    c: Horizontal(g1)
    c: Coincident(g1,g2)
    c: Vertical(g2)
    c: Coincident(g2,g3)
    c: Horizontal(g3)
    c: Coincident(g3,g4)
    c: Vertical(g4)
    c: Coincident(g4,g5)
    c: Horizontal(g5)
    c: Coincident(g5,g6)
    c: Vertical(g6)
    c: Coincident(g6,g7)
    c: Vertical(g7)
    c: Coincident(g7,g8)
    c: Coincident(g8,g0)
    c: Horizontal(g8)
    c: DistanceX(g8,g8) = 3
    c: DistanceX(g1,g1) = 1.49999
    c: DistanceX(g5,g5) = 3
    c: DistanceY(g6,g6) = 11
    c: DistanceY(g4,g4) = 2
    c: DistanceY(g2,g2) = 10
    c: DistanceY(g0,g0) = 2
FEATURE [Part::Extrusion] Extrude043  label="Extrude073"
  Base = -> Sketch116
  Dir = (-1,2e-16,-2e-16)
  DirMode = 2
  FaceMakerClass = Part::FaceMakerBullseye
  LengthFwd = 10
  LengthRev = 0
  Solid = true
  Symmetric = false
FEATURE [Sketcher::SketchObject] Sketch117
  FullyConstrained = false
  MapMode = 5
  Placement = pos=(0,-109.3,0) rot=(1,0,0;1.5708rad)
  Support = -> [Pocket021]
  sketch-geometry (32):
    g0: Circle CenterX=10 CenterY=16 CenterZ=0 NormalX=0 NormalY=0 NormalZ=1 AngleXU=0 Radius=0.5
    g1: Circle CenterX=11.3 CenterY=16 CenterZ=0 NormalX=0 NormalY=0 NormalZ=1 AngleXU=0 Radius=0.5
    g2: Circle CenterX=10 CenterY=14.7 CenterZ=0 NormalX=0 NormalY=0 NormalZ=1 AngleXU=0 Radius=0.5
    g3: Circle CenterX=11.3 CenterY=14.7 CenterZ=0 NormalX=0 NormalY=0 NormalZ=1 AngleXU=0 Radius=0.5
    g4: Circle CenterX=12.6 CenterY=14.7 CenterZ=0 NormalX=0 NormalY=0 NormalZ=1 AngleXU=0 Radius=0.5
    g5: Circle CenterX=13.9 CenterY=14.7 CenterZ=0 NormalX=0 NormalY=0 NormalZ=1 AngleXU=0 Radius=0.5
    g6: Circle CenterX=15.2 CenterY=14.7 CenterZ=0 NormalX=0 NormalY=0 NormalZ=1 AngleXU=0 Radius=0.5
    g7: Circle CenterX=12.6 CenterY=16 CenterZ=0 NormalX=0 NormalY=0 NormalZ=1 AngleXU=0 Radius=0.5
    g8: Circle CenterX=13.9 CenterY=16 CenterZ=0 NormalX=0 NormalY=0 NormalZ=1 AngleXU=0 Radius=0.5
    g9: Circle CenterX=15.2 CenterY=16 CenterZ=0 NormalX=0 NormalY=0 NormalZ=1 AngleXU=0 Radius=0.5
    g10: Circle CenterX=10 CenterY=13.4 CenterZ=0 NormalX=0 NormalY=0 NormalZ=1 AngleXU=0 Radius=0.5
    g11: Circle CenterX=11.3 CenterY=13.4 CenterZ=0 NormalX=0 NormalY=0 NormalZ=1 AngleXU=0 Radius=0.5
    g12: Circle CenterX=12.6 CenterY=13.4 CenterZ=0 NormalX=0 NormalY=0 NormalZ=1 AngleXU=0 Radius=0.5
    g13: Circle CenterX=13.9 CenterY=13.4 CenterZ=0 NormalX=0 NormalY=0 NormalZ=1 AngleXU=0 Radius=0.5
    g14: Circle CenterX=15.2 CenterY=13.4 CenterZ=0 NormalX=0 NormalY=0 NormalZ=1 AngleXU=0 Radius=0.5
    g15: Circle CenterX=10 CenterY=12.1 CenterZ=0 NormalX=0 NormalY=0 NormalZ=1 AngleXU=0 Radius=0.5
    g16: Circle CenterX=11.3 CenterY=12.1 CenterZ=0 NormalX=0 NormalY=0 NormalZ=1 AngleXU=0 Radius=0.5
    g17: Circle CenterX=12.6 CenterY=12.1 CenterZ=0 NormalX=0 NormalY=0 NormalZ=1 AngleXU=0 Radius=0.5
    g18: Circle CenterX=13.9 CenterY=12.1 CenterZ=0 NormalX=0 NormalY=0 NormalZ=1 AngleXU=0 Radius=0.5
    g19: Circle CenterX=15.2 CenterY=12.1 CenterZ=0 NormalX=0 NormalY=0 NormalZ=1 AngleXU=0 Radius=0.5
    g20: Circle CenterX=16.5 CenterY=16 CenterZ=0 NormalX=0 NormalY=0 NormalZ=1 AngleXU=0 Radius=0.5
    g21: Circle CenterX=16.5 CenterY=14.7 CenterZ=0 NormalX=0 NormalY=0 NormalZ=1 AngleXU=0 Radius=0.5
    g22: Circle CenterX=16.5 CenterY=13.4 CenterZ=0 NormalX=0 NormalY=0 NormalZ=1 AngleXU=0 Radius=0.5
    g23: Circle CenterX=16.5 CenterY=12.1 CenterZ=0 NormalX=0 NormalY=0 NormalZ=1 AngleXU=0 Radius=0.5
    g24: Circle CenterX=17.8 CenterY=16 CenterZ=0 NormalX=0 NormalY=0 NormalZ=1 AngleXU=0 Radius=0.5
    g25: Circle CenterX=19.1 CenterY=16 CenterZ=0 NormalX=0 NormalY=0 NormalZ=1 AngleXU=0 Radius=0.5
    g26: Circle CenterX=17.8 CenterY=14.7 CenterZ=0 NormalX=0 NormalY=0 NormalZ=1 AngleXU=0 Radius=0.5
    g27: Circle CenterX=19.1 CenterY=14.7 CenterZ=0 NormalX=0 NormalY=0 NormalZ=1 AngleXU=0 Radius=0.5
    g28: Circle CenterX=17.8 CenterY=13.4 CenterZ=0 NormalX=0 NormalY=0 NormalZ=1 AngleXU=0 Radius=0.5
    g29: Circle CenterX=19.1 CenterY=13.4 CenterZ=0 NormalX=0 NormalY=0 NormalZ=1 AngleXU=0 Radius=0.5
    g30: Circle CenterX=17.8 CenterY=12.1 CenterZ=0 NormalX=0 NormalY=0 NormalZ=1 AngleXU=0 Radius=0.5
    g31: Circle CenterX=19.1 CenterY=12.1 CenterZ=0 NormalX=0 NormalY=0 NormalZ=1 AngleXU=0 Radius=0.5
  constraints (32):
    c: Diameter(g0) = 1
    c: Diameter(g1) = 1
    c: Diameter(g7) = 1
    c: Diameter(g8) = 1
    c: Diameter(g9) = 1
    c: Diameter(g2) = 1
    c: Diameter(g3) = 1
    c: Diameter(g4) = 1
    c: Diameter(g5) = 1
    c: Diameter(g6) = 1
    c: Diameter(g10) = 1
    c: Diameter(g11) = 1
    c: Diameter(g12) = 1
    c: Diameter(g13) = 1
    c: Diameter(g14) = 1
    c: Diameter(g19) = 1
    c: Diameter(g18) = 1
    c: Diameter(g17) = 1
    c: Diameter(g16) = 1
    c: Diameter(g15) = 1
    c: Diameter(g20) = 1
    c: Diameter(g21) = 1
    c: Diameter(g22) = 1
    c: Diameter(g23) = 1
    c: Diameter(g24) = 1
    c: Diameter(g26) = 1
    c: Diameter(g28) = 1
    c: Diameter(g30) = 1
    c: Diameter(g31) = 1
    c: Diameter(g29) = 1
    c: Diameter(g27) = 1
    c: Diameter(g25) = 1
FEATURE [PartDesign::Hole] Hole026
  CustomThreadClearance = 0
  Depth = 2
  DepthType = 0
  Diameter = 1
  DrillForDepth = false
  DrillPoint = 0
  DrillPointAngle = 118
  HoleCutCountersinkAngle = 90
  HoleCutCustomValues = false
  HoleCutDepth = 0
  HoleCutDiameter = 6.1
  HoleCutType = 0
  ModelThread = false
  Profile = -> Sketch117
  Tapered = false
  TaperedAngle = 90
  ThreadClass = 0
  ThreadDepth = 2
  ThreadDepthType = 0
  ThreadDirection = 0
  ThreadFit = 0
  ThreadSize = 0
  ThreadType = 0
  Threaded = false
  UseCustomThreadClearance = false
FEATURE [Sketcher::SketchObject] Sketch118
  FullyConstrained = false
  MapMode = 5
  Placement = pos=(0,-99.794,0) rot=(1,0,0;1.5708rad)
  Support = -> [Pocket022]
  sketch-geometry (8):
    g0: ArcOfCircle CenterX=11.5 CenterY=21.374 CenterZ=0 NormalX=0 NormalY=0 NormalZ=1 AngleXU=0 Radius=7.50005 StartAngle=3.13813 EndAngle=6.28665
    g1: LineSegment StartX=4 StartY=21.4 StartZ=0 EndX=19 EndY=21.4 EndZ=0
    g2: ArcOfCircle CenterX=32 CenterY=21.3845 CenterZ=0 NormalX=0 NormalY=0 NormalZ=1 AngleXU=0 Radius=8.00001 StartAngle=3.13966 EndAngle=6.28512
    g3: LineSegment StartX=24 StartY=21.4 StartZ=0 EndX=40 EndY=21.4 EndZ=0
    g4: ArcOfCircle CenterX=52.2 CenterY=21.3636 CenterZ=0 NormalX=0 NormalY=0 NormalZ=1 AngleXU=0 Radius=7.80009 StartAngle=3.13692 EndAngle=6.28785
    g5: LineSegment StartX=60 StartY=21.4 StartZ=0 EndX=44.4 EndY=21.4 EndZ=0
    g6: ArcOfCircle CenterX=72.5 CenterY=21.2875 CenterZ=0 NormalX=0 NormalY=0 NormalZ=1 AngleXU=0 Radius=7.50084 StartAngle=3.12659 EndAngle=6.29819
    g7: LineSegment StartX=80 StartY=21.4 StartZ=0 EndX=65 EndY=21.4 EndZ=0
  constraints (19):
    c: Coincident(g1,g0)
    c: Coincident(g1,g0)
    c: Horizontal(g1)
    c: DistanceX(g1,g1) = 15
    c: Diameter(g0) = 15.0001
    c: Coincident(g3,g2)
    c: Coincident(g3,g2)
    c: Horizontal(g3)
    c: DistanceX(g3,g3) = 16
    c: Diameter(g2) = 16
    c: Coincident(g5,g4)
    c: Coincident(g5,g4)
    c: Horizontal(g5)
    c: DistanceX(g5,g5) = 15.6
    c: Diameter(g4) = 15.6002
    c: Coincident(g7,g6)
    c: Coincident(g7,g6)
    c: Horizontal(g7)
    c: DistanceX(g7,g7) = 15
FEATURE [PartDesign::Pocket] Pocket023  label="!!!!!!!!!!!!!!!!!!!!!!!!!!!!"
  Direction = (0,1,-2e-16)
  Length = 5
  Length2 = 5
  Profile = -> Sketch118
  ReferenceAxis = -> Sketch118 [N_Axis]
  Type = 0
FEATURE [Sketcher::SketchObject] Sketch119
  FullyConstrained = false
  MapMode = 5
  Placement = pos=(0,0,0) rot=(0.57735,-0.57735,-0.57735;2.0944rad)
  Support = -> [Pocket023]
  sketch-geometry (4):
    g0: LineSegment StartX=14.4002 StartY=0 StartZ=0 EndX=109.3 EndY=0 EndZ=0
    g1: LineSegment StartX=109.3 StartY=0 StartZ=0 EndX=109.3 EndY=4 EndZ=0
    g2: LineSegment StartX=109.3 StartY=4 StartZ=0 EndX=14.4002 EndY=4 EndZ=0
    g3: LineSegment StartX=14.4002 StartY=4 StartZ=0 EndX=14.4002 EndY=0 EndZ=0
  constraints (11):
    c: Coincident(g0,g1)
    c: Coincident(g1,g2)
    c: Coincident(g2,g3)
    c: Coincident(g3,g0)
    c: Horizontal(g0)
    c: Horizontal(g2)
    c: Vertical(g1)
    c: Vertical(g3)
    c: PointOnObject(g0,g-1)
    c: DistanceX(g2,g2) = 94.8998
    c: DistanceY(g1,g1) = 4
FEATURE [Part::Extrusion] Extrude044  label="Extrude074"
  Base = -> Sketch119
  Dir = (-1,0,0)
  DirMode = 2
  FaceMakerClass = Part::FaceMakerBullseye
  LengthFwd = 3
  LengthRev = 0
  Solid = true
  Symmetric = false
FEATURE [Sketcher::SketchObject] Sketch120
  FullyConstrained = false
  MapMode = 5
  Placement = pos=(84.2,0,0) rot=(0.57735,0.57735,0.57735;2.0944rad)
  Support = -> [Pocket023]
  sketch-geometry (4):
    g0: LineSegment StartX=-109.302 StartY=0 StartZ=0 EndX=-14.4 EndY=0 EndZ=0
    g1: LineSegment StartX=-14.4 StartY=0 StartZ=0 EndX=-14.4 EndY=4 EndZ=0
    g2: LineSegment StartX=-14.4 StartY=4 StartZ=0 EndX=-109.302 EndY=4 EndZ=0
    g3: LineSegment StartX=-109.302 StartY=4 StartZ=0 EndX=-109.302 EndY=0 EndZ=0
  constraints (11):
    c: Coincident(g0,g1)
    c: Coincident(g1,g2)
    c: Coincident(g2,g3)
    c: Coincident(g3,g0)
    c: Horizontal(g0)
    c: Horizontal(g2)
    c: Vertical(g1)
    c: Vertical(g3)
    c: PointOnObject(g0,g-1)
    c: DistanceX(g2,g2) = 94.9019
    c: DistanceY(g1,g1) = 4
FEATURE [Part::Extrusion] Extrude045  label="Extrude075"
  Base = -> Sketch120
  Dir = (1,0,0)
  DirMode = 2
  FaceMakerClass = Part::FaceMakerBullseye
  LengthFwd = 3
  LengthRev = 0
  Solid = true
  Symmetric = false
FEATURE [Sketcher::SketchObject] Sketch125
  FullyConstrained = false
  MapMode = 5
  Placement = pos=(0,-109.3,0) rot=(1,0,0;1.5708rad)
  Support = -> [Hole026]
  sketch-geometry (16):
    g0: LineSegment StartX=40.86 StartY=19.44 StartZ=0 EndX=31.16 EndY=19.44 EndZ=0
    g1: LineSegment StartX=43.5 StartY=19.44 StartZ=0 EndX=53.16 EndY=19.44 EndZ=0
    g2: LineSegment StartX=40.86 StartY=19.75 StartZ=0 EndX=43.5 EndY=19.75 EndZ=0
    g3: LineSegment StartX=43.5 StartY=19.75 StartZ=0 EndX=43.5 EndY=12.6 EndZ=0
    g4: LineSegment StartX=43.5 StartY=12.6 StartZ=0 EndX=40.86 EndY=12.6 EndZ=0
    g5: LineSegment StartX=40.86 StartY=12.6 StartZ=0 EndX=40.86 EndY=19.75 EndZ=0
    g6: LineSegment StartX=31.16 StartY=19.75 StartZ=0 EndX=33.8 EndY=19.75 EndZ=0
    g7: LineSegment StartX=33.8 StartY=19.75 StartZ=0 EndX=33.8 EndY=12.6 EndZ=0
    g8: LineSegment StartX=33.8 StartY=12.6 StartZ=0 EndX=31.16 EndY=12.6 EndZ=0
    g9: LineSegment StartX=31.16 StartY=12.6 StartZ=0 EndX=31.16 EndY=19.75 EndZ=0
    g10: LineSegment StartX=50.52 StartY=19.75 StartZ=0 EndX=53.16 EndY=19.75 EndZ=0
    g11: LineSegment StartX=53.16 StartY=19.75 StartZ=0 EndX=53.16 EndY=12.6 EndZ=0
    g12: LineSegment StartX=53.16 StartY=12.6 StartZ=0 EndX=50.52 EndY=12.6 EndZ=0
    g13: LineSegment StartX=50.52 StartY=12.6 StartZ=0 EndX=50.52 EndY=19.75 EndZ=0
    g14: LineSegment StartX=40.86 StartY=19.75 StartZ=0 EndX=31.16 EndY=19.75 EndZ=0
    g15: LineSegment StartX=43.5 StartY=19.75 StartZ=0 EndX=53.16 EndY=19.75 EndZ=0
  constraints (38):
    c: Horizontal(g0)
    c: DistanceX(g0,g0) = 9.7
    c: Horizontal(g1)
    c: DistanceX(g1,g1) = 9.66
    c: Coincident(g2,g3)
    c: Coincident(g3,g4)
    c: Coincident(g4,g5)
    c: Coincident(g5,g2)
    c: Horizontal(g2)
    c: Horizontal(g4)
    c: Vertical(g3)
    c: Vertical(g5)
    c: DistanceX(g2,g2) = 2.64
    c: DistanceY(g3,g3) = 7.15
    c: Coincident(g6,g7)
    c: Coincident(g7,g8)
    c: Coincident(g8,g9)
    c: Coincident(g9,g6)
    c: Horizontal(g6)
    c: Horizontal(g8)
    c: Vertical(g7)
    c: Vertical(g9)
    c: Coincident(g10,g11)
    c: Coincident(g11,g12)
    c: Coincident(g12,g13)
    c: Coincident(g13,g10)
    c: Horizontal(g10)
    c: Horizontal(g12)
    c: Vertical(g11)
    c: Vertical(g13)
    c: DistanceX(g6,g6) = 2.64
    c: DistanceX(g10,g10) = 2.64
    c: DistanceY(g9,g9) = 7.15
    c: DistanceY(g13,g13) = 7.15
    c: Coincident(g14,g2)
    c: Horizontal(g14)
    c: Coincident(g15,g2)
    c: Horizontal(g15)
FEATURE [PartDesign::Pocket] Pocket024
  BaseFeature = -> Hole026
  Direction = (0,1,-2e-16)
  Length = 5
  Length2 = 5
  Profile = -> Sketch125
  ReferenceAxis = -> Sketch125 [N_Axis]
  Type = 0
FEATURE [Sketcher::SketchObject] Sketch126
  FullyConstrained = false
  MapMode = 5
  Placement = pos=(-2.87e-14,-130.3,0) rot=(0,0.707107,0.707107;3.14159rad)
  Support = -> [Extrude043]
  sketch-geometry (4):
    g0: LineSegment StartX=10 StartY=5 StartZ=0 EndX=8 EndY=5 EndZ=0
    g1: LineSegment StartX=8 StartY=5 StartZ=0 EndX=8 EndY=2 EndZ=0
    g2: LineSegment StartX=8 StartY=2 StartZ=0 EndX=10 EndY=2 EndZ=0
    g3: LineSegment StartX=10 StartY=2 StartZ=0 EndX=10 EndY=5 EndZ=0
  constraints (10):
    c: Coincident(g0,g1)
    c: Coincident(g1,g2)
    c: Coincident(g2,g3)
    c: Coincident(g3,g0)
    c: Horizontal(g0)
    c: Horizontal(g2)
    c: Vertical(g1)
    c: Vertical(g3)
    c: DistanceX(g0,g0) = 2
    c: DistanceY(g1,g1) = 3
FEATURE [Part::Extrusion] Extrude048  label="Extrude077"
  Base = -> Sketch126
  Dir = (2e-16,1,-2e-16)
  DirMode = 2
  FaceMakerClass = Part::FaceMakerBullseye
  LengthFwd = 6.1
  LengthRev = 0
  Solid = true
  Symmetric = false
FEATURE [Sketcher::SketchObject] Sketch127
  FullyConstrained = false
  MapMode = 5
  Placement = pos=(-2.87e-14,-130.3,0) rot=(0,0.707107,0.707107;3.14159rad)
  Support = -> [Extrude042]
  sketch-geometry (4):
    g0: LineSegment StartX=-12 StartY=5 StartZ=0 EndX=-10 EndY=5 EndZ=0
    g1: LineSegment StartX=-10 StartY=5 StartZ=0 EndX=-10 EndY=2 EndZ=0
    g2: LineSegment StartX=-10 StartY=2 StartZ=0 EndX=-12 EndY=2 EndZ=0
    g3: LineSegment StartX=-12 StartY=2 StartZ=0 EndX=-12 EndY=5 EndZ=0
  constraints (10):
    c: Coincident(g0,g1)
    c: Coincident(g1,g2)
    c: Coincident(g2,g3)
    c: Coincident(g3,g0)
    c: Horizontal(g0)
    c: Horizontal(g2)
    c: Vertical(g1)
    c: Vertical(g3)
    c: DistanceX(g2,g2) = 2
    c: DistanceY(g1,g1) = 3
FEATURE [Part::Extrusion] Extrude049  label="Extrude078"
  Base = -> Sketch127
  Dir = (2e-16,1,-2e-16)
  DirMode = 2
  FaceMakerClass = Part::FaceMakerBullseye
  LengthFwd = 6.1
  LengthRev = 0
  Solid = true
  Symmetric = false
FEATURE [PartDesign::FeatureBase] BaseFeature015
  BaseFeature = -> Extrude049
FEATURE [Sketcher::SketchObject] Sketch128
  FullyConstrained = false
  MapMode = 5
  Placement = pos=(-10,2.2e-15,0) rot=(-0.57735,0.57735,0.57735;4.18879rad)
  Support = -> [Extrude048]
  sketch-geometry (1):
    g0: Circle CenterX=125.95 CenterY=3.5 CenterZ=0 NormalX=0 NormalY=0 NormalZ=1 AngleXU=0 Radius=0.75
  constraints (1):
    c: Diameter(g0) = 1.5
FEATURE [PartDesign::Hole] Hole027
  CustomThreadClearance = 0
  Depth = 2
  DepthType = 0
  Diameter = 1.5
  DrillForDepth = false
  DrillPoint = 1
  DrillPointAngle = 118
  HoleCutCountersinkAngle = 90
  HoleCutCustomValues = false
  HoleCutDepth = 0
  HoleCutDiameter = 6.1
  HoleCutType = 0
  ModelThread = false
  Profile = -> Sketch128
  Tapered = false
  TaperedAngle = 90
  ThreadClass = 0
  ThreadDepth = 2
  ThreadDepthType = 0
  ThreadDirection = 0
  ThreadFit = 0
  ThreadSize = 0
  ThreadType = 0
  Threaded = false
  UseCustomThreadClearance = false
FEATURE [Sketcher::SketchObject] Sketch129
  FullyConstrained = false
  MapMode = 5
  Placement = pos=(12,-2.6e-15,0) rot=(0.57735,0.57735,0.57735;2.0944rad)
  Support = -> [BaseFeature015]
  sketch-geometry (1):
    g0: Circle CenterX=-125.951 CenterY=3.5 CenterZ=0 NormalX=0 NormalY=0 NormalZ=1 AngleXU=0 Radius=0.75
  constraints (1):
    c: Diameter(g0) = 1.5
FEATURE [PartDesign::Hole] Hole028
  BaseFeature = -> BaseFeature015
  CustomThreadClearance = 0
  Depth = 14.3135
  DepthType = 0
  Diameter = 1.5
  DrillForDepth = false
  DrillPoint = 1
  DrillPointAngle = 118
  HoleCutCountersinkAngle = 90
  HoleCutCustomValues = false
  HoleCutDepth = 0
  HoleCutDiameter = 6.1
  HoleCutType = 0
  ModelThread = false
  Profile = -> Sketch129
  Tapered = false
  TaperedAngle = 90
  ThreadClass = 0
  ThreadDepth = 14.3135
  ThreadDepthType = 0
  ThreadDirection = 0
  ThreadFit = 0
  ThreadSize = 0
  ThreadType = 0
  Threaded = false
  UseCustomThreadClearance = false
FEATURE [PartDesign::Body] Body010  label="HANDLE LOCK"
  BaseFeature = -> Extrude049
  Group = -> [BaseFeature015,Sketch129,Hole028]
  Origin = -> Origin104
  Tip = -> Hole028
FEATURE [Sketcher::SketchObject] Sketch130
  FullyConstrained = false
  MapMode = 5
  Placement = pos=(-2.9e-14,-131.8,0) rot=(1,0,0;1.5708rad)
  Support = -> [Extrude042]
  sketch-geometry (8):
    g0: LineSegment StartX=-10 StartY=-7 StartZ=0 EndX=-8 EndY=-7 EndZ=0
    g1: LineSegment StartX=-8 StartY=-7 StartZ=0 EndX=-8 EndY=3 EndZ=0
    g2: LineSegment StartX=-8 StartY=3 StartZ=0 EndX=-10 EndY=3 EndZ=0
    g3: LineSegment StartX=-10 StartY=3 StartZ=0 EndX=-10 EndY=-7 EndZ=0
    g4: LineSegment StartX=10 StartY=3 StartZ=0 EndX=12 EndY=3 EndZ=0
    g5: LineSegment StartX=12 StartY=3 StartZ=0 EndX=12 EndY=-7 EndZ=0
    g6: LineSegment StartX=12 StartY=-7 StartZ=0 EndX=10 EndY=-7 EndZ=0
    g7: LineSegment StartX=10 StartY=-7 StartZ=0 EndX=10 EndY=3 EndZ=0
  constraints (20):
    c: Coincident(g0,g1)
    c: Coincident(g1,g2)
    c: Coincident(g2,g3)
    c: Coincident(g3,g0)
    c: Horizontal(g0)
    c: Horizontal(g2)
    c: Vertical(g1)
    c: Vertical(g3)
    c: Coincident(g4,g5)
    c: Coincident(g5,g6)
    c: Coincident(g6,g7)
    c: Coincident(g7,g4)
    c: Horizontal(g4)
    c: Horizontal(g6)
    c: Vertical(g5)
    c: Vertical(g7)
    c: DistanceX(g6,g6) = 2
    c: DistanceX(g0,g0) = 2
    c: DistanceY(g1,g1) = 10
    c: DistanceY(g7,g7) = 10
FEATURE [Part::Extrusion] Extrude050  label="Extrude079"
  Base = -> Sketch130
  Dir = (-2e-16,-1,2e-16)
  DirMode = 2
  FaceMakerClass = Part::FaceMakerBullseye
  LengthFwd = 1.5
  LengthRev = 0
  Solid = true
  Symmetric = false
FEATURE [App::Part] Part024  label="locking handle"
  Group = -> [Body010,Sketch090,Sketch113,Sketch116,Sketch115,Extrude041,Extrude043,Extrude042,Hole025,Sketch126,Sketch127,Sketch128,Extrude048,Extrude049,Hole027,Sketch130,Extrude050]
  Origin = -> Origin103
  Placement = pos=(41.16,20.68,14.44) rot=(0,0,1;0rad)
FEATURE [Sketcher::SketchObject] Sketch131
  FullyConstrained = false
  MapMode = 5
  Placement = pos=(0,-117,0) rot=(1,0,0;1.5708rad)
  Support = -> [BaseFeature016]
  sketch-geometry (20):
    g0: LineSegment StartX=-135.5 StartY=5.5 StartZ=0 EndX=-132.5 EndY=5.5 EndZ=0
    g1: LineSegment StartX=-132.5 StartY=5.5 StartZ=0 EndX=-132.5 EndY=1.5 EndZ=0
    g2: LineSegment StartX=-132.5 StartY=1.5 StartZ=0 EndX=-135.5 EndY=1.5 EndZ=0
    g3: LineSegment StartX=-135.5 StartY=1.5 StartZ=0 EndX=-135.5 EndY=5.5 EndZ=0
    g4: LineSegment StartX=-123 StartY=5 StartZ=0 EndX=-125 EndY=5 EndZ=0
    g5: LineSegment StartX=-125 StartY=5 StartZ=0 EndX=-125 EndY=2 EndZ=0
    g6: LineSegment StartX=-125 StartY=2 StartZ=0 EndX=-123 EndY=2 EndZ=0
    g7: LineSegment StartX=-123 StartY=2 StartZ=0 EndX=-123 EndY=5 EndZ=0
    g8: LineSegment StartX=-145 StartY=5 StartZ=0 EndX=-143 EndY=5 EndZ=0
    g9: LineSegment StartX=-143 StartY=5 StartZ=0 EndX=-143 EndY=2 EndZ=0
    g10: LineSegment StartX=-143 StartY=2 StartZ=0 EndX=-145 EndY=2 EndZ=0
    g11: LineSegment StartX=-145 StartY=2 StartZ=0 EndX=-145 EndY=5 EndZ=0
    g12: LineSegment StartX=-145.5 StartY=5.5 StartZ=0 EndX=-142.5 EndY=5.5 EndZ=0
    g13: LineSegment StartX=-142.5 StartY=5.5 StartZ=0 EndX=-142.5 EndY=1.5 EndZ=0
    g14: LineSegment StartX=-142.5 StartY=1.5 StartZ=0 EndX=-145.5 EndY=1.5 EndZ=0
    g15: LineSegment StartX=-145.5 StartY=1.5 StartZ=0 EndX=-145.5 EndY=5.5 EndZ=0
    g16: LineSegment StartX=-125.5 StartY=5.5 StartZ=0 EndX=-122.5 EndY=5.5 EndZ=0
    g17: LineSegment StartX=-122.5 StartY=5.5 StartZ=0 EndX=-122.5 EndY=1.5 EndZ=0
    g18: LineSegment StartX=-122.5 StartY=1.5 StartZ=0 EndX=-125.5 EndY=1.5 EndZ=0
    g19: LineSegment StartX=-125.5 StartY=1.5 StartZ=0 EndX=-125.5 EndY=5.5 EndZ=0
  constraints (46):
    c: Coincident(g0,g1)
    c: Coincident(g1,g2)
    c: Coincident(g2,g3)
    c: Coincident(g3,g0)
    c: Horizontal(g0)
    c: Horizontal(g2)
    c: Vertical(g1)
    c: Vertical(g3)
    c: Coincident(g4,g5)
    c: Coincident(g5,g6)
    c: Coincident(g6,g7)
    c: Coincident(g7,g4)
    c: Horizontal(g4)
    c: Horizontal(g6)
    c: Vertical(g5)
    c: Vertical(g7)
    c: Coincident(g8,g9)
    c: Coincident(g9,g10)
    c: Coincident(g10,g11)
    c: Coincident(g11,g8)
    c: Horizontal(g8)
    c: Horizontal(g10)
    c: Vertical(g9)
    c: Vertical(g11)
    c: Coincident(g12,g13)
    c: Coincident(g13,g14)
    c: Coincident(g14,g15)
    c: Coincident(g15,g12)
    c: Horizontal(g12)
    c: Horizontal(g14)
    c: Vertical(g13)
    c: Vertical(g15)
    c: Coincident(g16,g17)
    c: Coincident(g17,g18)
    c: Coincident(g18,g19)
    c: Coincident(g19,g16)
    c: Horizontal(g16)
    c: Horizontal(g18)
    c: Vertical(g17)
    c: Vertical(g19)
    c: DistanceY(g13,g13) = 4
    c: DistanceY(g1,g1) = 4
    c: DistanceY(g19,g19) = 4
    c: DistanceX(g12,g12) = 3
    c: DistanceX(g0,g0) = 3
    c: DistanceX(g16,g16) = 3
FEATURE [PartDesign::Pocket] Pocket025
  BaseFeature = -> BaseFeature016
  Direction = (0,1,-2e-16)
  Length = 4
  Length2 = 5
  Profile = -> Sketch131
  ReferenceAxis = -> Sketch131 [N_Axis]
  Type = 0
FEATURE [Sketcher::SketchObject] Sketch132
  FullyConstrained = false
  MapMode = 5
  Placement = pos=(-121,0,0) rot=(0.57735,0.57735,0.57735;2.0944rad)
  Support = -> [Pocket025]
  sketch-geometry (1):
    g0: Circle CenterX=-115.25 CenterY=3.5 CenterZ=0 NormalX=0 NormalY=0 NormalZ=1 AngleXU=0 Radius=0.75
  constraints (1):
    c: Diameter(g0) = 1.5
FEATURE [PartDesign::Hole] Hole029
  BaseFeature = -> Pocket025
  CustomThreadClearance = 0
  Depth = 24
  DepthType = 0
  Diameter = 1.5
  DrillForDepth = false
  DrillPoint = 0
  DrillPointAngle = 118
  HoleCutCountersinkAngle = 90
  HoleCutCustomValues = false
  HoleCutDepth = 0
  HoleCutDiameter = 6.1
  HoleCutType = 0
  ModelThread = false
  Profile = -> Sketch132
  Tapered = false
  TaperedAngle = 90
  ThreadClass = 0
  ThreadDepth = 24
  ThreadDepthType = 0
  ThreadDirection = 0
  ThreadFit = 0
  ThreadSize = 0
  ThreadType = 0
  Threaded = false
  UseCustomThreadClearance = false
FEATURE [PartDesign::Body] Body009  label="LOCK MECHANISM BODY"
  BaseFeature = -> Extrude047
  Group = -> [BaseFeature016,Sketch131,Pocket025,Sketch132,Hole029]
  Origin = -> Origin102
  Tip = -> Hole029
FEATURE [App::Part] Part023  label="locking mechanism"
  Group = -> [Body009,BaseFeature007,BaseFeature008,Sketch089,Extrude007,Sketch110,Sketch088,Sketch012,BaseFeature010,Pocket018,Sketch087,Sketch107,Sketch109,Extrude039,Extrude040,Pocket019,Hole018]
  Origin = -> Origin101
  Placement = pos=(176.16,9.99,14.45) rot=(0,0,1;0rad)
FEATURE [App::Part] Part028  label="Locking Components"
  Group = -> [Part023,Part024,Part025]
  Origin = -> Origin111
FEATURE [Sketcher::SketchObject] Sketch133
  FullyConstrained = false
  MapMode = 5
  Placement = pos=(0,-109.3,0) rot=(1,0,0;1.5708rad)
  Support = -> [Pocket024]
  sketch-geometry (8):
    g0: LineSegment StartX=7.1 StartY=19.01 StartZ=0 EndX=27.1 EndY=19.01 EndZ=0
    g1: LineSegment StartX=27.1 StartY=19.01 StartZ=0 EndX=27.1 EndY=4.01 EndZ=0
    g2: LineSegment StartX=27.1 StartY=4.01 StartZ=0 EndX=7.1 EndY=4.01 EndZ=0
    g3: LineSegment StartX=7.1 StartY=4.01 StartZ=0 EndX=7.1 EndY=19.01 EndZ=0
    g4: LineSegment StartX=57.1633 StartY=4 StartZ=0 EndX=77.1635 EndY=4 EndZ=0
    g5: LineSegment StartX=77.1635 StartY=4 StartZ=0 EndX=77.1635 EndY=19 EndZ=0
    g6: LineSegment StartX=77.1635 StartY=19 StartZ=0 EndX=57.1633 EndY=19 EndZ=0
    g7: LineSegment StartX=57.1633 StartY=19 StartZ=0 EndX=57.1633 EndY=4 EndZ=0
  constraints (20):
    c: Coincident(g0,g1)
    c: Coincident(g1,g2)
    c: Coincident(g2,g3)
    c: Coincident(g3,g0)
    c: Horizontal(g0)
    c: Horizontal(g2)
    c: Vertical(g1)
    c: Vertical(g3)
    c: Coincident(g4,g5)
    c: Coincident(g5,g6)
    c: Coincident(g6,g7)
    c: Coincident(g7,g4)
    c: Horizontal(g4)
    c: Horizontal(g6)
    c: Vertical(g5)
    c: Vertical(g7)
    c: DistanceY(g5,g5) = 15
    c: DistanceX(g6,g6) = 20.0002
    c: DistanceX(g0,g0) = 20
    c: DistanceY(g1,g1) = 15
FEATURE [PartDesign::Pocket] Pocket026
  BaseFeature = -> Pocket024
  Direction = (0,1,-2e-16)
  Length = 5
  Length2 = 5
  Profile = -> Sketch133
  ReferenceAxis = -> Sketch133 [N_Axis]
  Type = 0
FEATURE [PartDesign::Body] Body012  label="FRONT BODY"
  Group = -> [Sketch117,Hole026,Sketch125,Pocket024,Sketch133,Pocket026]
  Origin = -> Origin107
  Tip = -> Pocket026
FEATURE [App::Part] Part021  label="main enclosure"
  Group = -> [Body007,Extrude030,Extrude005,Sketch085,Sketch084,Body012,BaseFeature006,Sketch086,Sketch099,Extrude035,Sketch100,Sketch101,Hole021,Extrude036,Extrude033,BaseFeature009,Hole019,Sketch096,Sketch095,Sketch097,Sketch098,Sketch105,Extrude034,Hole020,Extrude038,Sketch106,Hole024,Extrude031,Sketch093,Sketch094,Pocket021,Sketch112,BaseFeature011,Extrude032,Pocket017,Sketch102,Hole022,Body008,Extrude029,+18 more]
  Origin = -> Origin097
FEATURE [App::Part] Part030  label="Battery"
  Group = -> [Part021,Part026,Part028,Part022,Part027,Sketch111,Extrude047]
  Origin = -> Origin114
  Placement = pos=(84.2,-17.7,19) rot=(0,-1,0;3.14159rad)
FEATURE [Part::Feature] Part__Feature322  label="Base012"
  shape: bbox 83.22 x 38.74 x 9.662 mm, 80 faces (baked)
FEATURE [Part::Feature] Part__Feature323  label="Base013"
  shape: bbox 76 x 12.7 x 41.75 mm, 13 faces (baked)
FEATURE [App::Part] Base  label="Base014"
  Group = -> [Part__Feature322,Part__Feature323]
  Origin = -> Origin118
FEATURE [Part::Feature] Part__Feature324  label="Springs and adjustment"
  shape: bbox 11 x 21.89 x 6.263 mm, 48 faces (baked)
FEATURE [Part::Feature] Part__Feature325  label="Springs and adjustment001"
  shape: bbox 5.684 x 18.4 x 5.67 mm, 22 faces (baked)
FEATURE [Part::Feature] Part__Feature326  label="Springs and adjustment002"
  shape: bbox 2.927 x 3.632 x 10.38 mm, 10 faces (baked)
FEATURE [Part::Feature] Part__Feature327  label="Springs and adjustment003"
  shape: bbox 2.927 x 3.632 x 10.38 mm, 10 faces (baked)
FEATURE [Part::Feature] Part__Feature328  label="Springs and adjustment004"
  shape: bbox 6.267 x 9.413 x 6.349 mm, 3 faces (baked)
FEATURE [App::Part] Springs_and_adjustment  label="Springs and adjustment005"
  Group = -> [Part__Feature324,Part__Feature325,Part__Feature326,Part__Feature327,Part__Feature328]
  Origin = -> Origin119
FEATURE [Part::Feature] Part__Feature329  label="Springs and adjustment006"
  Placement = pos=(-11,0,0) rot=(0,0,1;0rad)
  shape: bbox 11 x 21.89 x 6.263 mm, 48 faces (baked)
FEATURE [Part::Feature] Part__Feature330  label="Springs and adjustment007"
  Placement = pos=(-11,0,0) rot=(0,0,1;0rad)
  shape: bbox 5.684 x 18.4 x 5.67 mm, 22 faces (baked)
FEATURE [Part::Feature] Part__Feature331  label="Springs and adjustment008"
  Placement = pos=(-11,0,0) rot=(0,0,1;0rad)
  shape: bbox 2.927 x 3.632 x 10.38 mm, 10 faces (baked)
FEATURE [Part::Feature] Part__Feature332  label="Springs and adjustment009"
  Placement = pos=(-11,0,0) rot=(0,0,1;0rad)
  shape: bbox 2.927 x 3.632 x 10.38 mm, 10 faces (baked)
FEATURE [Part::Feature] Part__Feature333  label="Springs and adjustment010"
  Placement = pos=(-11,0,0) rot=(0,0,1;0rad)
  shape: bbox 6.267 x 9.413 x 6.349 mm, 3 faces (baked)
FEATURE [App::Part] Springs_and_adjustment001  label="Springs and adjustment011"
  Group = -> [Part__Feature329,Part__Feature330,Part__Feature331,Part__Feature332,Part__Feature333]
  Origin = -> Origin120
FEATURE [Part::Feature] Part__Feature334  label="Springs and adjustment012"
  Placement = pos=(-22,0,0) rot=(0,0,1;0rad)
  shape: bbox 11 x 21.89 x 6.263 mm, 48 faces (baked)
FEATURE [Part::Feature] Part__Feature335  label="Springs and adjustment013"
  Placement = pos=(-22,0,0) rot=(0,0,1;0rad)
  shape: bbox 5.684 x 18.4 x 5.67 mm, 22 faces (baked)
FEATURE [Part::Feature] Part__Feature336  label="Springs and adjustment014"
  Placement = pos=(-22,0,0) rot=(0,0,1;0rad)
  shape: bbox 2.927 x 3.632 x 10.38 mm, 10 faces (baked)
FEATURE [Part::Feature] Part__Feature337  label="Springs and adjustment015"
  Placement = pos=(-22,0,0) rot=(0,0,1;0rad)
  shape: bbox 2.927 x 3.632 x 10.38 mm, 10 faces (baked)
FEATURE [Part::Feature] Part__Feature338  label="Springs and adjustment016"
  Placement = pos=(-22,0,0) rot=(0,0,1;0rad)
  shape: bbox 6.267 x 9.413 x 6.349 mm, 3 faces (baked)
FEATURE [App::Part] Springs_and_adjustment002  label="Springs and adjustment017"
  Group = -> [Part__Feature334,Part__Feature335,Part__Feature336,Part__Feature337,Part__Feature338]
  Origin = -> Origin121
FEATURE [Part::Feature] Part__Feature339  label="Springs and adjustment018"
  Placement = pos=(-33,0,0) rot=(0,0,1;0rad)
  shape: bbox 11 x 21.89 x 6.263 mm, 48 faces (baked)
FEATURE [Part::Feature] Part__Feature340  label="Springs and adjustment019"
  Placement = pos=(-33,0,0) rot=(0,0,1;0rad)
  shape: bbox 5.684 x 18.4 x 5.67 mm, 22 faces (baked)
FEATURE [Part::Feature] Part__Feature341  label="Springs and adjustment020"
  Placement = pos=(-33,0,0) rot=(0,0,1;0rad)
  shape: bbox 2.927 x 3.632 x 10.38 mm, 10 faces (baked)
FEATURE [Part::Feature] Part__Feature342  label="Springs and adjustment021"
  Placement = pos=(-33,0,0) rot=(0,0,1;0rad)
  shape: bbox 2.927 x 3.632 x 10.38 mm, 10 faces (baked)
FEATURE [Part::Feature] Part__Feature343  label="Springs and adjustment022"
  Placement = pos=(-33,0,0) rot=(0,0,1;0rad)
  shape: bbox 6.267 x 9.413 x 6.349 mm, 3 faces (baked)
FEATURE [App::Part] Springs_and_adjustment003  label="Springs and adjustment023"
  Group = -> [Part__Feature339,Part__Feature340,Part__Feature341,Part__Feature342,Part__Feature343]
  Origin = -> Origin122
FEATURE [Part::Feature] Part__Feature344  label="Springs and adjustment024"
  Placement = pos=(-44,0,0) rot=(0,0,1;0rad)
  shape: bbox 11 x 21.89 x 6.263 mm, 48 faces (baked)
FEATURE [Part::Feature] Part__Feature345  label="Springs and adjustment025"
  Placement = pos=(-44,0,0) rot=(0,0,1;0rad)
  shape: bbox 5.684 x 18.4 x 5.67 mm, 22 faces (baked)
FEATURE [Part::Feature] Part__Feature346  label="Springs and adjustment026"
  Placement = pos=(-44,0,0) rot=(0,0,1;0rad)
  shape: bbox 2.927 x 3.632 x 10.38 mm, 10 faces (baked)
FEATURE [Part::Feature] Part__Feature347  label="Springs and adjustment027"
  Placement = pos=(-44,0,0) rot=(0,0,1;0rad)
  shape: bbox 2.927 x 3.632 x 10.38 mm, 10 faces (baked)
FEATURE [Part::Feature] Part__Feature348  label="Springs and adjustment028"
  Placement = pos=(-44,0,0) rot=(0,0,1;0rad)
  shape: bbox 6.267 x 9.413 x 6.349 mm, 3 faces (baked)
FEATURE [App::Part] Springs_and_adjustment004  label="Springs and adjustment029"
  Group = -> [Part__Feature344,Part__Feature345,Part__Feature346,Part__Feature347,Part__Feature348]
  Origin = -> Origin123
FEATURE [Part::Feature] Part__Feature349  label="Springs and adjustment030"
  Placement = pos=(-55,0,0) rot=(0,0,1;0rad)
  shape: bbox 11 x 21.89 x 6.263 mm, 48 faces (baked)
FEATURE [Part::Feature] Part__Feature350  label="Springs and adjustment031"
  Placement = pos=(-55,0,0) rot=(0,0,1;0rad)
  shape: bbox 5.684 x 18.4 x 5.67 mm, 22 faces (baked)
FEATURE [Part::Feature] Part__Feature351  label="Springs and adjustment032"
  Placement = pos=(-55,0,0) rot=(0,0,1;0rad)
  shape: bbox 2.927 x 3.632 x 10.38 mm, 10 faces (baked)
FEATURE [Part::Feature] Part__Feature352  label="Springs and adjustment033"
  Placement = pos=(-55,0,0) rot=(0,0,1;0rad)
  shape: bbox 2.927 x 3.632 x 10.38 mm, 10 faces (baked)
FEATURE [Part::Feature] Part__Feature353  label="Springs and adjustment034"
  Placement = pos=(-55,0,0) rot=(0,0,1;0rad)
  shape: bbox 6.267 x 9.413 x 6.349 mm, 3 faces (baked)
FEATURE [App::Part] Springs_and_adjustment005  label="Springs and adjustment035"
  Group = -> [Part__Feature349,Part__Feature350,Part__Feature351,Part__Feature352,Part__Feature353]
  Origin = -> Origin124
FEATURE [App::Part] Harley_Benton_Tremolo_11mm_spacing_v14  label="Tremelo Block"
  Group = -> [Base,Springs_and_adjustment,Springs_and_adjustment001,Springs_and_adjustment002,Springs_and_adjustment003,Springs_and_adjustment004,Springs_and_adjustment005]
  Origin = -> Origin125
  Placement = pos=(186.9,286.1,44.2) rot=(0,0,1;0rad)
FEATURE [Part::Feature] Part__Feature354  label="Sustainiac Single Coil v1"
  shape: bbox 8.068 x 2.988 x 3.81 mm, 24 faces (baked)
FEATURE [Part::Feature] Part__Feature355  label="Sustainiac Single Coil v002"
  shape: bbox 71.31 x 14.38 x 19.24 mm, 334 faces (baked)
FEATURE [Part::Feature] Part__Feature356  label="Sustainiac Single Coil v003"
  shape: bbox 84.78 x 3.405 x 19.24 mm, 71 faces (baked)
FEATURE [Part::Feature] Part__Feature357  label="Sustainiac Single Coil v004"
  shape: bbox 70.45 x 2 x 17.77 mm, 50 faces (baked)
FEATURE [Part::Feature] Part__Feature359  label="Sustainiac Single Coil v006"
  shape: bbox 31.75 x 2.5 x 8 mm, 18 faces (baked)
FEATURE [Part::Feature] Part__Feature360  label="Sustainiac Single Coil v007"
  shape: bbox 7.237 x 0.25 x 2.518 mm, 67 faces (baked)
FEATURE [Part::Feature] Part__Feature361  label="Sustainiac Single Coil v008"
  shape: bbox 3.06 x 0.25 x 2.456 mm, 30 faces (baked)
FEATURE [Part::Feature] Part__Feature362  label="Sustainiac Single Coil v009"
  shape: bbox 7.113 x 0.25 x 2.608 mm, 75 faces (baked)
FEATURE [Part::Feature] Part__Feature364  label="Sustainiac Single Coil v011"
  shape: bbox 3.07 x 0.25 x 2.423 mm, 17 faces (baked)
FEATURE [Part::Feature] Part__Feature365  label="Sustainiac Single Coil v012"
  shape: bbox 2.792 x 0.25 x 2.535 mm, 49 faces (baked)
FEATURE [Sketcher::SketchObject] Sketch140  label="Tremelo underside "
  FullyConstrained = false
  MapMode = 5
  Placement = pos=(0,0,0) rot=(1,0,0;3.14159rad)
  Support = -> [Pocket012]
  sketch-geometry (4):
    g0: LineSegment StartX=189.9 StartY=-261.3 StartZ=0 EndX=267.9 EndY=-261.3 EndZ=0
    g1: LineSegment StartX=267.9 StartY=-261.3 StartZ=0 EndX=267.9 EndY=-287.3 EndZ=0
    g2: LineSegment StartX=267.9 StartY=-287.3 StartZ=0 EndX=189.9 EndY=-287.3 EndZ=0
    g3: LineSegment StartX=189.9 StartY=-287.3 StartZ=0 EndX=189.9 EndY=-261.3 EndZ=0
  constraints (10):
    c: Coincident(g0,g1)
    c: Coincident(g1,g2)
    c: Coincident(g2,g3)
    c: Coincident(g3,g0)
    c: Horizontal(g0)
    c: Horizontal(g2)
    c: Vertical(g1)
    c: Vertical(g3)
    c: DistanceX(g0,g0) = 78
    c: DistanceY(g1,g1) = 26
FEATURE [Part::Feature] Part__Feature358  label="Sustainiac Single Coil v005"
  shape: bbox 31.75 x 2.5 x 8 mm, 18 faces (baked)
FEATURE [Part::Feature] Part__Feature363  label="Sustainiac Single Coil v010"
  shape: bbox 5.798 x 0.25 x 2.596 mm, 47 faces (baked)
FEATURE [App::Part] Sustainiac_Single_Coil_v1  label="Neck Pickup"
  Group = -> [Part__Feature354,Part__Feature355,Part__Feature356,Part__Feature357,Part__Feature358,Part__Feature359,Part__Feature360,Part__Feature361,Part__Feature362,Part__Feature363,Part__Feature364,Part__Feature365]
  Origin = -> Origin126
  Placement = pos=(225,450.5,31.1) rot=(0,0.707107,0.707107;3.14159rad)
FEATURE [Part::Feature] Part__Feature366  label="Sustainiac Single Coil v013"
  shape: bbox 8.068 x 2.988 x 3.81 mm, 24 faces (baked)
FEATURE [Part::Feature] Part__Feature367  label="Sustainiac Single Coil v014"
  shape: bbox 71.31 x 14.38 x 19.24 mm, 334 faces (baked)
FEATURE [Part::Feature] Part__Feature368  label="Sustainiac Single Coil v015"
  shape: bbox 84.78 x 3.405 x 19.24 mm, 71 faces (baked)
FEATURE [Part::Feature] Part__Feature369  label="Sustainiac Single Coil v016"
  shape: bbox 70.45 x 2 x 17.77 mm, 50 faces (baked)
FEATURE [Part::Feature] Part__Feature370  label="Sustainiac Single Coil v017"
  shape: bbox 31.75 x 2.5 x 8 mm, 18 faces (baked)
FEATURE [Part::Feature] Part__Feature371  label="Sustainiac Single Coil v018"
  shape: bbox 31.75 x 2.5 x 8 mm, 18 faces (baked)
FEATURE [Part::Feature] Part__Feature372  label="Sustainiac Single Coil v019"
  shape: bbox 7.237 x 0.25 x 2.518 mm, 67 faces (baked)
FEATURE [Part::Feature] Part__Feature373  label="Sustainiac Single Coil v020"
  shape: bbox 3.06 x 0.25 x 2.456 mm, 30 faces (baked)
FEATURE [Part::Feature] Part__Feature374  label="Sustainiac Single Coil v021"
  shape: bbox 7.113 x 0.25 x 2.608 mm, 75 faces (baked)
FEATURE [Part::Feature] Part__Feature375  label="Sustainiac Single Coil v022"
  shape: bbox 5.798 x 0.25 x 2.596 mm, 47 faces (baked)
FEATURE [Part::Feature] Part__Feature376  label="Sustainiac Single Coil v023"
  shape: bbox 3.07 x 0.25 x 2.423 mm, 17 faces (baked)
FEATURE [Part::Feature] Part__Feature377  label="Sustainiac Single Coil v024"
  shape: bbox 2.792 x 0.25 x 2.535 mm, 49 faces (baked)
FEATURE [App::Part] Sustainiac_Single_Coil_v002  label="Middle Pickup"
  Group = -> [Part__Feature366,Part__Feature367,Part__Feature368,Part__Feature369,Part__Feature370,Part__Feature371,Part__Feature372,Part__Feature373,Part__Feature374,Part__Feature375,Part__Feature376,Part__Feature377]
  Origin = -> Origin127
  Placement = pos=(225,390.5,31.2) rot=(0,0.707107,0.707107;3.14159rad)
FEATURE [Mesh::Feature] Humbucker_Rahmen_LP_Hals  label="Humbucker frame"
  Placement = pos=(177.9,189.6,45.1) rot=(0,0,1;0rad)
FEATURE [Part::Feature] SH13  label="Humbucker Bridge Pickup"
  Placement = pos=(224.4,338,35.4) rot=(0,0,1;0rad)
  shape: bbox 91.78 x 77.39 x 19.15 mm, 363 faces, 0 solids (baked)
FEATURE [Sketcher::SketchObject] Sketch141  label="Tremelo Springs Pocket"
  FullyConstrained = false
  MapMode = 5
  Placement = pos=(0,0,0) rot=(1,0,0;3.14159rad)
  Support = -> [Pocket012]
  sketch-geometry (5):
    g0: LineSegment StartX=253.5 StartY=-385.3 StartZ=0 EndX=196.5 EndY=-385.3 EndZ=0
    g1: LineSegment StartX=196.5 StartY=-385.3 StartZ=0 EndX=196.5 EndY=-287.3 EndZ=0
    g2: LineSegment StartX=196.5 StartY=-287.3 StartZ=0 EndX=253.5 EndY=-287.3 EndZ=0
    g3: LineSegment StartX=253.5 StartY=-287.3 StartZ=0 EndX=253.5 EndY=-385.3 EndZ=0
    g4: LineSegment StartX=225 StartY=-70 StartZ=0 EndX=225 EndY=-310 EndZ=0
  constraints (11):
    c: Coincident(g0,g1)
    c: Coincident(g1,g2)
    c: Coincident(g2,g3)
    c: Coincident(g3,g0)
    c: Horizontal(g0)
    c: Horizontal(g2)
    c: Vertical(g1)
    c: Vertical(g3)
    c: DistanceY(g3,g3) = 98
    c: DistanceX(g0,g0) = 57
    c: Vertical(g4)
FEATURE [PartDesign::Pocket] Pocket029  label="Trem underside pocket"
  BaseFeature = -> Pocket012
  Direction = (0,0,1)
  Length = 39
  Length2 = 5
  Profile = -> Sketch140
  ReferenceAxis = -> Sketch140 [N_Axis]
  Type = 0
FEATURE [PartDesign::Pocket] Pocket030  label="Trem Spring pocket"
  BaseFeature = -> Pocket029
  Direction = (0,0,1)
  Length = 16
  Length2 = 5
  Profile = -> Sketch141
  ReferenceAxis = -> Sketch141 [N_Axis]
  Type = 0
FEATURE [Sketcher::SketchObject] Sketch142  label="Speaker Rear cover mount pocket"
  FullyConstrained = false
  MapMode = 5
  Placement = pos=(0,0,0) rot=(1,0,0;3.14159rad)
  Support = -> [Pocket030]
  sketch-geometry (1):
    g0: Circle CenterX=330 CenterY=-121 CenterZ=0 NormalX=0 NormalY=0 NormalZ=1 AngleXU=0 Radius=47
  constraints (1):
    c: Diameter(g0) = 94
FEATURE [PartDesign::Fillet] Fillet004  label="Neck Pickup Internal Edges"
  Base = -> Pocket030 [Edge321,Edge320,Edge323,Edge325]
  BaseFeature = -> Pocket030
  Radius = 6.35
  SupportTransform = false
  UseAllEdges = false
FEATURE [PartDesign::Fillet] Fillet005  label="Middle Pickup Internal Edges"
  Base = -> Fillet004 [Edge269,Edge270,Edge274,Edge272]
  BaseFeature = -> Fillet004
  Radius = 6.35
  SupportTransform = false
  UseAllEdges = false
FEATURE [PartDesign::Fillet] Fillet006  label="Tremolo Top Side Internal Edges"
  Base = -> Fillet005 [Edge233,Edge234,Edge238,Edge236]
  BaseFeature = -> Fillet005
  Radius = 6
  SupportTransform = false
  UseAllEdges = false
FEATURE [PartDesign::Fillet] Fillet007  label="Tremolo Underside Internal Edges"
  Base = -> Fillet006 [Edge323,Edge322,Edge319,Edge320]
  BaseFeature = -> Fillet006
  Radius = 6
  SupportTransform = false
  UseAllEdges = false
FEATURE [PartDesign::Fillet] Fillet008  label="Tremolo Spring Pocket Internal Edges"
  Base = -> Fillet007 [Edge209,Edge206]
  BaseFeature = -> Fillet007
  Radius = 6
  SupportTransform = false
  UseAllEdges = false
FEATURE [PartDesign::Fillet] Fillet009  label="RGB Clear Plate Mount Internal Edges"
  Base = -> Fillet008 [Edge379,Edge376,Edge374,Edge377]
  BaseFeature = -> Fillet008
  Radius = 6
  SupportTransform = false
  UseAllEdges = false
FEATURE [Part::Feature] Part__Feature378  label="Potentiometer"
  shape: bbox 17.63 x 17.86 x 8.502 mm, 73 faces (baked)
FEATURE [Part::Feature] Part__Feature379  label="Potentiometer001"
  shape: bbox 6.5 x 7.506 x 5.668 mm, 47 faces (baked)
FEATURE [Part::Feature] Part__Feature380  label="Potentiometer002"
  shape: bbox 5.992 x 5.992 x 9 mm, 102 faces (baked)
FEATURE [Part::Feature] Part__Feature381  label="Potentiometer003"
  shape: bbox 16.5 x 23.7 x 1.45 mm, 84 faces (baked)
FEATURE [App::Part] Potentiometer  label="Tone Pot"
  Group = -> [Part__Feature378,Part__Feature379,Part__Feature380,Part__Feature381]
  Origin = -> Origin128
  Placement = pos=(304.1,218.6,41.9) rot=(0,0,1;0rad)
FEATURE [Part::Feature] Part__Feature382  label="Potentiometer005"
  shape: bbox 17.63 x 17.86 x 8.502 mm, 73 faces (baked)
FEATURE [Part::Feature] Part__Feature383  label="Potentiometer006"
  shape: bbox 6.5 x 7.506 x 5.668 mm, 47 faces (baked)
FEATURE [Part::Feature] Part__Feature384  label="Potentiometer007"
  shape: bbox 5.992 x 5.992 x 9 mm, 102 faces (baked)
FEATURE [Part::Feature] Part__Feature385  label="Potentiometer008"
  shape: bbox 16.5 x 23.7 x 1.45 mm, 84 faces (baked)
FEATURE [App::Part] Potentiometer001  label="Vol Pot"
  Group = -> [Part__Feature382,Part__Feature383,Part__Feature384,Part__Feature385]
  Origin = -> Origin129
  Placement = pos=(304.1,188.6,42.6) rot=(0,0,1;0rad)
FEATURE [Mesh::Feature] Trem_Claw  label="Trem Claw"
  Placement = pos=(248.7,358.6,12.3) rot=(0.57735,-0.57735,0.57735;4.18879rad)
FEATURE [Mesh::Feature] Spring  label="Left Spring"
  Placement = pos=(246.7,308.2,4.9) rot=(1,0,0;4.71239rad)
FEATURE [Mesh::Feature] Spring001  label="Middle Spring"
  Placement = pos=(226.6,308.3,4.8) rot=(1,0,0;4.71239rad)
FEATURE [Mesh::Feature] Spring002  label="Right Spring"
  Placement = pos=(207.8,308.2,4.8) rot=(1,0,0;4.71239rad)
FEATURE [App::Part] Part035  label="Trem Springs and Claw"
  Group = -> [Trem_Claw,Spring,Spring001,Spring002]
  Origin = -> Origin132
  Placement = pos=(0,6.5,0) rot=(0,0,1;0rad)
FEATURE [App::Part] Part034  label="Tremelo Parts"
  Group = -> [Part035,Harley_Benton_Tremolo_11mm_spacing_v14]
  Origin = -> Origin131
FEATURE [PartDesign::Fillet] Fillet010  label="Controls Cavity plate mount edges"
  Base = -> Fillet009 [Edge277,Edge273,Edge275,Edge279]
  BaseFeature = -> Fillet009
  Radius = 6
  SupportTransform = false
  UseAllEdges = false
FEATURE [PartDesign::Fillet] Fillet011  label="Control Cavity internal Edges"
  Base = -> Fillet010 [Edge403,Edge397,Edge399,Edge401]
  BaseFeature = -> Fillet010
  Radius = 6
  SupportTransform = false
  UseAllEdges = false
FEATURE [PartDesign::Fillet] Fillet012  label="body Outer edges 1"
  Base = -> Fillet011 [Edge98,Edge252,Edge100,Edge256,Edge102,Edge260,Edge104,Edge264,Edge106,Edge269,Edge108,Edge277,Edge281,Edge110,Edge112,Edge285,Edge96,Edge248,Edge114,Edge289,Edge116,Edge118,Edge120,Edge293,Edge297,Edge301,Edge122,Edge305,Edge124,Edge309,Edge126,Edge312,Edge127,Edge314,Edge125,Edge311,Edge123,Edge307,Edge121,Edge303,+8 more]
  BaseFeature = -> Fillet011
  Radius = 5
  SupportTransform = false
  UseAllEdges = false
FEATURE [PartDesign::Fillet] Fillet013  label="body Outer edges 2"
  Base = -> Fillet012 [Edge21,Edge23,Edge25,Edge27,Edge170,Edge166,Edge162,Edge158,Edge17,Edge150,Edge154,Edge19,Edge29,Edge175,Edge425,Edge434,Edge15,Edge145,Edge142,Edge13,Edge7,Edge130,Edge9,Edge11,Edge138,Edge134,Edge5,Edge3,Edge1,Edge109,Edge126,Edge121,Edge117]
  BaseFeature = -> Fillet012
  Radius = 5
  SupportTransform = false
  UseAllEdges = false
FEATURE [PartDesign::Fillet] Fillet014  label="body Outer edges 3"
  Base = -> Fillet013 [Edge208]
  BaseFeature = -> Fillet013
  Radius = 5
  SupportTransform = false
  UseAllEdges = false
FEATURE [PartDesign::Fillet] Fillet015  label="body Outer edges 4"
  Base = -> Fillet014 [Edge142,Edge146]
  BaseFeature = -> Fillet014
  Radius = 6.35
  SupportTransform = false
  UseAllEdges = false
FEATURE [Sketcher::SketchObject] Sketch143  label="control plate mount pocket002"
  FullyConstrained = false
  MapMode = 5
  Placement = pos=(0,0,45) rot=(0,0,1;0rad)
  sketch-geometry (6):
    g0: LineSegment StartX=267.9 StartY=263.3 StartZ=0 EndX=267.9 EndY=243.3 EndZ=0
    g1: LineSegment StartX=267.9 StartY=243.3 StartZ=0 EndX=272.9 EndY=243.3 EndZ=0
    g2: LineSegment StartX=282 StartY=258 StartZ=0 EndX=337 EndY=258 EndZ=0
    g3: LineSegment StartX=282 StartY=258 StartZ=0 EndX=282 EndY=172 EndZ=0
    g4: LineSegment StartX=282 StartY=172 StartZ=0 EndX=365.925 EndY=172 EndZ=0
    g5: LineSegment StartX=365.925 StartY=172 StartZ=0 EndX=337 EndY=258 EndZ=0
  constraints (12):
    c: Vertical(g0)
    c: Coincident(g1,g0)
    c: Horizontal(g1)
    c: Horizontal(g2)
    c: Coincident(g3,g2)
    c: Vertical(g3)
    c: DistanceY(g3,g3) = 86
    c: Coincident(g4,g3)
    c: Horizontal(g4)
    c: Coincident(g5,g4)
    c: Coincident(g5,g2)
    c: Distance(g5) = 90.7339
FEATURE [PartDesign::Pad] Pad004  label="Main Plate"
  Direction = (0,0,1)
  Length = 3
  Length2 = 10
  Placement = pos=(0,0,45) rot=(0,0,1;0rad)
  Profile = -> Sketch143
  ReferenceAxis = -> Sketch143 [N_Axis]
  Type = 0
FEATURE [PartDesign::Fillet] Fillet016  label="Corner edges "
  Base = -> Pad004 [Edge5,Edge8,Edge1,Edge2]
  BaseFeature = -> Pad004
  Placement = pos=(0,0,45) rot=(0,0,1;0rad)
  Radius = 6
  SupportTransform = false
  UseAllEdges = false
FEATURE [Sketcher::SketchObject] Sketch144  label="Pot holes"
  FullyConstrained = false
  MapMode = 5
  Placement = pos=(0,0,48) rot=(0,0,1;0rad)
  Support = -> [Fillet016]
  sketch-geometry (3):
    g0: Circle CenterX=302 CenterY=230 CenterZ=0 NormalX=0 NormalY=0 NormalZ=1 AngleXU=0 Radius=3.75
    g1: LineSegment StartX=310.5 StartY=200 StartZ=0 EndX=302 EndY=200 EndZ=0
    g2: Circle CenterX=302 CenterY=200 CenterZ=0 NormalX=0 NormalY=0 NormalZ=1 AngleXU=0 Radius=3.75
  constraints (4):
    c: Diameter(g0) = 7.5
    c: Horizontal(g1)
    c: Coincident(g2,g1)
    c: Diameter(g2) = 7.5
FEATURE [PartDesign::Pocket] Pocket031  label="Potentiometer holes"
  BaseFeature = -> Fillet016
  Direction = (0,0,-1)
  Length = 5
  Length2 = 5
  Placement = pos=(0,0,45) rot=(0,0,1;0rad)
  Profile = -> Sketch144
  ReferenceAxis = -> Sketch144 [N_Axis]
  Type = 0
FEATURE [Sketcher::SketchObject] Sketch145  label="Selector Switch Slit and mounting holes"
  FullyConstrained = false
  MapMode = 5
  Placement = pos=(0,0,48) rot=(0,0,1;0rad)
  Support = -> [Pocket031]
  sketch-geometry (18):
    g0: LineSegment StartX=326.216 StartY=240.209 StartZ=0 EndX=325.616 EndY=240.209 EndZ=0
    g1: LineSegment StartX=326.216 StartY=240.209 StartZ=0 EndX=320.985 EndY=238.509 EndZ=0
    g2: LineSegment StartX=320.985 StartY=238.509 StartZ=0 EndX=322.023 EndY=235.313 EndZ=0
    g3: Circle CenterX=322.023 CenterY=235.313 CenterZ=0 NormalX=0 NormalY=0 NormalZ=1 AngleXU=0 Radius=1.75
    g4: LineSegment StartX=341.048 StartY=194.558 StartZ=0 EndX=339.648 EndY=194.558 EndZ=0
    g5: LineSegment StartX=341.048 StartY=194.558 StartZ=0 EndX=335.818 EndY=192.858 EndZ=0
    g6: LineSegment StartX=335.818 StartY=192.858 StartZ=0 EndX=334.779 EndY=196.054 EndZ=0
    g7: Circle CenterX=334.779 CenterY=196.054 CenterZ=0 NormalX=0 NormalY=0 NormalZ=1 AngleXU=0 Radius=1.75
    g8: LineSegment StartX=322.023 StartY=235.313 StartZ=0 EndX=334.779 EndY=196.054 EndZ=0
    g9: LineSegment StartX=334.238 StartY=197.718 StartZ=0 EndX=333.263 EndY=200.72 EndZ=0
    g10: LineSegment StartX=333.263 StartY=200.72 StartZ=0 EndX=334.214 EndY=201.029 EndZ=0
    g11: LineSegment StartX=322.564 StartY=233.649 StartZ=0 EndX=323.538 EndY=230.65 EndZ=0
    g12: LineSegment StartX=334.238 StartY=197.718 StartZ=0 EndX=333.263 EndY=200.72 EndZ=0
    g13: LineSegment StartX=334.214 StartY=201.029 StartZ=0 EndX=324.49 EndY=230.959 EndZ=0
    g14: LineSegment StartX=333.263 StartY=200.72 StartZ=0 EndX=332.312 EndY=200.412 EndZ=0
    g15: LineSegment StartX=322.587 StartY=230.341 StartZ=0 EndX=332.312 EndY=200.412 EndZ=0
    g16: LineSegment StartX=323.538 StartY=230.65 StartZ=0 EndX=322.587 EndY=230.341 EndZ=0
    g17: LineSegment StartX=323.538 StartY=230.65 StartZ=0 EndX=324.49 EndY=230.959 EndZ=0
  constraints (44):
    c: Horizontal(g0)
    c: Coincident(g1,g0)
    c: DistanceX(g0,g0) = 0.6
    c: Angle(g0,g1) = 0.314159
    c: Distance(g1) = 5.5
    c: Coincident(g2,g1)
    c: Coincident(g3,g2)
    c: Diameter(g3) = 3.5
    c: Angle(g2,g0) = 1.25664
    c: Distance(g2) = 3.36
    c: Horizontal(g4)
    c: Coincident(g5,g4)
    c: DistanceX(g4,g4) = 1.4
    c: Distance(g5) = 5.5
    c: Angle(g4,g5) = 0.314159
    c: Coincident(g6,g5)
    c: Distance(g6) = 3.36
    c: Angle(g6,g4) = 1.25664
    c: Coincident(g7,g6)
    c: Diameter(g7) = 3.5
    c: Coincident(g8,g3)
    c: Coincident(g8,g7)
    c: PointOnObject(g9,g7)
    c: PointOnObject(g9,g8)
    c: Coincident(g9,g10)
    c: PointOnObject(g11,g8)
    c: PointOnObject(g11,g8)
    c: Distance(g11) = 3.15373
    c: Coincident(g12,g9)
    c: Coincident(g12,g10)
    c: Distance(g12) = 3.1567
    c: Distance(g10) = 1
    c: Angle(g12,g10) = 1.5708
    c: Coincident(g13,g10)
    c: Coincident(g14,g10)
    c: Distance(g14) = 1
    c: Angle(g14,g12) = 1.5708
    c: Coincident(g15,g14)
    c: Distance(g13) = 31.4696
    c: Coincident(g16,g11)
    c: Coincident(g16,g15)
    c: Coincident(g17,g16)
    c: Coincident(g17,g13)
    c: Distance(g16) = 1
FEATURE [Sketcher::SketchObject] Sketch152  label="IO Pocket"
  FullyConstrained = false
  MapMode = 5
  Placement = pos=(73.7302,122.096,0) rot=(0.930428,-0.259137,-0.259137;1.64285rad)
  Support = -> [Fillet015]
  sketch-geometry (4):
    g0: LineSegment StartX=-12.9 StartY=35 StartZ=0 EndX=87.1 EndY=35 EndZ=0
    g1: LineSegment StartX=87.1 StartY=35 StartZ=0 EndX=87.1 EndY=10 EndZ=0
    g2: LineSegment StartX=87.1 StartY=10 StartZ=0 EndX=-12.9 EndY=10 EndZ=0
    g3: LineSegment StartX=-12.9 StartY=10 StartZ=0 EndX=-12.9 EndY=35 EndZ=0
  constraints (10):
    c: Coincident(g0,g1)
    c: Coincident(g1,g2)
    c: Coincident(g2,g3)
    c: Coincident(g3,g0)
    c: Horizontal(g0)
    c: Horizontal(g2)
    c: Vertical(g1)
    c: Vertical(g3)
    c: DistanceX(g0,g0) = 100
    c: DistanceY(g3,g3) = 25
FEATURE [Sketcher::SketchObject] Sketch153  label="IO Plate Mounting Pocket"
  FullyConstrained = false
  MapMode = 5
  Placement = pos=(73.7302,122.096,0) rot=(0.930428,-0.259137,-0.259137;1.64285rad)
  Support = -> [Fillet015]
  sketch-geometry (4):
    g0: LineSegment StartX=-23 StartY=39 StartZ=0 EndX=97 EndY=39 EndZ=0
    g1: LineSegment StartX=97 StartY=39 StartZ=0 EndX=97 EndY=6 EndZ=0
    g2: LineSegment StartX=97 StartY=6 StartZ=0 EndX=-23 EndY=6 EndZ=0
    g3: LineSegment StartX=-23 StartY=6 StartZ=0 EndX=-23 EndY=39 EndZ=0
  constraints (9):
    c: Coincident(g0,g1)
    c: Coincident(g1,g2)
    c: Coincident(g2,g3)
    c: Coincident(g3,g0)
    c: Horizontal(g0)
    c: Horizontal(g2)
    c: Vertical(g1)
    c: Vertical(g3)
    c: DistanceX(g0,g0) = 120
FEATURE [PartDesign::Pocket] Pocket032  label="IO section Pocket"
  BaseFeature = -> Fillet015
  Direction = (0.51693,0.856028,0)
  Length = 40
  Length2 = 5
  Profile = -> Sketch152
  ReferenceAxis = -> Sketch152 [N_Axis]
  Type = 0
FEATURE [PartDesign::Pocket] Pocket033  label="IO Plate Mounting lip Pocket"
  BaseFeature = -> Pocket032
  Direction = (0.51693,0.856028,0)
  Length = 3
  Length2 = 5
  Profile = -> Sketch153
  ReferenceAxis = -> Sketch153 [N_Axis]
  Type = 0
FEATURE [PartDesign::Fillet] Fillet017  label="IO Pocket internal Edges"
  Base = -> Pocket033 [Edge655,Edge658,Edge656,Edge653]
  BaseFeature = -> Pocket033
  Radius = 6
  SupportTransform = false
  UseAllEdges = false
FEATURE [PartDesign::Fillet] Fillet018  label="IO plate Internal Edges"
  Base = -> Fillet017 [Edge34,Edge32,Edge29,Edge30]
  BaseFeature = -> Fillet017
  Radius = 6
  SupportTransform = false
  UseAllEdges = false
FEATURE [Sketcher::SketchObject] Sketch155  label="Wire channels Pocket"
  FullyConstrained = false
  MapMode = 5
  Placement = pos=(0,0,0) rot=(1,0,0;3.14159rad)
  Support = -> [Fillet018]
  sketch-geometry (35):
    g0: LineSegment StartX=137.085 StartY=-133.454 StartZ=0 EndX=137.085 EndY=-200.021 EndZ=0
    g1: LineSegment StartX=156.976 StartY=-121.576 StartZ=0 EndX=156.976 EndY=-200 EndZ=0
    g2: LineSegment StartX=137.085 StartY=-200.021 StartZ=0 EndX=150.067 EndY=-239.979 EndZ=0
    g3: LineSegment StartX=156.976 StartY=-200 StartZ=0 EndX=163.474 EndY=-220 EndZ=0
    g4: LineSegment StartX=101.467 StartY=-402.5 StartZ=0 EndX=101.467 EndY=-397.5 EndZ=0
    g5: LineSegment StartX=101.467 StartY=-397.5 StartZ=0 EndX=150.067 EndY=-348.9 EndZ=0
    g6: LineSegment StartX=150.067 StartY=-348.9 StartZ=0 EndX=150.067 EndY=-239.979 EndZ=0
    g7: LineSegment StartX=130.4 StartY=-402.5 StartZ=0 EndX=130.4 EndY=-397.5 EndZ=0
    g8: LineSegment StartX=130.4 StartY=-397.5 StartZ=0 EndX=170 EndY=-357.835 EndZ=0
    g9: LineSegment StartX=170 StartY=-357.835 StartZ=0 EndX=170 EndY=-240 EndZ=0
    g10: LineSegment StartX=163.474 StartY=-220 StartZ=0 EndX=200 EndY=-220 EndZ=0
    g11: LineSegment StartX=200 StartY=-220 StartZ=0 EndX=200 EndY=-200 EndZ=0
    g12: LineSegment StartX=220 StartY=-200 StartZ=0 EndX=220 EndY=-220 EndZ=0
    g13: LineSegment StartX=101.467 StartY=-402.5 StartZ=0 EndX=130.4 EndY=-402.5 EndZ=0
    g14: LineSegment StartX=200 StartY=-200 StartZ=0 EndX=220 EndY=-200 EndZ=0
    g15: LineSegment StartX=156.976 StartY=-121.576 StartZ=0 EndX=156.976 EndY=-115 EndZ=0
    g16: LineSegment StartX=137.085 StartY=-133.454 StartZ=0 EndX=137.085 EndY=-126.91 EndZ=0
    g17: LineSegment StartX=137.085 StartY=-126.91 StartZ=0 EndX=156.976 EndY=-115 EndZ=0
    g18: LineSegment StartX=254 StartY=-454.998 StartZ=0 EndX=254 EndY=-385.013 EndZ=0
    g19: LineSegment StartX=254 StartY=-385.013 StartZ=0 EndX=260 EndY=-369.99 EndZ=0
    g20: LineSegment StartX=260 StartY=-369.99 StartZ=0 EndX=255.25 EndY=-344.003 EndZ=0
    g21: LineSegment StartX=279 StartY=-454.998 StartZ=0 EndX=279 EndY=-384.9 EndZ=0
    g22: LineSegment StartX=295.012 StartY=-275.002 StartZ=0 EndX=279 EndY=-384.9 EndZ=0
    g23: LineSegment StartX=282 StartY=-274.99 StartZ=0 EndX=255.25 EndY=-332.21 EndZ=0
    g24: LineSegment StartX=255.25 StartY=-344.003 StartZ=0 EndX=255.25 EndY=-332.21 EndZ=0
    g25: LineSegment StartX=254 StartY=-454.998 StartZ=0 EndX=254 EndY=-459.998 EndZ=0
    g26: LineSegment StartX=279 StartY=-454.998 StartZ=0 EndX=279 EndY=-459.998 EndZ=0
    g27: LineSegment StartX=279 StartY=-459.998 StartZ=0 EndX=254 EndY=-459.998 EndZ=0
    g28: LineSegment StartX=290 StartY=-220 StartZ=0 EndX=220 EndY=-220 EndZ=0
    g29: LineSegment StartX=170 StartY=-240 StartZ=0 EndX=290 EndY=-240 EndZ=0
    g30: LineSegment StartX=290 StartY=-240 StartZ=0 EndX=290 EndY=-220 EndZ=0
    g31: LineSegment StartX=317.382 StartY=-256 StartZ=0 EndX=295.012 EndY=-275.002 EndZ=0
    g32: LineSegment StartX=307.382 StartY=-251 StartZ=0 EndX=282 EndY=-274.99 EndZ=0
    g33: LineSegment StartX=317.382 StartY=-256 StartZ=0 EndX=317.382 EndY=-251 EndZ=0
    g34: LineSegment StartX=307.382 StartY=-251 StartZ=0 EndX=317.382 EndY=-251 EndZ=0
  constraints (94):
    c: Vertical(g0)
    c: Vertical(g1)
    c: Coincident(g2,g0)
    c: Coincident(g3,g1)
    c: Angle(g3,g1) = 2.82743
    c: Angle(g2,g0) = 2.82743
    c: Vertical(g4)
    c: Coincident(g5,g4)
    c: Angle(g4,g5) = 2.35619
    c: DistanceY(g4,g4) = 5
    c: Coincident(g6,g5)
    c: Coincident(g6,g2)
    c: Vertical(g6)
    c: Vertical(g7)
    c: DistanceY(g7,g7) = 5
    c: Coincident(g8,g7)
    c: Coincident(g9,g8)
    c: Vertical(g9)
    c: Coincident(g10,g3)
    c: Horizontal(g10)
    c: Coincident(g11,g10)
    c: Vertical(g11)
    c: Vertical(g12)
    c: Coincident(g13,g4)
    c: Coincident(g13,g7)
    c: Horizontal(g13)
    c: Distance(g5) = 68.7308
    c: Distance(g8) = 56.0489
    c: Distance(g9) = 117.835
    c: Distance(g6) = 108.921
    c: Distance(g2) = 42.0134
    c: Distance(g0) = 66.5671
    c: Distance(g1) = 78.4237
    c: Distance(g3) = 21.0293
    c: Distance(g10) = 36.5256
    c: Distance(g11) = 20
    c: DistanceX(g13,g13) = 28.9326
    c: Coincident(g14,g11)
    c: Coincident(g14,g12)
    c: Horizontal(g14)
    c: DistanceX(g14,g14) = 20
    c: Coincident(g15,g1)
    c: Vertical(g15)
    c: DistanceY(g15,g15) = 6.57624
    c: Coincident(g16,g0)
    c: Vertical(g16)
    c: DistanceY(g16,g16) = 6.5444
    c: Coincident(g17,g16)
    c: Coincident(g17,g15)
    c: Vertical(g18)
    c: Coincident(g18,g19)
    c: Coincident(g19,g20)
    c: Vertical(g21)
    c: Coincident(g22,g21)
    c: Distance(g22) = 111.059
    c: Distance(g23) = 63.1639
    c: Distance(g20) = 26.4172
    c: Distance(g19) = 16.1774
    c: Distance(g18) = 69.9845
    c: Distance(g21) = 70.0978
    c: Coincident(g24,g20)
    c: Coincident(g24,g23)
    c: Vertical(g24)
    c: Distance(g24) = 11.7934
    c: Coincident(g25,g18)
    c: Vertical(g25)
    c: Coincident(g26,g21)
    c: Vertical(g26)
    c: Coincident(g27,g26)
    c: Coincident(g27,g25)
    c: Horizontal(g27)
    c: Distance(g25) = 5
    c: Distance(g27) = 25
    c: Distance(g26) = 5
    c: Coincident(g28,g12)
    c: Horizontal(g28)
    c: Coincident(g29,g9)
    c: Horizontal(g29)
    c: Coincident(g30,g29)
    c: Coincident(g30,g28)
    c: Vertical(g30)
    c: DistanceX(g28,g28) = 70
    c: DistanceX(g29,g29) = 120
    c: DistanceY(g30,g30) = 20
    c: Coincident(g31,g22)
    c: Distance(g31) = 29.351
    c: Coincident(g32,g23)
    c: Coincident(g33,g31)
    c: Vertical(g33)
    c: Distance(g32) = 34.9253
    c: Distance(g33) = 5
    c: Coincident(g34,g32)
    c: Coincident(g34,g33)
    c: Horizontal(g34)
FEATURE [Sketcher::SketchObject] Sketch156  label="IO Plate Mounting Pocket001"
  FullyConstrained = false
  MapMode = 5
  Placement = pos=(73.7302,122.096,0) rot=(0.930428,-0.259137,-0.259137;1.64285rad)
  Support = -> [Fillet015]
  sketch-geometry (4):
    g0: LineSegment StartX=-23 StartY=39 StartZ=0 EndX=97 EndY=39 EndZ=0
    g1: LineSegment StartX=97 StartY=39 StartZ=0 EndX=97 EndY=6 EndZ=0
    g2: LineSegment StartX=97 StartY=6 StartZ=0 EndX=-23 EndY=6 EndZ=0
    g3: LineSegment StartX=-23 StartY=6 StartZ=0 EndX=-23 EndY=39 EndZ=0
  constraints (9):
    c: Coincident(g0,g1)
    c: Coincident(g1,g2)
    c: Coincident(g2,g3)
    c: Coincident(g3,g0)
    c: Horizontal(g0)
    c: Horizontal(g2)
    c: Vertical(g1)
    c: Vertical(g3)
    c: DistanceX(g0,g0) = 120
FEATURE [PartDesign::Body] Body016  label="IO Plate"
  Group = -> [Sketch156]
  Origin = -> Origin134
  Placement = pos=(1.5,2.5,0) rot=(0,0,1;0rad)
FEATURE [Part::Extrusion] Extrude051  label="Extrude080"
  Base = -> Sketch156
  Dir = (-0.51693,-0.856028,3e-16)
  DirMode = 2
  FaceMakerClass = Part::FaceMakerBullseye
  LengthFwd = 3
  LengthRev = 0
  Solid = true
  Symmetric = false
FEATURE [PartDesign::FeatureBase] BaseFeature018
  BaseFeature = -> Extrude051
FEATURE [PartDesign::Fillet] Fillet019
  Base = -> BaseFeature018 [Edge1,Edge8,Edge5,Edge2]
  BaseFeature = -> BaseFeature018
  Radius = 6
  SupportTransform = false
  UseAllEdges = false
FEATURE [Sketcher::SketchObject] Sketch157  label="IO plate jack Holes"
  FullyConstrained = false
  MapMode = 5
  Placement = pos=(72.1794,119.528,-5.45e-14) rot=(0.930428,-0.259137,-0.259137;1.64285rad)
  Support = -> [Fillet019]
  sketch-geometry (15):
    g0: LineSegment StartX=-13 StartY=38.9592 StartZ=0 EndX=-13 EndY=22.9592 EndZ=0
    g1: LineSegment StartX=-23 StartY=23 StartZ=0 EndX=-13 EndY=23 EndZ=0
    g2: LineSegment StartX=-13 StartY=23 StartZ=0 EndX=-3 EndY=23 EndZ=0
    g3: LineSegment StartX=7 StartY=23 StartZ=0 EndX=17 EndY=23 EndZ=0
    g4: LineSegment StartX=37.0325 StartY=23 StartZ=0 EndX=27 EndY=23 EndZ=0
    g5: LineSegment StartX=57 StartY=23 StartZ=0 EndX=67 EndY=23 EndZ=0
    g6: LineSegment StartX=77 StartY=23 StartZ=0 EndX=86 EndY=23 EndZ=0
    g7: LineSegment StartX=2 StartY=23 StartZ=0 EndX=2 EndY=22 EndZ=0
    g8: LineSegment StartX=22 StartY=23 StartZ=0 EndX=22 EndY=22 EndZ=0
    g9: LineSegment StartX=47 StartY=23 StartZ=0 EndX=47 EndY=22 EndZ=0
    g10: LineSegment StartX=72 StartY=23 StartZ=0 EndX=72 EndY=22 EndZ=0
    g11: Circle CenterX=2 CenterY=23 CenterZ=0 NormalX=0 NormalY=0 NormalZ=1 AngleXU=0 Radius=4
    g12: Circle CenterX=22 CenterY=23 CenterZ=0 NormalX=0 NormalY=0 NormalZ=1 AngleXU=0 Radius=4
    g13: Circle CenterX=47 CenterY=23 CenterZ=0 NormalX=0 NormalY=0 NormalZ=1 AngleXU=0 Radius=5
    g14: Circle CenterX=72 CenterY=23 CenterZ=0 NormalX=0 NormalY=0 NormalZ=1 AngleXU=0 Radius=4
  constraints (20):
    c: Vertical(g0)
    c: Horizontal(g1)
    c: Coincident(g2,g1)
    c: Horizontal(g2)
    c: Horizontal(g3)
    c: Horizontal(g4)
    c: Horizontal(g5)
    c: Horizontal(g6)
    c: Vertical(g7)
    c: Vertical(g8)
    c: Vertical(g9)
    c: Vertical(g10)
    c: Coincident(g11,g7)
    c: Coincident(g12,g8)
    c: Coincident(g13,g9)
    c: Coincident(g14,g10)
    c: Diameter(g14) = 8
    c: Diameter(g11) = 8
    c: Diameter(g12) = 8
    c: Diameter(g13) = 10
FEATURE [PartDesign::Pocket] Pocket034
  Direction = (0.51693,0.856028,-2e-16)
  Length = 3
  Length2 = 5
  Profile = -> Sketch157
  ReferenceAxis = -> Sketch157 [N_Axis]
  Type = 0
FEATURE [Part::Feature] Part__Feature386  label="FenderJack_Cylinder"
  Placement = pos=(5.05896,3.4811,15.0685) rot=(0,0,1;0rad)
  shape: bbox 15.24 x 10.78 x 15.24 mm, 76 faces (baked)
FEATURE [Part::Feature] Part__Feature387  label="FenderJack_UpperTab"
  Placement = pos=(5.05896,13.4506,15.0685) rot=(0,-1,0;0.523599rad)
  shape: bbox 16.87 x 8.606 x 12.95 mm, 28 faces (baked)
FEATURE [Part::Feature] Part__Feature388  label="FenderJack_UpperSiPlate"
  Placement = pos=(5.05896,12.4346,15.0685) rot=(0,0,1;0rad)
  shape: bbox 19.05 x 1.016 x 18.14 mm, 44 faces (baked)
FEATURE [Part::Feature] Part__Feature389  label="FenderJack_LowerTab"
  Placement = pos=(5.05896,12.1806,15.0685) rot=(0,1,0;3.14159rad)
  shape: bbox 17.49 x 22.56 x 16.82 mm, 64 faces (baked)
FEATURE [Part::Feature] Part__Feature390  label="FenderJack_LowerSiPlate"
  Placement = pos=(5.05896,11.1646,15.0685) rot=(0,0,1;0rad)
  shape: bbox 17.78 x 1.016 x 17.78 mm, 6 faces (baked)
FEATURE [App::Part] FenderJack  label="1/4 Aux Out Jack"
  Group = -> [Part__Feature386,Part__Feature387,Part__Feature388,Part__Feature389,Part__Feature390]
  Origin = -> Origin136
  Placement = pos=(106.054,94.5608,8) rot=(0,0,1;5.74213rad)
FEATURE [App::Part] Part036  label="IO Plate Peripherals"
  Group = -> [FenderJack]
  Origin = -> Origin137
FEATURE [Part::Feature] Part__Feature391  label="Fret Wire"
  shape: bbox 2.413 x 56.15 x 6.018 mm, 609 faces (baked)
FEATURE [Part::Feature] Part__Feature392  label="Fret Wire001"
  shape: bbox 2.413 x 55.75 x 5.982 mm, 599 faces (baked)
FEATURE [Part::Feature] Part__Feature393  label="Fret Wire002"
  shape: bbox 2.413 x 55.42 x 5.943 mm, 600 faces (baked)
FEATURE [Part::Feature] Part__Feature394  label="Fret Wire003"
  shape: bbox 2.413 x 55.17 x 5.903 mm, 601 faces (baked)
FEATURE [Part::Feature] Part__Feature395  label="Fret Wire004"
  shape: bbox 2.413 x 54.78 x 5.861 mm, 589 faces (baked)
FEATURE [Part::Feature] Part__Feature396  label="Fret Wire005"
  shape: bbox 2.413 x 54.38 x 5.816 mm, 589 faces (baked)
FEATURE [Part::Feature] Part__Feature397  label="Fret Wire006"
  shape: bbox 2.413 x 53.97 x 5.768 mm, 588 faces (baked)
FEATURE [Part::Feature] Part__Feature398  label="Fret Wire007"
  shape: bbox 2.413 x 53.5 x 5.726 mm, 580 faces (baked)
FEATURE [Part::Feature] Part__Feature399  label="Fret Wire008"
  shape: bbox 2.413 x 53.05 x 5.675 mm, 571 faces (baked)
FEATURE [Part::Feature] Part__Feature400  label="Fret Wire009"
  shape: bbox 2.413 x 52.57 x 5.621 mm, 571 faces (baked)
FEATURE [Part::Feature] Part__Feature401  label="Fret Wire010"
  shape: bbox 2.413 x 52.05 x 5.564 mm, 558 faces (baked)
FEATURE [Part::Feature] Part__Feature402  label="Fret Wire011"
  shape: bbox 2.413 x 51.51 x 5.504 mm, 552 faces (baked)
FEATURE [Part::Feature] Part__Feature403  label="Fret Wire012"
  shape: bbox 2.413 x 50.95 x 5.442 mm, 551 faces (baked)
FEATURE [Part::Feature] Part__Feature404  label="Fret Wire013"
  shape: bbox 2.413 x 50.34 x 5.376 mm, 539 faces (baked)
FEATURE [Part::Feature] Part__Feature405  label="Fret Wire014"
  shape: bbox 2.413 x 49.69 x 5.315 mm, 539 faces (baked)
FEATURE [Part::Feature] Part__Feature406  label="Fret Wire015"
  shape: bbox 2.413 x 49.01 x 5.244 mm, 533 faces (baked)
FEATURE [Part::Feature] Part__Feature407  label="Fret Wire016"
  shape: bbox 2.413 x 48.29 x 5.17 mm, 525 faces (baked)
FEATURE [Part::Feature] Part__Feature408  label="Fret Wire017"
  shape: bbox 2.413 x 47.61 x 5.093 mm, 519 faces (baked)
FEATURE [Part::Feature] Part__Feature409  label="Fret Wire018"
  shape: bbox 2.413 x 46.72 x 5.012 mm, 501 faces (baked)
FEATURE [Part::Feature] Part__Feature410  label="Fret Wire019"
  shape: bbox 2.413 x 45.96 x 4.927 mm, 496 faces (baked)
FEATURE [Part::Feature] Part__Feature411  label="Fret Wire020"
  shape: bbox 2.413 x 44.96 x 4.839 mm, 485 faces (baked)
FEATURE [Part::Feature] Part__Feature412  label="Fret Wire021"
  shape: bbox 2.413 x 44.06 x 4.757 mm, 482 faces (baked)
FEATURE [App::Part] Fret_Wire  label="Fret Wire022"
  Group = -> [Part__Feature391,Part__Feature392,Part__Feature393,Part__Feature394,Part__Feature395,Part__Feature396,Part__Feature397,Part__Feature398,Part__Feature399,Part__Feature400,Part__Feature401,Part__Feature402,Part__Feature403,Part__Feature404,Part__Feature405,Part__Feature406,Part__Feature407,Part__Feature408,Part__Feature409,Part__Feature410,Part__Feature411,Part__Feature412]
  Origin = -> Origin138
FEATURE [App::Part] Fret_Wire_Set  label="Fret Wire Set"
  Group = -> [Fret_Wire]
  Origin = -> Origin139
  Placement = pos=(369.946,0,88.8272) rot=(0,0,1;0rad)
FEATURE [Part::Feature] Part__Feature413  label="COMPOUND079"
  shape: bbox 656.6 x 94.69 x 37.28 mm, 125 faces (baked)
FEATURE [Part::Feature] Part__Feature414  label="COMPOUND080"
  shape: bbox 488 x 55.72 x 8.992 mm, 222 faces (baked)
FEATURE [Part::Feature] Part__Feature415  label="COMPOUND081"
  shape: bbox 390.2 x 7.073 x 12.95 mm, 16 faces (baked)
FEATURE [Part::Feature] Part__Feature416  label="COMPOUND082"
  shape: bbox 6.353 x 6.353 x 1.143 mm, 3 faces (baked)
FEATURE [Part::Feature] Part__Feature417  label="COMPOUND083"
  shape: bbox 6.353 x 6.353 x 1.143 mm, 3 faces (baked)
FEATURE [Part::Feature] Part__Feature418  label="COMPOUND084"
  shape: bbox 6.353 x 6.353 x 1.143 mm, 3 faces (baked)
FEATURE [Part::Feature] Part__Feature419  label="COMPOUND085"
  shape: bbox 6.353 x 6.353 x 1.143 mm, 3 faces (baked)
FEATURE [Part::Feature] Part__Feature420  label="COMPOUND086"
  shape: bbox 6.353 x 6.353 x 1.023 mm, 3 faces (baked)
FEATURE [Part::Feature] Part__Feature421  label="COMPOUND087"
  shape: bbox 6.353 x 6.353 x 1.023 mm, 3 faces (baked)
FEATURE [Part::Feature] Part__Feature422  label="COMPOUND088"
  shape: bbox 6.353 x 6.353 x 1.143 mm, 3 faces (baked)
FEATURE [Part::Feature] Part__Feature423  label="COMPOUND089"
  shape: bbox 6.353 x 6.353 x 1.143 mm, 3 faces (baked)
FEATURE [Part::Feature] Part__Feature424  label="COMPOUND090"
  shape: bbox 6.353 x 6.353 x 1.143 mm, 3 faces (baked)
FEATURE [Part::Feature] Part__Feature425  label="COMPOUND091"
  shape: bbox 6.353 x 6.353 x 1.143 mm, 3 faces (baked)
FEATURE [Part::Feature] Part__Feature426  label="COMPOUND092"
  shape: bbox 1.588 x 6.339 x 1.588 mm, 3 faces (baked)
FEATURE [Part::Feature] Part__Feature427  label="COMPOUND093"
  shape: bbox 1.588 x 6.339 x 1.588 mm, 3 faces (baked)
FEATURE [Part::Feature] Part__Feature428  label="COMPOUND094"
  shape: bbox 1.588 x 6.339 x 1.588 mm, 3 faces (baked)
FEATURE [Part::Feature] Part__Feature429  label="COMPOUND095"
  shape: bbox 1.588 x 6.339 x 1.588 mm, 3 faces (baked)
FEATURE [Part::Feature] Part__Feature430  label="COMPOUND096"
  shape: bbox 1.588 x 6.339 x 1.588 mm, 3 faces (baked)
FEATURE [Part::Feature] Part__Feature431  label="COMPOUND097"
  shape: bbox 1.588 x 6.339 x 1.588 mm, 3 faces (baked)
FEATURE [Part::Feature] Part__Feature432  label="COMPOUND098"
  shape: bbox 1.588 x 6.339 x 1.588 mm, 3 faces (baked)
FEATURE [Part::Feature] Part__Feature433  label="COMPOUND099"
  shape: bbox 1.588 x 6.339 x 1.588 mm, 3 faces (baked)
FEATURE [Part::Feature] Part__Feature434  label="COMPOUND100"
  shape: bbox 1.588 x 6.339 x 1.588 mm, 3 faces (baked)
FEATURE [Part::Feature] Part__Feature435  label="COMPOUND101"
  shape: bbox 1.588 x 6.339 x 1.588 mm, 3 faces (baked)
FEATURE [Part::Feature] Part__Feature436  label="COMPOUND102"
  shape: bbox 27.79 x 10.75 x 11.74 mm, 39 faces (baked)
FEATURE [Part::Feature] Part__Feature437  label="COMPOUND103"
  shape: bbox 3.175 x 42.92 x 4.725 mm, 126 faces (baked)
FEATURE [App::Part] COMPOUND006  label="COMPOUND104"
  Group = -> [Part__Feature413,Part__Feature414,Part__Feature415,Part__Feature416,Part__Feature417,Part__Feature418,Part__Feature419,Part__Feature420,Part__Feature421,Part__Feature422,Part__Feature423,Part__Feature424,Part__Feature425,Part__Feature426,Part__Feature427,Part__Feature428,Part__Feature429,Part__Feature430,Part__Feature431,Part__Feature432,Part__Feature433,Part__Feature434,Part__Feature435,+2 more]
  Origin = -> Origin140
FEATURE [App::Part] Neck
  Group = -> [Fret_Wire_Set,COMPOUND006]
  Origin = -> Origin141
FEATURE [Part::Feature] Part__Feature438  label="Truss Rod Anchor"
  shape: bbox 19.05 x 19.05 x 19.05 mm, 69 faces (baked)
FEATURE [Part::Feature] Part__Feature439  label="Truss Rod"
  Placement = pos=(-55.6412,0,13.6003) rot=(0,1,0;0.001086rad)
  shape: bbox 434.5 x 5.618 x 12.48 mm, 132 faces (baked)
FEATURE [Part::Feature] Part__Feature440  label="Truss Rod Nut"
  Placement = pos=(-84.2975,0,-12.7017) rot=(0,-1,0;0.051274rad)
  shape: bbox 25.35 x 8.002 x 9.222 mm, 100 faces (baked)
FEATURE [Part::Feature] Part__Feature441  label="Truss Rod Retainer"
  Placement = pos=(309.509,-3.175,6.75489) rot=(0,1,0;0.001086rad)
  shape: bbox 7.635 x 6.359 x 11.44 mm, 56 faces (baked)
FEATURE [Part::Feature] Part__Feature442  label="Washer, No.8"
  Placement = pos=(486.451,0,16.5884) rot=(-0.557618,0.586968,-0.586968;4.15894rad)
  shape: bbox 1.794 x 10.31 x 10.36 mm, 6 faces (baked)
FEATURE [Part::Feature] Part__Feature443  label="Washer, No.009"
  Placement = pos=(512.706,0,17.9358) rot=(-0.557618,0.586968,-0.586968;4.15894rad)
  shape: bbox 1.794 x 10.31 x 10.36 mm, 6 faces (baked)
FEATURE [Part::Feature] Part__Feature444  label="Screw, 4-40 UNC"
  Placement = pos=(313.114,-8.2e-14,13.9265) rot=(0.000543,0,1;3.14159rad)
  shape: bbox 6.729 x 6.415 x 10.25 mm, 70 faces (baked)
FEATURE [App::Part] Truss_Rod_Assembly  label="Truss Rod Assembly"
  Group = -> [Part__Feature438,Part__Feature439,Part__Feature440,Part__Feature441,Part__Feature442,Part__Feature443,Part__Feature444]
  Origin = -> Origin142
  Placement = pos=(276.288,0,28.702) rot=(0,0,1;0rad)
FEATURE [App::Part] Neck__American_Standard_v6  label="Guitar 22 Fret America Standard Neck"
  Group = -> [Neck,Truss_Rod_Assembly]
  Origin = -> Origin143
  Placement = pos=(225.2,147.3,-4) rot=(0,0,1;1.5708rad)
FEATURE [Part::Feature] Part__Feature445  label="Machine Head Casing"
  shape: bbox 23.13 x 26.04 x 19.4 mm, 137 faces (baked)
FEATURE [Part::Feature] Part__Feature446  label="Machine Head Casing001"
  shape: bbox 13.37 x 13.37 x 0.45 mm, 9 faces (baked)
FEATURE [App::Part] Machine_Head_Casing  label="Machine Head Casing002"
  Group = -> [Part__Feature445,Part__Feature446]
  Origin = -> Origin149
FEATURE [Part::Feature] Part__Feature447  label="Threaded Bush"
  Placement = pos=(-0.161068,9.11347,14.25) rot=(0,0,-1;0.359447rad)
  shape: bbox 11.56 x 11.56 x 13.22 mm, 43 faces (baked)
FEATURE [Part::Feature] Part__Feature448  label="Shoulder Washer"
  Placement = pos=(0,0,-1) rot=(0,0,1;0rad)
  shape: bbox 15.69 x 15.69 x 3 mm, 13 faces (baked)
FEATURE [Part::Feature] Part__Feature449  label="Wheel"
  Placement = pos=(4e-15,-1.6256,-1.6256) rot=(-0.673004,-0.523004,0.523004;1.95684rad)
  shape: bbox 16.38 x 16.29 x 7.63 mm, 271 faces (baked)
FEATURE [Part::Feature] Part__Feature450  label="Worm"
  Placement = pos=(-10.0783,9.19608,10.6389) rot=(0,-1,0;1.79163rad)
  shape: bbox 6.209 x 33.16 x 6.231 mm, 288 faces (baked)
FEATURE [App::Part] Worm_Gear_Drive  label="Worm Gear Drive"
  Group = -> [Part__Feature449,Part__Feature450]
  Origin = -> Origin150
  Placement = pos=(25,6.6256,6.1256) rot=(0,0,1;0rad)
FEATURE [Part::Feature] Part__Feature451  label="String Post"
  Placement = pos=(23.7653,0.154858,-20.0756) rot=(0,0,1;1.32126rad)
  shape: bbox 9.642 x 9.642 x 32.19 mm, 69 faces (baked)
FEATURE [Part::Feature] Part__Feature452  label="Washer, M4"
  Placement = pos=(9.53074,10.4443,8.821) rot=(0,1,0;1.34996rad)
  shape: bbox 6 x 1 x 6 mm, 8 faces (baked)
FEATURE [Part::Feature] Part__Feature453  label="Screw, M2.5, L5"
  Placement = pos=(25,5,4.7256) rot=(0,0,1;1.32126rad)
  shape: bbox 5.835 x 5.463 x 5.784 mm, 37 faces (baked)
FEATURE [Part::Feature] Part__Feature454  label="Shim, ID5"
  Placement = pos=(25,5,1.5004) rot=(0.717545,0.492509,0.492509;1.89678rad)
  shape: bbox 7.82 x 7.82 x 0.254 mm, 4 faces (baked)
FEATURE [Part::Feature] Part__Feature455  label="Button"
  Placement = pos=(20.0188,11.5943,-5.94015) rot=(-0.662083,0.529928,0.529928;1.97195rad)
  shape: bbox 10.07 x 14.71 x 19.93 mm, 68 faces (baked)
FEATURE [Part::Feature] Part__Feature456  label="Screw, M2.5, L12"
  Placement = pos=(17.675,34.3443,4.5) rot=(-0.362665,0.658967,0.658967;2.44577rad)
  shape: bbox 6.021 x 12.78 x 6.209 mm, 76 faces (baked)
FEATURE [Part::Feature] Part__Feature457  label="Washer, Plastic"
  Placement = pos=(47.5439,20.2943,-14.4168) rot=(-0.662083,0.529928,0.529928;1.97195rad)
  shape: bbox 7.393 x 1.3 x 7.393 mm, 8 faces (baked)
FEATURE [App::Part] Machine_Head_135_L_v9  label="Machine Head Low E"
  Group = -> [Machine_Head_Casing,Part__Feature447,Part__Feature448,Worm_Gear_Drive,Part__Feature451,Part__Feature452,Part__Feature453,Part__Feature454,Part__Feature455,Part__Feature456,Part__Feature457]
  Origin = -> Origin151
  Placement = pos=(207.4,999.2,22.9) rot=(0.707107,-0.707107,0;3.14159rad)
FEATURE [Part::Feature] Part__Feature458  label="Machine Head Casing004"
  shape: bbox 23.13 x 26.04 x 19.4 mm, 137 faces (baked)
FEATURE [Part::Feature] Part__Feature459  label="Machine Head Casing005"
  shape: bbox 13.37 x 13.37 x 0.45 mm, 9 faces (baked)
FEATURE [App::Part] Machine_Head_Casing001  label="Machine Head Casing003"
  Group = -> [Part__Feature458,Part__Feature459]
  Origin = -> Origin152
FEATURE [Part::Feature] Part__Feature460  label="Threaded Bush001"
  Placement = pos=(-0.161068,9.11347,14.25) rot=(0,0,-1;0.359447rad)
  shape: bbox 11.56 x 11.56 x 13.22 mm, 43 faces (baked)
FEATURE [Part::Feature] Part__Feature461  label="Shoulder Washer001"
  Placement = pos=(0,0,-1) rot=(0,0,1;0rad)
  shape: bbox 15.69 x 15.69 x 3 mm, 13 faces (baked)
FEATURE [Part::Feature] Part__Feature462  label="Wheel001"
  Placement = pos=(4e-15,-1.6256,-1.6256) rot=(-0.673004,-0.523004,0.523004;1.95684rad)
  shape: bbox 16.38 x 16.29 x 7.63 mm, 271 faces (baked)
FEATURE [Part::Feature] Part__Feature463  label="Worm001"
  Placement = pos=(-10.0783,9.19608,10.6389) rot=(0,-1,0;1.79163rad)
  shape: bbox 6.209 x 33.16 x 6.231 mm, 288 faces (baked)
FEATURE [Part::Feature] Part__Feature464  label="String Post001"
  Placement = pos=(23.7653,0.154858,-20.0756) rot=(0,0,1;1.32126rad)
  shape: bbox 9.642 x 9.642 x 32.19 mm, 69 faces (baked)
FEATURE [Part::Feature] Part__Feature465  label="Washer, M005"
  Placement = pos=(9.53074,10.4443,8.821) rot=(0,1,0;1.34996rad)
  shape: bbox 6 x 1 x 6 mm, 8 faces (baked)
FEATURE [Part::Feature] Part__Feature466  label="Screw, M2.5, L013"
  Placement = pos=(25,5,4.7256) rot=(0,0,1;1.32126rad)
  shape: bbox 5.835 x 5.463 x 5.784 mm, 37 faces (baked)
FEATURE [Part::Feature] Part__Feature467  label="Shim, ID006"
  Placement = pos=(25,5,1.5004) rot=(0.717545,0.492509,0.492509;1.89678rad)
  shape: bbox 7.82 x 7.82 x 0.254 mm, 4 faces (baked)
FEATURE [Part::Feature] Part__Feature468  label="Button001"
  Placement = pos=(20.0188,11.5943,-5.94015) rot=(-0.662083,0.529928,0.529928;1.97195rad)
  shape: bbox 10.07 x 14.71 x 19.93 mm, 68 faces (baked)
FEATURE [Part::Feature] Part__Feature469  label="Screw, M2.5, L014"
  Placement = pos=(17.675,34.3443,4.5) rot=(-0.362665,0.658967,0.658967;2.44577rad)
  shape: bbox 6.021 x 12.78 x 6.209 mm, 76 faces (baked)
FEATURE [Part::Feature] Part__Feature470  label="Washer, Plastic001"
  Placement = pos=(47.5439,20.2943,-14.4168) rot=(-0.662083,0.529928,0.529928;1.97195rad)
  shape: bbox 7.393 x 1.3 x 7.393 mm, 8 faces (baked)
FEATURE [App::Part] Worm_Gear_Drive001  label="Worm Gear Drive001"
  Group = -> [Part__Feature462,Part__Feature463]
  Origin = -> Origin153
  Placement = pos=(25,6.6256,6.1256) rot=(0,0,1;0rad)
FEATURE [App::Part] Machine_Head_135_L_v010  label="Machine Head A"
  Group = -> [Machine_Head_Casing001,Part__Feature460,Part__Feature461,Worm_Gear_Drive001,Part__Feature464,Part__Feature465,Part__Feature466,Part__Feature467,Part__Feature468,Part__Feature469,Part__Feature470]
  Origin = -> Origin154
  Placement = pos=(215.5,1021.6,23.2) rot=(0.707107,-0.707107,0;3.14159rad)
FEATURE [Part::Feature] Part__Feature471  label="Machine Head Casing007"
  shape: bbox 23.13 x 26.04 x 19.4 mm, 137 faces (baked)
FEATURE [Part::Feature] Part__Feature472  label="Machine Head Casing008"
  shape: bbox 13.37 x 13.37 x 0.45 mm, 9 faces (baked)
FEATURE [App::Part] Machine_Head_Casing002  label="Machine Head Casing006"
  Group = -> [Part__Feature471,Part__Feature472]
  Origin = -> Origin155
FEATURE [Part::Feature] Part__Feature473  label="Threaded Bush002"
  Placement = pos=(-0.161068,9.11347,14.25) rot=(0,0,-1;0.359447rad)
  shape: bbox 11.56 x 11.56 x 13.22 mm, 43 faces (baked)
FEATURE [Part::Feature] Part__Feature474  label="Shoulder Washer002"
  Placement = pos=(0,0,-1) rot=(0,0,1;0rad)
  shape: bbox 15.69 x 15.69 x 3 mm, 13 faces (baked)
FEATURE [Part::Feature] Part__Feature475  label="Wheel002"
  Placement = pos=(4e-15,-1.6256,-1.6256) rot=(-0.673004,-0.523004,0.523004;1.95684rad)
  shape: bbox 16.38 x 16.29 x 7.63 mm, 271 faces (baked)
FEATURE [Part::Feature] Part__Feature476  label="Worm002"
  Placement = pos=(-10.0783,9.19608,10.6389) rot=(0,-1,0;1.79163rad)
  shape: bbox 6.209 x 33.16 x 6.231 mm, 288 faces (baked)
FEATURE [Part::Feature] Part__Feature477  label="String Post002"
  Placement = pos=(23.7653,0.154858,-20.0756) rot=(0,0,1;1.32126rad)
  shape: bbox 9.642 x 9.642 x 32.19 mm, 69 faces (baked)
FEATURE [Part::Feature] Part__Feature478  label="Washer, M006"
  Placement = pos=(9.53074,10.4443,8.821) rot=(0,1,0;1.34996rad)
  shape: bbox 6 x 1 x 6 mm, 8 faces (baked)
FEATURE [Part::Feature] Part__Feature479  label="Screw, M2.5, L015"
  Placement = pos=(25,5,4.7256) rot=(0,0,1;1.32126rad)
  shape: bbox 5.835 x 5.463 x 5.784 mm, 37 faces (baked)
FEATURE [Part::Feature] Part__Feature480  label="Shim, ID007"
  Placement = pos=(25,5,1.5004) rot=(0.717545,0.492509,0.492509;1.89678rad)
  shape: bbox 7.82 x 7.82 x 0.254 mm, 4 faces (baked)
FEATURE [Part::Feature] Part__Feature481  label="Button002"
  Placement = pos=(20.0188,11.5943,-5.94015) rot=(-0.662083,0.529928,0.529928;1.97195rad)
  shape: bbox 10.07 x 14.71 x 19.93 mm, 68 faces (baked)
FEATURE [Part::Feature] Part__Feature482  label="Screw, M2.5, L016"
  Placement = pos=(17.675,34.3443,4.5) rot=(-0.362665,0.658967,0.658967;2.44577rad)
  shape: bbox 6.021 x 12.78 x 6.209 mm, 76 faces (baked)
FEATURE [Part::Feature] Part__Feature483  label="Washer, Plastic002"
  Placement = pos=(47.5439,20.2943,-14.4168) rot=(-0.662083,0.529928,0.529928;1.97195rad)
  shape: bbox 7.393 x 1.3 x 7.393 mm, 8 faces (baked)
FEATURE [App::Part] Worm_Gear_Drive002  label="Worm Gear Drive002"
  Group = -> [Part__Feature475,Part__Feature476]
  Origin = -> Origin156
  Placement = pos=(25,6.6256,6.1256) rot=(0,0,1;0rad)
FEATURE [App::Part] Machine_Head_135_L_v011  label="Machine Head D"
  Group = -> [Machine_Head_Casing002,Part__Feature473,Part__Feature474,Worm_Gear_Drive002,Part__Feature477,Part__Feature478,Part__Feature479,Part__Feature480,Part__Feature481,Part__Feature482,Part__Feature483]
  Origin = -> Origin157
  Placement = pos=(221.3,1046.7,23.1) rot=(0.707107,-0.707107,0;3.14159rad)
FEATURE [Part::Feature] Part__Feature484  label="Machine Head Casing010"
  shape: bbox 23.13 x 26.04 x 19.4 mm, 137 faces (baked)
FEATURE [Part::Feature] Part__Feature485  label="Machine Head Casing011"
  shape: bbox 13.37 x 13.37 x 0.45 mm, 9 faces (baked)
FEATURE [App::Part] Machine_Head_Casing003  label="Machine Head Casing009"
  Group = -> [Part__Feature484,Part__Feature485]
  Origin = -> Origin158
FEATURE [Part::Feature] Part__Feature486  label="Threaded Bush003"
  Placement = pos=(-0.161068,9.11347,14.25) rot=(0,0,-1;0.359447rad)
  shape: bbox 11.56 x 11.56 x 13.22 mm, 43 faces (baked)
FEATURE [Part::Feature] Part__Feature487  label="Shoulder Washer003"
  Placement = pos=(0,0,-1) rot=(0,0,1;0rad)
  shape: bbox 15.69 x 15.69 x 3 mm, 13 faces (baked)
FEATURE [Part::Feature] Part__Feature488  label="Wheel003"
  Placement = pos=(4e-15,-1.6256,-1.6256) rot=(-0.673004,-0.523004,0.523004;1.95684rad)
  shape: bbox 16.38 x 16.29 x 7.63 mm, 271 faces (baked)
FEATURE [Part::Feature] Part__Feature489  label="Worm003"
  Placement = pos=(-10.0783,9.19608,10.6389) rot=(0,-1,0;1.79163rad)
  shape: bbox 6.209 x 33.16 x 6.231 mm, 288 faces (baked)
FEATURE [Part::Feature] Part__Feature490  label="String Post003"
  Placement = pos=(23.7653,0.154858,-20.0756) rot=(0,0,1;1.32126rad)
  shape: bbox 9.642 x 9.642 x 32.19 mm, 69 faces (baked)
FEATURE [Part::Feature] Part__Feature491  label="Washer, M007"
  Placement = pos=(9.53074,10.4443,8.821) rot=(0,1,0;1.34996rad)
  shape: bbox 6 x 1 x 6 mm, 8 faces (baked)
FEATURE [Part::Feature] Part__Feature492  label="Screw, M2.5, L017"
  Placement = pos=(25,5,4.7256) rot=(0,0,1;1.32126rad)
  shape: bbox 5.835 x 5.463 x 5.784 mm, 37 faces (baked)
FEATURE [Part::Feature] Part__Feature493  label="Shim, ID008"
  Placement = pos=(25,5,1.5004) rot=(0.717545,0.492509,0.492509;1.89678rad)
  shape: bbox 7.82 x 7.82 x 0.254 mm, 4 faces (baked)
FEATURE [Part::Feature] Part__Feature494  label="Button003"
  Placement = pos=(20.0188,11.5943,-5.94015) rot=(-0.662083,0.529928,0.529928;1.97195rad)
  shape: bbox 10.07 x 14.71 x 19.93 mm, 68 faces (baked)
FEATURE [Part::Feature] Part__Feature495  label="Screw, M2.5, L018"
  Placement = pos=(17.675,34.3443,4.5) rot=(-0.362665,0.658967,0.658967;2.44577rad)
  shape: bbox 6.021 x 12.78 x 6.209 mm, 76 faces (baked)
FEATURE [Part::Feature] Part__Feature496  label="Washer, Plastic003"
  Placement = pos=(47.5439,20.2943,-14.4168) rot=(-0.662083,0.529928,0.529928;1.97195rad)
  shape: bbox 7.393 x 1.3 x 7.393 mm, 8 faces (baked)
FEATURE [App::Part] Worm_Gear_Drive003  label="Worm Gear Drive003"
  Group = -> [Part__Feature488,Part__Feature489]
  Origin = -> Origin159
  Placement = pos=(25,6.6256,6.1256) rot=(0,0,1;0rad)
FEATURE [App::Part] Machine_Head_135_L_v012  label="Machine Head G"
  Group = -> [Machine_Head_Casing003,Part__Feature486,Part__Feature487,Worm_Gear_Drive003,Part__Feature490,Part__Feature491,Part__Feature492,Part__Feature493,Part__Feature494,Part__Feature495,Part__Feature496]
  Origin = -> Origin160
  Placement = pos=(229.8,1068.8,23) rot=(0.707107,-0.707107,0;3.14159rad)
FEATURE [Part::Feature] Part__Feature497  label="Machine Head Casing013"
  shape: bbox 23.13 x 26.04 x 19.4 mm, 137 faces (baked)
FEATURE [Part::Feature] Part__Feature498  label="Machine Head Casing014"
  shape: bbox 13.37 x 13.37 x 0.45 mm, 9 faces (baked)
FEATURE [App::Part] Machine_Head_Casing004  label="Machine Head Casing012"
  Group = -> [Part__Feature497,Part__Feature498]
  Origin = -> Origin161
FEATURE [Part::Feature] Part__Feature499  label="Threaded Bush004"
  Placement = pos=(-0.161068,9.11347,14.25) rot=(0,0,-1;0.359447rad)
  shape: bbox 11.56 x 11.56 x 13.22 mm, 43 faces (baked)
FEATURE [Part::Feature] Part__Feature500  label="Shoulder Washer004"
  Placement = pos=(0,0,-1) rot=(0,0,1;0rad)
  shape: bbox 15.69 x 15.69 x 3 mm, 13 faces (baked)
FEATURE [Part::Feature] Part__Feature501  label="Wheel004"
  Placement = pos=(4e-15,-1.6256,-1.6256) rot=(-0.673004,-0.523004,0.523004;1.95684rad)
  shape: bbox 16.38 x 16.29 x 7.63 mm, 271 faces (baked)
FEATURE [Part::Feature] Part__Feature502  label="Worm004"
  Placement = pos=(-10.0783,9.19608,10.6389) rot=(0,-1,0;1.79163rad)
  shape: bbox 6.209 x 33.16 x 6.231 mm, 288 faces (baked)
FEATURE [Part::Feature] Part__Feature503  label="String Post004"
  Placement = pos=(23.7653,0.154858,-20.0756) rot=(0,0,1;1.32126rad)
  shape: bbox 9.642 x 9.642 x 32.19 mm, 69 faces (baked)
FEATURE [Part::Feature] Part__Feature504  label="Washer, M008"
  Placement = pos=(9.53074,10.4443,8.821) rot=(0,1,0;1.34996rad)
  shape: bbox 6 x 1 x 6 mm, 8 faces (baked)
FEATURE [Part::Feature] Part__Feature505  label="Screw, M2.5, L019"
  Placement = pos=(25,5,4.7256) rot=(0,0,1;1.32126rad)
  shape: bbox 5.835 x 5.463 x 5.784 mm, 37 faces (baked)
FEATURE [Part::Feature] Part__Feature506  label="Shim, ID009"
  Placement = pos=(25,5,1.5004) rot=(0.717545,0.492509,0.492509;1.89678rad)
  shape: bbox 7.82 x 7.82 x 0.254 mm, 4 faces (baked)
FEATURE [Part::Feature] Part__Feature507  label="Button004"
  Placement = pos=(20.0188,11.5943,-5.94015) rot=(-0.662083,0.529928,0.529928;1.97195rad)
  shape: bbox 10.07 x 14.71 x 19.93 mm, 68 faces (baked)
FEATURE [Part::Feature] Part__Feature508  label="Screw, M2.5, L020"
  Placement = pos=(17.675,34.3443,4.5) rot=(-0.362665,0.658967,0.658967;2.44577rad)
  shape: bbox 6.021 x 12.78 x 6.209 mm, 76 faces (baked)
FEATURE [Part::Feature] Part__Feature509  label="Washer, Plastic004"
  Placement = pos=(47.5439,20.2943,-14.4168) rot=(-0.662083,0.529928,0.529928;1.97195rad)
  shape: bbox 7.393 x 1.3 x 7.393 mm, 8 faces (baked)
FEATURE [App::Part] Worm_Gear_Drive004  label="Worm Gear Drive004"
  Group = -> [Part__Feature501,Part__Feature502]
  Origin = -> Origin162
  Placement = pos=(25,6.6256,6.1256) rot=(0,0,1;0rad)
FEATURE [App::Part] Machine_Head_135_L_v013  label="Machine Head B"
  Group = -> [Machine_Head_Casing004,Part__Feature499,Part__Feature500,Worm_Gear_Drive004,Part__Feature503,Part__Feature504,Part__Feature505,Part__Feature506,Part__Feature507,Part__Feature508,Part__Feature509]
  Origin = -> Origin163
  Placement = pos=(235.8,1092.2,23) rot=(0.707107,-0.707107,0;3.14159rad)
FEATURE [Part::Feature] Part__Feature510  label="Machine Head Casing016"
  shape: bbox 23.13 x 26.04 x 19.4 mm, 137 faces (baked)
FEATURE [Part::Feature] Part__Feature511  label="Machine Head Casing017"
  shape: bbox 13.37 x 13.37 x 0.45 mm, 9 faces (baked)
FEATURE [App::Part] Machine_Head_Casing005  label="Machine Head Casing015"
  Group = -> [Part__Feature510,Part__Feature511]
  Origin = -> Origin164
FEATURE [Part::Feature] Part__Feature512  label="Threaded Bush005"
  Placement = pos=(-0.161068,9.11347,14.25) rot=(0,0,-1;0.359447rad)
  shape: bbox 11.56 x 11.56 x 13.22 mm, 43 faces (baked)
FEATURE [Part::Feature] Part__Feature513  label="Shoulder Washer005"
  Placement = pos=(0,0,-1) rot=(0,0,1;0rad)
  shape: bbox 15.69 x 15.69 x 3 mm, 13 faces (baked)
FEATURE [Part::Feature] Part__Feature514  label="Wheel005"
  Placement = pos=(4e-15,-1.6256,-1.6256) rot=(-0.673004,-0.523004,0.523004;1.95684rad)
  shape: bbox 16.38 x 16.29 x 7.63 mm, 271 faces (baked)
FEATURE [Part::Feature] Part__Feature515  label="Worm005"
  Placement = pos=(-10.0783,9.19608,10.6389) rot=(0,-1,0;1.79163rad)
  shape: bbox 6.209 x 33.16 x 6.231 mm, 288 faces (baked)
FEATURE [Part::Feature] Part__Feature516  label="String Post005"
  Placement = pos=(23.7653,0.154858,-20.0756) rot=(0,0,1;1.32126rad)
  shape: bbox 9.642 x 9.642 x 32.19 mm, 69 faces (baked)
FEATURE [Part::Feature] Part__Feature517  label="Washer, M009"
  Placement = pos=(9.53074,10.4443,8.821) rot=(0,1,0;1.34996rad)
  shape: bbox 6 x 1 x 6 mm, 8 faces (baked)
FEATURE [Part::Feature] Part__Feature518  label="Screw, M2.5, L021"
  Placement = pos=(25,5,4.7256) rot=(0,0,1;1.32126rad)
  shape: bbox 5.835 x 5.463 x 5.784 mm, 37 faces (baked)
FEATURE [Part::Feature] Part__Feature519  label="Shim, ID010"
  Placement = pos=(25,5,1.5004) rot=(0.717545,0.492509,0.492509;1.89678rad)
  shape: bbox 7.82 x 7.82 x 0.254 mm, 4 faces (baked)
FEATURE [Part::Feature] Part__Feature520  label="Button005"
  Placement = pos=(20.0188,11.5943,-5.94015) rot=(-0.662083,0.529928,0.529928;1.97195rad)
  shape: bbox 10.07 x 14.71 x 19.93 mm, 68 faces (baked)
FEATURE [Part::Feature] Part__Feature521  label="Screw, M2.5, L022"
  Placement = pos=(17.675,34.3443,4.5) rot=(-0.362665,0.658967,0.658967;2.44577rad)
  shape: bbox 6.021 x 12.78 x 6.209 mm, 76 faces (baked)
FEATURE [Part::Feature] Part__Feature522  label="Washer, Plastic005"
  Placement = pos=(47.5439,20.2943,-14.4168) rot=(-0.662083,0.529928,0.529928;1.97195rad)
  shape: bbox 7.393 x 1.3 x 7.393 mm, 8 faces (baked)
FEATURE [App::Part] Worm_Gear_Drive005  label="Worm Gear Drive005"
  Group = -> [Part__Feature514,Part__Feature515]
  Origin = -> Origin165
  Placement = pos=(25,6.6256,6.1256) rot=(0,0,1;0rad)
FEATURE [App::Part] Machine_Head_135_L_v014  label="Machine Head High E"
  Group = -> [Machine_Head_Casing005,Part__Feature512,Part__Feature513,Worm_Gear_Drive005,Part__Feature516,Part__Feature517,Part__Feature518,Part__Feature519,Part__Feature520,Part__Feature521,Part__Feature522]
  Origin = -> Origin166
  Placement = pos=(243,1115.5,22.9) rot=(0.707107,-0.707107,0;3.14159rad)
FEATURE [App::Part] Part038  label="Machine Head Tuners"
  Group = -> [Machine_Head_135_L_v9,Machine_Head_135_L_v010,Machine_Head_135_L_v011,Machine_Head_135_L_v012,Machine_Head_135_L_v013,Machine_Head_135_L_v014]
  Origin = -> Origin148
FEATURE [App::Part] Part037  label="Neck and Pegs"
  Group = -> [Neck__American_Standard_v6,Part038]
  Origin = -> Origin144
  Placement = pos=(-0.2,-1.4,0.3) rot=(0,0,1;0rad)
FEATURE [Sketcher::SketchObject] Sketch158  label="Overall Guitar Dimensions"
  FullyConstrained = false
  MapMode = 5
  Support = -> [XY_Plane001]
  sketch-geometry (11):
    g0: LineSegment StartX=255 StartY=1125 StartZ=0 EndX=500 EndY=1125 EndZ=0
    g1: LineSegment StartX=408.821 StartY=43.4656 StartZ=0 EndX=500 EndY=43.4656 EndZ=0
    g2: LineSegment StartX=500 StartY=43.4656 StartZ=0 EndX=500 EndY=1125 EndZ=0
    g3: LineSegment StartX=413.448 StartY=50.4 StartZ=0 EndX=413.448 EndY=40 EndZ=0
    g4: LineSegment StartX=44.2 StartY=144.6 StartZ=0 EndX=44.2 EndY=40 EndZ=0
    g5: LineSegment StartX=44.2 StartY=40 StartZ=0 EndX=413.448 EndY=40 EndZ=0
    g6: LineSegment StartX=52.6 StartY=529.8 StartZ=0 EndX=52.6 EndY=600 EndZ=0
    g7: LineSegment StartX=355.987 StartY=452.42 StartZ=0 EndX=355.987 EndY=600 EndZ=0
    g8: LineSegment StartX=355.987 StartY=600 StartZ=0 EndX=52.6 EndY=600 EndZ=0
    g9: LineSegment StartX=97.988 StartY=587.07 StartZ=0 EndX=430 EndY=587.07 EndZ=0
    g10: LineSegment StartX=430 StartY=587.07 StartZ=0 EndX=430 EndY=43.4656 EndZ=0
  constraints (23):
    c: Horizontal(g0)
    c: Horizontal(g1)
    c: Coincident(g2,g1)
    c: Coincident(g2,g0)
    c: Vertical(g2)
    c: DistanceY(g2,g2) = 1081.53
    c: Vertical(g3)
    c: Vertical(g4)
    c: Coincident(g5,g4)
    c: Coincident(g5,g3)
    c: Horizontal(g5)
    c: DistanceX(g5,g5) = 369.248
    c: Vertical(g6)
    c: Vertical(g7)
    c: Coincident(g8,g7)
    c: Coincident(g8,g6)
    c: Horizontal(g8)
    c: DistanceX(g8,g8) = 303.387
    c: Horizontal(g9)
    c: Coincident(g10,g9)
    c: PointOnObject(g10,g1)
    c: Vertical(g10)
    c: DistanceY(g10,g10) = 543.604
FEATURE [Sketcher::SketchObject] Sketch159
  FullyConstrained = true
  MapMode = 5
  Support = -> [XY_Plane167]
  sketch-geometry (4):
    g0: LineSegment StartX=0 StartY=0 StartZ=0 EndX=100 EndY=0 EndZ=0
    g1: LineSegment StartX=100 StartY=0 StartZ=0 EndX=100 EndY=32.5 EndZ=0
    g2: LineSegment StartX=100 StartY=32.5 StartZ=0 EndX=0 EndY=32.5 EndZ=0
    g3: LineSegment StartX=0 StartY=32.5 StartZ=0 EndX=0 EndY=0 EndZ=0
  constraints (11):
    c: Coincident(g0,g1)
    c: Coincident(g1,g2)
    c: Coincident(g2,g3)
    c: Coincident(g3,g0)
    c: Horizontal(g0)
    c: Horizontal(g2)
    c: Vertical(g1)
    c: Vertical(g3)
    c: Coincident(g0,g-1)
    c: DistanceX(g2,g2) = 100
    c: DistanceY(g3,g3) = 32.5
FEATURE [PartDesign::Pad] Pad005
  Direction = (0,0,1)
  Length = 2
  Length2 = 10
  Profile = -> Sketch159
  ReferenceAxis = -> Sketch159 [N_Axis]
  Type = 0
FEATURE [Sketcher::SketchObject] Sketch160
  FullyConstrained = false
  MapMode = 5
  Placement = pos=(0,0,2) rot=(0,0,1;0rad)
  Support = -> [Pad005]
  sketch-geometry (17):
    g0: LineSegment StartX=15 StartY=29.1324 StartZ=0 EndX=85 EndY=29.1324 EndZ=0
    g1: LineSegment StartX=85 StartY=29.1324 StartZ=0 EndX=85 EndY=11.1324 EndZ=0
    g2: LineSegment StartX=85 StartY=11.1324 StartZ=0 EndX=15 EndY=11.1324 EndZ=0
    g3: LineSegment StartX=15 StartY=11.1324 StartZ=0 EndX=15 EndY=29.1324 EndZ=0
    g4: LineSegment StartX=15 StartY=29.1324 StartZ=0 EndX=12 EndY=29.1324 EndZ=0
    g5: LineSegment StartX=12 StartY=29.1324 StartZ=0 EndX=12 EndY=20.1324 EndZ=0
    g6: Circle CenterX=12 CenterY=20.1324 CenterZ=0 NormalX=0 NormalY=0 NormalZ=1 AngleXU=0 Radius=1.75
    g7: LineSegment StartX=85 StartY=29.1324 StartZ=0 EndX=88 EndY=29.1324 EndZ=0
    g8: LineSegment StartX=88 StartY=29.1324 StartZ=0 EndX=88 EndY=20.1324 EndZ=0
    g9: LineSegment StartX=88 StartY=20.1324 StartZ=0 EndX=12 EndY=20.1324 EndZ=0
    g10: Circle CenterX=88 CenterY=20.1324 CenterZ=0 NormalX=0 NormalY=0 NormalZ=1 AngleXU=0 Radius=1.75
    g11: LineSegment StartX=15 StartY=32.5 StartZ=0 EndX=15 EndY=29.2 EndZ=0
    g12: LineSegment StartX=0 StartY=32.5 StartZ=0 EndX=15 EndY=32.5 EndZ=0
    g13: LineSegment StartX=4.5 StartY=20.1324 StartZ=0 EndX=4.5 EndY=21.89 EndZ=0
    g14: Circle CenterX=4.5 CenterY=21.89 CenterZ=0 NormalX=0 NormalY=0 NormalZ=1 AngleXU=0 Radius=1.75
    g15: LineSegment StartX=95.5 StartY=20.1324 StartZ=0 EndX=95.5 EndY=21.89 EndZ=0
    g16: Circle CenterX=95.5 CenterY=21.89 CenterZ=0 NormalX=0 NormalY=0 NormalZ=1 AngleXU=0 Radius=1.75
  constraints (39):
    c: Coincident(g0,g1)
    c: Coincident(g1,g2)
    c: Coincident(g2,g3)
    c: Coincident(g3,g0)
    c: Horizontal(g0)
    c: Horizontal(g2)
    c: Vertical(g1)
    c: Vertical(g3)
    c: DistanceX(g0,g0) = 70
    c: DistanceY(g3,g3) = 18
    c: Coincident(g4,g0)
    c: Horizontal(g4)
    c: Coincident(g5,g4)
    c: Vertical(g5)
    c: DistanceY(g5,g5) = 9
    c: Coincident(g6,g5)
    c: Coincident(g0,g7)
    c: Horizontal(g7)
    c: Coincident(g7,g8)
    c: Vertical(g8)
    c: DistanceX(g7,g7) = 3
    c: DistanceY(g8,g8) = 9
    c: Coincident(g9,g8)
    c: Coincident(g9,g6)
    c: DistanceX(g9,g9) = 76
    c: Coincident(g10,g8)
    c: Diameter(g10) = 3.5
    c: Diameter(g6) = 3.5
    c: Vertical(g11)
    c: PointOnObject(g12,g-2)
    c: Horizontal(g12)
    c: DistanceX(g12,g12) = 15
    c: DistanceY(g11,g11) = 3.3
    c: Vertical(g13)
    c: Coincident(g14,g13)
    c: Diameter(g14) = 3.5
    c: Vertical(g15)
    c: Coincident(g16,g15)
    c: Diameter(g16) = 3.5
FEATURE [PartDesign::Pocket] Pocket035
  BaseFeature = -> Pad005
  Direction = (0,0,-1)
  Length = 2
  Length2 = 5
  Profile = -> Sketch160
  ReferenceAxis = -> Sketch160 [N_Axis]
  Type = 0
FEATURE [PartDesign::Fillet] Fillet020
  Base = -> Pocket035 [Edge32,Edge31,Edge34,Edge33]
  BaseFeature = -> Pocket035
  Radius = 8.5
  SupportTransform = false
  UseAllEdges = false
FEATURE [Sketcher::SketchObject] Sketch161
  FullyConstrained = false
  MapMode = 5
  Placement = pos=(0,0,2) rot=(0,0,1;0rad)
  Support = -> [Fillet020]
  sketch-geometry (15):
    g0: LineSegment StartX=8 StartY=32.4801 StartZ=0 EndX=8 EndY=10.2801 EndZ=0
    g1: LineSegment StartX=0 StartY=0 StartZ=0 EndX=50 EndY=0 EndZ=0
    g2: LineSegment StartX=12 StartY=21.8697 StartZ=0 EndX=12 EndY=20.1197 EndZ=0
    g3: LineSegment StartX=12 StartY=20.1197 StartZ=0 EndX=0 EndY=20.1197 EndZ=0
    g4: LineSegment StartX=8 StartY=10.2801 StartZ=0 EndX=50 EndY=0 EndZ=0
    g5: LineSegment StartX=8 StartY=32.4801 StartZ=0 EndX=0 EndY=32.4801 EndZ=0
    g6: LineSegment StartX=100 StartY=32.5 StartZ=0 EndX=92 EndY=32.5 EndZ=0
    g7: LineSegment StartX=92 StartY=32.5 StartZ=0 EndX=92 EndY=10.3 EndZ=0
    g8: LineSegment StartX=92 StartY=10.3 StartZ=0 EndX=50 EndY=0 EndZ=0
    g9: LineSegment StartX=50 StartY=0 StartZ=0 EndX=0 EndY=0 EndZ=0
    g10: LineSegment StartX=8 StartY=10.2801 StartZ=0 EndX=0 EndY=10.2801 EndZ=0
    g11: LineSegment StartX=0 StartY=10.2801 StartZ=0 EndX=0 EndY=0 EndZ=0
    g12: LineSegment StartX=92 StartY=10.3 StartZ=0 EndX=100.006 EndY=10.3 EndZ=0
    g13: LineSegment StartX=100.006 StartY=10.3 StartZ=0 EndX=100.006 EndY=0 EndZ=0
    g14: LineSegment StartX=100.006 StartY=0 StartZ=0 EndX=50 EndY=0 EndZ=0
  constraints (35):
    c: Vertical(g0)
    c: Coincident(g1,g-1)
    c: PointOnObject(g1,g-1)
    c: DistanceX(g1,g1) = 50
    c: Vertical(g2)
    c: DistanceY(g2,g2) = 1.75
    c: Coincident(g3,g2)
    c: PointOnObject(g3,g-2)
    c: Horizontal(g3)
    c: DistanceX(g3,g3) = 12
    c: DistanceY(g0,g0) = 22.2
    c: Coincident(g4,g0)
    c: Coincident(g4,g1)
    c: Coincident(g5,g0)
    c: PointOnObject(g5,g-2)
    c: Horizontal(g5)
    c: Horizontal(g6)
    c: Coincident(g7,g6)
    c: Vertical(g7)
    c: Coincident(g8,g7)
    c: Coincident(g8,g4)
    c: Coincident(g9,g4)
    c: Coincident(g9,g1)
    c: Coincident(g10,g4)
    c: PointOnObject(g10,g-2)
    c: Horizontal(g10)
    c: Coincident(g11,g10)
    c: Coincident(g11,g9)
    c: Coincident(g12,g8)
    c: Horizontal(g12)
    c: Coincident(g13,g12)
    c: PointOnObject(g13,g-1)
    c: Vertical(g13)
    c: Coincident(g14,g13)
    c: Coincident(g14,g4)
FEATURE [PartDesign::Pocket] Pocket036
  BaseFeature = -> Fillet020
  Direction = (0,0,-1)
  Length = 2
  Length2 = 5
  Profile = -> Sketch161
  ReferenceAxis = -> Sketch161 [N_Axis]
  Type = 0
FEATURE [PartDesign::Fillet] Fillet021
  Base = -> Pocket036 [Edge23,Edge26,Edge30,Edge27]
  BaseFeature = -> Pocket036
  Radius = 7.5
  SupportTransform = false
  UseAllEdges = false
FEATURE [PartDesign::Fillet] Fillet022
  Base = -> Fillet021 [Edge26,Edge33]
  BaseFeature = -> Fillet021
  Radius = 10
  SupportTransform = false
  UseAllEdges = false
FEATURE [PartDesign::Fillet] Fillet023
  Base = -> Fillet022 [Edge32]
  BaseFeature = -> Fillet022
  Radius = 8
  SupportTransform = false
  UseAllEdges = false
FEATURE [PartDesign::Body] Body018  label="Single Coil Frame Neck Pickup"
  Group = -> [Sketch159,Pad005,Sketch160,Pocket035,Fillet020,Sketch161,Pocket036,Fillet021,Fillet022,Fillet023]
  Origin = -> Origin167
  Placement = pos=(175.2,430.4,45.4) rot=(0,0,1;0rad)
  Tip = -> Fillet023
FEATURE [Sketcher::SketchObject] Sketch162
  FullyConstrained = true
  MapMode = 5
  Support = -> [XY_Plane168]
  sketch-geometry (4):
    g0: LineSegment StartX=0 StartY=0 StartZ=0 EndX=100 EndY=0 EndZ=0
    g1: LineSegment StartX=100 StartY=0 StartZ=0 EndX=100 EndY=32.5 EndZ=0
    g2: LineSegment StartX=100 StartY=32.5 StartZ=0 EndX=0 EndY=32.5 EndZ=0
    g3: LineSegment StartX=0 StartY=32.5 StartZ=0 EndX=0 EndY=0 EndZ=0
  constraints (11):
    c: Coincident(g0,g1)
    c: Coincident(g1,g2)
    c: Coincident(g2,g3)
    c: Coincident(g3,g0)
    c: Horizontal(g0)
    c: Horizontal(g2)
    c: Vertical(g1)
    c: Vertical(g3)
    c: Coincident(g0,g-1)
    c: DistanceX(g2,g2) = 100
    c: DistanceY(g3,g3) = 32.5
FEATURE [PartDesign::Pad] Pad006
  Direction = (0,0,1)
  Length = 2
  Length2 = 10
  Profile = -> Sketch162
  ReferenceAxis = -> Sketch162 [N_Axis]
  Type = 0
FEATURE [Sketcher::SketchObject] Sketch163
  FullyConstrained = false
  MapMode = 5
  Placement = pos=(0,0,2) rot=(0,0,1;0rad)
  Support = -> [Pad006]
  sketch-geometry (17):
    g0: LineSegment StartX=15 StartY=29.1324 StartZ=0 EndX=85 EndY=29.1324 EndZ=0
    g1: LineSegment StartX=85 StartY=29.1324 StartZ=0 EndX=85 EndY=11.1324 EndZ=0
    g2: LineSegment StartX=85 StartY=11.1324 StartZ=0 EndX=15 EndY=11.1324 EndZ=0
    g3: LineSegment StartX=15 StartY=11.1324 StartZ=0 EndX=15 EndY=29.1324 EndZ=0
    g4: LineSegment StartX=15 StartY=29.1324 StartZ=0 EndX=12 EndY=29.1324 EndZ=0
    g5: LineSegment StartX=12 StartY=29.1324 StartZ=0 EndX=12 EndY=20.1324 EndZ=0
    g6: Circle CenterX=12 CenterY=20.1324 CenterZ=0 NormalX=0 NormalY=0 NormalZ=1 AngleXU=0 Radius=1.75
    g7: LineSegment StartX=85 StartY=29.1324 StartZ=0 EndX=88 EndY=29.1324 EndZ=0
    g8: LineSegment StartX=88 StartY=29.1324 StartZ=0 EndX=88 EndY=20.1324 EndZ=0
    g9: LineSegment StartX=88 StartY=20.1324 StartZ=0 EndX=12 EndY=20.1324 EndZ=0
    g10: Circle CenterX=88 CenterY=20.1324 CenterZ=0 NormalX=0 NormalY=0 NormalZ=1 AngleXU=0 Radius=1.75
    g11: LineSegment StartX=15 StartY=32.5 StartZ=0 EndX=15 EndY=29.2 EndZ=0
    g12: LineSegment StartX=0 StartY=32.5 StartZ=0 EndX=15 EndY=32.5 EndZ=0
    g13: LineSegment StartX=4.5 StartY=20.1324 StartZ=0 EndX=4.5 EndY=21.89 EndZ=0
    g14: Circle CenterX=4.5 CenterY=21.89 CenterZ=0 NormalX=0 NormalY=0 NormalZ=1 AngleXU=0 Radius=1.75
    g15: LineSegment StartX=95.5 StartY=20.1324 StartZ=0 EndX=95.5 EndY=21.89 EndZ=0
    g16: Circle CenterX=95.5 CenterY=21.89 CenterZ=0 NormalX=0 NormalY=0 NormalZ=1 AngleXU=0 Radius=1.75
  constraints (39):
    c: Coincident(g0,g1)
    c: Coincident(g1,g2)
    c: Coincident(g2,g3)
    c: Coincident(g3,g0)
    c: Horizontal(g0)
    c: Horizontal(g2)
    c: Vertical(g1)
    c: Vertical(g3)
    c: DistanceX(g0,g0) = 70
    c: DistanceY(g3,g3) = 18
    c: Coincident(g4,g0)
    c: Horizontal(g4)
    c: Coincident(g5,g4)
    c: Vertical(g5)
    c: DistanceY(g5,g5) = 9
    c: Coincident(g6,g5)
    c: Coincident(g0,g7)
    c: Horizontal(g7)
    c: Coincident(g7,g8)
    c: Vertical(g8)
    c: DistanceX(g7,g7) = 3
    c: DistanceY(g8,g8) = 9
    c: Coincident(g9,g8)
    c: Coincident(g9,g6)
    c: DistanceX(g9,g9) = 76
    c: Coincident(g10,g8)
    c: Diameter(g10) = 3.5
    c: Diameter(g6) = 3.5
    c: Vertical(g11)
    c: PointOnObject(g12,g-2)
    c: Horizontal(g12)
    c: DistanceX(g12,g12) = 15
    c: DistanceY(g11,g11) = 3.3
    c: Vertical(g13)
    c: Coincident(g14,g13)
    c: Diameter(g14) = 3.5
    c: Vertical(g15)
    c: Coincident(g16,g15)
    c: Diameter(g16) = 3.5
FEATURE [PartDesign::Pocket] Pocket037
  BaseFeature = -> Pad006
  Direction = (0,0,-1)
  Length = 2
  Length2 = 5
  Profile = -> Sketch163
  ReferenceAxis = -> Sketch163 [N_Axis]
  Type = 0
FEATURE [PartDesign::Fillet] Fillet024
  Base = -> Pocket037 [Edge32,Edge31,Edge34,Edge33]
  BaseFeature = -> Pocket037
  Radius = 8.5
  SupportTransform = false
  UseAllEdges = false
FEATURE [Sketcher::SketchObject] Sketch164
  FullyConstrained = false
  MapMode = 5
  Placement = pos=(0,0,2) rot=(0,0,1;0rad)
  Support = -> [Fillet024]
  sketch-geometry (15):
    g0: LineSegment StartX=8 StartY=32.4801 StartZ=0 EndX=8 EndY=10.2801 EndZ=0
    g1: LineSegment StartX=0 StartY=0 StartZ=0 EndX=50 EndY=0 EndZ=0
    g2: LineSegment StartX=12 StartY=21.8697 StartZ=0 EndX=12 EndY=20.1197 EndZ=0
    g3: LineSegment StartX=12 StartY=20.1197 StartZ=0 EndX=0 EndY=20.1197 EndZ=0
    g4: LineSegment StartX=8 StartY=10.2801 StartZ=0 EndX=50 EndY=0 EndZ=0
    g5: LineSegment StartX=8 StartY=32.4801 StartZ=0 EndX=0 EndY=32.4801 EndZ=0
    g6: LineSegment StartX=100 StartY=32.5 StartZ=0 EndX=92 EndY=32.5 EndZ=0
    g7: LineSegment StartX=92 StartY=32.5 StartZ=0 EndX=92 EndY=10.3 EndZ=0
    g8: LineSegment StartX=92 StartY=10.3 StartZ=0 EndX=50 EndY=0 EndZ=0
    g9: LineSegment StartX=50 StartY=0 StartZ=0 EndX=0 EndY=0 EndZ=0
    g10: LineSegment StartX=8 StartY=10.2801 StartZ=0 EndX=0 EndY=10.2801 EndZ=0
    g11: LineSegment StartX=0 StartY=10.2801 StartZ=0 EndX=0 EndY=0 EndZ=0
    g12: LineSegment StartX=92 StartY=10.3 StartZ=0 EndX=100.006 EndY=10.3 EndZ=0
    g13: LineSegment StartX=100.006 StartY=10.3 StartZ=0 EndX=100.006 EndY=0 EndZ=0
    g14: LineSegment StartX=100.006 StartY=0 StartZ=0 EndX=50 EndY=0 EndZ=0
  constraints (35):
    c: Vertical(g0)
    c: Coincident(g1,g-1)
    c: PointOnObject(g1,g-1)
    c: DistanceX(g1,g1) = 50
    c: Vertical(g2)
    c: DistanceY(g2,g2) = 1.75
    c: Coincident(g3,g2)
    c: PointOnObject(g3,g-2)
    c: Horizontal(g3)
    c: DistanceX(g3,g3) = 12
    c: DistanceY(g0,g0) = 22.2
    c: Coincident(g4,g0)
    c: Coincident(g4,g1)
    c: Coincident(g5,g0)
    c: PointOnObject(g5,g-2)
    c: Horizontal(g5)
    c: Horizontal(g6)
    c: Coincident(g7,g6)
    c: Vertical(g7)
    c: Coincident(g8,g7)
    c: Coincident(g8,g4)
    c: Coincident(g9,g4)
    c: Coincident(g9,g1)
    c: Coincident(g10,g4)
    c: PointOnObject(g10,g-2)
    c: Horizontal(g10)
    c: Coincident(g11,g10)
    c: Coincident(g11,g9)
    c: Coincident(g12,g8)
    c: Horizontal(g12)
    c: Coincident(g13,g12)
    c: PointOnObject(g13,g-1)
    c: Vertical(g13)
    c: Coincident(g14,g13)
    c: Coincident(g14,g4)
FEATURE [PartDesign::Pocket] Pocket038
  BaseFeature = -> Fillet024
  Direction = (0,0,-1)
  Length = 2
  Length2 = 5
  Profile = -> Sketch164
  ReferenceAxis = -> Sketch164 [N_Axis]
  Type = 0
FEATURE [PartDesign::Fillet] Fillet025
  Base = -> Pocket038 [Edge23,Edge26,Edge30,Edge27]
  BaseFeature = -> Pocket038
  Radius = 7.5
  SupportTransform = false
  UseAllEdges = false
FEATURE [PartDesign::Fillet] Fillet026
  Base = -> Fillet025 [Edge26,Edge33]
  BaseFeature = -> Fillet025
  Radius = 10
  SupportTransform = false
  UseAllEdges = false
FEATURE [PartDesign::Fillet] Fillet027
  Base = -> Fillet026 [Edge32]
  BaseFeature = -> Fillet026
  Radius = 8
  SupportTransform = false
  UseAllEdges = false
FEATURE [PartDesign::Body] Body019  label="Single Coil Frame Middle Pickup"
  Group = -> [Sketch162,Pad006,Sketch163,Pocket037,Fillet024,Sketch164,Pocket038,Fillet025,Fillet026,Fillet027]
  Origin = -> Origin168
  Placement = pos=(175.2,370.3,45.4) rot=(0,0,1;0rad)
  Tip = -> Fillet027
FEATURE [TechDraw::DrawSVGTemplate] Template
  EditableTexts = AUTHOR_NAME=Alex Stewart; DATE=4/11/2024; DN=3, 4; DOCUMENT_TYPE=Manufacturing Drawing; OWNER_NAME=Alex Stewart; PM=Timber; PN=1; REVISION=REV A; RIGHTS=(R) DO NOT DUPLICATE THIS DRAWING TO THIRD PARTIES WITHOUT OWNER'S PERMISSION !; SCALE=1:1; SHEET=2 of 2; SIZE=A1; TITLELINE-1=Expeditioner Guitar Body Mk1; TITLELINE-2=ISO / Side Rear View; TOLERANCE=N/A
  Height = 594
  Orientation = 1
  Template = C:/Program Files/FreeCAD 0.21/data/Mod/TechDraw/Templates/A1_Landscape_ISO7200_Pep.svg
  Width = 841
FEATURE [TechDraw::DrawSVGTemplate] Template001
  EditableTexts = AUTHOR_NAME=Alex Stewart; DATE=4/11/2024; DN=1, 2; DOCUMENT_TYPE=Manufacturing Drawing; OWNER_NAME=Alex Stewart; PM=Timber; PN=1; REVISION=REV A; RIGHTS=(R) DO NOT DUPLICATE THIS DRAWING TO THIRD PARTIES WITHOUT OWNER'S PERMISSION !; SCALE=1:1; SHEET=1 of 2; SIZE=A1; TITLELINE-1=Expeditioner Guitar Body Mk1; TITLELINE-2=Front / Back View; TOLERANCE=N/A
  Height = 594
  Orientation = 1
  Template = C:/Program Files/FreeCAD 0.21/data/Mod/TechDraw/Templates/A1_Landscape_ISO7200_Pep.svg
  Width = 841
FEATURE [Sketcher::SketchObject] Sketch165
  FullyConstrained = false
  MapMode = 5
  Placement = pos=(0,0,45) rot=(0,0,1;0rad)
  Support = -> [Fillet018]
  sketch-geometry (4):
    g0: LineSegment StartX=290 StartY=161 StartZ=0 EndX=370 EndY=161 EndZ=0
    g1: LineSegment StartX=370 StartY=161 StartZ=0 EndX=370 EndY=81 EndZ=0
    g2: LineSegment StartX=370 StartY=81 StartZ=0 EndX=290 EndY=81 EndZ=0
    g3: LineSegment StartX=290 StartY=81 StartZ=0 EndX=290 EndY=161 EndZ=0
  constraints (10):
    c: Coincident(g0,g1)
    c: Coincident(g1,g2)
    c: Coincident(g2,g3)
    c: Coincident(g3,g0)
    c: Horizontal(g0)
    c: Horizontal(g2)
    c: Vertical(g1)
    c: Vertical(g3)
    c: DistanceX(g0,g0) = 80
    c: DistanceY(g1,g1) = 80
FEATURE [PartDesign::Pocket] Pocket039  label="Speaker Square Mount Pocket"
  BaseFeature = -> Fillet018
  Direction = (0,0,-1)
  Length = 3
  Length2 = 5
  Profile = -> Sketch165
  ReferenceAxis = -> Sketch165 [N_Axis]
  Type = 0
FEATURE [App::AnnotationLabel] surveyLabel002  label="Volume Label"
  BasePosition = (213.617,305.621,22.4089)
  LabelText = v 4018485.08932 mm³
  TextPosition = (0,0,0)
FEATURE [PartDesign::Fillet] Fillet028
  Base = -> Pocket039 [Edge394,Edge392,Edge405,Edge399]
  BaseFeature = -> Pocket039
  Radius = 6
  SupportTransform = false
  UseAllEdges = false
FEATURE [PartDesign::Pocket] Pocket041  label="Rear Speaker cover Mounting pocket"
  BaseFeature = -> Fillet028
  Direction = (0,0,1)
  Length = 5
  Length2 = 5
  Profile = -> Sketch142
  ReferenceAxis = -> Sketch142 [N_Axis]
  Type = 0
FEATURE [Sketcher::SketchObject] Sketch168
  FullyConstrained = false
  MapMode = 5
  Support = -> [XY_Plane169]
  sketch-geometry (2):
    g0: Circle CenterX=0 CenterY=0 CenterZ=0 NormalX=0 NormalY=0 NormalZ=1 AngleXU=0 Radius=37
    g1: Circle CenterX=0 CenterY=0 CenterZ=0 NormalX=0 NormalY=0 NormalZ=1 AngleXU=0 Radius=46.75
  constraints (3):
    c: Diameter(g0) = 74
    c: Coincident(g1,g0)
    c: Diameter(g1) = 93.5
FEATURE [PartDesign::Pad] Pad007  label="cover mounting lip"
  Direction = (0,0,1)
  Length = 5
  Length2 = 10
  Profile = -> Sketch168
  ReferenceAxis = -> Sketch168 [N_Axis]
  Type = 0
FEATURE [Sketcher::SketchObject] Sketch169
  FullyConstrained = true
  MapMode = 5
  Placement = pos=(0,0,5) rot=(0,0,1;0rad)
  Support = -> [Pad007]
  sketch-geometry (2):
    g0: Circle CenterX=0 CenterY=0 CenterZ=0 NormalX=0 NormalY=0 NormalZ=1 AngleXU=0 Radius=37
    g1: Circle CenterX=0 CenterY=0 CenterZ=0 NormalX=0 NormalY=0 NormalZ=1 AngleXU=0 Radius=39
  constraints (4):
    c: Coincident(g0,g-1)
    c: Diameter(g0) = 74
    c: Coincident(g1,g0)
    c: Diameter(g1) = 78
FEATURE [PartDesign::Pad] Pad008  label="Cylinder length"
  BaseFeature = -> Pad007
  Direction = (0,0,1)
  Length = 14
  Length2 = 10
  Profile = -> Sketch169
  ReferenceAxis = -> Sketch169 [N_Axis]
  Type = 0
FEATURE [Sketcher::SketchObject] Sketch170
  FullyConstrained = true
  MapMode = 5
  Placement = pos=(0,0,19) rot=(0,0,1;0rad)
  Support = -> [Pad008]
  sketch-geometry (1):
    g0: Circle CenterX=0 CenterY=0 CenterZ=0 NormalX=0 NormalY=0 NormalZ=1 AngleXU=0 Radius=37.5
  constraints (2):
    c: Coincident(g0,g-1)
    c: Diameter(g0) = 75
FEATURE [PartDesign::Pad] Pad009  label="Cover top"
  BaseFeature = -> Pad008
  Direction = (0,0,1)
  Length = 4
  Length2 = 10
  Profile = -> Sketch170
  ReferenceAxis = -> Sketch170 [N_Axis]
  Reversed = true
  Type = 0
FEATURE [PartDesign::Fillet] Fillet029  label="Top Edge"
  Base = -> Pad009 [Edge9]
  BaseFeature = -> Pad009
  Radius = 5
  SupportTransform = false
  UseAllEdges = false
FEATURE [PartDesign::Fillet] Fillet030  label="Mounting lip to cylinder edge"
  Base = -> Fillet029 [Edge3]
  BaseFeature = -> Fillet029
  Radius = 7.5
  SupportTransform = false
  UseAllEdges = false
FEATURE [Sketcher::SketchObject] Sketch171
  FullyConstrained = false
  MapMode = 5
  Placement = pos=(0,0,19) rot=(0,0,1;0rad)
  Support = -> [Fillet030]
  sketch-geometry (15):
    g0: Circle CenterX=0.0904534 CenterY=-3.91647e-05 CenterZ=0 NormalX=0 NormalY=0 NormalZ=1 AngleXU=0 Radius=42.25
    g1: Circle CenterX=-42.1595 CenterY=0.0181162 CenterZ=0 NormalX=0 NormalY=0 NormalZ=1 AngleXU=0 Radius=2.8
    g2: Circle CenterX=42.3405 CenterY=-0.009347 CenterZ=0 NormalX=0 NormalY=0 NormalZ=1 AngleXU=0 Radius=2.8
    g3: LineSegment StartX=0 StartY=42.16 StartZ=0 EndX=0 EndY=42.1666 EndZ=0
    g4: Circle CenterX=0 CenterY=42.1666 CenterZ=0 NormalX=0 NormalY=0 NormalZ=1 AngleXU=0 Radius=2.8
    g5: LineSegment StartX=0 StartY=-42.0004 StartZ=0 EndX=0 EndY=-42.1667 EndZ=0
    g6: Circle CenterX=0 CenterY=-42.1667 CenterZ=0 NormalX=0 NormalY=0 NormalZ=1 AngleXU=0 Radius=2.8
    g7: LineSegment StartX=-30 StartY=-30 StartZ=0 EndX=-29.788 EndY=-29.788 EndZ=0
    g8: Circle CenterX=-29.788 CenterY=-29.788 CenterZ=0 NormalX=0 NormalY=0 NormalZ=1 AngleXU=0 Radius=2.8
    g9: LineSegment StartX=30 StartY=30 StartZ=0 EndX=29.8749 EndY=29.8749 EndZ=0
    g10: Circle CenterX=29.8749 CenterY=29.8749 CenterZ=0 NormalX=0 NormalY=0 NormalZ=1 AngleXU=0 Radius=2.8
    g11: LineSegment StartX=-30 StartY=30 StartZ=0 EndX=-29.7873 EndY=29.7873 EndZ=0
    g12: Circle CenterX=-29.7873 CenterY=29.7873 CenterZ=0 NormalX=0 NormalY=0 NormalZ=1 AngleXU=0 Radius=2.8
    g13: LineSegment StartX=29.9 StartY=-29.9 StartZ=0 EndX=29.875 EndY=-29.875 EndZ=0
    g14: Circle CenterX=29.875 CenterY=-29.875 CenterZ=0 NormalX=0 NormalY=0 NormalZ=1 AngleXU=0 Radius=2.8
  constraints (21):
    c: Diameter(g0) = 84.5
    c: PointOnObject(g1,g0)
    c: Diameter(g1) = 5.6
    c: PointOnObject(g2,g0)
    c: PointOnObject(g3,g-2)
    c: PointOnObject(g3,g-2)
    c: Coincident(g4,g3)
    c: PointOnObject(g5,g-2)
    c: PointOnObject(g5,g-2)
    c: Coincident(g6,g5)
    c: Diameter(g4) = 5.6
    c: Diameter(g2) = 5.6
    c: Diameter(g6) = 5.6
    c: Coincident(g8,g7)
    c: Coincident(g10,g9)
    c: Coincident(g12,g11)
    c: Coincident(g14,g13)
    c: Diameter(g14) = 5.6
    c: Diameter(g10) = 5.6
    c: Diameter(g12) = 5.6
    c: Diameter(g8) = 5.6
FEATURE [PartDesign::Pocket] Pocket042  label="Screw Mounting Holes"
  BaseFeature = -> Fillet030
  Direction = (0,0,-1)
  Length = 16
  Length2 = 5
  Profile = -> Sketch171
  ReferenceAxis = -> Sketch171 [N_Axis]
  Type = 0
FEATURE [Sketcher::SketchObject] Sketch172
  FullyConstrained = false
  MapMode = 5
  Placement = pos=(0,0,3) rot=(0,0,1;0rad)
  Support = -> [Pocket042]
  sketch-geometry (15):
    g0: Circle CenterX=0.0904534 CenterY=-3.91647e-05 CenterZ=0 NormalX=0 NormalY=0 NormalZ=1 AngleXU=0 Radius=42.25
    g1: Circle CenterX=-42.1595 CenterY=0.0181162 CenterZ=0 NormalX=0 NormalY=0 NormalZ=1 AngleXU=0 Radius=1.75
    g2: Circle CenterX=42.3405 CenterY=-0.009347 CenterZ=0 NormalX=0 NormalY=0 NormalZ=1 AngleXU=0 Radius=1.75
    g3: LineSegment StartX=0 StartY=42.16 StartZ=0 EndX=0 EndY=42.1666 EndZ=0
    g4: Circle CenterX=0 CenterY=42.1666 CenterZ=0 NormalX=0 NormalY=0 NormalZ=1 AngleXU=0 Radius=1.75
    g5: LineSegment StartX=0 StartY=-42.0004 StartZ=0 EndX=0 EndY=-42.1667 EndZ=0
    g6: Circle CenterX=0 CenterY=-42.1667 CenterZ=0 NormalX=0 NormalY=0 NormalZ=1 AngleXU=0 Radius=1.75
    g7: LineSegment StartX=-30 StartY=-30 StartZ=0 EndX=-29.788 EndY=-29.788 EndZ=0
    g8: Circle CenterX=-29.788 CenterY=-29.788 CenterZ=0 NormalX=0 NormalY=0 NormalZ=1 AngleXU=0 Radius=1.75
    g9: LineSegment StartX=30 StartY=30 StartZ=0 EndX=29.8749 EndY=29.8749 EndZ=0
    g10: Circle CenterX=29.8749 CenterY=29.8749 CenterZ=0 NormalX=0 NormalY=0 NormalZ=1 AngleXU=0 Radius=1.75
    g11: LineSegment StartX=-30 StartY=30 StartZ=0 EndX=-29.7873 EndY=29.7873 EndZ=0
    g12: Circle CenterX=-29.7873 CenterY=29.7873 CenterZ=0 NormalX=0 NormalY=0 NormalZ=1 AngleXU=0 Radius=1.75
    g13: LineSegment StartX=29.9 StartY=-29.9 StartZ=0 EndX=29.875 EndY=-29.875 EndZ=0
    g14: Circle CenterX=29.875 CenterY=-29.875 CenterZ=0 NormalX=0 NormalY=0 NormalZ=1 AngleXU=0 Radius=1.75
  constraints (21):
    c: Diameter(g0) = 84.5
    c: PointOnObject(g1,g0)
    c: Diameter(g1) = 3.5
    c: PointOnObject(g2,g0)
    c: PointOnObject(g3,g-2)
    c: PointOnObject(g3,g-2)
    c: Coincident(g4,g3)
    c: PointOnObject(g5,g-2)
    c: PointOnObject(g5,g-2)
    c: Coincident(g6,g5)
    c: Diameter(g4) = 3.5
    c: Diameter(g2) = 3.5
    c: Diameter(g6) = 3.5
    c: Coincident(g8,g7)
    c: Coincident(g10,g9)
    c: Coincident(g12,g11)
    c: Coincident(g14,g13)
    c: Diameter(g14) = 3.5
    c: Diameter(g10) = 3.5
    c: Diameter(g12) = 3.5
    c: Diameter(g8) = 3.5
FEATURE [PartDesign::Pocket] Pocket043  label="Screw holes"
  BaseFeature = -> Pocket042
  Direction = (0,0,-1)
  Length = 3
  Length2 = 5
  Profile = -> Sketch172
  ReferenceAxis = -> Sketch172 [N_Axis]
  Type = 0
FEATURE [PartDesign::Fillet] Fillet031  label="internal edge "
  Base = -> Pocket043 [Edge73]
  BaseFeature = -> Pocket043
  Radius = 1.5
  SupportTransform = false
  UseAllEdges = false
FEATURE [PartDesign::Body] Body020  label="Rear Speaker Cover "
  Group = -> [Sketch168,Pad007,Sketch169,Pad008,Sketch170,Pad009,Fillet029,Fillet030,Sketch171,Pocket042,Sketch172,Pocket043,Fillet031]
  Origin = -> Origin169
  Placement = pos=(330,121,5) rot=(-0.566406,0.824126,0;3.14159rad)
  Tip = -> Fillet031
FEATURE [PartDesign::Body] Body021
  Origin = -> Origin173
FEATURE [App::Part] Part041  label="Electrical Wiring"
  Group = -> [Body021]
  Origin = -> Origin172
FEATURE [Sketcher::SketchObject] Sketch174
  FullyConstrained = false
  MapMode = 5
  Placement = pos=(0,0,23) rot=(0,0,1;0rad)
  sketch-geometry (4):
    g0: LineSegment StartX=247 StartY=427.9 StartZ=0 EndX=267 EndY=427.9 EndZ=0
    g1: LineSegment StartX=267 StartY=427.9 StartZ=0 EndX=267 EndY=412.9 EndZ=0
    g2: LineSegment StartX=267 StartY=412.9 StartZ=0 EndX=247 EndY=412.9 EndZ=0
    g3: LineSegment StartX=247 StartY=412.9 StartZ=0 EndX=247 EndY=427.9 EndZ=0
  constraints (10):
    c: Coincident(g0,g1)
    c: Coincident(g1,g2)
    c: Coincident(g2,g3)
    c: Coincident(g3,g0)
    c: Horizontal(g0)
    c: Horizontal(g2)
    c: Vertical(g1)
    c: Vertical(g3)
    c: DistanceX(g2,g2) = 20
    c: DistanceY(g3,g3) = 15
FEATURE [Sketcher::SketchObject] Sketch175
  FullyConstrained = false
  MapMode = 5
  Placement = pos=(0,180,0) rot=(0,0.707107,0.707107;3.14159rad)
  sketch-geometry (1):
    g0: Circle CenterX=-330 CenterY=25.5253 CenterZ=0 NormalX=0 NormalY=0 NormalZ=1 AngleXU=0 Radius=4
  constraints (1):
    c: Diameter(g0) = 8
FEATURE [PartDesign::Fillet] Fillet032  label="humbucker pocket edges"
  Base = -> Pocket041
  BaseFeature = -> Pocket041
  Radius = 6
  SupportTransform = false
  UseAllEdges = false
FEATURE [Part::Feature] Part__Feature523  label="SOLID034"
  shape: bbox 3.2 x 1.6 x 0.55 mm, 26 faces (baked)
FEATURE [App::Part] R_1206_3216Metric004
  Group = -> [Part__Feature523]
  Origin = -> Origin174
  Placement = pos=(-25.275,-4.225,1.65) rot=(0,0,-1;1.5708rad)
FEATURE [Part::Feature] Part__Feature524  label="SOLID035"
  shape: bbox 3.2 x 1.6 x 1.6 mm, 28 faces (baked)
FEATURE [App::Part] C_1206_3216Metric012
  Group = -> [Part__Feature524]
  Origin = -> Origin175
  Placement = pos=(-12.05,4.35,1.65) rot=(0,0,1;0rad)
FEATURE [Part::Feature] Part__Feature525  label="SOLID036"
  shape: bbox 6.985 x 6.828 x 5.4 mm, 41 faces (baked)
FEATURE [App::Part] CP_Elec_5x5_006  label="CP_Elec_5x5.006"
  Group = -> [Part__Feature525]
  Origin = -> Origin176
  Placement = pos=(-32.6,3.25,1.65) rot=(0,0,1;0rad)
FEATURE [Part::Feature] Part__Feature526  label="SOLID037"
  shape: bbox 3.2 x 1.6 x 1.6 mm, 28 faces (baked)
FEATURE [App::Part] C_1206_3216Metric013
  Group = -> [Part__Feature526]
  Origin = -> Origin177
  Placement = pos=(12.925,4.35,1.65) rot=(0,0,1;0rad)
FEATURE [Part::Feature] Part__Feature527  label="SOLID038"
  shape: bbox 7 x 4.95 x 4.2 mm, 162 faces (baked)
FEATURE [App::Part] JST_GH_BM03B_GHS_TBT_1x03_1MP_P1_25mm_Vertical  label="JST_GH_BM03B-GHS-TBT_1x03-1MP_P1.25mm_Vertical"
  Group = -> [Part__Feature527]
  Origin = -> Origin178
  Placement = pos=(32.3,-2.975,1.65) rot=(0,0,1;3.14159rad)
FEATURE [Part::Feature] Part__Feature528  label="SOLID039"
  shape: bbox 5.4 x 5 x 1.6 mm, 68 faces (baked)
FEATURE [App::Part] LED_WS2812B_PLCC4_5_0x5_0mm_P3_2mm  label="LED_WS2812B_PLCC4_5.0x5.0mm_P3.2mm"
  Group = -> [Part__Feature528]
  Origin = -> Origin179
  Placement = pos=(-10.75,-0.05,1.65) rot=(0,0,1;3.14159rad)
FEATURE [Part::Feature] Part__Feature529  label="SOLID040"
  shape: bbox 5.4 x 5 x 1.6 mm, 68 faces (baked)
FEATURE [App::Part] LED_WS2812B_PLCC4_5_0x5_0mm_P3_2mm012  label="LED_WS2812B_PLCC4_5.0x5.0mm_P3.2mm012"
  Group = -> [Part__Feature529]
  Origin = -> Origin180
  Placement = pos=(22.45,-0.05,1.65) rot=(0,0,1;3.14159rad)
FEATURE [Part::Feature] Part__Feature530  label="SOLID041"
  shape: bbox 3.2 x 1.6 x 1.6 mm, 28 faces (baked)
FEATURE [App::Part] C_1206_3216Metric014
  Group = -> [Part__Feature530]
  Origin = -> Origin181
  Placement = pos=(4.6,4.35,1.65) rot=(0,0,1;0rad)
FEATURE [Part::Feature] Part__Feature531  label="SOLID042"
  shape: bbox 3.2 x 1.6 x 1.6 mm, 28 faces (baked)
FEATURE [App::Part] C_1206_3216Metric015
  Group = -> [Part__Feature531]
  Origin = -> Origin182
  Placement = pos=(-3.725,4.35,1.65) rot=(0,0,1;0rad)
FEATURE [Part::Feature] Part__Feature532  label="SOLID043"
  shape: bbox 5.4 x 5 x 1.6 mm, 68 faces (baked)
FEATURE [App::Part] LED_WS2812B_PLCC4_5_0x5_0mm_P3_2mm013  label="LED_WS2812B_PLCC4_5.0x5.0mm_P3.2mm013"
  Group = -> [Part__Feature532]
  Origin = -> Origin183
  Placement = pos=(14.15,-0.05,1.65) rot=(0,0,1;3.14159rad)
FEATURE [Part::Feature] Part__Feature533  label="SOLID044"
  shape: bbox 3.2 x 1.6 x 1.6 mm, 28 faces (baked)
FEATURE [App::Part] C_1206_3216Metric016
  Group = -> [Part__Feature533]
  Origin = -> Origin184
  Placement = pos=(-20.375,4.35,1.65) rot=(0,0,1;0rad)
FEATURE [Part::Feature] Part__Feature534  label="SOLID045"
  shape: bbox 5.4 x 5 x 1.6 mm, 68 faces (baked)
FEATURE [App::Part] LED_WS2812B_PLCC4_5_0x5_0mm_P3_2mm014  label="LED_WS2812B_PLCC4_5.0x5.0mm_P3.2mm014"
  Group = -> [Part__Feature534]
  Origin = -> Origin185
  Placement = pos=(-19.05,-0.05,1.65) rot=(0,0,1;3.14159rad)
FEATURE [Part::Feature] Part__Feature535  label="SOLID046"
  shape: bbox 5.4 x 5 x 1.6 mm, 68 faces (baked)
FEATURE [App::Part] LED_WS2812B_PLCC4_5_0x5_0mm_P3_2mm015  label="LED_WS2812B_PLCC4_5.0x5.0mm_P3.2mm015"
  Group = -> [Part__Feature535]
  Origin = -> Origin186
  Placement = pos=(-2.45,-0.05,1.65) rot=(0,0,1;3.14159rad)
FEATURE [Part::Feature] Part__Feature536  label="SOLID047"
  shape: bbox 5.4 x 5 x 1.6 mm, 68 faces (baked)
FEATURE [App::Part] LED_WS2812B_PLCC4_5_0x5_0mm_P3_2mm016  label="LED_WS2812B_PLCC4_5.0x5.0mm_P3.2mm016"
  Group = -> [Part__Feature536]
  Origin = -> Origin187
  Placement = pos=(5.85,-0.05,1.65) rot=(0,0,1;3.14159rad)
FEATURE [Part::Feature] Part__Feature537  label="SOLID048"
  shape: bbox 7 x 4.95 x 4.2 mm, 162 faces (baked)
FEATURE [App::Part] JST_GH_BM03B_GHS_TBT_1x03_1MP_P1_25mm_Vertical006  label="JST_GH_BM03B-GHS-TBT_1x03-1MP_P1.25mm_Vertical006"
  Group = -> [Part__Feature537]
  Origin = -> Origin188
  Placement = pos=(-32.35,-4.125,1.65) rot=(0,0,1;3.14159rad)
FEATURE [Part::Feature] Part__Feature538  label="SOLID049"
  shape: bbox 3.2 x 1.6 x 1.6 mm, 28 faces (baked)
FEATURE [App::Part] C_1206_3216Metric017
  Group = -> [Part__Feature538]
  Origin = -> Origin189
  Placement = pos=(21.25,4.35,1.65) rot=(0,0,1;0rad)
FEATURE [Part::Feature] Part__Feature539  label="RGB LED Mounting Board PCB"
  shape: bbox 84 x 14.95 x 1.6 mm, 72 faces (baked)
FEATURE [App::Part] RGB_LED_Mounting_Board_1  label="RGB LED Mounting Board 1"
  Group = -> [R_1206_3216Metric004,C_1206_3216Metric012,CP_Elec_5x5_006,C_1206_3216Metric013,JST_GH_BM03B_GHS_TBT_1x03_1MP_P1_25mm_Vertical,LED_WS2812B_PLCC4_5_0x5_0mm_P3_2mm,LED_WS2812B_PLCC4_5_0x5_0mm_P3_2mm012,C_1206_3216Metric014,C_1206_3216Metric015,LED_WS2812B_PLCC4_5_0x5_0mm_P3_2mm013,C_1206_3216Metric016,LED_WS2812B_PLCC4_5_0x5_0mm_P3_2mm014,LED_WS2812B_PLCC4_5_0x5_0mm_P3_2mm015,+4 more]
  Origin = -> Origin190
  Placement = pos=(0.7,11,-12.1) rot=(0,0,1;0rad)
FEATURE [App::Part] Part019  label="Light 1"
  Group = -> [Part017,Part__Feature303,Part__Feature304,Part018,RGB_LED_Mounting_Board_1]
  Origin = -> Origin095
  Placement = pos=(224.6,409.8,42.1) rot=(0,0,1;0rad)
FEATURE [App::Part] Part016  label="RGB Board and Plate"
  Group = -> [Part019]
  Origin = -> Origin079
  Placement = pos=(-0.2,-0.2,0) rot=(0,0,1;0rad)
FEATURE [PartDesign::Pocket] Pocket045  label="Wire channel pockets"
  BaseFeature = -> Fillet032
  Direction = (0,0,1)
  Length = 20
  Length2 = 5
  Profile = -> Sketch155
  ReferenceAxis = -> Sketch155 [N_Axis]
  Type = 0
FEATURE [Sketcher::SketchObject] Sketch173
  FullyConstrained = false
  MapMode = 5
  Placement = pos=(0,0,21) rot=(0,0,1;0rad)
  Support = -> [Pocket045]
  sketch-geometry (24):
    g0: LineSegment StartX=253.5 StartY=460 StartZ=0 EndX=267.5 EndY=460 EndZ=0
    g1: LineSegment StartX=267.5 StartY=460 StartZ=0 EndX=267.5 EndY=441 EndZ=0
    g2: LineSegment StartX=267.5 StartY=441 StartZ=0 EndX=253.5 EndY=441 EndZ=0
    g3: LineSegment StartX=253.5 StartY=441 StartZ=0 EndX=253.5 EndY=460 EndZ=0
    g4: LineSegment StartX=196.5 StartY=441 StartZ=0 EndX=182.5 EndY=441 EndZ=0
    g5: LineSegment StartX=182.5 StartY=441 StartZ=0 EndX=182.5 EndY=460 EndZ=0
    g6: LineSegment StartX=182.5 StartY=460 StartZ=0 EndX=196.5 EndY=460 EndZ=0
    g7: LineSegment StartX=196.5 StartY=460 StartZ=0 EndX=196.5 EndY=441 EndZ=0
    g8: LineSegment StartX=196.5 StartY=400 StartZ=0 EndX=182.5 EndY=400 EndZ=0
    g9: LineSegment StartX=182.5 StartY=400 StartZ=0 EndX=182.5 EndY=381 EndZ=0
    g10: LineSegment StartX=182.5 StartY=381 StartZ=0 EndX=196.5 EndY=381 EndZ=0
    g11: LineSegment StartX=196.5 StartY=381 StartZ=0 EndX=196.5 EndY=400 EndZ=0
    g12: LineSegment StartX=253.5 StartY=400 StartZ=0 EndX=267.5 EndY=400 EndZ=0
    g13: LineSegment StartX=267.5 StartY=400 StartZ=0 EndX=267.5 EndY=381 EndZ=0
    g14: LineSegment StartX=267.5 StartY=381 StartZ=0 EndX=253.5 EndY=381 EndZ=0
    g15: LineSegment StartX=253.5 StartY=381 StartZ=0 EndX=253.5 EndY=400 EndZ=0
    g16: LineSegment StartX=180.75 StartY=347.8 StartZ=0 EndX=194.75 EndY=347.8 EndZ=0
    g17: LineSegment StartX=194.75 StartY=347.8 StartZ=0 EndX=194.75 EndY=327.8 EndZ=0
    g18: LineSegment StartX=194.75 StartY=327.8 StartZ=0 EndX=180.75 EndY=327.8 EndZ=0
    g19: LineSegment StartX=180.75 StartY=327.8 StartZ=0 EndX=180.75 EndY=347.8 EndZ=0
    g20: LineSegment StartX=255.25 StartY=347.8 StartZ=0 EndX=269.25 EndY=347.8 EndZ=0
    g21: LineSegment StartX=269.25 StartY=347.8 StartZ=0 EndX=269.25 EndY=327.8 EndZ=0
    g22: LineSegment StartX=269.25 StartY=327.8 StartZ=0 EndX=255.25 EndY=327.8 EndZ=0
    g23: LineSegment StartX=255.25 StartY=327.8 StartZ=0 EndX=255.25 EndY=347.8 EndZ=0
  constraints (60):
    c: Coincident(g0,g1)
    c: Coincident(g1,g2)
    c: Coincident(g2,g3)
    c: Coincident(g3,g0)
    c: Horizontal(g0)
    c: Horizontal(g2)
    c: Vertical(g1)
    c: Vertical(g3)
    c: DistanceX(g0,g0) = 14
    c: Coincident(g4,g5)
    c: Coincident(g5,g6)
    c: Coincident(g6,g7)
    c: Coincident(g7,g4)
    c: Horizontal(g4)
    c: Horizontal(g6)
    c: Vertical(g5)
    c: Vertical(g7)
    c: DistanceX(g4,g4) = 14
    c: DistanceY(g7,g7) = 19
    c: DistanceY(g3,g3) = 19
    c: Coincident(g8,g9)
    c: Coincident(g9,g10)
    c: Coincident(g10,g11)
    c: Coincident(g11,g8)
    c: Horizontal(g8)
    c: Horizontal(g10)
    c: Vertical(g9)
    c: Vertical(g11)
    c: DistanceX(g8,g8) = 14
    c: DistanceY(g11,g11) = 19
    c: Coincident(g12,g13)
    c: Coincident(g13,g14)
    c: Coincident(g14,g15)
    c: Coincident(g15,g12)
    c: Horizontal(g12)
    c: Horizontal(g14)
    c: Vertical(g13)
    c: Vertical(g15)
    c: DistanceX(g12,g12) = 14
    c: DistanceY(g15,g15) = 19
    c: Coincident(g16,g17)
    c: Coincident(g17,g18)
    c: Coincident(g18,g19)
    c: Coincident(g19,g16)
    c: Horizontal(g16)
    c: Horizontal(g18)
    c: Vertical(g17)
    c: Vertical(g19)
    c: DistanceX(g16,g16) = 14
    c: DistanceY(g17,g17) = 20
    c: Coincident(g20,g21)
    c: Coincident(g21,g22)
    c: Coincident(g22,g23)
    c: Coincident(g23,g20)
    c: Horizontal(g20)
    c: Horizontal(g22)
    c: Vertical(g21)
    c: Vertical(g23)
    c: DistanceX(g22,g22) = 14
    c: DistanceY(g23,g23) = 20
FEATURE [PartDesign::Pocket] Pocket046  label="pickup to wire channel holes"
  BaseFeature = -> Pocket045
  Direction = (0,0,-1)
  Length = 1
  Length2 = 5
  Profile = -> Sketch173
  ReferenceAxis = -> Sketch173 [N_Axis]
  Type = 0
FEATURE [PartDesign::Pocket] Pocket047  label="control cavity to speaker hole"
  BaseFeature = -> Pocket046
  Direction = (0,-1,2e-16)
  Length = 30
  Length2 = 5
  Profile = -> Sketch175
  ReferenceAxis = -> Sketch175 [N_Axis]
  Type = 0
FEATURE [PartDesign::Pocket] Pocket048  label="rgb board to wire channel hole"
  BaseFeature = -> Pocket047
  Direction = (0,0,-1)
  Length = 3
  Length2 = 5
  Profile = -> Sketch174
  ReferenceAxis = -> Sketch174 [N_Axis]
  Type = 0
FEATURE [Sketcher::SketchObject] Sketch177  label="Wire channels Pocket002"
  FullyConstrained = false
  MapMode = 5
  Placement = pos=(0,0,0) rot=(1,0,0;3.14159rad)
  Support = -> [Fillet018]
  sketch-geometry (29):
    g0: LineSegment StartX=101.467 StartY=-402.5 StartZ=0 EndX=130.4 EndY=-402.5 EndZ=0
    g1: LineSegment StartX=200 StartY=-200 StartZ=0 EndX=220 EndY=-200 EndZ=0
    g2: LineSegment StartX=135.4 StartY=-402.5 StartZ=0 EndX=135.4 EndY=-397.5 EndZ=0
    g3: LineSegment StartX=135.4 StartY=-397.5 StartZ=0 EndX=175 EndY=-357.904 EndZ=0
    g4: LineSegment StartX=175 StartY=-357.904 StartZ=0 EndX=175 EndY=-245 EndZ=0
    g5: LineSegment StartX=175 StartY=-245 StartZ=0 EndX=290 EndY=-245 EndZ=0
    g6: LineSegment StartX=290 StartY=-245 StartZ=0 EndX=295 EndY=-245 EndZ=0
    g7: LineSegment StartX=295 StartY=-245 StartZ=0 EndX=295 EndY=-215 EndZ=0
    g8: LineSegment StartX=295 StartY=-215 StartZ=0 EndX=290 EndY=-215 EndZ=0
    g9: LineSegment StartX=290 StartY=-215 StartZ=0 EndX=225 EndY=-215 EndZ=0
    g10: LineSegment StartX=225 StartY=-215 StartZ=0 EndX=225 EndY=-200 EndZ=0
    g11: LineSegment StartX=195 StartY=-200 StartZ=0 EndX=195 EndY=-215 EndZ=0
    g12: LineSegment StartX=195 StartY=-215 StartZ=0 EndX=168.46 EndY=-215 EndZ=0
    g13: LineSegment StartX=168.46 StartY=-215 StartZ=0 EndX=162 EndY=-198.36 EndZ=0
    g14: LineSegment StartX=162 StartY=-198.36 StartZ=0 EndX=162 EndY=-115 EndZ=0
    g15: LineSegment StartX=162 StartY=-115 StartZ=0 EndX=162 EndY=-110 EndZ=0
    g16: LineSegment StartX=162 StartY=-110 StartZ=0 EndX=157 EndY=-110 EndZ=0
    g17: LineSegment StartX=157 StartY=-110 StartZ=0 EndX=134.577 EndY=-122.534 EndZ=0
    g18: LineSegment StartX=134.577 StartY=-122.534 StartZ=0 EndX=132 EndY=-126.896 EndZ=0
    g19: LineSegment StartX=132 StartY=-126.896 StartZ=0 EndX=132 EndY=-200.027 EndZ=0
    g20: LineSegment StartX=132 StartY=-200.027 StartZ=0 EndX=144.989 EndY=-239.968 EndZ=0
    g21: LineSegment StartX=144.989 StartY=-239.968 StartZ=0 EndX=144.989 EndY=-343.839 EndZ=0
    g22: LineSegment StartX=144.989 StartY=-343.839 StartZ=0 EndX=96.4674 EndY=-392.5 EndZ=0
    g23: LineSegment StartX=96.4674 StartY=-392.5 StartZ=0 EndX=96.4674 EndY=-397.5 EndZ=0
    g24: LineSegment StartX=96.4674 StartY=-397.5 StartZ=0 EndX=96.4674 EndY=-402.5 EndZ=0
    g25: LineSegment StartX=101.467 StartY=-402.5 StartZ=0 EndX=96.4674 EndY=-402.5 EndZ=0
    g26: LineSegment StartX=130.4 StartY=-402.5 StartZ=0 EndX=135.4 EndY=-402.5 EndZ=0
    g27: LineSegment StartX=225 StartY=-200 StartZ=0 EndX=220 EndY=-200 EndZ=0
    g28: LineSegment StartX=195 StartY=-200 StartZ=0 EndX=200 EndY=-200 EndZ=0
  constraints (78):
    c: Horizontal(g0)
    c: DistanceX(g0,g0) = 28.9326
    c: Horizontal(g1)
    c: DistanceX(g1,g1) = 20
    c: Vertical(g2)
    c: Coincident(g2,g3)
    c: Coincident(g3,g4)
    c: Vertical(g4)
    c: Coincident(g4,g5)
    c: Horizontal(g5)
    c: Coincident(g5,g6)
    c: Horizontal(g6)
    c: Coincident(g6,g7)
    c: Vertical(g7)
    c: Coincident(g7,g8)
    c: Horizontal(g8)
    c: Coincident(g8,g9)
    c: Horizontal(g9)
    c: Coincident(g9,g10)
    c: Vertical(g10)
    c: Vertical(g11)
    c: Coincident(g11,g12)
    c: Horizontal(g12)
    c: Coincident(g12,g13)
    c: Coincident(g13,g14)
    c: Vertical(g14)
    c: Coincident(g14,g15)
    c: Vertical(g15)
    c: Coincident(g15,g16)
    c: Horizontal(g16)
    c: Coincident(g16,g17)
    c: Coincident(g17,g18)
    c: Coincident(g18,g19)
    c: Vertical(g19)
    c: Coincident(g19,g20)
    c: Coincident(g20,g21)
    c: Vertical(g21)
    c: Coincident(g21,g22)
    c: Coincident(g22,g23)
    c: Vertical(g23)
    c: Coincident(g23,g24)
    c: Vertical(g24)
    c: Coincident(g25,g0)
    c: Coincident(g25,g24)
    c: Horizontal(g25)
    c: Coincident(g26,g0)
    c: Coincident(g26,g2)
    c: Horizontal(g26)
    c: Coincident(g27,g10)
    c: Coincident(g27,g1)
    c: Horizontal(g27)
    c: Coincident(g28,g11)
    c: Coincident(g28,g1)
    c: Horizontal(g28)
    c: DistanceX(g25,g25) = 5
    c: DistanceX(g26,g26) = 5
    c: DistanceY(g24,g24) = 5
    c: DistanceY(g23,g23) = 5
    c: DistanceY(g2,g2) = 5
    c: Distance(g22) = 68.7186
    c: Distance(g3) = 56
    c: DistanceY(g21,g21) = 103.871
    c: DistanceY(g4,g4) = 112.904
    c: DistanceX(g5,g5) = 115
    c: DistanceX(g12,g12) = 26.54
    c: DistanceX(g9,g9) = 65
    c: Distance(g20) = 42
    c: DistanceY(g19,g19) = 73.1311
    c: DistanceY(g14,g14) = 83.36
    c: DistanceX(g27,g27) = 5
    c: DistanceX(g28,g28) = 5
    c: DistanceX(g8,g8) = 5
    c: DistanceX(g6,g6) = 5
    c: DistanceY(g7,g7) = 30
    c: Distance(g17) = 25.6886
    c: Distance(g18) = 5.06593
    c: Distance(g16) = 5
    c: DistanceY(g15,g15) = 5
FEATURE [PartDesign::Pocket] Pocket049  label="afpi batt and io plate channel mounting plate lip pocket"
  BaseFeature = -> Pocket048
  Direction = (0,0,1)
  Length = 3
  Length2 = 5
  Profile = -> Sketch177
  ReferenceAxis = -> Sketch177 [N_Axis]
  Type = 0
FEATURE [Sketcher::SketchObject] Sketch178  label="Underside plate pocket001"
  FullyConstrained = false
  MapMode = 5
  Placement = pos=(0,0,0) rot=(1,0,0;3.14159rad)
  sketch-geometry (11):
    g0: ArcOfCircle CenterX=250 CenterY=-459.965 CenterZ=0 NormalX=0 NormalY=0 NormalZ=1 AngleXU=0 Radius=10.0011 StartAngle=3.14501 EndAngle=4.71235
    g1: ArcOfCircle CenterX=290.043 CenterY=-460 CenterZ=0 NormalX=0 NormalY=0 NormalZ=1 AngleXU=0 Radius=9.96676 StartAngle=4.70814 EndAngle=6.28304
    g2: ArcOfCircle CenterX=192.411 CenterY=-438.241 CenterZ=0 NormalX=0 NormalY=0 NormalZ=1 AngleXU=0 Radius=48.2966 StartAngle=0.171466 EndAngle=1.62074
    g3: ArcOfCircle CenterX=189.983 CenterY=-379.994 CenterZ=0 NormalX=0 NormalY=0 NormalZ=1 AngleXU=0 Radius=10.0109 StartAngle=3.14223 EndAngle=4.71402
    g4: ArcOfCircle CenterX=648.991 CenterY=-407.85 CenterZ=0 NormalX=0 NormalY=0 NormalZ=1 AngleXU=0 Radius=352.857 StartAngle=2.69985 EndAngle=3.28993
    g5: LineSegment StartX=179.972 StartY=-380 StartZ=0 EndX=179.972 EndY=-256.999 EndZ=0
    g6: ArcOfCircle CenterX=189.994 CenterY=-257.016 CenterZ=0 NormalX=0 NormalY=0 NormalZ=1 AngleXU=0 Radius=10.0214 StartAngle=1.57135 EndAngle=3.13987
    g7: ArcOfCircle CenterX=320 CenterY=-257 CenterZ=0 NormalX=0 NormalY=0 NormalZ=1 AngleXU=0 Radius=10.0052 StartAngle=0.000134912 EndAngle=1.57136
    g8: LineSegment StartX=319.994 StartY=-246.995 StartZ=0 EndX=189.988 EndY=-246.995 EndZ=0
    g9: LineSegment StartX=239.999 StartY=-430 StartZ=0 EndX=239.999 EndY=-459.999 EndZ=0
    g10: LineSegment StartX=250 StartY=-469.966 StartZ=0 EndX=290 EndY=-469.966 EndZ=0
  constraints (15):
    c: Coincident(g3,g2)
    c: Coincident(g4,g1)
    c: Coincident(g5,g3)
    c: Vertical(g5)
    c: Coincident(g6,g5)
    c: Coincident(g7,g4)
    c: Coincident(g8,g7)
    c: Coincident(g8,g6)
    c: Horizontal(g8)
    c: Coincident(g9,g2)
    c: Coincident(g9,g0)
    c: Vertical(g9)
    c: Coincident(g10,g0)
    c: Coincident(g10,g1)
    c: Horizontal(g10)
FEATURE [PartDesign::Pad] Pad010
  Direction = (0,0,-1)
  Length = 3
  Length2 = 10
  Placement = pos=(0,0,0) rot=(1,0,0;3.14159rad)
  Profile = -> Sketch178
  ReferenceAxis = -> Sketch178 [N_Axis]
  Type = 0
FEATURE [PartDesign::Fillet] Fillet033
  Base = -> Pad010 [Edge28,Edge25,Edge22,Edge19,Edge16,Edge13,Edge10,Edge7,Edge4,Edge33,Edge31]
  BaseFeature = -> Pad010
  Placement = pos=(0,0,0) rot=(1,0,0;3.14159rad)
  Radius = 2.5
  SupportTransform = false
  UseAllEdges = false
FEATURE [Sketcher::SketchObject] Sketch179
  FullyConstrained = false
  MapMode = 5
  Placement = pos=(0,0,-3) rot=(1,0,0;3.14159rad)
  Support = -> [Fillet033]
  sketch-geometry (51):
    g0: LineSegment StartX=290 StartY=-465 StartZ=0 EndX=270 EndY=-465 EndZ=0
    g1: LineSegment StartX=270 StartY=-465 StartZ=0 EndX=250 EndY=-465 EndZ=0
    g2: LineSegment StartX=250 StartY=-465 StartZ=0 EndX=245 EndY=-445.592 EndZ=0
    g3: LineSegment StartX=245 StartY=-445.592 StartZ=0 EndX=245 EndY=-425.5 EndZ=0
    g4: LineSegment StartX=245 StartY=-425.5 StartZ=0 EndX=239 EndY=-406.4 EndZ=0
    g5: LineSegment StartX=239 StartY=-406.4 StartZ=0 EndX=224.413 EndY=-392.651 EndZ=0
    g6: LineSegment StartX=290 StartY=-465 StartZ=0 EndX=288 EndY=-445 EndZ=0
    g7: LineSegment StartX=288 StartY=-445 StartZ=0 EndX=290 EndY=-425 EndZ=0
    g8: LineSegment StartX=290 StartY=-425 StartZ=0 EndX=289 EndY=-405 EndZ=0
    g9: LineSegment StartX=289 StartY=-405 StartZ=0 EndX=290 EndY=-385 EndZ=0
    g10: LineSegment StartX=290 StartY=-385 StartZ=0 EndX=292 EndY=-365 EndZ=0
    g11: LineSegment StartX=292 StartY=-365 StartZ=0 EndX=294 EndY=-345 EndZ=0
    g12: LineSegment StartX=294 StartY=-345 StartZ=0 EndX=299 EndY=-325.584 EndZ=0
    g13: LineSegment StartX=299 StartY=-325.584 StartZ=0 EndX=304 EndY=-306.2 EndZ=0
    g14: LineSegment StartX=304 StartY=-306.2 StartZ=0 EndX=310 EndY=-287.1 EndZ=0
    g15: LineSegment StartX=310 StartY=-287.1 StartZ=0 EndX=318 EndY=-268.708 EndZ=0
    g16: LineSegment StartX=318 StartY=-268.708 StartZ=0 EndX=323 EndY=-256 EndZ=0
    g17: LineSegment StartX=323 StartY=-256 StartZ=0 EndX=298.1 EndY=-253.1 EndZ=0
    g18: LineSegment StartX=298.1 StartY=-253.1 StartZ=0 EndX=278.1 EndY=-253.1 EndZ=0
    g19: LineSegment StartX=278.1 StartY=-253.1 StartZ=0 EndX=258.1 EndY=-253.1 EndZ=0
    g20: LineSegment StartX=258.1 StartY=-253.1 StartZ=0 EndX=238.1 EndY=-253.1 EndZ=0
    g21: LineSegment StartX=238.1 StartY=-253.1 StartZ=0 EndX=218.1 EndY=-253.1 EndZ=0
    g22: LineSegment StartX=218.1 StartY=-253.1 StartZ=0 EndX=198.1 EndY=-253.1 EndZ=0
    g23: LineSegment StartX=198.1 StartY=-253.1 StartZ=0 EndX=185 EndY=-268.3 EndZ=0
    g24: LineSegment StartX=185 StartY=-268.3 StartZ=0 EndX=185 EndY=-288.3 EndZ=0
    g25: LineSegment StartX=185 StartY=-288.3 StartZ=0 EndX=185 EndY=-308.3 EndZ=0
    g26: LineSegment StartX=185 StartY=-308.3 StartZ=0 EndX=185 EndY=-328.3 EndZ=0
    g27: LineSegment StartX=185 StartY=-328.3 StartZ=0 EndX=185 EndY=-348.3 EndZ=0
    g28: LineSegment StartX=185 StartY=-348.3 StartZ=0 EndX=185 EndY=-368.3 EndZ=0
    g29: LineSegment StartX=185 StartY=-368.3 StartZ=0 EndX=190 EndY=-382 EndZ=0
    g30: LineSegment StartX=190 StartY=-382 StartZ=0 EndX=214 EndY=-388 EndZ=0
    g31: LineSegment StartX=214 StartY=-388 StartZ=0 EndX=224.413 EndY=-392.651 EndZ=0
    g32: Circle CenterX=290 CenterY=-465 CenterZ=0 NormalX=0 NormalY=0 NormalZ=1 AngleXU=0 Radius=1.65
    g33: Circle CenterX=270 CenterY=-465 CenterZ=0 NormalX=0 NormalY=0 NormalZ=1 AngleXU=0 Radius=1.65
    g34: Circle CenterX=250 CenterY=-465 CenterZ=0 NormalX=0 NormalY=0 NormalZ=1 AngleXU=0 Radius=1.65
    g35: Circle CenterX=245 CenterY=-425.5 CenterZ=0 NormalX=0 NormalY=0 NormalZ=1 AngleXU=0 Radius=1.65
    g36: Circle CenterX=214 CenterY=-388 CenterZ=0 NormalX=0 NormalY=0 NormalZ=1 AngleXU=0 Radius=1.65
    g37: Circle CenterX=190 CenterY=-382 CenterZ=0 NormalX=0 NormalY=0 NormalZ=1 AngleXU=0 Radius=1.65
    g38: Circle CenterX=185 CenterY=-348.3 CenterZ=0 NormalX=0 NormalY=0 NormalZ=1 AngleXU=0 Radius=1.65
    g39: Circle CenterX=185 CenterY=-308.3 CenterZ=0 NormalX=0 NormalY=0 NormalZ=1 AngleXU=0 Radius=1.65
    g40: Circle CenterX=185 CenterY=-268.3 CenterZ=0 NormalX=0 NormalY=0 NormalZ=1 AngleXU=0 Radius=1.65
    g41: Circle CenterX=198.1 CenterY=-253.1 CenterZ=0 NormalX=0 NormalY=0 NormalZ=1 AngleXU=0 Radius=1.65
    g42: Circle CenterX=238.1 CenterY=-253.1 CenterZ=0 NormalX=0 NormalY=0 NormalZ=1 AngleXU=0 Radius=1.65
    g43: Circle CenterX=278.1 CenterY=-253.1 CenterZ=0 NormalX=0 NormalY=0 NormalZ=1 AngleXU=0 Radius=1.65
    g44: Circle CenterX=298.1 CenterY=-253.1 CenterZ=0 NormalX=0 NormalY=0 NormalZ=1 AngleXU=0 Radius=1.65
    g45: Circle CenterX=323 CenterY=-256 CenterZ=0 NormalX=0 NormalY=0 NormalZ=1 AngleXU=0 Radius=1.65
    g46: Circle CenterX=318 CenterY=-268.708 CenterZ=0 NormalX=0 NormalY=0 NormalZ=1 AngleXU=0 Radius=1.65
    g47: Circle CenterX=304 CenterY=-306.2 CenterZ=0 NormalX=0 NormalY=0 NormalZ=1 AngleXU=0 Radius=1.65
    g48: Circle CenterX=294 CenterY=-345 CenterZ=0 NormalX=0 NormalY=0 NormalZ=1 AngleXU=0 Radius=1.65
    g49: Circle CenterX=290 CenterY=-385 CenterZ=0 NormalX=0 NormalY=0 NormalZ=1 AngleXU=0 Radius=1.65
    g50: Circle CenterX=290 CenterY=-425 CenterZ=0 NormalX=0 NormalY=0 NormalZ=1 AngleXU=0 Radius=1.65
  constraints (66):
    c: Horizontal(g0)
    c: Coincident(g1,g0)
    c: Horizontal(g1)
    c: Coincident(g2,g1)
    c: Coincident(g3,g2)
    c: Vertical(g3)
    c: Coincident(g4,g3)
    c: Coincident(g4,g5)
    c: Coincident(g0,g6)
    c: Coincident(g6,g7)
    c: Coincident(g7,g8)
    c: Coincident(g8,g9)
    c: Coincident(g9,g10)
    c: Coincident(g10,g11)
    c: Coincident(g11,g12)
    c: Coincident(g12,g13)
    c: Coincident(g13,g14)
    c: Coincident(g14,g15)
    c: Coincident(g15,g16)
    c: Coincident(g16,g17)
    c: Coincident(g17,g18)
    c: Horizontal(g18)
    c: Coincident(g18,g19)
    c: Horizontal(g19)
    c: Coincident(g19,g20)
    c: Horizontal(g20)
    c: Coincident(g20,g21)
    c: Horizontal(g21)
    c: Coincident(g21,g22)
    c: Horizontal(g22)
    c: Coincident(g22,g23)
    c: Coincident(g23,g24)
    c: Vertical(g24)
    c: Coincident(g24,g25)
    c: Vertical(g25)
    c: Coincident(g25,g26)
    c: Vertical(g26)
    c: Coincident(g26,g27)
    c: Vertical(g27)
    c: Coincident(g27,g28)
    c: Vertical(g28)
    c: Coincident(g28,g29)
    c: Coincident(g29,g30)
    c: Coincident(g30,g31)
    c: Coincident(g31,g5)
    c: Coincident(g32,g0)
    c: Coincident(g33,g0)
    c: Coincident(g34,g1)
    c: Coincident(g35,g3)
    c: Coincident(g36,g30)
    c: Coincident(g37,g29)
    c: Coincident(g38,g27)
    c: Coincident(g39,g25)
    c: Coincident(g40,g23)
    c: Coincident(g41,g22)
    c: Coincident(g42,g20)
    c: Coincident(g43,g18)
    c: Coincident(g44,g17)
    c: Coincident(g45,g16)
    c: Coincident(g46,g15)
    c: Coincident(g47,g13)
    c: Coincident(g48,g11)
    c: Coincident(g49,g9)
    c: Coincident(g50,g7)
    c: Equal(g32, g33-g50) x18
    c: Diameter(g32) = 3.3
FEATURE [PartDesign::Pocket] Pocket050
  BaseFeature = -> Fillet033
  Direction = (0,0,1)
  Length = 3
  Length2 = 5
  Placement = pos=(0,0,0) rot=(1,0,0;3.14159rad)
  Profile = -> Sketch179
  ReferenceAxis = -> Sketch179 [N_Axis]
  Type = 0
FEATURE [Sketcher::SketchObject] Sketch181
  FullyConstrained = false
  MapMode = 5
  Placement = pos=(0,0,-3) rot=(1,0,0;3.14159rad)
  Support = -> [Pocket050]
  sketch-geometry (4):
    g0: LineSegment StartX=190 StartY=-270.2 StartZ=0 EndX=260 EndY=-270.2 EndZ=0
    g1: LineSegment StartX=260 StartY=-270.2 StartZ=0 EndX=260 EndY=-281.2 EndZ=0
    g2: LineSegment StartX=260 StartY=-281.2 StartZ=0 EndX=190 EndY=-281.2 EndZ=0
    g3: LineSegment StartX=190 StartY=-281.2 StartZ=0 EndX=190 EndY=-270.2 EndZ=0
  constraints (10):
    c: Coincident(g0,g1)
    c: Coincident(g1,g2)
    c: Coincident(g2,g3)
    c: Coincident(g3,g0)
    c: Horizontal(g0)
    c: Horizontal(g2)
    c: Vertical(g1)
    c: Vertical(g3)
    c: DistanceX(g0,g0) = 70
    c: DistanceY(g1,g1) = 11
FEATURE [PartDesign::Pocket] Pocket051
  BaseFeature = -> Pocket050
  Direction = (0,-1e-16,1)
  Length = 3
  Length2 = 5
  Placement = pos=(0,0,0) rot=(1,0,0;3.14159rad)
  Profile = -> Sketch181
  ReferenceAxis = -> Sketch181 [N_Axis]
  Type = 0
FEATURE [PartDesign::Fillet] Fillet034
  Base = -> Pocket051 [Edge99,Edge98,Edge97,Edge100]
  BaseFeature = -> Pocket051
  Placement = pos=(0,0,0) rot=(1,0,0;3.14159rad)
  Radius = 3
  SupportTransform = false
  UseAllEdges = false
FEATURE [PartDesign::Body] Body022  label="Back Plate 1"
  Group = -> [Sketch178,Pad010,Fillet033,Sketch179,Pocket050,Sketch181,Pocket051,Fillet034]
  Origin = -> Origin191
  Tip = -> Fillet034
FEATURE [Sketcher::SketchObject] Sketch182  label="Wire channels Pocket003"
  FullyConstrained = false
  MapMode = 5
  Placement = pos=(0,0,0) rot=(1,0,0;3.14159rad)
  sketch-geometry (29):
    g0: LineSegment StartX=101.467 StartY=-402.5 StartZ=0 EndX=130.4 EndY=-402.5 EndZ=0
    g1: LineSegment StartX=200 StartY=-200 StartZ=0 EndX=220 EndY=-200 EndZ=0
    g2: LineSegment StartX=135.4 StartY=-402.5 StartZ=0 EndX=135.4 EndY=-397.5 EndZ=0
    g3: LineSegment StartX=135.4 StartY=-397.5 StartZ=0 EndX=175 EndY=-357.904 EndZ=0
    g4: LineSegment StartX=175 StartY=-357.904 StartZ=0 EndX=175 EndY=-245 EndZ=0
    g5: LineSegment StartX=175 StartY=-245 StartZ=0 EndX=290 EndY=-245 EndZ=0
    g6: LineSegment StartX=290 StartY=-245 StartZ=0 EndX=295 EndY=-245 EndZ=0
    g7: LineSegment StartX=295 StartY=-245 StartZ=0 EndX=295 EndY=-215 EndZ=0
    g8: LineSegment StartX=295 StartY=-215 StartZ=0 EndX=290 EndY=-215 EndZ=0
    g9: LineSegment StartX=290 StartY=-215 StartZ=0 EndX=225 EndY=-215 EndZ=0
    g10: LineSegment StartX=225 StartY=-215 StartZ=0 EndX=225 EndY=-200 EndZ=0
    g11: LineSegment StartX=195 StartY=-200 StartZ=0 EndX=195 EndY=-215 EndZ=0
    g12: LineSegment StartX=195 StartY=-215 StartZ=0 EndX=168.46 EndY=-215 EndZ=0
    g13: LineSegment StartX=168.46 StartY=-215 StartZ=0 EndX=162 EndY=-198.36 EndZ=0
    g14: LineSegment StartX=162 StartY=-198.36 StartZ=0 EndX=162 EndY=-115 EndZ=0
    g15: LineSegment StartX=162 StartY=-115 StartZ=0 EndX=162 EndY=-110 EndZ=0
    g16: LineSegment StartX=162 StartY=-110 StartZ=0 EndX=157 EndY=-110 EndZ=0
    g17: LineSegment StartX=157 StartY=-110 StartZ=0 EndX=134.577 EndY=-122.534 EndZ=0
    g18: LineSegment StartX=134.577 StartY=-122.534 StartZ=0 EndX=132 EndY=-126.896 EndZ=0
    g19: LineSegment StartX=132 StartY=-126.896 StartZ=0 EndX=132 EndY=-200.027 EndZ=0
    g20: LineSegment StartX=132 StartY=-200.027 StartZ=0 EndX=144.989 EndY=-239.968 EndZ=0
    g21: LineSegment StartX=144.989 StartY=-239.968 StartZ=0 EndX=144.989 EndY=-343.839 EndZ=0
    g22: LineSegment StartX=144.989 StartY=-343.839 StartZ=0 EndX=96.4674 EndY=-392.5 EndZ=0
    g23: LineSegment StartX=96.4674 StartY=-392.5 StartZ=0 EndX=96.4674 EndY=-397.5 EndZ=0
    g24: LineSegment StartX=96.4674 StartY=-397.5 StartZ=0 EndX=96.4674 EndY=-402.5 EndZ=0
    g25: LineSegment StartX=101.467 StartY=-402.5 StartZ=0 EndX=96.4674 EndY=-402.5 EndZ=0
    g26: LineSegment StartX=130.4 StartY=-402.5 StartZ=0 EndX=135.4 EndY=-402.5 EndZ=0
    g27: LineSegment StartX=225 StartY=-200 StartZ=0 EndX=220 EndY=-200 EndZ=0
    g28: LineSegment StartX=195 StartY=-200 StartZ=0 EndX=200 EndY=-200 EndZ=0
  constraints (78):
    c: Horizontal(g0)
    c: DistanceX(g0,g0) = 28.9326
    c: Horizontal(g1)
    c: DistanceX(g1,g1) = 20
    c: Vertical(g2)
    c: Coincident(g2,g3)
    c: Coincident(g3,g4)
    c: Vertical(g4)
    c: Coincident(g4,g5)
    c: Horizontal(g5)
    c: Coincident(g5,g6)
    c: Horizontal(g6)
    c: Coincident(g6,g7)
    c: Vertical(g7)
    c: Coincident(g7,g8)
    c: Horizontal(g8)
    c: Coincident(g8,g9)
    c: Horizontal(g9)
    c: Coincident(g9,g10)
    c: Vertical(g10)
    c: Vertical(g11)
    c: Coincident(g11,g12)
    c: Horizontal(g12)
    c: Coincident(g12,g13)
    c: Coincident(g13,g14)
    c: Vertical(g14)
    c: Coincident(g14,g15)
    c: Vertical(g15)
    c: Coincident(g15,g16)
    c: Horizontal(g16)
    c: Coincident(g16,g17)
    c: Coincident(g17,g18)
    c: Coincident(g18,g19)
    c: Vertical(g19)
    c: Coincident(g19,g20)
    c: Coincident(g20,g21)
    c: Vertical(g21)
    c: Coincident(g21,g22)
    c: Coincident(g22,g23)
    c: Vertical(g23)
    c: Coincident(g23,g24)
    c: Vertical(g24)
    c: Coincident(g25,g0)
    c: Coincident(g25,g24)
    c: Horizontal(g25)
    c: Coincident(g26,g0)
    c: Coincident(g26,g2)
    c: Horizontal(g26)
    c: Coincident(g27,g10)
    c: Coincident(g27,g1)
    c: Horizontal(g27)
    c: Coincident(g28,g11)
    c: Coincident(g28,g1)
    c: Horizontal(g28)
    c: DistanceX(g25,g25) = 5
    c: DistanceX(g26,g26) = 5
    c: DistanceY(g24,g24) = 5
    c: DistanceY(g23,g23) = 5
    c: DistanceY(g2,g2) = 5
    c: Distance(g22) = 68.7186
    c: Distance(g3) = 56
    c: DistanceY(g21,g21) = 103.871
    c: DistanceY(g4,g4) = 112.904
    c: DistanceX(g5,g5) = 115
    c: DistanceX(g12,g12) = 26.54
    c: DistanceX(g9,g9) = 65
    c: Distance(g20) = 42
    c: DistanceY(g19,g19) = 73.1311
    c: DistanceY(g14,g14) = 83.36
    c: DistanceX(g27,g27) = 5
    c: DistanceX(g28,g28) = 5
    c: DistanceX(g8,g8) = 5
    c: DistanceX(g6,g6) = 5
    c: DistanceY(g7,g7) = 30
    c: Distance(g17) = 25.6886
    c: Distance(g18) = 5.06593
    c: Distance(g16) = 5
    c: DistanceY(g15,g15) = 5
FEATURE [PartDesign::Pad] Pad011
  Direction = (0,0,-1)
  Length = 3
  Length2 = 10
  Placement = pos=(0,0,0) rot=(1,0,0;3.14159rad)
  Profile = -> Sketch182
  ReferenceAxis = -> Sketch182 [N_Axis]
  Type = 0
FEATURE [PartDesign::Fillet] Fillet035  label="AFPI batt and IO plate channel edges"
  Base = -> Pocket049 [Edge1015,Edge741,Edge1014,Edge739,Edge736,Edge963,Edge984,Edge783,Edge1022,Edge781,Edge1023,Edge779,Edge1016,Edge745,Edge1020,Edge765,Edge1018,Edge767,Edge769,Edge771,Edge773,Edge775,Edge747,Edge1017,Edge1021,Edge763,Edge761,Edge996,Edge997,Edge749,Edge1038]
  BaseFeature = -> Pocket049
  Radius = 3.35
  SupportTransform = false
  UseAllEdges = false
FEATURE [PartDesign::Fillet] Fillet036
  Base = -> Pad011 [Edge2,Edge5,Edge8,Edge14,Edge17,Edge20,Edge23,Edge26,Edge29,Edge32,Edge35,Edge53,Edge56,Edge59,Edge65,Edge68,Edge74]
  BaseFeature = -> Pad011
  Placement = pos=(0,0,0) rot=(1,0,0;3.14159rad)
  Radius = 3.35
  SupportTransform = false
  UseAllEdges = false
FEATURE [Sketcher::SketchObject] Sketch183
  FullyConstrained = false
  MapMode = 5
  Placement = pos=(0,0,-3) rot=(1,0,0;3.14159rad)
  Support = -> [Fillet036]
  sketch-geometry (38):
    g0: Circle CenterX=105 CenterY=-389 CenterZ=0 NormalX=0 NormalY=0 NormalZ=1 AngleXU=0 Radius=1.15
    g1: Circle CenterX=145 CenterY=-349 CenterZ=0 NormalX=0 NormalY=0 NormalZ=1 AngleXU=0 Radius=1.15
    g2: Circle CenterX=147.5 CenterY=-309 CenterZ=0 NormalX=0 NormalY=0 NormalZ=1 AngleXU=0 Radius=1.15
    g3: Circle CenterX=147.5 CenterY=-259 CenterZ=0 NormalX=0 NormalY=0 NormalZ=1 AngleXU=0 Radius=1.15
    g4: Circle CenterX=172.5 CenterY=-259 CenterZ=0 NormalX=0 NormalY=0 NormalZ=1 AngleXU=0 Radius=1.15
    g5: Circle CenterX=172.5 CenterY=-309 CenterZ=0 NormalX=0 NormalY=0 NormalZ=1 AngleXU=0 Radius=1.15
    g6: Circle CenterX=172.5 CenterY=-349 CenterZ=0 NormalX=0 NormalY=0 NormalZ=1 AngleXU=0 Radius=1.15
    g7: Circle CenterX=147.665 CenterY=-382.765 CenterZ=0 NormalX=0 NormalY=0 NormalZ=1 AngleXU=0 Radius=1.15
    g8: LineSegment StartX=147.5 StartY=-259 StartZ=0 EndX=147.5 EndY=-239 EndZ=0
    g9: LineSegment StartX=147.5 StartY=-239 StartZ=0 EndX=141 EndY=-220 EndZ=0
    g10: LineSegment StartX=141 StartY=-220 StartZ=0 EndX=134.428 EndY=-201 EndZ=0
    g11: LineSegment StartX=134.428 StartY=-201 StartZ=0 EndX=134.428 EndY=-161 EndZ=0
    g12: LineSegment StartX=134.428 StartY=-161 StartZ=0 EndX=134.428 EndY=-131 EndZ=0
    g13: LineSegment StartX=134.428 StartY=-131.025 StartZ=0 EndX=137 EndY=-124 EndZ=0
    g14: LineSegment StartX=137 StartY=-124 StartZ=0 EndX=146.85 EndY=-118.15 EndZ=0
    g15: LineSegment StartX=172.5 StartY=-259 StartZ=0 EndX=178 EndY=-242.5 EndZ=0
    g16: LineSegment StartX=178 StartY=-242.5 StartZ=0 EndX=218 EndY=-242.5 EndZ=0
    g17: LineSegment StartX=218 StartY=-242.5 StartZ=0 EndX=258 EndY=-242.5 EndZ=0
    g18: LineSegment StartX=258 StartY=-242.5 StartZ=0 EndX=292 EndY=-242.5 EndZ=0
    g19: Circle CenterX=178 CenterY=-242.5 CenterZ=0 NormalX=0 NormalY=0 NormalZ=1 AngleXU=0 Radius=1.15
    g20: Circle CenterX=218 CenterY=-242.5 CenterZ=0 NormalX=0 NormalY=0 NormalZ=1 AngleXU=0 Radius=1.15
    g21: Circle CenterX=258 CenterY=-242.5 CenterZ=0 NormalX=0 NormalY=0 NormalZ=1 AngleXU=0 Radius=1.15
    g22: Circle CenterX=258 CenterY=-217.5 CenterZ=0 NormalX=0 NormalY=0 NormalZ=1 AngleXU=0 Radius=1.15
    g23: Circle CenterX=292 CenterY=-242.5 CenterZ=0 NormalX=0 NormalY=0 NormalZ=1 AngleXU=0 Radius=1.15
    g24: Circle CenterX=292 CenterY=-217.5 CenterZ=0 NormalX=0 NormalY=0 NormalZ=1 AngleXU=0 Radius=1.15
    g25: Circle CenterX=292.5 CenterY=-230 CenterZ=0 NormalX=0 NormalY=0 NormalZ=1 AngleXU=0 Radius=1.15
    g26: Circle CenterX=223 CenterY=-217 CenterZ=0 NormalX=0 NormalY=0 NormalZ=1 AngleXU=0 Radius=1.15
    g27: Circle CenterX=197 CenterY=-217 CenterZ=0 NormalX=0 NormalY=0 NormalZ=1 AngleXU=0 Radius=1.15
    g28: Circle CenterX=166.11 CenterY=-217.11 CenterZ=0 NormalX=0 NormalY=0 NormalZ=1 AngleXU=0 Radius=1.15
    g29: Circle CenterX=147.5 CenterY=-239 CenterZ=0 NormalX=0 NormalY=0 NormalZ=1 AngleXU=0 Radius=1.15
    g30: Circle CenterX=141 CenterY=-220 CenterZ=0 NormalX=0 NormalY=0 NormalZ=1 AngleXU=0 Radius=1.15
    g31: Circle CenterX=134.428 CenterY=-201 CenterZ=0 NormalX=0 NormalY=0 NormalZ=1 AngleXU=0 Radius=1.15
    g32: Circle CenterX=160.15 CenterY=-201 CenterZ=0 NormalX=0 NormalY=0 NormalZ=1 AngleXU=0 Radius=1.15
    g33: Circle CenterX=134.428 CenterY=-161 CenterZ=0 NormalX=0 NormalY=0 NormalZ=1 AngleXU=0 Radius=1.15
    g34: Circle CenterX=159.5 CenterY=-161 CenterZ=0 NormalX=0 NormalY=0 NormalZ=1 AngleXU=0 Radius=1.15
    g35: Circle CenterX=137 CenterY=-124 CenterZ=0 NormalX=0 NormalY=0 NormalZ=1 AngleXU=0 Radius=1.15
    g36: Circle CenterX=146.85 CenterY=-118.15 CenterZ=0 NormalX=0 NormalY=0 NormalZ=1 AngleXU=0 Radius=1.15
    g37: Circle CenterX=159 CenterY=-113 CenterZ=0 NormalX=0 NormalY=0 NormalZ=1 AngleXU=0 Radius=1.15
  constraints (50):
    c: Diameter(g0) = 2.3
    c: Diameter(g1) = 2.3
    c: Diameter(g2) = 2.3
    c: Diameter(g7) = 2.3
    c: Diameter(g6) = 2.3
    c: Diameter(g5) = 2.3
    c: Diameter(g3) = 2.3
    c: Diameter(g4) = 2.3
    c: Coincident(g8,g3)
    c: Vertical(g8)
    c: Coincident(g9,g8)
    c: Coincident(g10,g9)
    c: Coincident(g11,g10)
    c: Vertical(g11)
    c: Coincident(g12,g11)
    c: Vertical(g12)
    c: PointOnObject(g13,g12)
    c: Coincident(g14,g13)
    c: Coincident(g15,g4)
    c: Coincident(g16,g15)
    c: Horizontal(g16)
    c: Coincident(g17,g16)
    c: Horizontal(g17)
    c: Coincident(g18,g17)
    c: Horizontal(g18)
    c: Coincident(g19,g15)
    c: Coincident(g20,g16)
    c: Coincident(g21,g17)
    c: Coincident(g23,g18)
    c: Coincident(g29,g8)
    c: Coincident(g30,g9)
    c: Coincident(g31,g10)
    c: Coincident(g33,g11)
    c: Coincident(g35,g13)
    c: Coincident(g36,g14)
    c: Equal(g29,g30)
    c: Equal(g29,g19)
    c: Equal(g29,g28)
    c: Equal(g29,g27)
    c: Equal(g29,g26)
    c: Equal(g29,g20)
    c: Equal(g29,g21)
    c: Equal(g29,g22)
    c: Equal(g29,g24)
    c: Equal(g29,g23)
    c: Equal(g29,g25)
    c: Equal(g29,g32)
    c: Equal(g29,g31)
    c: Equal(g29, g33-g37) x5
    c: Diameter(g29) = 2.3
FEATURE [PartDesign::Pocket] Pocket052
  BaseFeature = -> Fillet036
  Direction = (0,-1e-16,1)
  Length = 3
  Length2 = 5
  Placement = pos=(0,0,0) rot=(1,0,0;3.14159rad)
  Profile = -> Sketch183
  ReferenceAxis = -> Sketch183 [N_Axis]
  Type = 0
FEATURE [Sketcher::SketchObject] Sketch184  label="Wire channels Pocket004"
  FullyConstrained = false
  MapMode = 5
  Placement = pos=(0,0,0) rot=(1,0,0;3.14159rad)
  sketch-geometry (29):
    g0: LineSegment StartX=101.467 StartY=-402.5 StartZ=0 EndX=130.4 EndY=-402.5 EndZ=0
    g1: LineSegment StartX=200 StartY=-200 StartZ=0 EndX=220 EndY=-200 EndZ=0
    g2: LineSegment StartX=135.4 StartY=-402.5 StartZ=0 EndX=135.4 EndY=-397.5 EndZ=0
    g3: LineSegment StartX=135.4 StartY=-397.5 StartZ=0 EndX=175 EndY=-357.904 EndZ=0
    g4: LineSegment StartX=175 StartY=-357.904 StartZ=0 EndX=175 EndY=-245 EndZ=0
    g5: LineSegment StartX=175 StartY=-245 StartZ=0 EndX=290 EndY=-245 EndZ=0
    g6: LineSegment StartX=290 StartY=-245 StartZ=0 EndX=295 EndY=-245 EndZ=0
    g7: LineSegment StartX=295 StartY=-245 StartZ=0 EndX=295 EndY=-215 EndZ=0
    g8: LineSegment StartX=295 StartY=-215 StartZ=0 EndX=290 EndY=-215 EndZ=0
    g9: LineSegment StartX=290 StartY=-215 StartZ=0 EndX=225 EndY=-215 EndZ=0
    g10: LineSegment StartX=225 StartY=-215 StartZ=0 EndX=225 EndY=-200 EndZ=0
    g11: LineSegment StartX=195 StartY=-200 StartZ=0 EndX=195 EndY=-215 EndZ=0
    g12: LineSegment StartX=195 StartY=-215 StartZ=0 EndX=168.46 EndY=-215 EndZ=0
    g13: LineSegment StartX=168.46 StartY=-215 StartZ=0 EndX=162 EndY=-198.36 EndZ=0
    g14: LineSegment StartX=162 StartY=-198.36 StartZ=0 EndX=162 EndY=-115 EndZ=0
    g15: LineSegment StartX=162 StartY=-115 StartZ=0 EndX=162 EndY=-110 EndZ=0
    g16: LineSegment StartX=162 StartY=-110 StartZ=0 EndX=157 EndY=-110 EndZ=0
    g17: LineSegment StartX=157 StartY=-110 StartZ=0 EndX=134.577 EndY=-122.534 EndZ=0
    g18: LineSegment StartX=134.577 StartY=-122.534 StartZ=0 EndX=132 EndY=-126.896 EndZ=0
    g19: LineSegment StartX=132 StartY=-126.896 StartZ=0 EndX=132 EndY=-200.027 EndZ=0
    g20: LineSegment StartX=132 StartY=-200.027 StartZ=0 EndX=144.989 EndY=-239.968 EndZ=0
    g21: LineSegment StartX=144.989 StartY=-239.968 StartZ=0 EndX=144.989 EndY=-343.839 EndZ=0
    g22: LineSegment StartX=144.989 StartY=-343.839 StartZ=0 EndX=96.4674 EndY=-392.5 EndZ=0
    g23: LineSegment StartX=96.4674 StartY=-392.5 StartZ=0 EndX=96.4674 EndY=-397.5 EndZ=0
    g24: LineSegment StartX=96.4674 StartY=-397.5 StartZ=0 EndX=96.4674 EndY=-402.5 EndZ=0
    g25: LineSegment StartX=101.467 StartY=-402.5 StartZ=0 EndX=96.4674 EndY=-402.5 EndZ=0
    g26: LineSegment StartX=130.4 StartY=-402.5 StartZ=0 EndX=135.4 EndY=-402.5 EndZ=0
    g27: LineSegment StartX=225 StartY=-200 StartZ=0 EndX=220 EndY=-200 EndZ=0
    g28: LineSegment StartX=195 StartY=-200 StartZ=0 EndX=200 EndY=-200 EndZ=0
  constraints (78):
    c: Horizontal(g0)
    c: DistanceX(g0,g0) = 28.9326
    c: Horizontal(g1)
    c: DistanceX(g1,g1) = 20
    c: Vertical(g2)
    c: Coincident(g2,g3)
    c: Coincident(g3,g4)
    c: Vertical(g4)
    c: Coincident(g4,g5)
    c: Horizontal(g5)
    c: Coincident(g5,g6)
    c: Horizontal(g6)
    c: Coincident(g6,g7)
    c: Vertical(g7)
    c: Coincident(g7,g8)
    c: Horizontal(g8)
    c: Coincident(g8,g9)
    c: Horizontal(g9)
    c: Coincident(g9,g10)
    c: Vertical(g10)
    c: Vertical(g11)
    c: Coincident(g11,g12)
    c: Horizontal(g12)
    c: Coincident(g12,g13)
    c: Coincident(g13,g14)
    c: Vertical(g14)
    c: Coincident(g14,g15)
    c: Vertical(g15)
    c: Coincident(g15,g16)
    c: Horizontal(g16)
    c: Coincident(g16,g17)
    c: Coincident(g17,g18)
    c: Coincident(g18,g19)
    c: Vertical(g19)
    c: Coincident(g19,g20)
    c: Coincident(g20,g21)
    c: Vertical(g21)
    c: Coincident(g21,g22)
    c: Coincident(g22,g23)
    c: Vertical(g23)
    c: Coincident(g23,g24)
    c: Vertical(g24)
    c: Coincident(g25,g0)
    c: Coincident(g25,g24)
    c: Horizontal(g25)
    c: Coincident(g26,g0)
    c: Coincident(g26,g2)
    c: Horizontal(g26)
    c: Coincident(g27,g10)
    c: Coincident(g27,g1)
    c: Horizontal(g27)
    c: Coincident(g28,g11)
    c: Coincident(g28,g1)
    c: Horizontal(g28)
    c: DistanceX(g25,g25) = 5
    c: DistanceX(g26,g26) = 5
    c: DistanceY(g24,g24) = 5
    c: DistanceY(g23,g23) = 5
    c: DistanceY(g2,g2) = 5
    c: Distance(g22) = 68.7186
    c: Distance(g3) = 56
    c: DistanceY(g21,g21) = 103.871
    c: DistanceY(g4,g4) = 112.904
    c: DistanceX(g5,g5) = 115
    c: DistanceX(g12,g12) = 26.54
    c: DistanceX(g9,g9) = 65
    c: Distance(g20) = 42
    c: DistanceY(g19,g19) = 73.1311
    c: DistanceY(g14,g14) = 83.36
    c: DistanceX(g27,g27) = 5
    c: DistanceX(g28,g28) = 5
    c: DistanceX(g8,g8) = 5
    c: DistanceX(g6,g6) = 5
    c: DistanceY(g7,g7) = 30
    c: Distance(g17) = 25.6886
    c: Distance(g18) = 5.06593
    c: Distance(g16) = 5
    c: DistanceY(g15,g15) = 5
FEATURE [PartDesign::Pad] Pad012
  Direction = (0,0,-1)
  Length = 3
  Length2 = 10
  Placement = pos=(0,0,0) rot=(1,0,0;3.14159rad)
  Profile = -> Sketch184
  ReferenceAxis = -> Sketch184 [N_Axis]
  Type = 0
FEATURE [PartDesign::Fillet] Fillet037
  Base = -> Pad012 [Edge2,Edge5,Edge8,Edge14,Edge17,Edge20,Edge23,Edge26,Edge29,Edge32,Edge35,Edge53,Edge56,Edge59,Edge65,Edge68,Edge74]
  BaseFeature = -> Pad012
  Placement = pos=(0,0,0) rot=(1,0,0;3.14159rad)
  Radius = 3.35
  SupportTransform = false
  UseAllEdges = false
FEATURE [Sketcher::SketchObject] Sketch185
  FullyConstrained = false
  MapMode = 5
  Placement = pos=(0,0,-3) rot=(1,0,0;3.14159rad)
  Support = -> [Fillet037]
  sketch-geometry (38):
    g0: Circle CenterX=105 CenterY=-389 CenterZ=0 NormalX=0 NormalY=0 NormalZ=1 AngleXU=0 Radius=1.15
    g1: Circle CenterX=145 CenterY=-349 CenterZ=0 NormalX=0 NormalY=0 NormalZ=1 AngleXU=0 Radius=1.15
    g2: Circle CenterX=147.5 CenterY=-309 CenterZ=0 NormalX=0 NormalY=0 NormalZ=1 AngleXU=0 Radius=1.15
    g3: Circle CenterX=147.5 CenterY=-259 CenterZ=0 NormalX=0 NormalY=0 NormalZ=1 AngleXU=0 Radius=1.15
    g4: Circle CenterX=172.5 CenterY=-259 CenterZ=0 NormalX=0 NormalY=0 NormalZ=1 AngleXU=0 Radius=1.15
    g5: Circle CenterX=172.5 CenterY=-309 CenterZ=0 NormalX=0 NormalY=0 NormalZ=1 AngleXU=0 Radius=1.15
    g6: Circle CenterX=172.5 CenterY=-349 CenterZ=0 NormalX=0 NormalY=0 NormalZ=1 AngleXU=0 Radius=1.15
    g7: Circle CenterX=147.665 CenterY=-382.765 CenterZ=0 NormalX=0 NormalY=0 NormalZ=1 AngleXU=0 Radius=1.15
    g8: LineSegment StartX=147.5 StartY=-259 StartZ=0 EndX=147.5 EndY=-239 EndZ=0
    g9: LineSegment StartX=147.5 StartY=-239 StartZ=0 EndX=141 EndY=-220 EndZ=0
    g10: LineSegment StartX=141 StartY=-220 StartZ=0 EndX=134.428 EndY=-201 EndZ=0
    g11: LineSegment StartX=134.428 StartY=-201 StartZ=0 EndX=134.428 EndY=-161 EndZ=0
    g12: LineSegment StartX=134.428 StartY=-161 StartZ=0 EndX=134.428 EndY=-131 EndZ=0
    g13: LineSegment StartX=134.428 StartY=-131.025 StartZ=0 EndX=137 EndY=-124 EndZ=0
    g14: LineSegment StartX=137 StartY=-124 StartZ=0 EndX=146.85 EndY=-118.15 EndZ=0
    g15: LineSegment StartX=172.5 StartY=-259 StartZ=0 EndX=178 EndY=-242.5 EndZ=0
    g16: LineSegment StartX=178 StartY=-242.5 StartZ=0 EndX=218 EndY=-242.5 EndZ=0
    g17: LineSegment StartX=218 StartY=-242.5 StartZ=0 EndX=258 EndY=-242.5 EndZ=0
    g18: LineSegment StartX=258 StartY=-242.5 StartZ=0 EndX=292 EndY=-242.5 EndZ=0
    g19: Circle CenterX=178 CenterY=-242.5 CenterZ=0 NormalX=0 NormalY=0 NormalZ=1 AngleXU=0 Radius=1.15
    g20: Circle CenterX=218 CenterY=-242.5 CenterZ=0 NormalX=0 NormalY=0 NormalZ=1 AngleXU=0 Radius=1.15
    g21: Circle CenterX=258 CenterY=-242.5 CenterZ=0 NormalX=0 NormalY=0 NormalZ=1 AngleXU=0 Radius=1.15
    g22: Circle CenterX=258 CenterY=-217.5 CenterZ=0 NormalX=0 NormalY=0 NormalZ=1 AngleXU=0 Radius=1.15
    g23: Circle CenterX=292 CenterY=-242.5 CenterZ=0 NormalX=0 NormalY=0 NormalZ=1 AngleXU=0 Radius=1.15
    g24: Circle CenterX=292 CenterY=-217.5 CenterZ=0 NormalX=0 NormalY=0 NormalZ=1 AngleXU=0 Radius=1.15
    g25: Circle CenterX=292.5 CenterY=-230 CenterZ=0 NormalX=0 NormalY=0 NormalZ=1 AngleXU=0 Radius=1.15
    g26: Circle CenterX=223 CenterY=-217 CenterZ=0 NormalX=0 NormalY=0 NormalZ=1 AngleXU=0 Radius=1.15
    g27: Circle CenterX=197 CenterY=-217 CenterZ=0 NormalX=0 NormalY=0 NormalZ=1 AngleXU=0 Radius=1.15
    g28: Circle CenterX=166.11 CenterY=-217.11 CenterZ=0 NormalX=0 NormalY=0 NormalZ=1 AngleXU=0 Radius=1.15
    g29: Circle CenterX=147.5 CenterY=-239 CenterZ=0 NormalX=0 NormalY=0 NormalZ=1 AngleXU=0 Radius=1.15
    g30: Circle CenterX=141 CenterY=-220 CenterZ=0 NormalX=0 NormalY=0 NormalZ=1 AngleXU=0 Radius=1.15
    g31: Circle CenterX=134.428 CenterY=-201 CenterZ=0 NormalX=0 NormalY=0 NormalZ=1 AngleXU=0 Radius=1.15
    g32: Circle CenterX=160.15 CenterY=-201 CenterZ=0 NormalX=0 NormalY=0 NormalZ=1 AngleXU=0 Radius=1.15
    g33: Circle CenterX=134.428 CenterY=-161 CenterZ=0 NormalX=0 NormalY=0 NormalZ=1 AngleXU=0 Radius=1.15
    g34: Circle CenterX=159.5 CenterY=-161 CenterZ=0 NormalX=0 NormalY=0 NormalZ=1 AngleXU=0 Radius=1.15
    g35: Circle CenterX=137 CenterY=-124 CenterZ=0 NormalX=0 NormalY=0 NormalZ=1 AngleXU=0 Radius=1.15
    g36: Circle CenterX=146.85 CenterY=-118.15 CenterZ=0 NormalX=0 NormalY=0 NormalZ=1 AngleXU=0 Radius=1.15
    g37: Circle CenterX=159 CenterY=-113 CenterZ=0 NormalX=0 NormalY=0 NormalZ=1 AngleXU=0 Radius=1.15
  constraints (50):
    c: Diameter(g0) = 2.3
    c: Diameter(g1) = 2.3
    c: Diameter(g2) = 2.3
    c: Diameter(g7) = 2.3
    c: Diameter(g6) = 2.3
    c: Diameter(g5) = 2.3
    c: Diameter(g3) = 2.3
    c: Diameter(g4) = 2.3
    c: Coincident(g8,g3)
    c: Vertical(g8)
    c: Coincident(g9,g8)
    c: Coincident(g10,g9)
    c: Coincident(g11,g10)
    c: Vertical(g11)
    c: Coincident(g12,g11)
    c: Vertical(g12)
    c: PointOnObject(g13,g12)
    c: Coincident(g14,g13)
    c: Coincident(g15,g4)
    c: Coincident(g16,g15)
    c: Horizontal(g16)
    c: Coincident(g17,g16)
    c: Horizontal(g17)
    c: Coincident(g18,g17)
    c: Horizontal(g18)
    c: Coincident(g19,g15)
    c: Coincident(g20,g16)
    c: Coincident(g21,g17)
    c: Coincident(g23,g18)
    c: Coincident(g29,g8)
    c: Coincident(g30,g9)
    c: Coincident(g31,g10)
    c: Coincident(g33,g11)
    c: Coincident(g35,g13)
    c: Coincident(g36,g14)
    c: Equal(g29,g30)
    c: Equal(g29,g19)
    c: Equal(g29,g28)
    c: Equal(g29,g27)
    c: Equal(g29,g26)
    c: Equal(g29,g20)
    c: Equal(g29,g21)
    c: Equal(g29,g22)
    c: Equal(g29,g24)
    c: Equal(g29,g23)
    c: Equal(g29,g25)
    c: Equal(g29,g32)
    c: Equal(g29,g31)
    c: Equal(g29, g33-g37) x5
    c: Diameter(g29) = 2.3
FEATURE [PartDesign::Pocket] Pocket053
  BaseFeature = -> Fillet037
  Direction = (0,0,1)
  Length = 3
  Length2 = 5
  Placement = pos=(0,0,0) rot=(1,0,0;3.14159rad)
  Profile = -> Sketch185
  ReferenceAxis = -> Sketch185 [N_Axis]
  Type = 0
FEATURE [Sketcher::SketchObject] Sketch186
  FullyConstrained = false
  MapMode = 5
  Placement = pos=(0,0,-3) rot=(1,0,0;3.14159rad)
  Support = -> [Pocket052]
  sketch-geometry (8):
    g0: LineSegment StartX=172.5 StartY=-259 StartZ=0 EndX=172.5 EndY=-249 EndZ=0
    g1: LineSegment StartX=175 StartY=-249 StartZ=0 EndX=130 EndY=-249 EndZ=0
    g2: LineSegment StartX=130 StartY=-249 StartZ=0 EndX=130 EndY=-100 EndZ=0
    g3: LineSegment StartX=130 StartY=-100 StartZ=0 EndX=170 EndY=-100 EndZ=0
    g4: LineSegment StartX=170 StartY=-100 StartZ=0 EndX=170 EndY=-190 EndZ=0
    g5: LineSegment StartX=170 StartY=-190 StartZ=0 EndX=300 EndY=-190 EndZ=0
    g6: LineSegment StartX=300 StartY=-190 StartZ=0 EndX=300 EndY=-249 EndZ=0
    g7: LineSegment StartX=300 StartY=-249 StartZ=0 EndX=175 EndY=-249 EndZ=0
  constraints (15):
    c: Vertical(g0)
    c: Horizontal(g1)
    c: Coincident(g1,g2)
    c: Vertical(g2)
    c: Coincident(g2,g3)
    c: Horizontal(g3)
    c: Coincident(g3,g4)
    c: Vertical(g4)
    c: Coincident(g4,g5)
    c: Horizontal(g5)
    c: Coincident(g5,g6)
    c: Vertical(g6)
    c: Coincident(g6,g7)
    c: Coincident(g7,g1)
    c: Horizontal(g7)
FEATURE [PartDesign::Pocket] Pocket054
  BaseFeature = -> Pocket052
  Direction = (0,-2e-16,1)
  Length = 5
  Length2 = 5
  Placement = pos=(0,0,0) rot=(1,0,0;3.14159rad)
  Profile = -> Sketch186
  ReferenceAxis = -> Sketch186 [N_Axis]
  Type = 0
FEATURE [Sketcher::SketchObject] Sketch187
  FullyConstrained = false
  MapMode = 5
  Placement = pos=(0,0,-3) rot=(1,0,0;3.14159rad)
  Support = -> [Pocket054]
  sketch-geometry (4):
    g0: LineSegment StartX=144 StartY=-249 StartZ=0 EndX=175 EndY=-249 EndZ=0
    g1: LineSegment StartX=175 StartY=-249 StartZ=0 EndX=175 EndY=-269 EndZ=0
    g2: LineSegment StartX=175 StartY=-269 StartZ=0 EndX=144 EndY=-269 EndZ=0
    g3: LineSegment StartX=144 StartY=-269 StartZ=0 EndX=144 EndY=-249 EndZ=0
  constraints (8):
    c: Coincident(g0,g1)
    c: Coincident(g1,g2)
    c: Coincident(g2,g3)
    c: Coincident(g3,g0)
    c: Horizontal(g0)
    c: Horizontal(g2)
    c: Vertical(g1)
    c: Vertical(g3)
FEATURE [PartDesign::Pocket] Pocket055
  BaseFeature = -> Pocket054
  Direction = (0,-4e-16,1)
  Length = 1.5
  Length2 = 5
  Placement = pos=(0,0,0) rot=(1,0,0;3.14159rad)
  Profile = -> Sketch187
  ReferenceAxis = -> Sketch187 [N_Axis]
  Type = 0
FEATURE [Sketcher::SketchObject] Sketch188
  FullyConstrained = false
  MapMode = 5
  Placement = pos=(0,0,-3) rot=(1,0,0;3.14159rad)
  Support = -> [Pocket053]
  sketch-geometry (8):
    g0: LineSegment StartX=147.5 StartY=-259 StartZ=0 EndX=147.5 EndY=-249 EndZ=0
    g1: LineSegment StartX=145 StartY=-249 StartZ=0 EndX=145 EndY=-269 EndZ=0
    g2: LineSegment StartX=145 StartY=-269 StartZ=0 EndX=175 EndY=-269 EndZ=0
    g3: LineSegment StartX=175 StartY=-269 StartZ=0 EndX=176 EndY=-269 EndZ=0
    g4: LineSegment StartX=176 StartY=-269 StartZ=0 EndX=176 EndY=-410 EndZ=0
    g5: LineSegment StartX=176 StartY=-410 StartZ=0 EndX=90 EndY=-410 EndZ=0
    g6: LineSegment StartX=90 StartY=-410 StartZ=0 EndX=90 EndY=-269 EndZ=0
    g7: LineSegment StartX=90 StartY=-269 StartZ=0 EndX=145 EndY=-269 EndZ=0
  constraints (15):
    c: Vertical(g0)
    c: Vertical(g1)
    c: Coincident(g1,g2)
    c: Horizontal(g2)
    c: Coincident(g2,g3)
    c: Horizontal(g3)
    c: Coincident(g3,g4)
    c: Vertical(g4)
    c: Coincident(g4,g5)
    c: Horizontal(g5)
    c: Coincident(g5,g6)
    c: Vertical(g6)
    c: Coincident(g6,g7)
    c: Coincident(g7,g2)
    c: Horizontal(g7)
FEATURE [PartDesign::Pocket] Pocket056
  BaseFeature = -> Pocket053
  Direction = (0,-1e-16,1)
  Length = 5
  Length2 = 5
  Placement = pos=(0,0,0) rot=(1,0,0;3.14159rad)
  Profile = -> Sketch188
  ReferenceAxis = -> Sketch188 [N_Axis]
  Type = 0
FEATURE [Sketcher::SketchObject] Sketch189
  FullyConstrained = false
  MapMode = 5
  Support = -> [Pocket056]
  sketch-geometry (4):
    g0: LineSegment StartX=144 StartY=269 StartZ=0 EndX=176 EndY=269 EndZ=0
    g1: LineSegment StartX=176 StartY=269 StartZ=0 EndX=176 EndY=249 EndZ=0
    g2: LineSegment StartX=176 StartY=249 StartZ=0 EndX=144 EndY=249 EndZ=0
    g3: LineSegment StartX=144 StartY=249 StartZ=0 EndX=144 EndY=269 EndZ=0
  constraints (8):
    c: Coincident(g0,g1)
    c: Coincident(g1,g2)
    c: Coincident(g2,g3)
    c: Coincident(g3,g0)
    c: Horizontal(g0)
    c: Horizontal(g2)
    c: Vertical(g1)
    c: Vertical(g3)
FEATURE [PartDesign::Pocket] Pocket057
  BaseFeature = -> Pocket056
  Direction = (0,2e-16,-1)
  Length = 1.5
  Length2 = 5
  Placement = pos=(0,0,0) rot=(1,0,0;3.14159rad)
  Profile = -> Sketch189
  ReferenceAxis = -> Sketch189 [N_Axis]
  Type = 0
FEATURE [PartDesign::Chamfer] Chamfer001
  Angle = 45
  Base = -> Pocket055 [Edge74,Edge24]
  BaseFeature = -> Pocket055
  ChamferType = 0
  FlipDirection = false
  Placement = pos=(0,0,0) rot=(1,0,0;3.14159rad)
  Size = 1.49
  Size2 = 1
  SupportTransform = false
  UseAllEdges = false
FEATURE [PartDesign::Body] Body023  label="Back Plate 2"
  Group = -> [Sketch182,Pad011,Fillet036,Sketch183,Pocket052,Sketch186,Pocket054,Sketch187,Pocket055,Chamfer001]
  Origin = -> Origin192
  Placement = pos=(0,0,-5) rot=(0,0,1;0rad)
  Tip = -> Chamfer001
FEATURE [PartDesign::Chamfer] Chamfer002
  Angle = 45
  Base = -> Pocket057 [Edge173,Edge136]
  BaseFeature = -> Pocket057
  ChamferType = 0
  FlipDirection = false
  Placement = pos=(0,0,0) rot=(1,0,0;3.14159rad)
  Size = 1.49
  Size2 = 1
  SupportTransform = false
  UseAllEdges = false
FEATURE [PartDesign::Body] Body024  label="Back Plate 3"
  Group = -> [Sketch184,Pad012,Fillet037,Sketch185,Pocket053,Sketch188,Pocket056,Sketch189,Pocket057,Chamfer002]
  Origin = -> Origin193
  Placement = pos=(0,0,-5) rot=(0,0,1;0rad)
  Tip = -> Chamfer002
FEATURE [App::Part] Part042  label="Wire Channel back Plate"
  Group = -> [Body023,Body024]
  Origin = -> Origin194
  Placement = pos=(0,0,8) rot=(0,0,1;0rad)
FEATURE [PartDesign::Fillet] Fillet038  label="pickup wire channel edges 1"
  Base = -> Fillet035 [Edge391,Edge396]
  BaseFeature = -> Fillet035
  Radius = 6.35
  SupportTransform = false
  UseAllEdges = false
FEATURE [Part::Feature] Part__Feature549  label="TREMOLO-ARM"
  Placement = pos=(-8e-15,-9.2e-15,0) rot=(0,0,1;4.01426rad)
  shape: bbox 73.01 x 144.7 x 57.14 mm, 22 faces (baked)
FEATURE [App::Part] TREMOLO_ARM_ASM  label="TREMOLO-ARM_ASM"
  Group = -> [Part__Feature549]
  Origin = -> Origin196
  Placement = pos=(261.7,271.791,45.6306) rot=(0,0,-1;3.87463rad)
FEATURE [PartDesign::Fillet] Fillet039  label="pickup wire channel edges 2"
  Base = -> Fillet038 [Edge165,Edge163,Edge161]
  BaseFeature = -> Fillet038
  Radius = 3.35
  SupportTransform = false
  UseAllEdges = false
FEATURE [PartDesign::Fillet] Fillet040  label="pickup wire channel edges 3"
  Base = -> Fillet039 [Edge165]
  BaseFeature = -> Fillet039
  Radius = 30
  SupportTransform = false
  UseAllEdges = false
FEATURE [PartDesign::Fillet] Fillet041  label="pickup wire channel edges 4"
  Base = -> Fillet040 [Edge162]
  BaseFeature = -> Fillet040
  Radius = 40
  SupportTransform = false
  UseAllEdges = false
FEATURE [PartDesign::Fillet] Fillet042  label="pickup wire channel edges 5"
  Base = -> Fillet041 [Edge144,Edge149]
  BaseFeature = -> Fillet041
  Radius = 20
  SupportTransform = false
  UseAllEdges = false
FEATURE [PartDesign::Fillet] Fillet043  label="pickup wire channel edges 6"
  Base = -> Fillet042 [Edge187]
  BaseFeature = -> Fillet042
  Radius = 50
  SupportTransform = false
  UseAllEdges = false
FEATURE [PartDesign::Fillet] Fillet044  label="pickup wire channel edges 7"
  Base = -> Fillet043 [Edge168]
  BaseFeature = -> Fillet043
  Radius = 30
  SupportTransform = false
  UseAllEdges = false
FEATURE [PartDesign::Fillet] Fillet045  label="pickup wire channel edges 8"
  Base = -> Fillet044 [Edge144]
  BaseFeature = -> Fillet044
  Radius = 20
  SupportTransform = false
  UseAllEdges = false
FEATURE [Mesh::Feature] SchallerStrapLockButton  label="Butt strap lock peg"
  Placement = pos=(282.82,63.9325,22.6) rot=(1,0,0;1.5708rad)
FEATURE [Mesh::Feature] SchallerStrapLockButton001  label="top strap lock peg"
  Placement = pos=(94.4316,593.116,22.6) rot=(0,0.707107,0.707107;3.14159rad)
FEATURE [PartDesign::Pocket] Pocket058
  BaseFeature = -> Pocket031
  Direction = (0,0,-1)
  Length = 3
  Length2 = 5
  Placement = pos=(0,0,45) rot=(0,0,1;0rad)
  Profile = -> Sketch145
  ReferenceAxis = -> Sketch145 [N_Axis]
  Type = 0
FEATURE [Part::Feature] Part__Feature550  label="92010A126_Passivated 18-8 Stainless Steel Phillips Flat Head Screw (1
)"
  Placement = pos=(-20.32,2.525,-1.125) rot=(-0.876232,-0.340748,-0.340748;1.70254rad)
  shape: bbox 5.6 x 16.2 x 5.6 mm, 85 faces (baked)
FEATURE [Part::Feature] Part__Feature551  label="92010A126_Passivated 18-8 Stainless Steel Phillips Flat Head Screw (1
)001"
  Placement = pos=(20.32,2.525,-1.125) rot=(-0.876232,-0.340748,-0.340748;1.70254rad)
  shape: bbox 5.6 x 16.2 x 5.6 mm, 85 faces (baked)
FEATURE [Part::Feature] Part__Feature552  label="COMPOUND106"
  shape: bbox 48.25 x 24.12 x 12.12 mm, 360 faces (baked)
FEATURE [Part::Feature] Part__Feature553  label="COMPOUND107"
  shape: bbox 36.16 x 26.16 x 1 mm, 50 faces (baked)
FEATURE [Part::Feature] Part__Feature554  label="COMPOUND108"
  shape: bbox 2 x 2.8 x 0.5 mm, 18 faces (baked)
FEATURE [Part::Feature] Part__Feature555  label="COMPOUND109"
  shape: bbox 2 x 2.8 x 0.5 mm, 18 faces (baked)
FEATURE [Part::Feature] Part__Feature556  label="COMPOUND110"
  shape: bbox 2 x 2.8 x 0.5 mm, 18 faces (baked)
FEATURE [Part::Feature] Part__Feature557  label="COMPOUND111"
  shape: bbox 2 x 2.8 x 0.5 mm, 18 faces (baked)
FEATURE [Part::Feature] Part__Feature558  label="COMPOUND112"
  shape: bbox 2 x 2.8 x 0.5 mm, 18 faces (baked)
FEATURE [Part::Feature] Part__Feature559  label="COMPOUND113"
  shape: bbox 2 x 2.8 x 0.5 mm, 18 faces (baked)
FEATURE [Part::Feature] Part__Feature560  label="COMPOUND114"
  shape: bbox 2 x 2.8 x 0.5 mm, 18 faces (baked)
FEATURE [Part::Feature] Part__Feature561  label="COMPOUND115"
  shape: bbox 2 x 2.924 x 2.624 mm, 39 faces (baked)
FEATURE [Part::Feature] Part__Feature562  label="COMPOUND116"
  shape: bbox 22.96 x 37.56 x 1 mm, 50 faces (baked)
FEATURE [Part::Feature] Part__Feature563  label="COMPOUND117"
  shape: bbox 11.83 x 16.93 x 9.424 mm, 7 faces (baked)
FEATURE [App::Part] COMPOUND007  label="COMPOUND105"
  Group = -> [Part__Feature552,Part__Feature553,Part__Feature554,Part__Feature555,Part__Feature556,Part__Feature557,Part__Feature558,Part__Feature559,Part__Feature560,Part__Feature561,Part__Feature562,Part__Feature563]
  Origin = -> Origin197
FEATURE [App::Part] __Way_Switch_v2__1_  label="3-Way Switch v2 (1)"
  Group = -> [Part__Feature550,Part__Feature551,COMPOUND007]
  Origin = -> Origin198
  Placement = pos=(329.47,216.021,45.607) rot=(-0.456966,-0.62896,-0.62896;3.99886rad)
FEATURE [App::Part] Part033  label="Pickup Controls"
  Group = -> [Potentiometer001,Potentiometer,__Way_Switch_v2__1_]
  Origin = -> Origin130
  Placement = pos=(-2.1,-1.1,-4.8) rot=(0,0,1;0rad)
FEATURE [Part::Feature] Part__Feature565  label="sleeve enclosure v2"
  Placement = pos=(-0.1,0,24.3) rot=(0,1,0;3.14159rad)
  shape: bbox 112.8 x 127 x 25.3 mm, 56 faces (baked)
FEATURE [Sketcher::SketchObject] Sketch190
  FullyConstrained = false
  MapMode = 5
  Placement = pos=(0,0,0) rot=(1,0,0;3.14159rad)
  Support = -> [Fillet045]
  sketch-geometry (4):
    g0: LineSegment StartX=168.5 StartY=-70 StartZ=0 EndX=281.3 EndY=-70 EndZ=0
    g1: LineSegment StartX=281.3 StartY=-70 StartZ=0 EndX=281.3 EndY=-200 EndZ=0
    g2: LineSegment StartX=281.3 StartY=-200 StartZ=0 EndX=168.5 EndY=-200 EndZ=0
    g3: LineSegment StartX=168.5 StartY=-200 StartZ=0 EndX=168.5 EndY=-70 EndZ=0
  constraints (10):
    c: Coincident(g0,g1)
    c: Coincident(g1,g2)
    c: Coincident(g2,g3)
    c: Coincident(g3,g0)
    c: Horizontal(g0)
    c: Horizontal(g2)
    c: Vertical(g1)
    c: Vertical(g3)
    c: DistanceX(g0,g0) = 112.8
    c: DistanceY(g3,g3) = 130
FEATURE [PartDesign::Pocket] Pocket059  label="Battery Sleeve lip mount pocket"
  BaseFeature = -> Fillet045
  Direction = (0,0,1)
  Length = 6
  Length2 = 5
  Profile = -> Sketch190
  ReferenceAxis = -> Sketch190 [N_Axis]
  Type = 0
FEATURE [PartDesign::Fillet] Fillet046  label="Battery Sleeve edges"
  Base = -> Pocket059 [Edge352,Edge854,Edge235,Edge852]
  BaseFeature = -> Pocket059
  Radius = 3.35
  SupportTransform = false
  UseAllEdges = false
FEATURE [Part::Feature] Part__Feature566  label="sleeve enclosure top plate"
  Placement = pos=(-143.1,1e-15,-1) rot=(0,1,0;3.14159rad)
  shape: bbox 112.8 x 130 x 3 mm, 32 faces (baked)
FEATURE [App::Part] Part043  label="Battery Sleeve"
  Group = -> [Part__Feature565,Part__Feature566]
  Origin = -> Origin199
  Placement = pos=(84,-140.1,-3.2) rot=(0,0,1;0rad)
FEATURE [App::Part] Part020  label="Battery and Sleeve"
  Group = -> [Part030,Part043]
  Origin = -> Origin096
  Placement = pos=(182.9,199.9,7.2) rot=(0,0,1;0rad)
FEATURE [App::Part] Part002  label="Electronics"
  Group = -> [Part004,Part016,Part020,Part041]
  Origin = -> Origin004
FEATURE [Sketcher::SketchObject] Sketch191
  FullyConstrained = false
  MapMode = 5
  Placement = pos=(0,0,48) rot=(0,0,1;0rad)
  Support = -> [Pocket058]
  sketch-geometry (8):
    g0: Circle CenterX=287 CenterY=178.79 CenterZ=0 NormalX=0 NormalY=0 NormalZ=1 AngleXU=0 Radius=1.65
    g1: Circle CenterX=287.6 CenterY=252 CenterZ=0 NormalX=0 NormalY=0 NormalZ=1 AngleXU=0 Radius=1.65
    g2: Circle CenterX=333.1 CenterY=252.5 CenterZ=0 NormalX=0 NormalY=0 NormalZ=1 AngleXU=0 Radius=1.65
    g3: Circle CenterX=357 CenterY=179 CenterZ=0 NormalX=0 NormalY=0 NormalZ=1 AngleXU=0 Radius=1.65
    g4: LineSegment StartX=336.506 StartY=256.572 StartZ=0 EndX=333.1 EndY=252.5 EndZ=0
    g5: LineSegment StartX=284 StartY=256.277 StartZ=0 EndX=287.6 EndY=252 EndZ=0
    g6: LineSegment StartX=283.266 StartY=174.455 StartZ=0 EndX=287 EndY=178.792 EndZ=0
    g7: LineSegment StartX=350.571 StartY=183.276 StartZ=0 EndX=357 EndY=179 EndZ=0
  constraints (4):
    c: Equal(g1,g2)
    c: Equal(g1,g0)
    c: Equal(g1,g3)
    c: Diameter(g1) = 3.3
FEATURE [PartDesign::Pocket] Pocket060
  BaseFeature = -> Pocket058
  Direction = (0,0,-1)
  Length = 3
  Length2 = 5
  Placement = pos=(0,0,45) rot=(0,0,1;0rad)
  Profile = -> Sketch191
  ReferenceAxis = -> Sketch191 [N_Axis]
  Type = 0
FEATURE [PartDesign::Body] Body015  label="Control Cavity Plate"
  Group = -> [Sketch143,Pad004,Fillet016,Sketch144,Pocket031,Sketch145,Pocket058,Sketch191,Pocket060]
  Origin = -> Origin133
  Placement = pos=(0,0,-2.9) rot=(0,0,1;0rad)
  Tip = -> Pocket060
FEATURE [App::Part] Part039  label="Mounted Guitar specific Components"
  Group = -> [Body020,Body015,Part042,Body022]
  Origin = -> Origin170
FEATURE [Sketcher::SketchObject] Sketch192
  FullyConstrained = false
  MapMode = 5
  Placement = pos=(72.1794,119.528,-5.45e-14) rot=(0.930428,-0.259137,-0.259137;1.64285rad)
  Support = -> [Pocket034]
  sketch-geometry (9):
    g0: LineSegment StartX=-10.5 StartY=32 StartZ=0 EndX=-15.85 EndY=34.6 EndZ=0
    g1: Circle CenterX=-15.85 CenterY=34.6 CenterZ=0 NormalX=0 NormalY=0 NormalZ=1 AngleXU=0 Radius=1.65
    g2: LineSegment StartX=-15.85 StartY=34.6 StartZ=0 EndX=-15.85 EndY=10.3024 EndZ=0
    g3: LineSegment StartX=-15.85 StartY=34.6 StartZ=0 EndX=89.9 EndY=34.6 EndZ=0
    g4: LineSegment StartX=89.9 StartY=34.6 StartZ=0 EndX=89.9 EndY=6 EndZ=0
    g5: LineSegment StartX=-15.85 StartY=10.3024 StartZ=0 EndX=89.9 EndY=10.3024 EndZ=0
    g6: Circle CenterX=89.9 CenterY=10.3024 CenterZ=0 NormalX=0 NormalY=0 NormalZ=1 AngleXU=0 Radius=1.65
    g7: Circle CenterX=89.9 CenterY=34.6 CenterZ=0 NormalX=0 NormalY=0 NormalZ=1 AngleXU=0 Radius=1.65
    g8: Circle CenterX=-15.85 CenterY=10.3024 CenterZ=0 NormalX=0 NormalY=0 NormalZ=1 AngleXU=0 Radius=1.65
  constraints (17):
    c: Coincident(g1,g0)
    c: Coincident(g2,g0)
    c: Vertical(g2)
    c: Coincident(g3,g0)
    c: Horizontal(g3)
    c: Coincident(g4,g3)
    c: Vertical(g4)
    c: Coincident(g5,g2)
    c: PointOnObject(g5,g4)
    c: Horizontal(g5)
    c: Coincident(g6,g5)
    c: Coincident(g7,g3)
    c: Coincident(g8,g2)
    c: Equal(g1,g8)
    c: Equal(g1,g7)
    c: Equal(g1,g6)
    c: Diameter(g1) = 3.3
FEATURE [PartDesign::Pocket] Pocket061
  Direction = (0.51693,0.856028,-2e-16)
  Length = 5
  Length2 = 5
  Profile = -> Sketch192
  ReferenceAxis = -> Sketch192 [N_Axis]
  Type = 0
FEATURE [Sketcher::SketchObject] Sketch193
  FullyConstrained = false
  MapMode = 5
  Placement = pos=(290,0,0) rot=(0.57735,-0.57735,-0.57735;2.0944rad)
  Support = -> [Fillet046]
  sketch-geometry (1):
    g0: Circle CenterX=-230 CenterY=11.5995 CenterZ=0 NormalX=0 NormalY=0 NormalZ=1 AngleXU=0 Radius=5
  constraints (1):
    c: Diameter(g0) = 10
FEATURE [Sketcher::SketchObject] Sketch194
  FullyConstrained = false
  MapMode = 5
  Placement = pos=(0,251,0) rot=(0,0.707107,0.707107;3.14159rad)
  Support = -> [Fillet046]
  sketch-geometry (1):
    g0: Circle CenterX=-311.358 CenterY=11 CenterZ=0 NormalX=0 NormalY=0 NormalZ=1 AngleXU=0 Radius=2.5
  constraints (1):
    c: Diameter(g0) = 5
FEATURE [PartDesign::Pocket] Pocket062  label="Pickup wire channel to control cavity wire hole"
  BaseFeature = -> Fillet046
  Direction = (0,-1,2e-16)
  Length = 5
  Length2 = 5
  Profile = -> Sketch194
  ReferenceAxis = -> Sketch194 [N_Axis]
  Type = 0
FEATURE [PartDesign::Fillet] Fillet047  label="Humbucker edges"
  Base = -> Pocket062 [Edge997,Edge1011,Edge1013,Edge999]
  BaseFeature = -> Pocket062
  Radius = 6.35
  SupportTransform = false
  UseAllEdges = false
FEATURE [Sketcher::SketchObject] Sketch195
  FullyConstrained = false
  MapMode = 5
  Support = -> [XY_Plane200]
  sketch-geometry (24):
    g0: LineSegment StartX=207.209 StartY=938 StartZ=0 EndX=208.314 EndY=938 EndZ=0
    g1: LineSegment StartX=197.057 StartY=277 StartZ=0 EndX=195.953 EndY=277 EndZ=0
    g2: LineSegment StartX=214.706 StartY=938 StartZ=0 EndX=215.682 EndY=938 EndZ=0
    g3: LineSegment StartX=207.974 StartY=277 StartZ=0 EndX=206.997 EndY=277 EndZ=0
    g4: LineSegment StartX=222.018 StartY=938 StartZ=0 EndX=222.718 EndY=938 EndZ=0
    g5: LineSegment StartX=218.852 StartY=277 StartZ=0 EndX=218.152 EndY=277 EndZ=0
    g6: LineSegment StartX=229.053 StartY=938 StartZ=0 EndX=229.52 EndY=938 EndZ=0
    g7: LineSegment StartX=229.725 StartY=277 StartZ=0 EndX=229.258 EndY=277 EndZ=0
    g8: LineSegment StartX=235.766 StartY=938 StartZ=0 EndX=236.149 EndY=938 EndZ=0
    g9: LineSegment StartX=240.693 StartY=277 StartZ=0 EndX=240.31 EndY=277 EndZ=0
    g10: LineSegment StartX=242.587 StartY=937.9 StartZ=0 EndX=242.818 EndY=937.9 EndZ=0
    g11: LineSegment StartX=251.659 StartY=277 StartZ=0 EndX=251.428 EndY=277 EndZ=0
    g12: LineSegment StartX=207.209 StartY=938 StartZ=0 EndX=195.953 EndY=277 EndZ=0
    g13: LineSegment StartX=197.057 StartY=277 StartZ=0 EndX=208.314 EndY=938 EndZ=0
    g14: LineSegment StartX=214.706 StartY=938 StartZ=0 EndX=206.997 EndY=277 EndZ=0
    g15: LineSegment StartX=207.974 StartY=277 StartZ=0 EndX=215.682 EndY=938 EndZ=0
    g16: LineSegment StartX=222.018 StartY=938 StartZ=0 EndX=218.152 EndY=277 EndZ=0
    g17: LineSegment StartX=218.852 StartY=277 StartZ=0 EndX=222.718 EndY=938 EndZ=0
    g18: LineSegment StartX=229.053 StartY=938 StartZ=0 EndX=229.258 EndY=277 EndZ=0
    g19: LineSegment StartX=229.725 StartY=277 StartZ=0 EndX=229.52 EndY=938 EndZ=0
    g20: LineSegment StartX=235.766 StartY=938 StartZ=0 EndX=240.31 EndY=277 EndZ=0
    g21: LineSegment StartX=240.693 StartY=277 StartZ=0 EndX=236.149 EndY=938 EndZ=0
    g22: LineSegment StartX=242.587 StartY=937.9 StartZ=0 EndX=251.428 EndY=277 EndZ=0
    g23: LineSegment StartX=242.818 StartY=937.9 StartZ=0 EndX=251.659 EndY=277 EndZ=0
  constraints (24):
    c: Horizontal(g0)
    c: Horizontal(g1)
    c: Horizontal(g2)
    c: Horizontal(g3)
    c: Horizontal(g4)
    c: Horizontal(g5)
    c: Horizontal(g6)
    c: Horizontal(g7)
    c: Horizontal(g8)
    c: Horizontal(g9)
    c: Horizontal(g10)
    c: Horizontal(g11)
    c: Coincident(g12,g0)
    c: Coincident(g13,g1)
    c: Coincident(g14,g2)
    c: Coincident(g15,g3)
    c: Coincident(g16,g4)
    c: Coincident(g17,g5)
    c: Coincident(g18,g6)
    c: Coincident(g19,g7)
    c: Coincident(g20,g8)
    c: Coincident(g21,g9)
    c: Coincident(g22,g10)
    c: Coincident(g23,g10)
FEATURE [PartDesign::Body] Body025  label="Strings"
  Group = -> [Sketch195]
  Origin = -> Origin200
  Placement = pos=(0,0,55.3) rot=(0,0,1;0rad)
FEATURE [App::Part] Part003  label="Assembly Parts"
  Group = -> [Sustainiac_Single_Coil_v1,Sustainiac_Single_Coil_v002,Humbucker_Rahmen_LP_Hals,SH13,Part034,Body018,Body019,TREMOLO_ARM_ASM,SchallerStrapLockButton001,SchallerStrapLockButton,Body025]
  Origin = -> Origin005
FEATURE [App::Part] Part001  label="Guitar Components"
  Group = -> [Part002,Part003,Part033,Part036,Part037,Part039]
  Origin = -> Origin003
FEATURE [Sketcher::SketchObject] Sketch227  label="blank template003"
  FullyConstrained = false
  MapMode = 5
  Support = -> [XY_Plane206]
  sketch-geometry (4):
    g0: LineSegment StartX=0 StartY=615 StartZ=0 EndX=450 EndY=615 EndZ=0
    g1: LineSegment StartX=450 StartY=615 StartZ=0 EndX=450 EndY=15 EndZ=0
    g2: LineSegment StartX=450 StartY=15 StartZ=0 EndX=0 EndY=15 EndZ=0
    g3: LineSegment StartX=0 StartY=15 StartZ=0 EndX=0 EndY=615 EndZ=0
  constraints (10):
    c: Coincident(g0,g1)
    c: Coincident(g1,g2)
    c: Coincident(g2,g3)
    c: Coincident(g3,g0)
    c: Horizontal(g0)
    c: Horizontal(g2)
    c: Vertical(g1)
    c: Vertical(g3)
    c: DistanceX(g2,g2) = 450
    c: DistanceY(g1,g1) = 600
FEATURE [PartDesign::Pad] Pad014  label="Template 600x452"
  Direction = (0,0,1)
  Length = 7
  Length2 = 10
  Profile = -> Sketch227
  ReferenceAxis = -> Sketch227 [N_Axis]
  Type = 0
FEATURE [Sketcher::SketchObject] Sketch228  label="pickup holes003"
  FullyConstrained = false
  MapMode = 5
  Placement = pos=(0,0,7) rot=(0,0,1;0rad)
  Support = -> [Pad014]
  sketch-geometry (28):
    g0: LineSegment StartX=225 StartY=601 StartZ=0 EndX=225 EndY=-1 EndZ=0
    g1: LineSegment StartX=182.5 StartY=460 StartZ=0 EndX=267.5 EndY=460 EndZ=0
    g2: LineSegment StartX=267.5 StartY=460 StartZ=0 EndX=267.5 EndY=441 EndZ=0
    g3: LineSegment StartX=267.5 StartY=441 StartZ=0 EndX=182.5 EndY=441 EndZ=0
    g4: LineSegment StartX=182.5 StartY=441 StartZ=0 EndX=182.5 EndY=460 EndZ=0
    g5: LineSegment StartX=182.5 StartY=400 StartZ=0 EndX=267.5 EndY=400 EndZ=0
    g6: LineSegment StartX=267.5 StartY=400 StartZ=0 EndX=267.5 EndY=381 EndZ=0
    g7: LineSegment StartX=267.5 StartY=381 StartZ=0 EndX=182.5 EndY=381 EndZ=0
    g8: LineSegment StartX=182.5 StartY=381 StartZ=0 EndX=182.5 EndY=400 EndZ=0
    g9: LineSegment StartX=188.75 StartY=357.8 StartZ=0 EndX=261.25 EndY=357.8 EndZ=0
    g10: LineSegment StartX=261.25 StartY=357.8 StartZ=0 EndX=261.25 EndY=347.8 EndZ=0
    g11: LineSegment StartX=261.25 StartY=347.8 StartZ=0 EndX=269.25 EndY=347.8 EndZ=0
    g12: LineSegment StartX=269.25 StartY=347.8 StartZ=0 EndX=269.25 EndY=327.8 EndZ=0
    g13: LineSegment StartX=269.25 StartY=327.8 StartZ=0 EndX=261.25 EndY=327.8 EndZ=0
    g14: LineSegment StartX=261.25 StartY=327.8 StartZ=0 EndX=261.25 EndY=317.8 EndZ=0
    g15: LineSegment StartX=261.25 StartY=317.8 StartZ=0 EndX=188.75 EndY=317.8 EndZ=0
    g16: LineSegment StartX=188.75 StartY=317.8 StartZ=0 EndX=188.75 EndY=327.8 EndZ=0
    g17: LineSegment StartX=188.75 StartY=327.8 StartZ=0 EndX=180.75 EndY=327.8 EndZ=0
    g18: LineSegment StartX=180.75 StartY=327.8 StartZ=0 EndX=180.75 EndY=347.8 EndZ=0
    g19: LineSegment StartX=180.75 StartY=347.8 StartZ=0 EndX=188.75 EndY=347.8 EndZ=0
    g20: LineSegment StartX=188.75 StartY=347.8 StartZ=0 EndX=188.75 EndY=357.8 EndZ=0
    g21: LineSegment StartX=182.5 StartY=460 StartZ=0 EndX=182.5 EndY=469.3 EndZ=0
    g22: LineSegment StartX=182.5 StartY=469.3 StartZ=0 EndX=210 EndY=469.3 EndZ=0
    g23: LineSegment StartX=182.5 StartY=441 StartZ=0 EndX=182.5 EndY=400 EndZ=0
    g24: LineSegment StartX=177 StartY=469.3 StartZ=0 EndX=177 EndY=357.8 EndZ=0
    g25: LineSegment StartX=177 StartY=357.8 StartZ=0 EndX=180.75 EndY=357.8 EndZ=0
    g26: LineSegment StartX=180.75 StartY=357.8 StartZ=0 EndX=188.75 EndY=357.8 EndZ=0
    g27: LineSegment StartX=261.25 StartY=357.8 StartZ=0 EndX=261.25 EndY=381 EndZ=0
  constraints (76):
    c: Vertical(g0)
    c: Coincident(g1,g2)
    c: Coincident(g2,g3)
    c: Coincident(g3,g4)
    c: Coincident(g4,g1)
    c: Horizontal(g1)
    c: Horizontal(g3)
    c: Vertical(g2)
    c: Vertical(g4)
    c: DistanceX(g1,g1) = 85
    c: DistanceY(g2,g2) = 19
    c: Coincident(g5,g6)
    c: Coincident(g6,g7)
    c: Coincident(g7,g8)
    c: Coincident(g8,g5)
    c: Horizontal(g5)
    c: Horizontal(g7)
    c: Vertical(g6)
    c: Vertical(g8)
    c: DistanceX(g5,g5) = 85
    c: DistanceY(g8,g8) = 19
    c: Horizontal(g9)
    c: Coincident(g9,g10)
    c: Vertical(g10)
    c: Coincident(g10,g11)
    c: Horizontal(g11)
    c: Coincident(g11,g12)
    c: Vertical(g12)
    c: Coincident(g12,g13)
    c: Horizontal(g13)
    c: Coincident(g13,g14)
    c: Vertical(g14)
    c: Coincident(g14,g15)
    c: Horizontal(g15)
    c: Coincident(g15,g16)
    c: Vertical(g16)
    c: Coincident(g16,g17)
    c: Horizontal(g17)
    c: Coincident(g17,g18)
    c: Vertical(g18)
    c: Coincident(g18,g19)
    c: Horizontal(g19)
    c: Coincident(g19,g20)
    c: Coincident(g20,g9)
    c: Vertical(g20)
    c: DistanceX(g9,g9) = 72.5
    c: DistanceY(g12,g12) = 20
    c: DistanceY(g10,g10) = 10
    c: DistanceY(g14,g14) = 10
    c: DistanceX(g19,g19) = 8
    c: DistanceX(g17,g17) = 8
    c: DistanceX(g13,g13) = 8
    c: DistanceY(g20,g20) = 10
    c: DistanceY(g16,g16) = 10
    c: DistanceX(g15,g15) = 72.5
    c: Coincident(g21,g1)
    c: Vertical(g21)
    c: DistanceY(g21,g21) = 9.3
    c: Coincident(g22,g21)
    c: Horizontal(g22)
    c: Coincident(g23,g3)
    c: Vertical(g23)
    c: DistanceY(g23,g23) = 41
    c: Vertical(g24)
    c: Coincident(g25,g24)
    c: Horizontal(g25)
    c: DistanceY(g24,g24) = 111.5
    c: Coincident(g26,g25)
    c: Coincident(g26,g9)
    c: Horizontal(g26)
    c: DistanceX(g26,g26) = 8
    c: DistanceX(g25,g25) = 3.74999
    c: Coincident(g27,g9)
    c: PointOnObject(g27,g7)
    c: Vertical(g27)
    c: DistanceY(g27,g27) = 23.2
FEATURE [Sketcher::SketchObject] Sketch229  label="tremelo pocket003"
  FullyConstrained = false
  MapMode = 5
  Placement = pos=(0,0,7) rot=(0,0,1;0rad)
  Support = -> [Pad014]
  sketch-geometry (11):
    g0: LineSegment StartX=225 StartY=610 StartZ=0 EndX=225 EndY=-10 EndZ=0
    g1: LineSegment StartX=182.5 StartY=460 StartZ=0 EndX=182.5 EndY=469.3 EndZ=0
    g2: LineSegment StartX=182.5 StartY=469.3 StartZ=0 EndX=182.5 EndY=481.3 EndZ=0
    g3: LineSegment StartX=178 StartY=481.3 StartZ=0 EndX=178 EndY=295.3 EndZ=0
    g4: LineSegment StartX=178 StartY=295.3 StartZ=0 EndX=178 EndY=282.3 EndZ=0
    g5: LineSegment StartX=224.9 StartY=282.4 StartZ=0 EndX=224.99 EndY=282.4 EndZ=0
    g6: LineSegment StartX=224.9 StartY=282.4 StartZ=0 EndX=189.9 EndY=282.4 EndZ=0
    g7: LineSegment StartX=189.9 StartY=282.3 StartZ=0 EndX=267.9 EndY=282.3 EndZ=0
    g8: LineSegment StartX=267.9 StartY=282.3 StartZ=0 EndX=267.9 EndY=263.3 EndZ=0
    g9: LineSegment StartX=267.9 StartY=263.3 StartZ=0 EndX=189.9 EndY=263.3 EndZ=0
    g10: LineSegment StartX=189.9 StartY=263.3 StartZ=0 EndX=189.9 EndY=282.3 EndZ=0
  constraints (26):
    c: Vertical(g0)
    c: Vertical(g1)
    c: Coincident(g2,g1)
    c: Vertical(g2)
    c: Vertical(g3)
    c: Coincident(g4,g3)
    c: Vertical(g4)
    c: DistanceY(g4,g4) = 13
    c: DistanceY(g3,g3) = 186
    c: DistanceY(g1,g1) = 9.3
    c: DistanceY(g2,g2) = 12
    c: Horizontal(g5)
    c: Coincident(g6,g5)
    c: Horizontal(g6)
    c: DistanceX(g6,g6) = 35
    c: DistanceX(g5,g5) = 0.08999
    c: Coincident(g7,g8)
    c: Coincident(g8,g9)
    c: Coincident(g9,g10)
    c: Coincident(g10,g7)
    c: Horizontal(g7)
    c: Horizontal(g9)
    c: Vertical(g8)
    c: Vertical(g10)
    c: DistanceX(g7,g7) = 78
    c: DistanceY(g10,g10) = 19
FEATURE [Sketcher::SketchObject] Sketch236  label="neck pocket003"
  FullyConstrained = false
  MapMode = 5
  Placement = pos=(0,0,7) rot=(0,0,1;0rad)
  Support = -> [Pad014]
  sketch-geometry (8):
    g0: LineSegment StartX=225 StartY=610 StartZ=0 EndX=225 EndY=-10 EndZ=0
    g1: LineSegment StartX=182.5 StartY=460 StartZ=0 EndX=182.5 EndY=469.332 EndZ=0
    g2: LineSegment StartX=182.5 StartY=469.332 StartZ=0 EndX=225 EndY=469.332 EndZ=0
    g3: LineSegment StartX=196.001 StartY=469.332 StartZ=0 EndX=196.001 EndY=545.5 EndZ=0
    g4: ArcOfCircle CenterX=225 CenterY=596.31 CenterZ=0 NormalX=0 NormalY=0 NormalZ=1 AngleXU=0 Radius=127 StartAngle=4.4901 EndAngle=4.93459
    g5: LineSegment StartX=252.988 StartY=472.432 StartZ=0 EndX=252.15 EndY=545.7 EndZ=0
    g6: LineSegment StartX=197.001 StartY=472.435 StartZ=0 EndX=197.8 EndY=545.7 EndZ=0
    g7: LineSegment StartX=197.8 StartY=545.7 StartZ=0 EndX=252.15 EndY=545.7 EndZ=0
  constraints (15):
    c: Vertical(g0)
    c: Vertical(g1)
    c: Coincident(g2,g1)
    c: Horizontal(g2)
    c: PointOnObject(g3,g2)
    c: Vertical(g3)
    c: Radius(g4) = 127
    c: Coincident(g5,g4)
    c: Distance(g5) = 73.2725
    c: Coincident(g6,g4)
    c: Coincident(g7,g6)
    c: Coincident(g7,g5)
    c: Horizontal(g7)
    c: DistanceX(g7,g7) = 54.35
    c: Distance(g6) = 73.2695
FEATURE [Sketcher::SketchObject] Sketch237  label="Body Outline006"
  FullyConstrained = false
  MapMode = 5
  Placement = pos=(0,0,7) rot=(0,0,1;0rad)
  Support = -> [Pad014]
  sketch-geometry (54):
    g0: LineSegment StartX=197.29 StartY=495.3 StartZ=0 EndX=73.9 EndY=550.1 EndZ=0
    g1: LineSegment StartX=252.15 StartY=545.5 StartZ=0 EndX=252.536 EndY=509.5 EndZ=0
    g2: LineSegment StartX=252.536 StartY=509.5 StartZ=0 EndX=349.402 EndY=461.057 EndZ=0
    g3: LineSegment StartX=349.402 StartY=461.057 StartZ=0 EndX=353.186 EndY=456.92 EndZ=0
    g4: LineSegment StartX=353.186 StartY=456.92 StartZ=0 EndX=355.987 EndY=452.42 EndZ=0
    g5: LineSegment StartX=355.987 StartY=452.42 StartZ=0 EndX=355.987 EndY=442.02 EndZ=0
    g6: LineSegment StartX=355.987 StartY=442.02 StartZ=0 EndX=320 EndY=343.5 EndZ=0
    g7: LineSegment StartX=320 StartY=343.5 StartZ=0 EndX=320 EndY=331.5 EndZ=0
    g8: LineSegment StartX=195.596 StartY=533.25 StartZ=0 EndX=190.601 EndY=530.784 EndZ=0
    g9: LineSegment StartX=190.601 StartY=530.784 StartZ=0 EndX=185.731 EndY=530.784 EndZ=0
    g10: LineSegment StartX=185.731 StartY=530.784 StartZ=0 EndX=184.499 EndY=530.912 EndZ=0
    g11: LineSegment StartX=184.499 StartY=530.912 StartZ=0 EndX=97.9865 EndY=587.073 EndZ=0
    g12: LineSegment StartX=97.9865 StartY=587.073 StartZ=0 EndX=91.1348 EndY=587.073 EndZ=0
    g13: LineSegment StartX=91.1348 StartY=587.073 StartZ=0 EndX=89.4748 EndY=585.83 EndZ=0
    g14: LineSegment StartX=89.4748 StartY=585.83 StartZ=0 EndX=87.4848 EndY=583.86 EndZ=0
    g15: LineSegment StartX=87.4848 StartY=583.86 StartZ=0 EndX=85.9748 EndY=581.98 EndZ=0
    g16: LineSegment StartX=107.659 StartY=357.048 StartZ=0 EndX=122.894 EndY=344.497 EndZ=0
    g17: LineSegment StartX=122.894 StartY=344.497 StartZ=0 EndX=130.394 EndY=322.397 EndZ=0
    g18: LineSegment StartX=130.394 StartY=322.397 StartZ=0 EndX=130.394 EndY=310.397 EndZ=0
    g19: LineSegment StartX=130.394 StartY=310.397 StartZ=0 EndX=128.394 EndY=307.697 EndZ=0
    g20: LineSegment StartX=128.394 StartY=307.697 StartZ=0 EndX=44.2002 EndY=150.2 EndZ=0
    g21: LineSegment StartX=44.2002 StartY=150.2 StartZ=0 EndX=44.2002 EndY=148.6 EndZ=0
    g22: LineSegment StartX=44.2002 StartY=148.6 StartZ=0 EndX=44.2002 EndY=144.6 EndZ=0
    g23: LineSegment StartX=44.2002 StartY=144.6 StartZ=0 EndX=45.1102 EndY=141.95 EndZ=0
    g24: LineSegment StartX=45.1102 StartY=141.95 StartZ=0 EndX=47.2242 EndY=138.987 EndZ=0
    g25: LineSegment StartX=47.2242 StartY=138.987 StartZ=0 EndX=50.9702 EndY=135.84 EndZ=0
    g26: LineSegment StartX=413.447 StartY=50.3962 StartZ=0 EndX=410.947 EndY=46.6962 EndZ=0
    g27: LineSegment StartX=410.947 StartY=46.6962 StartZ=0 EndX=408.821 EndY=43.4657 EndZ=0
    g28: LineSegment StartX=408.821 StartY=43.4657 StartZ=0 EndX=403.447 EndY=43.4657 EndZ=0
    g29: LineSegment StartX=403.447 StartY=43.4657 StartZ=0 EndX=320.445 EndY=66.6106 EndZ=0
    g30: LineSegment StartX=320.445 StartY=66.6106 StartZ=0 EndX=290 EndY=70.0001 EndZ=0
    g31: LineSegment StartX=290 StartY=70.0001 StartZ=0 EndX=160 EndY=70.0001 EndZ=0
    g32: LineSegment StartX=160 StartY=70.0001 StartZ=0 EndX=50.9702 EndY=135.84 EndZ=0
    g33: LineSegment StartX=252.15 StartY=545.5 StartZ=0 EndX=197.848 EndY=545.5 EndZ=0
    g34: LineSegment StartX=197.848 StartY=545.5 StartZ=0 EndX=197.726 EndY=534.521 EndZ=0
    g35: LineSegment StartX=197.726 StartY=534.521 StartZ=0 EndX=195.596 EndY=533.25 EndZ=0
    g36: LineSegment StartX=107.659 StartY=357.048 StartZ=0 EndX=96.1282 EndY=362.119 EndZ=0
    g37: LineSegment StartX=96.1282 StartY=362.119 StartZ=0 EndX=64 EndY=377 EndZ=0
    g38: LineSegment StartX=64 StartY=377 StartZ=0 EndX=61 EndY=378.8 EndZ=0
    g39: LineSegment StartX=61 StartY=378.8 StartZ=0 EndX=56.5 EndY=383.7 EndZ=0
    g40: LineSegment StartX=56.5 StartY=383.7 StartZ=0 EndX=54 EndY=388 EndZ=0
    g41: LineSegment StartX=54 StartY=388 StartZ=0 EndX=52.6 EndY=392 EndZ=0
    g42: LineSegment StartX=52.6 StartY=392 StartZ=0 EndX=52.6 EndY=529.8 EndZ=0
    g43: LineSegment StartX=52.6 StartY=529.8 StartZ=0 EndX=54 EndY=534 EndZ=0
    g44: LineSegment StartX=54 StartY=534 StartZ=0 EndX=57 EndY=538 EndZ=0
    g45: LineSegment StartX=57 StartY=538 StartZ=0 EndX=85.9748 EndY=581.98 EndZ=0
    g46: LineSegment StartX=413.447 StartY=50.3962 StartZ=0 EndX=413.447 EndY=57.5962 EndZ=0
    g47: LineSegment StartX=-1 StartY=616 StartZ=0 EndX=451 EndY=616 EndZ=0
    g48: LineSegment StartX=451 StartY=616 StartZ=0 EndX=451 EndY=14 EndZ=0
    g49: LineSegment StartX=451 StartY=14 StartZ=0 EndX=-1 EndY=14 EndZ=0
    g50: LineSegment StartX=-1 StartY=14 StartZ=0 EndX=-1 EndY=616 EndZ=0
    g51: LineSegment StartX=257 StartY=545.5 StartZ=0 EndX=257 EndY=245.424 EndZ=0
    g52: LineSegment StartX=320 StartY=331.5 StartZ=0 EndX=413.447 EndY=57.5962 EndZ=0
    g53: LineSegment StartX=320 StartY=331.5 StartZ=0 EndX=127.305 EndY=331.5 EndZ=0
  constraints (149):
    c: Coincident(g1,g2)
    c: Coincident(g2,g3)
    c: Coincident(g3,g4)
    c: Coincident(g4,g5)
    c: Vertical(g5)
    c: Coincident(g6,g5)
    c: Coincident(g7,g6)
    c: Vertical(g7)
    c: Coincident(g8,g9)
    c: Horizontal(g9)
    c: Coincident(g9,g10)
    c: Coincident(g10,g11)
    c: Distance(g10) = 1.23908
    c: Distance(g8) = 5.57001
    c: DistanceX(g9,g9) = 4.86999
    c: Coincident(g12,g11)
    c: Horizontal(g12)
    c: Coincident(g13,g12)
    c: Coincident(g13,g14)
    c: Coincident(g14,g15)
    c: Coincident(g16,g17)
    c: Coincident(g17,g18)
    c: Vertical(g18)
    c: Coincident(g19,g18)
    c: Coincident(g20,g19)
    c: Coincident(g21,g20)
    c: Vertical(g21)
    c: Coincident(g21,g22)
    c: Vertical(g22)
    c: Coincident(g22,g23)
    c: Coincident(g23,g24)
    c: Coincident(g24,g25)
    c: Coincident(g27,g26)
    c: Coincident(g28,g27)
    c: Horizontal(g28)
    c: DistanceX(g28,g28) = 5.37372
    c: Distance(g26) = 4.46542
    c: Distance(g27) = 3.86749
    c: Coincident(g29,g28)
    c: DistanceY(g7,g7) = 12
    c: DistanceY(g5,g5) = 10.4
    c: Distance(g4) = 5.3
    c: Distance(g3) = 5.60673
    c: Distance(g1) = 36.0023
    c: Distance(g15) = 2.41133
    c: Distance(g14) = 2.80018
    c: Distance(g13) = 2.07357
    c: DistanceX(g12,g12) = 6.85172
    c: Distance(g16) = 19.7388
    c: Distance(g17) = 23.3379
    c: DistanceY(g18,g18) = 12
    c: DistanceY(g21,g21) = 1.6
    c: DistanceY(g22,g22) = 4
    c: Distance(g23) = 2.8019
    c: Distance(g24) = 3.63982
    c: Distance(g25) = 4.89246
    c: Angle(g23,g22) = 2.81082
    c: Angle(g24,g22) = 2.52188
    c: Angle(g25,g22) = 2.26951
    c: Angle(g18,g19) = 2.50404
    c: Angle(g17,g18) = 2.81442
    c: Coincident(g30,g29)
    c: Coincident(g31,g30)
    c: Horizontal(g31)
    c: Coincident(g32,g31)
    c: Coincident(g32,g25)
    c: Distance(g30) = 30.6334
    c: Angle(g30,g28) = 0.110874
    c: DistanceX(g31,g31) = 130
    c: Distance(g32) = 127.367
    c: Coincident(g1,g33)
    c: Horizontal(g33)
    c: Coincident(g33,g34)
    c: Coincident(g35,g34)
    c: Coincident(g35,g8)
    c: Distance(g35) = 2.4804
    c: Angle(g13,g12) = 2.49901
    c: Angle(g14,g12) = 2.36124
    c: Angle(g15,g12) = 2.24748
    c: Angle(g34,g35) = 2.11973
    c: Angle(g34,g8) = 2.04062
    c: Angle(g34,g9) = 1.58195
    c: Angle(g9,g10) = 3.03808
    c: Angle(g31,g32) = 2.59833
    c: Coincident(g16,g36)
    c: Coincident(g36,g37)
    c: Coincident(g37,g38)
    c: Coincident(g38,g39)
    c: Coincident(g39,g40)
    c: Coincident(g40,g41)
    c: Coincident(g41,g42)
    c: Vertical(g42)
    c: Coincident(g42,g43)
    c: Coincident(g43,g44)
    c: Coincident(g45,g15)
    c: Distance(g36) = 12.5968
    c: Distance(g37) = 35.4072
    c: Distance(g38) = 3.49857
    c: Distance(g39) = 6.65282
    c: Distance(g40) = 4.97393
    c: Distance(g41) = 4.23793
    c: DistanceY(g42,g42) = 137.8
    c: Angle(g16,g17) = 2.58706
    c: Angle(g36,g16) = 2.86681
    c: Angle(g36,g37) = 3.12214
    c: Angle(g37,g38) = 3.03493
    c: Angle(g38,g39) = 2.85409
    c: Angle(g39,g40) = 2.92535
    c: Angle(g40,g41) = 2.95164
    c: Angle(g42,g43) = 2.81984
    c: Angle(g42,g44) = 2.49809
    c: Angle(g33,g1) = 1.58154
    c: Distance(g34) = 10.9802
    c: Distance(g45) = 52.6666
    c: Distance(g44) = 5
    c: Distance(g43) = 4.42719
    c: Distance(g11) = 103.143
    c: Coincident(g44,g45)
    c: Coincident(g46,g26)
    c: Vertical(g46)
    c: Distance(g46) = 7.20003
    c: Angle(g46,g26) = 2.54737
    c: Coincident(g47,g48)
    c: Coincident(g48,g49)
    c: Coincident(g49,g50)
    c: Coincident(g50,g47)
    c: Horizontal(g47)
    c: Horizontal(g49)
    c: Vertical(g48)
    c: Vertical(g50)
    c: DistanceY(g48,g48) = 602
    c: DistanceX(g49,g49) = 452
    c: Vertical(g51)
    c: Coincident(g52,g7)
    c: Coincident(g52,g46)
    c: Angle(g27,g28) = 2.1529
    c: Angle(g4,g5) = 2.58482
    c: Angle(g3,g5) = 2.40074
    c: Distance(g2) = 108.304
    c: Angle(g2,g5) = 2.03453
    c: Angle(g28,g29) = 2.86965
    c: DistanceX(g33,g33) = 54.3011
    c: Angle(g21,g20) = 2.65067
    c: Distance(g20) = 178.589
    c: Distance(g19) = 3.36006
    c: Coincident(g53,g7)
    c: PointOnObject(g53,g17)
    c: Horizontal(g53)
    c: DistanceX(g53,g53) = 192.695
FEATURE [PartDesign::Pocket] Pocket089  label="Body Cutout002"
  BaseFeature = -> Pad014
  Direction = (0,0,-1)
  Length = 45
  Length2 = 5
  Profile = -> Sketch237
  ReferenceAxis = -> Sketch237 [N_Axis]
  Type = 0
FEATURE [Sketcher::SketchObject] Sketch238  label="speaker grill recess003"
  FullyConstrained = false
  MapMode = 5
  Placement = pos=(0,0,7) rot=(0,0,1;0rad)
  Support = -> [Pad014]
  sketch-geometry (1):
    g0: Circle CenterX=330 CenterY=121 CenterZ=0 NormalX=0 NormalY=0 NormalZ=1 AngleXU=0 Radius=47
  constraints (1):
    c: Diameter(g0) = 94
FEATURE [Sketcher::SketchObject] Sketch240  label="AFPI Mount Pocket003"
  FullyConstrained = false
  MapMode = 5
  Placement = pos=(0,0,7) rot=(0,0,1;0rad)
  Support = -> [Pad014]
  sketch-geometry (4):
    g0: LineSegment StartX=68 StartY=514 StartZ=0 EndX=160 EndY=514 EndZ=0
    g1: LineSegment StartX=160 StartY=514 StartZ=0 EndX=160 EndY=395 EndZ=0
    g2: LineSegment StartX=160 StartY=395 StartZ=0 EndX=68 EndY=395 EndZ=0
    g3: LineSegment StartX=68 StartY=395 StartZ=0 EndX=68 EndY=514 EndZ=0
  constraints (10):
    c: Coincident(g0,g1)
    c: Coincident(g1,g2)
    c: Coincident(g2,g3)
    c: Coincident(g3,g0)
    c: Horizontal(g0)
    c: Horizontal(g2)
    c: Vertical(g1)
    c: Vertical(g3)
    c: DistanceY(g1,g1) = 119
    c: DistanceX(g0,g0) = 92
FEATURE [Sketcher::SketchObject] Sketch242  label="RGB clear plate pocket003"
  FullyConstrained = false
  MapMode = 5
  Placement = pos=(0,0,7) rot=(0,0,1;0rad)
  Support = -> [Pad014]
  sketch-geometry (4):
    g0: LineSegment StartX=178 StartY=430.5 StartZ=0 EndX=272 EndY=430.5 EndZ=0
    g1: LineSegment StartX=272 StartY=430.5 StartZ=0 EndX=272 EndY=410.5 EndZ=0
    g2: LineSegment StartX=272 StartY=410.5 StartZ=0 EndX=178 EndY=410.5 EndZ=0
    g3: LineSegment StartX=178 StartY=410.5 StartZ=0 EndX=178 EndY=430.5 EndZ=0
  constraints (10):
    c: Coincident(g0,g1)
    c: Coincident(g1,g2)
    c: Coincident(g2,g3)
    c: Coincident(g3,g0)
    c: Horizontal(g0)
    c: Horizontal(g2)
    c: Vertical(g1)
    c: Vertical(g3)
    c: DistanceY(g3,g3) = 20
    c: DistanceX(g0,g0) = 94
FEATURE [Sketcher::SketchObject] Sketch258  label="blank template004"
  FullyConstrained = false
  MapMode = 5
  Support = -> [XY_Plane207]
  sketch-geometry (4):
    g0: LineSegment StartX=0 StartY=615 StartZ=0 EndX=450 EndY=615 EndZ=0
    g1: LineSegment StartX=450 StartY=615 StartZ=0 EndX=450 EndY=15 EndZ=0
    g2: LineSegment StartX=450 StartY=15 StartZ=0 EndX=0 EndY=15 EndZ=0
    g3: LineSegment StartX=0 StartY=15 StartZ=0 EndX=0 EndY=615 EndZ=0
  constraints (10):
    c: Coincident(g0,g1)
    c: Coincident(g1,g2)
    c: Coincident(g2,g3)
    c: Coincident(g3,g0)
    c: Horizontal(g0)
    c: Horizontal(g2)
    c: Vertical(g1)
    c: Vertical(g3)
    c: DistanceX(g2,g2) = 450
    c: DistanceY(g1,g1) = 600
FEATURE [PartDesign::Pad] Pad015  label="Template 600x453"
  Direction = (0,0,1)
  Length = 7
  Length2 = 10
  Profile = -> Sketch258
  ReferenceAxis = -> Sketch258 [N_Axis]
  Type = 0
FEATURE [Sketcher::SketchObject] Sketch262  label="AFPI pocket004"
  FullyConstrained = false
  MapMode = 5
  Placement = pos=(0,0,7) rot=(0,0,1;0rad)
  Support = -> [Pad015]
  sketch-geometry (24):
    g0: LineSegment StartX=68 StartY=506.5 StartZ=0 EndX=160 EndY=506.5 EndZ=0
    g1: LineSegment StartX=160 StartY=506.5 StartZ=0 EndX=160 EndY=402.5 EndZ=0
    g2: LineSegment StartX=160 StartY=402.5 StartZ=0 EndX=68 EndY=402.5 EndZ=0
    g3: LineSegment StartX=68 StartY=402.5 StartZ=0 EndX=68 EndY=506.5 EndZ=0
    g4: LineSegment StartX=-192.181 StartY=581.522 StartZ=0 EndX=-181.31 EndY=478.092 EndZ=0
    g5: LineSegment StartX=-181.31 StartY=478.092 StartZ=0 EndX=-89.8139 EndY=487.709 EndZ=0
    g6: LineSegment StartX=-192.181 StartY=581.522 StartZ=0 EndX=-100.685 EndY=591.139 EndZ=0
    g7: LineSegment StartX=-100.685 StartY=591.139 StartZ=0 EndX=-89.8139 EndY=487.709 EndZ=0
    g8: LineSegment StartX=-192.181 StartY=581.522 StartZ=0 EndX=-192.181 EndY=481.522 EndZ=0
    g9: LineSegment StartX=175 StartY=400 StartZ=0 EndX=275 EndY=400 EndZ=0
    g10: LineSegment StartX=175 StartY=400 StartZ=0 EndX=175 EndY=490 EndZ=0
    g11: LineSegment StartX=175 StartY=400 StartZ=0 EndX=175 EndY=380 EndZ=0
    g12: LineSegment StartX=-89.8139 StartY=487.709 StartZ=0 EndX=-88.927 EndY=479.201 EndZ=0
    g13: LineSegment StartX=-181.31 StartY=478.092 StartZ=0 EndX=-180.433 EndY=469.628 EndZ=0
    g14: LineSegment StartX=-180.433 StartY=469.628 StartZ=0 EndX=-88.927 EndY=479.201 EndZ=0
    g15: LineSegment StartX=-192.181 StartY=581.522 StartZ=0 EndX=-193.082 EndY=590 EndZ=0
    g16: LineSegment StartX=-100.685 StartY=591.139 StartZ=0 EndX=-101.58 EndY=599.597 EndZ=0
    g17: LineSegment StartX=-101.58 StartY=599.597 StartZ=0 EndX=-193.082 EndY=590 EndZ=0
    g18: LineSegment StartX=68 StartY=506.5 StartZ=0 EndX=68 EndY=515 EndZ=0
    g19: LineSegment StartX=68 StartY=515 StartZ=0 EndX=160 EndY=515 EndZ=0
    g20: LineSegment StartX=160 StartY=515 StartZ=0 EndX=160 EndY=506.5 EndZ=0
    g21: LineSegment StartX=160 StartY=402.5 StartZ=0 EndX=160 EndY=393.9 EndZ=0
    g22: LineSegment StartX=160 StartY=393.9 StartZ=0 EndX=68 EndY=393.9 EndZ=0
    g23: LineSegment StartX=68 StartY=393.9 StartZ=0 EndX=68 EndY=402.5 EndZ=0
  constraints (60):
    c: Coincident(g0,g1)
    c: Coincident(g1,g2)
    c: Coincident(g2,g3)
    c: Coincident(g3,g0)
    c: Horizontal(g0)
    c: Horizontal(g2)
    c: Vertical(g1)
    c: Vertical(g3)
    c: DistanceY(g1,g1) = 104
    c: DistanceX(g0,g0) = 92
    c: Coincident(g4,g5)
    c: Coincident(g4,g6)
    c: Coincident(g6,g7)
    c: Coincident(g7,g5)
    c: Angle(g7,g5) = 1.5708
    c: Angle(g6,g7) = 1.5708
    c: Angle(g4,g6) = 1.5708
    c: Distance(g4) = 104
    c: Distance(g5) = 92
    c: Coincident(g8,g4)
    c: Vertical(g8)
    c: Angle(g8,g4) = 0.10472
    c: DistanceY(g8,g8) = 100
    c: Horizontal(g9)
    c: Coincident(g10,g9)
    c: Vertical(g10)
    c: Coincident(g11,g9)
    c: Vertical(g11)
    c: Coincident(g5,g12)
    c: Coincident(g4,g13)
    c: Coincident(g13,g14)
    c: Coincident(g14,g12)
    c: Distance(g12) = 8.5541
    c: Distance(g14) = 92.0049
    c: Distance(g13) = 8.50942
    c: Coincident(g4,g15)
    c: Coincident(g16,g6)
    c: Coincident(g17,g16)
    c: Coincident(g17,g15)
    c: Distance(g15) = 8.52543
    c: Distance(g17) = 92.0046
    c: Distance(g16) = 8.50507
    c: Angle(g17,g16) = 1.57171
    c: Angle(g12,g14) = 1.57116
    c: Coincident(g0,g18)
    c: Vertical(g18)
    c: Coincident(g18,g19)
    c: Horizontal(g19)
    c: Coincident(g19,g20)
    c: Coincident(g20,g0)
    c: Vertical(g20)
    c: Coincident(g1,g21)
    c: Vertical(g21)
    c: Coincident(g21,g22)
    c: Horizontal(g22)
    c: Coincident(g22,g23)
    c: Coincident(g23,g2)
    c: Vertical(g23)
    c: DistanceY(g23,g23) = 8.59999
    c: DistanceY(g18,g18) = 8.50001
FEATURE [Sketcher::SketchObject] Sketch264  label="RGB Board Pockets004"
  FullyConstrained = false
  MapMode = 5
  Placement = pos=(0,0,7) rot=(0,0,1;0rad)
  Support = -> [Pad015]
  sketch-geometry (12):
    g0: LineSegment StartX=220 StartY=282.3 StartZ=0 EndX=220 EndY=284.3 EndZ=0
    g1: LineSegment StartX=220 StartY=284.3 StartZ=0 EndX=220 EndY=382.3 EndZ=0
    g2: LineSegment StartX=183 StartY=427.9 StartZ=0 EndX=267 EndY=427.9 EndZ=0
    g3: LineSegment StartX=267 StartY=427.9 StartZ=0 EndX=267 EndY=412.9 EndZ=0
    g4: LineSegment StartX=267 StartY=412.9 StartZ=0 EndX=183 EndY=412.9 EndZ=0
    g5: LineSegment StartX=183 StartY=412.9 StartZ=0 EndX=183 EndY=427.9 EndZ=0
    g6: LineSegment StartX=182.5 StartY=460 StartZ=0 EndX=225 EndY=460 EndZ=0
    g7: LineSegment StartX=225 StartY=460 StartZ=0 EndX=225 EndY=244 EndZ=0
    g8: LineSegment StartX=267.5 StartY=441 StartZ=0 EndX=267.5 EndY=400 EndZ=0
    g9: LineSegment StartX=267 StartY=441 StartZ=0 EndX=267 EndY=420.4 EndZ=0
    g10: LineSegment StartX=263.999 StartY=441 StartZ=0 EndX=263.999 EndY=427.9 EndZ=0
    g11: LineSegment StartX=210 StartY=282.3 StartZ=0 EndX=210 EndY=302.3 EndZ=0
  constraints (21):
    c: Vertical(g0)
    c: Coincident(g1,g0)
    c: Vertical(g1)
    c: Coincident(g2,g3)
    c: Coincident(g3,g4)
    c: Coincident(g4,g5)
    c: Coincident(g5,g2)
    c: Horizontal(g2)
    c: Horizontal(g4)
    c: Vertical(g3)
    c: Vertical(g5)
    c: DistanceX(g2,g2) = 84
    c: DistanceY(g5,g5) = 15
    c: Horizontal(g6)
    c: Coincident(g7,g6)
    c: Vertical(g7)
    c: Vertical(g8)
    c: Vertical(g9)
    c: PointOnObject(g10,g2)
    c: Vertical(g10)
    c: Vertical(g11)
FEATURE [Sketcher::SketchObject] Sketch266  label="control plate mount pocket005"
  FullyConstrained = false
  MapMode = 5
  Placement = pos=(0,0,7) rot=(0,0,1;0rad)
  Support = -> [Pad015]
  sketch-geometry (6):
    g0: LineSegment StartX=267.9 StartY=263.3 StartZ=0 EndX=267.9 EndY=243.3 EndZ=0
    g1: LineSegment StartX=267.9 StartY=243.3 StartZ=0 EndX=272.9 EndY=243.3 EndZ=0
    g2: LineSegment StartX=282 StartY=258 StartZ=0 EndX=337 EndY=258 EndZ=0
    g3: LineSegment StartX=282 StartY=258 StartZ=0 EndX=282 EndY=172 EndZ=0
    g4: LineSegment StartX=282 StartY=172 StartZ=0 EndX=365.925 EndY=172 EndZ=0
    g5: LineSegment StartX=365.925 StartY=172 StartZ=0 EndX=337 EndY=258 EndZ=0
  constraints (12):
    c: Vertical(g0)
    c: Coincident(g1,g0)
    c: Horizontal(g1)
    c: Horizontal(g2)
    c: Coincident(g3,g2)
    c: Vertical(g3)
    c: DistanceY(g3,g3) = 86
    c: Coincident(g4,g3)
    c: Horizontal(g4)
    c: Coincident(g5,g4)
    c: Coincident(g5,g2)
    c: Distance(g5) = 90.7339
FEATURE [Sketcher::SketchObject] Sketch268  label="Body Outline007"
  FullyConstrained = false
  MapMode = 5
  Placement = pos=(0,0,7) rot=(0,0,1;0rad)
  Support = -> [Pad015]
  sketch-geometry (54):
    g0: LineSegment StartX=197.29 StartY=495.3 StartZ=0 EndX=73.9 EndY=550.1 EndZ=0
    g1: LineSegment StartX=252.15 StartY=545.5 StartZ=0 EndX=252.536 EndY=509.5 EndZ=0
    g2: LineSegment StartX=252.536 StartY=509.5 StartZ=0 EndX=349.402 EndY=461.057 EndZ=0
    g3: LineSegment StartX=349.402 StartY=461.057 StartZ=0 EndX=353.186 EndY=456.92 EndZ=0
    g4: LineSegment StartX=353.186 StartY=456.92 StartZ=0 EndX=355.987 EndY=452.42 EndZ=0
    g5: LineSegment StartX=355.987 StartY=452.42 StartZ=0 EndX=355.987 EndY=442.02 EndZ=0
    g6: LineSegment StartX=355.987 StartY=442.02 StartZ=0 EndX=320 EndY=343.5 EndZ=0
    g7: LineSegment StartX=320 StartY=343.5 StartZ=0 EndX=320 EndY=331.5 EndZ=0
    g8: LineSegment StartX=195.596 StartY=533.25 StartZ=0 EndX=190.601 EndY=530.784 EndZ=0
    g9: LineSegment StartX=190.601 StartY=530.784 StartZ=0 EndX=185.731 EndY=530.784 EndZ=0
    g10: LineSegment StartX=185.731 StartY=530.784 StartZ=0 EndX=184.499 EndY=530.912 EndZ=0
    g11: LineSegment StartX=184.499 StartY=530.912 StartZ=0 EndX=97.9865 EndY=587.073 EndZ=0
    g12: LineSegment StartX=97.9865 StartY=587.073 StartZ=0 EndX=91.1348 EndY=587.073 EndZ=0
    g13: LineSegment StartX=91.1348 StartY=587.073 StartZ=0 EndX=89.4748 EndY=585.83 EndZ=0
    g14: LineSegment StartX=89.4748 StartY=585.83 StartZ=0 EndX=87.4848 EndY=583.86 EndZ=0
    g15: LineSegment StartX=87.4848 StartY=583.86 StartZ=0 EndX=85.9748 EndY=581.98 EndZ=0
    g16: LineSegment StartX=107.659 StartY=357.048 StartZ=0 EndX=122.894 EndY=344.497 EndZ=0
    g17: LineSegment StartX=122.894 StartY=344.497 StartZ=0 EndX=130.394 EndY=322.397 EndZ=0
    g18: LineSegment StartX=130.394 StartY=322.397 StartZ=0 EndX=130.394 EndY=310.397 EndZ=0
    g19: LineSegment StartX=130.394 StartY=310.397 StartZ=0 EndX=128.394 EndY=307.697 EndZ=0
    g20: LineSegment StartX=128.394 StartY=307.697 StartZ=0 EndX=44.2002 EndY=150.2 EndZ=0
    g21: LineSegment StartX=44.2002 StartY=150.2 StartZ=0 EndX=44.2002 EndY=148.6 EndZ=0
    g22: LineSegment StartX=44.2002 StartY=148.6 StartZ=0 EndX=44.2002 EndY=144.6 EndZ=0
    g23: LineSegment StartX=44.2002 StartY=144.6 StartZ=0 EndX=45.1102 EndY=141.95 EndZ=0
    g24: LineSegment StartX=45.1102 StartY=141.95 StartZ=0 EndX=47.2242 EndY=138.987 EndZ=0
    g25: LineSegment StartX=47.2242 StartY=138.987 StartZ=0 EndX=50.9702 EndY=135.84 EndZ=0
    g26: LineSegment StartX=413.447 StartY=50.3962 StartZ=0 EndX=410.947 EndY=46.6962 EndZ=0
    g27: LineSegment StartX=410.947 StartY=46.6962 StartZ=0 EndX=408.821 EndY=43.4657 EndZ=0
    g28: LineSegment StartX=408.821 StartY=43.4657 StartZ=0 EndX=403.447 EndY=43.4657 EndZ=0
    g29: LineSegment StartX=403.447 StartY=43.4657 StartZ=0 EndX=320.445 EndY=66.6106 EndZ=0
    g30: LineSegment StartX=320.445 StartY=66.6106 StartZ=0 EndX=290 EndY=70.0001 EndZ=0
    g31: LineSegment StartX=290 StartY=70.0001 StartZ=0 EndX=160 EndY=70.0001 EndZ=0
    g32: LineSegment StartX=160 StartY=70.0001 StartZ=0 EndX=50.9702 EndY=135.84 EndZ=0
    g33: LineSegment StartX=252.15 StartY=545.5 StartZ=0 EndX=197.848 EndY=545.5 EndZ=0
    g34: LineSegment StartX=197.848 StartY=545.5 StartZ=0 EndX=197.726 EndY=534.521 EndZ=0
    g35: LineSegment StartX=197.726 StartY=534.521 StartZ=0 EndX=195.596 EndY=533.25 EndZ=0
    g36: LineSegment StartX=107.659 StartY=357.048 StartZ=0 EndX=96.1282 EndY=362.119 EndZ=0
    g37: LineSegment StartX=96.1282 StartY=362.119 StartZ=0 EndX=64 EndY=377 EndZ=0
    g38: LineSegment StartX=64 StartY=377 StartZ=0 EndX=61 EndY=378.8 EndZ=0
    g39: LineSegment StartX=61 StartY=378.8 StartZ=0 EndX=56.5 EndY=383.7 EndZ=0
    g40: LineSegment StartX=56.5 StartY=383.7 StartZ=0 EndX=54 EndY=388 EndZ=0
    g41: LineSegment StartX=54 StartY=388 StartZ=0 EndX=52.6 EndY=392 EndZ=0
    g42: LineSegment StartX=52.6 StartY=392 StartZ=0 EndX=52.6 EndY=529.8 EndZ=0
    g43: LineSegment StartX=52.6 StartY=529.8 StartZ=0 EndX=54 EndY=534 EndZ=0
    g44: LineSegment StartX=54 StartY=534 StartZ=0 EndX=57 EndY=538 EndZ=0
    g45: LineSegment StartX=57 StartY=538 StartZ=0 EndX=85.9748 EndY=581.98 EndZ=0
    g46: LineSegment StartX=413.447 StartY=50.3962 StartZ=0 EndX=413.447 EndY=57.5962 EndZ=0
    g47: LineSegment StartX=-1 StartY=616 StartZ=0 EndX=451 EndY=616 EndZ=0
    g48: LineSegment StartX=451 StartY=616 StartZ=0 EndX=451 EndY=14 EndZ=0
    g49: LineSegment StartX=451 StartY=14 StartZ=0 EndX=-1 EndY=14 EndZ=0
    g50: LineSegment StartX=-1 StartY=14 StartZ=0 EndX=-1 EndY=616 EndZ=0
    g51: LineSegment StartX=257 StartY=545.5 StartZ=0 EndX=257 EndY=245.424 EndZ=0
    g52: LineSegment StartX=320 StartY=331.5 StartZ=0 EndX=413.447 EndY=57.5962 EndZ=0
    g53: LineSegment StartX=320 StartY=331.5 StartZ=0 EndX=127.305 EndY=331.5 EndZ=0
  constraints (149):
    c: Coincident(g1,g2)
    c: Coincident(g2,g3)
    c: Coincident(g3,g4)
    c: Coincident(g4,g5)
    c: Vertical(g5)
    c: Coincident(g6,g5)
    c: Coincident(g7,g6)
    c: Vertical(g7)
    c: Coincident(g8,g9)
    c: Horizontal(g9)
    c: Coincident(g9,g10)
    c: Coincident(g10,g11)
    c: Distance(g10) = 1.23908
    c: Distance(g8) = 5.57001
    c: DistanceX(g9,g9) = 4.86999
    c: Coincident(g12,g11)
    c: Horizontal(g12)
    c: Coincident(g13,g12)
    c: Coincident(g13,g14)
    c: Coincident(g14,g15)
    c: Coincident(g16,g17)
    c: Coincident(g17,g18)
    c: Vertical(g18)
    c: Coincident(g19,g18)
    c: Coincident(g20,g19)
    c: Coincident(g21,g20)
    c: Vertical(g21)
    c: Coincident(g21,g22)
    c: Vertical(g22)
    c: Coincident(g22,g23)
    c: Coincident(g23,g24)
    c: Coincident(g24,g25)
    c: Coincident(g27,g26)
    c: Coincident(g28,g27)
    c: Horizontal(g28)
    c: DistanceX(g28,g28) = 5.37372
    c: Distance(g26) = 4.46542
    c: Distance(g27) = 3.86749
    c: Coincident(g29,g28)
    c: DistanceY(g7,g7) = 12
    c: DistanceY(g5,g5) = 10.4
    c: Distance(g4) = 5.3
    c: Distance(g3) = 5.60673
    c: Distance(g1) = 36.0023
    c: Distance(g15) = 2.41133
    c: Distance(g14) = 2.80018
    c: Distance(g13) = 2.07357
    c: DistanceX(g12,g12) = 6.85172
    c: Distance(g16) = 19.7388
    c: Distance(g17) = 23.3379
    c: DistanceY(g18,g18) = 12
    c: DistanceY(g21,g21) = 1.6
    c: DistanceY(g22,g22) = 4
    c: Distance(g23) = 2.8019
    c: Distance(g24) = 3.63982
    c: Distance(g25) = 4.89246
    c: Angle(g23,g22) = 2.81082
    c: Angle(g24,g22) = 2.52188
    c: Angle(g25,g22) = 2.26951
    c: Angle(g18,g19) = 2.50404
    c: Angle(g17,g18) = 2.81442
    c: Coincident(g30,g29)
    c: Coincident(g31,g30)
    c: Horizontal(g31)
    c: Coincident(g32,g31)
    c: Coincident(g32,g25)
    c: Distance(g30) = 30.6334
    c: Angle(g30,g28) = 0.110874
    c: DistanceX(g31,g31) = 130
    c: Distance(g32) = 127.367
    c: Coincident(g1,g33)
    c: Horizontal(g33)
    c: Coincident(g33,g34)
    c: Coincident(g35,g34)
    c: Coincident(g35,g8)
    c: Distance(g35) = 2.4804
    c: Angle(g13,g12) = 2.49901
    c: Angle(g14,g12) = 2.36124
    c: Angle(g15,g12) = 2.24748
    c: Angle(g34,g35) = 2.11973
    c: Angle(g34,g8) = 2.04062
    c: Angle(g34,g9) = 1.58195
    c: Angle(g9,g10) = 3.03808
    c: Angle(g31,g32) = 2.59833
    c: Coincident(g16,g36)
    c: Coincident(g36,g37)
    c: Coincident(g37,g38)
    c: Coincident(g38,g39)
    c: Coincident(g39,g40)
    c: Coincident(g40,g41)
    c: Coincident(g41,g42)
    c: Vertical(g42)
    c: Coincident(g42,g43)
    c: Coincident(g43,g44)
    c: Coincident(g45,g15)
    c: Distance(g36) = 12.5968
    c: Distance(g37) = 35.4072
    c: Distance(g38) = 3.49857
    c: Distance(g39) = 6.65282
    c: Distance(g40) = 4.97393
    c: Distance(g41) = 4.23793
    c: DistanceY(g42,g42) = 137.8
    c: Angle(g16,g17) = 2.58706
    c: Angle(g36,g16) = 2.86681
    c: Angle(g36,g37) = 3.12214
    c: Angle(g37,g38) = 3.03493
    c: Angle(g38,g39) = 2.85409
    c: Angle(g39,g40) = 2.92535
    c: Angle(g40,g41) = 2.95164
    c: Angle(g42,g43) = 2.81984
    c: Angle(g42,g44) = 2.49809
    c: Angle(g33,g1) = 1.58154
    c: Distance(g34) = 10.9802
    c: Distance(g45) = 52.6666
    c: Distance(g44) = 5
    c: Distance(g43) = 4.42719
    c: Distance(g11) = 103.143
    c: Coincident(g44,g45)
    c: Coincident(g46,g26)
    c: Vertical(g46)
    c: Distance(g46) = 7.20003
    c: Angle(g46,g26) = 2.54737
    c: Coincident(g47,g48)
    c: Coincident(g48,g49)
    c: Coincident(g49,g50)
    c: Coincident(g50,g47)
    c: Horizontal(g47)
    c: Horizontal(g49)
    c: Vertical(g48)
    c: Vertical(g50)
    c: DistanceY(g48,g48) = 602
    c: DistanceX(g49,g49) = 452
    c: Vertical(g51)
    c: Coincident(g52,g7)
    c: Coincident(g52,g46)
    c: Angle(g27,g28) = 2.1529
    c: Angle(g4,g5) = 2.58482
    c: Angle(g3,g5) = 2.40074
    c: Distance(g2) = 108.304
    c: Angle(g2,g5) = 2.03453
    c: Angle(g28,g29) = 2.86965
    c: DistanceX(g33,g33) = 54.3011
    c: Angle(g21,g20) = 2.65067
    c: Distance(g20) = 178.589
    c: Distance(g19) = 3.36006
    c: Coincident(g53,g7)
    c: PointOnObject(g53,g17)
    c: Horizontal(g53)
    c: DistanceX(g53,g53) = 192.695
FEATURE [PartDesign::Pocket] Pocket090  label="Body Cutout003"
  BaseFeature = -> Pad015
  Direction = (0,0,-1)
  Length = 45
  Length2 = 5
  Profile = -> Sketch268
  ReferenceAxis = -> Sketch268 [N_Axis]
  Type = 0
FEATURE [Sketcher::SketchObject] Sketch279  label="Overall Guitar Dimensions003"
  FullyConstrained = false
  MapMode = 5
  Support = -> [XY_Plane207]
  sketch-geometry (11):
    g0: LineSegment StartX=255 StartY=1125 StartZ=0 EndX=500 EndY=1125 EndZ=0
    g1: LineSegment StartX=408.821 StartY=43.4656 StartZ=0 EndX=500 EndY=43.4656 EndZ=0
    g2: LineSegment StartX=500 StartY=43.4656 StartZ=0 EndX=500 EndY=1125 EndZ=0
    g3: LineSegment StartX=413.448 StartY=50.4 StartZ=0 EndX=413.448 EndY=40 EndZ=0
    g4: LineSegment StartX=44.2 StartY=144.6 StartZ=0 EndX=44.2 EndY=40 EndZ=0
    g5: LineSegment StartX=44.2 StartY=40 StartZ=0 EndX=413.448 EndY=40 EndZ=0
    g6: LineSegment StartX=52.6 StartY=529.8 StartZ=0 EndX=52.6 EndY=600 EndZ=0
    g7: LineSegment StartX=355.987 StartY=452.42 StartZ=0 EndX=355.987 EndY=600 EndZ=0
    g8: LineSegment StartX=355.987 StartY=600 StartZ=0 EndX=52.6 EndY=600 EndZ=0
    g9: LineSegment StartX=97.988 StartY=587.07 StartZ=0 EndX=430 EndY=587.07 EndZ=0
    g10: LineSegment StartX=430 StartY=587.07 StartZ=0 EndX=430 EndY=43.4656 EndZ=0
  constraints (23):
    c: Horizontal(g0)
    c: Horizontal(g1)
    c: Coincident(g2,g1)
    c: Coincident(g2,g0)
    c: Vertical(g2)
    c: DistanceY(g2,g2) = 1081.53
    c: Vertical(g3)
    c: Vertical(g4)
    c: Coincident(g5,g4)
    c: Coincident(g5,g3)
    c: Horizontal(g5)
    c: DistanceX(g5,g5) = 369.248
    c: Vertical(g6)
    c: Vertical(g7)
    c: Coincident(g8,g7)
    c: Coincident(g8,g6)
    c: Horizontal(g8)
    c: DistanceX(g8,g8) = 303.387
    c: Horizontal(g9)
    c: Coincident(g10,g9)
    c: PointOnObject(g10,g1)
    c: Vertical(g10)
    c: DistanceY(g10,g10) = 543.604
FEATURE [Sketcher::SketchObject] Sketch280
  FullyConstrained = false
  MapMode = 5
  Placement = pos=(0,0,7) rot=(0,0,1;0rad)
  Support = -> [Pocket090]
  sketch-geometry (4):
    g0: LineSegment StartX=290 StartY=161 StartZ=0 EndX=370 EndY=161 EndZ=0
    g1: LineSegment StartX=370 StartY=161 StartZ=0 EndX=370 EndY=81 EndZ=0
    g2: LineSegment StartX=370 StartY=81 StartZ=0 EndX=290 EndY=81 EndZ=0
    g3: LineSegment StartX=290 StartY=81 StartZ=0 EndX=290 EndY=161 EndZ=0
  constraints (10):
    c: Coincident(g0,g1)
    c: Coincident(g1,g2)
    c: Coincident(g2,g3)
    c: Coincident(g3,g0)
    c: Horizontal(g0)
    c: Horizontal(g2)
    c: Vertical(g1)
    c: Vertical(g3)
    c: DistanceX(g0,g0) = 80
    c: DistanceY(g1,g1) = 80
FEATURE [PartDesign::Pocket] Pocket091
  BaseFeature = -> Pocket089
  Direction = (0,0,-1)
  Length = 10
  Length2 = 5
  Profile = -> Sketch236
  ReferenceAxis = -> Sketch236 [N_Axis]
  Type = 0
FEATURE [PartDesign::Pocket] Pocket092
  BaseFeature = -> Pocket091
  Direction = (0,0,-1)
  Length = 10
  Length2 = 5
  Profile = -> Sketch238
  ReferenceAxis = -> Sketch238 [N_Axis]
  Type = 0
FEATURE [PartDesign::Pocket] Pocket093
  BaseFeature = -> Pocket092
  Direction = (0,0,-1)
  Length = 10
  Length2 = 5
  Profile = -> Sketch229
  ReferenceAxis = -> Sketch229 [N_Axis]
  Type = 0
FEATURE [PartDesign::Pocket] Pocket094
  BaseFeature = -> Pocket093
  Direction = (0,0,-1)
  Length = 10
  Length2 = 5
  Profile = -> Sketch228
  ReferenceAxis = -> Sketch228 [N_Axis]
  Type = 0
FEATURE [PartDesign::Pocket] Pocket095
  BaseFeature = -> Pocket094
  Direction = (0,0,-1)
  Length = 10
  Length2 = 5
  Profile = -> Sketch240
  ReferenceAxis = -> Sketch240 [N_Axis]
  Type = 0
FEATURE [PartDesign::Pocket] Pocket096
  BaseFeature = -> Pocket095
  Direction = (0,0,-1)
  Length = 10
  Length2 = 5
  Profile = -> Sketch242
  ReferenceAxis = -> Sketch242 [N_Axis]
  Type = 0
FEATURE [Sketcher::SketchObject] Sketch288  label="control pocket005"
  FullyConstrained = false
  MapMode = 5
  Placement = pos=(0,0,7) rot=(0,0,1;0rad)
  Support = -> [Pocket096]
  sketch-geometry (11):
    g0: LineSegment StartX=330 StartY=250 StartZ=0 EndX=353.532 EndY=180 EndZ=0
    g1: LineSegment StartX=353.532 StartY=180 StartZ=0 EndX=290 EndY=180 EndZ=0
    g2: LineSegment StartX=290 StartY=180 StartZ=0 EndX=290 EndY=250 EndZ=0
    g3: LineSegment StartX=330 StartY=250 StartZ=0 EndX=290 EndY=250 EndZ=0
    g4: Circle CenterX=302 CenterY=230 CenterZ=0 NormalX=0 NormalY=0 NormalZ=1 AngleXU=0 Radius=8.5
    g5: Circle CenterX=302 CenterY=200 CenterZ=0 NormalX=0 NormalY=0 NormalZ=1 AngleXU=0 Radius=8.5
    g6: LineSegment StartX=316.216 StartY=240.298 StartZ=0 EndX=326.216 EndY=240.298 EndZ=0
    g7: LineSegment StartX=326.216 StartY=240.298 StartZ=0 EndX=341.048 EndY=194.647 EndZ=0
    g8: LineSegment StartX=341.048 StartY=194.647 StartZ=0 EndX=330.587 EndY=191.248 EndZ=0
    g9: LineSegment StartX=326.216 StartY=240.298 StartZ=0 EndX=315.754 EndY=236.898 EndZ=0
    g10: LineSegment StartX=315.754 StartY=236.898 StartZ=0 EndX=330.587 EndY=191.248 EndZ=0
  constraints (25):
    c: Coincident(g1,g0)
    c: Horizontal(g1)
    c: Coincident(g2,g1)
    c: Vertical(g2)
    c: Coincident(g3,g0)
    c: Coincident(g3,g2)
    c: Horizontal(g3)
    c: Distance(g0) = 73.8495
    c: DistanceX(g3,g3) = 40
    c: DistanceX(g1,g1) = 63.5319
    c: Diameter(g4) = 17
    c: Diameter(g5) = 17
    c: Horizontal(g6)
    c: Coincident(g7,g6)
    c: DistanceX(g6,g6) = 10
    c: Angle(g6,g7) = 1.88496
    c: Distance(g7) = 48
    c: Coincident(g8,g7)
    c: Angle(g7,g8) = 1.5708
    c: Distance(g8) = 11
    c: Coincident(g9,g7)
    c: Angle(g9,g7) = 1.5708
    c: Coincident(g10,g9)
    c: Coincident(g10,g8)
    c: Distance(g9) = 11
FEATURE [PartDesign::Pocket] Pocket097
  BaseFeature = -> Pocket096
  Direction = (0,0,-1)
  Length = 10
  Length2 = 5
  Profile = -> Sketch288
  ReferenceAxis = -> Sketch288 [N_Axis]
  Type = 0
FEATURE [PartDesign::Fillet] Fillet048
  Base = -> Pocket097 [Edge251,Edge249,Edge246,Edge247,Edge231,Edge230,Edge235,Edge233,Edge211,Edge206,Edge221,Edge225]
  BaseFeature = -> Pocket097
  Radius = 6.35
  SupportTransform = false
  UseAllEdges = false
FEATURE [PartDesign::Fillet] Fillet049
  Base = -> Fillet048 [Edge226,Edge227,Edge231,Edge229,Edge253,Edge255,Edge251,Edge250]
  BaseFeature = -> Fillet048
  Radius = 6
  SupportTransform = false
  UseAllEdges = false
FEATURE [PartDesign::Fillet] Fillet050
  Base = -> Fillet049 [Edge161,Edge157]
  BaseFeature = -> Fillet049
  Radius = 6.35
  SupportTransform = false
  UseAllEdges = false
FEATURE [PartDesign::Fillet] Fillet051
  Base = -> Fillet050 [Edge256,Edge257,Edge259,Edge261]
  BaseFeature = -> Fillet050
  Radius = 6
  SupportTransform = false
  UseAllEdges = false
FEATURE [PartDesign::Body] Body027  label="Jig 1 Body"
  Group = -> [Sketch227,Sketch228,Sketch229,Sketch236,Pad014,Sketch237,Sketch238,Sketch240,Sketch242,Pocket089,Pocket091,Pocket092,Pocket093,Pocket094,Pocket095,Pocket096,Sketch288,Pocket097,Fillet048,Fillet049,Fillet050,Fillet051]
  Origin = -> Origin206
  Tip = -> Fillet051
FEATURE [App::Part] Part046  label="Jig 1"
  Group = -> [Body027]
  Origin = -> Origin203
  Placement = pos=(0,0,235.6) rot=(0,0,1;0rad)
FEATURE [Sketcher::SketchObject] Sketch289  label="blank template005"
  FullyConstrained = false
  MapMode = 5
  Support = -> [XY_Plane209]
  sketch-geometry (4):
    g0: LineSegment StartX=0 StartY=615 StartZ=0 EndX=450 EndY=615 EndZ=0
    g1: LineSegment StartX=450 StartY=615 StartZ=0 EndX=450 EndY=15 EndZ=0
    g2: LineSegment StartX=450 StartY=15 StartZ=0 EndX=0 EndY=15 EndZ=0
    g3: LineSegment StartX=0 StartY=15 StartZ=0 EndX=0 EndY=615 EndZ=0
  constraints (10):
    c: Coincident(g0,g1)
    c: Coincident(g1,g2)
    c: Coincident(g2,g3)
    c: Coincident(g3,g0)
    c: Horizontal(g0)
    c: Horizontal(g2)
    c: Vertical(g1)
    c: Vertical(g3)
    c: DistanceX(g2,g2) = 450
    c: DistanceY(g1,g1) = 600
FEATURE [PartDesign::Pad] Pad016  label="Template 600x454"
  Direction = (0,0,1)
  Length = 7
  Length2 = 10
  Profile = -> Sketch289
  ReferenceAxis = -> Sketch289 [N_Axis]
  Type = 0
FEATURE [Sketcher::SketchObject] Sketch296  label="Speaker hole005"
  FullyConstrained = false
  MapMode = 5
  Placement = pos=(0,0,7) rot=(0,0,1;0rad)
  Support = -> [Pad016]
  sketch-geometry (3):
    g0: Circle CenterX=330 CenterY=121 CenterZ=0 NormalX=0 NormalY=0 NormalZ=1 AngleXU=0 Radius=37
    g1: LineSegment StartX=377 StartY=123.392 StartZ=0 EndX=283 EndY=123.392 EndZ=0
    g2: LineSegment StartX=377 StartY=123.4 StartZ=0 EndX=330 EndY=123.4 EndZ=0
  constraints (4):
    c: Diameter(g0) = 74
    c: Horizontal(g1)
    c: DistanceX(g1,g1) = 94
    c: Horizontal(g2)
FEATURE [Sketcher::SketchObject] Sketch299  label="Body Outline008"
  FullyConstrained = false
  MapMode = 5
  Placement = pos=(0,0,7) rot=(0,0,1;0rad)
  Support = -> [Pad016]
  sketch-geometry (54):
    g0: LineSegment StartX=197.29 StartY=495.3 StartZ=0 EndX=73.9 EndY=550.1 EndZ=0
    g1: LineSegment StartX=252.15 StartY=545.5 StartZ=0 EndX=252.536 EndY=509.5 EndZ=0
    g2: LineSegment StartX=252.536 StartY=509.5 StartZ=0 EndX=349.402 EndY=461.057 EndZ=0
    g3: LineSegment StartX=349.402 StartY=461.057 StartZ=0 EndX=353.186 EndY=456.92 EndZ=0
    g4: LineSegment StartX=353.186 StartY=456.92 StartZ=0 EndX=355.987 EndY=452.42 EndZ=0
    g5: LineSegment StartX=355.987 StartY=452.42 StartZ=0 EndX=355.987 EndY=442.02 EndZ=0
    g6: LineSegment StartX=355.987 StartY=442.02 StartZ=0 EndX=320 EndY=343.5 EndZ=0
    g7: LineSegment StartX=320 StartY=343.5 StartZ=0 EndX=320 EndY=331.5 EndZ=0
    g8: LineSegment StartX=195.596 StartY=533.25 StartZ=0 EndX=190.601 EndY=530.784 EndZ=0
    g9: LineSegment StartX=190.601 StartY=530.784 StartZ=0 EndX=185.731 EndY=530.784 EndZ=0
    g10: LineSegment StartX=185.731 StartY=530.784 StartZ=0 EndX=184.499 EndY=530.912 EndZ=0
    g11: LineSegment StartX=184.499 StartY=530.912 StartZ=0 EndX=97.9865 EndY=587.073 EndZ=0
    g12: LineSegment StartX=97.9865 StartY=587.073 StartZ=0 EndX=91.1348 EndY=587.073 EndZ=0
    g13: LineSegment StartX=91.1348 StartY=587.073 StartZ=0 EndX=89.4748 EndY=585.83 EndZ=0
    g14: LineSegment StartX=89.4748 StartY=585.83 StartZ=0 EndX=87.4848 EndY=583.86 EndZ=0
    g15: LineSegment StartX=87.4848 StartY=583.86 StartZ=0 EndX=85.9748 EndY=581.98 EndZ=0
    g16: LineSegment StartX=107.659 StartY=357.048 StartZ=0 EndX=122.894 EndY=344.497 EndZ=0
    g17: LineSegment StartX=122.894 StartY=344.497 StartZ=0 EndX=130.394 EndY=322.397 EndZ=0
    g18: LineSegment StartX=130.394 StartY=322.397 StartZ=0 EndX=130.394 EndY=310.397 EndZ=0
    g19: LineSegment StartX=130.394 StartY=310.397 StartZ=0 EndX=128.394 EndY=307.697 EndZ=0
    g20: LineSegment StartX=128.394 StartY=307.697 StartZ=0 EndX=44.2002 EndY=150.2 EndZ=0
    g21: LineSegment StartX=44.2002 StartY=150.2 StartZ=0 EndX=44.2002 EndY=148.6 EndZ=0
    g22: LineSegment StartX=44.2002 StartY=148.6 StartZ=0 EndX=44.2002 EndY=144.6 EndZ=0
    g23: LineSegment StartX=44.2002 StartY=144.6 StartZ=0 EndX=45.1102 EndY=141.95 EndZ=0
    g24: LineSegment StartX=45.1102 StartY=141.95 StartZ=0 EndX=47.2242 EndY=138.987 EndZ=0
    g25: LineSegment StartX=47.2242 StartY=138.987 StartZ=0 EndX=50.9702 EndY=135.84 EndZ=0
    g26: LineSegment StartX=413.447 StartY=50.3962 StartZ=0 EndX=410.947 EndY=46.6962 EndZ=0
    g27: LineSegment StartX=410.947 StartY=46.6962 StartZ=0 EndX=408.821 EndY=43.4657 EndZ=0
    g28: LineSegment StartX=408.821 StartY=43.4657 StartZ=0 EndX=403.447 EndY=43.4657 EndZ=0
    g29: LineSegment StartX=403.447 StartY=43.4657 StartZ=0 EndX=320.445 EndY=66.6106 EndZ=0
    g30: LineSegment StartX=320.445 StartY=66.6106 StartZ=0 EndX=290 EndY=70.0001 EndZ=0
    g31: LineSegment StartX=290 StartY=70.0001 StartZ=0 EndX=160 EndY=70.0001 EndZ=0
    g32: LineSegment StartX=160 StartY=70.0001 StartZ=0 EndX=50.9702 EndY=135.84 EndZ=0
    g33: LineSegment StartX=252.15 StartY=545.5 StartZ=0 EndX=197.848 EndY=545.5 EndZ=0
    g34: LineSegment StartX=197.848 StartY=545.5 StartZ=0 EndX=197.726 EndY=534.521 EndZ=0
    g35: LineSegment StartX=197.726 StartY=534.521 StartZ=0 EndX=195.596 EndY=533.25 EndZ=0
    g36: LineSegment StartX=107.659 StartY=357.048 StartZ=0 EndX=96.1282 EndY=362.119 EndZ=0
    g37: LineSegment StartX=96.1282 StartY=362.119 StartZ=0 EndX=64 EndY=377 EndZ=0
    g38: LineSegment StartX=64 StartY=377 StartZ=0 EndX=61 EndY=378.8 EndZ=0
    g39: LineSegment StartX=61 StartY=378.8 StartZ=0 EndX=56.5 EndY=383.7 EndZ=0
    g40: LineSegment StartX=56.5 StartY=383.7 StartZ=0 EndX=54 EndY=388 EndZ=0
    g41: LineSegment StartX=54 StartY=388 StartZ=0 EndX=52.6 EndY=392 EndZ=0
    g42: LineSegment StartX=52.6 StartY=392 StartZ=0 EndX=52.6 EndY=529.8 EndZ=0
    g43: LineSegment StartX=52.6 StartY=529.8 StartZ=0 EndX=54 EndY=534 EndZ=0
    g44: LineSegment StartX=54 StartY=534 StartZ=0 EndX=57 EndY=538 EndZ=0
    g45: LineSegment StartX=57 StartY=538 StartZ=0 EndX=85.9748 EndY=581.98 EndZ=0
    g46: LineSegment StartX=413.447 StartY=50.3962 StartZ=0 EndX=413.447 EndY=57.5962 EndZ=0
    g47: LineSegment StartX=-1 StartY=616 StartZ=0 EndX=451 EndY=616 EndZ=0
    g48: LineSegment StartX=451 StartY=616 StartZ=0 EndX=451 EndY=14 EndZ=0
    g49: LineSegment StartX=451 StartY=14 StartZ=0 EndX=-1 EndY=14 EndZ=0
    g50: LineSegment StartX=-1 StartY=14 StartZ=0 EndX=-1 EndY=616 EndZ=0
    g51: LineSegment StartX=257 StartY=545.5 StartZ=0 EndX=257 EndY=245.424 EndZ=0
    g52: LineSegment StartX=320 StartY=331.5 StartZ=0 EndX=413.447 EndY=57.5962 EndZ=0
    g53: LineSegment StartX=320 StartY=331.5 StartZ=0 EndX=127.305 EndY=331.5 EndZ=0
  constraints (149):
    c: Coincident(g1,g2)
    c: Coincident(g2,g3)
    c: Coincident(g3,g4)
    c: Coincident(g4,g5)
    c: Vertical(g5)
    c: Coincident(g6,g5)
    c: Coincident(g7,g6)
    c: Vertical(g7)
    c: Coincident(g8,g9)
    c: Horizontal(g9)
    c: Coincident(g9,g10)
    c: Coincident(g10,g11)
    c: Distance(g10) = 1.23908
    c: Distance(g8) = 5.57001
    c: DistanceX(g9,g9) = 4.86999
    c: Coincident(g12,g11)
    c: Horizontal(g12)
    c: Coincident(g13,g12)
    c: Coincident(g13,g14)
    c: Coincident(g14,g15)
    c: Coincident(g16,g17)
    c: Coincident(g17,g18)
    c: Vertical(g18)
    c: Coincident(g19,g18)
    c: Coincident(g20,g19)
    c: Coincident(g21,g20)
    c: Vertical(g21)
    c: Coincident(g21,g22)
    c: Vertical(g22)
    c: Coincident(g22,g23)
    c: Coincident(g23,g24)
    c: Coincident(g24,g25)
    c: Coincident(g27,g26)
    c: Coincident(g28,g27)
    c: Horizontal(g28)
    c: DistanceX(g28,g28) = 5.37372
    c: Distance(g26) = 4.46542
    c: Distance(g27) = 3.86749
    c: Coincident(g29,g28)
    c: DistanceY(g7,g7) = 12
    c: DistanceY(g5,g5) = 10.4
    c: Distance(g4) = 5.3
    c: Distance(g3) = 5.60673
    c: Distance(g1) = 36.0023
    c: Distance(g15) = 2.41133
    c: Distance(g14) = 2.80018
    c: Distance(g13) = 2.07357
    c: DistanceX(g12,g12) = 6.85172
    c: Distance(g16) = 19.7388
    c: Distance(g17) = 23.3379
    c: DistanceY(g18,g18) = 12
    c: DistanceY(g21,g21) = 1.6
    c: DistanceY(g22,g22) = 4
    c: Distance(g23) = 2.8019
    c: Distance(g24) = 3.63982
    c: Distance(g25) = 4.89246
    c: Angle(g23,g22) = 2.81082
    c: Angle(g24,g22) = 2.52188
    c: Angle(g25,g22) = 2.26951
    c: Angle(g18,g19) = 2.50404
    c: Angle(g17,g18) = 2.81442
    c: Coincident(g30,g29)
    c: Coincident(g31,g30)
    c: Horizontal(g31)
    c: Coincident(g32,g31)
    c: Coincident(g32,g25)
    c: Distance(g30) = 30.6334
    c: Angle(g30,g28) = 0.110874
    c: DistanceX(g31,g31) = 130
    c: Distance(g32) = 127.367
    c: Coincident(g1,g33)
    c: Horizontal(g33)
    c: Coincident(g33,g34)
    c: Coincident(g35,g34)
    c: Coincident(g35,g8)
    c: Distance(g35) = 2.4804
    c: Angle(g13,g12) = 2.49901
    c: Angle(g14,g12) = 2.36124
    c: Angle(g15,g12) = 2.24748
    c: Angle(g34,g35) = 2.11973
    c: Angle(g34,g8) = 2.04062
    c: Angle(g34,g9) = 1.58195
    c: Angle(g9,g10) = 3.03808
    c: Angle(g31,g32) = 2.59833
    c: Coincident(g16,g36)
    c: Coincident(g36,g37)
    c: Coincident(g37,g38)
    c: Coincident(g38,g39)
    c: Coincident(g39,g40)
    c: Coincident(g40,g41)
    c: Coincident(g41,g42)
    c: Vertical(g42)
    c: Coincident(g42,g43)
    c: Coincident(g43,g44)
    c: Coincident(g45,g15)
    c: Distance(g36) = 12.5968
    c: Distance(g37) = 35.4072
    c: Distance(g38) = 3.49857
    c: Distance(g39) = 6.65282
    c: Distance(g40) = 4.97393
    c: Distance(g41) = 4.23793
    c: DistanceY(g42,g42) = 137.8
    c: Angle(g16,g17) = 2.58706
    c: Angle(g36,g16) = 2.86681
    c: Angle(g36,g37) = 3.12214
    c: Angle(g37,g38) = 3.03493
    c: Angle(g38,g39) = 2.85409
    c: Angle(g39,g40) = 2.92535
    c: Angle(g40,g41) = 2.95164
    c: Angle(g42,g43) = 2.81984
    c: Angle(g42,g44) = 2.49809
    c: Angle(g33,g1) = 1.58154
    c: Distance(g34) = 10.9802
    c: Distance(g45) = 52.6666
    c: Distance(g44) = 5
    c: Distance(g43) = 4.42719
    c: Distance(g11) = 103.143
    c: Coincident(g44,g45)
    c: Coincident(g46,g26)
    c: Vertical(g46)
    c: Distance(g46) = 7.20003
    c: Angle(g46,g26) = 2.54737
    c: Coincident(g47,g48)
    c: Coincident(g48,g49)
    c: Coincident(g49,g50)
    c: Coincident(g50,g47)
    c: Horizontal(g47)
    c: Horizontal(g49)
    c: Vertical(g48)
    c: Vertical(g50)
    c: DistanceY(g48,g48) = 602
    c: DistanceX(g49,g49) = 452
    c: Vertical(g51)
    c: Coincident(g52,g7)
    c: Coincident(g52,g46)
    c: Angle(g27,g28) = 2.1529
    c: Angle(g4,g5) = 2.58482
    c: Angle(g3,g5) = 2.40074
    c: Distance(g2) = 108.304
    c: Angle(g2,g5) = 2.03453
    c: Angle(g28,g29) = 2.86965
    c: DistanceX(g33,g33) = 54.3011
    c: Angle(g21,g20) = 2.65067
    c: Distance(g20) = 178.589
    c: Distance(g19) = 3.36006
    c: Coincident(g53,g7)
    c: PointOnObject(g53,g17)
    c: Horizontal(g53)
    c: DistanceX(g53,g53) = 192.695
FEATURE [PartDesign::Pocket] Pocket098  label="Body Cutout004"
  BaseFeature = -> Pad016
  Direction = (0,0,-1)
  Length = 45
  Length2 = 5
  Profile = -> Sketch299
  ReferenceAxis = -> Sketch299 [N_Axis]
  Type = 0
FEATURE [Sketcher::SketchObject] Sketch304  label="Tremelo underside 004"
  FullyConstrained = false
  MapMode = 5
  Placement = pos=(0,0,0) rot=(1,0,0;3.14159rad)
  sketch-geometry (4):
    g0: LineSegment StartX=189.9 StartY=-261.3 StartZ=0 EndX=267.9 EndY=-261.3 EndZ=0
    g1: LineSegment StartX=267.9 StartY=-261.3 StartZ=0 EndX=267.9 EndY=-287.3 EndZ=0
    g2: LineSegment StartX=267.9 StartY=-287.3 StartZ=0 EndX=189.9 EndY=-287.3 EndZ=0
    g3: LineSegment StartX=189.9 StartY=-287.3 StartZ=0 EndX=189.9 EndY=-261.3 EndZ=0
  constraints (10):
    c: Coincident(g0,g1)
    c: Coincident(g1,g2)
    c: Coincident(g2,g3)
    c: Coincident(g3,g0)
    c: Horizontal(g0)
    c: Horizontal(g2)
    c: Vertical(g1)
    c: Vertical(g3)
    c: DistanceX(g0,g0) = 78
    c: DistanceY(g1,g1) = 26
FEATURE [Sketcher::SketchObject] Sketch310  label="Overall Guitar Dimensions004"
  FullyConstrained = false
  MapMode = 5
  Support = -> [XY_Plane209]
  sketch-geometry (11):
    g0: LineSegment StartX=255 StartY=1125 StartZ=0 EndX=500 EndY=1125 EndZ=0
    g1: LineSegment StartX=408.821 StartY=43.4656 StartZ=0 EndX=500 EndY=43.4656 EndZ=0
    g2: LineSegment StartX=500 StartY=43.4656 StartZ=0 EndX=500 EndY=1125 EndZ=0
    g3: LineSegment StartX=413.448 StartY=50.4 StartZ=0 EndX=413.448 EndY=40 EndZ=0
    g4: LineSegment StartX=44.2 StartY=144.6 StartZ=0 EndX=44.2 EndY=40 EndZ=0
    g5: LineSegment StartX=44.2 StartY=40 StartZ=0 EndX=413.448 EndY=40 EndZ=0
    g6: LineSegment StartX=52.6 StartY=529.8 StartZ=0 EndX=52.6 EndY=600 EndZ=0
    g7: LineSegment StartX=355.987 StartY=452.42 StartZ=0 EndX=355.987 EndY=600 EndZ=0
    g8: LineSegment StartX=355.987 StartY=600 StartZ=0 EndX=52.6 EndY=600 EndZ=0
    g9: LineSegment StartX=97.988 StartY=587.07 StartZ=0 EndX=430 EndY=587.07 EndZ=0
    g10: LineSegment StartX=430 StartY=587.07 StartZ=0 EndX=430 EndY=43.4656 EndZ=0
  constraints (23):
    c: Horizontal(g0)
    c: Horizontal(g1)
    c: Coincident(g2,g1)
    c: Coincident(g2,g0)
    c: Vertical(g2)
    c: DistanceY(g2,g2) = 1081.53
    c: Vertical(g3)
    c: Vertical(g4)
    c: Coincident(g5,g4)
    c: Coincident(g5,g3)
    c: Horizontal(g5)
    c: DistanceX(g5,g5) = 369.248
    c: Vertical(g6)
    c: Vertical(g7)
    c: Coincident(g8,g7)
    c: Coincident(g8,g6)
    c: Horizontal(g8)
    c: DistanceX(g8,g8) = 303.387
    c: Horizontal(g9)
    c: Coincident(g10,g9)
    c: PointOnObject(g10,g1)
    c: Vertical(g10)
    c: DistanceY(g10,g10) = 543.604
FEATURE [Sketcher::SketchObject] Sketch316
  FullyConstrained = false
  MapMode = 5
  Placement = pos=(0,0,0) rot=(1,0,0;3.14159rad)
  sketch-geometry (4):
    g0: LineSegment StartX=168.5 StartY=-70 StartZ=0 EndX=281.3 EndY=-70 EndZ=0
    g1: LineSegment StartX=281.3 StartY=-70 StartZ=0 EndX=281.3 EndY=-200 EndZ=0
    g2: LineSegment StartX=281.3 StartY=-200 StartZ=0 EndX=168.5 EndY=-200 EndZ=0
    g3: LineSegment StartX=168.5 StartY=-200 StartZ=0 EndX=168.5 EndY=-70 EndZ=0
  constraints (10):
    c: Coincident(g0,g1)
    c: Coincident(g1,g2)
    c: Coincident(g2,g3)
    c: Coincident(g3,g0)
    c: Horizontal(g0)
    c: Horizontal(g2)
    c: Vertical(g1)
    c: Vertical(g3)
    c: DistanceX(g0,g0) = 112.8
    c: DistanceY(g3,g3) = 130
FEATURE [PartDesign::Pocket] Pocket099
  BaseFeature = -> Pocket090
  Direction = (0,0,-1)
  Length = 10
  Length2 = 5
  Profile = -> Sketch262
  ReferenceAxis = -> Sketch262 [N_Axis]
  Type = 0
FEATURE [PartDesign::Pocket] Pocket100
  BaseFeature = -> Pocket099
  Direction = (0,0,-1)
  Length = 10
  Length2 = 5
  Profile = -> Sketch280
  ReferenceAxis = -> Sketch280 [N_Axis]
  Type = 0
FEATURE [PartDesign::Fillet] Fillet052
  Base = -> Pocket100 [Edge151,Edge154,Edge156,Edge152]
  BaseFeature = -> Pocket100
  Radius = 6
  SupportTransform = false
  UseAllEdges = false
FEATURE [PartDesign::Pocket] Pocket101
  BaseFeature = -> Fillet052
  Direction = (0,0,-1)
  Length = 10
  Length2 = 5
  Profile = -> Sketch266
  ReferenceAxis = -> Sketch266 [N_Axis]
  Type = 0
FEATURE [PartDesign::Fillet] Fillet053
  Base = -> Pocket101 [Edge178,Edge180,Edge176,Edge175]
  BaseFeature = -> Pocket101
  Radius = 6
  SupportTransform = false
  UseAllEdges = false
FEATURE [PartDesign::Pocket] Pocket102
  BaseFeature = -> Fillet053
  Direction = (0,0,-1)
  Length = 10
  Length2 = 5
  Profile = -> Sketch264
  ReferenceAxis = -> Sketch264 [N_Axis]
  Type = 0
FEATURE [PartDesign::Fillet] Fillet054
  Base = -> Pocket102 [Edge207,Edge208,Edge210,Edge212]
  BaseFeature = -> Pocket102
  Radius = 3.35
  SupportTransform = false
  UseAllEdges = false
FEATURE [Sketcher::SketchObject] Sketch281
  FullyConstrained = false
  MapMode = 5
  Placement = pos=(0,0,7) rot=(0,0,1;0rad)
  Support = -> [Fillet054]
  sketch-geometry (24):
    g0: LineSegment StartX=253.5 StartY=460 StartZ=0 EndX=267.5 EndY=460 EndZ=0
    g1: LineSegment StartX=267.5 StartY=460 StartZ=0 EndX=267.5 EndY=441 EndZ=0
    g2: LineSegment StartX=267.5 StartY=441 StartZ=0 EndX=253.5 EndY=441 EndZ=0
    g3: LineSegment StartX=253.5 StartY=441 StartZ=0 EndX=253.5 EndY=460 EndZ=0
    g4: LineSegment StartX=196.5 StartY=441 StartZ=0 EndX=182.5 EndY=441 EndZ=0
    g5: LineSegment StartX=182.5 StartY=441 StartZ=0 EndX=182.5 EndY=460 EndZ=0
    g6: LineSegment StartX=182.5 StartY=460 StartZ=0 EndX=196.5 EndY=460 EndZ=0
    g7: LineSegment StartX=196.5 StartY=460 StartZ=0 EndX=196.5 EndY=441 EndZ=0
    g8: LineSegment StartX=196.5 StartY=400 StartZ=0 EndX=182.5 EndY=400 EndZ=0
    g9: LineSegment StartX=182.5 StartY=400 StartZ=0 EndX=182.5 EndY=381 EndZ=0
    g10: LineSegment StartX=182.5 StartY=381 StartZ=0 EndX=196.5 EndY=381 EndZ=0
    g11: LineSegment StartX=196.5 StartY=381 StartZ=0 EndX=196.5 EndY=400 EndZ=0
    g12: LineSegment StartX=253.5 StartY=400 StartZ=0 EndX=267.5 EndY=400 EndZ=0
    g13: LineSegment StartX=267.5 StartY=400 StartZ=0 EndX=267.5 EndY=381 EndZ=0
    g14: LineSegment StartX=267.5 StartY=381 StartZ=0 EndX=253.5 EndY=381 EndZ=0
    g15: LineSegment StartX=253.5 StartY=381 StartZ=0 EndX=253.5 EndY=400 EndZ=0
    g16: LineSegment StartX=180.75 StartY=347.8 StartZ=0 EndX=194.75 EndY=347.8 EndZ=0
    g17: LineSegment StartX=194.75 StartY=347.8 StartZ=0 EndX=194.75 EndY=327.8 EndZ=0
    g18: LineSegment StartX=194.75 StartY=327.8 StartZ=0 EndX=180.75 EndY=327.8 EndZ=0
    g19: LineSegment StartX=180.75 StartY=327.8 StartZ=0 EndX=180.75 EndY=347.8 EndZ=0
    g20: LineSegment StartX=255.25 StartY=347.8 StartZ=0 EndX=269.25 EndY=347.8 EndZ=0
    g21: LineSegment StartX=269.25 StartY=347.8 StartZ=0 EndX=269.25 EndY=327.8 EndZ=0
    g22: LineSegment StartX=269.25 StartY=327.8 StartZ=0 EndX=255.25 EndY=327.8 EndZ=0
    g23: LineSegment StartX=255.25 StartY=327.8 StartZ=0 EndX=255.25 EndY=347.8 EndZ=0
  constraints (60):
    c: Coincident(g0,g1)
    c: Coincident(g1,g2)
    c: Coincident(g2,g3)
    c: Coincident(g3,g0)
    c: Horizontal(g0)
    c: Horizontal(g2)
    c: Vertical(g1)
    c: Vertical(g3)
    c: DistanceX(g0,g0) = 14
    c: Coincident(g4,g5)
    c: Coincident(g5,g6)
    c: Coincident(g6,g7)
    c: Coincident(g7,g4)
    c: Horizontal(g4)
    c: Horizontal(g6)
    c: Vertical(g5)
    c: Vertical(g7)
    c: DistanceX(g4,g4) = 14
    c: DistanceY(g7,g7) = 19
    c: DistanceY(g3,g3) = 19
    c: Coincident(g8,g9)
    c: Coincident(g9,g10)
    c: Coincident(g10,g11)
    c: Coincident(g11,g8)
    c: Horizontal(g8)
    c: Horizontal(g10)
    c: Vertical(g9)
    c: Vertical(g11)
    c: DistanceX(g8,g8) = 14
    c: DistanceY(g11,g11) = 19
    c: Coincident(g12,g13)
    c: Coincident(g13,g14)
    c: Coincident(g14,g15)
    c: Coincident(g15,g12)
    c: Horizontal(g12)
    c: Horizontal(g14)
    c: Vertical(g13)
    c: Vertical(g15)
    c: DistanceX(g12,g12) = 14
    c: DistanceY(g15,g15) = 19
    c: Coincident(g16,g17)
    c: Coincident(g17,g18)
    c: Coincident(g18,g19)
    c: Coincident(g19,g16)
    c: Horizontal(g16)
    c: Horizontal(g18)
    c: Vertical(g17)
    c: Vertical(g19)
    c: DistanceX(g16,g16) = 14
    c: DistanceY(g17,g17) = 20
    c: Coincident(g20,g21)
    c: Coincident(g21,g22)
    c: Coincident(g22,g23)
    c: Coincident(g23,g20)
    c: Horizontal(g20)
    c: Horizontal(g22)
    c: Vertical(g21)
    c: Vertical(g23)
    c: DistanceX(g22,g22) = 14
    c: DistanceY(g23,g23) = 20
FEATURE [PartDesign::Pocket] Pocket103
  BaseFeature = -> Fillet054
  Direction = (0,0,-1)
  Length = 10
  Length2 = 5
  Profile = -> Sketch281
  ReferenceAxis = -> Sketch281 [N_Axis]
  Type = 0
FEATURE [PartDesign::Fillet] Fillet055
  Base = -> Pocket103 [Edge260,Edge262,Edge264,Edge259,Edge228,Edge238,Edge256,Edge235,Edge227,Edge254,Edge267,Edge291,Edge268,Edge292,Edge294,Edge270,Edge251,Edge240,Edge230,Edge232,Edge236,Edge272,Edge296,Edge252]
  BaseFeature = -> Pocket103
  Radius = 6.35
  SupportTransform = false
  UseAllEdges = false
FEATURE [PartDesign::Body] Body028  label="Jig 2 Body"
  Group = -> [Sketch258,Sketch262,Sketch264,Sketch266,Pad015,Sketch268,Pocket090,Sketch279,Sketch280,Sketch281,Pocket099,Pocket100,Fillet052,Pocket101,Fillet053,Pocket102,Fillet054,Pocket103,Fillet055]
  Origin = -> Origin207
  Tip = -> Fillet055
FEATURE [App::Part] Part047  label="Jig 2"
  Group = -> [Body028]
  Origin = -> Origin204
  Placement = pos=(0,0,167.8) rot=(0,0,1;0rad)
FEATURE [Sketcher::SketchObject] Sketch319  label="blank template006"
  FullyConstrained = false
  MapMode = 5
  Support = -> [XY_Plane211]
  sketch-geometry (4):
    g0: LineSegment StartX=0 StartY=615 StartZ=0 EndX=450 EndY=615 EndZ=0
    g1: LineSegment StartX=450 StartY=615 StartZ=0 EndX=450 EndY=15 EndZ=0
    g2: LineSegment StartX=450 StartY=15 StartZ=0 EndX=0 EndY=15 EndZ=0
    g3: LineSegment StartX=0 StartY=15 StartZ=0 EndX=0 EndY=615 EndZ=0
  constraints (10):
    c: Coincident(g0,g1)
    c: Coincident(g1,g2)
    c: Coincident(g2,g3)
    c: Coincident(g3,g0)
    c: Horizontal(g0)
    c: Horizontal(g2)
    c: Vertical(g1)
    c: Vertical(g3)
    c: DistanceX(g2,g2) = 450
    c: DistanceY(g1,g1) = 600
FEATURE [PartDesign::Pad] Pad017  label="Template 600x455"
  Direction = (0,0,1)
  Length = 7
  Length2 = 10
  Profile = -> Sketch319
  ReferenceAxis = -> Sketch319 [N_Axis]
  Type = 0
FEATURE [Sketcher::SketchObject] Sketch329  label="Body Outline009"
  FullyConstrained = false
  MapMode = 5
  Placement = pos=(0,0,7) rot=(0,0,1;0rad)
  Support = -> [Pad017]
  sketch-geometry (54):
    g0: LineSegment StartX=197.29 StartY=495.3 StartZ=0 EndX=73.9 EndY=550.1 EndZ=0
    g1: LineSegment StartX=252.15 StartY=545.5 StartZ=0 EndX=252.536 EndY=509.5 EndZ=0
    g2: LineSegment StartX=252.536 StartY=509.5 StartZ=0 EndX=349.402 EndY=461.057 EndZ=0
    g3: LineSegment StartX=349.402 StartY=461.057 StartZ=0 EndX=353.186 EndY=456.92 EndZ=0
    g4: LineSegment StartX=353.186 StartY=456.92 StartZ=0 EndX=355.987 EndY=452.42 EndZ=0
    g5: LineSegment StartX=355.987 StartY=452.42 StartZ=0 EndX=355.987 EndY=442.02 EndZ=0
    g6: LineSegment StartX=355.987 StartY=442.02 StartZ=0 EndX=320 EndY=343.5 EndZ=0
    g7: LineSegment StartX=320 StartY=343.5 StartZ=0 EndX=320 EndY=331.5 EndZ=0
    g8: LineSegment StartX=195.596 StartY=533.25 StartZ=0 EndX=190.601 EndY=530.784 EndZ=0
    g9: LineSegment StartX=190.601 StartY=530.784 StartZ=0 EndX=185.731 EndY=530.784 EndZ=0
    g10: LineSegment StartX=185.731 StartY=530.784 StartZ=0 EndX=184.499 EndY=530.912 EndZ=0
    g11: LineSegment StartX=184.499 StartY=530.912 StartZ=0 EndX=97.9865 EndY=587.073 EndZ=0
    g12: LineSegment StartX=97.9865 StartY=587.073 StartZ=0 EndX=91.1348 EndY=587.073 EndZ=0
    g13: LineSegment StartX=91.1348 StartY=587.073 StartZ=0 EndX=89.4748 EndY=585.83 EndZ=0
    g14: LineSegment StartX=89.4748 StartY=585.83 StartZ=0 EndX=87.4848 EndY=583.86 EndZ=0
    g15: LineSegment StartX=87.4848 StartY=583.86 StartZ=0 EndX=85.9748 EndY=581.98 EndZ=0
    g16: LineSegment StartX=107.659 StartY=357.048 StartZ=0 EndX=122.894 EndY=344.497 EndZ=0
    g17: LineSegment StartX=122.894 StartY=344.497 StartZ=0 EndX=130.394 EndY=322.397 EndZ=0
    g18: LineSegment StartX=130.394 StartY=322.397 StartZ=0 EndX=130.394 EndY=310.397 EndZ=0
    g19: LineSegment StartX=130.394 StartY=310.397 StartZ=0 EndX=128.394 EndY=307.697 EndZ=0
    g20: LineSegment StartX=128.394 StartY=307.697 StartZ=0 EndX=44.2002 EndY=150.2 EndZ=0
    g21: LineSegment StartX=44.2002 StartY=150.2 StartZ=0 EndX=44.2002 EndY=148.6 EndZ=0
    g22: LineSegment StartX=44.2002 StartY=148.6 StartZ=0 EndX=44.2002 EndY=144.6 EndZ=0
    g23: LineSegment StartX=44.2002 StartY=144.6 StartZ=0 EndX=45.1102 EndY=141.95 EndZ=0
    g24: LineSegment StartX=45.1102 StartY=141.95 StartZ=0 EndX=47.2242 EndY=138.987 EndZ=0
    g25: LineSegment StartX=47.2242 StartY=138.987 StartZ=0 EndX=50.9702 EndY=135.84 EndZ=0
    g26: LineSegment StartX=413.447 StartY=50.3962 StartZ=0 EndX=410.947 EndY=46.6962 EndZ=0
    g27: LineSegment StartX=410.947 StartY=46.6962 StartZ=0 EndX=408.821 EndY=43.4657 EndZ=0
    g28: LineSegment StartX=408.821 StartY=43.4657 StartZ=0 EndX=403.447 EndY=43.4657 EndZ=0
    g29: LineSegment StartX=403.447 StartY=43.4657 StartZ=0 EndX=320.445 EndY=66.6106 EndZ=0
    g30: LineSegment StartX=320.445 StartY=66.6106 StartZ=0 EndX=290 EndY=70.0001 EndZ=0
    g31: LineSegment StartX=290 StartY=70.0001 StartZ=0 EndX=160 EndY=70.0001 EndZ=0
    g32: LineSegment StartX=160 StartY=70.0001 StartZ=0 EndX=50.9702 EndY=135.84 EndZ=0
    g33: LineSegment StartX=252.15 StartY=545.5 StartZ=0 EndX=197.848 EndY=545.5 EndZ=0
    g34: LineSegment StartX=197.848 StartY=545.5 StartZ=0 EndX=197.726 EndY=534.521 EndZ=0
    g35: LineSegment StartX=197.726 StartY=534.521 StartZ=0 EndX=195.596 EndY=533.25 EndZ=0
    g36: LineSegment StartX=107.659 StartY=357.048 StartZ=0 EndX=96.1282 EndY=362.119 EndZ=0
    g37: LineSegment StartX=96.1282 StartY=362.119 StartZ=0 EndX=64 EndY=377 EndZ=0
    g38: LineSegment StartX=64 StartY=377 StartZ=0 EndX=61 EndY=378.8 EndZ=0
    g39: LineSegment StartX=61 StartY=378.8 StartZ=0 EndX=56.5 EndY=383.7 EndZ=0
    g40: LineSegment StartX=56.5 StartY=383.7 StartZ=0 EndX=54 EndY=388 EndZ=0
    g41: LineSegment StartX=54 StartY=388 StartZ=0 EndX=52.6 EndY=392 EndZ=0
    g42: LineSegment StartX=52.6 StartY=392 StartZ=0 EndX=52.6 EndY=529.8 EndZ=0
    g43: LineSegment StartX=52.6 StartY=529.8 StartZ=0 EndX=54 EndY=534 EndZ=0
    g44: LineSegment StartX=54 StartY=534 StartZ=0 EndX=57 EndY=538 EndZ=0
    g45: LineSegment StartX=57 StartY=538 StartZ=0 EndX=85.9748 EndY=581.98 EndZ=0
    g46: LineSegment StartX=413.447 StartY=50.3962 StartZ=0 EndX=413.447 EndY=57.5962 EndZ=0
    g47: LineSegment StartX=-1 StartY=616 StartZ=0 EndX=451 EndY=616 EndZ=0
    g48: LineSegment StartX=451 StartY=616 StartZ=0 EndX=451 EndY=14 EndZ=0
    g49: LineSegment StartX=451 StartY=14 StartZ=0 EndX=-1 EndY=14 EndZ=0
    g50: LineSegment StartX=-1 StartY=14 StartZ=0 EndX=-1 EndY=616 EndZ=0
    g51: LineSegment StartX=257 StartY=545.5 StartZ=0 EndX=257 EndY=245.424 EndZ=0
    g52: LineSegment StartX=320 StartY=331.5 StartZ=0 EndX=413.447 EndY=57.5962 EndZ=0
    g53: LineSegment StartX=320 StartY=331.5 StartZ=0 EndX=127.305 EndY=331.5 EndZ=0
  constraints (149):
    c: Coincident(g1,g2)
    c: Coincident(g2,g3)
    c: Coincident(g3,g4)
    c: Coincident(g4,g5)
    c: Vertical(g5)
    c: Coincident(g6,g5)
    c: Coincident(g7,g6)
    c: Vertical(g7)
    c: Coincident(g8,g9)
    c: Horizontal(g9)
    c: Coincident(g9,g10)
    c: Coincident(g10,g11)
    c: Distance(g10) = 1.23908
    c: Distance(g8) = 5.57001
    c: DistanceX(g9,g9) = 4.86999
    c: Coincident(g12,g11)
    c: Horizontal(g12)
    c: Coincident(g13,g12)
    c: Coincident(g13,g14)
    c: Coincident(g14,g15)
    c: Coincident(g16,g17)
    c: Coincident(g17,g18)
    c: Vertical(g18)
    c: Coincident(g19,g18)
    c: Coincident(g20,g19)
    c: Coincident(g21,g20)
    c: Vertical(g21)
    c: Coincident(g21,g22)
    c: Vertical(g22)
    c: Coincident(g22,g23)
    c: Coincident(g23,g24)
    c: Coincident(g24,g25)
    c: Coincident(g27,g26)
    c: Coincident(g28,g27)
    c: Horizontal(g28)
    c: DistanceX(g28,g28) = 5.37372
    c: Distance(g26) = 4.46542
    c: Distance(g27) = 3.86749
    c: Coincident(g29,g28)
    c: DistanceY(g7,g7) = 12
    c: DistanceY(g5,g5) = 10.4
    c: Distance(g4) = 5.3
    c: Distance(g3) = 5.60673
    c: Distance(g1) = 36.0023
    c: Distance(g15) = 2.41133
    c: Distance(g14) = 2.80018
    c: Distance(g13) = 2.07357
    c: DistanceX(g12,g12) = 6.85172
    c: Distance(g16) = 19.7388
    c: Distance(g17) = 23.3379
    c: DistanceY(g18,g18) = 12
    c: DistanceY(g21,g21) = 1.6
    c: DistanceY(g22,g22) = 4
    c: Distance(g23) = 2.8019
    c: Distance(g24) = 3.63982
    c: Distance(g25) = 4.89246
    c: Angle(g23,g22) = 2.81082
    c: Angle(g24,g22) = 2.52188
    c: Angle(g25,g22) = 2.26951
    c: Angle(g18,g19) = 2.50404
    c: Angle(g17,g18) = 2.81442
    c: Coincident(g30,g29)
    c: Coincident(g31,g30)
    c: Horizontal(g31)
    c: Coincident(g32,g31)
    c: Coincident(g32,g25)
    c: Distance(g30) = 30.6334
    c: Angle(g30,g28) = 0.110874
    c: DistanceX(g31,g31) = 130
    c: Distance(g32) = 127.367
    c: Coincident(g1,g33)
    c: Horizontal(g33)
    c: Coincident(g33,g34)
    c: Coincident(g35,g34)
    c: Coincident(g35,g8)
    c: Distance(g35) = 2.4804
    c: Angle(g13,g12) = 2.49901
    c: Angle(g14,g12) = 2.36124
    c: Angle(g15,g12) = 2.24748
    c: Angle(g34,g35) = 2.11973
    c: Angle(g34,g8) = 2.04062
    c: Angle(g34,g9) = 1.58195
    c: Angle(g9,g10) = 3.03808
    c: Angle(g31,g32) = 2.59833
    c: Coincident(g16,g36)
    c: Coincident(g36,g37)
    c: Coincident(g37,g38)
    c: Coincident(g38,g39)
    c: Coincident(g39,g40)
    c: Coincident(g40,g41)
    c: Coincident(g41,g42)
    c: Vertical(g42)
    c: Coincident(g42,g43)
    c: Coincident(g43,g44)
    c: Coincident(g45,g15)
    c: Distance(g36) = 12.5968
    c: Distance(g37) = 35.4072
    c: Distance(g38) = 3.49857
    c: Distance(g39) = 6.65282
    c: Distance(g40) = 4.97393
    c: Distance(g41) = 4.23793
    c: DistanceY(g42,g42) = 137.8
    c: Angle(g16,g17) = 2.58706
    c: Angle(g36,g16) = 2.86681
    c: Angle(g36,g37) = 3.12214
    c: Angle(g37,g38) = 3.03493
    c: Angle(g38,g39) = 2.85409
    c: Angle(g39,g40) = 2.92535
    c: Angle(g40,g41) = 2.95164
    c: Angle(g42,g43) = 2.81984
    c: Angle(g42,g44) = 2.49809
    c: Angle(g33,g1) = 1.58154
    c: Distance(g34) = 10.9802
    c: Distance(g45) = 52.6666
    c: Distance(g44) = 5
    c: Distance(g43) = 4.42719
    c: Distance(g11) = 103.143
    c: Coincident(g44,g45)
    c: Coincident(g46,g26)
    c: Vertical(g46)
    c: Distance(g46) = 7.20003
    c: Angle(g46,g26) = 2.54737
    c: Coincident(g47,g48)
    c: Coincident(g48,g49)
    c: Coincident(g49,g50)
    c: Coincident(g50,g47)
    c: Horizontal(g47)
    c: Horizontal(g49)
    c: Vertical(g48)
    c: Vertical(g50)
    c: DistanceY(g48,g48) = 602
    c: DistanceX(g49,g49) = 452
    c: Vertical(g51)
    c: Coincident(g52,g7)
    c: Coincident(g52,g46)
    c: Angle(g27,g28) = 2.1529
    c: Angle(g4,g5) = 2.58482
    c: Angle(g3,g5) = 2.40074
    c: Distance(g2) = 108.304
    c: Angle(g2,g5) = 2.03453
    c: Angle(g28,g29) = 2.86965
    c: DistanceX(g33,g33) = 54.3011
    c: Angle(g21,g20) = 2.65067
    c: Distance(g20) = 178.589
    c: Distance(g19) = 3.36006
    c: Coincident(g53,g7)
    c: PointOnObject(g53,g17)
    c: Horizontal(g53)
    c: DistanceX(g53,g53) = 192.695
FEATURE [PartDesign::Pocket] Pocket104  label="Body Cutout005"
  BaseFeature = -> Pad017
  Direction = (0,0,-1)
  Length = 45
  Length2 = 5
  Profile = -> Sketch329
  ReferenceAxis = -> Sketch329 [N_Axis]
  Type = 0
FEATURE [Sketcher::SketchObject] Sketch335  label="Tremelo Springs Pocket005"
  FullyConstrained = false
  MapMode = 5
  Placement = pos=(0,0,0) rot=(1,0,0;3.14159rad)
  sketch-geometry (5):
    g0: LineSegment StartX=253.5 StartY=-385.3 StartZ=0 EndX=196.5 EndY=-385.3 EndZ=0
    g1: LineSegment StartX=196.5 StartY=-385.3 StartZ=0 EndX=196.5 EndY=-287.3 EndZ=0
    g2: LineSegment StartX=196.5 StartY=-287.3 StartZ=0 EndX=253.5 EndY=-287.3 EndZ=0
    g3: LineSegment StartX=253.5 StartY=-287.3 StartZ=0 EndX=253.5 EndY=-385.3 EndZ=0
    g4: LineSegment StartX=225 StartY=-70 StartZ=0 EndX=225 EndY=-310 EndZ=0
  constraints (11):
    c: Coincident(g0,g1)
    c: Coincident(g1,g2)
    c: Coincident(g2,g3)
    c: Coincident(g3,g0)
    c: Horizontal(g0)
    c: Horizontal(g2)
    c: Vertical(g1)
    c: Vertical(g3)
    c: DistanceY(g3,g3) = 98
    c: DistanceX(g0,g0) = 57
    c: Vertical(g4)
FEATURE [Sketcher::SketchObject] Sketch336  label="Speaker Rear cover mount pocket005"
  FullyConstrained = false
  MapMode = 5
  Placement = pos=(0,0,0) rot=(1,0,0;3.14159rad)
  sketch-geometry (1):
    g0: Circle CenterX=330 CenterY=-121 CenterZ=0 NormalX=0 NormalY=0 NormalZ=1 AngleXU=0 Radius=47
  constraints (1):
    c: Diameter(g0) = 94
FEATURE [PartDesign::Pocket] Pocket105
  BaseFeature = -> Pocket098
  Direction = (0,0,-1)
  Length = 10
  Length2 = 5
  Profile = -> Sketch296
  ReferenceAxis = -> Sketch296 [N_Axis]
  Type = 0
FEATURE [PartDesign::Pocket] Pocket106
  BaseFeature = -> Pocket105
  Direction = (0,0,1)
  Length = 10
  Length2 = 5
  Profile = -> Sketch304
  ReferenceAxis = -> Sketch304 [N_Axis]
  Type = 0
FEATURE [PartDesign::Pocket] Pocket107
  BaseFeature = -> Pocket106
  Direction = (0,0,1)
  Length = 10
  Length2 = 5
  Profile = -> Sketch316
  ReferenceAxis = -> Sketch316 [N_Axis]
  Type = 0
FEATURE [PartDesign::Fillet] Fillet056
  Base = -> Pocket107 [Edge90,Edge88]
  BaseFeature = -> Pocket107
  Radius = 3.35
  SupportTransform = false
  UseAllEdges = false
FEATURE [PartDesign::Fillet] Fillet057
  Base = -> Fillet056 [Edge172,Edge171,Edge169,Edge167]
  BaseFeature = -> Fillet056
  Radius = 6
  SupportTransform = false
  UseAllEdges = false
FEATURE [Sketcher::SketchObject] Sketch309  label="Wire channels Pocket011"
  FullyConstrained = false
  MapMode = 5
  Placement = pos=(0,0,0) rot=(1,0,0;3.14159rad)
  Support = -> [Fillet057]
  sketch-geometry (14):
    g0: LineSegment StartX=254 StartY=-454.998 StartZ=0 EndX=254 EndY=-385.013 EndZ=0
    g1: LineSegment StartX=254 StartY=-385.013 StartZ=0 EndX=260 EndY=-369.99 EndZ=0
    g2: LineSegment StartX=260 StartY=-369.99 StartZ=0 EndX=255.25 EndY=-344.003 EndZ=0
    g3: LineSegment StartX=279 StartY=-454.998 StartZ=0 EndX=279 EndY=-384.9 EndZ=0
    g4: LineSegment StartX=295.012 StartY=-275.002 StartZ=0 EndX=279 EndY=-384.9 EndZ=0
    g5: LineSegment StartX=282 StartY=-274.99 StartZ=0 EndX=255.25 EndY=-332.21 EndZ=0
    g6: LineSegment StartX=255.25 StartY=-344.003 StartZ=0 EndX=255.25 EndY=-332.21 EndZ=0
    g7: LineSegment StartX=254 StartY=-454.998 StartZ=0 EndX=254 EndY=-459.998 EndZ=0
    g8: LineSegment StartX=279 StartY=-454.998 StartZ=0 EndX=279 EndY=-459.998 EndZ=0
    g9: LineSegment StartX=279 StartY=-459.998 StartZ=0 EndX=254 EndY=-459.998 EndZ=0
    g10: LineSegment StartX=317.382 StartY=-256 StartZ=0 EndX=295.012 EndY=-275.002 EndZ=0
    g11: LineSegment StartX=307.382 StartY=-251 StartZ=0 EndX=282 EndY=-274.99 EndZ=0
    g12: LineSegment StartX=317.382 StartY=-256 StartZ=0 EndX=317.382 EndY=-251 EndZ=0
    g13: LineSegment StartX=307.382 StartY=-251 StartZ=0 EndX=317.382 EndY=-251 EndZ=0
  constraints (35):
    c: Vertical(g0)
    c: Coincident(g0,g1)
    c: Coincident(g1,g2)
    c: Vertical(g3)
    c: Coincident(g4,g3)
    c: Distance(g4) = 111.059
    c: Distance(g5) = 63.1639
    c: Distance(g2) = 26.4172
    c: Distance(g1) = 16.1774
    c: Distance(g0) = 69.9845
    c: Distance(g3) = 70.0978
    c: Coincident(g6,g2)
    c: Coincident(g6,g5)
    c: Vertical(g6)
    c: Distance(g6) = 11.7934
    c: Coincident(g7,g0)
    c: Vertical(g7)
    c: Coincident(g8,g3)
    c: Vertical(g8)
    c: Coincident(g9,g8)
    c: Coincident(g9,g7)
    c: Horizontal(g9)
    c: Distance(g7) = 5
    c: Distance(g9) = 25
    c: Distance(g8) = 5
    c: Coincident(g10,g4)
    c: Distance(g10) = 29.351
    c: Coincident(g11,g5)
    c: Coincident(g12,g10)
    c: Vertical(g12)
    c: Distance(g11) = 34.9253
    c: Distance(g12) = 5
    c: Coincident(g13,g11)
    c: Coincident(g13,g12)
    c: Horizontal(g13)
FEATURE [PartDesign::Pocket] Pocket108
  BaseFeature = -> Fillet057
  Direction = (0,0,1)
  Length = 10
  Length2 = 5
  Profile = -> Sketch309
  ReferenceAxis = -> Sketch309 [N_Axis]
  Type = 0
FEATURE [PartDesign::Fillet] Fillet058
  Base = -> Pocket108 [Edge226,Edge224]
  BaseFeature = -> Pocket108
  Radius = 6.35
  SupportTransform = false
  UseAllEdges = false
FEATURE [PartDesign::Fillet] Fillet059
  Base = -> Fillet058 [Edge99,Edge101,Edge102]
  BaseFeature = -> Fillet058
  Radius = 3.35
  SupportTransform = false
  UseAllEdges = false
FEATURE [PartDesign::Fillet] Fillet060
  Base = -> Fillet059 [Edge103]
  BaseFeature = -> Fillet059
  Radius = 30
  SupportTransform = false
  UseAllEdges = false
FEATURE [PartDesign::Fillet] Fillet061
  Base = -> Fillet060 [Edge106]
  BaseFeature = -> Fillet060
  Radius = 40
  SupportTransform = false
  UseAllEdges = false
FEATURE [PartDesign::Fillet] Fillet062
  Base = -> Fillet061 [Edge89,Edge94]
  BaseFeature = -> Fillet061
  Radius = 20
  SupportTransform = false
  UseAllEdges = false
FEATURE [PartDesign::Fillet] Fillet063
  Base = -> Fillet062 [Edge123]
  BaseFeature = -> Fillet062
  Radius = 50
  SupportTransform = false
  UseAllEdges = false
FEATURE [PartDesign::Fillet] Fillet064
  Base = -> Fillet063 [Edge106]
  BaseFeature = -> Fillet063
  Radius = 30
  SupportTransform = false
  UseAllEdges = false
FEATURE [PartDesign::Fillet] Fillet065
  Base = -> Fillet064 [Edge87]
  BaseFeature = -> Fillet064
  Radius = 20
  SupportTransform = false
  UseAllEdges = false
FEATURE [PartDesign::Pocket] Pocket110
  BaseFeature = -> Pocket104
  Direction = (0,0,1)
  Length = 7
  Length2 = 5
  Profile = -> Sketch335
  ReferenceAxis = -> Sketch335 [N_Axis]
  Type = 0
FEATURE [Sketcher::SketchObject] Sketch343
  FullyConstrained = false
  MapMode = 5
  Placement = pos=(0,0,7) rot=(0,0,1;0rad)
  Support = -> [Pocket110]
  sketch-geometry (4):
    g0: LineSegment StartX=247 StartY=427.9 StartZ=0 EndX=267 EndY=427.9 EndZ=0
    g1: LineSegment StartX=267 StartY=427.9 StartZ=0 EndX=267 EndY=412.9 EndZ=0
    g2: LineSegment StartX=267 StartY=412.9 StartZ=0 EndX=247 EndY=412.9 EndZ=0
    g3: LineSegment StartX=247 StartY=412.9 StartZ=0 EndX=247 EndY=427.9 EndZ=0
  constraints (10):
    c: Coincident(g0,g1)
    c: Coincident(g1,g2)
    c: Coincident(g2,g3)
    c: Coincident(g3,g0)
    c: Horizontal(g0)
    c: Horizontal(g2)
    c: Vertical(g1)
    c: Vertical(g3)
    c: DistanceX(g2,g2) = 20
    c: DistanceY(g3,g3) = 15
FEATURE [PartDesign::Pocket] Pocket111
  BaseFeature = -> Pocket110
  Direction = (0,0,-1)
  Length = 7
  Length2 = 5
  Profile = -> Sketch343
  ReferenceAxis = -> Sketch343 [N_Axis]
  Type = 0
FEATURE [PartDesign::Pocket] Pocket113
  BaseFeature = -> Pocket111
  Direction = (0,0,1)
  Length = 7
  Length2 = 5
  Profile = -> Sketch336
  ReferenceAxis = -> Sketch336 [N_Axis]
  Type = 0
FEATURE [Sketcher::SketchObject] Sketch345  label="Wire channels Pocket014"
  FullyConstrained = false
  MapMode = 5
  Placement = pos=(0,0,0) rot=(1,0,0;3.14159rad)
  Support = -> [Pocket113]
  sketch-geometry (29):
    g0: LineSegment StartX=101.467 StartY=-402.5 StartZ=0 EndX=130.4 EndY=-402.5 EndZ=0
    g1: LineSegment StartX=200 StartY=-200 StartZ=0 EndX=220 EndY=-200 EndZ=0
    g2: LineSegment StartX=135.4 StartY=-402.5 StartZ=0 EndX=135.4 EndY=-397.5 EndZ=0
    g3: LineSegment StartX=135.4 StartY=-397.5 StartZ=0 EndX=175 EndY=-357.904 EndZ=0
    g4: LineSegment StartX=175 StartY=-357.904 StartZ=0 EndX=175 EndY=-245 EndZ=0
    g5: LineSegment StartX=175 StartY=-245 StartZ=0 EndX=290 EndY=-245 EndZ=0
    g6: LineSegment StartX=290 StartY=-245 StartZ=0 EndX=295 EndY=-245 EndZ=0
    g7: LineSegment StartX=295 StartY=-245 StartZ=0 EndX=295 EndY=-215 EndZ=0
    g8: LineSegment StartX=295 StartY=-215 StartZ=0 EndX=290 EndY=-215 EndZ=0
    g9: LineSegment StartX=290 StartY=-215 StartZ=0 EndX=225 EndY=-215 EndZ=0
    g10: LineSegment StartX=225 StartY=-215 StartZ=0 EndX=225 EndY=-200 EndZ=0
    g11: LineSegment StartX=195 StartY=-200 StartZ=0 EndX=195 EndY=-215 EndZ=0
    g12: LineSegment StartX=195 StartY=-215 StartZ=0 EndX=168.46 EndY=-215 EndZ=0
    g13: LineSegment StartX=168.46 StartY=-215 StartZ=0 EndX=162 EndY=-198.36 EndZ=0
    g14: LineSegment StartX=162 StartY=-198.36 StartZ=0 EndX=162 EndY=-115 EndZ=0
    g15: LineSegment StartX=162 StartY=-115 StartZ=0 EndX=162 EndY=-110 EndZ=0
    g16: LineSegment StartX=162 StartY=-110 StartZ=0 EndX=157 EndY=-110 EndZ=0
    g17: LineSegment StartX=157 StartY=-110 StartZ=0 EndX=134.577 EndY=-122.534 EndZ=0
    g18: LineSegment StartX=134.577 StartY=-122.534 StartZ=0 EndX=132 EndY=-126.896 EndZ=0
    g19: LineSegment StartX=132 StartY=-126.896 StartZ=0 EndX=132 EndY=-200.027 EndZ=0
    g20: LineSegment StartX=132 StartY=-200.027 StartZ=0 EndX=144.989 EndY=-239.968 EndZ=0
    g21: LineSegment StartX=144.989 StartY=-239.968 StartZ=0 EndX=144.989 EndY=-343.839 EndZ=0
    g22: LineSegment StartX=144.989 StartY=-343.839 StartZ=0 EndX=96.4674 EndY=-392.5 EndZ=0
    g23: LineSegment StartX=96.4674 StartY=-392.5 StartZ=0 EndX=96.4674 EndY=-397.5 EndZ=0
    g24: LineSegment StartX=96.4674 StartY=-397.5 StartZ=0 EndX=96.4674 EndY=-402.5 EndZ=0
    g25: LineSegment StartX=101.467 StartY=-402.5 StartZ=0 EndX=96.4674 EndY=-402.5 EndZ=0
    g26: LineSegment StartX=130.4 StartY=-402.5 StartZ=0 EndX=135.4 EndY=-402.5 EndZ=0
    g27: LineSegment StartX=225 StartY=-200 StartZ=0 EndX=220 EndY=-200 EndZ=0
    g28: LineSegment StartX=195 StartY=-200 StartZ=0 EndX=200 EndY=-200 EndZ=0
  constraints (78):
    c: Horizontal(g0)
    c: DistanceX(g0,g0) = 28.9326
    c: Horizontal(g1)
    c: DistanceX(g1,g1) = 20
    c: Vertical(g2)
    c: Coincident(g2,g3)
    c: Coincident(g3,g4)
    c: Vertical(g4)
    c: Coincident(g4,g5)
    c: Horizontal(g5)
    c: Coincident(g5,g6)
    c: Horizontal(g6)
    c: Coincident(g6,g7)
    c: Vertical(g7)
    c: Coincident(g7,g8)
    c: Horizontal(g8)
    c: Coincident(g8,g9)
    c: Horizontal(g9)
    c: Coincident(g9,g10)
    c: Vertical(g10)
    c: Vertical(g11)
    c: Coincident(g11,g12)
    c: Horizontal(g12)
    c: Coincident(g12,g13)
    c: Coincident(g13,g14)
    c: Vertical(g14)
    c: Coincident(g14,g15)
    c: Vertical(g15)
    c: Coincident(g15,g16)
    c: Horizontal(g16)
    c: Coincident(g16,g17)
    c: Coincident(g17,g18)
    c: Coincident(g18,g19)
    c: Vertical(g19)
    c: Coincident(g19,g20)
    c: Coincident(g20,g21)
    c: Vertical(g21)
    c: Coincident(g21,g22)
    c: Coincident(g22,g23)
    c: Vertical(g23)
    c: Coincident(g23,g24)
    c: Vertical(g24)
    c: Coincident(g25,g0)
    c: Coincident(g25,g24)
    c: Horizontal(g25)
    c: Coincident(g26,g0)
    c: Coincident(g26,g2)
    c: Horizontal(g26)
    c: Coincident(g27,g10)
    c: Coincident(g27,g1)
    c: Horizontal(g27)
    c: Coincident(g28,g11)
    c: Coincident(g28,g1)
    c: Horizontal(g28)
    c: DistanceX(g25,g25) = 5
    c: DistanceX(g26,g26) = 5
    c: DistanceY(g24,g24) = 5
    c: DistanceY(g23,g23) = 5
    c: DistanceY(g2,g2) = 5
    c: Distance(g22) = 68.7186
    c: Distance(g3) = 56
    c: DistanceY(g21,g21) = 103.871
    c: DistanceY(g4,g4) = 112.904
    c: DistanceX(g5,g5) = 115
    c: DistanceX(g12,g12) = 26.54
    c: DistanceX(g9,g9) = 65
    c: Distance(g20) = 42
    c: DistanceY(g19,g19) = 73.1311
    c: DistanceY(g14,g14) = 83.36
    c: DistanceX(g27,g27) = 5
    c: DistanceX(g28,g28) = 5
    c: DistanceX(g8,g8) = 5
    c: DistanceX(g6,g6) = 5
    c: DistanceY(g7,g7) = 30
    c: Distance(g17) = 25.6886
    c: Distance(g18) = 5.06593
    c: Distance(g16) = 5
    c: DistanceY(g15,g15) = 5
FEATURE [PartDesign::Pocket] Pocket114
  BaseFeature = -> Pocket113
  Direction = (0,0,1)
  Length = 7
  Length2 = 5
  Profile = -> Sketch345
  ReferenceAxis = -> Sketch345 [N_Axis]
  Type = 0
FEATURE [Sketcher::SketchObject] Sketch346  label="blank template007"
  FullyConstrained = false
  MapMode = 5
  Support = -> [XY_Plane213]
  sketch-geometry (4):
    g0: LineSegment StartX=0 StartY=615 StartZ=0 EndX=450 EndY=615 EndZ=0
    g1: LineSegment StartX=450 StartY=615 StartZ=0 EndX=450 EndY=15 EndZ=0
    g2: LineSegment StartX=450 StartY=15 StartZ=0 EndX=0 EndY=15 EndZ=0
    g3: LineSegment StartX=0 StartY=15 StartZ=0 EndX=0 EndY=615 EndZ=0
  constraints (10):
    c: Coincident(g0,g1)
    c: Coincident(g1,g2)
    c: Coincident(g2,g3)
    c: Coincident(g3,g0)
    c: Horizontal(g0)
    c: Horizontal(g2)
    c: Vertical(g1)
    c: Vertical(g3)
    c: DistanceX(g2,g2) = 450
    c: DistanceY(g1,g1) = 600
FEATURE [PartDesign::Pad] Pad018  label="Template 600x456"
  Direction = (0,0,1)
  Length = 7
  Length2 = 10
  Profile = -> Sketch346
  ReferenceAxis = -> Sketch346 [N_Axis]
  Type = 0
FEATURE [Sketcher::SketchObject] Sketch347  label="Batt Sleeve Pocket007"
  FullyConstrained = false
  MapMode = 5
  Placement = pos=(0,0,0) rot=(1,0,0;3.14159rad)
  sketch-geometry (6):
    g0: LineSegment StartX=177.5 StartY=-200 StartZ=0 EndX=272.5 EndY=-200 EndZ=0
    g1: LineSegment StartX=272.5 StartY=-200 StartZ=0 EndX=272.5 EndY=-70 EndZ=0
    g2: LineSegment StartX=272.5 StartY=-70 StartZ=0 EndX=177.5 EndY=-70 EndZ=0
    g3: LineSegment StartX=177.5 StartY=-70 StartZ=0 EndX=177.5 EndY=-200 EndZ=0
    g4: LineSegment StartX=182.5 StartY=460 StartZ=0 EndX=267.5 EndY=460 EndZ=0
    g5: LineSegment StartX=225 StartY=459 StartZ=0 EndX=225 EndY=69 EndZ=0
  constraints (13):
    c: Coincident(g0,g1)
    c: Coincident(g1,g2)
    c: Coincident(g2,g3)
    c: Coincident(g3,g0)
    c: Horizontal(g0)
    c: Horizontal(g2)
    c: Vertical(g1)
    c: Vertical(g3)
    c: DistanceY(g1,g1) = 130
    c: DistanceX(g2,g2) = 95
    c: Horizontal(g4)
    c: DistanceX(g4,g4) = 85
    c: Vertical(g5)
FEATURE [Sketcher::SketchObject] Sketch348  label="Body Outline010"
  FullyConstrained = false
  MapMode = 5
  Placement = pos=(0,0,7) rot=(0,0,1;0rad)
  Support = -> [Pad018]
  sketch-geometry (54):
    g0: LineSegment StartX=197.29 StartY=495.3 StartZ=0 EndX=73.9 EndY=550.1 EndZ=0
    g1: LineSegment StartX=252.15 StartY=545.5 StartZ=0 EndX=252.536 EndY=509.5 EndZ=0
    g2: LineSegment StartX=252.536 StartY=509.5 StartZ=0 EndX=349.402 EndY=461.057 EndZ=0
    g3: LineSegment StartX=349.402 StartY=461.057 StartZ=0 EndX=353.186 EndY=456.92 EndZ=0
    g4: LineSegment StartX=353.186 StartY=456.92 StartZ=0 EndX=355.987 EndY=452.42 EndZ=0
    g5: LineSegment StartX=355.987 StartY=452.42 StartZ=0 EndX=355.987 EndY=442.02 EndZ=0
    g6: LineSegment StartX=355.987 StartY=442.02 StartZ=0 EndX=320 EndY=343.5 EndZ=0
    g7: LineSegment StartX=320 StartY=343.5 StartZ=0 EndX=320 EndY=331.5 EndZ=0
    g8: LineSegment StartX=195.596 StartY=533.25 StartZ=0 EndX=190.601 EndY=530.784 EndZ=0
    g9: LineSegment StartX=190.601 StartY=530.784 StartZ=0 EndX=185.731 EndY=530.784 EndZ=0
    g10: LineSegment StartX=185.731 StartY=530.784 StartZ=0 EndX=184.499 EndY=530.912 EndZ=0
    g11: LineSegment StartX=184.499 StartY=530.912 StartZ=0 EndX=97.9865 EndY=587.073 EndZ=0
    g12: LineSegment StartX=97.9865 StartY=587.073 StartZ=0 EndX=91.1348 EndY=587.073 EndZ=0
    g13: LineSegment StartX=91.1348 StartY=587.073 StartZ=0 EndX=89.4748 EndY=585.83 EndZ=0
    g14: LineSegment StartX=89.4748 StartY=585.83 StartZ=0 EndX=87.4848 EndY=583.86 EndZ=0
    g15: LineSegment StartX=87.4848 StartY=583.86 StartZ=0 EndX=85.9748 EndY=581.98 EndZ=0
    g16: LineSegment StartX=107.659 StartY=357.048 StartZ=0 EndX=122.894 EndY=344.497 EndZ=0
    g17: LineSegment StartX=122.894 StartY=344.497 StartZ=0 EndX=130.394 EndY=322.397 EndZ=0
    g18: LineSegment StartX=130.394 StartY=322.397 StartZ=0 EndX=130.394 EndY=310.397 EndZ=0
    g19: LineSegment StartX=130.394 StartY=310.397 StartZ=0 EndX=128.394 EndY=307.697 EndZ=0
    g20: LineSegment StartX=128.394 StartY=307.697 StartZ=0 EndX=44.2002 EndY=150.2 EndZ=0
    g21: LineSegment StartX=44.2002 StartY=150.2 StartZ=0 EndX=44.2002 EndY=148.6 EndZ=0
    g22: LineSegment StartX=44.2002 StartY=148.6 StartZ=0 EndX=44.2002 EndY=144.6 EndZ=0
    g23: LineSegment StartX=44.2002 StartY=144.6 StartZ=0 EndX=45.1102 EndY=141.95 EndZ=0
    g24: LineSegment StartX=45.1102 StartY=141.95 StartZ=0 EndX=47.2242 EndY=138.987 EndZ=0
    g25: LineSegment StartX=47.2242 StartY=138.987 StartZ=0 EndX=50.9702 EndY=135.84 EndZ=0
    g26: LineSegment StartX=413.447 StartY=50.3962 StartZ=0 EndX=410.947 EndY=46.6962 EndZ=0
    g27: LineSegment StartX=410.947 StartY=46.6962 StartZ=0 EndX=408.821 EndY=43.4657 EndZ=0
    g28: LineSegment StartX=408.821 StartY=43.4657 StartZ=0 EndX=403.447 EndY=43.4657 EndZ=0
    g29: LineSegment StartX=403.447 StartY=43.4657 StartZ=0 EndX=320.445 EndY=66.6106 EndZ=0
    g30: LineSegment StartX=320.445 StartY=66.6106 StartZ=0 EndX=290 EndY=70.0001 EndZ=0
    g31: LineSegment StartX=290 StartY=70.0001 StartZ=0 EndX=160 EndY=70.0001 EndZ=0
    g32: LineSegment StartX=160 StartY=70.0001 StartZ=0 EndX=50.9702 EndY=135.84 EndZ=0
    g33: LineSegment StartX=252.15 StartY=545.5 StartZ=0 EndX=197.848 EndY=545.5 EndZ=0
    g34: LineSegment StartX=197.848 StartY=545.5 StartZ=0 EndX=197.726 EndY=534.521 EndZ=0
    g35: LineSegment StartX=197.726 StartY=534.521 StartZ=0 EndX=195.596 EndY=533.25 EndZ=0
    g36: LineSegment StartX=107.659 StartY=357.048 StartZ=0 EndX=96.1282 EndY=362.119 EndZ=0
    g37: LineSegment StartX=96.1282 StartY=362.119 StartZ=0 EndX=64 EndY=377 EndZ=0
    g38: LineSegment StartX=64 StartY=377 StartZ=0 EndX=61 EndY=378.8 EndZ=0
    g39: LineSegment StartX=61 StartY=378.8 StartZ=0 EndX=56.5 EndY=383.7 EndZ=0
    g40: LineSegment StartX=56.5 StartY=383.7 StartZ=0 EndX=54 EndY=388 EndZ=0
    g41: LineSegment StartX=54 StartY=388 StartZ=0 EndX=52.6 EndY=392 EndZ=0
    g42: LineSegment StartX=52.6 StartY=392 StartZ=0 EndX=52.6 EndY=529.8 EndZ=0
    g43: LineSegment StartX=52.6 StartY=529.8 StartZ=0 EndX=54 EndY=534 EndZ=0
    g44: LineSegment StartX=54 StartY=534 StartZ=0 EndX=57 EndY=538 EndZ=0
    g45: LineSegment StartX=57 StartY=538 StartZ=0 EndX=85.9748 EndY=581.98 EndZ=0
    g46: LineSegment StartX=413.447 StartY=50.3962 StartZ=0 EndX=413.447 EndY=57.5962 EndZ=0
    g47: LineSegment StartX=-1 StartY=616 StartZ=0 EndX=451 EndY=616 EndZ=0
    g48: LineSegment StartX=451 StartY=616 StartZ=0 EndX=451 EndY=14 EndZ=0
    g49: LineSegment StartX=451 StartY=14 StartZ=0 EndX=-1 EndY=14 EndZ=0
    g50: LineSegment StartX=-1 StartY=14 StartZ=0 EndX=-1 EndY=616 EndZ=0
    g51: LineSegment StartX=257 StartY=545.5 StartZ=0 EndX=257 EndY=245.424 EndZ=0
    g52: LineSegment StartX=320 StartY=331.5 StartZ=0 EndX=413.447 EndY=57.5962 EndZ=0
    g53: LineSegment StartX=320 StartY=331.5 StartZ=0 EndX=127.305 EndY=331.5 EndZ=0
  constraints (149):
    c: Coincident(g1,g2)
    c: Coincident(g2,g3)
    c: Coincident(g3,g4)
    c: Coincident(g4,g5)
    c: Vertical(g5)
    c: Coincident(g6,g5)
    c: Coincident(g7,g6)
    c: Vertical(g7)
    c: Coincident(g8,g9)
    c: Horizontal(g9)
    c: Coincident(g9,g10)
    c: Coincident(g10,g11)
    c: Distance(g10) = 1.23908
    c: Distance(g8) = 5.57001
    c: DistanceX(g9,g9) = 4.86999
    c: Coincident(g12,g11)
    c: Horizontal(g12)
    c: Coincident(g13,g12)
    c: Coincident(g13,g14)
    c: Coincident(g14,g15)
    c: Coincident(g16,g17)
    c: Coincident(g17,g18)
    c: Vertical(g18)
    c: Coincident(g19,g18)
    c: Coincident(g20,g19)
    c: Coincident(g21,g20)
    c: Vertical(g21)
    c: Coincident(g21,g22)
    c: Vertical(g22)
    c: Coincident(g22,g23)
    c: Coincident(g23,g24)
    c: Coincident(g24,g25)
    c: Coincident(g27,g26)
    c: Coincident(g28,g27)
    c: Horizontal(g28)
    c: DistanceX(g28,g28) = 5.37372
    c: Distance(g26) = 4.46542
    c: Distance(g27) = 3.86749
    c: Coincident(g29,g28)
    c: DistanceY(g7,g7) = 12
    c: DistanceY(g5,g5) = 10.4
    c: Distance(g4) = 5.3
    c: Distance(g3) = 5.60673
    c: Distance(g1) = 36.0023
    c: Distance(g15) = 2.41133
    c: Distance(g14) = 2.80018
    c: Distance(g13) = 2.07357
    c: DistanceX(g12,g12) = 6.85172
    c: Distance(g16) = 19.7388
    c: Distance(g17) = 23.3379
    c: DistanceY(g18,g18) = 12
    c: DistanceY(g21,g21) = 1.6
    c: DistanceY(g22,g22) = 4
    c: Distance(g23) = 2.8019
    c: Distance(g24) = 3.63982
    c: Distance(g25) = 4.89246
    c: Angle(g23,g22) = 2.81082
    c: Angle(g24,g22) = 2.52188
    c: Angle(g25,g22) = 2.26951
    c: Angle(g18,g19) = 2.50404
    c: Angle(g17,g18) = 2.81442
    c: Coincident(g30,g29)
    c: Coincident(g31,g30)
    c: Horizontal(g31)
    c: Coincident(g32,g31)
    c: Coincident(g32,g25)
    c: Distance(g30) = 30.6334
    c: Angle(g30,g28) = 0.110874
    c: DistanceX(g31,g31) = 130
    c: Distance(g32) = 127.367
    c: Coincident(g1,g33)
    c: Horizontal(g33)
    c: Coincident(g33,g34)
    c: Coincident(g35,g34)
    c: Coincident(g35,g8)
    c: Distance(g35) = 2.4804
    c: Angle(g13,g12) = 2.49901
    c: Angle(g14,g12) = 2.36124
    c: Angle(g15,g12) = 2.24748
    c: Angle(g34,g35) = 2.11973
    c: Angle(g34,g8) = 2.04062
    c: Angle(g34,g9) = 1.58195
    c: Angle(g9,g10) = 3.03808
    c: Angle(g31,g32) = 2.59833
    c: Coincident(g16,g36)
    c: Coincident(g36,g37)
    c: Coincident(g37,g38)
    c: Coincident(g38,g39)
    c: Coincident(g39,g40)
    c: Coincident(g40,g41)
    c: Coincident(g41,g42)
    c: Vertical(g42)
    c: Coincident(g42,g43)
    c: Coincident(g43,g44)
    c: Coincident(g45,g15)
    c: Distance(g36) = 12.5968
    c: Distance(g37) = 35.4072
    c: Distance(g38) = 3.49857
    c: Distance(g39) = 6.65282
    c: Distance(g40) = 4.97393
    c: Distance(g41) = 4.23793
    c: DistanceY(g42,g42) = 137.8
    c: Angle(g16,g17) = 2.58706
    c: Angle(g36,g16) = 2.86681
    c: Angle(g36,g37) = 3.12214
    c: Angle(g37,g38) = 3.03493
    c: Angle(g38,g39) = 2.85409
    c: Angle(g39,g40) = 2.92535
    c: Angle(g40,g41) = 2.95164
    c: Angle(g42,g43) = 2.81984
    c: Angle(g42,g44) = 2.49809
    c: Angle(g33,g1) = 1.58154
    c: Distance(g34) = 10.9802
    c: Distance(g45) = 52.6666
    c: Distance(g44) = 5
    c: Distance(g43) = 4.42719
    c: Distance(g11) = 103.143
    c: Coincident(g44,g45)
    c: Coincident(g46,g26)
    c: Vertical(g46)
    c: Distance(g46) = 7.20003
    c: Angle(g46,g26) = 2.54737
    c: Coincident(g47,g48)
    c: Coincident(g48,g49)
    c: Coincident(g49,g50)
    c: Coincident(g50,g47)
    c: Horizontal(g47)
    c: Horizontal(g49)
    c: Vertical(g48)
    c: Vertical(g50)
    c: DistanceY(g48,g48) = 602
    c: DistanceX(g49,g49) = 452
    c: Vertical(g51)
    c: Coincident(g52,g7)
    c: Coincident(g52,g46)
    c: Angle(g27,g28) = 2.1529
    c: Angle(g4,g5) = 2.58482
    c: Angle(g3,g5) = 2.40074
    c: Distance(g2) = 108.304
    c: Angle(g2,g5) = 2.03453
    c: Angle(g28,g29) = 2.86965
    c: DistanceX(g33,g33) = 54.3011
    c: Angle(g21,g20) = 2.65067
    c: Distance(g20) = 178.589
    c: Distance(g19) = 3.36006
    c: Coincident(g53,g7)
    c: PointOnObject(g53,g17)
    c: Horizontal(g53)
    c: DistanceX(g53,g53) = 192.695
FEATURE [PartDesign::Pocket] Pocket115  label="Body Cutout006"
  BaseFeature = -> Pad018
  Direction = (0,0,-1)
  Length = 45
  Length2 = 5
  Profile = -> Sketch348
  ReferenceAxis = -> Sketch348 [N_Axis]
  Type = 0
FEATURE [Sketcher::SketchObject] Sketch351  label="Wire channels Pocket015"
  FullyConstrained = false
  MapMode = 5
  Placement = pos=(0,0,0) rot=(1,0,0;3.14159rad)
  Support = -> [Pocket115]
  sketch-geometry (21):
    g0: LineSegment StartX=137.085 StartY=-133.454 StartZ=0 EndX=137.085 EndY=-200.021 EndZ=0
    g1: LineSegment StartX=156.976 StartY=-121.576 StartZ=0 EndX=156.976 EndY=-200 EndZ=0
    g2: LineSegment StartX=137.085 StartY=-200.021 StartZ=0 EndX=150.067 EndY=-239.979 EndZ=0
    g3: LineSegment StartX=156.976 StartY=-200 StartZ=0 EndX=163.474 EndY=-220 EndZ=0
    g4: LineSegment StartX=101.467 StartY=-402.5 StartZ=0 EndX=101.467 EndY=-397.5 EndZ=0
    g5: LineSegment StartX=101.467 StartY=-397.5 StartZ=0 EndX=150.067 EndY=-348.9 EndZ=0
    g6: LineSegment StartX=150.067 StartY=-348.9 StartZ=0 EndX=150.067 EndY=-239.979 EndZ=0
    g7: LineSegment StartX=130.4 StartY=-402.5 StartZ=0 EndX=130.4 EndY=-397.5 EndZ=0
    g8: LineSegment StartX=130.4 StartY=-397.5 StartZ=0 EndX=170 EndY=-357.835 EndZ=0
    g9: LineSegment StartX=170 StartY=-357.835 StartZ=0 EndX=170 EndY=-240 EndZ=0
    g10: LineSegment StartX=163.474 StartY=-220 StartZ=0 EndX=200 EndY=-220 EndZ=0
    g11: LineSegment StartX=200 StartY=-220 StartZ=0 EndX=200 EndY=-200 EndZ=0
    g12: LineSegment StartX=220 StartY=-200 StartZ=0 EndX=220 EndY=-220 EndZ=0
    g13: LineSegment StartX=101.467 StartY=-402.5 StartZ=0 EndX=130.4 EndY=-402.5 EndZ=0
    g14: LineSegment StartX=200 StartY=-200 StartZ=0 EndX=220 EndY=-200 EndZ=0
    g15: LineSegment StartX=156.976 StartY=-121.576 StartZ=0 EndX=156.976 EndY=-115 EndZ=0
    g16: LineSegment StartX=137.085 StartY=-133.454 StartZ=0 EndX=137.085 EndY=-126.91 EndZ=0
    g17: LineSegment StartX=137.085 StartY=-126.91 StartZ=0 EndX=156.976 EndY=-115 EndZ=0
    g18: LineSegment StartX=290 StartY=-220 StartZ=0 EndX=220 EndY=-220 EndZ=0
    g19: LineSegment StartX=170 StartY=-240 StartZ=0 EndX=290 EndY=-240 EndZ=0
    g20: LineSegment StartX=290 StartY=-240 StartZ=0 EndX=290 EndY=-220 EndZ=0
  constraints (59):
    c: Vertical(g0)
    c: Vertical(g1)
    c: Coincident(g2,g0)
    c: Coincident(g3,g1)
    c: Angle(g3,g1) = 2.82743
    c: Angle(g2,g0) = 2.82743
    c: Vertical(g4)
    c: Coincident(g5,g4)
    c: Angle(g4,g5) = 2.35619
    c: DistanceY(g4,g4) = 5
    c: Coincident(g6,g5)
    c: Coincident(g6,g2)
    c: Vertical(g6)
    c: Vertical(g7)
    c: DistanceY(g7,g7) = 5
    c: Coincident(g8,g7)
    c: Coincident(g9,g8)
    c: Vertical(g9)
    c: Coincident(g10,g3)
    c: Horizontal(g10)
    c: Coincident(g11,g10)
    c: Vertical(g11)
    c: Vertical(g12)
    c: Coincident(g13,g4)
    c: Coincident(g13,g7)
    c: Horizontal(g13)
    c: Distance(g5) = 68.7308
    c: Distance(g8) = 56.0489
    c: Distance(g9) = 117.835
    c: Distance(g6) = 108.921
    c: Distance(g2) = 42.0134
    c: Distance(g0) = 66.5671
    c: Distance(g1) = 78.4237
    c: Distance(g3) = 21.0293
    c: Distance(g10) = 36.5256
    c: Distance(g11) = 20
    c: DistanceX(g13,g13) = 28.9326
    c: Coincident(g14,g11)
    c: Coincident(g14,g12)
    c: Horizontal(g14)
    c: DistanceX(g14,g14) = 20
    c: Coincident(g15,g1)
    c: Vertical(g15)
    c: DistanceY(g15,g15) = 6.57624
    c: Coincident(g16,g0)
    c: Vertical(g16)
    c: DistanceY(g16,g16) = 6.5444
    c: Coincident(g17,g16)
    c: Coincident(g17,g15)
    c: Coincident(g18,g12)
    c: Horizontal(g18)
    c: Coincident(g19,g9)
    c: Horizontal(g19)
    c: Coincident(g20,g19)
    c: Coincident(g20,g18)
    c: Vertical(g20)
    c: DistanceX(g18,g18) = 70
    c: DistanceX(g19,g19) = 120
    c: DistanceY(g20,g20) = 20
FEATURE [PartDesign::Fillet] Fillet066
  Base = -> Pocket114 [Edge240,Edge241]
  BaseFeature = -> Pocket114
  Radius = 6
  SupportTransform = false
  UseAllEdges = false
FEATURE [PartDesign::Fillet] Fillet067
  Base = -> Fillet066 [Edge255,Edge254,Edge257,Edge259]
  BaseFeature = -> Fillet066
  Radius = 6.35
  SupportTransform = false
  UseAllEdges = false
FEATURE [PartDesign::Fillet] Fillet068
  Base = -> Fillet067 [Edge249,Edge237,Edge235,Edge251,Edge253,Edge233,Edge271,Edge269,Edge267,Edge223,Edge227,Edge229,Edge255,Edge257,Edge259,Edge261,Edge263]
  BaseFeature = -> Fillet067
  Radius = 3.35
  SupportTransform = false
  UseAllEdges = false
FEATURE [PartDesign::Body] Body030  label="Jig 4 Body"
  Group = -> [Sketch319,Pad017,Sketch329,Pocket104,Sketch335,Sketch336,Sketch343,Sketch345,Pocket110,Pocket111,Pocket113,Pocket114,Fillet066,Fillet067,Fillet068]
  Origin = -> Origin211
  Tip = -> Fillet068
FEATURE [App::Part] Part049  label="Jig 4"
  Group = -> [Body030]
  Origin = -> Origin210
  Placement = pos=(0,0,-181.8) rot=(0,0,1;0rad)
FEATURE [PartDesign::Pocket] Pocket116
  BaseFeature = -> Pocket115
  Direction = (0,0,1)
  Length = 7
  Length2 = 5
  Profile = -> Sketch347
  ReferenceAxis = -> Sketch347 [N_Axis]
  Type = 0
FEATURE [PartDesign::Pocket] Pocket117
  BaseFeature = -> Pocket116
  Direction = (0,0,1)
  Length = 7
  Length2 = 5
  Profile = -> Sketch351
  ReferenceAxis = -> Sketch351 [N_Axis]
  Type = 0
FEATURE [PartDesign::Fillet] Fillet069
  Base = -> Pocket117 [Edge144,Edge108,Edge130,Edge128,Edge126,Edge124,Edge134,Edge142,Edge140,Edge116,Edge118,Edge114,Edge112,Edge110]
  BaseFeature = -> Pocket117
  Radius = 3.35
  SupportTransform = false
  UseAllEdges = false
FEATURE [PartDesign::Body] Body031  label="Jig 5 Body"
  Group = -> [Sketch346,Sketch347,Pad018,Sketch348,Pocket115,Sketch351,Pocket116,Pocket117,Fillet069]
  Origin = -> Origin213
  Tip = -> Fillet069
FEATURE [App::Part] Part050  label="Jig 5"
  Group = -> [Body031]
  Origin = -> Origin212
  Placement = pos=(0,0,-255.1) rot=(0,0,1;0rad)
FEATURE [Sketcher::SketchObject] Sketch352
  FullyConstrained = true
  MapMode = 5
  Placement = pos=(0,0,0) rot=(1,0,0;1.5708rad)
  Support = -> [XZ_Plane216]
  sketch-geometry (4):
    g0: LineSegment StartX=0 StartY=0 StartZ=0 EndX=-160 EndY=0 EndZ=0
    g1: LineSegment StartX=-160 StartY=0 StartZ=0 EndX=-160 EndY=45 EndZ=0
    g2: LineSegment StartX=-160 StartY=45 StartZ=0 EndX=0 EndY=45 EndZ=0
    g3: LineSegment StartX=0 StartY=45 StartZ=0 EndX=0 EndY=0 EndZ=0
  constraints (11):
    c: Coincident(g0,g1)
    c: Coincident(g1,g2)
    c: Coincident(g2,g3)
    c: Coincident(g3,g0)
    c: Horizontal(g0)
    c: Horizontal(g2)
    c: Vertical(g1)
    c: Vertical(g3)
    c: Coincident(g0,g-1)
    c: DistanceX(g0,g0) = 160
    c: DistanceY(g3,g3) = 45
FEATURE [PartDesign::Pad] Pad019
  Direction = (0,-1,2e-16)
  Length = 7
  Length2 = 10
  Placement = pos=(0,0,0) rot=(1,0,0;1.5708rad)
  Profile = -> Sketch352
  ReferenceAxis = -> Sketch352 [N_Axis]
  Type = 0
FEATURE [Sketcher::SketchObject] Sketch353  label="IO Pocket001"
  FullyConstrained = false
  MapMode = 5
  Placement = pos=(0,-7,3.1e-15) rot=(1,0,0;1.5708rad)
  Support = -> [Pad019]
  sketch-geometry (4):
    g0: LineSegment StartX=-130 StartY=35 StartZ=0 EndX=-30 EndY=35 EndZ=0
    g1: LineSegment StartX=-30 StartY=35 StartZ=0 EndX=-30 EndY=10 EndZ=0
    g2: LineSegment StartX=-30 StartY=10 StartZ=0 EndX=-130 EndY=10 EndZ=0
    g3: LineSegment StartX=-130 StartY=10 StartZ=0 EndX=-130 EndY=35 EndZ=0
  constraints (10):
    c: Coincident(g0,g1)
    c: Coincident(g1,g2)
    c: Coincident(g2,g3)
    c: Coincident(g3,g0)
    c: Horizontal(g0)
    c: Horizontal(g2)
    c: Vertical(g1)
    c: Vertical(g3)
    c: DistanceX(g0,g0) = 100
    c: DistanceY(g3,g3) = 25
FEATURE [Sketcher::SketchObject] Sketch355
  FullyConstrained = true
  MapMode = 5
  Placement = pos=(0,0,0) rot=(1,0,0;1.5708rad)
  Support = -> [XZ_Plane217]
  sketch-geometry (4):
    g0: LineSegment StartX=0 StartY=0 StartZ=0 EndX=-160 EndY=0 EndZ=0
    g1: LineSegment StartX=-160 StartY=0 StartZ=0 EndX=-160 EndY=45 EndZ=0
    g2: LineSegment StartX=-160 StartY=45 StartZ=0 EndX=0 EndY=45 EndZ=0
    g3: LineSegment StartX=0 StartY=45 StartZ=0 EndX=0 EndY=0 EndZ=0
  constraints (11):
    c: Coincident(g0,g1)
    c: Coincident(g1,g2)
    c: Coincident(g2,g3)
    c: Coincident(g3,g0)
    c: Horizontal(g0)
    c: Horizontal(g2)
    c: Vertical(g1)
    c: Vertical(g3)
    c: Coincident(g0,g-1)
    c: DistanceX(g0,g0) = 160
    c: DistanceY(g3,g3) = 45
FEATURE [PartDesign::Pad] Pad020
  Direction = (0,-1,2e-16)
  Length = 7
  Length2 = 10
  Placement = pos=(0,0,0) rot=(1,0,0;1.5708rad)
  Profile = -> Sketch355
  ReferenceAxis = -> Sketch355 [N_Axis]
  Type = 0
FEATURE [Sketcher::SketchObject] Sketch357  label="IO Plate Mounting Pocket003"
  FullyConstrained = false
  MapMode = 5
  Placement = pos=(0,-7,3.1e-15) rot=(1,0,0;1.5708rad)
  Support = -> [Pad020]
  sketch-geometry (4):
    g0: LineSegment StartX=-140 StartY=39 StartZ=0 EndX=-20 EndY=39 EndZ=0
    g1: LineSegment StartX=-20 StartY=39 StartZ=0 EndX=-20 EndY=6 EndZ=0
    g2: LineSegment StartX=-20 StartY=6 StartZ=0 EndX=-140 EndY=6 EndZ=0
    g3: LineSegment StartX=-140 StartY=6 StartZ=0 EndX=-140 EndY=39 EndZ=0
  constraints (9):
    c: Coincident(g0,g1)
    c: Coincident(g1,g2)
    c: Coincident(g2,g3)
    c: Coincident(g3,g0)
    c: Horizontal(g0)
    c: Horizontal(g2)
    c: Vertical(g1)
    c: Vertical(g3)
    c: DistanceX(g0,g0) = 120
FEATURE [PartDesign::Pocket] Pocket118
  BaseFeature = -> Pad019
  Direction = (0,1,-2e-16)
  Length = 7
  Length2 = 5
  Placement = pos=(0,0,0) rot=(1,0,0;1.5708rad)
  Profile = -> Sketch353
  ReferenceAxis = -> Sketch353 [N_Axis]
  Type = 0
FEATURE [PartDesign::Fillet] Fillet070
  Base = -> Pocket118 [Edge23,Edge22,Edge21,Edge24]
  BaseFeature = -> Pocket118
  Placement = pos=(0,0,0) rot=(1,0,0;1.5708rad)
  Radius = 6
  SupportTransform = false
  UseAllEdges = false
FEATURE [PartDesign::Body] Body032  label="Jig 6 Body"
  Group = -> [Sketch352,Pad019,Sketch353,Pocket118,Fillet070]
  Origin = -> Origin216
  Tip = -> Fillet070
FEATURE [App::Part] Part051  label="Jig 6"
  Group = -> [Body032]
  Origin = -> Origin214
  Placement = pos=(152.229,38.3824,0) rot=(0.930961,-0.258178,0.258178;4.64091rad)
FEATURE [PartDesign::Pocket] Pocket119
  BaseFeature = -> Pad020
  Direction = (0,1,-4e-16)
  Length = 7
  Length2 = 5
  Placement = pos=(0,0,0) rot=(1,0,0;1.5708rad)
  Profile = -> Sketch357
  ReferenceAxis = -> Sketch357 [N_Axis]
  Type = 0
FEATURE [PartDesign::Fillet] Fillet071
  Base = -> Pocket119 [Edge23,Edge22,Edge21,Edge24]
  BaseFeature = -> Pocket119
  Placement = pos=(0,0,0) rot=(1,0,0;1.5708rad)
  Radius = 6
  SupportTransform = false
  UseAllEdges = false
FEATURE [PartDesign::Body] Body033  label="Jig 7 Body"
  Group = -> [Sketch355,Pad020,Sketch357,Pocket119,Fillet071]
  Origin = -> Origin217
  Tip = -> Fillet071
FEATURE [App::Part] Part052  label="Jig 7"
  Group = -> [Body033]
  Origin = -> Origin215
  Placement = pos=(118.356,-17.7017,5.6e-15) rot=(-0.930961,0.258178,-0.258178;1.64227rad)
FEATURE [PartDesign::Fillet] Fillet072
  Base = -> Fillet065 [Edge197,Edge201]
  BaseFeature = -> Fillet065
  Radius = 4.8
  SupportTransform = false
  UseAllEdges = false
FEATURE [Sketcher::SketchObject] Sketch358
  FullyConstrained = false
  MapMode = 5
  Placement = pos=(0,0,0) rot=(1,0,0;3.14159rad)
  Support = -> [Fillet047]
  sketch-geometry (13):
    g0: LineSegment StartX=252.2 StartY=-540 StartZ=0 EndX=197.79 EndY=-540 EndZ=0
    g1: LineSegment StartX=197.79 StartY=-540.01 StartZ=0 EndX=225 EndY=-540.01 EndZ=0
    g2: LineSegment StartX=225 StartY=-540.01 StartZ=0 EndX=225 EndY=-546 EndZ=0
    g3: LineSegment StartX=225 StartY=-545.502 StartZ=0 EndX=225 EndY=-535.5 EndZ=0
    g4: LineSegment StartX=225 StartY=-535.5 StartZ=0 EndX=225 EndY=-484.5 EndZ=0
    g5: LineSegment StartX=225 StartY=-484.5 StartZ=0 EndX=244 EndY=-484.5 EndZ=0
    g6: LineSegment StartX=225 StartY=-484.5 StartZ=0 EndX=206 EndY=-484.5 EndZ=0
    g7: LineSegment StartX=225 StartY=-535.5 StartZ=0 EndX=244 EndY=-535.5 EndZ=0
    g8: LineSegment StartX=225 StartY=-535.5 StartZ=0 EndX=205.9 EndY=-535.5 EndZ=0
    g9: Circle CenterX=205.9 CenterY=-535.5 CenterZ=0 NormalX=0 NormalY=0 NormalZ=1 AngleXU=0 Radius=2.25
    g10: Circle CenterX=244 CenterY=-535.5 CenterZ=0 NormalX=0 NormalY=0 NormalZ=1 AngleXU=0 Radius=2.25
    g11: Circle CenterX=244 CenterY=-484.5 CenterZ=0 NormalX=0 NormalY=0 NormalZ=1 AngleXU=0 Radius=2.25
    g12: Circle CenterX=206 CenterY=-484.5 CenterZ=0 NormalX=0 NormalY=0 NormalZ=1 AngleXU=0 Radius=2.25
  constraints (24):
    c: Horizontal(g0)
    c: Horizontal(g1)
    c: Coincident(g2,g1)
    c: Vertical(g2)
    c: PointOnObject(g3,g2)
    c: Vertical(g3)
    c: Coincident(g4,g3)
    c: Vertical(g4)
    c: Coincident(g5,g4)
    c: Horizontal(g5)
    c: Coincident(g6,g4)
    c: Horizontal(g6)
    c: Coincident(g7,g3)
    c: Horizontal(g7)
    c: Coincident(g8,g3)
    c: Horizontal(g8)
    c: Coincident(g9,g8)
    c: Coincident(g10,g7)
    c: Coincident(g11,g5)
    c: Coincident(g12,g6)
    c: Equal(g10,g9)
    c: Equal(g10,g12)
    c: Equal(g10,g11)
    c: Diameter(g10) = 4.5
FEATURE [PartDesign::Pocket] Pocket120  label="Neck Bolt Holes"
  BaseFeature = -> Fillet047
  Direction = (0,0,1)
  Length = 25
  Length2 = 5
  Profile = -> Sketch358
  ReferenceAxis = -> Sketch358 [N_Axis]
  Type = 0
FEATURE [PartDesign::Body] Body001  label="Body Mk 1"
  Group = -> [Sketch019,Sketch021,Sketch022,Sketch023,Sketch024,Sketch025,Sketch026,Sketch027,Sketch028,Sketch029,Pad001,Sketch031,Sketch032,Sketch033,Sketch034,Sketch035,Sketch036,Pocket,Pocket001,Pocket002,Pocket003,Pocket004,Pocket005,Pocket006,Pocket007,Pocket008,Pocket009,Pocket010,Pocket011,Pocket012,Sketch140,Sketch141,Sketch142,Pocket029,Pocket030,Fillet004,Fillet005,Fillet006,Fillet007,Fillet008,+47 more]
  Origin = -> Origin001
  Tip = -> Pocket120
FEATURE [TechDraw::DrawViewPart] View
  CoarseView = false
  Direction = (-0.581633,-0.443958,0.681619)
  Focus = 100
  HardHidden = false
  IsoCount = 0
  IsoHidden = false
  IsoVisible = false
  LockPosition = false
  Perspective = false
  Rotation = 0
  ScaleType = 0
  ScrubCount = 0
  SeamHidden = false
  SeamVisible = false
  SmoothHidden = false
  SmoothVisible = true
  Source = -> [Body001]
  X = 319.48
  XDirection = (0.753938,-0.608826,0.246797)
  Y = 363.667
FEATURE [TechDraw::DrawViewPart] View002
  CoarseView = false
  Direction = (0,0,-1)
  Focus = 100
  HardHidden = false
  IsoCount = 0
  IsoHidden = false
  IsoVisible = false
  LockPosition = false
  Perspective = false
  Rotation = 0
  ScaleType = 0
  ScrubCount = 0
  SeamHidden = false
  SeamVisible = false
  SmoothHidden = false
  SmoothVisible = true
  Source = -> [Body001]
  X = 612.009
  XDirection = (-1,0,0)
  Y = 297.521
FEATURE [TechDraw::DrawViewDimension] Dimension049
  AngleOverride = false
  Arbitrary = false
  ArbitraryTolerances = false
  EqualTolerance = true
  ExtensionAngle = 0
  FormatSpec = %.2w
  FormatSpecOverTolerance = %+.2w
  FormatSpecUnderTolerance = %+.2w
  Inverted = false
  LineAngle = 0
  LockPosition = false
  MeasureType = 1
  OverTolerance = 0
  References2D = -> [View002]
  Rotation = 0
  ScaleType = 0
  TheoreticalExact = false
  Type = 1
  UnderTolerance = 0
  X = -8.89752
  Y = -272.235
FEATURE [TechDraw::DrawViewDimension] Dimension050
  AngleOverride = false
  Arbitrary = false
  ArbitraryTolerances = false
  EqualTolerance = true
  ExtensionAngle = 0
  FormatSpec = %.2w
  FormatSpecOverTolerance = %+.2w
  FormatSpecUnderTolerance = %+.2w
  Inverted = false
  LineAngle = 0
  LockPosition = false
  MeasureType = 1
  OverTolerance = 0
  References2D = -> [View002]
  Rotation = 0
  ScaleType = 0
  TheoreticalExact = false
  Type = 1
  UnderTolerance = 0
  X = 28.7113
  Y = 281.824
FEATURE [TechDraw::DrawViewDimension] Dimension051
  AngleOverride = false
  Arbitrary = false
  ArbitraryTolerances = false
  EqualTolerance = true
  ExtensionAngle = 0
  FormatSpec = %.2w
  FormatSpecOverTolerance = %+.2w
  FormatSpecUnderTolerance = %+.2w
  Inverted = false
  LineAngle = 0
  LockPosition = false
  MeasureType = 1
  OverTolerance = 0
  References2D = -> [View002]
  Rotation = 0
  ScaleType = 0
  TheoreticalExact = false
  Type = 2
  UnderTolerance = 0
  X = -191.885
  Y = -16.749
FEATURE [TechDraw::DrawViewDimension] Dimension052
  AngleOverride = false
  Arbitrary = false
  ArbitraryTolerances = false
  EqualTolerance = true
  ExtensionAngle = 0
  FormatSpec = ⌀%.2w
  FormatSpecOverTolerance = %+.2w
  FormatSpecUnderTolerance = %+.2w
  Inverted = false
  LineAngle = 0
  LockPosition = false
  MeasureType = 1
  OverTolerance = 0
  References2D = -> [View002]
  Rotation = 0
  ScaleType = 0
  TheoreticalExact = false
  Type = 5
  UnderTolerance = 0
  X = -87.7919
  Y = -202.846
FEATURE [TechDraw::DrawViewDimension] Dimension053
  AngleOverride = false
  Arbitrary = false
  ArbitraryTolerances = false
  EqualTolerance = true
  ExtensionAngle = 0
  FormatSpec = ⌀%.2w
  FormatSpecOverTolerance = %+.2w
  FormatSpecUnderTolerance = %+.2w
  Inverted = false
  LineAngle = 0
  LockPosition = false
  MeasureType = 1
  OverTolerance = 0
  References2D = -> [View002]
  Rotation = 0
  ScaleType = 0
  TheoreticalExact = false
  Type = 5
  UnderTolerance = 0
  X = -87.6418
  Y = -174.25
FEATURE [TechDraw::DrawViewDimension] Dimension054
  AngleOverride = false
  Arbitrary = false
  ArbitraryTolerances = false
  EqualTolerance = true
  ExtensionAngle = 0
  FormatSpec = %.2w
  FormatSpecOverTolerance = %+.2w
  FormatSpecUnderTolerance = %+.2w
  Inverted = false
  LineAngle = 0
  LockPosition = false
  MeasureType = 1
  OverTolerance = 0
  References2D = -> [View002]
  Rotation = 0
  ScaleType = 0
  TheoreticalExact = false
  Type = 2
  UnderTolerance = 0
  X = 36.2767
  Y = 23.5308
FEATURE [TechDraw::DrawViewDimension] Dimension055
  AngleOverride = false
  Arbitrary = false
  ArbitraryTolerances = false
  EqualTolerance = true
  ExtensionAngle = 0
  FormatSpec = %.2w
  FormatSpecOverTolerance = %+.2w
  FormatSpecUnderTolerance = %+.2w
  Inverted = false
  LineAngle = 0
  LockPosition = false
  MeasureType = 1
  OverTolerance = 0
  References2D = -> [View002]
  Rotation = 0
  ScaleType = 0
  TheoreticalExact = false
  Type = 1
  UnderTolerance = 0
  X = 2.7257
  Y = 78.9733
FEATURE [TechDraw::DrawViewDimension] Dimension056
  AngleOverride = false
  Arbitrary = false
  ArbitraryTolerances = false
  EqualTolerance = true
  ExtensionAngle = 0
  FormatSpec = R%.2w
  FormatSpecOverTolerance = %+.2w
  FormatSpecUnderTolerance = %+.2w
  Inverted = false
  LineAngle = 0
  LockPosition = false
  MeasureType = 1
  OverTolerance = 0
  References2D = -> [View002]
  Rotation = 0
  ScaleType = 0
  TheoreticalExact = false
  Type = 4
  UnderTolerance = 0
  X = 36.5956
  Y = 84.5359
FEATURE [TechDraw::DrawViewDimension] Dimension057
  AngleOverride = false
  Arbitrary = false
  ArbitraryTolerances = false
  EqualTolerance = true
  ExtensionAngle = 0
  FormatSpec = %.2w
  FormatSpecOverTolerance = %+.2w
  FormatSpecUnderTolerance = %+.2w
  Inverted = false
  LineAngle = 0
  LockPosition = false
  MeasureType = 1
  OverTolerance = 0
  References2D = -> [View002]
  Rotation = 0
  ScaleType = 0
  TheoreticalExact = false
  Type = 1
  UnderTolerance = 0
  X = 0.154185
  Y = -53.5578
FEATURE [TechDraw::DrawViewDimension] Dimension058
  AngleOverride = false
  Arbitrary = false
  ArbitraryTolerances = false
  EqualTolerance = true
  ExtensionAngle = 0
  FormatSpec = %.2w
  FormatSpecOverTolerance = %+.2w
  FormatSpecUnderTolerance = %+.2w
  Inverted = false
  LineAngle = 0
  LockPosition = false
  MeasureType = 1
  OverTolerance = 0
  References2D = -> [View002]
  Rotation = 0
  ScaleType = 0
  TheoreticalExact = false
  Type = 2
  UnderTolerance = 0
  X = 42.8348
  Y = -38.8222
FEATURE [TechDraw::DrawViewDimension] Dimension059
  AngleOverride = false
  Arbitrary = false
  ArbitraryTolerances = false
  EqualTolerance = true
  ExtensionAngle = 0
  FormatSpec = R%.2w
  FormatSpecOverTolerance = %+.2w
  FormatSpecUnderTolerance = %+.2w
  Inverted = false
  LineAngle = 0
  LockPosition = false
  MeasureType = 1
  OverTolerance = 0
  References2D = -> [View002]
  Rotation = 0
  ScaleType = 0
  TheoreticalExact = false
  Type = 4
  UnderTolerance = 0
  X = -46.5917
  Y = -54.004
FEATURE [TechDraw::DrawViewDimension] Dimension060
  AngleOverride = false
  Arbitrary = false
  ArbitraryTolerances = false
  EqualTolerance = true
  ExtensionAngle = 0
  FormatSpec = %.2w
  FormatSpecOverTolerance = %+.2w
  FormatSpecUnderTolerance = %+.2w
  Inverted = false
  LineAngle = 0
  LockPosition = false
  MeasureType = 1
  OverTolerance = 0
  References2D = -> [View002]
  Rotation = 0
  ScaleType = 0
  TheoreticalExact = false
  Type = 1
  UnderTolerance = 0
  X = 3.98212
  Y = -137.69
FEATURE [TechDraw::DrawViewDimension] Dimension061
  AngleOverride = false
  Arbitrary = false
  ArbitraryTolerances = false
  EqualTolerance = true
  ExtensionAngle = 0
  FormatSpec = %.2w
  FormatSpecOverTolerance = %+.2w
  FormatSpecUnderTolerance = %+.2w
  Inverted = false
  LineAngle = 0
  LockPosition = false
  MeasureType = 1
  OverTolerance = 0
  References2D = -> [View002]
  Rotation = 0
  ScaleType = 0
  TheoreticalExact = false
  Type = 1
  UnderTolerance = 0
  X = 4.61296
  Y = -147.831
FEATURE [TechDraw::DrawViewDimension] Dimension062
  AngleOverride = false
  Arbitrary = false
  ArbitraryTolerances = false
  EqualTolerance = true
  ExtensionAngle = 0
  FormatSpec = R%.2w
  FormatSpecOverTolerance = %+.2w
  FormatSpecUnderTolerance = %+.2w
  Inverted = false
  LineAngle = 0
  LockPosition = false
  MeasureType = 1
  OverTolerance = 0
  References2D = -> [View002]
  Rotation = 0
  ScaleType = 0
  TheoreticalExact = false
  Type = 4
  UnderTolerance = 0
  X = -29.1224
  Y = -121.375
FEATURE [TechDraw::DrawViewDimension] Dimension064
  AngleOverride = false
  Arbitrary = false
  ArbitraryTolerances = false
  EqualTolerance = true
  ExtensionAngle = 0
  FormatSpec = %.2w
  FormatSpecOverTolerance = %+.2w
  FormatSpecUnderTolerance = %+.2w
  Inverted = false
  LineAngle = 0
  LockPosition = false
  MeasureType = 1
  OverTolerance = 0
  References2D = -> [View002]
  Rotation = 0
  ScaleType = 0
  TheoreticalExact = false
  Type = 2
  UnderTolerance = 0
  X = 34.0892
  Y = -176.301
FEATURE [TechDraw::DrawViewDimension] Dimension065
  AngleOverride = false
  Arbitrary = false
  ArbitraryTolerances = false
  EqualTolerance = true
  ExtensionAngle = 0
  FormatSpec = %.2w
  FormatSpecOverTolerance = %+.2w
  FormatSpecUnderTolerance = %+.2w
  Inverted = false
  LineAngle = 0
  LockPosition = false
  MeasureType = 1
  OverTolerance = 0
  References2D = -> [View002]
  Rotation = 0
  ScaleType = 0
  TheoreticalExact = false
  Type = 0
  UnderTolerance = 0
  X = 82.2975
  Y = 62.6374
FEATURE [TechDraw::DrawViewDimension] Dimension066
  AngleOverride = false
  Arbitrary = false
  ArbitraryTolerances = false
  EqualTolerance = true
  ExtensionAngle = 0
  FormatSpec = %.2w
  FormatSpecOverTolerance = %+.2w
  FormatSpecUnderTolerance = %+.2w
  Inverted = false
  LineAngle = 0
  LockPosition = false
  MeasureType = 1
  OverTolerance = 0
  References2D = -> [View002]
  Rotation = 0
  ScaleType = 0
  TheoreticalExact = false
  Type = 0
  UnderTolerance = 0
  X = 96.2736
  Y = 64.9525
FEATURE [TechDraw::DrawViewDimension] Dimension067
  AngleOverride = false
  Arbitrary = false
  ArbitraryTolerances = false
  EqualTolerance = true
  ExtensionAngle = 0
  FormatSpec = %.2w
  FormatSpecOverTolerance = %+.2w
  FormatSpecUnderTolerance = %+.2w
  Inverted = false
  LineAngle = 0
  LockPosition = false
  MeasureType = 1
  OverTolerance = 0
  References2D = -> [View002]
  Rotation = 0
  ScaleType = 0
  TheoreticalExact = false
  Type = 0
  UnderTolerance = 0
  X = 67.0192
  Y = -12.022
FEATURE [TechDraw::DrawViewDimension] Dimension068
  AngleOverride = false
  Arbitrary = false
  ArbitraryTolerances = false
  EqualTolerance = true
  ExtensionAngle = 0
  FormatSpec = %.2w
  FormatSpecOverTolerance = %+.2w
  FormatSpecUnderTolerance = %+.2w
  Inverted = false
  LineAngle = 0
  LockPosition = false
  MeasureType = 1
  OverTolerance = 0
  References2D = -> [View002]
  Rotation = 0
  ScaleType = 0
  TheoreticalExact = false
  Type = 0
  UnderTolerance = 0
  X = 75.0823
  Y = -25.541
FEATURE [TechDraw::DrawViewDimension] Dimension069
  AngleOverride = false
  Arbitrary = false
  ArbitraryTolerances = false
  EqualTolerance = true
  ExtensionAngle = 0
  FormatSpec = %.2w
  FormatSpecOverTolerance = %+.2w
  FormatSpecUnderTolerance = %+.2w
  Inverted = false
  LineAngle = 0
  LockPosition = false
  MeasureType = 1
  OverTolerance = 0
  References2D = -> [View002]
  Rotation = 0
  ScaleType = 0
  TheoreticalExact = false
  Type = 0
  UnderTolerance = 0
  X = -0.328606
  Y = -76.1605
FEATURE [TechDraw::DrawViewDimension] Dimension071
  AngleOverride = false
  Arbitrary = false
  ArbitraryTolerances = false
  EqualTolerance = true
  ExtensionAngle = 0
  FormatSpec = %.2w
  FormatSpecOverTolerance = %+.2w
  FormatSpecUnderTolerance = %+.2w
  Inverted = false
  LineAngle = 0
  LockPosition = false
  MeasureType = 1
  OverTolerance = 0
  References2D = -> [View002]
  Rotation = 0
  ScaleType = 0
  TheoreticalExact = false
  Type = 2
  UnderTolerance = 0
  X = -83.5358
  Y = -82.3767
FEATURE [TechDraw::DrawViewDimension] Dimension072
  AngleOverride = false
  Arbitrary = false
  ArbitraryTolerances = false
  EqualTolerance = true
  ExtensionAngle = 0
  FormatSpec = %.2w
  FormatSpecOverTolerance = %+.2w
  FormatSpecUnderTolerance = %+.2w
  Inverted = false
  LineAngle = 0
  LockPosition = false
  MeasureType = 1
  OverTolerance = 0
  References2D = -> [View002]
  Rotation = 0
  ScaleType = 0
  TheoreticalExact = false
  Type = 2
  UnderTolerance = 0
  X = -92.5827
  Y = -82.6556
FEATURE [TechDraw::DrawViewDimension] Dimension073
  AngleOverride = false
  Arbitrary = false
  ArbitraryTolerances = false
  EqualTolerance = true
  ExtensionAngle = 0
  FormatSpec = %.2w
  FormatSpecOverTolerance = %+.2w
  FormatSpecUnderTolerance = %+.2w
  Inverted = false
  LineAngle = 0
  LockPosition = false
  MeasureType = 1
  OverTolerance = 0
  References2D = -> [View002]
  Rotation = 0
  ScaleType = 0
  TheoreticalExact = false
  Type = 1
  UnderTolerance = 0
  X = -27.4186
  Y = -85.1385
FEATURE [TechDraw::DrawViewDimension] Dimension074
  AngleOverride = false
  Arbitrary = false
  ArbitraryTolerances = false
  EqualTolerance = true
  ExtensionAngle = 0
  FormatSpec = %.2w
  FormatSpecOverTolerance = %+.2w
  FormatSpecUnderTolerance = %+.2w
  Inverted = false
  LineAngle = 0
  LockPosition = false
  MeasureType = 1
  OverTolerance = 0
  References2D = -> [View002]
  Rotation = 0
  ScaleType = 0
  TheoreticalExact = false
  Type = 2
  UnderTolerance = 0
  X = 14.3248
  Y = -104.799
FEATURE [TechDraw::DrawViewDimension] Dimension075
  AngleOverride = false
  Arbitrary = false
  ArbitraryTolerances = false
  EqualTolerance = true
  ExtensionAngle = 0
  FormatSpec = %.2w
  FormatSpecOverTolerance = %+.2w
  FormatSpecUnderTolerance = %+.2w
  Inverted = false
  LineAngle = 0
  LockPosition = false
  MeasureType = 1
  OverTolerance = 0
  References2D = -> [View002]
  Rotation = 0
  ScaleType = 0
  TheoreticalExact = false
  Type = 1
  UnderTolerance = 0
  X = 48.6092
  Y = -85.1385
FEATURE [TechDraw::DrawViewDimension] Dimension076
  AngleOverride = false
  Arbitrary = false
  ArbitraryTolerances = false
  EqualTolerance = true
  ExtensionAngle = 0
  FormatSpec = %.2w
  FormatSpecOverTolerance = %+.2w
  FormatSpecUnderTolerance = %+.2w
  Inverted = false
  LineAngle = 0
  LockPosition = false
  MeasureType = 1
  OverTolerance = 0
  References2D = -> [View002]
  Rotation = 0
  ScaleType = 0
  TheoreticalExact = false
  Type = 0
  UnderTolerance = 0
  X = 76.1683
  Y = -100.835
FEATURE [TechDraw::DrawViewDimension] Dimension077
  AngleOverride = false
  Arbitrary = false
  ArbitraryTolerances = false
  EqualTolerance = true
  ExtensionAngle = 0
  FormatSpec = %.2w
  FormatSpecOverTolerance = %+.2w
  FormatSpecUnderTolerance = %+.2w
  Inverted = false
  LineAngle = 0
  LockPosition = false
  MeasureType = 1
  OverTolerance = 0
  References2D = -> [View002]
  Rotation = 0
  ScaleType = 0
  TheoreticalExact = false
  Type = 0
  UnderTolerance = 0
  X = 75.0418
  Y = -153.134
FEATURE [TechDraw::DrawViewDimension] Dimension078
  AngleOverride = false
  Arbitrary = false
  ArbitraryTolerances = false
  EqualTolerance = true
  ExtensionAngle = 0
  FormatSpec = %.2w
  FormatSpecOverTolerance = %+.2w
  FormatSpecUnderTolerance = %+.2w
  Inverted = false
  LineAngle = 0
  LockPosition = false
  MeasureType = 1
  OverTolerance = 0
  References2D = -> [View002]
  Rotation = 0
  ScaleType = 0
  TheoreticalExact = false
  Type = 0
  UnderTolerance = 0
  X = 78.7624
  Y = -180.525
FEATURE [TechDraw::DrawViewDimension] Dimension079
  AngleOverride = false
  Arbitrary = false
  ArbitraryTolerances = false
  EqualTolerance = true
  ExtensionAngle = 0
  FormatSpec = %.2w
  FormatSpecOverTolerance = %+.2w
  FormatSpecUnderTolerance = %+.2w
  Inverted = false
  LineAngle = 0
  LockPosition = false
  MeasureType = 1
  OverTolerance = 0
  References2D = -> [View002]
  Rotation = 0
  ScaleType = 0
  TheoreticalExact = false
  Type = 0
  UnderTolerance = 0
  X = 84.6657
  Y = -148.654
FEATURE [TechDraw::DrawViewDimension] Dimension080
  AngleOverride = false
  Arbitrary = false
  ArbitraryTolerances = false
  EqualTolerance = true
  ExtensionAngle = 0
  FormatSpec = %.2w
  FormatSpecOverTolerance = %+.2w
  FormatSpecUnderTolerance = %+.2w
  Inverted = false
  LineAngle = 0
  LockPosition = false
  MeasureType = 1
  OverTolerance = 0
  References2D = -> [View002]
  Rotation = 0
  ScaleType = 0
  TheoreticalExact = false
  Type = 0
  UnderTolerance = 0
  X = 81.8016
  Y = -94.7642
FEATURE [TechDraw::DrawViewDimension] Dimension081
  AngleOverride = false
  Arbitrary = false
  ArbitraryTolerances = false
  EqualTolerance = true
  ExtensionAngle = 0
  FormatSpec = %.2w
  FormatSpecOverTolerance = %+.2w
  FormatSpecUnderTolerance = %+.2w
  Inverted = false
  LineAngle = 0
  LockPosition = false
  MeasureType = 1
  OverTolerance = 0
  References2D = -> [View002]
  Rotation = 0
  ScaleType = 0
  TheoreticalExact = false
  Type = 0
  UnderTolerance = 0
  X = 87.5415
  Y = -21.0607
FEATURE [TechDraw::DrawViewDimension] Dimension082
  AngleOverride = false
  Arbitrary = false
  ArbitraryTolerances = false
  EqualTolerance = true
  ExtensionAngle = 0
  FormatSpec = %.2w
  FormatSpecOverTolerance = %+.2w
  FormatSpecUnderTolerance = %+.2w
  Inverted = false
  LineAngle = 0
  LockPosition = false
  MeasureType = 1
  OverTolerance = 0
  References2D = -> [View002]
  Rotation = 0
  ScaleType = 0
  TheoreticalExact = false
  Type = 0
  UnderTolerance = 0
  X = 110.876
  Y = 53.0834
FEATURE [TechDraw::DrawViewDimension] Dimension083
  AngleOverride = false
  Arbitrary = false
  ArbitraryTolerances = false
  EqualTolerance = true
  ExtensionAngle = 0
  FormatSpec = %.2w
  FormatSpecOverTolerance = %+.2w
  FormatSpecUnderTolerance = %+.2w
  Inverted = false
  LineAngle = 0
  LockPosition = false
  MeasureType = 1
  OverTolerance = 0
  References2D = -> [View002]
  Rotation = 0
  ScaleType = 0
  TheoreticalExact = false
  Type = 0
  UnderTolerance = 0
  X = 99.597
  Y = -90.9181
FEATURE [TechDraw::DrawViewDimension] Dimension084
  AngleOverride = false
  Arbitrary = false
  ArbitraryTolerances = false
  EqualTolerance = true
  ExtensionAngle = 0
  FormatSpec = %.2w
  FormatSpecOverTolerance = %+.2w
  FormatSpecUnderTolerance = %+.2w
  Inverted = false
  LineAngle = 0
  LockPosition = false
  MeasureType = 1
  OverTolerance = 0
  References2D = -> [View002]
  Rotation = 0
  ScaleType = 0
  TheoreticalExact = false
  Type = 0
  UnderTolerance = 0
  X = 101.458
  Y = -149.115
FEATURE [TechDraw::DrawViewDimension] Dimension085
  AngleOverride = false
  Arbitrary = false
  ArbitraryTolerances = false
  EqualTolerance = true
  ExtensionAngle = 0
  FormatSpec = %.2w
  FormatSpecOverTolerance = %+.2w
  FormatSpecUnderTolerance = %+.2w
  Inverted = false
  LineAngle = 0
  LockPosition = false
  MeasureType = 1
  OverTolerance = 0
  References2D = -> [View002]
  Rotation = 0
  ScaleType = 0
  TheoreticalExact = false
  Type = 0
  UnderTolerance = 0
  X = 64.0563
  Y = -157.44
FEATURE [TechDraw::DrawViewDimension] Dimension086
  AngleOverride = false
  Arbitrary = false
  ArbitraryTolerances = false
  EqualTolerance = true
  ExtensionAngle = 0
  FormatSpec = %.2w
  FormatSpecOverTolerance = %+.2w
  FormatSpecUnderTolerance = %+.2w
  Inverted = false
  LineAngle = 0
  LockPosition = false
  MeasureType = 1
  OverTolerance = 0
  References2D = -> [View002]
  Rotation = 0
  ScaleType = 0
  TheoreticalExact = false
  Type = 0
  UnderTolerance = 0
  X = 62.2972
  Y = -107.194
FEATURE [TechDraw::DrawViewDimension] Dimension087
  AngleOverride = false
  Arbitrary = false
  ArbitraryTolerances = false
  EqualTolerance = true
  ExtensionAngle = 0
  FormatSpec = %.2w
  FormatSpecOverTolerance = %+.2w
  FormatSpecUnderTolerance = %+.2w
  Inverted = false
  LineAngle = 0
  LockPosition = false
  MeasureType = 1
  OverTolerance = 0
  References2D = -> [View002]
  Rotation = 0
  ScaleType = 0
  TheoreticalExact = false
  Type = 0
  UnderTolerance = 0
  X = 47.6671
  Y = -96.627
FEATURE [TechDraw::DrawViewDimension] Dimension090
  AngleOverride = false
  Arbitrary = false
  ArbitraryTolerances = false
  EqualTolerance = true
  ExtensionAngle = 0
  FormatSpec = %.2w
  FormatSpecOverTolerance = %+.2w
  FormatSpecUnderTolerance = %+.2w
  Inverted = false
  LineAngle = 0
  LockPosition = false
  MeasureType = 1
  OverTolerance = 0
  References2D = -> [View002]
  Rotation = 0
  ScaleType = 0
  TheoreticalExact = false
  Type = 0
  UnderTolerance = 0
  X = -0.487475
  Y = -121.454
FEATURE [TechDraw::DrawViewDimension] Dimension091
  AngleOverride = false
  Arbitrary = false
  ArbitraryTolerances = false
  EqualTolerance = true
  ExtensionAngle = 0
  FormatSpec = %.2w
  FormatSpecOverTolerance = %+.2w
  FormatSpecUnderTolerance = %+.2w
  Inverted = false
  LineAngle = 0
  LockPosition = false
  MeasureType = 1
  OverTolerance = 0
  References2D = -> [View002]
  Rotation = 0
  ScaleType = 0
  TheoreticalExact = false
  Type = 0
  UnderTolerance = 0
  X = -30.0596
  Y = -100.833
FEATURE [TechDraw::DrawViewDimension] Dimension092
  AngleOverride = false
  Arbitrary = false
  ArbitraryTolerances = false
  EqualTolerance = true
  ExtensionAngle = 0
  FormatSpec = %.2w
  FormatSpecOverTolerance = %+.2w
  FormatSpecUnderTolerance = %+.2w
  Inverted = false
  LineAngle = 0
  LockPosition = false
  MeasureType = 1
  OverTolerance = 0
  References2D = -> [View002]
  Rotation = 0
  ScaleType = 0
  TheoreticalExact = false
  Type = 0
  UnderTolerance = 0
  X = -6.81037
  Y = -60.7662
FEATURE [TechDraw::DrawViewDimension] Dimension093
  AngleOverride = false
  Arbitrary = false
  ArbitraryTolerances = false
  EqualTolerance = true
  ExtensionAngle = 0
  FormatSpec = %.2w
  FormatSpecOverTolerance = %+.2w
  FormatSpecUnderTolerance = %+.2w
  Inverted = false
  LineAngle = 0
  LockPosition = false
  MeasureType = 1
  OverTolerance = 0
  References2D = -> [View002]
  Rotation = 0
  ScaleType = 0
  TheoreticalExact = false
  Type = 0
  UnderTolerance = 0
  X = 51.1975
  Y = -10.3361
FEATURE [TechDraw::DrawViewDimension] Dimension094
  AngleOverride = false
  Arbitrary = false
  ArbitraryTolerances = false
  EqualTolerance = true
  ExtensionAngle = 0
  FormatSpec = %.2w
  FormatSpecOverTolerance = %+.2w
  FormatSpecUnderTolerance = %+.2w
  Inverted = false
  LineAngle = 0
  LockPosition = false
  MeasureType = 1
  OverTolerance = 0
  References2D = -> [View002]
  Rotation = 0
  ScaleType = 0
  TheoreticalExact = false
  Type = 0
  UnderTolerance = 0
  X = 63.958
  Y = 69.3097
FEATURE [TechDraw::DrawViewDimension] Dimension095
  AngleOverride = false
  Arbitrary = false
  ArbitraryTolerances = false
  EqualTolerance = true
  ExtensionAngle = 0
  FormatSpec = %.2w
  FormatSpecOverTolerance = %+.2w
  FormatSpecUnderTolerance = %+.2w
  Inverted = false
  LineAngle = 0
  LockPosition = false
  MeasureType = 1
  OverTolerance = 0
  References2D = -> [View002]
  Rotation = 0
  ScaleType = 0
  TheoreticalExact = false
  Type = 0
  UnderTolerance = 0
  X = 112.16
  Y = 96.8432
FEATURE [TechDraw::DrawViewDimension] Dimension096
  AngleOverride = false
  Arbitrary = false
  ArbitraryTolerances = false
  EqualTolerance = true
  ExtensionAngle = 0
  FormatSpec = R%.2w
  FormatSpecOverTolerance = %+.2w
  FormatSpecUnderTolerance = %+.2w
  Inverted = false
  LineAngle = 0
  LockPosition = false
  MeasureType = 1
  OverTolerance = 0
  References2D = -> [View002]
  Rotation = 0
  ScaleType = 0
  TheoreticalExact = false
  Type = 4
  UnderTolerance = 0
  X = 22.7159
  Y = -84.4565
FEATURE [TechDraw::DrawViewDimension] Dimension097
  AngleOverride = false
  Arbitrary = false
  ArbitraryTolerances = false
  EqualTolerance = true
  ExtensionAngle = 0
  FormatSpec = R%.2w
  FormatSpecOverTolerance = %+.2w
  FormatSpecUnderTolerance = %+.2w
  Inverted = false
  LineAngle = 0
  LockPosition = false
  MeasureType = 1
  OverTolerance = 0
  References2D = -> [View002]
  Rotation = 0
  ScaleType = 0
  TheoreticalExact = false
  Type = 4
  UnderTolerance = 0
  X = -76.802
  Y = -105.469
FEATURE [TechDraw::DrawViewBalloon] Balloon
  BubbleShape = 0
  EndType = 0
  EndTypeScale = 1
  KinkLength = 5
  LockPosition = false
  OriginX = -375.214
  OriginY = 130.279
  Rotation = 0
  ScaleType = 0
  ShapeScale = 1
  SourceView = -> View002
  Text = 1
  TextWrapLen = -1
  X = -333.388
  Y = 158.673
FEATURE [TechDraw::DrawViewBalloon] Balloon014
  BubbleShape = 1
  EndType = 0
  EndTypeScale = 1
  KinkLength = 5
  LockPosition = false
  OriginX = -111.165
  OriginY = -169.119
  Rotation = 0
  ScaleType = 0
  ShapeScale = 1
  SourceView = -> View002
  Text = 45.00 Depth
  TextWrapLen = -1
  X = -169.163
  Y = -142.32
FEATURE [TechDraw::DrawViewBalloon] Balloon015
  BubbleShape = 1
  EndType = 0
  EndTypeScale = 1
  KinkLength = 5
  LockPosition = false
  OriginX = -85.5155
  OriginY = -159.015
  Rotation = 0
  ScaleType = 0
  ShapeScale = 1
  SourceView = -> View002
  Text = 5.00 Depth
  TextWrapLen = -1
  X = -114.437
  Y = -141.253
FEATURE [TechDraw::DrawViewBalloon] Balloon016
  BubbleShape = 1
  EndType = 0
  EndTypeScale = 1
  KinkLength = 5
  LockPosition = false
  OriginX = -14.3968
  OriginY = -232.465
  Rotation = 0
  ScaleType = 0
  ShapeScale = 1
  SourceView = -> View002
  Text = 28.50 Depth
  TextWrapLen = -1
  X = 13.2422
  Y = -213.145
FEATURE [TechDraw::DrawViewBalloon] Balloon017
  BubbleShape = 1
  EndType = 0
  EndTypeScale = 1
  KinkLength = 5
  LockPosition = false
  OriginX = -47.0415
  OriginY = -199.821
  Rotation = 0
  ScaleType = 0
  ShapeScale = 1
  SourceView = -> View002
  Text = 3.00 Depth
  TextWrapLen = -1
  X = -17.1294
  Y = -182.059
FEATURE [TechDraw::DrawViewBalloon] Balloon018
  BubbleShape = 1
  EndType = 0
  EndTypeScale = 1
  KinkLength = 5
  LockPosition = false
  OriginX = 80.8167
  OriginY = -46.7018
  Rotation = 0
  ScaleType = 0
  ShapeScale = 1
  SourceView = -> View002
  Text = 3.00 Depth
  TextWrapLen = -1
  X = 136.511
  Y = -28.8136
FEATURE [TechDraw::DrawViewBalloon] Balloon019
  BubbleShape = 1
  EndType = 0
  EndTypeScale = 1
  KinkLength = 5
  LockPosition = false
  OriginX = 74.5987
  OriginY = -61.8582
  Rotation = 0
  ScaleType = 0
  ShapeScale = 1
  SourceView = -> View002
  Text = 20.00 Depth
  TextWrapLen = -1
  X = 150.889
  Y = -51.5753
FEATURE [TechDraw::DrawViewBalloon] Balloon020
  BubbleShape = 1
  EndType = 0
  EndTypeScale = 1
  KinkLength = 5
  LockPosition = false
  OriginX = 6.58902
  OriginY = -31.5453
  Rotation = 0
  ScaleType = 0
  ShapeScale = 1
  SourceView = -> View002
  Text = 39.00 Depth
  TextWrapLen = -1
  X = -2.88198
  Y = -15.2743
FEATURE [TechDraw::DrawViewBalloon] Balloon021
  BubbleShape = 1
  EndType = 0
  EndTypeScale = 1
  KinkLength = 5
  LockPosition = false
  OriginX = 0.759618
  OriginY = 15.4785
  Rotation = 0
  ScaleType = 0
  ShapeScale = 1
  SourceView = -> View002
  Text = 16.00 Depth
  TextWrapLen = -1
  X = 9.4353
  Y = 37.81
FEATURE [TechDraw::DrawViewBalloon] Balloon022
  BubbleShape = 1
  EndType = 0
  EndTypeScale = 1
  KinkLength = 5
  LockPosition = false
  OriginX = -49.7619
  OriginY = -7.83911
  Rotation = 0
  ScaleType = 0
  ShapeScale = 1
  SourceView = -> View002
  Text = 20.00 Depth
  TextWrapLen = -1
  X = -115.427
  Y = 9.36578
FEATURE [TechDraw::DrawViewDimension] Dimension101
  AngleOverride = false
  Arbitrary = false
  ArbitraryTolerances = false
  EqualTolerance = true
  ExtensionAngle = 0
  FormatSpec = %.2w
  FormatSpecOverTolerance = %+.2w
  FormatSpecUnderTolerance = %+.2w
  Inverted = false
  LineAngle = 0
  LockPosition = false
  MeasureType = 1
  OverTolerance = 0
  References2D = -> [View002]
  Rotation = 0
  ScaleType = 0
  TheoreticalExact = false
  Type = 2
  UnderTolerance = 0
  X = -68.148
  Y = 109.418
FEATURE [TechDraw::DrawViewDimension] Dimension102
  AngleOverride = false
  Arbitrary = false
  ArbitraryTolerances = false
  EqualTolerance = true
  ExtensionAngle = 0
  FormatSpec = R%.2w
  FormatSpecOverTolerance = %+.2w
  FormatSpecUnderTolerance = %+.2w
  Inverted = false
  LineAngle = 0
  LockPosition = false
  MeasureType = 1
  OverTolerance = 0
  References2D = -> [View002]
  Rotation = 0
  ScaleType = 0
  TheoreticalExact = false
  Type = 4
  UnderTolerance = 0
  X = -55.1705
  Y = 160.956
FEATURE [TechDraw::DrawViewDimension] Dimension103
  AngleOverride = false
  Arbitrary = false
  ArbitraryTolerances = false
  EqualTolerance = true
  ExtensionAngle = 0
  FormatSpec = %.2w
  FormatSpecOverTolerance = %+.2w
  FormatSpecUnderTolerance = %+.2w
  Inverted = false
  LineAngle = 0
  LockPosition = false
  MeasureType = 1
  OverTolerance = 0
  References2D = -> [View002]
  Rotation = 0
  ScaleType = 0
  TheoreticalExact = false
  Type = 1
  UnderTolerance = 0
  X = -38.6004
  Y = 155.939
FEATURE [TechDraw::DrawViewDimension] Dimension104
  AngleOverride = false
  Arbitrary = false
  ArbitraryTolerances = false
  EqualTolerance = true
  ExtensionAngle = 0
  FormatSpec = %.2w
  FormatSpecOverTolerance = %+.2w
  FormatSpecUnderTolerance = %+.2w
  Inverted = false
  LineAngle = 0
  LockPosition = false
  MeasureType = 1
  OverTolerance = 0
  References2D = -> [View002]
  Rotation = 0
  ScaleType = 0
  TheoreticalExact = false
  Type = 0
  UnderTolerance = 0
  X = -69.8086
  Y = 26.6319
FEATURE [TechDraw::DrawViewDimension] Dimension105
  AngleOverride = false
  Arbitrary = false
  ArbitraryTolerances = false
  EqualTolerance = true
  ExtensionAngle = 0
  FormatSpec = %.2w
  FormatSpecOverTolerance = %+.2w
  FormatSpecUnderTolerance = %+.2w
  Inverted = false
  LineAngle = 0
  LockPosition = false
  MeasureType = 1
  OverTolerance = 0
  References2D = -> [View002]
  Rotation = 0
  ScaleType = 0
  TheoreticalExact = false
  Type = 2
  UnderTolerance = 0
  X = -86.381
  Y = -34.2508
FEATURE [TechDraw::DrawViewDimension] Dimension106
  AngleOverride = false
  Arbitrary = false
  ArbitraryTolerances = false
  EqualTolerance = true
  ExtensionAngle = 0
  FormatSpec = R%.2w
  FormatSpecOverTolerance = %+.2w
  FormatSpecUnderTolerance = %+.2w
  Inverted = false
  LineAngle = 0
  LockPosition = false
  MeasureType = 1
  OverTolerance = 0
  References2D = -> [View002]
  Rotation = 0
  ScaleType = 0
  TheoreticalExact = false
  Type = 4
  UnderTolerance = 0
  X = -73.7636
  Y = -29.5505
FEATURE [TechDraw::DrawViewDimension] Dimension107
  AngleOverride = false
  Arbitrary = false
  ArbitraryTolerances = false
  EqualTolerance = true
  ExtensionAngle = 0
  FormatSpec = %.2w
  FormatSpecOverTolerance = %+.2w
  FormatSpecUnderTolerance = %+.2w
  Inverted = false
  LineAngle = 0
  LockPosition = false
  MeasureType = 1
  OverTolerance = 0
  References2D = -> [View002]
  Rotation = 0
  ScaleType = 0
  TheoreticalExact = false
  Type = 2
  UnderTolerance = 0
  X = -46.8872
  Y = -38.9757
FEATURE [TechDraw::DrawViewDimension] Dimension108
  AngleOverride = false
  Arbitrary = false
  ArbitraryTolerances = false
  EqualTolerance = true
  ExtensionAngle = 0
  FormatSpec = R%.2w
  FormatSpecOverTolerance = %+.2w
  FormatSpecUnderTolerance = %+.2w
  Inverted = false
  LineAngle = 0
  LockPosition = false
  MeasureType = 1
  OverTolerance = 0
  References2D = -> [View002]
  Rotation = 0
  ScaleType = 0
  TheoreticalExact = false
  Type = 4
  UnderTolerance = 0
  X = -32.9342
  Y = -16.4671
FEATURE [TechDraw::DrawViewDimension] Dimension109
  AngleOverride = false
  Arbitrary = false
  ArbitraryTolerances = false
  EqualTolerance = true
  ExtensionAngle = 0
  FormatSpec = %.2w
  FormatSpecOverTolerance = %+.2w
  FormatSpecUnderTolerance = %+.2w
  Inverted = false
  LineAngle = 0
  LockPosition = false
  MeasureType = 1
  OverTolerance = 0
  References2D = -> [View002]
  Rotation = 0
  ScaleType = 0
  TheoreticalExact = false
  Type = 0
  UnderTolerance = 0
  X = -45.4393
  Y = -5.23076
FEATURE [TechDraw::DrawViewDimension] Dimension110
  AngleOverride = false
  Arbitrary = false
  ArbitraryTolerances = false
  EqualTolerance = true
  ExtensionAngle = 0
  FormatSpec = R%.2w
  FormatSpecOverTolerance = %+.2w
  FormatSpecUnderTolerance = %+.2w
  Inverted = false
  LineAngle = 0
  LockPosition = false
  MeasureType = 1
  OverTolerance = 0
  References2D = -> [View002]
  Rotation = 0
  ScaleType = 0
  TheoreticalExact = false
  Type = 4
  UnderTolerance = 0
  X = -14.3174
  Y = 59.8264
FEATURE [TechDraw::DrawViewDimension] Dimension111
  AngleOverride = false
  Arbitrary = false
  ArbitraryTolerances = false
  EqualTolerance = true
  ExtensionAngle = 0
  FormatSpec = %.2w
  FormatSpecOverTolerance = %+.2w
  FormatSpecUnderTolerance = %+.2w
  Inverted = false
  LineAngle = 0
  LockPosition = false
  MeasureType = 1
  OverTolerance = 0
  References2D = -> [View002]
  Rotation = 0
  ScaleType = 0
  TheoreticalExact = false
  Type = 0
  UnderTolerance = 0
  X = -65.6652
  Y = -55.6608
FEATURE [TechDraw::DrawViewPart] View001
  CoarseView = false
  Direction = (0,0,1)
  Focus = 100
  HardHidden = false
  IsoCount = 0
  IsoHidden = false
  IsoVisible = false
  LockPosition = false
  Perspective = false
  Rotation = 0
  ScaleType = 0
  ScrubCount = 0
  SeamHidden = false
  SeamVisible = false
  SmoothHidden = false
  SmoothVisible = true
  Source = -> [Body001]
  X = 219.196
  XDirection = (1,0,0)
  Y = 293.45
FEATURE [TechDraw::DrawViewDimension] Dimension018
  AngleOverride = false
  Arbitrary = false
  ArbitraryTolerances = false
  EqualTolerance = true
  ExtensionAngle = 0
  FormatSpec = R%.2w
  FormatSpecOverTolerance = %+.2w
  FormatSpecUnderTolerance = %+.2w
  Inverted = false
  LineAngle = 0
  LockPosition = false
  MeasureType = 1
  OverTolerance = 0
  References2D = -> [View001]
  Rotation = 0
  ScaleType = 0
  TheoreticalExact = false
  Type = 4
  UnderTolerance = 0
  X = 36.7794
  Y = 245.043
FEATURE [TechDraw::DrawViewDimension] Dimension023
  AngleOverride = false
  Arbitrary = false
  ArbitraryTolerances = false
  EqualTolerance = true
  ExtensionAngle = 0
  FormatSpec = %.2w
  FormatSpecOverTolerance = %+.2w
  FormatSpecUnderTolerance = %+.2w
  Inverted = false
  LineAngle = 0
  LockPosition = false
  MeasureType = 1
  OverTolerance = 0
  References2D = -> [View001]
  Rotation = 0
  ScaleType = 0
  TheoreticalExact = false
  Type = 1
  UnderTolerance = 0
  X = -1.95115
  Y = 167.164
FEATURE [TechDraw::DrawViewDimension] Dimension019
  AngleOverride = false
  Arbitrary = false
  ArbitraryTolerances = false
  EqualTolerance = true
  ExtensionAngle = 0
  FormatSpec = %.2w
  FormatSpecOverTolerance = %+.2w
  FormatSpecUnderTolerance = %+.2w
  Inverted = false
  LineAngle = 0
  LockPosition = false
  MeasureType = 1
  OverTolerance = 0
  References2D = -> [View001]
  Rotation = 0
  ScaleType = 0
  TheoreticalExact = false
  Type = 0
  UnderTolerance = 0
  X = 78.2255
  Y = 182.08
FEATURE [TechDraw::DrawViewDimension] Dimension020
  AngleOverride = false
  Arbitrary = false
  ArbitraryTolerances = false
  EqualTolerance = true
  ExtensionAngle = 0
  FormatSpec = %.2w
  FormatSpecOverTolerance = %+.2w
  FormatSpecUnderTolerance = %+.2w
  Inverted = false
  LineAngle = 0
  LockPosition = false
  MeasureType = 1
  OverTolerance = 0
  References2D = -> [View001]
  Rotation = 0
  ScaleType = 0
  TheoreticalExact = false
  Type = 2
  UnderTolerance = 0
  X = -26.2914
  Y = 195.661
FEATURE [TechDraw::DrawViewDimension] Dimension031
  AngleOverride = false
  Arbitrary = false
  ArbitraryTolerances = false
  EqualTolerance = true
  ExtensionAngle = 0
  FormatSpec = %.2w
  FormatSpecOverTolerance = %+.2w
  FormatSpecUnderTolerance = %+.2w
  Inverted = false
  LineAngle = 0
  LockPosition = false
  MeasureType = 1
  OverTolerance = 0
  References2D = -> [View001]
  Rotation = 0
  ScaleType = 0
  TheoreticalExact = false
  Type = 1
  UnderTolerance = 0
  X = 101.176
  Y = -157.769
FEATURE [TechDraw::DrawViewDimension] Dimension017
  AngleOverride = false
  Arbitrary = false
  ArbitraryTolerances = false
  EqualTolerance = true
  ExtensionAngle = 0
  FormatSpec = %.2w
  FormatSpecOverTolerance = %+.2w
  FormatSpecUnderTolerance = %+.2w
  Inverted = false
  LineAngle = 0
  LockPosition = false
  MeasureType = 1
  OverTolerance = 0
  References2D = -> [View001]
  Rotation = 0
  ScaleType = 0
  TheoreticalExact = false
  Type = 0
  UnderTolerance = 0
  X = -15.797
  Y = 243.702
FEATURE [TechDraw::DrawViewDimension] Dimension016
  AngleOverride = false
  Arbitrary = false
  ArbitraryTolerances = false
  EqualTolerance = true
  ExtensionAngle = 0
  FormatSpec = %.2w
  FormatSpecOverTolerance = %+.2w
  FormatSpecUnderTolerance = %+.2w
  Inverted = false
  LineAngle = 0
  LockPosition = false
  MeasureType = 1
  OverTolerance = 0
  References2D = -> [View001]
  Rotation = 0
  ScaleType = 0
  TheoreticalExact = false
  Type = 0
  UnderTolerance = 0
  X = -83.2647
  Y = 256.644
FEATURE [TechDraw::DrawViewDimension] Dimension022
  AngleOverride = false
  Arbitrary = false
  ArbitraryTolerances = false
  EqualTolerance = true
  ExtensionAngle = 0
  FormatSpec = R%.2w
  FormatSpecOverTolerance = %+.2w
  FormatSpecUnderTolerance = %+.2w
  Inverted = false
  LineAngle = 0
  LockPosition = false
  MeasureType = 1
  OverTolerance = 0
  References2D = -> [View001]
  Rotation = 0
  ScaleType = 0
  TheoreticalExact = false
  Type = 4
  UnderTolerance = 0
  X = -16.4928
  Y = 186.019
FEATURE [TechDraw::DrawViewDimension] Dimension021
  AngleOverride = false
  Arbitrary = false
  ArbitraryTolerances = false
  EqualTolerance = true
  ExtensionAngle = 0
  FormatSpec = R%.2w
  FormatSpecOverTolerance = %+.2w
  FormatSpecUnderTolerance = %+.2w
  Inverted = false
  LineAngle = 0
  LockPosition = false
  MeasureType = 1
  OverTolerance = 0
  References2D = -> [View001]
  Rotation = 0
  ScaleType = 0
  TheoreticalExact = false
  Type = 4
  UnderTolerance = 0
  X = 1.4948
  Y = 181.458
FEATURE [TechDraw::DrawViewDimension] Dimension024
  AngleOverride = false
  Arbitrary = false
  ArbitraryTolerances = false
  EqualTolerance = true
  ExtensionAngle = 0
  FormatSpec = %.2w
  FormatSpecOverTolerance = %+.2w
  FormatSpecUnderTolerance = %+.2w
  Inverted = false
  LineAngle = 0
  LockPosition = false
  MeasureType = 1
  OverTolerance = 0
  References2D = -> [View001]
  Rotation = 0
  ScaleType = 0
  TheoreticalExact = false
  Type = 0
  UnderTolerance = 0
  X = 139.944
  Y = 135.955
FEATURE [TechDraw::DrawViewDimension] Dimension025
  AngleOverride = false
  Arbitrary = false
  ArbitraryTolerances = false
  EqualTolerance = true
  ExtensionAngle = 0
  FormatSpec = %.2w
  FormatSpecOverTolerance = %+.2w
  FormatSpecUnderTolerance = %+.2w
  Inverted = false
  LineAngle = 0
  LockPosition = false
  MeasureType = 1
  OverTolerance = 0
  References2D = -> [View001]
  Rotation = 0
  ScaleType = 0
  TheoreticalExact = false
  Type = 0
  UnderTolerance = 0
  X = 123.244
  Y = 78.2393
FEATURE [TechDraw::DrawViewDimension] Dimension026
  AngleOverride = false
  Arbitrary = false
  ArbitraryTolerances = false
  EqualTolerance = true
  ExtensionAngle = 0
  FormatSpec = %.2w
  FormatSpecOverTolerance = %+.2w
  FormatSpecUnderTolerance = %+.2w
  Inverted = false
  LineAngle = 0
  LockPosition = false
  MeasureType = 1
  OverTolerance = 0
  References2D = -> [View001]
  Rotation = 0
  ScaleType = 0
  TheoreticalExact = false
  Type = 0
  UnderTolerance = 0
  X = 147.459
  Y = -116.628
FEATURE [TechDraw::DrawViewDimension] Dimension027
  AngleOverride = false
  Arbitrary = false
  ArbitraryTolerances = false
  EqualTolerance = true
  ExtensionAngle = 0
  FormatSpec = %.2w
  FormatSpecOverTolerance = %+.2w
  FormatSpecUnderTolerance = %+.2w
  Inverted = false
  LineAngle = 0
  LockPosition = false
  MeasureType = 1
  OverTolerance = 0
  References2D = -> [View001]
  Rotation = 0
  ScaleType = 0
  TheoreticalExact = false
  Type = 2
  UnderTolerance = 0
  X = 73.6507
  Y = 25.793
FEATURE [TechDraw::DrawViewDimension] Dimension028
  AngleOverride = false
  Arbitrary = false
  ArbitraryTolerances = false
  EqualTolerance = true
  ExtensionAngle = 0
  FormatSpec = %.2w
  FormatSpecOverTolerance = %+.2w
  FormatSpecUnderTolerance = %+.2w
  Inverted = false
  LineAngle = 0
  LockPosition = false
  MeasureType = 1
  OverTolerance = 0
  References2D = -> [View001]
  Rotation = 0
  ScaleType = 0
  TheoreticalExact = false
  Type = 1
  UnderTolerance = 0
  X = 2.28928
  Y = -17.2912
FEATURE [TechDraw::DrawViewDimension] Dimension029
  AngleOverride = false
  Arbitrary = false
  ArbitraryTolerances = false
  EqualTolerance = true
  ExtensionAngle = 0
  FormatSpec = %.2w
  FormatSpecOverTolerance = %+.2w
  FormatSpecUnderTolerance = %+.2w
  Inverted = false
  LineAngle = 0
  LockPosition = false
  MeasureType = 1
  OverTolerance = 0
  References2D = -> [View001]
  Rotation = 0
  ScaleType = 0
  TheoreticalExact = false
  Type = 2
  UnderTolerance = 0
  X = -53.5768
  Y = -38.494
FEATURE [TechDraw::DrawViewDimension] Dimension
  AngleOverride = false
  Arbitrary = false
  ArbitraryTolerances = false
  EqualTolerance = true
  ExtensionAngle = 0
  FormatSpec = %.2w
  FormatSpecOverTolerance = %+.2w
  FormatSpecUnderTolerance = %+.2w
  Inverted = false
  LineAngle = 0
  LockPosition = false
  MeasureType = 1
  OverTolerance = 0
  References2D = -> [View001]
  Rotation = 0
  ScaleType = 0
  TheoreticalExact = false
  Type = 1
  UnderTolerance = 0
  X = -9.26566
  Y = -227.432
FEATURE [TechDraw::DrawViewDimension] Dimension002
  AngleOverride = false
  Arbitrary = false
  ArbitraryTolerances = false
  EqualTolerance = true
  ExtensionAngle = 0
  FormatSpec = %.2w
  FormatSpecOverTolerance = %+.2w
  FormatSpecUnderTolerance = %+.2w
  Inverted = false
  LineAngle = 0
  LockPosition = false
  MeasureType = 1
  OverTolerance = 0
  References2D = -> [View001]
  Rotation = 0
  ScaleType = 0
  TheoreticalExact = false
  Type = 0
  UnderTolerance = 0
  X = 75.9045
  Y = -250.896
FEATURE [TechDraw::DrawViewDimension] Dimension003
  AngleOverride = false
  Arbitrary = false
  ArbitraryTolerances = false
  EqualTolerance = true
  ExtensionAngle = 0
  FormatSpec = %.2w
  FormatSpecOverTolerance = %+.2w
  FormatSpecUnderTolerance = %+.2w
  Inverted = false
  LineAngle = 0
  LockPosition = false
  MeasureType = 1
  OverTolerance = 0
  References2D = -> [View001]
  Rotation = 0
  ScaleType = 0
  TheoreticalExact = false
  Type = 0
  UnderTolerance = 0
  X = 132.407
  Y = -262.503
FEATURE [TechDraw::DrawViewDimension] Dimension001
  AngleOverride = false
  Arbitrary = false
  ArbitraryTolerances = false
  EqualTolerance = true
  ExtensionAngle = 0
  FormatSpec = %.2w
  FormatSpecOverTolerance = %+.2w
  FormatSpecUnderTolerance = %+.2w
  Inverted = false
  LineAngle = 0
  LockPosition = false
  MeasureType = 1
  OverTolerance = 0
  References2D = -> [View001]
  Rotation = 0
  ScaleType = 0
  TheoreticalExact = false
  Type = 0
  UnderTolerance = 0
  X = -105.408
  Y = -198.458
FEATURE [TechDraw::DrawViewDimension] Dimension040
  AngleOverride = false
  Arbitrary = false
  ArbitraryTolerances = false
  EqualTolerance = true
  ExtensionAngle = 0
  FormatSpec = %.2w
  FormatSpecOverTolerance = %+.2w
  FormatSpecUnderTolerance = %+.2w
  Inverted = false
  LineAngle = 0
  LockPosition = false
  MeasureType = 1
  OverTolerance = 0
  References2D = -> [View001]
  Rotation = 0
  ScaleType = 0
  TheoreticalExact = false
  Type = 6
  UnderTolerance = 0
  X = 91.4609
  Y = -74.1657
FEATURE [TechDraw::DrawViewDimension] Dimension048
  AngleOverride = false
  Arbitrary = false
  ArbitraryTolerances = false
  EqualTolerance = true
  ExtensionAngle = 0
  FormatSpec = R%.2w
  FormatSpecOverTolerance = %+.2w
  FormatSpecUnderTolerance = %+.2w
  Inverted = false
  LineAngle = 0
  LockPosition = false
  MeasureType = 1
  OverTolerance = 0
  References2D = -> [View001]
  Rotation = 0
  ScaleType = 0
  TheoreticalExact = false
  Type = 4
  UnderTolerance = 0
  X = 45.7396
  Y = -17.4642
FEATURE [TechDraw::DrawViewDimension] Dimension039
  AngleOverride = false
  Arbitrary = false
  ArbitraryTolerances = false
  EqualTolerance = true
  ExtensionAngle = 0
  FormatSpec = %.2w
  FormatSpecOverTolerance = %+.2w
  FormatSpecUnderTolerance = %+.2w
  Inverted = false
  LineAngle = 0
  LockPosition = false
  MeasureType = 1
  OverTolerance = 0
  References2D = -> [View001]
  Rotation = 0
  ScaleType = 0
  TheoreticalExact = false
  Type = 1
  UnderTolerance = 0
  X = 94.4902
  Y = -133.399
FEATURE [TechDraw::DrawViewDimension] Dimension009
  AngleOverride = false
  Arbitrary = false
  ArbitraryTolerances = false
  EqualTolerance = true
  ExtensionAngle = 0
  FormatSpec = %.2w
  FormatSpecOverTolerance = %+.2w
  FormatSpecUnderTolerance = %+.2w
  Inverted = false
  LineAngle = 0
  LockPosition = false
  MeasureType = 1
  OverTolerance = 0
  References2D = -> [View001]
  Rotation = 0
  ScaleType = 0
  TheoreticalExact = false
  Type = 0
  UnderTolerance = 0
  X = -3.71754
  Y = 54.9901
FEATURE [TechDraw::DrawViewDimension] Dimension041
  AngleOverride = false
  Arbitrary = false
  ArbitraryTolerances = false
  EqualTolerance = true
  ExtensionAngle = 0
  FormatSpec = %.2w
  FormatSpecOverTolerance = %+.2w
  FormatSpecUnderTolerance = %+.2w
  Inverted = false
  LineAngle = 0
  LockPosition = false
  MeasureType = 1
  OverTolerance = 0
  References2D = -> [View001]
  Rotation = 0
  ScaleType = 0
  TheoreticalExact = false
  Type = 6
  UnderTolerance = 0
  X = 69.3611
  Y = -69.7115
FEATURE [TechDraw::DrawViewDimension] Dimension004
  AngleOverride = false
  Arbitrary = false
  ArbitraryTolerances = false
  EqualTolerance = true
  ExtensionAngle = 0
  FormatSpec = ⌀%.2w
  FormatSpecOverTolerance = %+.2w
  FormatSpecUnderTolerance = %+.2w
  Inverted = false
  LineAngle = 0
  LockPosition = false
  MeasureType = 1
  OverTolerance = 0
  References2D = -> [View001]
  Rotation = 0
  ScaleType = 0
  TheoreticalExact = false
  Type = 5
  UnderTolerance = 0
  X = 11.6478
  Y = -172.579
FEATURE [TechDraw::DrawViewDimension] Dimension015
  AngleOverride = false
  Arbitrary = false
  ArbitraryTolerances = false
  EqualTolerance = true
  ExtensionAngle = 0
  FormatSpec = %.2w
  FormatSpecOverTolerance = %+.2w
  FormatSpecUnderTolerance = %+.2w
  Inverted = false
  LineAngle = 0
  LockPosition = false
  MeasureType = 1
  OverTolerance = 0
  References2D = -> [View001]
  Rotation = 0
  ScaleType = 0
  TheoreticalExact = false
  Type = 0
  UnderTolerance = 0
  X = -169.237
  Y = 255.205
FEATURE [TechDraw::DrawViewDimension] Dimension113
  AngleOverride = false
  Arbitrary = false
  ArbitraryTolerances = false
  EqualTolerance = true
  ExtensionAngle = 0
  FormatSpec = %.2w
  FormatSpecOverTolerance = %+.2w
  FormatSpecUnderTolerance = %+.2w
  Inverted = false
  LineAngle = 0
  LockPosition = false
  MeasureType = 1
  OverTolerance = 0
  References2D = -> [View001]
  Rotation = 0
  ScaleType = 0
  TheoreticalExact = false
  Type = 2
  UnderTolerance = 0
  X = -55.087
  Y = 59.8
FEATURE [TechDraw::DrawViewDimension] Dimension112
  AngleOverride = false
  Arbitrary = false
  ArbitraryTolerances = false
  EqualTolerance = true
  ExtensionAngle = 0
  FormatSpec = %.2w
  FormatSpecOverTolerance = %+.2w
  FormatSpecUnderTolerance = %+.2w
  Inverted = false
  LineAngle = 0
  LockPosition = false
  MeasureType = 1
  OverTolerance = 0
  References2D = -> [View001]
  Rotation = 0
  ScaleType = 0
  TheoreticalExact = false
  Type = 2
  UnderTolerance = 0
  X = -52.6591
  Y = -9.47957
FEATURE [TechDraw::DrawViewDimension] Dimension117
  AngleOverride = false
  Arbitrary = false
  ArbitraryTolerances = false
  EqualTolerance = true
  ExtensionAngle = 0
  FormatSpec = %.2w
  FormatSpecOverTolerance = %+.2w
  FormatSpecUnderTolerance = %+.2w
  Inverted = false
  LineAngle = 0
  LockPosition = false
  MeasureType = 1
  OverTolerance = 0
  References2D = -> [View001]
  Rotation = 0
  ScaleType = 0
  TheoreticalExact = false
  Type = 2
  UnderTolerance = 0
  X = -56.9325
  Y = 152.925
FEATURE [TechDraw::DrawViewDimension] Dimension114
  AngleOverride = false
  Arbitrary = false
  ArbitraryTolerances = false
  EqualTolerance = true
  ExtensionAngle = 0
  FormatSpec = %.2w
  FormatSpecOverTolerance = %+.2w
  FormatSpecUnderTolerance = %+.2w
  Inverted = false
  LineAngle = 0
  LockPosition = false
  MeasureType = 1
  OverTolerance = 0
  References2D = -> [View001]
  Rotation = 0
  ScaleType = 0
  TheoreticalExact = false
  Type = 2
  UnderTolerance = 0
  X = -56.6046
  Y = 92.5818
FEATURE [TechDraw::DrawViewDimension] Dimension116
  AngleOverride = false
  Arbitrary = false
  ArbitraryTolerances = false
  EqualTolerance = true
  ExtensionAngle = 0
  FormatSpec = %.2w
  FormatSpecOverTolerance = %+.2w
  FormatSpecUnderTolerance = %+.2w
  Inverted = false
  LineAngle = 0
  LockPosition = false
  MeasureType = 1
  OverTolerance = 0
  References2D = -> [View001]
  Rotation = 0
  ScaleType = 0
  TheoreticalExact = false
  Type = 2
  UnderTolerance = 0
  X = -56.6358
  Y = 120.444
FEATURE [TechDraw::DrawViewDimension] Dimension115
  AngleOverride = false
  Arbitrary = false
  ArbitraryTolerances = false
  EqualTolerance = true
  ExtensionAngle = 0
  FormatSpec = %.2w
  FormatSpecOverTolerance = %+.2w
  FormatSpecUnderTolerance = %+.2w
  Inverted = false
  LineAngle = 0
  LockPosition = false
  MeasureType = 1
  OverTolerance = 0
  References2D = -> [View001]
  Rotation = 0
  ScaleType = 0
  TheoreticalExact = false
  Type = 2
  UnderTolerance = 0
  X = 45.803
  Y = 138.401
FEATURE [TechDraw::DrawViewDimension] Dimension118
  AngleOverride = false
  Arbitrary = false
  ArbitraryTolerances = false
  EqualTolerance = true
  ExtensionAngle = 0
  FormatSpec = %.2w
  FormatSpecOverTolerance = %+.2w
  FormatSpecUnderTolerance = %+.2w
  Inverted = false
  LineAngle = 0
  LockPosition = false
  MeasureType = 1
  OverTolerance = 0
  References2D = -> [View001]
  Rotation = 0
  ScaleType = 0
  TheoreticalExact = false
  Type = 2
  UnderTolerance = 0
  X = -76.1516
  Y = 54.3934
FEATURE [TechDraw::DrawViewDimension] Dimension124
  AngleOverride = false
  Arbitrary = false
  ArbitraryTolerances = false
  EqualTolerance = true
  ExtensionAngle = 0
  FormatSpec = %.2w
  FormatSpecOverTolerance = %+.2w
  FormatSpecUnderTolerance = %+.2w
  Inverted = false
  LineAngle = 0
  LockPosition = false
  MeasureType = 1
  OverTolerance = 0
  References2D = -> [View001]
  Rotation = 0
  ScaleType = 0
  TheoreticalExact = false
  Type = 2
  UnderTolerance = 0
  X = -48.7447
  Y = 186.913
FEATURE [TechDraw::DrawViewDimension] Dimension121
  AngleOverride = false
  Arbitrary = false
  ArbitraryTolerances = false
  EqualTolerance = true
  ExtensionAngle = 0
  FormatSpec = %.2w
  FormatSpecOverTolerance = %+.2w
  FormatSpecUnderTolerance = %+.2w
  Inverted = false
  LineAngle = 0
  LockPosition = false
  MeasureType = 1
  OverTolerance = 0
  References2D = -> [View001]
  Rotation = 0
  ScaleType = 0
  TheoreticalExact = false
  Type = 1
  UnderTolerance = 0
  X = -9.91741
  Y = 94.0913
FEATURE [TechDraw::DrawViewDimension] Dimension122
  AngleOverride = false
  Arbitrary = false
  ArbitraryTolerances = false
  EqualTolerance = true
  ExtensionAngle = 0
  FormatSpec = %.2w
  FormatSpecOverTolerance = %+.2w
  FormatSpecUnderTolerance = %+.2w
  Inverted = false
  LineAngle = 0
  LockPosition = false
  MeasureType = 1
  OverTolerance = 0
  References2D = -> [View001]
  Rotation = 0
  ScaleType = 0
  TheoreticalExact = false
  Type = 1
  UnderTolerance = 0
  X = -11.4176
  Y = 124.364
FEATURE [TechDraw::DrawViewDimension] Dimension123
  AngleOverride = false
  Arbitrary = false
  ArbitraryTolerances = false
  EqualTolerance = true
  ExtensionAngle = 0
  FormatSpec = R%.2w
  FormatSpecOverTolerance = %+.2w
  FormatSpecUnderTolerance = %+.2w
  Inverted = false
  LineAngle = 0
  LockPosition = false
  MeasureType = 1
  OverTolerance = 0
  References2D = -> [View001]
  Rotation = 0
  ScaleType = 0
  TheoreticalExact = false
  Type = 4
  UnderTolerance = 0
  X = -32.0499
  Y = 139.994
FEATURE [TechDraw::DrawViewDimension] Dimension119
  AngleOverride = false
  Arbitrary = false
  ArbitraryTolerances = false
  EqualTolerance = true
  ExtensionAngle = 0
  FormatSpec = %.2w
  FormatSpecOverTolerance = %+.2w
  FormatSpecUnderTolerance = %+.2w
  Inverted = false
  LineAngle = 0
  LockPosition = false
  MeasureType = 1
  OverTolerance = 0
  References2D = -> [View001]
  Rotation = 0
  ScaleType = 0
  TheoreticalExact = false
  Type = 2
  UnderTolerance = 0
  X = 58.6837
  Y = 109.054
FEATURE [TechDraw::DrawViewDimension] Dimension120
  AngleOverride = false
  Arbitrary = false
  ArbitraryTolerances = false
  EqualTolerance = true
  ExtensionAngle = 0
  FormatSpec = %.2w
  FormatSpecOverTolerance = %+.2w
  FormatSpecUnderTolerance = %+.2w
  Inverted = false
  LineAngle = 0
  LockPosition = false
  MeasureType = 1
  OverTolerance = 0
  References2D = -> [View001]
  Rotation = 0
  ScaleType = 0
  TheoreticalExact = false
  Type = 2
  UnderTolerance = 0
  X = 49.9227
  Y = 108.293
FEATURE [TechDraw::DrawViewDimension] Dimension125
  AngleOverride = false
  Arbitrary = false
  ArbitraryTolerances = false
  EqualTolerance = true
  ExtensionAngle = 0
  FormatSpec = %.2w
  FormatSpecOverTolerance = %+.2w
  FormatSpecUnderTolerance = %+.2w
  Inverted = false
  LineAngle = 0
  LockPosition = false
  MeasureType = 1
  OverTolerance = 0
  References2D = -> [View001]
  Rotation = 0
  ScaleType = 0
  TheoreticalExact = false
  Type = 1
  UnderTolerance = 0
  X = -45.0442
  Y = 169.569
FEATURE [TechDraw::DrawViewDimension] Dimension007
  AngleOverride = false
  Arbitrary = false
  ArbitraryTolerances = false
  EqualTolerance = true
  ExtensionAngle = 0
  FormatSpec = %.2w
  FormatSpecOverTolerance = %+.2w
  FormatSpecUnderTolerance = %+.2w
  Inverted = false
  LineAngle = 0
  LockPosition = false
  MeasureType = 1
  OverTolerance = 0
  References2D = -> [View001]
  Rotation = 0
  ScaleType = 0
  TheoreticalExact = false
  Type = 0
  UnderTolerance = 0
  X = -86.9213
  Y = 25.8946
FEATURE [TechDraw::DrawViewDimension] Dimension005
  AngleOverride = false
  Arbitrary = false
  ArbitraryTolerances = false
  EqualTolerance = true
  ExtensionAngle = 0
  FormatSpec = %.2w
  FormatSpecOverTolerance = %+.2w
  FormatSpecUnderTolerance = %+.2w
  Inverted = false
  LineAngle = 0
  LockPosition = false
  MeasureType = 1
  OverTolerance = 0
  References2D = -> [View001]
  Rotation = 0
  ScaleType = 0
  TheoreticalExact = false
  Type = 0
  UnderTolerance = 0
  X = -155.978
  Y = -77.3776
FEATURE [TechDraw::DrawViewDimension] Dimension014
  AngleOverride = false
  Arbitrary = false
  ArbitraryTolerances = false
  EqualTolerance = true
  ExtensionAngle = 0
  FormatSpec = %.2w
  FormatSpecOverTolerance = %+.2w
  FormatSpecUnderTolerance = %+.2w
  Inverted = false
  LineAngle = 0
  LockPosition = false
  MeasureType = 1
  OverTolerance = 0
  References2D = -> [View001]
  Rotation = 0
  ScaleType = 0
  TheoreticalExact = false
  Type = 0
  UnderTolerance = 0
  X = -187.432
  Y = 139.993
FEATURE [TechDraw::DrawViewDimension] Dimension010
  AngleOverride = false
  Arbitrary = false
  ArbitraryTolerances = false
  EqualTolerance = true
  ExtensionAngle = 0
  FormatSpec = R%.2w
  FormatSpecOverTolerance = %+.2w
  FormatSpecUnderTolerance = %+.2w
  Inverted = false
  LineAngle = 0
  LockPosition = false
  MeasureType = 1
  OverTolerance = 0
  References2D = -> [View001]
  Rotation = 0
  ScaleType = 0
  TheoreticalExact = false
  Type = 4
  UnderTolerance = 0
  X = -25.2827
  Y = 37.7695
FEATURE [TechDraw::DrawViewDimension] Dimension006
  AngleOverride = false
  Arbitrary = false
  ArbitraryTolerances = false
  EqualTolerance = true
  ExtensionAngle = 0
  FormatSpec = %.2w
  FormatSpecOverTolerance = %+.2w
  FormatSpecUnderTolerance = %+.2w
  Inverted = false
  LineAngle = 0
  LockPosition = false
  MeasureType = 1
  OverTolerance = 0
  References2D = -> [View001]
  Rotation = 0
  ScaleType = 0
  TheoreticalExact = false
  Type = 0
  UnderTolerance = 0
  X = -80.9946
  Y = -0.130127
FEATURE [TechDraw::DrawViewDimension] Dimension011
  AngleOverride = false
  Arbitrary = false
  ArbitraryTolerances = false
  EqualTolerance = true
  ExtensionAngle = 0
  FormatSpec = %.2w
  FormatSpecOverTolerance = %+.2w
  FormatSpecUnderTolerance = %+.2w
  Inverted = false
  LineAngle = 0
  LockPosition = false
  MeasureType = 1
  OverTolerance = 0
  References2D = -> [View001]
  Rotation = 0
  ScaleType = 0
  TheoreticalExact = false
  Type = 2
  UnderTolerance = 0
  X = 60.4724
  Y = 26.4979
FEATURE [TechDraw::DrawViewDimension] Dimension008
  AngleOverride = false
  Arbitrary = false
  ArbitraryTolerances = false
  EqualTolerance = true
  ExtensionAngle = 0
  FormatSpec = %.2w
  FormatSpecOverTolerance = %+.2w
  FormatSpecUnderTolerance = %+.2w
  Inverted = false
  LineAngle = 0
  LockPosition = false
  MeasureType = 1
  OverTolerance = 0
  References2D = -> [View001]
  Rotation = 0
  ScaleType = 0
  TheoreticalExact = false
  Type = 0
  UnderTolerance = 0
  X = -105.07
  Y = 47.1323
FEATURE [TechDraw::DrawViewDimension] Dimension012
  AngleOverride = false
  Arbitrary = false
  ArbitraryTolerances = false
  EqualTolerance = true
  ExtensionAngle = 0
  FormatSpec = %.2w
  FormatSpecOverTolerance = %+.2w
  FormatSpecUnderTolerance = %+.2w
  Inverted = false
  LineAngle = 0
  LockPosition = false
  MeasureType = 1
  OverTolerance = 0
  References2D = -> [View001]
  Rotation = 0
  ScaleType = 0
  TheoreticalExact = false
  Type = 0
  UnderTolerance = 0
  X = -122.324
  Y = 60.9403
FEATURE [TechDraw::DrawViewDimension] Dimension013
  AngleOverride = false
  Arbitrary = false
  ArbitraryTolerances = false
  EqualTolerance = true
  ExtensionAngle = 0
  FormatSpec = %.2w
  FormatSpecOverTolerance = %+.2w
  FormatSpecUnderTolerance = %+.2w
  Inverted = false
  LineAngle = 0
  LockPosition = false
  MeasureType = 1
  OverTolerance = 0
  References2D = -> [View001]
  Rotation = 0
  ScaleType = 0
  TheoreticalExact = false
  Type = 0
  UnderTolerance = 0
  X = -152.905
  Y = 48.6526
FEATURE [TechDraw::DrawViewDimension] Dimension035
  AngleOverride = false
  Arbitrary = false
  ArbitraryTolerances = false
  EqualTolerance = true
  ExtensionAngle = 0
  FormatSpec = %.2w
  FormatSpecOverTolerance = %+.2w
  FormatSpecUnderTolerance = %+.2w
  Inverted = false
  LineAngle = 0
  LockPosition = false
  MeasureType = 1
  OverTolerance = 0
  References2D = -> [View001]
  Rotation = 0
  ScaleType = 0
  TheoreticalExact = false
  Type = 2
  UnderTolerance = 0
  X = 36.3076
  Y = -100.551
FEATURE [TechDraw::DrawViewDimension] Dimension034
  AngleOverride = false
  Arbitrary = false
  ArbitraryTolerances = false
  EqualTolerance = true
  ExtensionAngle = 0
  FormatSpec = R%.2w
  FormatSpecOverTolerance = %+.2w
  FormatSpecUnderTolerance = %+.2w
  Inverted = false
  LineAngle = 0
  LockPosition = false
  MeasureType = 1
  OverTolerance = 0
  References2D = -> [View001]
  Rotation = 0
  ScaleType = 0
  TheoreticalExact = false
  Type = 4
  UnderTolerance = 0
  X = 39.3517
  Y = -145.082
FEATURE [TechDraw::DrawViewDimension] Dimension032
  AngleOverride = false
  Arbitrary = false
  ArbitraryTolerances = false
  EqualTolerance = true
  ExtensionAngle = 0
  FormatSpec = %.2w
  FormatSpecOverTolerance = %+.2w
  FormatSpecUnderTolerance = %+.2w
  Inverted = false
  LineAngle = 0
  LockPosition = false
  MeasureType = 1
  OverTolerance = 0
  References2D = -> [View001]
  Rotation = 0
  ScaleType = 0
  TheoreticalExact = false
  Type = 2
  UnderTolerance = 0
  X = 38.0406
  Y = -190.294
FEATURE [TechDraw::DrawViewDimension] Dimension036
  AngleOverride = false
  Arbitrary = false
  ArbitraryTolerances = false
  EqualTolerance = true
  ExtensionAngle = 0
  FormatSpec = %.2w
  FormatSpecOverTolerance = %+.2w
  FormatSpecUnderTolerance = %+.2w
  Inverted = false
  LineAngle = 0
  LockPosition = false
  MeasureType = 1
  OverTolerance = 0
  References2D = -> [View001]
  Rotation = 0
  ScaleType = 0
  TheoreticalExact = false
  Type = 1
  UnderTolerance = 0
  X = 81.8808
  Y = -35.2647
FEATURE [TechDraw::DrawViewDimension] Dimension033
  AngleOverride = false
  Arbitrary = false
  ArbitraryTolerances = false
  EqualTolerance = true
  ExtensionAngle = 0
  FormatSpec = R%.2w
  FormatSpecOverTolerance = %+.2w
  FormatSpecUnderTolerance = %+.2w
  Inverted = false
  LineAngle = 0
  LockPosition = false
  MeasureType = 1
  OverTolerance = 0
  References2D = -> [View001]
  Rotation = 0
  ScaleType = 0
  TheoreticalExact = false
  Type = 4
  UnderTolerance = 0
  X = 149.374
  Y = -237.522
FEATURE [TechDraw::DrawViewDimension] Dimension037
  AngleOverride = false
  Arbitrary = false
  ArbitraryTolerances = false
  EqualTolerance = true
  ExtensionAngle = 0
  FormatSpec = R%.2w
  FormatSpecOverTolerance = %+.2w
  FormatSpecUnderTolerance = %+.2w
  Inverted = false
  LineAngle = 0
  LockPosition = false
  MeasureType = 1
  OverTolerance = 0
  References2D = -> [View001]
  Rotation = 0
  ScaleType = 0
  TheoreticalExact = false
  Type = 4
  UnderTolerance = 0
  X = 81.8952
  Y = -79.7319
FEATURE [TechDraw::DrawViewDimension] Dimension038
  AngleOverride = false
  Arbitrary = false
  ArbitraryTolerances = false
  EqualTolerance = true
  ExtensionAngle = 0
  FormatSpec = %.2w
  FormatSpecOverTolerance = %+.2w
  FormatSpecUnderTolerance = %+.2w
  Inverted = false
  LineAngle = 0
  LockPosition = false
  MeasureType = 1
  OverTolerance = 0
  References2D = -> [View001]
  Rotation = 0
  ScaleType = 0
  TheoreticalExact = false
  Type = 1
  UnderTolerance = 0
  X = 82.4561
  Y = -45.6884
FEATURE [TechDraw::DrawViewDimension] Dimension047
  AngleOverride = false
  Arbitrary = false
  ArbitraryTolerances = false
  EqualTolerance = true
  ExtensionAngle = 0
  FormatSpec = %.2w
  FormatSpecOverTolerance = %+.2w
  FormatSpecUnderTolerance = %+.2w
  Inverted = false
  LineAngle = 0
  LockPosition = false
  MeasureType = 1
  OverTolerance = 0
  References2D = -> [View001]
  Rotation = 0
  ScaleType = 0
  TheoreticalExact = false
  Type = 2
  UnderTolerance = 0
  X = -93.3848
  Y = 139.296
FEATURE [TechDraw::DrawViewDimension] Dimension044
  AngleOverride = false
  Arbitrary = false
  ArbitraryTolerances = false
  EqualTolerance = true
  ExtensionAngle = 0
  FormatSpec = %.2w
  FormatSpecOverTolerance = %+.2w
  FormatSpecUnderTolerance = %+.2w
  Inverted = false
  LineAngle = 0
  LockPosition = false
  MeasureType = 1
  OverTolerance = 0
  References2D = -> [View001]
  Rotation = 0
  ScaleType = 0
  TheoreticalExact = false
  Type = 1
  UnderTolerance = 0
  X = 93.1207
  Y = -141.717
FEATURE [TechDraw::DrawViewDimension] Dimension043
  AngleOverride = false
  Arbitrary = false
  ArbitraryTolerances = false
  EqualTolerance = true
  ExtensionAngle = 0
  FormatSpec = %.2w
  FormatSpecOverTolerance = %+.2w
  FormatSpecUnderTolerance = %+.2w
  Inverted = false
  LineAngle = 0
  LockPosition = false
  MeasureType = 1
  OverTolerance = 0
  References2D = -> [View001]
  Rotation = 0
  ScaleType = 0
  TheoreticalExact = false
  Type = 6
  UnderTolerance = 0
  X = 108.253
  Y = -121.905
FEATURE [TechDraw::DrawViewDimension] Dimension045
  AngleOverride = false
  Arbitrary = false
  ArbitraryTolerances = false
  EqualTolerance = true
  ExtensionAngle = 0
  FormatSpec = %.2w
  FormatSpecOverTolerance = %+.2w
  FormatSpecUnderTolerance = %+.2w
  Inverted = false
  LineAngle = 0
  LockPosition = false
  MeasureType = 1
  OverTolerance = 0
  References2D = -> [View001]
  Rotation = 0
  ScaleType = 0
  TheoreticalExact = false
  Type = 1
  UnderTolerance = 0
  X = -116.024
  Y = 213.306
FEATURE [TechDraw::DrawViewDimension] Dimension042
  AngleOverride = false
  Arbitrary = false
  ArbitraryTolerances = false
  EqualTolerance = true
  ExtensionAngle = 0
  FormatSpec = %.2w
  FormatSpecOverTolerance = %+.2w
  FormatSpecUnderTolerance = %+.2w
  Inverted = false
  LineAngle = 0
  LockPosition = false
  MeasureType = 1
  OverTolerance = 0
  References2D = -> [View001]
  Rotation = 0
  ScaleType = 0
  TheoreticalExact = false
  Type = 6
  UnderTolerance = 0
  X = 70.4503
  Y = -115.375
FEATURE [TechDraw::DrawViewDimension] Dimension046
  AngleOverride = false
  Arbitrary = false
  ArbitraryTolerances = false
  EqualTolerance = true
  ExtensionAngle = 0
  FormatSpec = %.2w
  FormatSpecOverTolerance = %+.2w
  FormatSpecUnderTolerance = %+.2w
  Inverted = false
  LineAngle = 0
  LockPosition = false
  MeasureType = 1
  OverTolerance = 0
  References2D = -> [View001]
  Rotation = 0
  ScaleType = 0
  TheoreticalExact = false
  Type = 2
  UnderTolerance = 0
  X = -82.5821
  Y = 137.667
FEATURE [TechDraw::DrawViewBalloon] Balloon012
  BubbleShape = 1
  EndType = 0
  EndTypeScale = 1
  KinkLength = 5
  LockPosition = false
  OriginX = 144.797
  OriginY = -191.292
  Rotation = 0
  ScaleType = 0
  ShapeScale = 1
  SourceView = -> View001
  Text = 2.00 Depth
  TextWrapLen = -1
  X = 178.546
  Y = -159.781
FEATURE [TechDraw::DrawViewBalloon] Balloon006
  BubbleShape = 1
  EndType = 0
  EndTypeScale = 1
  KinkLength = 5
  LockPosition = false
  OriginX = 34.4273
  OriginY = 72.5855
  Rotation = 0
  ScaleType = 0
  ShapeScale = 1
  SourceView = -> View001
  Text = 25.00 Depth
  TextWrapLen = -1
  X = 67.5406
  Y = 75.2857
FEATURE [TechDraw::DrawViewBalloon] Balloon011
  BubbleShape = 1
  EndType = 0
  EndTypeScale = 1
  KinkLength = 5
  LockPosition = false
  OriginX = 106.712
  OriginY = -109.292
  Rotation = 0
  ScaleType = 0
  ShapeScale = 1
  SourceView = -> View001
  Text = 36.00 Depth
  TextWrapLen = -1
  X = 160.077
  Y = -88.7459
FEATURE [TechDraw::DrawViewBalloon] Balloon003
  BubbleShape = 1
  EndType = 0
  EndTypeScale = 1
  KinkLength = 5
  LockPosition = false
  OriginX = -109.442
  OriginY = 146.829
  Rotation = 0
  ScaleType = 0
  ShapeScale = 1
  SourceView = -> View001
  Text = 45.00 Depth
  TextWrapLen = -1
  X = -138.811
  Y = 162.736
FEATURE [TechDraw::DrawViewBalloon] Balloon010
  BubbleShape = 1
  EndType = 0
  EndTypeScale = 1
  KinkLength = 5
  LockPosition = false
  OriginX = 113.319
  OriginY = -87.1402
  Rotation = 0
  ScaleType = 0
  ShapeScale = 1
  SourceView = -> View001
  Text = 3.00 Depth
  TextWrapLen = -1
  X = 150.295
  Y = -66.1809
FEATURE [TechDraw::DrawViewBalloon] Balloon005
  BubbleShape = 1
  EndType = 0
  EndTypeScale = 1
  KinkLength = 5
  LockPosition = false
  OriginX = 2.94854
  OriginY = 104.064
  Rotation = 0
  ScaleType = 0
  ShapeScale = 1
  SourceView = -> View001
  Text = 22.00 Depth
  TextWrapLen = -1
  X = 64.1943
  Y = 89.7636
FEATURE [TechDraw::DrawViewBalloon] Balloon004
  BubbleShape = 1
  EndType = 0
  EndTypeScale = 1
  KinkLength = 5
  LockPosition = false
  OriginX = 41.034
  OriginY = 105.619
  Rotation = 0
  ScaleType = 0
  ShapeScale = 1
  SourceView = -> View001
  Text = 1.50 Depth
  TextWrapLen = -1
  X = 77.908
  Y = 122.101
FEATURE [TechDraw::DrawViewBalloon] Balloon007
  BubbleShape = 1
  EndType = 0
  EndTypeScale = 1
  KinkLength = 5
  LockPosition = false
  OriginX = 14.2187
  OriginY = 30.6138
  Rotation = 0
  ScaleType = 0
  ShapeScale = 1
  SourceView = -> View001
  Text = 24.00 Depth
  TextWrapLen = -1
  X = 45.1003
  Y = 55.6659
FEATURE [TechDraw::DrawViewBalloon] Balloon008
  BubbleShape = 1
  EndType = 0
  EndTypeScale = 1
  KinkLength = 5
  LockPosition = false
  OriginX = 33.6501
  OriginY = 19.3436
  Rotation = 0
  ScaleType = 0
  ShapeScale = 1
  SourceView = -> View001
  Text = 25.00 Depth
  TextWrapLen = -1
  X = 72.1992
  Y = 47.2886
FEATURE [TechDraw::DrawViewBalloon] Balloon009
  BubbleShape = 1
  EndType = 0
  EndTypeScale = 1
  KinkLength = 5
  LockPosition = false
  OriginX = -12.2079
  OriginY = -44.3912
  Rotation = 0
  ScaleType = 0
  ShapeScale = 1
  SourceView = -> View001
  Text = 6.00 Depth
  TextWrapLen = -1
  X = -30.4542
  Y = -15.2773
FEATURE [TechDraw::DrawViewBalloon] Balloon013
  BubbleShape = 1
  EndType = 0
  EndTypeScale = 1
  KinkLength = 5
  LockPosition = false
  OriginX = 137.025
  OriginY = -221.994
  Rotation = 0
  ScaleType = 0
  ShapeScale = 1
  SourceView = -> View001
  Text = 3.00 Depth
  TextWrapLen = -1
  X = 188.448
  Y = -193.563
FEATURE [TechDraw::DrawViewBalloon] Balloon001
  BubbleShape = 1
  EndType = 0
  EndTypeScale = 1
  KinkLength = 5
  LockPosition = false
  OriginX = 14.2343
  OriginY = 201.112
  Rotation = 0
  ScaleType = 0
  ShapeScale = 1
  SourceView = -> View001
  Text = 20.00 Depth
  TextWrapLen = -1
  X = 54.2355
  Y = 215.452
FEATURE [TechDraw::DrawViewBalloon] Balloon002
  BubbleShape = 1
  EndType = 0
  EndTypeScale = 1
  KinkLength = 5
  LockPosition = false
  OriginX = -84.8189
  OriginY = 193.837
  Rotation = 0
  ScaleType = 0
  ShapeScale = 1
  SourceView = -> View001
  Text = 5.00 Depth
  TextWrapLen = -1
  X = -51.3891
  Y = 208.912
FEATURE [TechDraw::DrawViewBalloon] Balloon023
  BubbleShape = 1
  EndType = 0
  EndTypeScale = 1
  KinkLength = 5
  LockPosition = false
  OriginX = 15.9839
  OriginY = 137.047
  Rotation = 0
  ScaleType = 0
  ShapeScale = 1
  SourceView = -> View001
  Text = 24.00 Depth
  TextWrapLen = -1
  X = 55.9158
  Y = 154.873
FEATURE [TechDraw::DrawViewDimension] Dimension126
  AngleOverride = false
  Arbitrary = false
  ArbitraryTolerances = false
  EqualTolerance = true
  ExtensionAngle = 0
  FormatSpec = ⌀%.2w
  FormatSpecOverTolerance = %+.2w
  FormatSpecUnderTolerance = %+.2w
  Inverted = false
  LineAngle = 0
  LockPosition = false
  MeasureType = 1
  OverTolerance = 0
  References2D = -> [View002]
  Rotation = 0
  ScaleType = 0
  TheoreticalExact = false
  Type = 5
  UnderTolerance = 0
  X = 32.7354
  Y = 162.67
FEATURE [TechDraw::DrawViewDimension] Dimension127
  AngleOverride = false
  Arbitrary = false
  ArbitraryTolerances = false
  EqualTolerance = true
  ExtensionAngle = 0
  FormatSpec = %.2w
  FormatSpecOverTolerance = %+.2w
  FormatSpecUnderTolerance = %+.2w
  Inverted = false
  LineAngle = 0
  LockPosition = false
  MeasureType = 1
  OverTolerance = 0
  References2D = -> [View002]
  Rotation = 0
  ScaleType = 0
  TheoreticalExact = false
  Type = 2
  UnderTolerance = 0
  X = -32.8084
  Y = 197.838
FEATURE [TechDraw::DrawViewDimension] Dimension128
  AngleOverride = false
  Arbitrary = false
  ArbitraryTolerances = false
  EqualTolerance = true
  ExtensionAngle = 0
  FormatSpec = %.2w
  FormatSpecOverTolerance = %+.2w
  FormatSpecUnderTolerance = %+.2w
  Inverted = false
  LineAngle = 0
  LockPosition = false
  MeasureType = 1
  OverTolerance = 0
  References2D = -> [View002]
  Rotation = 0
  ScaleType = 0
  TheoreticalExact = false
  Type = 2
  UnderTolerance = 0
  X = 1.24535
  Y = 227.816
FEATURE [TechDraw::DrawViewDimension] Dimension129
  AngleOverride = false
  Arbitrary = false
  ArbitraryTolerances = false
  EqualTolerance = true
  ExtensionAngle = 0
  FormatSpec = %.2w
  FormatSpecOverTolerance = %+.2w
  FormatSpecUnderTolerance = %+.2w
  Inverted = false
  LineAngle = 0
  LockPosition = false
  MeasureType = 1
  OverTolerance = 0
  References2D = -> [View002]
  Rotation = 0
  ScaleType = 0
  TheoreticalExact = false
  Type = 1
  UnderTolerance = 0
  X = 3.60935
  Y = 217.766
FEATURE [TechDraw::DrawViewBalloon] Balloon024
  BubbleShape = 1
  EndType = 0
  EndTypeScale = 1
  KinkLength = 5
  LockPosition = false
  OriginX = 25.5042
  OriginY = 105.929
  Rotation = 0
  ScaleType = 0
  ShapeScale = 1
  SourceView = -> View001
  Text = 25.00 Depth
  TextWrapLen = -1
  X = 87.4895
  Y = 131.39
FEATURE [TechDraw::DrawViewDimension] Dimension130
  AngleOverride = false
  Arbitrary = false
  ArbitraryTolerances = false
  EqualTolerance = true
  ExtensionAngle = 0
  FormatSpec = %.2w
  FormatSpecOverTolerance = %+.2w
  FormatSpecUnderTolerance = %+.2w
  Inverted = false
  LineAngle = 0
  LockPosition = false
  MeasureType = 1
  OverTolerance = 0
  References2D = -> [View001]
  Rotation = 0
  ScaleType = 0
  TheoreticalExact = false
  Type = 6
  UnderTolerance = 0
  X = -163.831
  Y = 214.92
FEATURE [TechDraw::DrawViewDimension] Dimension131
  AngleOverride = false
  Arbitrary = false
  ArbitraryTolerances = false
  EqualTolerance = true
  ExtensionAngle = 0
  FormatSpec = %.2w
  FormatSpecOverTolerance = %+.2w
  FormatSpecUnderTolerance = %+.2w
  Inverted = false
  LineAngle = 0
  LockPosition = false
  MeasureType = 1
  OverTolerance = 0
  References2D = -> [View001]
  Rotation = 0
  ScaleType = 0
  TheoreticalExact = false
  Type = 6
  UnderTolerance = 0
  X = -128.999
  Y = 256.792
FEATURE [TechDraw::DrawViewDimension] Dimension132
  AngleOverride = false
  Arbitrary = false
  ArbitraryTolerances = false
  EqualTolerance = true
  ExtensionAngle = 0
  FormatSpec = %.2w
  FormatSpecOverTolerance = %+.2w
  FormatSpecUnderTolerance = %+.2w
  Inverted = false
  LineAngle = 0
  LockPosition = false
  MeasureType = 1
  OverTolerance = 0
  References2D = -> [View001]
  Rotation = 0
  ScaleType = 0
  TheoreticalExact = false
  Type = 6
  UnderTolerance = 0
  X = 37.3802
  Y = 173.237
FEATURE [TechDraw::DrawViewDimension] Dimension133
  AngleOverride = false
  Arbitrary = false
  ArbitraryTolerances = false
  EqualTolerance = true
  ExtensionAngle = 0
  FormatSpec = %.2w
  FormatSpecOverTolerance = %+.2w
  FormatSpecUnderTolerance = %+.2w
  Inverted = false
  LineAngle = 0
  LockPosition = false
  MeasureType = 1
  OverTolerance = 0
  References2D = -> [View001]
  Rotation = 0
  ScaleType = 0
  TheoreticalExact = false
  Type = 6
  UnderTolerance = 0
  X = 113.736
  Y = 137.052
FEATURE [TechDraw::DrawViewDimension] Dimension134
  AngleOverride = false
  Arbitrary = false
  ArbitraryTolerances = false
  EqualTolerance = true
  ExtensionAngle = 0
  FormatSpec = %.2w
  FormatSpecOverTolerance = %+.2w
  FormatSpecUnderTolerance = %+.2w
  Inverted = false
  LineAngle = 0
  LockPosition = false
  MeasureType = 1
  OverTolerance = 0
  References2D = -> [View001]
  Rotation = 0
  ScaleType = 0
  TheoreticalExact = false
  Type = 6
  UnderTolerance = 0
  X = 103.314
  Y = 32.4901
FEATURE [TechDraw::DrawViewDimension] Dimension135
  AngleOverride = false
  Arbitrary = false
  ArbitraryTolerances = false
  EqualTolerance = true
  ExtensionAngle = 0
  FormatSpec = %.2w
  FormatSpecOverTolerance = %+.2w
  FormatSpecUnderTolerance = %+.2w
  Inverted = false
  LineAngle = 0
  LockPosition = false
  MeasureType = 1
  OverTolerance = 0
  References2D = -> [View001]
  Rotation = 0
  ScaleType = 0
  TheoreticalExact = false
  Type = 6
  UnderTolerance = 0
  X = 81.7298
  Y = 10.9166
FEATURE [TechDraw::DrawViewDimension] Dimension136
  AngleOverride = false
  Arbitrary = false
  ArbitraryTolerances = false
  EqualTolerance = true
  ExtensionAngle = 0
  FormatSpec = %.2w
  FormatSpecOverTolerance = %+.2w
  FormatSpecUnderTolerance = %+.2w
  Inverted = false
  LineAngle = 0
  LockPosition = false
  MeasureType = 1
  OverTolerance = 0
  References2D = -> [View001]
  Rotation = 0
  ScaleType = 0
  TheoreticalExact = false
  Type = 6
  UnderTolerance = 0
  X = 162.171
  Y = -245.455
FEATURE [TechDraw::DrawViewDimension] Dimension137
  AngleOverride = false
  Arbitrary = false
  ArbitraryTolerances = false
  EqualTolerance = true
  ExtensionAngle = 0
  FormatSpec = %.2w
  FormatSpecOverTolerance = %+.2w
  FormatSpecUnderTolerance = %+.2w
  Inverted = false
  LineAngle = 0
  LockPosition = false
  MeasureType = 1
  OverTolerance = 0
  References2D = -> [View001]
  Rotation = 0
  ScaleType = 0
  TheoreticalExact = false
  Type = 6
  UnderTolerance = 0
  X = -165.989
  Y = -160.611
FEATURE [TechDraw::DrawViewDimension] Dimension138
  AngleOverride = false
  Arbitrary = false
  ArbitraryTolerances = false
  EqualTolerance = true
  ExtensionAngle = 0
  FormatSpec = %.2w
  FormatSpecOverTolerance = %+.2w
  FormatSpecUnderTolerance = %+.2w
  Inverted = false
  LineAngle = 0
  LockPosition = false
  MeasureType = 1
  OverTolerance = 0
  References2D = -> [View001]
  Rotation = 0
  ScaleType = 0
  TheoreticalExact = false
  Type = 6
  UnderTolerance = 0
  X = -105.194
  Y = 0.957632
FEATURE [TechDraw::DrawViewDimension] Dimension139
  AngleOverride = false
  Arbitrary = false
  ArbitraryTolerances = false
  EqualTolerance = true
  ExtensionAngle = 0
  FormatSpec = %.2w
  FormatSpecOverTolerance = %+.2w
  FormatSpecUnderTolerance = %+.2w
  Inverted = false
  LineAngle = 0
  LockPosition = false
  MeasureType = 1
  OverTolerance = 0
  References2D = -> [View001]
  Rotation = 0
  ScaleType = 0
  TheoreticalExact = false
  Type = 6
  UnderTolerance = 0
  X = -161.033
  Y = 81.9143
FEATURE [TechDraw::DrawViewDimension] Dimension140
  AngleOverride = false
  Arbitrary = false
  ArbitraryTolerances = false
  EqualTolerance = true
  ExtensionAngle = 0
  FormatSpec = R%.2w
  FormatSpecOverTolerance = %+.2w
  FormatSpecUnderTolerance = %+.2w
  Inverted = false
  LineAngle = 0
  LockPosition = false
  MeasureType = 1
  OverTolerance = 0
  References2D = -> [View002]
  Rotation = 0
  ScaleType = 0
  TheoreticalExact = false
  Type = 4
  UnderTolerance = 0
  X = -36.9826
  Y = -124.709
FEATURE [TechDraw::DrawViewDimension] Dimension141
  AngleOverride = false
  Arbitrary = false
  ArbitraryTolerances = false
  EqualTolerance = true
  ExtensionAngle = 0
  FormatSpec = %.2w
  FormatSpecOverTolerance = %+.2w
  FormatSpecUnderTolerance = %+.2w
  Inverted = false
  LineAngle = 0
  LockPosition = false
  MeasureType = 1
  OverTolerance = 0
  References2D = -> [View002]
  Rotation = 0
  ScaleType = 0
  TheoreticalExact = false
  Type = 1
  UnderTolerance = 0
  X = 80.8512
  Y = -205.871
FEATURE [TechDraw::DrawViewDimension] Dimension142
  AngleOverride = false
  Arbitrary = false
  ArbitraryTolerances = false
  EqualTolerance = true
  ExtensionAngle = 0
  FormatSpec = %.2w
  FormatSpecOverTolerance = %+.2w
  FormatSpecUnderTolerance = %+.2w
  Inverted = false
  LineAngle = 0
  LockPosition = false
  MeasureType = 1
  OverTolerance = 0
  References2D = -> [View002]
  Rotation = 0
  ScaleType = 0
  TheoreticalExact = false
  Type = 1
  UnderTolerance = 0
  X = -32.4699
  Y = 122.499
FEATURE [TechDraw::DrawViewDimension] Dimension143
  AngleOverride = false
  Arbitrary = false
  ArbitraryTolerances = false
  EqualTolerance = true
  ExtensionAngle = 0
  FormatSpec = %.2w
  FormatSpecOverTolerance = %+.2w
  FormatSpecUnderTolerance = %+.2w
  Inverted = false
  LineAngle = 0
  LockPosition = false
  MeasureType = 1
  OverTolerance = 0
  References2D = -> [View002]
  Rotation = 0
  ScaleType = 0
  TheoreticalExact = false
  Type = 2
  UnderTolerance = 0
  X = -45.8177
  Y = 135.236
FEATURE [TechDraw::DrawViewDimension] Dimension144
  AngleOverride = false
  Arbitrary = false
  ArbitraryTolerances = false
  EqualTolerance = true
  ExtensionAngle = 0
  FormatSpec = %.2w
  FormatSpecOverTolerance = %+.2w
  FormatSpecUnderTolerance = %+.2w
  Inverted = false
  LineAngle = 0
  LockPosition = false
  MeasureType = 1
  OverTolerance = 0
  References2D = -> [View002]
  Rotation = 0
  ScaleType = 0
  TheoreticalExact = false
  Type = 2
  UnderTolerance = 0
  X = -45.4543
  Y = 122.701
FEATURE [TechDraw::DrawViewDimension] Dimension145
  AngleOverride = false
  Arbitrary = false
  ArbitraryTolerances = false
  EqualTolerance = true
  ExtensionAngle = 0
  FormatSpec = %.2w
  FormatSpecOverTolerance = %+.2w
  FormatSpecUnderTolerance = %+.2w
  Inverted = false
  LineAngle = 0
  LockPosition = false
  MeasureType = 1
  OverTolerance = 0
  References2D = -> [View002]
  Rotation = 0
  ScaleType = 0
  TheoreticalExact = false
  Type = 2
  UnderTolerance = 0
  X = -45.6577
  Y = 106.724
FEATURE [TechDraw::DrawViewDimension] Dimension146
  AngleOverride = false
  Arbitrary = false
  ArbitraryTolerances = false
  EqualTolerance = true
  ExtensionAngle = 0
  FormatSpec = %.2w
  FormatSpecOverTolerance = %+.2w
  FormatSpecUnderTolerance = %+.2w
  Inverted = false
  LineAngle = 0
  LockPosition = false
  MeasureType = 1
  OverTolerance = 0
  References2D = -> [View002]
  Rotation = 0
  ScaleType = 0
  TheoreticalExact = false
  Type = 2
  UnderTolerance = 0
  X = -45.2276
  Y = 94.2476
FEATURE [TechDraw::DrawViewDimension] Dimension147
  AngleOverride = false
  Arbitrary = false
  ArbitraryTolerances = false
  EqualTolerance = true
  ExtensionAngle = 0
  FormatSpec = %.2w
  FormatSpecOverTolerance = %+.2w
  FormatSpecUnderTolerance = %+.2w
  Inverted = false
  LineAngle = 0
  LockPosition = false
  MeasureType = 1
  OverTolerance = 0
  References2D = -> [View002]
  Rotation = 0
  ScaleType = 0
  TheoreticalExact = false
  Type = 1
  UnderTolerance = 0
  X = -32.9466
  Y = 95.959
FEATURE [TechDraw::DrawViewDimension] Dimension148
  AngleOverride = false
  Arbitrary = false
  ArbitraryTolerances = false
  EqualTolerance = true
  ExtensionAngle = 0
  FormatSpec = %.2w
  FormatSpecOverTolerance = %+.2w
  FormatSpecUnderTolerance = %+.2w
  Inverted = false
  LineAngle = 0
  LockPosition = false
  MeasureType = 1
  OverTolerance = 0
  References2D = -> [View002]
  Rotation = 0
  ScaleType = 0
  TheoreticalExact = false
  Type = 2
  UnderTolerance = 0
  X = -45.3642
  Y = 77.8442
FEATURE [TechDraw::DrawViewDimension] Dimension149
  AngleOverride = false
  Arbitrary = false
  ArbitraryTolerances = false
  EqualTolerance = true
  ExtensionAngle = 0
  FormatSpec = %.2w
  FormatSpecOverTolerance = %+.2w
  FormatSpecUnderTolerance = %+.2w
  Inverted = false
  LineAngle = 0
  LockPosition = false
  MeasureType = 1
  OverTolerance = 0
  References2D = -> [View002]
  Rotation = 0
  ScaleType = 0
  TheoreticalExact = false
  Type = 2
  UnderTolerance = 0
  X = -39.5514
  Y = 51.6308
FEATURE [TechDraw::DrawViewDimension] Dimension150
  AngleOverride = false
  Arbitrary = false
  ArbitraryTolerances = false
  EqualTolerance = true
  ExtensionAngle = 0
  FormatSpec = %.2w
  FormatSpecOverTolerance = %+.2w
  FormatSpecUnderTolerance = %+.2w
  Inverted = false
  LineAngle = 0
  LockPosition = false
  MeasureType = 1
  OverTolerance = 0
  References2D = -> [View002]
  Rotation = 0
  ScaleType = 0
  TheoreticalExact = false
  Type = 2
  UnderTolerance = 0
  X = -50.1677
  Y = 25.0308
FEATURE [TechDraw::DrawViewDimension] Dimension151
  AngleOverride = false
  Arbitrary = false
  ArbitraryTolerances = false
  EqualTolerance = true
  ExtensionAngle = 0
  FormatSpec = %.2w
  FormatSpecOverTolerance = %+.2w
  FormatSpecUnderTolerance = %+.2w
  Inverted = false
  LineAngle = 0
  LockPosition = false
  MeasureType = 1
  OverTolerance = 0
  References2D = -> [View002]
  Rotation = 0
  ScaleType = 0
  TheoreticalExact = false
  Type = 1
  UnderTolerance = 0
  X = -46.799
  Y = 41.7571
FEATURE [TechDraw::DrawViewBalloon] Balloon025
  BubbleShape = 1
  EndType = 0
  EndTypeScale = 1
  KinkLength = 5
  LockPosition = false
  OriginX = 101.502
  OriginY = -22.3879
  Rotation = 0
  ScaleType = 0
  ShapeScale = 1
  SourceView = -> View001
  Text = R5.00 
  TextWrapLen = -1
  X = 143.046
  Y = -2.94035
FEATURE [TechDraw::DrawViewPart] View003
  CoarseView = false
  Direction = (-0.521445,-0.853283,0.001833)
  Focus = 100
  HardHidden = false
  IsoCount = 0
  IsoHidden = false
  IsoVisible = false
  LockPosition = false
  Perspective = false
  Rotation = 0
  ScaleType = 0
  ScrubCount = 0
  SeamHidden = false
  SeamVisible = false
  SmoothHidden = false
  SmoothVisible = true
  Source = -> [Body001]
  X = 319.748
  XDirection = (0.853284,-0.521446,-0.000188679)
  Y = 108.624
FEATURE [TechDraw::DrawViewDimension] Dimension152
  AngleOverride = false
  Arbitrary = false
  ArbitraryTolerances = false
  EqualTolerance = true
  ExtensionAngle = 0
  FormatSpec = R%.2w
  FormatSpecOverTolerance = %+.2w
  FormatSpecUnderTolerance = %+.2w
  Inverted = false
  LineAngle = 0
  LockPosition = false
  MeasureType = 1
  OverTolerance = 0
  References2D = -> [View003]
  Rotation = 0
  ScaleType = 0
  TheoreticalExact = false
  Type = 4
  UnderTolerance = 0
  X = -49.6526
  Y = 9.98758
FEATURE [TechDraw::DrawViewDimension] Dimension153
  AngleOverride = false
  Arbitrary = false
  ArbitraryTolerances = false
  EqualTolerance = true
  ExtensionAngle = 0
  FormatSpec = %.2w
  FormatSpecOverTolerance = %+.2w
  FormatSpecUnderTolerance = %+.2w
  Inverted = false
  LineAngle = 0
  LockPosition = false
  MeasureType = 0
  OverTolerance = 0
  References2D = -> [View003]
  References3D = -> [Body001]
  Rotation = 0
  ScaleType = 0
  TheoreticalExact = false
  Type = 1
  UnderTolerance = 0
  X = -13.6896
  Y = 34.3297
FEATURE [TechDraw::DrawViewDimension] Dimension154
  AngleOverride = false
  Arbitrary = false
  ArbitraryTolerances = false
  EqualTolerance = true
  ExtensionAngle = 0
  FormatSpec = %.2w
  FormatSpecOverTolerance = %+.2w
  FormatSpecUnderTolerance = %+.2w
  Inverted = false
  LineAngle = 0
  LockPosition = false
  MeasureType = 0
  OverTolerance = 0
  References2D = -> [View003]
  References3D = -> [Body001]
  Rotation = 0
  ScaleType = 0
  TheoreticalExact = false
  Type = 1
  UnderTolerance = 0
  X = -13.8273
  Y = 44.999
FEATURE [TechDraw::DrawViewDimension] Dimension155
  AngleOverride = false
  Arbitrary = false
  ArbitraryTolerances = false
  EqualTolerance = true
  ExtensionAngle = 0
  FormatSpec = %.2w
  FormatSpecOverTolerance = %+.2w
  FormatSpecUnderTolerance = %+.2w
  Inverted = false
  LineAngle = 0
  LockPosition = false
  MeasureType = 1
  OverTolerance = 0
  References2D = -> [View003]
  Rotation = 0
  ScaleType = 0
  TheoreticalExact = false
  Type = 2
  UnderTolerance = 0
  X = -40.29
  Y = 1.6735
FEATURE [TechDraw::DrawViewDimension] Dimension156
  AngleOverride = false
  Arbitrary = false
  ArbitraryTolerances = false
  EqualTolerance = true
  ExtensionAngle = 0
  FormatSpec = %.2w
  FormatSpecOverTolerance = %+.2w
  FormatSpecUnderTolerance = %+.2w
  Inverted = false
  LineAngle = 0
  LockPosition = false
  MeasureType = 1
  OverTolerance = 0
  References2D = -> [View003]
  Rotation = 0
  ScaleType = 0
  TheoreticalExact = false
  Type = 2
  UnderTolerance = 0
  X = -24.4001
  Y = 3.6093
FEATURE [TechDraw::DrawViewDimension] Dimension157
  AngleOverride = false
  Arbitrary = false
  ArbitraryTolerances = false
  EqualTolerance = true
  ExtensionAngle = 0
  FormatSpec = %.2w
  FormatSpecOverTolerance = %+.2w
  FormatSpecUnderTolerance = %+.2w
  Inverted = false
  LineAngle = 0
  LockPosition = false
  MeasureType = 0
  OverTolerance = 0
  References2D = -> [View003]
  References3D = -> [Body001]
  Rotation = 0
  ScaleType = 0
  TheoreticalExact = false
  Type = 1
  UnderTolerance = 0
  X = 13.98
  Y = 6.0468
FEATURE [TechDraw::DrawViewDimension] Dimension158
  AngleOverride = false
  Arbitrary = false
  ArbitraryTolerances = false
  EqualTolerance = true
  ExtensionAngle = 0
  FormatSpec = %.2w
  FormatSpecOverTolerance = %+.2w
  FormatSpecUnderTolerance = %+.2w
  Inverted = false
  LineAngle = 0
  LockPosition = false
  MeasureType = 0
  OverTolerance = 0
  References2D = -> [View003]
  References3D = -> [Body001]
  Rotation = 0
  ScaleType = 0
  TheoreticalExact = false
  Type = 2
  UnderTolerance = 0
  X = -5.83083
  Y = -4.56155
FEATURE [TechDraw::DrawViewBalloon] Balloon027
  BubbleShape = 1
  EndType = 0
  EndTypeScale = 1
  KinkLength = 5
  LockPosition = false
  OriginX = 33.7151
  OriginY = 6.53899
  Rotation = 0
  ScaleType = 0
  ShapeScale = 1
  SourceView = -> View003
  Text = 40.00 Depth
  TextWrapLen = -1
  X = 72.5513
  Y = 31.9463
FEATURE [TechDraw::DrawViewDimension] Dimension159
  AngleOverride = false
  Arbitrary = false
  ArbitraryTolerances = false
  EqualTolerance = true
  ExtensionAngle = 0
  FormatSpec = %.2w
  FormatSpecOverTolerance = %+.2w
  FormatSpecUnderTolerance = %+.2w
  Inverted = false
  LineAngle = 0
  LockPosition = false
  MeasureType = 0
  OverTolerance = 0
  References2D = -> [View003]
  References3D = -> [Body001]
  Rotation = 0
  ScaleType = 0
  TheoreticalExact = false
  Type = 1
  UnderTolerance = 0
  X = 59.7969
  Y = 14.8185
FEATURE [TechDraw::DrawViewDimension] Dimension162
  AngleOverride = false
  Arbitrary = false
  ArbitraryTolerances = false
  EqualTolerance = true
  ExtensionAngle = 0
  FormatSpec = %.2w
  FormatSpecOverTolerance = %+.2w
  FormatSpecUnderTolerance = %+.2w
  Inverted = false
  LineAngle = 0
  LockPosition = false
  MeasureType = 0
  OverTolerance = 0
  References2D = -> [View003]
  References3D = -> [Body001]
  Rotation = 0
  ScaleType = 0
  TheoreticalExact = false
  Type = 1
  UnderTolerance = 0
  X = -64.3944
  Y = 4.44728
FEATURE [TechDraw::DrawViewDimension] Dimension164
  AngleOverride = false
  Arbitrary = false
  ArbitraryTolerances = false
  EqualTolerance = true
  ExtensionAngle = 0
  FormatSpec = %.2w
  FormatSpecOverTolerance = %+.2w
  FormatSpecUnderTolerance = %+.2w
  Inverted = false
  LineAngle = 0
  LockPosition = false
  MeasureType = 1
  OverTolerance = 0
  References2D = -> [View003]
  Rotation = 0
  ScaleType = 0
  TheoreticalExact = false
  Type = 2
  UnderTolerance = 0
  X = 53.643
  Y = -28.166
FEATURE [TechDraw::DrawViewAnnotation] Annotation
  Font = osifont
  LineSpace = 100
  LockPosition = false
  MaxWidth = -1
  Rotation = 0
  ScaleType = 0
  Text = AFPI Device
  TextSize = 5
  TextStyle = 0
  X = 128.975
  Y = 445.239
FEATURE [TechDraw::DrawViewAnnotation] Annotation001
  Font = osifont
  LineSpace = 100
  LockPosition = false
  MaxWidth = -1
  Rotation = 0
  ScaleType = 0
  Text = Speaker
  TextSize = 5
  TextStyle = 0
  X = 513.095
  Y = 303.468
FEATURE [TechDraw::DrawViewAnnotation] Annotation002
  Font = osifont
  LineSpace = 100
  LockPosition = false
  MaxWidth = -1
  Rotation = 0
  ScaleType = 0
  Text = Single Coil | Neck Pickup
  TextSize = 5
  TextStyle = 0
  X = 277.46
  Y = 510.339
FEATURE [TechDraw::DrawViewAnnotation] Annotation003
  Font = osifont
  LineSpace = 100
  LockPosition = false
  MaxWidth = -1
  Rotation = 0
  ScaleType = 0
  Text = RGB Lighting Board
  TextSize = 5
  TextStyle = 0
  X = 306.577
  Y = 492.047
FEATURE [TechDraw::DrawViewAnnotation] Annotation004
  Font = osifont
  LineSpace = 100
  LockPosition = false
  MaxWidth = -1
  Rotation = 0
  ScaleType = 0
  Text = Single Coil | Middle Pickup
  TextSize = 5
  TextStyle = 0
  X = 320.556
  Y = 465.766
FEATURE [TechDraw::DrawViewAnnotation] Annotation005
  Font = osifont
  LineSpace = 100
  LockPosition = false
  MaxWidth = -1
  Rotation = 0
  ScaleType = 0
  Text = Humbucker | Bridge Pickup
  TextSize = 5
  TextStyle = 0
  X = 353.409
  Y = 432.482
FEATURE [TechDraw::DrawViewAnnotation] Annotation006
  Font = osifont
  LineSpace = 100
  LockPosition = false
  MaxWidth = -1
  Rotation = 0
  ScaleType = 0
  Text = Tremolo
  TextSize = 5
  TextStyle = 0
  X = 351.705
  Y = 355.334
FEATURE [TechDraw::DrawViewAnnotation] Annotation007
  Font = osifont
  LineSpace = 100
  LockPosition = false
  MaxWidth = -1
  Rotation = 0
  ScaleType = 0
  Text = Neck Insert
  TextSize = 5
  TextStyle = 0
  X = 189.449
  Y = 515.352
FEATURE [TechDraw::DrawViewAnnotation] Annotation008
  Font = osifont
  LineSpace = 100
  LockPosition = false
  MaxWidth = -1
  Rotation = 0
  ScaleType = 0
  Text = Control Cavity
  TextSize = 5
  TextStyle = 0
  X = 448.417
  Y = 355.086
FEATURE [TechDraw::DrawViewAnnotation] Annotation009
  Font = osifont
  LineSpace = 100
  LockPosition = false
  MaxWidth = -1
  Rotation = 0
  ScaleType = 0
  Text = IO Ports
  TextSize = 5
  TextStyle = 0
  X = 344.121
  Y = 231.71
FEATURE [TechDraw::DrawViewAnnotation] Annotation010
  Font = osifont
  LineSpace = 100
  LockPosition = false
  MaxWidth = -1
  Rotation = 0
  ScaleType = 0
  Text = TOP VIEW
  TextSize = 5
  TextStyle = 0
  X = 240.201
  Y = 555.155
FEATURE [TechDraw::DrawViewAnnotation] Annotation011
  Font = osifont
  LineSpace = 100
  LockPosition = false
  MaxWidth = -1
  Rotation = 0
  ScaleType = 0
  Text = BOTTOM VIEW
  TextSize = 5
  TextStyle = 0
  X = 618.555
  Y = 553.106
FEATURE [TechDraw::DrawPage] Page001  label="Front Back View"
  KeepUpdated = true
  NextBalloonIndex = 28
  ProjectionType = 0
  Template = -> Template001
  Views = -> [View001,View002,Dimension,Dimension001,Dimension002,Dimension003,Dimension004,Dimension005,Dimension006,Dimension007,Dimension008,Dimension009,Dimension010,Dimension011,Dimension012,Dimension013,Dimension014,Dimension015,Dimension016,Dimension017,Dimension018,Dimension019,Dimension020,Dimension021,Dimension022,Dimension023,Dimension024,Dimension025,Dimension026,Dimension027,Dimension028,+143 more]
FEATURE [Sketcher::SketchObject] Sketch359
  FullyConstrained = false
  MapMode = 5
  Placement = pos=(0,0,0) rot=(1,0,0;3.14159rad)
  Support = -> [Fillet047]
  sketch-geometry (13):
    g0: LineSegment StartX=252.2 StartY=-540 StartZ=0 EndX=197.79 EndY=-540 EndZ=0
    g1: LineSegment StartX=197.79 StartY=-540.01 StartZ=0 EndX=225 EndY=-540.01 EndZ=0
    g2: LineSegment StartX=225 StartY=-540.01 StartZ=0 EndX=225 EndY=-546 EndZ=0
    g3: LineSegment StartX=225 StartY=-545.502 StartZ=0 EndX=225 EndY=-535.5 EndZ=0
    g4: LineSegment StartX=225 StartY=-535.5 StartZ=0 EndX=225 EndY=-484.5 EndZ=0
    g5: LineSegment StartX=225 StartY=-484.5 StartZ=0 EndX=244 EndY=-484.5 EndZ=0
    g6: LineSegment StartX=225 StartY=-484.5 StartZ=0 EndX=206 EndY=-484.5 EndZ=0
    g7: LineSegment StartX=225 StartY=-535.5 StartZ=0 EndX=244 EndY=-535.5 EndZ=0
    g8: LineSegment StartX=225 StartY=-535.5 StartZ=0 EndX=205.9 EndY=-535.5 EndZ=0
    g9: Circle CenterX=205.9 CenterY=-535.5 CenterZ=0 NormalX=0 NormalY=0 NormalZ=1 AngleXU=0 Radius=2.25
    g10: Circle CenterX=244 CenterY=-535.5 CenterZ=0 NormalX=0 NormalY=0 NormalZ=1 AngleXU=0 Radius=2.25
    g11: Circle CenterX=244 CenterY=-484.5 CenterZ=0 NormalX=0 NormalY=0 NormalZ=1 AngleXU=0 Radius=2.25
    g12: Circle CenterX=206 CenterY=-484.5 CenterZ=0 NormalX=0 NormalY=0 NormalZ=1 AngleXU=0 Radius=2.25
  constraints (24):
    c: Horizontal(g0)
    c: Horizontal(g1)
    c: Coincident(g2,g1)
    c: Vertical(g2)
    c: PointOnObject(g3,g2)
    c: Vertical(g3)
    c: Coincident(g4,g3)
    c: Vertical(g4)
    c: Coincident(g5,g4)
    c: Horizontal(g5)
    c: Coincident(g6,g4)
    c: Horizontal(g6)
    c: Coincident(g7,g3)
    c: Horizontal(g7)
    c: Coincident(g8,g3)
    c: Horizontal(g8)
    c: Coincident(g9,g8)
    c: Coincident(g10,g7)
    c: Coincident(g11,g5)
    c: Coincident(g12,g6)
    c: Equal(g10,g9)
    c: Equal(g10,g12)
    c: Equal(g10,g11)
    c: Diameter(g10) = 4.5
FEATURE [PartDesign::Pocket] Pocket121
  BaseFeature = -> Fillet072
  Direction = (0,0,1)
  Length = 7
  Length2 = 5
  Profile = -> Sketch359
  ReferenceAxis = -> Sketch359 [N_Axis]
  Type = 0
FEATURE [PartDesign::Body] Body029  label="Jig 3 Body"
  Group = -> [Sketch289,Sketch296,Pad016,Sketch299,Pocket098,Sketch304,Sketch309,Sketch310,Sketch316,Pocket105,Pocket106,Pocket107,Fillet056,Fillet057,Pocket108,Fillet058,Fillet059,Fillet060,Fillet061,Fillet062,Fillet063,Fillet064,Fillet065,Fillet072,Sketch359,Pocket121]
  Origin = -> Origin209
  Tip = -> Pocket121
FEATURE [App::Part] Part048  label="Jig 3"
  Group = -> [Body029]
  Origin = -> Origin208
  Placement = pos=(0,0,-99.9) rot=(0,0,1;0rad)
FEATURE [App::Part] Part044  label="Jigs"
  Group = -> [Part046,Part047,Part048,Part049,Part050,Part051,Part052]
  Origin = -> Origin201
FEATURE [TechDraw::DrawViewDimension] Dimension165
  AngleOverride = false
  Arbitrary = false
  ArbitraryTolerances = false
  EqualTolerance = true
  ExtensionAngle = 0
  FormatSpec = %.2w
  FormatSpecOverTolerance = %+.2w
  FormatSpecUnderTolerance = %+.2w
  Inverted = false
  LineAngle = 0
  LockPosition = false
  MeasureType = 1
  OverTolerance = 0
  References2D = -> [View003]
  Rotation = 0
  ScaleType = 0
  TheoreticalExact = false
  Type = 2
  UnderTolerance = 0
  X = 296.45
  Y = 2.53654
FEATURE [TechDraw::DrawViewDimension] Dimension166
  AngleOverride = false
  Arbitrary = false
  ArbitraryTolerances = false
  EqualTolerance = true
  ExtensionAngle = 0
  FormatSpec = R%.2w
  FormatSpecOverTolerance = %+.2w
  FormatSpecUnderTolerance = %+.2w
  Inverted = false
  LineAngle = 0
  LockPosition = false
  MeasureType = 1
  OverTolerance = 0
  References2D = -> [View003]
  Rotation = 0
  ScaleType = 0
  TheoreticalExact = false
  Type = 4
  UnderTolerance = 0
  X = 44.1698
  Y = -4.85382
FEATURE [TechDraw::DrawViewBalloon] Balloon028
  BubbleShape = 1
  EndType = 0
  EndTypeScale = 1
  KinkLength = 5
  LockPosition = false
  OriginX = 16.7839
  OriginY = 13.2066
  Rotation = 0
  ScaleType = 0
  ShapeScale = 1
  SourceView = -> View003
  Text = 3.00 Depth
  TextWrapLen = -1
  X = 58.4643
  Y = 47.9299
FEATURE [TechDraw::DrawViewAnnotation] Annotation012
  Font = osifont
  LineSpace = 100
  LockPosition = false
  MaxWidth = -1
  Rotation = 0
  ScaleType = 0
  Text = Rear View IO Section
  TextSize = 5
  TextStyle = 0
  X = 204.232
  Y = 154.608
FEATURE [TechDraw::DrawViewAnnotation] Annotation013
  Font = osifont
  LineSpace = 100
  LockPosition = false
  MaxWidth = -1
  Rotation = 0
  ScaleType = 0
  Text = Isometric View
  TextSize = 5
  TextStyle = 0
  X = 421.096
  Y = 512.077
FEATURE [TechDraw::DrawPage] Page  label="Isometric View"
  KeepUpdated = true
  NextBalloonIndex = 4
  ProjectionType = 0
  Template = -> Template
  Views = -> [View,View003,Dimension152,Dimension153,Dimension154,Dimension155,Dimension156,Dimension157,Dimension158,Balloon027,Dimension159,Dimension162,Dimension164,Annotation,Annotation001,Annotation002,Annotation003,Annotation004,Annotation005,Annotation006,Annotation007,Annotation008,Annotation009,Dimension165,Dimension166,Balloon028,Annotation012,Annotation013]
FEATURE [App::Part] Part040  label="Technical Documentation"
  Group = -> [surveyLabel002,Page,Page001]
  Origin = -> Origin171
FEATURE [Sketcher::SketchObject] Sketch360
  FullyConstrained = true
  MapMode = 5
  Support = -> [XY_Plane220]
  sketch-geometry (4):
    g0: LineSegment StartX=0 StartY=0 StartZ=0 EndX=270 EndY=0 EndZ=0
    g1: LineSegment StartX=270 StartY=0 StartZ=0 EndX=270 EndY=-170 EndZ=0
    g2: LineSegment StartX=270 StartY=-170 StartZ=0 EndX=0 EndY=-170 EndZ=0
    g3: LineSegment StartX=0 StartY=-170 StartZ=0 EndX=0 EndY=0 EndZ=0
  constraints (11):
    c: Coincident(g0,g1)
    c: Coincident(g1,g2)
    c: Coincident(g2,g3)
    c: Coincident(g3,g0)
    c: Horizontal(g0)
    c: Horizontal(g2)
    c: Vertical(g1)
    c: Vertical(g3)
    c: Coincident(g0,g-1)
    c: DistanceX(g0,g0) = 270
    c: DistanceY(g3,g3) = 170
FEATURE [PartDesign::Pad] Pad021
  Direction = (0,0,1)
  Length = 3
  Length2 = 10
  Profile = -> Sketch360
  ReferenceAxis = -> Sketch360 [N_Axis]
  Type = 0
FEATURE [PartDesign::Body] Body034  label="Template cnc 1"
  Group = -> [Sketch360,Pad021]
  Origin = -> Origin220
  Tip = -> Pad021
FEATURE [Sketcher::SketchObject] Sketch361
  FullyConstrained = true
  MapMode = 5
  Support = -> [XY_Plane221]
  sketch-geometry (4):
    g0: LineSegment StartX=0 StartY=0 StartZ=0 EndX=270 EndY=0 EndZ=0
    g1: LineSegment StartX=270 StartY=0 StartZ=0 EndX=270 EndY=-170 EndZ=0
    g2: LineSegment StartX=270 StartY=-170 StartZ=0 EndX=0 EndY=-170 EndZ=0
    g3: LineSegment StartX=0 StartY=-170 StartZ=0 EndX=0 EndY=0 EndZ=0
  constraints (11):
    c: Coincident(g0,g1)
    c: Coincident(g1,g2)
    c: Coincident(g2,g3)
    c: Coincident(g3,g0)
    c: Horizontal(g0)
    c: Horizontal(g2)
    c: Vertical(g1)
    c: Vertical(g3)
    c: Coincident(g0,g-1)
    c: DistanceX(g0,g0) = 270
    c: DistanceY(g3,g3) = 170
FEATURE [PartDesign::Pad] Pad022
  Direction = (0,0,1)
  Length = 3
  Length2 = 10
  Profile = -> Sketch361
  ReferenceAxis = -> Sketch361 [N_Axis]
  Type = 0
FEATURE [PartDesign::Body] Body035  label="Template cnc 2"
  Group = -> [Sketch361,Pad022]
  Origin = -> Origin221
  Placement = pos=(0,-214.7,0) rot=(0,0,1;0rad)
  Tip = -> Pad022
FEATURE [Sketcher::SketchObject] Sketch362  label="Underside plate pocket002"
  FullyConstrained = false
  MapMode = 5
  Placement = pos=(0,0,0) rot=(1,0,0;3.14159rad)
  sketch-geometry (11):
    g0: ArcOfCircle CenterX=250 CenterY=-459.965 CenterZ=0 NormalX=0 NormalY=0 NormalZ=1 AngleXU=0 Radius=10.0011 StartAngle=3.14501 EndAngle=4.71235
    g1: ArcOfCircle CenterX=290.043 CenterY=-460 CenterZ=0 NormalX=0 NormalY=0 NormalZ=1 AngleXU=0 Radius=9.96676 StartAngle=4.70814 EndAngle=6.28304
    g2: ArcOfCircle CenterX=192.411 CenterY=-438.241 CenterZ=0 NormalX=0 NormalY=0 NormalZ=1 AngleXU=0 Radius=48.2966 StartAngle=0.171466 EndAngle=1.62074
    g3: ArcOfCircle CenterX=189.983 CenterY=-379.994 CenterZ=0 NormalX=0 NormalY=0 NormalZ=1 AngleXU=0 Radius=10.0109 StartAngle=3.14223 EndAngle=4.71402
    g4: ArcOfCircle CenterX=648.991 CenterY=-407.85 CenterZ=0 NormalX=0 NormalY=0 NormalZ=1 AngleXU=0 Radius=352.857 StartAngle=2.69985 EndAngle=3.28993
    g5: LineSegment StartX=179.972 StartY=-380 StartZ=0 EndX=179.972 EndY=-256.999 EndZ=0
    g6: ArcOfCircle CenterX=189.994 CenterY=-257.016 CenterZ=0 NormalX=0 NormalY=0 NormalZ=1 AngleXU=0 Radius=10.0214 StartAngle=1.57135 EndAngle=3.13987
    g7: ArcOfCircle CenterX=320 CenterY=-257 CenterZ=0 NormalX=0 NormalY=0 NormalZ=1 AngleXU=0 Radius=10.0052 StartAngle=0.000134912 EndAngle=1.57136
    g8: LineSegment StartX=319.994 StartY=-246.995 StartZ=0 EndX=189.988 EndY=-246.995 EndZ=0
    g9: LineSegment StartX=239.999 StartY=-430 StartZ=0 EndX=239.999 EndY=-459.999 EndZ=0
    g10: LineSegment StartX=250 StartY=-469.966 StartZ=0 EndX=290 EndY=-469.966 EndZ=0
  constraints (15):
    c: Coincident(g3,g2)
    c: Coincident(g4,g1)
    c: Coincident(g5,g3)
    c: Vertical(g5)
    c: Coincident(g6,g5)
    c: Coincident(g7,g4)
    c: Coincident(g8,g7)
    c: Coincident(g8,g6)
    c: Horizontal(g8)
    c: Coincident(g9,g2)
    c: Coincident(g9,g0)
    c: Vertical(g9)
    c: Coincident(g10,g0)
    c: Coincident(g10,g1)
    c: Horizontal(g10)
FEATURE [PartDesign::Pad] Pad023
  Direction = (0,0,-1)
  Length = 3
  Length2 = 10
  Placement = pos=(0,0,0) rot=(1,0,0;3.14159rad)
  Profile = -> Sketch362
  ReferenceAxis = -> Sketch362 [N_Axis]
  Type = 0
FEATURE [PartDesign::Fillet] Fillet073
  Base = -> Pad023 [Edge28,Edge25,Edge22,Edge19,Edge16,Edge13,Edge10,Edge7,Edge4,Edge33,Edge31]
  BaseFeature = -> Pad023
  Placement = pos=(0,0,0) rot=(1,0,0;3.14159rad)
  Radius = 2.5
  SupportTransform = false
  UseAllEdges = false
FEATURE [Sketcher::SketchObject] Sketch363
  FullyConstrained = false
  MapMode = 5
  Placement = pos=(0,0,-3) rot=(1,0,0;3.14159rad)
  Support = -> [Fillet073]
  sketch-geometry (51):
    g0: LineSegment StartX=290 StartY=-465 StartZ=0 EndX=270 EndY=-465 EndZ=0
    g1: LineSegment StartX=270 StartY=-465 StartZ=0 EndX=250 EndY=-465 EndZ=0
    g2: LineSegment StartX=250 StartY=-465 StartZ=0 EndX=245 EndY=-445.592 EndZ=0
    g3: LineSegment StartX=245 StartY=-445.592 StartZ=0 EndX=245 EndY=-425.5 EndZ=0
    g4: LineSegment StartX=245 StartY=-425.5 StartZ=0 EndX=239 EndY=-406.4 EndZ=0
    g5: LineSegment StartX=239 StartY=-406.4 StartZ=0 EndX=224.413 EndY=-392.651 EndZ=0
    g6: LineSegment StartX=290 StartY=-465 StartZ=0 EndX=288 EndY=-445 EndZ=0
    g7: LineSegment StartX=288 StartY=-445 StartZ=0 EndX=290 EndY=-425 EndZ=0
    g8: LineSegment StartX=290 StartY=-425 StartZ=0 EndX=289 EndY=-405 EndZ=0
    g9: LineSegment StartX=289 StartY=-405 StartZ=0 EndX=290 EndY=-385 EndZ=0
    g10: LineSegment StartX=290 StartY=-385 StartZ=0 EndX=292 EndY=-365 EndZ=0
    g11: LineSegment StartX=292 StartY=-365 StartZ=0 EndX=294 EndY=-345 EndZ=0
    g12: LineSegment StartX=294 StartY=-345 StartZ=0 EndX=299 EndY=-325.584 EndZ=0
    g13: LineSegment StartX=299 StartY=-325.584 StartZ=0 EndX=304 EndY=-306.2 EndZ=0
    g14: LineSegment StartX=304 StartY=-306.2 StartZ=0 EndX=310 EndY=-287.1 EndZ=0
    g15: LineSegment StartX=310 StartY=-287.1 StartZ=0 EndX=318 EndY=-268.708 EndZ=0
    g16: LineSegment StartX=318 StartY=-268.708 StartZ=0 EndX=323 EndY=-256 EndZ=0
    g17: LineSegment StartX=323 StartY=-256 StartZ=0 EndX=298.1 EndY=-253.1 EndZ=0
    g18: LineSegment StartX=298.1 StartY=-253.1 StartZ=0 EndX=278.1 EndY=-253.1 EndZ=0
    g19: LineSegment StartX=278.1 StartY=-253.1 StartZ=0 EndX=258.1 EndY=-253.1 EndZ=0
    g20: LineSegment StartX=258.1 StartY=-253.1 StartZ=0 EndX=238.1 EndY=-253.1 EndZ=0
    g21: LineSegment StartX=238.1 StartY=-253.1 StartZ=0 EndX=218.1 EndY=-253.1 EndZ=0
    g22: LineSegment StartX=218.1 StartY=-253.1 StartZ=0 EndX=198.1 EndY=-253.1 EndZ=0
    g23: LineSegment StartX=198.1 StartY=-253.1 StartZ=0 EndX=185 EndY=-268.3 EndZ=0
    g24: LineSegment StartX=185 StartY=-268.3 StartZ=0 EndX=185 EndY=-288.3 EndZ=0
    g25: LineSegment StartX=185 StartY=-288.3 StartZ=0 EndX=185 EndY=-308.3 EndZ=0
    g26: LineSegment StartX=185 StartY=-308.3 StartZ=0 EndX=185 EndY=-328.3 EndZ=0
    g27: LineSegment StartX=185 StartY=-328.3 StartZ=0 EndX=185 EndY=-348.3 EndZ=0
    g28: LineSegment StartX=185 StartY=-348.3 StartZ=0 EndX=185 EndY=-368.3 EndZ=0
    g29: LineSegment StartX=185 StartY=-368.3 StartZ=0 EndX=190 EndY=-382 EndZ=0
    g30: LineSegment StartX=190 StartY=-382 StartZ=0 EndX=214 EndY=-388 EndZ=0
    g31: LineSegment StartX=214 StartY=-388 StartZ=0 EndX=224.413 EndY=-392.651 EndZ=0
    g32: Circle CenterX=290 CenterY=-465 CenterZ=0 NormalX=0 NormalY=0 NormalZ=1 AngleXU=0 Radius=1.65
    g33: Circle CenterX=270 CenterY=-465 CenterZ=0 NormalX=0 NormalY=0 NormalZ=1 AngleXU=0 Radius=1.65
    g34: Circle CenterX=250 CenterY=-465 CenterZ=0 NormalX=0 NormalY=0 NormalZ=1 AngleXU=0 Radius=1.65
    g35: Circle CenterX=245 CenterY=-425.5 CenterZ=0 NormalX=0 NormalY=0 NormalZ=1 AngleXU=0 Radius=1.65
    g36: Circle CenterX=214 CenterY=-388 CenterZ=0 NormalX=0 NormalY=0 NormalZ=1 AngleXU=0 Radius=1.65
    g37: Circle CenterX=190 CenterY=-382 CenterZ=0 NormalX=0 NormalY=0 NormalZ=1 AngleXU=0 Radius=1.65
    g38: Circle CenterX=185 CenterY=-348.3 CenterZ=0 NormalX=0 NormalY=0 NormalZ=1 AngleXU=0 Radius=1.65
    g39: Circle CenterX=185 CenterY=-308.3 CenterZ=0 NormalX=0 NormalY=0 NormalZ=1 AngleXU=0 Radius=1.65
    g40: Circle CenterX=185 CenterY=-268.3 CenterZ=0 NormalX=0 NormalY=0 NormalZ=1 AngleXU=0 Radius=1.65
    g41: Circle CenterX=198.1 CenterY=-253.1 CenterZ=0 NormalX=0 NormalY=0 NormalZ=1 AngleXU=0 Radius=1.65
    g42: Circle CenterX=238.1 CenterY=-253.1 CenterZ=0 NormalX=0 NormalY=0 NormalZ=1 AngleXU=0 Radius=1.65
    g43: Circle CenterX=278.1 CenterY=-253.1 CenterZ=0 NormalX=0 NormalY=0 NormalZ=1 AngleXU=0 Radius=1.65
    g44: Circle CenterX=298.1 CenterY=-253.1 CenterZ=0 NormalX=0 NormalY=0 NormalZ=1 AngleXU=0 Radius=1.65
    g45: Circle CenterX=323 CenterY=-256 CenterZ=0 NormalX=0 NormalY=0 NormalZ=1 AngleXU=0 Radius=1.65
    g46: Circle CenterX=318 CenterY=-268.708 CenterZ=0 NormalX=0 NormalY=0 NormalZ=1 AngleXU=0 Radius=1.65
    g47: Circle CenterX=304 CenterY=-306.2 CenterZ=0 NormalX=0 NormalY=0 NormalZ=1 AngleXU=0 Radius=1.65
    g48: Circle CenterX=294 CenterY=-345 CenterZ=0 NormalX=0 NormalY=0 NormalZ=1 AngleXU=0 Radius=1.65
    g49: Circle CenterX=290 CenterY=-385 CenterZ=0 NormalX=0 NormalY=0 NormalZ=1 AngleXU=0 Radius=1.65
    g50: Circle CenterX=290 CenterY=-425 CenterZ=0 NormalX=0 NormalY=0 NormalZ=1 AngleXU=0 Radius=1.65
  constraints (66):
    c: Horizontal(g0)
    c: Coincident(g1,g0)
    c: Horizontal(g1)
    c: Coincident(g2,g1)
    c: Coincident(g3,g2)
    c: Vertical(g3)
    c: Coincident(g4,g3)
    c: Coincident(g4,g5)
    c: Coincident(g0,g6)
    c: Coincident(g6,g7)
    c: Coincident(g7,g8)
    c: Coincident(g8,g9)
    c: Coincident(g9,g10)
    c: Coincident(g10,g11)
    c: Coincident(g11,g12)
    c: Coincident(g12,g13)
    c: Coincident(g13,g14)
    c: Coincident(g14,g15)
    c: Coincident(g15,g16)
    c: Coincident(g16,g17)
    c: Coincident(g17,g18)
    c: Horizontal(g18)
    c: Coincident(g18,g19)
    c: Horizontal(g19)
    c: Coincident(g19,g20)
    c: Horizontal(g20)
    c: Coincident(g20,g21)
    c: Horizontal(g21)
    c: Coincident(g21,g22)
    c: Horizontal(g22)
    c: Coincident(g22,g23)
    c: Coincident(g23,g24)
    c: Vertical(g24)
    c: Coincident(g24,g25)
    c: Vertical(g25)
    c: Coincident(g25,g26)
    c: Vertical(g26)
    c: Coincident(g26,g27)
    c: Vertical(g27)
    c: Coincident(g27,g28)
    c: Vertical(g28)
    c: Coincident(g28,g29)
    c: Coincident(g29,g30)
    c: Coincident(g30,g31)
    c: Coincident(g31,g5)
    c: Coincident(g32,g0)
    c: Coincident(g33,g0)
    c: Coincident(g34,g1)
    c: Coincident(g35,g3)
    c: Coincident(g36,g30)
    c: Coincident(g37,g29)
    c: Coincident(g38,g27)
    c: Coincident(g39,g25)
    c: Coincident(g40,g23)
    c: Coincident(g41,g22)
    c: Coincident(g42,g20)
    c: Coincident(g43,g18)
    c: Coincident(g44,g17)
    c: Coincident(g45,g16)
    c: Coincident(g46,g15)
    c: Coincident(g47,g13)
    c: Coincident(g48,g11)
    c: Coincident(g49,g9)
    c: Coincident(g50,g7)
    c: Equal(g32, g33-g50) x18
    c: Diameter(g32) = 3.3
FEATURE [PartDesign::Pocket] Pocket122
  BaseFeature = -> Fillet073
  Direction = (0,-1e-16,1)
  Length = 3
  Length2 = 5
  Placement = pos=(0,0,0) rot=(1,0,0;3.14159rad)
  Profile = -> Sketch363
  ReferenceAxis = -> Sketch363 [N_Axis]
  Type = 0
FEATURE [Sketcher::SketchObject] Sketch364
  FullyConstrained = false
  MapMode = 5
  Placement = pos=(0,0,-3) rot=(1,0,0;3.14159rad)
  Support = -> [Pocket122]
  sketch-geometry (4):
    g0: LineSegment StartX=190 StartY=-270.2 StartZ=0 EndX=260 EndY=-270.2 EndZ=0
    g1: LineSegment StartX=260 StartY=-270.2 StartZ=0 EndX=260 EndY=-281.2 EndZ=0
    g2: LineSegment StartX=260 StartY=-281.2 StartZ=0 EndX=190 EndY=-281.2 EndZ=0
    g3: LineSegment StartX=190 StartY=-281.2 StartZ=0 EndX=190 EndY=-270.2 EndZ=0
  constraints (10):
    c: Coincident(g0,g1)
    c: Coincident(g1,g2)
    c: Coincident(g2,g3)
    c: Coincident(g3,g0)
    c: Horizontal(g0)
    c: Horizontal(g2)
    c: Vertical(g1)
    c: Vertical(g3)
    c: DistanceX(g0,g0) = 70
    c: DistanceY(g1,g1) = 11
FEATURE [PartDesign::Pocket] Pocket123
  BaseFeature = -> Pocket122
  Direction = (0,0,1)
  Length = 3
  Length2 = 5
  Placement = pos=(0,0,0) rot=(1,0,0;3.14159rad)
  Profile = -> Sketch364
  ReferenceAxis = -> Sketch364 [N_Axis]
  Type = 0
FEATURE [PartDesign::Fillet] Fillet074
  Base = -> Pocket123 [Edge99,Edge98,Edge97,Edge100]
  BaseFeature = -> Pocket123
  Placement = pos=(0,0,0) rot=(1,0,0;3.14159rad)
  Radius = 3
  SupportTransform = false
  UseAllEdges = false
FEATURE [PartDesign::Body] Body036  label="Back Plate 1 template"
  Group = -> [Sketch362,Pad023,Fillet073,Sketch363,Pocket122,Sketch364,Pocket123,Fillet074]
  Origin = -> Origin222
  Placement = pos=(486.536,-46.3513,4.03128) rot=(0.707107,-0.707107,0;3.14159rad)
  Tip = -> Fillet074
FEATURE [Sketcher::SketchObject] Sketch365  label="Wire channels Pocket016"
  FullyConstrained = false
  MapMode = 5
  Placement = pos=(0,0,0) rot=(1,0,0;3.14159rad)
  sketch-geometry (29):
    g0: LineSegment StartX=101.467 StartY=-402.5 StartZ=0 EndX=130.4 EndY=-402.5 EndZ=0
    g1: LineSegment StartX=200 StartY=-200 StartZ=0 EndX=220 EndY=-200 EndZ=0
    g2: LineSegment StartX=135.4 StartY=-402.5 StartZ=0 EndX=135.4 EndY=-397.5 EndZ=0
    g3: LineSegment StartX=135.4 StartY=-397.5 StartZ=0 EndX=175 EndY=-357.904 EndZ=0
    g4: LineSegment StartX=175 StartY=-357.904 StartZ=0 EndX=175 EndY=-245 EndZ=0
    g5: LineSegment StartX=175 StartY=-245 StartZ=0 EndX=290 EndY=-245 EndZ=0
    g6: LineSegment StartX=290 StartY=-245 StartZ=0 EndX=295 EndY=-245 EndZ=0
    g7: LineSegment StartX=295 StartY=-245 StartZ=0 EndX=295 EndY=-215 EndZ=0
    g8: LineSegment StartX=295 StartY=-215 StartZ=0 EndX=290 EndY=-215 EndZ=0
    g9: LineSegment StartX=290 StartY=-215 StartZ=0 EndX=225 EndY=-215 EndZ=0
    g10: LineSegment StartX=225 StartY=-215 StartZ=0 EndX=225 EndY=-200 EndZ=0
    g11: LineSegment StartX=195 StartY=-200 StartZ=0 EndX=195 EndY=-215 EndZ=0
    g12: LineSegment StartX=195 StartY=-215 StartZ=0 EndX=168.46 EndY=-215 EndZ=0
    g13: LineSegment StartX=168.46 StartY=-215 StartZ=0 EndX=162 EndY=-198.36 EndZ=0
    g14: LineSegment StartX=162 StartY=-198.36 StartZ=0 EndX=162 EndY=-115 EndZ=0
    g15: LineSegment StartX=162 StartY=-115 StartZ=0 EndX=162 EndY=-110 EndZ=0
    g16: LineSegment StartX=162 StartY=-110 StartZ=0 EndX=157 EndY=-110 EndZ=0
    g17: LineSegment StartX=157 StartY=-110 StartZ=0 EndX=134.577 EndY=-122.534 EndZ=0
    g18: LineSegment StartX=134.577 StartY=-122.534 StartZ=0 EndX=132 EndY=-126.896 EndZ=0
    g19: LineSegment StartX=132 StartY=-126.896 StartZ=0 EndX=132 EndY=-200.027 EndZ=0
    g20: LineSegment StartX=132 StartY=-200.027 StartZ=0 EndX=144.989 EndY=-239.968 EndZ=0
    g21: LineSegment StartX=144.989 StartY=-239.968 StartZ=0 EndX=144.989 EndY=-343.839 EndZ=0
    g22: LineSegment StartX=144.989 StartY=-343.839 StartZ=0 EndX=96.4674 EndY=-392.5 EndZ=0
    g23: LineSegment StartX=96.4674 StartY=-392.5 StartZ=0 EndX=96.4674 EndY=-397.5 EndZ=0
    g24: LineSegment StartX=96.4674 StartY=-397.5 StartZ=0 EndX=96.4674 EndY=-402.5 EndZ=0
    g25: LineSegment StartX=101.467 StartY=-402.5 StartZ=0 EndX=96.4674 EndY=-402.5 EndZ=0
    g26: LineSegment StartX=130.4 StartY=-402.5 StartZ=0 EndX=135.4 EndY=-402.5 EndZ=0
    g27: LineSegment StartX=225 StartY=-200 StartZ=0 EndX=220 EndY=-200 EndZ=0
    g28: LineSegment StartX=195 StartY=-200 StartZ=0 EndX=200 EndY=-200 EndZ=0
  constraints (78):
    c: Horizontal(g0)
    c: DistanceX(g0,g0) = 28.9326
    c: Horizontal(g1)
    c: DistanceX(g1,g1) = 20
    c: Vertical(g2)
    c: Coincident(g2,g3)
    c: Coincident(g3,g4)
    c: Vertical(g4)
    c: Coincident(g4,g5)
    c: Horizontal(g5)
    c: Coincident(g5,g6)
    c: Horizontal(g6)
    c: Coincident(g6,g7)
    c: Vertical(g7)
    c: Coincident(g7,g8)
    c: Horizontal(g8)
    c: Coincident(g8,g9)
    c: Horizontal(g9)
    c: Coincident(g9,g10)
    c: Vertical(g10)
    c: Vertical(g11)
    c: Coincident(g11,g12)
    c: Horizontal(g12)
    c: Coincident(g12,g13)
    c: Coincident(g13,g14)
    c: Vertical(g14)
    c: Coincident(g14,g15)
    c: Vertical(g15)
    c: Coincident(g15,g16)
    c: Horizontal(g16)
    c: Coincident(g16,g17)
    c: Coincident(g17,g18)
    c: Coincident(g18,g19)
    c: Vertical(g19)
    c: Coincident(g19,g20)
    c: Coincident(g20,g21)
    c: Vertical(g21)
    c: Coincident(g21,g22)
    c: Coincident(g22,g23)
    c: Vertical(g23)
    c: Coincident(g23,g24)
    c: Vertical(g24)
    c: Coincident(g25,g0)
    c: Coincident(g25,g24)
    c: Horizontal(g25)
    c: Coincident(g26,g0)
    c: Coincident(g26,g2)
    c: Horizontal(g26)
    c: Coincident(g27,g10)
    c: Coincident(g27,g1)
    c: Horizontal(g27)
    c: Coincident(g28,g11)
    c: Coincident(g28,g1)
    c: Horizontal(g28)
    c: DistanceX(g25,g25) = 5
    c: DistanceX(g26,g26) = 5
    c: DistanceY(g24,g24) = 5
    c: DistanceY(g23,g23) = 5
    c: DistanceY(g2,g2) = 5
    c: Distance(g22) = 68.7186
    c: Distance(g3) = 56
    c: DistanceY(g21,g21) = 103.871
    c: DistanceY(g4,g4) = 112.904
    c: DistanceX(g5,g5) = 115
    c: DistanceX(g12,g12) = 26.54
    c: DistanceX(g9,g9) = 65
    c: Distance(g20) = 42
    c: DistanceY(g19,g19) = 73.1311
    c: DistanceY(g14,g14) = 83.36
    c: DistanceX(g27,g27) = 5
    c: DistanceX(g28,g28) = 5
    c: DistanceX(g8,g8) = 5
    c: DistanceX(g6,g6) = 5
    c: DistanceY(g7,g7) = 30
    c: Distance(g17) = 25.6886
    c: Distance(g18) = 5.06593
    c: Distance(g16) = 5
    c: DistanceY(g15,g15) = 5
FEATURE [PartDesign::Pad] Pad024
  Direction = (0,0,-1)
  Length = 3
  Length2 = 10
  Placement = pos=(0,0,0) rot=(1,0,0;3.14159rad)
  Profile = -> Sketch365
  ReferenceAxis = -> Sketch365 [N_Axis]
  Type = 0
FEATURE [PartDesign::Fillet] Fillet075
  Base = -> Pad024 [Edge2,Edge5,Edge8,Edge14,Edge17,Edge20,Edge23,Edge26,Edge29,Edge32,Edge35,Edge53,Edge56,Edge59,Edge65,Edge68,Edge74]
  BaseFeature = -> Pad024
  Placement = pos=(0,0,0) rot=(1,0,0;3.14159rad)
  Radius = 3.35
  SupportTransform = false
  UseAllEdges = false
FEATURE [Sketcher::SketchObject] Sketch366
  FullyConstrained = false
  MapMode = 5
  Placement = pos=(0,0,-3) rot=(1,0,0;3.14159rad)
  Support = -> [Fillet075]
  sketch-geometry (38):
    g0: Circle CenterX=105 CenterY=-389 CenterZ=0 NormalX=0 NormalY=0 NormalZ=1 AngleXU=0 Radius=1.15
    g1: Circle CenterX=145 CenterY=-349 CenterZ=0 NormalX=0 NormalY=0 NormalZ=1 AngleXU=0 Radius=1.15
    g2: Circle CenterX=147.5 CenterY=-309 CenterZ=0 NormalX=0 NormalY=0 NormalZ=1 AngleXU=0 Radius=1.15
    g3: Circle CenterX=147.5 CenterY=-259 CenterZ=0 NormalX=0 NormalY=0 NormalZ=1 AngleXU=0 Radius=1.15
    g4: Circle CenterX=172.5 CenterY=-259 CenterZ=0 NormalX=0 NormalY=0 NormalZ=1 AngleXU=0 Radius=1.15
    g5: Circle CenterX=172.5 CenterY=-309 CenterZ=0 NormalX=0 NormalY=0 NormalZ=1 AngleXU=0 Radius=1.15
    g6: Circle CenterX=172.5 CenterY=-349 CenterZ=0 NormalX=0 NormalY=0 NormalZ=1 AngleXU=0 Radius=1.15
    g7: Circle CenterX=147.665 CenterY=-382.765 CenterZ=0 NormalX=0 NormalY=0 NormalZ=1 AngleXU=0 Radius=1.15
    g8: LineSegment StartX=147.5 StartY=-259 StartZ=0 EndX=147.5 EndY=-239 EndZ=0
    g9: LineSegment StartX=147.5 StartY=-239 StartZ=0 EndX=141 EndY=-220 EndZ=0
    g10: LineSegment StartX=141 StartY=-220 StartZ=0 EndX=134.428 EndY=-201 EndZ=0
    g11: LineSegment StartX=134.428 StartY=-201 StartZ=0 EndX=134.428 EndY=-161 EndZ=0
    g12: LineSegment StartX=134.428 StartY=-161 StartZ=0 EndX=134.428 EndY=-131 EndZ=0
    g13: LineSegment StartX=134.428 StartY=-131.025 StartZ=0 EndX=137 EndY=-124 EndZ=0
    g14: LineSegment StartX=137 StartY=-124 StartZ=0 EndX=146.85 EndY=-118.15 EndZ=0
    g15: LineSegment StartX=172.5 StartY=-259 StartZ=0 EndX=178 EndY=-242.5 EndZ=0
    g16: LineSegment StartX=178 StartY=-242.5 StartZ=0 EndX=218 EndY=-242.5 EndZ=0
    g17: LineSegment StartX=218 StartY=-242.5 StartZ=0 EndX=258 EndY=-242.5 EndZ=0
    g18: LineSegment StartX=258 StartY=-242.5 StartZ=0 EndX=292 EndY=-242.5 EndZ=0
    g19: Circle CenterX=178 CenterY=-242.5 CenterZ=0 NormalX=0 NormalY=0 NormalZ=1 AngleXU=0 Radius=1.15
    g20: Circle CenterX=218 CenterY=-242.5 CenterZ=0 NormalX=0 NormalY=0 NormalZ=1 AngleXU=0 Radius=1.15
    g21: Circle CenterX=258 CenterY=-242.5 CenterZ=0 NormalX=0 NormalY=0 NormalZ=1 AngleXU=0 Radius=1.15
    g22: Circle CenterX=258 CenterY=-217.5 CenterZ=0 NormalX=0 NormalY=0 NormalZ=1 AngleXU=0 Radius=1.15
    g23: Circle CenterX=292 CenterY=-242.5 CenterZ=0 NormalX=0 NormalY=0 NormalZ=1 AngleXU=0 Radius=1.15
    g24: Circle CenterX=292 CenterY=-217.5 CenterZ=0 NormalX=0 NormalY=0 NormalZ=1 AngleXU=0 Radius=1.15
    g25: Circle CenterX=292.5 CenterY=-230 CenterZ=0 NormalX=0 NormalY=0 NormalZ=1 AngleXU=0 Radius=1.15
    g26: Circle CenterX=223 CenterY=-217 CenterZ=0 NormalX=0 NormalY=0 NormalZ=1 AngleXU=0 Radius=1.15
    g27: Circle CenterX=197 CenterY=-217 CenterZ=0 NormalX=0 NormalY=0 NormalZ=1 AngleXU=0 Radius=1.15
    g28: Circle CenterX=166.11 CenterY=-217.11 CenterZ=0 NormalX=0 NormalY=0 NormalZ=1 AngleXU=0 Radius=1.15
    g29: Circle CenterX=147.5 CenterY=-239 CenterZ=0 NormalX=0 NormalY=0 NormalZ=1 AngleXU=0 Radius=1.15
    g30: Circle CenterX=141 CenterY=-220 CenterZ=0 NormalX=0 NormalY=0 NormalZ=1 AngleXU=0 Radius=1.15
    g31: Circle CenterX=134.428 CenterY=-201 CenterZ=0 NormalX=0 NormalY=0 NormalZ=1 AngleXU=0 Radius=1.15
    g32: Circle CenterX=160.15 CenterY=-201 CenterZ=0 NormalX=0 NormalY=0 NormalZ=1 AngleXU=0 Radius=1.15
    g33: Circle CenterX=134.428 CenterY=-161 CenterZ=0 NormalX=0 NormalY=0 NormalZ=1 AngleXU=0 Radius=1.15
    g34: Circle CenterX=159.5 CenterY=-161 CenterZ=0 NormalX=0 NormalY=0 NormalZ=1 AngleXU=0 Radius=1.15
    g35: Circle CenterX=137 CenterY=-124 CenterZ=0 NormalX=0 NormalY=0 NormalZ=1 AngleXU=0 Radius=1.15
    g36: Circle CenterX=146.85 CenterY=-118.15 CenterZ=0 NormalX=0 NormalY=0 NormalZ=1 AngleXU=0 Radius=1.15
    g37: Circle CenterX=159 CenterY=-113 CenterZ=0 NormalX=0 NormalY=0 NormalZ=1 AngleXU=0 Radius=1.15
  constraints (50):
    c: Diameter(g0) = 2.3
    c: Diameter(g1) = 2.3
    c: Diameter(g2) = 2.3
    c: Diameter(g7) = 2.3
    c: Diameter(g6) = 2.3
    c: Diameter(g5) = 2.3
    c: Diameter(g3) = 2.3
    c: Diameter(g4) = 2.3
    c: Coincident(g8,g3)
    c: Vertical(g8)
    c: Coincident(g9,g8)
    c: Coincident(g10,g9)
    c: Coincident(g11,g10)
    c: Vertical(g11)
    c: Coincident(g12,g11)
    c: Vertical(g12)
    c: PointOnObject(g13,g12)
    c: Coincident(g14,g13)
    c: Coincident(g15,g4)
    c: Coincident(g16,g15)
    c: Horizontal(g16)
    c: Coincident(g17,g16)
    c: Horizontal(g17)
    c: Coincident(g18,g17)
    c: Horizontal(g18)
    c: Coincident(g19,g15)
    c: Coincident(g20,g16)
    c: Coincident(g21,g17)
    c: Coincident(g23,g18)
    c: Coincident(g29,g8)
    c: Coincident(g30,g9)
    c: Coincident(g31,g10)
    c: Coincident(g33,g11)
    c: Coincident(g35,g13)
    c: Coincident(g36,g14)
    c: Equal(g29,g30)
    c: Equal(g29,g19)
    c: Equal(g29,g28)
    c: Equal(g29,g27)
    c: Equal(g29,g26)
    c: Equal(g29,g20)
    c: Equal(g29,g21)
    c: Equal(g29,g22)
    c: Equal(g29,g24)
    c: Equal(g29,g23)
    c: Equal(g29,g25)
    c: Equal(g29,g32)
    c: Equal(g29,g31)
    c: Equal(g29, g33-g37) x5
    c: Diameter(g29) = 2.3
FEATURE [PartDesign::Pocket] Pocket124
  BaseFeature = -> Fillet075
  Direction = (0,-1e-16,1)
  Length = 3
  Length2 = 5
  Placement = pos=(0,0,0) rot=(1,0,0;3.14159rad)
  Profile = -> Sketch366
  ReferenceAxis = -> Sketch366 [N_Axis]
  Type = 0
FEATURE [Sketcher::SketchObject] Sketch367  label="Wire channels Pocket017"
  FullyConstrained = false
  MapMode = 5
  Placement = pos=(0,0,0) rot=(1,0,0;3.14159rad)
  sketch-geometry (29):
    g0: LineSegment StartX=101.467 StartY=-402.5 StartZ=0 EndX=130.4 EndY=-402.5 EndZ=0
    g1: LineSegment StartX=200 StartY=-200 StartZ=0 EndX=220 EndY=-200 EndZ=0
    g2: LineSegment StartX=135.4 StartY=-402.5 StartZ=0 EndX=135.4 EndY=-397.5 EndZ=0
    g3: LineSegment StartX=135.4 StartY=-397.5 StartZ=0 EndX=175 EndY=-357.904 EndZ=0
    g4: LineSegment StartX=175 StartY=-357.904 StartZ=0 EndX=175 EndY=-245 EndZ=0
    g5: LineSegment StartX=175 StartY=-245 StartZ=0 EndX=290 EndY=-245 EndZ=0
    g6: LineSegment StartX=290 StartY=-245 StartZ=0 EndX=295 EndY=-245 EndZ=0
    g7: LineSegment StartX=295 StartY=-245 StartZ=0 EndX=295 EndY=-215 EndZ=0
    g8: LineSegment StartX=295 StartY=-215 StartZ=0 EndX=290 EndY=-215 EndZ=0
    g9: LineSegment StartX=290 StartY=-215 StartZ=0 EndX=225 EndY=-215 EndZ=0
    g10: LineSegment StartX=225 StartY=-215 StartZ=0 EndX=225 EndY=-200 EndZ=0
    g11: LineSegment StartX=195 StartY=-200 StartZ=0 EndX=195 EndY=-215 EndZ=0
    g12: LineSegment StartX=195 StartY=-215 StartZ=0 EndX=168.46 EndY=-215 EndZ=0
    g13: LineSegment StartX=168.46 StartY=-215 StartZ=0 EndX=162 EndY=-198.36 EndZ=0
    g14: LineSegment StartX=162 StartY=-198.36 StartZ=0 EndX=162 EndY=-115 EndZ=0
    g15: LineSegment StartX=162 StartY=-115 StartZ=0 EndX=162 EndY=-110 EndZ=0
    g16: LineSegment StartX=162 StartY=-110 StartZ=0 EndX=157 EndY=-110 EndZ=0
    g17: LineSegment StartX=157 StartY=-110 StartZ=0 EndX=134.577 EndY=-122.534 EndZ=0
    g18: LineSegment StartX=134.577 StartY=-122.534 StartZ=0 EndX=132 EndY=-126.896 EndZ=0
    g19: LineSegment StartX=132 StartY=-126.896 StartZ=0 EndX=132 EndY=-200.027 EndZ=0
    g20: LineSegment StartX=132 StartY=-200.027 StartZ=0 EndX=144.989 EndY=-239.968 EndZ=0
    g21: LineSegment StartX=144.989 StartY=-239.968 StartZ=0 EndX=144.989 EndY=-343.839 EndZ=0
    g22: LineSegment StartX=144.989 StartY=-343.839 StartZ=0 EndX=96.4674 EndY=-392.5 EndZ=0
    g23: LineSegment StartX=96.4674 StartY=-392.5 StartZ=0 EndX=96.4674 EndY=-397.5 EndZ=0
    g24: LineSegment StartX=96.4674 StartY=-397.5 StartZ=0 EndX=96.4674 EndY=-402.5 EndZ=0
    g25: LineSegment StartX=101.467 StartY=-402.5 StartZ=0 EndX=96.4674 EndY=-402.5 EndZ=0
    g26: LineSegment StartX=130.4 StartY=-402.5 StartZ=0 EndX=135.4 EndY=-402.5 EndZ=0
    g27: LineSegment StartX=225 StartY=-200 StartZ=0 EndX=220 EndY=-200 EndZ=0
    g28: LineSegment StartX=195 StartY=-200 StartZ=0 EndX=200 EndY=-200 EndZ=0
  constraints (78):
    c: Horizontal(g0)
    c: DistanceX(g0,g0) = 28.9326
    c: Horizontal(g1)
    c: DistanceX(g1,g1) = 20
    c: Vertical(g2)
    c: Coincident(g2,g3)
    c: Coincident(g3,g4)
    c: Vertical(g4)
    c: Coincident(g4,g5)
    c: Horizontal(g5)
    c: Coincident(g5,g6)
    c: Horizontal(g6)
    c: Coincident(g6,g7)
    c: Vertical(g7)
    c: Coincident(g7,g8)
    c: Horizontal(g8)
    c: Coincident(g8,g9)
    c: Horizontal(g9)
    c: Coincident(g9,g10)
    c: Vertical(g10)
    c: Vertical(g11)
    c: Coincident(g11,g12)
    c: Horizontal(g12)
    c: Coincident(g12,g13)
    c: Coincident(g13,g14)
    c: Vertical(g14)
    c: Coincident(g14,g15)
    c: Vertical(g15)
    c: Coincident(g15,g16)
    c: Horizontal(g16)
    c: Coincident(g16,g17)
    c: Coincident(g17,g18)
    c: Coincident(g18,g19)
    c: Vertical(g19)
    c: Coincident(g19,g20)
    c: Coincident(g20,g21)
    c: Vertical(g21)
    c: Coincident(g21,g22)
    c: Coincident(g22,g23)
    c: Vertical(g23)
    c: Coincident(g23,g24)
    c: Vertical(g24)
    c: Coincident(g25,g0)
    c: Coincident(g25,g24)
    c: Horizontal(g25)
    c: Coincident(g26,g0)
    c: Coincident(g26,g2)
    c: Horizontal(g26)
    c: Coincident(g27,g10)
    c: Coincident(g27,g1)
    c: Horizontal(g27)
    c: Coincident(g28,g11)
    c: Coincident(g28,g1)
    c: Horizontal(g28)
    c: DistanceX(g25,g25) = 5
    c: DistanceX(g26,g26) = 5
    c: DistanceY(g24,g24) = 5
    c: DistanceY(g23,g23) = 5
    c: DistanceY(g2,g2) = 5
    c: Distance(g22) = 68.7186
    c: Distance(g3) = 56
    c: DistanceY(g21,g21) = 103.871
    c: DistanceY(g4,g4) = 112.904
    c: DistanceX(g5,g5) = 115
    c: DistanceX(g12,g12) = 26.54
    c: DistanceX(g9,g9) = 65
    c: Distance(g20) = 42
    c: DistanceY(g19,g19) = 73.1311
    c: DistanceY(g14,g14) = 83.36
    c: DistanceX(g27,g27) = 5
    c: DistanceX(g28,g28) = 5
    c: DistanceX(g8,g8) = 5
    c: DistanceX(g6,g6) = 5
    c: DistanceY(g7,g7) = 30
    c: Distance(g17) = 25.6886
    c: Distance(g18) = 5.06593
    c: Distance(g16) = 5
    c: DistanceY(g15,g15) = 5
FEATURE [PartDesign::Pad] Pad025
  Direction = (0,0,-1)
  Length = 3
  Length2 = 10
  Placement = pos=(0,0,0) rot=(1,0,0;3.14159rad)
  Profile = -> Sketch367
  ReferenceAxis = -> Sketch367 [N_Axis]
  Type = 0
FEATURE [PartDesign::Fillet] Fillet076
  Base = -> Pad025 [Edge2,Edge5,Edge8,Edge14,Edge17,Edge20,Edge23,Edge26,Edge29,Edge32,Edge35,Edge53,Edge56,Edge59,Edge65,Edge68,Edge74]
  BaseFeature = -> Pad025
  Placement = pos=(0,0,0) rot=(1,0,0;3.14159rad)
  Radius = 3.35
  SupportTransform = false
  UseAllEdges = false
FEATURE [Sketcher::SketchObject] Sketch368
  FullyConstrained = false
  MapMode = 5
  Placement = pos=(0,0,-3) rot=(1,0,0;3.14159rad)
  Support = -> [Fillet076]
  sketch-geometry (38):
    g0: Circle CenterX=105 CenterY=-389 CenterZ=0 NormalX=0 NormalY=0 NormalZ=1 AngleXU=0 Radius=1.15
    g1: Circle CenterX=145 CenterY=-349 CenterZ=0 NormalX=0 NormalY=0 NormalZ=1 AngleXU=0 Radius=1.15
    g2: Circle CenterX=147.5 CenterY=-309 CenterZ=0 NormalX=0 NormalY=0 NormalZ=1 AngleXU=0 Radius=1.15
    g3: Circle CenterX=147.5 CenterY=-259 CenterZ=0 NormalX=0 NormalY=0 NormalZ=1 AngleXU=0 Radius=1.15
    g4: Circle CenterX=172.5 CenterY=-259 CenterZ=0 NormalX=0 NormalY=0 NormalZ=1 AngleXU=0 Radius=1.15
    g5: Circle CenterX=172.5 CenterY=-309 CenterZ=0 NormalX=0 NormalY=0 NormalZ=1 AngleXU=0 Radius=1.15
    g6: Circle CenterX=172.5 CenterY=-349 CenterZ=0 NormalX=0 NormalY=0 NormalZ=1 AngleXU=0 Radius=1.15
    g7: Circle CenterX=147.665 CenterY=-382.765 CenterZ=0 NormalX=0 NormalY=0 NormalZ=1 AngleXU=0 Radius=1.15
    g8: LineSegment StartX=147.5 StartY=-259 StartZ=0 EndX=147.5 EndY=-239 EndZ=0
    g9: LineSegment StartX=147.5 StartY=-239 StartZ=0 EndX=141 EndY=-220 EndZ=0
    g10: LineSegment StartX=141 StartY=-220 StartZ=0 EndX=134.428 EndY=-201 EndZ=0
    g11: LineSegment StartX=134.428 StartY=-201 StartZ=0 EndX=134.428 EndY=-161 EndZ=0
    g12: LineSegment StartX=134.428 StartY=-161 StartZ=0 EndX=134.428 EndY=-131 EndZ=0
    g13: LineSegment StartX=134.428 StartY=-131.025 StartZ=0 EndX=137 EndY=-124 EndZ=0
    g14: LineSegment StartX=137 StartY=-124 StartZ=0 EndX=146.85 EndY=-118.15 EndZ=0
    g15: LineSegment StartX=172.5 StartY=-259 StartZ=0 EndX=178 EndY=-242.5 EndZ=0
    g16: LineSegment StartX=178 StartY=-242.5 StartZ=0 EndX=218 EndY=-242.5 EndZ=0
    g17: LineSegment StartX=218 StartY=-242.5 StartZ=0 EndX=258 EndY=-242.5 EndZ=0
    g18: LineSegment StartX=258 StartY=-242.5 StartZ=0 EndX=292 EndY=-242.5 EndZ=0
    g19: Circle CenterX=178 CenterY=-242.5 CenterZ=0 NormalX=0 NormalY=0 NormalZ=1 AngleXU=0 Radius=1.15
    g20: Circle CenterX=218 CenterY=-242.5 CenterZ=0 NormalX=0 NormalY=0 NormalZ=1 AngleXU=0 Radius=1.15
    g21: Circle CenterX=258 CenterY=-242.5 CenterZ=0 NormalX=0 NormalY=0 NormalZ=1 AngleXU=0 Radius=1.15
    g22: Circle CenterX=258 CenterY=-217.5 CenterZ=0 NormalX=0 NormalY=0 NormalZ=1 AngleXU=0 Radius=1.15
    g23: Circle CenterX=292 CenterY=-242.5 CenterZ=0 NormalX=0 NormalY=0 NormalZ=1 AngleXU=0 Radius=1.15
    g24: Circle CenterX=292 CenterY=-217.5 CenterZ=0 NormalX=0 NormalY=0 NormalZ=1 AngleXU=0 Radius=1.15
    g25: Circle CenterX=292.5 CenterY=-230 CenterZ=0 NormalX=0 NormalY=0 NormalZ=1 AngleXU=0 Radius=1.15
    g26: Circle CenterX=223 CenterY=-217 CenterZ=0 NormalX=0 NormalY=0 NormalZ=1 AngleXU=0 Radius=1.15
    g27: Circle CenterX=197 CenterY=-217 CenterZ=0 NormalX=0 NormalY=0 NormalZ=1 AngleXU=0 Radius=1.15
    g28: Circle CenterX=166.11 CenterY=-217.11 CenterZ=0 NormalX=0 NormalY=0 NormalZ=1 AngleXU=0 Radius=1.15
    g29: Circle CenterX=147.5 CenterY=-239 CenterZ=0 NormalX=0 NormalY=0 NormalZ=1 AngleXU=0 Radius=1.15
    g30: Circle CenterX=141 CenterY=-220 CenterZ=0 NormalX=0 NormalY=0 NormalZ=1 AngleXU=0 Radius=1.15
    g31: Circle CenterX=134.428 CenterY=-201 CenterZ=0 NormalX=0 NormalY=0 NormalZ=1 AngleXU=0 Radius=1.15
    g32: Circle CenterX=160.15 CenterY=-201 CenterZ=0 NormalX=0 NormalY=0 NormalZ=1 AngleXU=0 Radius=1.15
    g33: Circle CenterX=134.428 CenterY=-161 CenterZ=0 NormalX=0 NormalY=0 NormalZ=1 AngleXU=0 Radius=1.15
    g34: Circle CenterX=159.5 CenterY=-161 CenterZ=0 NormalX=0 NormalY=0 NormalZ=1 AngleXU=0 Radius=1.15
    g35: Circle CenterX=137 CenterY=-124 CenterZ=0 NormalX=0 NormalY=0 NormalZ=1 AngleXU=0 Radius=1.15
    g36: Circle CenterX=146.85 CenterY=-118.15 CenterZ=0 NormalX=0 NormalY=0 NormalZ=1 AngleXU=0 Radius=1.15
    g37: Circle CenterX=159 CenterY=-113 CenterZ=0 NormalX=0 NormalY=0 NormalZ=1 AngleXU=0 Radius=1.15
  constraints (50):
    c: Diameter(g0) = 2.3
    c: Diameter(g1) = 2.3
    c: Diameter(g2) = 2.3
    c: Diameter(g7) = 2.3
    c: Diameter(g6) = 2.3
    c: Diameter(g5) = 2.3
    c: Diameter(g3) = 2.3
    c: Diameter(g4) = 2.3
    c: Coincident(g8,g3)
    c: Vertical(g8)
    c: Coincident(g9,g8)
    c: Coincident(g10,g9)
    c: Coincident(g11,g10)
    c: Vertical(g11)
    c: Coincident(g12,g11)
    c: Vertical(g12)
    c: PointOnObject(g13,g12)
    c: Coincident(g14,g13)
    c: Coincident(g15,g4)
    c: Coincident(g16,g15)
    c: Horizontal(g16)
    c: Coincident(g17,g16)
    c: Horizontal(g17)
    c: Coincident(g18,g17)
    c: Horizontal(g18)
    c: Coincident(g19,g15)
    c: Coincident(g20,g16)
    c: Coincident(g21,g17)
    c: Coincident(g23,g18)
    c: Coincident(g29,g8)
    c: Coincident(g30,g9)
    c: Coincident(g31,g10)
    c: Coincident(g33,g11)
    c: Coincident(g35,g13)
    c: Coincident(g36,g14)
    c: Equal(g29,g30)
    c: Equal(g29,g19)
    c: Equal(g29,g28)
    c: Equal(g29,g27)
    c: Equal(g29,g26)
    c: Equal(g29,g20)
    c: Equal(g29,g21)
    c: Equal(g29,g22)
    c: Equal(g29,g24)
    c: Equal(g29,g23)
    c: Equal(g29,g25)
    c: Equal(g29,g32)
    c: Equal(g29,g31)
    c: Equal(g29, g33-g37) x5
    c: Diameter(g29) = 2.3
FEATURE [PartDesign::Pocket] Pocket125
  BaseFeature = -> Fillet076
  Direction = (0,0,1)
  Length = 3
  Length2 = 5
  Placement = pos=(0,0,0) rot=(1,0,0;3.14159rad)
  Profile = -> Sketch368
  ReferenceAxis = -> Sketch368 [N_Axis]
  Type = 0
FEATURE [Sketcher::SketchObject] Sketch369
  FullyConstrained = false
  MapMode = 5
  Placement = pos=(0,0,-3) rot=(1,0,0;3.14159rad)
  Support = -> [Pocket124]
  sketch-geometry (8):
    g0: LineSegment StartX=172.5 StartY=-259 StartZ=0 EndX=172.5 EndY=-249 EndZ=0
    g1: LineSegment StartX=175 StartY=-249 StartZ=0 EndX=130 EndY=-249 EndZ=0
    g2: LineSegment StartX=130 StartY=-249 StartZ=0 EndX=130 EndY=-100 EndZ=0
    g3: LineSegment StartX=130 StartY=-100 StartZ=0 EndX=170 EndY=-100 EndZ=0
    g4: LineSegment StartX=170 StartY=-100 StartZ=0 EndX=170 EndY=-190 EndZ=0
    g5: LineSegment StartX=170 StartY=-190 StartZ=0 EndX=300 EndY=-190 EndZ=0
    g6: LineSegment StartX=300 StartY=-190 StartZ=0 EndX=300 EndY=-249 EndZ=0
    g7: LineSegment StartX=300 StartY=-249 StartZ=0 EndX=175 EndY=-249 EndZ=0
  constraints (15):
    c: Vertical(g0)
    c: Horizontal(g1)
    c: Coincident(g1,g2)
    c: Vertical(g2)
    c: Coincident(g2,g3)
    c: Horizontal(g3)
    c: Coincident(g3,g4)
    c: Vertical(g4)
    c: Coincident(g4,g5)
    c: Horizontal(g5)
    c: Coincident(g5,g6)
    c: Vertical(g6)
    c: Coincident(g6,g7)
    c: Coincident(g7,g1)
    c: Horizontal(g7)
FEATURE [PartDesign::Pocket] Pocket126
  BaseFeature = -> Pocket124
  Direction = (0,-2e-16,1)
  Length = 5
  Length2 = 5
  Placement = pos=(0,0,0) rot=(1,0,0;3.14159rad)
  Profile = -> Sketch369
  ReferenceAxis = -> Sketch369 [N_Axis]
  Type = 0
FEATURE [Sketcher::SketchObject] Sketch370
  FullyConstrained = false
  MapMode = 5
  Placement = pos=(0,0,-3) rot=(1,0,0;3.14159rad)
  Support = -> [Pocket126]
  sketch-geometry (4):
    g0: LineSegment StartX=144 StartY=-249 StartZ=0 EndX=175 EndY=-249 EndZ=0
    g1: LineSegment StartX=175 StartY=-249 StartZ=0 EndX=175 EndY=-269 EndZ=0
    g2: LineSegment StartX=175 StartY=-269 StartZ=0 EndX=144 EndY=-269 EndZ=0
    g3: LineSegment StartX=144 StartY=-269 StartZ=0 EndX=144 EndY=-249 EndZ=0
  constraints (8):
    c: Coincident(g0,g1)
    c: Coincident(g1,g2)
    c: Coincident(g2,g3)
    c: Coincident(g3,g0)
    c: Horizontal(g0)
    c: Horizontal(g2)
    c: Vertical(g1)
    c: Vertical(g3)
FEATURE [PartDesign::Pocket] Pocket127
  BaseFeature = -> Pocket126
  Direction = (0,-4e-16,1)
  Length = 1.5
  Length2 = 5
  Placement = pos=(0,0,0) rot=(1,0,0;3.14159rad)
  Profile = -> Sketch370
  ReferenceAxis = -> Sketch370 [N_Axis]
  Type = 0
FEATURE [PartDesign::Chamfer] Chamfer003
  Angle = 45
  Base = -> Pocket127 [Edge74,Edge24]
  BaseFeature = -> Pocket127
  ChamferType = 0
  FlipDirection = false
  Placement = pos=(0,0,0) rot=(1,0,0;3.14159rad)
  Size = 1.49
  Size2 = 1
  SupportTransform = false
  UseAllEdges = false
FEATURE [PartDesign::Body] Body037  label="Back Plate 005"
  Group = -> [Sketch365,Pad024,Fillet075,Sketch366,Pocket124,Sketch369,Pocket126,Sketch370,Pocket127,Chamfer003]
  Origin = -> Origin223
  Placement = pos=(-228,-214,-1) rot=(0.707107,0.707107,0;3.14159rad)
  Tip = -> Chamfer003
FEATURE [Sketcher::SketchObject] Sketch371
  FullyConstrained = false
  MapMode = 5
  Placement = pos=(0,0,-3) rot=(1,0,0;3.14159rad)
  Support = -> [Pocket125]
  sketch-geometry (8):
    g0: LineSegment StartX=147.5 StartY=-259 StartZ=0 EndX=147.5 EndY=-249 EndZ=0
    g1: LineSegment StartX=145 StartY=-249 StartZ=0 EndX=145 EndY=-269 EndZ=0
    g2: LineSegment StartX=145 StartY=-269 StartZ=0 EndX=175 EndY=-269 EndZ=0
    g3: LineSegment StartX=175 StartY=-269 StartZ=0 EndX=176 EndY=-269 EndZ=0
    g4: LineSegment StartX=176 StartY=-269 StartZ=0 EndX=176 EndY=-410 EndZ=0
    g5: LineSegment StartX=176 StartY=-410 StartZ=0 EndX=90 EndY=-410 EndZ=0
    g6: LineSegment StartX=90 StartY=-410 StartZ=0 EndX=90 EndY=-269 EndZ=0
    g7: LineSegment StartX=90 StartY=-269 StartZ=0 EndX=145 EndY=-269 EndZ=0
  constraints (15):
    c: Vertical(g0)
    c: Vertical(g1)
    c: Coincident(g1,g2)
    c: Horizontal(g2)
    c: Coincident(g2,g3)
    c: Horizontal(g3)
    c: Coincident(g3,g4)
    c: Vertical(g4)
    c: Coincident(g4,g5)
    c: Horizontal(g5)
    c: Coincident(g5,g6)
    c: Vertical(g6)
    c: Coincident(g6,g7)
    c: Coincident(g7,g2)
    c: Horizontal(g7)
FEATURE [PartDesign::Pocket] Pocket128
  BaseFeature = -> Pocket125
  Direction = (0,-1e-16,1)
  Length = 5
  Length2 = 5
  Placement = pos=(0,0,0) rot=(1,0,0;3.14159rad)
  Profile = -> Sketch371
  ReferenceAxis = -> Sketch371 [N_Axis]
  Type = 0
FEATURE [Sketcher::SketchObject] Sketch372
  FullyConstrained = false
  MapMode = 5
  Support = -> [Pocket128]
  sketch-geometry (4):
    g0: LineSegment StartX=144 StartY=269 StartZ=0 EndX=176 EndY=269 EndZ=0
    g1: LineSegment StartX=176 StartY=269 StartZ=0 EndX=176 EndY=249 EndZ=0
    g2: LineSegment StartX=176 StartY=249 StartZ=0 EndX=144 EndY=249 EndZ=0
    g3: LineSegment StartX=144 StartY=249 StartZ=0 EndX=144 EndY=269 EndZ=0
  constraints (8):
    c: Coincident(g0,g1)
    c: Coincident(g1,g2)
    c: Coincident(g2,g3)
    c: Coincident(g3,g0)
    c: Horizontal(g0)
    c: Horizontal(g2)
    c: Vertical(g1)
    c: Vertical(g3)
FEATURE [PartDesign::Pocket] Pocket129
  BaseFeature = -> Pocket128
  Direction = (0,2e-16,-1)
  Length = 1.5
  Length2 = 5
  Placement = pos=(0,0,0) rot=(1,0,0;3.14159rad)
  Profile = -> Sketch372
  ReferenceAxis = -> Sketch372 [N_Axis]
  Type = 0
FEATURE [PartDesign::Chamfer] Chamfer004
  Angle = 45
  Base = -> Pocket129 [Edge173,Edge136]
  BaseFeature = -> Pocket129
  ChamferType = 0
  FlipDirection = false
  Placement = pos=(0,0,0) rot=(1,0,0;3.14159rad)
  Size = 1.49
  Size2 = 1
  SupportTransform = false
  UseAllEdges = false
FEATURE [PartDesign::Body] Body038  label="Back Plate 006"
  Group = -> [Sketch367,Pad025,Fillet076,Sketch368,Pocket125,Sketch371,Pocket128,Sketch372,Pocket129,Chamfer004]
  Origin = -> Origin224
  Placement = pos=(-20,129,4) rot=(0,0,-1;1.5708rad)
  Tip = -> Chamfer004
FEATURE [Sketcher::SketchObject] Sketch373  label="control plate mount pocket006"
  FullyConstrained = false
  MapMode = 5
  Placement = pos=(0,0,45) rot=(0,0,1;0rad)
  sketch-geometry (6):
    g0: LineSegment StartX=267.9 StartY=263.3 StartZ=0 EndX=267.9 EndY=243.3 EndZ=0
    g1: LineSegment StartX=267.9 StartY=243.3 StartZ=0 EndX=272.9 EndY=243.3 EndZ=0
    g2: LineSegment StartX=282 StartY=258 StartZ=0 EndX=337 EndY=258 EndZ=0
    g3: LineSegment StartX=282 StartY=258 StartZ=0 EndX=282 EndY=172 EndZ=0
    g4: LineSegment StartX=282 StartY=172 StartZ=0 EndX=365.925 EndY=172 EndZ=0
    g5: LineSegment StartX=365.925 StartY=172 StartZ=0 EndX=337 EndY=258 EndZ=0
  constraints (12):
    c: Vertical(g0)
    c: Coincident(g1,g0)
    c: Horizontal(g1)
    c: Horizontal(g2)
    c: Coincident(g3,g2)
    c: Vertical(g3)
    c: DistanceY(g3,g3) = 86
    c: Coincident(g4,g3)
    c: Horizontal(g4)
    c: Coincident(g5,g4)
    c: Coincident(g5,g2)
    c: Distance(g5) = 90.7339
FEATURE [PartDesign::Pad] Pad026  label="Main Plate001"
  Direction = (0,0,1)
  Length = 3
  Length2 = 10
  Placement = pos=(0,0,45) rot=(0,0,1;0rad)
  Profile = -> Sketch373
  ReferenceAxis = -> Sketch373 [N_Axis]
  Type = 0
FEATURE [PartDesign::Fillet] Fillet077  label="Corner edges 001"
  Base = -> Pad026 [Edge5,Edge8,Edge1,Edge2]
  BaseFeature = -> Pad026
  Placement = pos=(0,0,45) rot=(0,0,1;0rad)
  Radius = 6
  SupportTransform = false
  UseAllEdges = false
FEATURE [Sketcher::SketchObject] Sketch374  label="Pot holes001"
  FullyConstrained = false
  MapMode = 5
  Placement = pos=(0,0,48) rot=(0,0,1;0rad)
  Support = -> [Fillet077]
  sketch-geometry (3):
    g0: Circle CenterX=302 CenterY=230 CenterZ=0 NormalX=0 NormalY=0 NormalZ=1 AngleXU=0 Radius=3.75
    g1: LineSegment StartX=310.5 StartY=200 StartZ=0 EndX=302 EndY=200 EndZ=0
    g2: Circle CenterX=302 CenterY=200 CenterZ=0 NormalX=0 NormalY=0 NormalZ=1 AngleXU=0 Radius=3.75
  constraints (4):
    c: Diameter(g0) = 7.5
    c: Horizontal(g1)
    c: Coincident(g2,g1)
    c: Diameter(g2) = 7.5
FEATURE [PartDesign::Pocket] Pocket130  label="Potentiometer holes001"
  BaseFeature = -> Fillet077
  Direction = (0,0,-1)
  Length = 5
  Length2 = 5
  Placement = pos=(0,0,45) rot=(0,0,1;0rad)
  Profile = -> Sketch374
  ReferenceAxis = -> Sketch374 [N_Axis]
  Type = 0
FEATURE [Sketcher::SketchObject] Sketch375  label="Selector Switch Slit and mounting holes001"
  FullyConstrained = false
  MapMode = 5
  Placement = pos=(0,0,48) rot=(0,0,1;0rad)
  Support = -> [Pocket130]
  sketch-geometry (18):
    g0: LineSegment StartX=326.216 StartY=240.209 StartZ=0 EndX=325.616 EndY=240.209 EndZ=0
    g1: LineSegment StartX=326.216 StartY=240.209 StartZ=0 EndX=320.985 EndY=238.509 EndZ=0
    g2: LineSegment StartX=320.985 StartY=238.509 StartZ=0 EndX=322.023 EndY=235.313 EndZ=0
    g3: Circle CenterX=322.023 CenterY=235.313 CenterZ=0 NormalX=0 NormalY=0 NormalZ=1 AngleXU=0 Radius=1.75
    g4: LineSegment StartX=341.048 StartY=194.558 StartZ=0 EndX=339.648 EndY=194.558 EndZ=0
    g5: LineSegment StartX=341.048 StartY=194.558 StartZ=0 EndX=335.818 EndY=192.858 EndZ=0
    g6: LineSegment StartX=335.818 StartY=192.858 StartZ=0 EndX=334.779 EndY=196.054 EndZ=0
    g7: Circle CenterX=334.779 CenterY=196.054 CenterZ=0 NormalX=0 NormalY=0 NormalZ=1 AngleXU=0 Radius=1.75
    g8: LineSegment StartX=322.023 StartY=235.313 StartZ=0 EndX=334.779 EndY=196.054 EndZ=0
    g9: LineSegment StartX=334.238 StartY=197.718 StartZ=0 EndX=333.263 EndY=200.72 EndZ=0
    g10: LineSegment StartX=333.263 StartY=200.72 StartZ=0 EndX=334.214 EndY=201.029 EndZ=0
    g11: LineSegment StartX=322.564 StartY=233.649 StartZ=0 EndX=323.538 EndY=230.65 EndZ=0
    g12: LineSegment StartX=334.238 StartY=197.718 StartZ=0 EndX=333.263 EndY=200.72 EndZ=0
    g13: LineSegment StartX=334.214 StartY=201.029 StartZ=0 EndX=324.49 EndY=230.959 EndZ=0
    g14: LineSegment StartX=333.263 StartY=200.72 StartZ=0 EndX=332.312 EndY=200.412 EndZ=0
    g15: LineSegment StartX=322.587 StartY=230.341 StartZ=0 EndX=332.312 EndY=200.412 EndZ=0
    g16: LineSegment StartX=323.538 StartY=230.65 StartZ=0 EndX=322.587 EndY=230.341 EndZ=0
    g17: LineSegment StartX=323.538 StartY=230.65 StartZ=0 EndX=324.49 EndY=230.959 EndZ=0
  constraints (44):
    c: Horizontal(g0)
    c: Coincident(g1,g0)
    c: DistanceX(g0,g0) = 0.6
    c: Angle(g0,g1) = 0.314159
    c: Distance(g1) = 5.5
    c: Coincident(g2,g1)
    c: Coincident(g3,g2)
    c: Diameter(g3) = 3.5
    c: Angle(g2,g0) = 1.25664
    c: Distance(g2) = 3.36
    c: Horizontal(g4)
    c: Coincident(g5,g4)
    c: DistanceX(g4,g4) = 1.4
    c: Distance(g5) = 5.5
    c: Angle(g4,g5) = 0.314159
    c: Coincident(g6,g5)
    c: Distance(g6) = 3.36
    c: Angle(g6,g4) = 1.25664
    c: Coincident(g7,g6)
    c: Diameter(g7) = 3.5
    c: Coincident(g8,g3)
    c: Coincident(g8,g7)
    c: PointOnObject(g9,g7)
    c: PointOnObject(g9,g8)
    c: Coincident(g9,g10)
    c: PointOnObject(g11,g8)
    c: PointOnObject(g11,g8)
    c: Distance(g11) = 3.15373
    c: Coincident(g12,g9)
    c: Coincident(g12,g10)
    c: Distance(g12) = 3.1567
    c: Distance(g10) = 1
    c: Angle(g12,g10) = 1.5708
    c: Coincident(g13,g10)
    c: Coincident(g14,g10)
    c: Distance(g14) = 1
    c: Angle(g14,g12) = 1.5708
    c: Coincident(g15,g14)
    c: Distance(g13) = 31.4696
    c: Coincident(g16,g11)
    c: Coincident(g16,g15)
    c: Coincident(g17,g16)
    c: Coincident(g17,g13)
    c: Distance(g16) = 1
FEATURE [PartDesign::Pocket] Pocket131
  BaseFeature = -> Pocket130
  Direction = (0,0,-1)
  Length = 3
  Length2 = 5
  Placement = pos=(0,0,45) rot=(0,0,1;0rad)
  Profile = -> Sketch375
  ReferenceAxis = -> Sketch375 [N_Axis]
  Type = 0
FEATURE [Sketcher::SketchObject] Sketch376
  FullyConstrained = false
  MapMode = 5
  Placement = pos=(0,0,48) rot=(0,0,1;0rad)
  Support = -> [Pocket131]
  sketch-geometry (8):
    g0: Circle CenterX=287 CenterY=178.79 CenterZ=0 NormalX=0 NormalY=0 NormalZ=1 AngleXU=0 Radius=1.65
    g1: Circle CenterX=287.6 CenterY=252 CenterZ=0 NormalX=0 NormalY=0 NormalZ=1 AngleXU=0 Radius=1.65
    g2: Circle CenterX=333.1 CenterY=252.5 CenterZ=0 NormalX=0 NormalY=0 NormalZ=1 AngleXU=0 Radius=1.65
    g3: Circle CenterX=357 CenterY=179 CenterZ=0 NormalX=0 NormalY=0 NormalZ=1 AngleXU=0 Radius=1.65
    g4: LineSegment StartX=336.506 StartY=256.572 StartZ=0 EndX=333.1 EndY=252.5 EndZ=0
    g5: LineSegment StartX=284 StartY=256.277 StartZ=0 EndX=287.6 EndY=252 EndZ=0
    g6: LineSegment StartX=283.266 StartY=174.455 StartZ=0 EndX=287 EndY=178.792 EndZ=0
    g7: LineSegment StartX=350.571 StartY=183.276 StartZ=0 EndX=357 EndY=179 EndZ=0
  constraints (4):
    c: Equal(g1,g2)
    c: Equal(g1,g0)
    c: Equal(g1,g3)
    c: Diameter(g1) = 3.3
FEATURE [PartDesign::Pocket] Pocket132
  BaseFeature = -> Pocket131
  Direction = (0,0,-1)
  Length = 3
  Length2 = 5
  Placement = pos=(0,0,45) rot=(0,0,1;0rad)
  Profile = -> Sketch376
  ReferenceAxis = -> Sketch376 [N_Axis]
  Type = 0
FEATURE [PartDesign::Body] Body039  label="Control Cavity Plate template"
  Group = -> [Sketch373,Pad026,Fillet077,Sketch374,Pocket130,Sketch375,Pocket131,Sketch376,Pocket132]
  Origin = -> Origin226
  Placement = pos=(-118,-728,-40.9) rot=(0,0,1;0rad)
  Tip = -> Pocket132
FEATURE [PartDesign::Pocket] Pocket133
  BaseFeature = -> Pocket034
  Direction = (0.51693,0.856028,-2e-16)
  Length = 5
  Length2 = 5
  Profile = -> Sketch192
  ReferenceAxis = -> Sketch192 [N_Axis]
  Type = 0
FEATURE [Part::Compound] Compound  label="IO plate template"
  Links = -> [Pocket133]
  Placement = pos=(112.609,-99.1298,148.183) rot=(-0.198707,-0.685449,0.700482;3.52073rad)
FEATURE [Sketcher::SketchObject] Sketch377
  FullyConstrained = false
  MapMode = 5
  Support = -> [XY_Plane227]
  sketch-geometry (4):
    g0: LineSegment StartX=400 StartY=-100 StartZ=0 EndX=697 EndY=-100 EndZ=0
    g1: LineSegment StartX=697 StartY=-100 StartZ=0 EndX=697 EndY=-310 EndZ=0
    g2: LineSegment StartX=697 StartY=-310 StartZ=0 EndX=400 EndY=-310 EndZ=0
    g3: LineSegment StartX=400 StartY=-310 StartZ=0 EndX=400 EndY=-100 EndZ=0
  constraints (10):
    c: Coincident(g0,g1)
    c: Coincident(g1,g2)
    c: Coincident(g2,g3)
    c: Coincident(g3,g0)
    c: Horizontal(g0)
    c: Horizontal(g2)
    c: Vertical(g1)
    c: Vertical(g3)
    c: DistanceX(g0,g0) = 297
    c: DistanceY(g3,g3) = 210
FEATURE [PartDesign::Pad] Pad027
  Direction = (0,0,1)
  Length = 3
  Length2 = 10
  Profile = -> Sketch377
  ReferenceAxis = -> Sketch377 [N_Axis]
  Type = 0
FEATURE [PartDesign::Body] Body040
  Group = -> [Sketch377,Pad027]
  Origin = -> Origin227
  Tip = -> Pad027
FEATURE [Sketcher::SketchObject] Sketch378
  FullyConstrained = false
  MapMode = 5
  Support = -> [XY_Plane228]
  sketch-geometry (4):
    g0: LineSegment StartX=400 StartY=-100 StartZ=0 EndX=697 EndY=-100 EndZ=0
    g1: LineSegment StartX=697 StartY=-100 StartZ=0 EndX=697 EndY=-310 EndZ=0
    g2: LineSegment StartX=697 StartY=-310 StartZ=0 EndX=400 EndY=-310 EndZ=0
    g3: LineSegment StartX=400 StartY=-310 StartZ=0 EndX=400 EndY=-100 EndZ=0
  constraints (10):
    c: Coincident(g0,g1)
    c: Coincident(g1,g2)
    c: Coincident(g2,g3)
    c: Coincident(g3,g0)
    c: Horizontal(g0)
    c: Horizontal(g2)
    c: Vertical(g1)
    c: Vertical(g3)
    c: DistanceX(g0,g0) = 297
    c: DistanceY(g3,g3) = 210
FEATURE [PartDesign::Pad] Pad028
  Direction = (0,0,1)
  Length = 3
  Length2 = 10
  Profile = -> Sketch378
  ReferenceAxis = -> Sketch378 [N_Axis]
  Type = 0
FEATURE [PartDesign::Body] Body041
  Group = -> [Sketch378,Pad028]
  Origin = -> Origin228
  Tip = -> Pad028
FEATURE [App::Part] Part054  label="Wire Channel back Plate001"
  Group = -> [Body037,Body038,Body040,Body041]
  Origin = -> Origin225
  Placement = pos=(0,0,8) rot=(0,0,1;0rad)
FEATURE [Part::Feature] Part__Feature567  label="sleeve enclosure top plate001"
  Placement = pos=(-13.1,-589,10) rot=(0,1,0;3.14159rad)
  shape: bbox 112.8 x 130 x 3 mm, 32 faces (baked)
FEATURE [Sketcher::SketchObject] Sketch379
  FullyConstrained = true
  MapMode = 5
  Support = -> [XY_Plane229]
  sketch-geometry (4):
    g0: LineSegment StartX=0 StartY=0 StartZ=0 EndX=270 EndY=0 EndZ=0
    g1: LineSegment StartX=270 StartY=0 StartZ=0 EndX=270 EndY=-170 EndZ=0
    g2: LineSegment StartX=270 StartY=-170 StartZ=0 EndX=0 EndY=-170 EndZ=0
    g3: LineSegment StartX=0 StartY=-170 StartZ=0 EndX=0 EndY=0 EndZ=0
  constraints (11):
    c: Coincident(g0,g1)
    c: Coincident(g1,g2)
    c: Coincident(g2,g3)
    c: Coincident(g3,g0)
    c: Horizontal(g0)
    c: Horizontal(g2)
    c: Vertical(g1)
    c: Vertical(g3)
    c: Coincident(g0,g-1)
    c: DistanceX(g0,g0) = 270
    c: DistanceY(g3,g3) = 170
FEATURE [PartDesign::Pad] Pad029
  Direction = (0,0,1)
  Length = 3
  Length2 = 10
  Profile = -> Sketch379
  ReferenceAxis = -> Sketch379 [N_Axis]
  Type = 0
FEATURE [PartDesign::Body] Body042  label="Template cnc 003"
  Group = -> [Sketch379,Pad029]
  Origin = -> Origin229
  Placement = pos=(0,-428.7,0) rot=(0,0,1;0rad)
  Tip = -> Pad029
FEATURE [App::Part] Part053  label="Acrylic plate cutout fitting"
  Group = -> [Body034,Body035,Part054,Body036,Body039,Part__Feature567,Body042]
  Origin = -> Origin218
FEATURE [TechDraw::DrawSVGTemplate] Template002
  Height = 594
  Orientation = 1
  Template = C:/Program Files/FreeCAD 0.21/data/Mod/TechDraw/Templates/A1_Landscape_blank.svg
  Width = 841
FEATURE [TechDraw::DrawViewPart] View004
  CoarseView = false
  Direction = (0,0,1)
  Focus = 100
  HardHidden = false
  IsoCount = 0
  IsoHidden = false
  IsoVisible = false
  LockPosition = false
  Perspective = false
  Rotation = 0
  ScaleType = 0
  ScrubCount = 0
  SeamHidden = false
  SeamVisible = false
  SmoothHidden = false
  SmoothVisible = true
  Source = -> [Body027]
  X = 210.59
  XDirection = (1,0,0)
  Y = 299.233
FEATURE [TechDraw::DrawViewPart] View005
  CoarseView = false
  Direction = (0,0,1)
  Focus = 100
  HardHidden = false
  IsoCount = 0
  IsoHidden = false
  IsoVisible = false
  LockPosition = false
  Perspective = false
  Rotation = 0
  ScaleType = 0
  ScrubCount = 0
  SeamHidden = false
  SeamVisible = false
  SmoothHidden = false
  SmoothVisible = true
  Source = -> [Fillet055]
  X = 612.545
  XDirection = (1,0,0)
  Y = 299.233
FEATURE [TechDraw::DrawPage] Page002
  KeepUpdated = true
  NextBalloonIndex = 1
  ProjectionType = 0
  Template = -> Template002
  Views = -> [View004,View005]
FEATURE [TechDraw::DrawSVGTemplate] Template003
  Height = 594
  Orientation = 1
  Template = C:/Program Files/FreeCAD 0.21/data/Mod/TechDraw/Templates/A1_Landscape_blank.svg
  Width = 841
FEATURE [TechDraw::DrawViewPart] View006
  CoarseView = false
  Direction = (0,0,1)
  Focus = 100
  HardHidden = false
  IsoCount = 0
  IsoHidden = false
  IsoVisible = false
  LockPosition = false
  Perspective = false
  Rotation = 0
  ScaleType = 0
  ScrubCount = 0
  SeamHidden = false
  SeamVisible = false
  SmoothHidden = false
  SmoothVisible = true
  Source = -> [Pocket121]
  X = 217.848
  XDirection = (1,0,0)
  Y = 307.607
FEATURE [TechDraw::DrawViewPart] View007
  CoarseView = false
  Direction = (0,0,1)
  Focus = 100
  HardHidden = false
  IsoCount = 0
  IsoHidden = false
  IsoVisible = false
  LockPosition = false
  Perspective = false
  Rotation = 0
  ScaleType = 0
  ScrubCount = 0
  SeamHidden = false
  SeamVisible = false
  SmoothHidden = false
  SmoothVisible = true
  Source = -> [Fillet068]
  X = 627.06
  XDirection = (1,0,0)
  Y = 309.282
FEATURE [TechDraw::DrawPage] Page003
  KeepUpdated = true
  NextBalloonIndex = 1
  ProjectionType = 0
  Template = -> Template003
  Views = -> [View006,View007]
FEATURE [TechDraw::DrawSVGTemplate] Template004
  Height = 594
  Orientation = 1
  Template = C:/Program Files/FreeCAD 0.21/data/Mod/TechDraw/Templates/A1_Landscape_blank.svg
  Width = 841
FEATURE [TechDraw::DrawViewPart] View008
  CoarseView = false
  Direction = (0,0,1)
  Focus = 100
  HardHidden = false
  IsoCount = 0
  IsoHidden = false
  IsoVisible = false
  LockPosition = false
  Perspective = false
  Rotation = 0
  ScaleType = 0
  ScrubCount = 0
  SeamHidden = false
  SeamVisible = false
  SmoothHidden = false
  SmoothVisible = true
  Source = -> [Fillet069]
  X = 221.197
  XDirection = (1,0,0)
  Y = 300.908
FEATURE [TechDraw::DrawViewPart] View009
  CoarseView = false
  Direction = (0,-1,0)
  Focus = 100
  HardHidden = false
  IsoCount = 0
  IsoHidden = false
  IsoVisible = false
  LockPosition = false
  Perspective = false
  Rotation = 0
  ScaleType = 0
  ScrubCount = 0
  SeamHidden = false
  SeamVisible = false
  SmoothHidden = false
  SmoothVisible = true
  Source = -> [Fillet070]
  X = 567.325
  XDirection = (1,0,0)
  Y = 507.468
FEATURE [TechDraw::DrawViewPart] View010
  CoarseView = false
  Direction = (0,-1,0)
  Focus = 100
  HardHidden = false
  IsoCount = 0
  IsoHidden = false
  IsoVisible = false
  LockPosition = false
  Perspective = false
  Rotation = 0
  ScaleType = 0
  ScrubCount = 0
  SeamHidden = false
  SeamVisible = false
  SmoothHidden = false
  SmoothVisible = true
  Source = -> [Fillet071]
  X = 567.325
  XDirection = (1,0,0)
  Y = 436.568
FEATURE [TechDraw::DrawPage] Page004
  KeepUpdated = true
  NextBalloonIndex = 1
  ProjectionType = 0
  Template = -> Template004
  Views = -> [View008,View009,View010]
FEATURE [PartDesign::Pocket] Pocket134
  Direction = (0.51693,0.856028,-2e-16)
  Length = 5
  Length2 = 5
  Profile = -> Sketch192
  ReferenceAxis = -> Sketch192 [N_Axis]
  Type = 0
FEATURE [App::Part] Part055
  Group = -> [BaseFeature018,Compound,Pocket034,Sketch157,Pocket061,Sketch192,Pocket133,Fillet019,Pocket134]
  Origin = -> Origin230
note: 1 file-system path scrubbed to <path> (originals preserved in the JSON sidecar)
